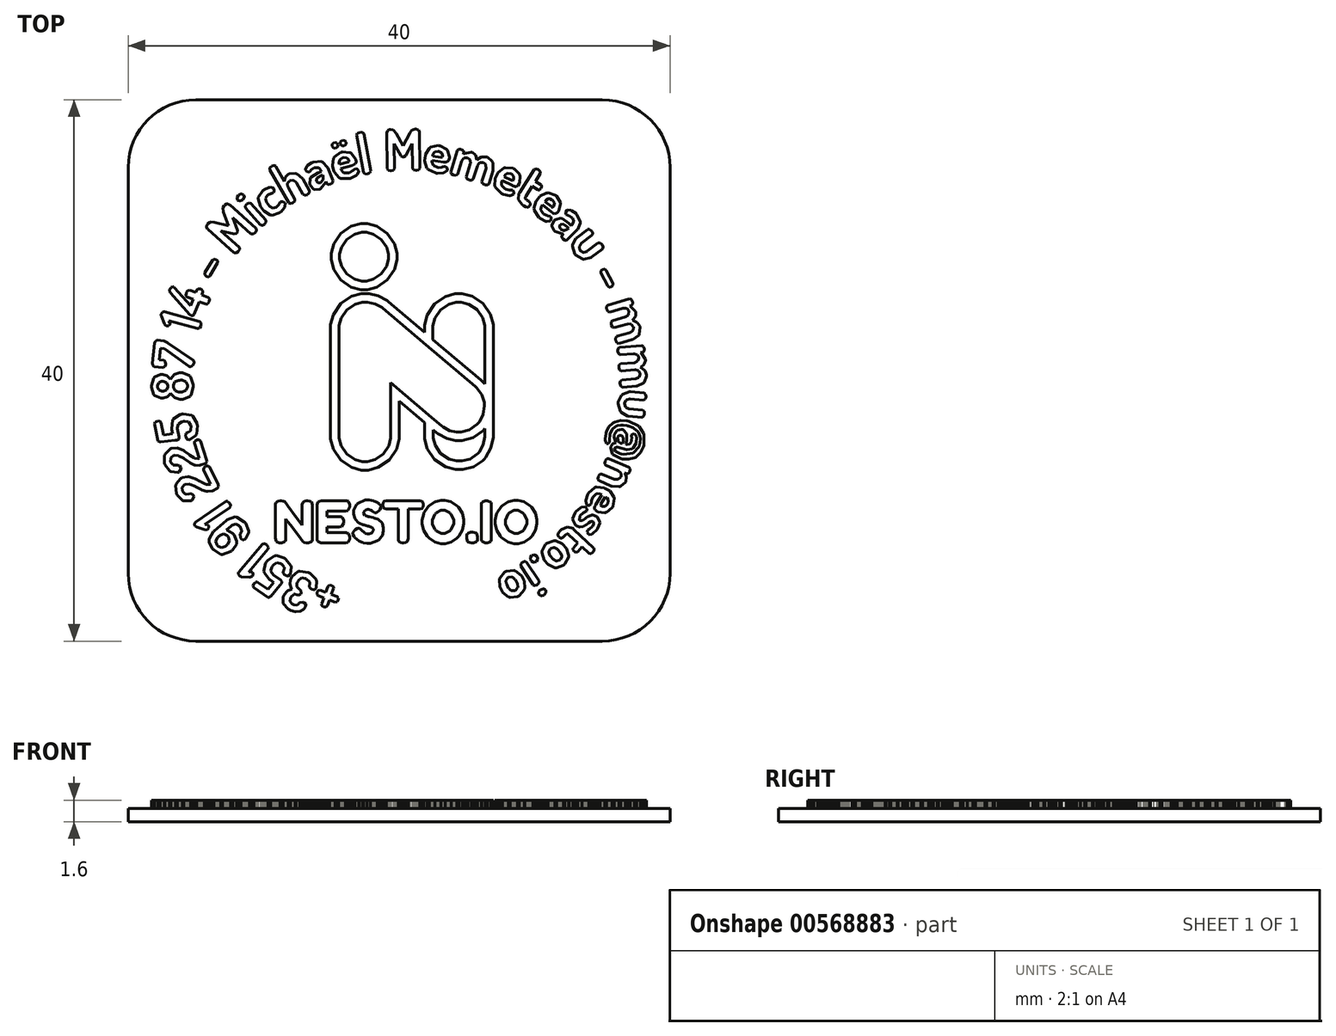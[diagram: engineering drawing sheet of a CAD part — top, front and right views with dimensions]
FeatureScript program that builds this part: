
annotation { "Feature Type Name" : "Feature", "Feature Type Description" : "" }
export const myFeature = defineFeature(function(context is Context, id is Id, definition is map)
    precondition{}
    {
        {
            var Q0;
            Q0=qCreatedBy(makeId("Top.planeOp"),FACE);
            var sketch = newSketch(context, id + "F0", { "sketchPlane" : qUnion([Q0])});
            skLineSegment(sketch, "E0", {"start": v(0.3, -0.3) * mm, "end": v(0.29, -0.31) * mm});
            skLineSegment(sketch, "E1", {"start": v(0.29, -0.31) * mm, "end": v(0.26, -0.33) * mm});
            skLineSegment(sketch, "E2", {"start": v(0.26, -0.33) * mm, "end": v(0.23, -0.33) * mm});
            skLineSegment(sketch, "E3", {"start": v(0.23, -0.33) * mm, "end": v(0.23, -0.33) * mm});
            skLineSegment(sketch, "E4", {"start": v(0.23, -0.33) * mm, "end": v(0.22, -0.33) * mm});
            skLineSegment(sketch, "E5", {"start": v(0.22, -0.33) * mm, "end": v(0.22, -0.33) * mm});
            skLineSegment(sketch, "E6", {"start": v(0.22, -0.33) * mm, "end": v(0.21, -0.33) * mm});
            skLineSegment(sketch, "E7", {"start": v(0.21, -0.33) * mm, "end": v(0.18, -0.33) * mm});
            skLineSegment(sketch, "E8", {"start": v(0.18, -0.33) * mm, "end": v(0.15, -0.3) * mm});
            skLineSegment(sketch, "E9", {"start": v(0.15, -0.3) * mm, "end": v(0.13, -0.28) * mm});
            skLineSegment(sketch, "E10", {"start": v(0.13, -0.28) * mm, "end": v(0.13, -0.25) * mm});
            skLineSegment(sketch, "E11", {"start": v(0.13, -0.25) * mm, "end": v(0.12, -0.24) * mm});
            skLineSegment(sketch, "E12", {"start": v(0.12, -0.24) * mm, "end": v(0.12, -0.22) * mm});
            skLineSegment(sketch, "E13", {"start": v(0.12, -0.22) * mm, "end": v(0.14, -0.23) * mm});
            skLineSegment(sketch, "E14", {"start": v(0.14, -0.23) * mm, "end": v(0.14, -0.23) * mm});
            skLineSegment(sketch, "E15", {"start": v(0.14, -0.23) * mm, "end": v(0.18, -0.25) * mm});
            skLineSegment(sketch, "E16", {"start": v(0.18, -0.25) * mm, "end": v(0.2, -0.26) * mm});
            skLineSegment(sketch, "E17", {"start": v(0.2, -0.26) * mm, "end": v(0.22, -0.26) * mm});
            skLineSegment(sketch, "E18", {"start": v(0.22, -0.26) * mm, "end": v(0.23, -0.26) * mm});
            skLineSegment(sketch, "E19", {"start": v(0.23, -0.26) * mm, "end": v(0.27, -0.25) * mm});
            skLineSegment(sketch, "E20", {"start": v(0.27, -0.25) * mm, "end": v(0.3, -0.22) * mm});
            skLineSegment(sketch, "E21", {"start": v(0.3, -0.22) * mm, "end": v(0.32, -0.22) * mm});
            skLineSegment(sketch, "E22", {"start": v(0.32, -0.22) * mm, "end": v(0.32, -0.24) * mm});
            skLineSegment(sketch, "E23", {"start": v(0.32, -0.24) * mm, "end": v(0.32, -0.24) * mm});
            skLineSegment(sketch, "E24", {"start": v(0.32, -0.24) * mm, "end": v(0.3, -0.28) * mm});
            skLineSegment(sketch, "E25", {"start": v(0.3, -0.28) * mm, "end": v(0.3, -0.3) * mm});
            skLineSegment(sketch, "E26", {"start": v(0.3, -0.3) * mm, "end": v(0.3, -0.3) * mm});
            skLineSegment(sketch, "E27", {"start": v(-0.03, -0.05) * mm, "end": v(-0.03, -0.24) * mm});
            skLineSegment(sketch, "E28", {"start": v(-0.03, -0.24) * mm, "end": v(-0.03, -0.25) * mm});
            skLineSegment(sketch, "E29", {"start": v(-0.03, -0.25) * mm, "end": v(-0.04, -0.28) * mm});
            skLineSegment(sketch, "E30", {"start": v(-0.04, -0.28) * mm, "end": v(-0.06, -0.3) * mm});
            skLineSegment(sketch, "E31", {"start": v(-0.06, -0.3) * mm, "end": v(-0.09, -0.33) * mm});
            skLineSegment(sketch, "E32", {"start": v(-0.09, -0.33) * mm, "end": v(-0.12, -0.34) * mm});
            skLineSegment(sketch, "E33", {"start": v(-0.12, -0.34) * mm, "end": v(-0.13, -0.34) * mm});
            skLineSegment(sketch, "E34", {"start": v(-0.13, -0.34) * mm, "end": v(-0.14, -0.34) * mm});
            skLineSegment(sketch, "E35", {"start": v(-0.14, -0.34) * mm, "end": v(-0.16, -0.33) * mm});
            skLineSegment(sketch, "E36", {"start": v(-0.16, -0.33) * mm, "end": v(-0.2, -0.3) * mm});
            skLineSegment(sketch, "E37", {"start": v(-0.2, -0.3) * mm, "end": v(-0.21, -0.28) * mm});
            skLineSegment(sketch, "E38", {"start": v(-0.21, -0.28) * mm, "end": v(-0.22, -0.25) * mm});
            skLineSegment(sketch, "E39", {"start": v(-0.22, -0.25) * mm, "end": v(-0.22, -0.24) * mm});
            skLineSegment(sketch, "E40", {"start": v(-0.22, -0.24) * mm, "end": v(-0.22, 0.16) * mm});
            skLineSegment(sketch, "E41", {"start": v(-0.22, 0.16) * mm, "end": v(-0.22, 0.17) * mm});
            skLineSegment(sketch, "E42", {"start": v(-0.22, 0.17) * mm, "end": v(-0.21, 0.2) * mm});
            skLineSegment(sketch, "E43", {"start": v(-0.21, 0.2) * mm, "end": v(-0.2, 0.22) * mm});
            skLineSegment(sketch, "E44", {"start": v(-0.2, 0.22) * mm, "end": v(-0.16, 0.24) * mm});
            skLineSegment(sketch, "E45", {"start": v(-0.16, 0.24) * mm, "end": v(-0.14, 0.25) * mm});
            skLineSegment(sketch, "E46", {"start": v(-0.14, 0.25) * mm, "end": v(-0.13, 0.25) * mm});
            skLineSegment(sketch, "E47", {"start": v(-0.13, 0.25) * mm, "end": v(-0.13, 0.25) * mm});
            skLineSegment(sketch, "E48", {"start": v(-0.13, 0.25) * mm, "end": v(-0.12, 0.25) * mm});
            skLineSegment(sketch, "E49", {"start": v(-0.12, 0.25) * mm, "end": v(-0.12, 0.25) * mm});
            skLineSegment(sketch, "E50", {"start": v(-0.12, 0.25) * mm, "end": v(-0.09, 0.25) * mm});
            skLineSegment(sketch, "E51", {"start": v(-0.09, 0.25) * mm, "end": v(-0.06, 0.23) * mm});
            skLineSegment(sketch, "E52", {"start": v(-0.06, 0.23) * mm, "end": v(-0.06, 0.23) * mm});
            skLineSegment(sketch, "E53", {"start": v(-0.06, 0.23) * mm, "end": v(0.1, 0.1) * mm});
            skLineSegment(sketch, "E54", {"start": v(0.1, 0.1) * mm, "end": v(0.1, 0.1) * mm});
            skLineSegment(sketch, "E55", {"start": v(0.1, 0.1) * mm, "end": v(0.28, -0.06) * mm});
            skLineSegment(sketch, "E56", {"start": v(0.28, -0.06) * mm, "end": v(0.29, -0.06) * mm});
            skLineSegment(sketch, "E57", {"start": v(0.29, -0.06) * mm, "end": v(0.3, -0.09) * mm});
            skLineSegment(sketch, "E58", {"start": v(0.3, -0.09) * mm, "end": v(0.31, -0.12) * mm});
            skLineSegment(sketch, "E59", {"start": v(0.31, -0.12) * mm, "end": v(0.31, -0.12) * mm});
            skLineSegment(sketch, "E60", {"start": v(0.31, -0.12) * mm, "end": v(0.32, -0.13) * mm});
            skLineSegment(sketch, "E61", {"start": v(0.32, -0.13) * mm, "end": v(0.31, -0.16) * mm});
            skLineSegment(sketch, "E62", {"start": v(0.31, -0.16) * mm, "end": v(0.3, -0.19) * mm});
            skLineSegment(sketch, "E63", {"start": v(0.3, -0.19) * mm, "end": v(0.3, -0.2) * mm});
            skLineSegment(sketch, "E64", {"start": v(0.3, -0.2) * mm, "end": v(0.29, -0.2) * mm});
            skLineSegment(sketch, "E65", {"start": v(0.29, -0.2) * mm, "end": v(0.26, -0.22) * mm});
            skLineSegment(sketch, "E66", {"start": v(0.26, -0.22) * mm, "end": v(0.23, -0.23) * mm});
            skLineSegment(sketch, "E67", {"start": v(0.23, -0.23) * mm, "end": v(0.22, -0.23) * mm});
            skLineSegment(sketch, "E68", {"start": v(0.22, -0.23) * mm, "end": v(0.21, -0.23) * mm});
            skLineSegment(sketch, "E69", {"start": v(0.21, -0.23) * mm, "end": v(0.19, -0.22) * mm});
            skLineSegment(sketch, "E70", {"start": v(0.19, -0.22) * mm, "end": v(0.16, -0.2) * mm});
            skLineSegment(sketch, "E71", {"start": v(0.16, -0.2) * mm, "end": v(0.16, -0.2) * mm});
            skLineSegment(sketch, "E72", {"start": v(0.16, -0.2) * mm, "end": v(0.12, -0.17) * mm});
            skLineSegment(sketch, "E73", {"start": v(0.12, -0.17) * mm, "end": v(-0.03, -0.05) * mm});
            skLineSegment(sketch, "E74", {"start": v(0.22, 0.25) * mm, "end": v(0.22, 0.25) * mm});
            skLineSegment(sketch, "E75", {"start": v(0.22, 0.25) * mm, "end": v(0.23, 0.25) * mm});
            skLineSegment(sketch, "E76", {"start": v(0.23, 0.25) * mm, "end": v(0.26, 0.24) * mm});
            skLineSegment(sketch, "E77", {"start": v(0.26, 0.24) * mm, "end": v(0.29, 0.22) * mm});
            skLineSegment(sketch, "E78", {"start": v(0.29, 0.22) * mm, "end": v(0.3, 0.2) * mm});
            skLineSegment(sketch, "E79", {"start": v(0.3, 0.2) * mm, "end": v(0.32, 0.17) * mm});
            skLineSegment(sketch, "E80", {"start": v(0.32, 0.17) * mm, "end": v(0.32, 0.16) * mm});
            skLineSegment(sketch, "E81", {"start": v(0.32, 0.16) * mm, "end": v(0.32, -0.05) * mm});
            skLineSegment(sketch, "E82", {"start": v(0.32, -0.05) * mm, "end": v(0.31, -0.05) * mm});
            skLineSegment(sketch, "E83", {"start": v(0.31, -0.05) * mm, "end": v(0.3, -0.04) * mm});
            skLineSegment(sketch, "E84", {"start": v(0.3, -0.04) * mm, "end": v(0.3, -0.04) * mm});
            skLineSegment(sketch, "E85", {"start": v(0.3, -0.04) * mm, "end": v(0.12, 0.11) * mm});
            skLineSegment(sketch, "E86", {"start": v(0.12, 0.11) * mm, "end": v(0.12, 0.16) * mm});
            skLineSegment(sketch, "E87", {"start": v(0.12, 0.16) * mm, "end": v(0.12, 0.16) * mm});
            skLineSegment(sketch, "E88", {"start": v(0.12, 0.16) * mm, "end": v(0.13, 0.2) * mm});
            skLineSegment(sketch, "E89", {"start": v(0.13, 0.2) * mm, "end": v(0.15, 0.22) * mm});
            skLineSegment(sketch, "E90", {"start": v(0.15, 0.22) * mm, "end": v(0.18, 0.24) * mm});
            skLineSegment(sketch, "E91", {"start": v(0.18, 0.24) * mm, "end": v(0.21, 0.25) * mm});
            skLineSegment(sketch, "E92", {"start": v(0.21, 0.25) * mm, "end": v(0.22, 0.25) * mm});
            skLineSegment(sketch, "E93", {"start": v(0.35, 0.16) * mm, "end": v(0.35, 0.17) * mm});
            skLineSegment(sketch, "E94", {"start": v(0.35, 0.17) * mm, "end": v(0.34, 0.2) * mm});
            skLineSegment(sketch, "E95", {"start": v(0.34, 0.2) * mm, "end": v(0.3, 0.25) * mm});
            skLineSegment(sketch, "E96", {"start": v(0.3, 0.25) * mm, "end": v(0.27, 0.27) * mm});
            skLineSegment(sketch, "E97", {"start": v(0.27, 0.27) * mm, "end": v(0.23, 0.28) * mm});
            skLineSegment(sketch, "E98", {"start": v(0.23, 0.28) * mm, "end": v(0.22, 0.28) * mm});
            skLineSegment(sketch, "E99", {"start": v(0.22, 0.28) * mm, "end": v(0.22, 0.28) * mm});
            skLineSegment(sketch, "E100", {"start": v(0.22, 0.28) * mm, "end": v(0.2, 0.28) * mm});
            skLineSegment(sketch, "E101", {"start": v(0.2, 0.28) * mm, "end": v(0.17, 0.27) * mm});
            skLineSegment(sketch, "E102", {"start": v(0.17, 0.27) * mm, "end": v(0.13, 0.25) * mm});
            skLineSegment(sketch, "E103", {"start": v(0.13, 0.25) * mm, "end": v(0.1, 0.2) * mm});
            skLineSegment(sketch, "E104", {"start": v(0.1, 0.2) * mm, "end": v(0.1, 0.17) * mm});
            skLineSegment(sketch, "E105", {"start": v(0.1, 0.17) * mm, "end": v(0.1, 0.16) * mm});
            skLineSegment(sketch, "E106", {"start": v(0.1, 0.16) * mm, "end": v(0.1, 0.14) * mm});
            skLineSegment(sketch, "E107", {"start": v(0.1, 0.14) * mm, "end": v(-0.04, 0.25) * mm});
            skLineSegment(sketch, "E108", {"start": v(-0.04, 0.25) * mm, "end": v(-0.05, 0.26) * mm});
            skLineSegment(sketch, "E109", {"start": v(-0.05, 0.26) * mm, "end": v(-0.08, 0.28) * mm});
            skLineSegment(sketch, "E110", {"start": v(-0.08, 0.28) * mm, "end": v(-0.11, 0.28) * mm});
            skLineSegment(sketch, "E111", {"start": v(-0.11, 0.28) * mm, "end": v(-0.12, 0.28) * mm});
            skLineSegment(sketch, "E112", {"start": v(-0.12, 0.28) * mm, "end": v(-0.12, 0.28) * mm});
            skLineSegment(sketch, "E113", {"start": v(-0.12, 0.28) * mm, "end": v(-0.13, 0.28) * mm});
            skLineSegment(sketch, "E114", {"start": v(-0.13, 0.28) * mm, "end": v(-0.13, 0.28) * mm});
            skLineSegment(sketch, "E115", {"start": v(-0.13, 0.28) * mm, "end": v(-0.14, 0.28) * mm});
            skLineSegment(sketch, "E116", {"start": v(-0.14, 0.28) * mm, "end": v(-0.18, 0.27) * mm});
            skLineSegment(sketch, "E117", {"start": v(-0.18, 0.27) * mm, "end": v(-0.22, 0.25) * mm});
            skLineSegment(sketch, "E118", {"start": v(-0.22, 0.25) * mm, "end": v(-0.24, 0.2) * mm});
            skLineSegment(sketch, "E119", {"start": v(-0.24, 0.2) * mm, "end": v(-0.25, 0.17) * mm});
            skLineSegment(sketch, "E120", {"start": v(-0.25, 0.17) * mm, "end": v(-0.25, 0.16) * mm});
            skLineSegment(sketch, "E121", {"start": v(-0.25, 0.16) * mm, "end": v(-0.25, -0.24) * mm});
            skLineSegment(sketch, "E122", {"start": v(-0.25, -0.24) * mm, "end": v(-0.25, -0.25) * mm});
            skLineSegment(sketch, "E123", {"start": v(-0.25, -0.25) * mm, "end": v(-0.24, -0.3) * mm});
            skLineSegment(sketch, "E124", {"start": v(-0.24, -0.3) * mm, "end": v(-0.22, -0.33) * mm});
            skLineSegment(sketch, "E125", {"start": v(-0.22, -0.33) * mm, "end": v(-0.18, -0.36) * mm});
            skLineSegment(sketch, "E126", {"start": v(-0.18, -0.36) * mm, "end": v(-0.14, -0.37) * mm});
            skLineSegment(sketch, "E127", {"start": v(-0.14, -0.37) * mm, "end": v(-0.13, -0.37) * mm});
            skLineSegment(sketch, "E128", {"start": v(-0.13, -0.37) * mm, "end": v(-0.11, -0.37) * mm});
            skLineSegment(sketch, "E129", {"start": v(-0.11, -0.37) * mm, "end": v(-0.08, -0.36) * mm});
            skLineSegment(sketch, "E130", {"start": v(-0.08, -0.36) * mm, "end": v(-0.04, -0.33) * mm});
            skLineSegment(sketch, "E131", {"start": v(-0.04, -0.33) * mm, "end": v(0, -0.3) * mm});
            skLineSegment(sketch, "E132", {"start": v(0, -0.3) * mm, "end": v(0, -0.25) * mm});
            skLineSegment(sketch, "E133", {"start": v(0, -0.25) * mm, "end": v(0, -0.24) * mm});
            skLineSegment(sketch, "E134", {"start": v(0, -0.24) * mm, "end": v(0, -0.11) * mm});
            skLineSegment(sketch, "E135", {"start": v(0, -0.11) * mm, "end": v(0.1, -0.2) * mm});
            skLineSegment(sketch, "E136", {"start": v(0.1, -0.2) * mm, "end": v(0.1, -0.24) * mm});
            skLineSegment(sketch, "E137", {"start": v(0.1, -0.24) * mm, "end": v(0.1, -0.25) * mm});
            skLineSegment(sketch, "E138", {"start": v(0.1, -0.25) * mm, "end": v(0.1, -0.29) * mm});
            skLineSegment(sketch, "E139", {"start": v(0.1, -0.29) * mm, "end": v(0.13, -0.33) * mm});
            skLineSegment(sketch, "E140", {"start": v(0.13, -0.33) * mm, "end": v(0.17, -0.36) * mm});
            skLineSegment(sketch, "E141", {"start": v(0.17, -0.36) * mm, "end": v(0.2, -0.37) * mm});
            skLineSegment(sketch, "E142", {"start": v(0.2, -0.37) * mm, "end": v(0.22, -0.37) * mm});
            skLineSegment(sketch, "E143", {"start": v(0.22, -0.37) * mm, "end": v(0.23, -0.37) * mm});
            skLineSegment(sketch, "E144", {"start": v(0.23, -0.37) * mm, "end": v(0.23, -0.37) * mm});
            skLineSegment(sketch, "E145", {"start": v(0.23, -0.37) * mm, "end": v(0.27, -0.36) * mm});
            skLineSegment(sketch, "E146", {"start": v(0.27, -0.36) * mm, "end": v(0.3, -0.33) * mm});
            skLineSegment(sketch, "E147", {"start": v(0.3, -0.33) * mm, "end": v(0.31, -0.33) * mm});
            skLineSegment(sketch, "E148", {"start": v(0.31, -0.33) * mm, "end": v(0.32, -0.32) * mm});
            skLineSegment(sketch, "E149", {"start": v(0.32, -0.32) * mm, "end": v(0.34, -0.29) * mm});
            skLineSegment(sketch, "E150", {"start": v(0.34, -0.29) * mm, "end": v(0.35, -0.25) * mm});
            skLineSegment(sketch, "E151", {"start": v(0.35, -0.25) * mm, "end": v(0.35, -0.24) * mm});
            skLineSegment(sketch, "E152", {"start": v(0.35, -0.24) * mm, "end": v(0.35, 0.16) * mm});
            skLineSegment(sketch, "E153", {"start": v(-0.13, 0.51) * mm, "end": v(-0.12, 0.51) * mm});
            skLineSegment(sketch, "E154", {"start": v(-0.12, 0.51) * mm, "end": v(-0.1, 0.5) * mm});
            skLineSegment(sketch, "E155", {"start": v(-0.1, 0.5) * mm, "end": v(-0.07, 0.48) * mm});
            skLineSegment(sketch, "E156", {"start": v(-0.07, 0.48) * mm, "end": v(-0.05, 0.46) * mm});
            skLineSegment(sketch, "E157", {"start": v(-0.05, 0.46) * mm, "end": v(-0.04, 0.43) * mm});
            skLineSegment(sketch, "E158", {"start": v(-0.04, 0.43) * mm, "end": v(-0.04, 0.42) * mm});
            skLineSegment(sketch, "E159", {"start": v(-0.04, 0.42) * mm, "end": v(-0.04, 0.41) * mm});
            skLineSegment(sketch, "E160", {"start": v(-0.04, 0.41) * mm, "end": v(-0.05, 0.39) * mm});
            skLineSegment(sketch, "E161", {"start": v(-0.05, 0.39) * mm, "end": v(-0.07, 0.36) * mm});
            skLineSegment(sketch, "E162", {"start": v(-0.07, 0.36) * mm, "end": v(-0.1, 0.34) * mm});
            skLineSegment(sketch, "E163", {"start": v(-0.1, 0.34) * mm, "end": v(-0.12, 0.33) * mm});
            skLineSegment(sketch, "E164", {"start": v(-0.12, 0.33) * mm, "end": v(-0.13, 0.33) * mm});
            skLineSegment(sketch, "E165", {"start": v(-0.13, 0.33) * mm, "end": v(-0.14, 0.33) * mm});
            skLineSegment(sketch, "E166", {"start": v(-0.14, 0.33) * mm, "end": v(-0.16, 0.34) * mm});
            skLineSegment(sketch, "E167", {"start": v(-0.16, 0.34) * mm, "end": v(-0.2, 0.36) * mm});
            skLineSegment(sketch, "E168", {"start": v(-0.2, 0.36) * mm, "end": v(-0.21, 0.39) * mm});
            skLineSegment(sketch, "E169", {"start": v(-0.21, 0.39) * mm, "end": v(-0.22, 0.41) * mm});
            skLineSegment(sketch, "E170", {"start": v(-0.22, 0.41) * mm, "end": v(-0.22, 0.42) * mm});
            skLineSegment(sketch, "E171", {"start": v(-0.22, 0.42) * mm, "end": v(-0.22, 0.43) * mm});
            skLineSegment(sketch, "E172", {"start": v(-0.22, 0.43) * mm, "end": v(-0.21, 0.46) * mm});
            skLineSegment(sketch, "E173", {"start": v(-0.21, 0.46) * mm, "end": v(-0.2, 0.48) * mm});
            skLineSegment(sketch, "E174", {"start": v(-0.2, 0.48) * mm, "end": v(-0.16, 0.5) * mm});
            skLineSegment(sketch, "E175", {"start": v(-0.16, 0.5) * mm, "end": v(-0.14, 0.51) * mm});
            skLineSegment(sketch, "E176", {"start": v(-0.14, 0.51) * mm, "end": v(-0.13, 0.51) * mm});
            skLineSegment(sketch, "E177", {"start": v(-0.13, 0.3) * mm, "end": v(-0.12, 0.3) * mm});
            skLineSegment(sketch, "E178", {"start": v(-0.12, 0.3) * mm, "end": v(-0.08, 0.3) * mm});
            skLineSegment(sketch, "E179", {"start": v(-0.08, 0.3) * mm, "end": v(-0.04, 0.33) * mm});
            skLineSegment(sketch, "E180", {"start": v(-0.04, 0.33) * mm, "end": v(-0.02, 0.37) * mm});
            skLineSegment(sketch, "E181", {"start": v(-0.02, 0.37) * mm, "end": v(0, 0.4) * mm});
            skLineSegment(sketch, "E182", {"start": v(0, 0.4) * mm, "end": v(0, 0.42) * mm});
            skLineSegment(sketch, "E183", {"start": v(0, 0.42) * mm, "end": v(0, 0.43) * mm});
            skLineSegment(sketch, "E184", {"start": v(0, 0.43) * mm, "end": v(-0.02, 0.47) * mm});
            skLineSegment(sketch, "E185", {"start": v(-0.02, 0.47) * mm, "end": v(-0.04, 0.5) * mm});
            skLineSegment(sketch, "E186", {"start": v(-0.04, 0.5) * mm, "end": v(-0.08, 0.53) * mm});
            skLineSegment(sketch, "E187", {"start": v(-0.08, 0.53) * mm, "end": v(-0.12, 0.54) * mm});
            skLineSegment(sketch, "E188", {"start": v(-0.12, 0.54) * mm, "end": v(-0.13, 0.54) * mm});
            skLineSegment(sketch, "E189", {"start": v(-0.13, 0.54) * mm, "end": v(-0.14, 0.54) * mm});
            skLineSegment(sketch, "E190", {"start": v(-0.14, 0.54) * mm, "end": v(-0.18, 0.53) * mm});
            skLineSegment(sketch, "E191", {"start": v(-0.18, 0.53) * mm, "end": v(-0.22, 0.5) * mm});
            skLineSegment(sketch, "E192", {"start": v(-0.22, 0.5) * mm, "end": v(-0.24, 0.47) * mm});
            skLineSegment(sketch, "E193", {"start": v(-0.24, 0.47) * mm, "end": v(-0.25, 0.43) * mm});
            skLineSegment(sketch, "E194", {"start": v(-0.25, 0.43) * mm, "end": v(-0.25, 0.42) * mm});
            skLineSegment(sketch, "E195", {"start": v(-0.25, 0.42) * mm, "end": v(-0.25, 0.4) * mm});
            skLineSegment(sketch, "E196", {"start": v(-0.25, 0.4) * mm, "end": v(-0.24, 0.37) * mm});
            skLineSegment(sketch, "E197", {"start": v(-0.24, 0.37) * mm, "end": v(-0.22, 0.33) * mm});
            skLineSegment(sketch, "E198", {"start": v(-0.22, 0.33) * mm, "end": v(-0.18, 0.3) * mm});
            skLineSegment(sketch, "E199", {"start": v(-0.18, 0.3) * mm, "end": v(-0.14, 0.3) * mm});
            skLineSegment(sketch, "E200", {"start": v(-0.14, 0.3) * mm, "end": v(-0.13, 0.3) * mm});
            skLineSegment(sketch, "E201", {"start": v(-0.36, -0.49) * mm, "end": v(-0.36, -0.49) * mm});
            skLineSegment(sketch, "E202", {"start": v(-0.36, -0.49) * mm, "end": v(-0.35, -0.48) * mm});
            skLineSegment(sketch, "E203", {"start": v(-0.35, -0.48) * mm, "end": v(-0.35, -0.48) * mm});
            skLineSegment(sketch, "E204", {"start": v(-0.35, -0.48) * mm, "end": v(-0.34, -0.48) * mm});
            skLineSegment(sketch, "E205", {"start": v(-0.34, -0.48) * mm, "end": v(-0.34, -0.48) * mm});
            skLineSegment(sketch, "E206", {"start": v(-0.34, -0.48) * mm, "end": v(-0.33, -0.48) * mm});
            skLineSegment(sketch, "E207", {"start": v(-0.33, -0.48) * mm, "end": v(-0.33, -0.48) * mm});
            skLineSegment(sketch, "E208", {"start": v(-0.33, -0.48) * mm, "end": v(-0.32, -0.48) * mm});
            skLineSegment(sketch, "E209", {"start": v(-0.32, -0.48) * mm, "end": v(-0.32, -0.49) * mm});
            skLineSegment(sketch, "E210", {"start": v(-0.32, -0.49) * mm, "end": v(-0.32, -0.49) * mm});
            skLineSegment(sketch, "E211", {"start": v(-0.32, -0.49) * mm, "end": v(-0.32, -0.5) * mm});
            skLineSegment(sketch, "E212", {"start": v(-0.32, -0.5) * mm, "end": v(-0.32, -0.5) * mm});
            skLineSegment(sketch, "E213", {"start": v(-0.32, -0.5) * mm, "end": v(-0.32, -0.62) * mm});
            skLineSegment(sketch, "E214", {"start": v(-0.32, -0.62) * mm, "end": v(-0.32, -0.62) * mm});
            skLineSegment(sketch, "E215", {"start": v(-0.32, -0.62) * mm, "end": v(-0.32, -0.63) * mm});
            skLineSegment(sketch, "E216", {"start": v(-0.32, -0.63) * mm, "end": v(-0.32, -0.63) * mm});
            skLineSegment(sketch, "E217", {"start": v(-0.32, -0.63) * mm, "end": v(-0.34, -0.64) * mm});
            skLineSegment(sketch, "E218", {"start": v(-0.34, -0.64) * mm, "end": v(-0.34, -0.64) * mm});
            skLineSegment(sketch, "E219", {"start": v(-0.34, -0.64) * mm, "end": v(-0.35, -0.64) * mm});
            skLineSegment(sketch, "E220", {"start": v(-0.35, -0.64) * mm, "end": v(-0.35, -0.64) * mm});
            skLineSegment(sketch, "E221", {"start": v(-0.35, -0.64) * mm, "end": v(-0.36, -0.63) * mm});
            skLineSegment(sketch, "E222", {"start": v(-0.36, -0.63) * mm, "end": v(-0.36, -0.63) * mm});
            skLineSegment(sketch, "E223", {"start": v(-0.36, -0.63) * mm, "end": v(-0.36, -0.62) * mm});
            skLineSegment(sketch, "E224", {"start": v(-0.36, -0.62) * mm, "end": v(-0.4, -0.58) * mm});
            skLineSegment(sketch, "E225", {"start": v(-0.4, -0.58) * mm, "end": v(-0.42, -0.55) * mm});
            skLineSegment(sketch, "E226", {"start": v(-0.42, -0.55) * mm, "end": v(-0.42, -0.55) * mm});
            skLineSegment(sketch, "E227", {"start": v(-0.42, -0.55) * mm, "end": v(-0.42, -0.62) * mm});
            skLineSegment(sketch, "E228", {"start": v(-0.42, -0.62) * mm, "end": v(-0.42, -0.62) * mm});
            skLineSegment(sketch, "E229", {"start": v(-0.42, -0.62) * mm, "end": v(-0.42, -0.63) * mm});
            skLineSegment(sketch, "E230", {"start": v(-0.42, -0.63) * mm, "end": v(-0.42, -0.63) * mm});
            skLineSegment(sketch, "E231", {"start": v(-0.42, -0.63) * mm, "end": v(-0.43, -0.64) * mm});
            skLineSegment(sketch, "E232", {"start": v(-0.43, -0.64) * mm, "end": v(-0.44, -0.64) * mm});
            skLineSegment(sketch, "E233", {"start": v(-0.44, -0.64) * mm, "end": v(-0.44, -0.64) * mm});
            skLineSegment(sketch, "E234", {"start": v(-0.44, -0.64) * mm, "end": v(-0.45, -0.63) * mm});
            skLineSegment(sketch, "E235", {"start": v(-0.45, -0.63) * mm, "end": v(-0.45, -0.63) * mm});
            skLineSegment(sketch, "E236", {"start": v(-0.45, -0.63) * mm, "end": v(-0.46, -0.63) * mm});
            skLineSegment(sketch, "E237", {"start": v(-0.46, -0.63) * mm, "end": v(-0.46, -0.63) * mm});
            skLineSegment(sketch, "E238", {"start": v(-0.46, -0.63) * mm, "end": v(-0.46, -0.62) * mm});
            skLineSegment(sketch, "E239", {"start": v(-0.46, -0.62) * mm, "end": v(-0.46, -0.62) * mm});
            skLineSegment(sketch, "E240", {"start": v(-0.46, -0.62) * mm, "end": v(-0.46, -0.5) * mm});
            skLineSegment(sketch, "E241", {"start": v(-0.46, -0.5) * mm, "end": v(-0.46, -0.5) * mm});
            skLineSegment(sketch, "E242", {"start": v(-0.46, -0.5) * mm, "end": v(-0.45, -0.49) * mm});
            skLineSegment(sketch, "E243", {"start": v(-0.45, -0.49) * mm, "end": v(-0.45, -0.49) * mm});
            skLineSegment(sketch, "E244", {"start": v(-0.45, -0.49) * mm, "end": v(-0.45, -0.48) * mm});
            skLineSegment(sketch, "E245", {"start": v(-0.45, -0.48) * mm, "end": v(-0.45, -0.48) * mm});
            skLineSegment(sketch, "E246", {"start": v(-0.45, -0.48) * mm, "end": v(-0.44, -0.48) * mm});
            skLineSegment(sketch, "E247", {"start": v(-0.44, -0.48) * mm, "end": v(-0.44, -0.48) * mm});
            skLineSegment(sketch, "E248", {"start": v(-0.44, -0.48) * mm, "end": v(-0.43, -0.48) * mm});
            skLineSegment(sketch, "E249", {"start": v(-0.43, -0.48) * mm, "end": v(-0.43, -0.48) * mm});
            skLineSegment(sketch, "E250", {"start": v(-0.43, -0.48) * mm, "end": v(-0.42, -0.48) * mm});
            skLineSegment(sketch, "E251", {"start": v(-0.42, -0.48) * mm, "end": v(-0.42, -0.49) * mm});
            skLineSegment(sketch, "E252", {"start": v(-0.42, -0.49) * mm, "end": v(-0.42, -0.49) * mm});
            skLineSegment(sketch, "E253", {"start": v(-0.42, -0.49) * mm, "end": v(-0.42, -0.5) * mm});
            skLineSegment(sketch, "E254", {"start": v(-0.42, -0.5) * mm, "end": v(-0.41, -0.5) * mm});
            skLineSegment(sketch, "E255", {"start": v(-0.41, -0.5) * mm, "end": v(-0.38, -0.54) * mm});
            skLineSegment(sketch, "E256", {"start": v(-0.38, -0.54) * mm, "end": v(-0.36, -0.57) * mm});
            skLineSegment(sketch, "E257", {"start": v(-0.36, -0.57) * mm, "end": v(-0.36, -0.57) * mm});
            skLineSegment(sketch, "E258", {"start": v(-0.36, -0.57) * mm, "end": v(-0.36, -0.5) * mm});
            skLineSegment(sketch, "E259", {"start": v(-0.36, -0.5) * mm, "end": v(-0.36, -0.5) * mm});
            skLineSegment(sketch, "E260", {"start": v(-0.36, -0.5) * mm, "end": v(-0.36, -0.49) * mm});
            skLineSegment(sketch, "E261", {"start": v(-0.27, -0.6) * mm, "end": v(-0.2, -0.6) * mm});
            skLineSegment(sketch, "E262", {"start": v(-0.2, -0.6) * mm, "end": v(-0.2, -0.6) * mm});
            skLineSegment(sketch, "E263", {"start": v(-0.2, -0.6) * mm, "end": v(-0.19, -0.6) * mm});
            skLineSegment(sketch, "E264", {"start": v(-0.19, -0.6) * mm, "end": v(-0.19, -0.6) * mm});
            skLineSegment(sketch, "E265", {"start": v(-0.19, -0.6) * mm, "end": v(-0.18, -0.61) * mm});
            skLineSegment(sketch, "E266", {"start": v(-0.18, -0.61) * mm, "end": v(-0.18, -0.62) * mm});
            skLineSegment(sketch, "E267", {"start": v(-0.18, -0.62) * mm, "end": v(-0.18, -0.62) * mm});
            skLineSegment(sketch, "E268", {"start": v(-0.18, -0.62) * mm, "end": v(-0.19, -0.64) * mm});
            skLineSegment(sketch, "E269", {"start": v(-0.19, -0.64) * mm, "end": v(-0.19, -0.64) * mm});
            skLineSegment(sketch, "E270", {"start": v(-0.19, -0.64) * mm, "end": v(-0.2, -0.64) * mm});
            skLineSegment(sketch, "E271", {"start": v(-0.2, -0.64) * mm, "end": v(-0.2, -0.64) * mm});
            skLineSegment(sketch, "E272", {"start": v(-0.2, -0.64) * mm, "end": v(-0.28, -0.64) * mm});
            skLineSegment(sketch, "E273", {"start": v(-0.28, -0.64) * mm, "end": v(-0.29, -0.64) * mm});
            skLineSegment(sketch, "E274", {"start": v(-0.29, -0.64) * mm, "end": v(-0.3, -0.63) * mm});
            skLineSegment(sketch, "E275", {"start": v(-0.3, -0.63) * mm, "end": v(-0.3, -0.63) * mm});
            skLineSegment(sketch, "E276", {"start": v(-0.3, -0.63) * mm, "end": v(-0.3, -0.62) * mm});
            skLineSegment(sketch, "E277", {"start": v(-0.3, -0.62) * mm, "end": v(-0.3, -0.62) * mm});
            skLineSegment(sketch, "E278", {"start": v(-0.3, -0.62) * mm, "end": v(-0.3, -0.5) * mm});
            skLineSegment(sketch, "E279", {"start": v(-0.3, -0.5) * mm, "end": v(-0.3, -0.5) * mm});
            skLineSegment(sketch, "E280", {"start": v(-0.3, -0.5) * mm, "end": v(-0.3, -0.49) * mm});
            skLineSegment(sketch, "E281", {"start": v(-0.3, -0.49) * mm, "end": v(-0.3, -0.49) * mm});
            skLineSegment(sketch, "E282", {"start": v(-0.3, -0.49) * mm, "end": v(-0.3, -0.48) * mm});
            skLineSegment(sketch, "E283", {"start": v(-0.3, -0.48) * mm, "end": v(-0.29, -0.48) * mm});
            skLineSegment(sketch, "E284", {"start": v(-0.29, -0.48) * mm, "end": v(-0.28, -0.48) * mm});
            skLineSegment(sketch, "E285", {"start": v(-0.28, -0.48) * mm, "end": v(-0.2, -0.48) * mm});
            skLineSegment(sketch, "E286", {"start": v(-0.2, -0.48) * mm, "end": v(-0.2, -0.48) * mm});
            skLineSegment(sketch, "E287", {"start": v(-0.2, -0.48) * mm, "end": v(-0.19, -0.48) * mm});
            skLineSegment(sketch, "E288", {"start": v(-0.19, -0.48) * mm, "end": v(-0.19, -0.48) * mm});
            skLineSegment(sketch, "E289", {"start": v(-0.19, -0.48) * mm, "end": v(-0.18, -0.5) * mm});
            skLineSegment(sketch, "E290", {"start": v(-0.18, -0.5) * mm, "end": v(-0.18, -0.5) * mm});
            skLineSegment(sketch, "E291", {"start": v(-0.18, -0.5) * mm, "end": v(-0.19, -0.52) * mm});
            skLineSegment(sketch, "E292", {"start": v(-0.19, -0.52) * mm, "end": v(-0.19, -0.52) * mm});
            skLineSegment(sketch, "E293", {"start": v(-0.19, -0.52) * mm, "end": v(-0.2, -0.52) * mm});
            skLineSegment(sketch, "E294", {"start": v(-0.2, -0.52) * mm, "end": v(-0.2, -0.52) * mm});
            skLineSegment(sketch, "E295", {"start": v(-0.2, -0.52) * mm, "end": v(-0.27, -0.52) * mm});
            skLineSegment(sketch, "E296", {"start": v(-0.27, -0.52) * mm, "end": v(-0.27, -0.54) * mm});
            skLineSegment(sketch, "E297", {"start": v(-0.27, -0.54) * mm, "end": v(-0.22, -0.54) * mm});
            skLineSegment(sketch, "E298", {"start": v(-0.22, -0.54) * mm, "end": v(-0.22, -0.54) * mm});
            skLineSegment(sketch, "E299", {"start": v(-0.22, -0.54) * mm, "end": v(-0.21, -0.54) * mm});
            skLineSegment(sketch, "E300", {"start": v(-0.21, -0.54) * mm, "end": v(-0.21, -0.54) * mm});
            skLineSegment(sketch, "E301", {"start": v(-0.21, -0.54) * mm, "end": v(-0.2, -0.54) * mm});
            skLineSegment(sketch, "E302", {"start": v(-0.2, -0.54) * mm, "end": v(-0.2, -0.56) * mm});
            skLineSegment(sketch, "E303", {"start": v(-0.2, -0.56) * mm, "end": v(-0.2, -0.56) * mm});
            skLineSegment(sketch, "E304", {"start": v(-0.2, -0.56) * mm, "end": v(-0.21, -0.58) * mm});
            skLineSegment(sketch, "E305", {"start": v(-0.21, -0.58) * mm, "end": v(-0.21, -0.58) * mm});
            skLineSegment(sketch, "E306", {"start": v(-0.21, -0.58) * mm, "end": v(-0.22, -0.58) * mm});
            skLineSegment(sketch, "E307", {"start": v(-0.22, -0.58) * mm, "end": v(-0.22, -0.58) * mm});
            skLineSegment(sketch, "E308", {"start": v(-0.22, -0.58) * mm, "end": v(-0.27, -0.58) * mm});
            skLineSegment(sketch, "E309", {"start": v(-0.27, -0.58) * mm, "end": v(-0.27, -0.6) * mm});
            skLineSegment(sketch, "E310", {"start": v(-0.17, -0.62) * mm, "end": v(-0.17, -0.61) * mm});
            skLineSegment(sketch, "E311", {"start": v(-0.17, -0.61) * mm, "end": v(-0.17, -0.6) * mm});
            skLineSegment(sketch, "E312", {"start": v(-0.17, -0.6) * mm, "end": v(-0.17, -0.6) * mm});
            skLineSegment(sketch, "E313", {"start": v(-0.17, -0.6) * mm, "end": v(-0.16, -0.59) * mm});
            skLineSegment(sketch, "E314", {"start": v(-0.16, -0.59) * mm, "end": v(-0.16, -0.59) * mm});
            skLineSegment(sketch, "E315", {"start": v(-0.16, -0.59) * mm, "end": v(-0.15, -0.58) * mm});
            skLineSegment(sketch, "E316", {"start": v(-0.15, -0.58) * mm, "end": v(-0.15, -0.58) * mm});
            skLineSegment(sketch, "E317", {"start": v(-0.15, -0.58) * mm, "end": v(-0.14, -0.6) * mm});
            skLineSegment(sketch, "E318", {"start": v(-0.14, -0.6) * mm, "end": v(-0.13, -0.6) * mm});
            skLineSegment(sketch, "E319", {"start": v(-0.13, -0.6) * mm, "end": v(-0.13, -0.6) * mm});
            skLineSegment(sketch, "E320", {"start": v(-0.13, -0.6) * mm, "end": v(-0.12, -0.6) * mm});
            skLineSegment(sketch, "E321", {"start": v(-0.12, -0.6) * mm, "end": v(-0.12, -0.6) * mm});
            skLineSegment(sketch, "E322", {"start": v(-0.12, -0.6) * mm, "end": v(-0.11, -0.6) * mm});
            skLineSegment(sketch, "E323", {"start": v(-0.11, -0.6) * mm, "end": v(-0.1, -0.6) * mm});
            skLineSegment(sketch, "E324", {"start": v(-0.1, -0.6) * mm, "end": v(-0.1, -0.6) * mm});
            skLineSegment(sketch, "E325", {"start": v(-0.1, -0.6) * mm, "end": v(-0.1, -0.59) * mm});
            skLineSegment(sketch, "E326", {"start": v(-0.1, -0.59) * mm, "end": v(-0.1, -0.59) * mm});
            skLineSegment(sketch, "E327", {"start": v(-0.1, -0.59) * mm, "end": v(-0.1, -0.58) * mm});
            skLineSegment(sketch, "E328", {"start": v(-0.1, -0.58) * mm, "end": v(-0.1, -0.58) * mm});
            skLineSegment(sketch, "E329", {"start": v(-0.1, -0.58) * mm, "end": v(-0.11, -0.58) * mm});
            skLineSegment(sketch, "E330", {"start": v(-0.11, -0.58) * mm, "end": v(-0.11, -0.58) * mm});
            skLineSegment(sketch, "E331", {"start": v(-0.11, -0.58) * mm, "end": v(-0.12, -0.57) * mm});
            skLineSegment(sketch, "E332", {"start": v(-0.12, -0.57) * mm, "end": v(-0.13, -0.57) * mm});
            skLineSegment(sketch, "E333", {"start": v(-0.13, -0.57) * mm, "end": v(-0.13, -0.57) * mm});
            skLineSegment(sketch, "E334", {"start": v(-0.13, -0.57) * mm, "end": v(-0.15, -0.56) * mm});
            skLineSegment(sketch, "E335", {"start": v(-0.15, -0.56) * mm, "end": v(-0.15, -0.56) * mm});
            skLineSegment(sketch, "E336", {"start": v(-0.15, -0.56) * mm, "end": v(-0.16, -0.55) * mm});
            skLineSegment(sketch, "E337", {"start": v(-0.16, -0.55) * mm, "end": v(-0.16, -0.55) * mm});
            skLineSegment(sketch, "E338", {"start": v(-0.16, -0.55) * mm, "end": v(-0.17, -0.53) * mm});
            skLineSegment(sketch, "E339", {"start": v(-0.17, -0.53) * mm, "end": v(-0.17, -0.53) * mm});
            skLineSegment(sketch, "E340", {"start": v(-0.17, -0.53) * mm, "end": v(-0.17, -0.52) * mm});
            skLineSegment(sketch, "E341", {"start": v(-0.17, -0.52) * mm, "end": v(-0.16, -0.5) * mm});
            skLineSegment(sketch, "E342", {"start": v(-0.16, -0.5) * mm, "end": v(-0.15, -0.5) * mm});
            skLineSegment(sketch, "E343", {"start": v(-0.15, -0.5) * mm, "end": v(-0.15, -0.5) * mm});
            skLineSegment(sketch, "E344", {"start": v(-0.15, -0.5) * mm, "end": v(-0.13, -0.48) * mm});
            skLineSegment(sketch, "E345", {"start": v(-0.13, -0.48) * mm, "end": v(-0.12, -0.48) * mm});
            skLineSegment(sketch, "E346", {"start": v(-0.12, -0.48) * mm, "end": v(-0.11, -0.48) * mm});
            skLineSegment(sketch, "E347", {"start": v(-0.11, -0.48) * mm, "end": v(-0.1, -0.48) * mm});
            skLineSegment(sketch, "E348", {"start": v(-0.1, -0.48) * mm, "end": v(-0.1, -0.48) * mm});
            skLineSegment(sketch, "E349", {"start": v(-0.1, -0.48) * mm, "end": v(-0.08, -0.49) * mm});
            skLineSegment(sketch, "E350", {"start": v(-0.08, -0.49) * mm, "end": v(-0.08, -0.49) * mm});
            skLineSegment(sketch, "E351", {"start": v(-0.08, -0.49) * mm, "end": v(-0.07, -0.5) * mm});
            skLineSegment(sketch, "E352", {"start": v(-0.07, -0.5) * mm, "end": v(-0.07, -0.5) * mm});
            skLineSegment(sketch, "E353", {"start": v(-0.07, -0.5) * mm, "end": v(-0.07, -0.51) * mm});
            skLineSegment(sketch, "E354", {"start": v(-0.07, -0.51) * mm, "end": v(-0.07, -0.51) * mm});
            skLineSegment(sketch, "E355", {"start": v(-0.07, -0.51) * mm, "end": v(-0.07, -0.52) * mm});
            skLineSegment(sketch, "E356", {"start": v(-0.07, -0.52) * mm, "end": v(-0.08, -0.53) * mm});
            skLineSegment(sketch, "E357", {"start": v(-0.08, -0.53) * mm, "end": v(-0.09, -0.53) * mm});
            skLineSegment(sketch, "E358", {"start": v(-0.09, -0.53) * mm, "end": v(-0.09, -0.53) * mm});
            skLineSegment(sketch, "E359", {"start": v(-0.09, -0.53) * mm, "end": v(-0.1, -0.52) * mm});
            skLineSegment(sketch, "E360", {"start": v(-0.1, -0.52) * mm, "end": v(-0.1, -0.52) * mm});
            skLineSegment(sketch, "E361", {"start": v(-0.1, -0.52) * mm, "end": v(-0.11, -0.51) * mm});
            skLineSegment(sketch, "E362", {"start": v(-0.11, -0.51) * mm, "end": v(-0.11, -0.51) * mm});
            skLineSegment(sketch, "E363", {"start": v(-0.11, -0.51) * mm, "end": v(-0.12, -0.51) * mm});
            skLineSegment(sketch, "E364", {"start": v(-0.12, -0.51) * mm, "end": v(-0.13, -0.52) * mm});
            skLineSegment(sketch, "E365", {"start": v(-0.13, -0.52) * mm, "end": v(-0.13, -0.52) * mm});
            skLineSegment(sketch, "E366", {"start": v(-0.13, -0.52) * mm, "end": v(-0.13, -0.53) * mm});
            skLineSegment(sketch, "E367", {"start": v(-0.13, -0.53) * mm, "end": v(-0.13, -0.53) * mm});
            skLineSegment(sketch, "E368", {"start": v(-0.13, -0.53) * mm, "end": v(-0.13, -0.54) * mm});
            skLineSegment(sketch, "E369", {"start": v(-0.13, -0.54) * mm, "end": v(-0.12, -0.54) * mm});
            skLineSegment(sketch, "E370", {"start": v(-0.12, -0.54) * mm, "end": v(-0.11, -0.54) * mm});
            skLineSegment(sketch, "E371", {"start": v(-0.11, -0.54) * mm, "end": v(-0.11, -0.54) * mm});
            skLineSegment(sketch, "E372", {"start": v(-0.11, -0.54) * mm, "end": v(-0.1, -0.54) * mm});
            skLineSegment(sketch, "E373", {"start": v(-0.1, -0.54) * mm, "end": v(-0.1, -0.54) * mm});
            skLineSegment(sketch, "E374", {"start": v(-0.1, -0.54) * mm, "end": v(-0.08, -0.55) * mm});
            skLineSegment(sketch, "E375", {"start": v(-0.08, -0.55) * mm, "end": v(-0.08, -0.55) * mm});
            skLineSegment(sketch, "E376", {"start": v(-0.08, -0.55) * mm, "end": v(-0.06, -0.56) * mm});
            skLineSegment(sketch, "E377", {"start": v(-0.06, -0.56) * mm, "end": v(-0.06, -0.56) * mm});
            skLineSegment(sketch, "E378", {"start": v(-0.06, -0.56) * mm, "end": v(-0.06, -0.57) * mm});
            skLineSegment(sketch, "E379", {"start": v(-0.06, -0.57) * mm, "end": v(-0.06, -0.58) * mm});
            skLineSegment(sketch, "E380", {"start": v(-0.06, -0.58) * mm, "end": v(-0.06, -0.59) * mm});
            skLineSegment(sketch, "E381", {"start": v(-0.06, -0.59) * mm, "end": v(-0.06, -0.6) * mm});
            skLineSegment(sketch, "E382", {"start": v(-0.06, -0.6) * mm, "end": v(-0.06, -0.6) * mm});
            skLineSegment(sketch, "E383", {"start": v(-0.06, -0.6) * mm, "end": v(-0.06, -0.61) * mm});
            skLineSegment(sketch, "E384", {"start": v(-0.06, -0.61) * mm, "end": v(-0.06, -0.61) * mm});
            skLineSegment(sketch, "E385", {"start": v(-0.06, -0.61) * mm, "end": v(-0.08, -0.63) * mm});
            skLineSegment(sketch, "E386", {"start": v(-0.08, -0.63) * mm, "end": v(-0.08, -0.63) * mm});
            skLineSegment(sketch, "E387", {"start": v(-0.08, -0.63) * mm, "end": v(-0.1, -0.64) * mm});
            skLineSegment(sketch, "E388", {"start": v(-0.1, -0.64) * mm, "end": v(-0.11, -0.64) * mm});
            skLineSegment(sketch, "E389", {"start": v(-0.11, -0.64) * mm, "end": v(-0.12, -0.64) * mm});
            skLineSegment(sketch, "E390", {"start": v(-0.12, -0.64) * mm, "end": v(-0.13, -0.64) * mm});
            skLineSegment(sketch, "E391", {"start": v(-0.13, -0.64) * mm, "end": v(-0.13, -0.64) * mm});
            skLineSegment(sketch, "E392", {"start": v(-0.13, -0.64) * mm, "end": v(-0.15, -0.63) * mm});
            skLineSegment(sketch, "E393", {"start": v(-0.15, -0.63) * mm, "end": v(-0.15, -0.63) * mm});
            skLineSegment(sketch, "E394", {"start": v(-0.15, -0.63) * mm, "end": v(-0.16, -0.62) * mm});
            skLineSegment(sketch, "E395", {"start": v(-0.16, -0.62) * mm, "end": v(-0.16, -0.62) * mm});
            skLineSegment(sketch, "E396", {"start": v(-0.16, -0.62) * mm, "end": v(-0.17, -0.62) * mm});
            skLineSegment(sketch, "E397", {"start": v(-0.04, -0.48) * mm, "end": v(0.07, -0.48) * mm});
            skLineSegment(sketch, "E398", {"start": v(0.07, -0.48) * mm, "end": v(0.08, -0.48) * mm});
            skLineSegment(sketch, "E399", {"start": v(0.08, -0.48) * mm, "end": v(0.08, -0.48) * mm});
            skLineSegment(sketch, "E400", {"start": v(0.08, -0.48) * mm, "end": v(0.09, -0.49) * mm});
            skLineSegment(sketch, "E401", {"start": v(0.09, -0.49) * mm, "end": v(0.09, -0.49) * mm});
            skLineSegment(sketch, "E402", {"start": v(0.09, -0.49) * mm, "end": v(0.09, -0.5) * mm});
            skLineSegment(sketch, "E403", {"start": v(0.09, -0.5) * mm, "end": v(0.09, -0.5) * mm});
            skLineSegment(sketch, "E404", {"start": v(0.09, -0.5) * mm, "end": v(0.08, -0.5) * mm});
            skLineSegment(sketch, "E405", {"start": v(0.08, -0.5) * mm, "end": v(0.08, -0.5) * mm});
            skLineSegment(sketch, "E406", {"start": v(0.08, -0.5) * mm, "end": v(0.08, -0.51) * mm});
            skLineSegment(sketch, "E407", {"start": v(0.08, -0.51) * mm, "end": v(0.08, -0.51) * mm});
            skLineSegment(sketch, "E408", {"start": v(0.08, -0.51) * mm, "end": v(0.07, -0.51) * mm});
            skLineSegment(sketch, "E409", {"start": v(0.07, -0.51) * mm, "end": v(0.03, -0.51) * mm});
            skLineSegment(sketch, "E410", {"start": v(0.03, -0.51) * mm, "end": v(0.03, -0.62) * mm});
            skLineSegment(sketch, "E411", {"start": v(0.03, -0.62) * mm, "end": v(0.03, -0.62) * mm});
            skLineSegment(sketch, "E412", {"start": v(0.03, -0.62) * mm, "end": v(0.03, -0.63) * mm});
            skLineSegment(sketch, "E413", {"start": v(0.03, -0.63) * mm, "end": v(0.03, -0.63) * mm});
            skLineSegment(sketch, "E414", {"start": v(0.03, -0.63) * mm, "end": v(0.03, -0.64) * mm});
            skLineSegment(sketch, "E415", {"start": v(0.03, -0.64) * mm, "end": v(0.03, -0.64) * mm});
            skLineSegment(sketch, "E416", {"start": v(0.03, -0.64) * mm, "end": v(0.02, -0.64) * mm});
            skLineSegment(sketch, "E417", {"start": v(0.02, -0.64) * mm, "end": v(0.02, -0.64) * mm});
            skLineSegment(sketch, "E418", {"start": v(0.02, -0.64) * mm, "end": v(0.01, -0.64) * mm});
            skLineSegment(sketch, "E419", {"start": v(0.01, -0.64) * mm, "end": v(0.01, -0.64) * mm});
            skLineSegment(sketch, "E420", {"start": v(0.01, -0.64) * mm, "end": v(0, -0.64) * mm});
            skLineSegment(sketch, "E421", {"start": v(0, -0.64) * mm, "end": v(0, -0.64) * mm});
            skLineSegment(sketch, "E422", {"start": v(0, -0.64) * mm, "end": v(0, -0.63) * mm});
            skLineSegment(sketch, "E423", {"start": v(0, -0.63) * mm, "end": v(0, -0.63) * mm});
            skLineSegment(sketch, "E424", {"start": v(0, -0.63) * mm, "end": v(0, -0.62) * mm});
            skLineSegment(sketch, "E425", {"start": v(0, -0.62) * mm, "end": v(0, -0.62) * mm});
            skLineSegment(sketch, "E426", {"start": v(0, -0.62) * mm, "end": v(0, -0.51) * mm});
            skLineSegment(sketch, "E427", {"start": v(0, -0.51) * mm, "end": v(-0.04, -0.51) * mm});
            skLineSegment(sketch, "E428", {"start": v(-0.04, -0.51) * mm, "end": v(-0.05, -0.51) * mm});
            skLineSegment(sketch, "E429", {"start": v(-0.05, -0.51) * mm, "end": v(-0.05, -0.51) * mm});
            skLineSegment(sketch, "E430", {"start": v(-0.05, -0.51) * mm, "end": v(-0.06, -0.51) * mm});
            skLineSegment(sketch, "E431", {"start": v(-0.06, -0.51) * mm, "end": v(-0.06, -0.5) * mm});
            skLineSegment(sketch, "E432", {"start": v(-0.06, -0.5) * mm, "end": v(-0.06, -0.5) * mm});
            skLineSegment(sketch, "E433", {"start": v(-0.06, -0.5) * mm, "end": v(-0.06, -0.49) * mm});
            skLineSegment(sketch, "E434", {"start": v(-0.06, -0.49) * mm, "end": v(-0.06, -0.49) * mm});
            skLineSegment(sketch, "E435", {"start": v(-0.06, -0.49) * mm, "end": v(-0.06, -0.48) * mm});
            skLineSegment(sketch, "E436", {"start": v(-0.06, -0.48) * mm, "end": v(-0.06, -0.48) * mm});
            skLineSegment(sketch, "E437", {"start": v(-0.06, -0.48) * mm, "end": v(-0.05, -0.48) * mm});
            skLineSegment(sketch, "E438", {"start": v(-0.05, -0.48) * mm, "end": v(-0.05, -0.48) * mm});
            skLineSegment(sketch, "E439", {"start": v(-0.05, -0.48) * mm, "end": v(-0.04, -0.48) * mm});
            skLineSegment(sketch, "E440", {"start": v(0.12, -0.56) * mm, "end": v(0.12, -0.57) * mm});
            skLineSegment(sketch, "E441", {"start": v(0.12, -0.57) * mm, "end": v(0.13, -0.59) * mm});
            skLineSegment(sketch, "E442", {"start": v(0.13, -0.59) * mm, "end": v(0.13, -0.6) * mm});
            skLineSegment(sketch, "E443", {"start": v(0.13, -0.6) * mm, "end": v(0.14, -0.6) * mm});
            skLineSegment(sketch, "E444", {"start": v(0.14, -0.6) * mm, "end": v(0.16, -0.6) * mm});
            skLineSegment(sketch, "E445", {"start": v(0.16, -0.6) * mm, "end": v(0.16, -0.6) * mm});
            skLineSegment(sketch, "E446", {"start": v(0.16, -0.6) * mm, "end": v(0.17, -0.6) * mm});
            skLineSegment(sketch, "E447", {"start": v(0.17, -0.6) * mm, "end": v(0.19, -0.6) * mm});
            skLineSegment(sketch, "E448", {"start": v(0.19, -0.6) * mm, "end": v(0.19, -0.6) * mm});
            skLineSegment(sketch, "E449", {"start": v(0.19, -0.6) * mm, "end": v(0.2, -0.59) * mm});
            skLineSegment(sketch, "E450", {"start": v(0.2, -0.59) * mm, "end": v(0.2, -0.57) * mm});
            skLineSegment(sketch, "E451", {"start": v(0.2, -0.57) * mm, "end": v(0.2, -0.56) * mm});
            skLineSegment(sketch, "E452", {"start": v(0.2, -0.56) * mm, "end": v(0.2, -0.55) * mm});
            skLineSegment(sketch, "E453", {"start": v(0.2, -0.55) * mm, "end": v(0.2, -0.53) * mm});
            skLineSegment(sketch, "E454", {"start": v(0.2, -0.53) * mm, "end": v(0.19, -0.53) * mm});
            skLineSegment(sketch, "E455", {"start": v(0.19, -0.53) * mm, "end": v(0.19, -0.53) * mm});
            skLineSegment(sketch, "E456", {"start": v(0.19, -0.53) * mm, "end": v(0.17, -0.52) * mm});
            skLineSegment(sketch, "E457", {"start": v(0.17, -0.52) * mm, "end": v(0.16, -0.52) * mm});
            skLineSegment(sketch, "E458", {"start": v(0.16, -0.52) * mm, "end": v(0.15, -0.52) * mm});
            skLineSegment(sketch, "E459", {"start": v(0.15, -0.52) * mm, "end": v(0.14, -0.53) * mm});
            skLineSegment(sketch, "E460", {"start": v(0.14, -0.53) * mm, "end": v(0.13, -0.53) * mm});
            skLineSegment(sketch, "E461", {"start": v(0.13, -0.53) * mm, "end": v(0.13, -0.53) * mm});
            skLineSegment(sketch, "E462", {"start": v(0.13, -0.53) * mm, "end": v(0.12, -0.55) * mm});
            skLineSegment(sketch, "E463", {"start": v(0.12, -0.55) * mm, "end": v(0.12, -0.56) * mm});
            skLineSegment(sketch, "E464", {"start": v(0.16, -0.48) * mm, "end": v(0.17, -0.48) * mm});
            skLineSegment(sketch, "E465", {"start": v(0.17, -0.48) * mm, "end": v(0.2, -0.48) * mm});
            skLineSegment(sketch, "E466", {"start": v(0.2, -0.48) * mm, "end": v(0.21, -0.5) * mm});
            skLineSegment(sketch, "E467", {"start": v(0.21, -0.5) * mm, "end": v(0.22, -0.5) * mm});
            skLineSegment(sketch, "E468", {"start": v(0.22, -0.5) * mm, "end": v(0.22, -0.5) * mm});
            skLineSegment(sketch, "E469", {"start": v(0.22, -0.5) * mm, "end": v(0.23, -0.53) * mm});
            skLineSegment(sketch, "E470", {"start": v(0.23, -0.53) * mm, "end": v(0.24, -0.55) * mm});
            skLineSegment(sketch, "E471", {"start": v(0.24, -0.55) * mm, "end": v(0.24, -0.56) * mm});
            skLineSegment(sketch, "E472", {"start": v(0.24, -0.56) * mm, "end": v(0.24, -0.57) * mm});
            skLineSegment(sketch, "E473", {"start": v(0.24, -0.57) * mm, "end": v(0.23, -0.59) * mm});
            skLineSegment(sketch, "E474", {"start": v(0.23, -0.59) * mm, "end": v(0.22, -0.61) * mm});
            skLineSegment(sketch, "E475", {"start": v(0.22, -0.61) * mm, "end": v(0.22, -0.62) * mm});
            skLineSegment(sketch, "E476", {"start": v(0.22, -0.62) * mm, "end": v(0.21, -0.62) * mm});
            skLineSegment(sketch, "E477", {"start": v(0.21, -0.62) * mm, "end": v(0.2, -0.63) * mm});
            skLineSegment(sketch, "E478", {"start": v(0.2, -0.63) * mm, "end": v(0.17, -0.64) * mm});
            skLineSegment(sketch, "E479", {"start": v(0.17, -0.64) * mm, "end": v(0.16, -0.64) * mm});
            skLineSegment(sketch, "E480", {"start": v(0.16, -0.64) * mm, "end": v(0.15, -0.64) * mm});
            skLineSegment(sketch, "E481", {"start": v(0.15, -0.64) * mm, "end": v(0.13, -0.63) * mm});
            skLineSegment(sketch, "E482", {"start": v(0.13, -0.63) * mm, "end": v(0.11, -0.62) * mm});
            skLineSegment(sketch, "E483", {"start": v(0.11, -0.62) * mm, "end": v(0.1, -0.62) * mm});
            skLineSegment(sketch, "E484", {"start": v(0.1, -0.62) * mm, "end": v(0.1, -0.61) * mm});
            skLineSegment(sketch, "E485", {"start": v(0.1, -0.61) * mm, "end": v(0.1, -0.6) * mm});
            skLineSegment(sketch, "E486", {"start": v(0.1, -0.6) * mm, "end": v(0.08, -0.57) * mm});
            skLineSegment(sketch, "E487", {"start": v(0.08, -0.57) * mm, "end": v(0.08, -0.56) * mm});
            skLineSegment(sketch, "E488", {"start": v(0.08, -0.56) * mm, "end": v(0.08, -0.55) * mm});
            skLineSegment(sketch, "E489", {"start": v(0.08, -0.55) * mm, "end": v(0.1, -0.53) * mm});
            skLineSegment(sketch, "E490", {"start": v(0.1, -0.53) * mm, "end": v(0.1, -0.53) * mm});
            skLineSegment(sketch, "E491", {"start": v(0.1, -0.53) * mm, "end": v(0.1, -0.52) * mm});
            skLineSegment(sketch, "E492", {"start": v(0.1, -0.52) * mm, "end": v(0.1, -0.5) * mm});
            skLineSegment(sketch, "E493", {"start": v(0.1, -0.5) * mm, "end": v(0.1, -0.5) * mm});
            skLineSegment(sketch, "E494", {"start": v(0.1, -0.5) * mm, "end": v(0.13, -0.49) * mm});
            skLineSegment(sketch, "E495", {"start": v(0.13, -0.49) * mm, "end": v(0.13, -0.49) * mm});
            skLineSegment(sketch, "E496", {"start": v(0.13, -0.49) * mm, "end": v(0.13, -0.48) * mm});
            skLineSegment(sketch, "E497", {"start": v(0.13, -0.48) * mm, "end": v(0.15, -0.48) * mm});
            skLineSegment(sketch, "E498", {"start": v(0.15, -0.48) * mm, "end": v(0.16, -0.48) * mm});
            skLineSegment(sketch, "E499", {"start": v(0.29, -0.6) * mm, "end": v(0.29, -0.6) * mm});
            skLineSegment(sketch, "E500", {"start": v(0.29, -0.6) * mm, "end": v(0.29, -0.61) * mm});
            skLineSegment(sketch, "E501", {"start": v(0.29, -0.61) * mm, "end": v(0.29, -0.62) * mm});
            skLineSegment(sketch, "E502", {"start": v(0.29, -0.62) * mm, "end": v(0.29, -0.62) * mm});
            skLineSegment(sketch, "E503", {"start": v(0.29, -0.62) * mm, "end": v(0.29, -0.63) * mm});
            skLineSegment(sketch, "E504", {"start": v(0.29, -0.63) * mm, "end": v(0.29, -0.63) * mm});
            skLineSegment(sketch, "E505", {"start": v(0.29, -0.63) * mm, "end": v(0.27, -0.64) * mm});
            skLineSegment(sketch, "E506", {"start": v(0.27, -0.64) * mm, "end": v(0.27, -0.64) * mm});
            skLineSegment(sketch, "E507", {"start": v(0.27, -0.64) * mm, "end": v(0.25, -0.63) * mm});
            skLineSegment(sketch, "E508", {"start": v(0.25, -0.63) * mm, "end": v(0.25, -0.63) * mm});
            skLineSegment(sketch, "E509", {"start": v(0.25, -0.63) * mm, "end": v(0.25, -0.62) * mm});
            skLineSegment(sketch, "E510", {"start": v(0.25, -0.62) * mm, "end": v(0.25, -0.62) * mm});
            skLineSegment(sketch, "E511", {"start": v(0.25, -0.62) * mm, "end": v(0.25, -0.6) * mm});
            skLineSegment(sketch, "E512", {"start": v(0.25, -0.6) * mm, "end": v(0.25, -0.6) * mm});
            skLineSegment(sketch, "E513", {"start": v(0.25, -0.6) * mm, "end": v(0.26, -0.6) * mm});
            skLineSegment(sketch, "E514", {"start": v(0.26, -0.6) * mm, "end": v(0.27, -0.6) * mm});
            skLineSegment(sketch, "E515", {"start": v(0.27, -0.6) * mm, "end": v(0.27, -0.6) * mm});
            skLineSegment(sketch, "E516", {"start": v(0.27, -0.6) * mm, "end": v(0.28, -0.6) * mm});
            skLineSegment(sketch, "E517", {"start": v(0.28, -0.6) * mm, "end": v(0.29, -0.6) * mm});
            skLineSegment(sketch, "E518", {"start": v(0.3, -0.5) * mm, "end": v(0.3, -0.5) * mm});
            skLineSegment(sketch, "E519", {"start": v(0.3, -0.5) * mm, "end": v(0.3, -0.49) * mm});
            skLineSegment(sketch, "E520", {"start": v(0.3, -0.49) * mm, "end": v(0.3, -0.49) * mm});
            skLineSegment(sketch, "E521", {"start": v(0.3, -0.49) * mm, "end": v(0.32, -0.48) * mm});
            skLineSegment(sketch, "E522", {"start": v(0.32, -0.48) * mm, "end": v(0.32, -0.48) * mm});
            skLineSegment(sketch, "E523", {"start": v(0.32, -0.48) * mm, "end": v(0.33, -0.48) * mm});
            skLineSegment(sketch, "E524", {"start": v(0.33, -0.48) * mm, "end": v(0.34, -0.49) * mm});
            skLineSegment(sketch, "E525", {"start": v(0.34, -0.49) * mm, "end": v(0.34, -0.49) * mm});
            skLineSegment(sketch, "E526", {"start": v(0.34, -0.49) * mm, "end": v(0.34, -0.5) * mm});
            skLineSegment(sketch, "E527", {"start": v(0.34, -0.5) * mm, "end": v(0.34, -0.5) * mm});
            skLineSegment(sketch, "E528", {"start": v(0.34, -0.5) * mm, "end": v(0.34, -0.62) * mm});
            skLineSegment(sketch, "E529", {"start": v(0.34, -0.62) * mm, "end": v(0.34, -0.62) * mm});
            skLineSegment(sketch, "E530", {"start": v(0.34, -0.62) * mm, "end": v(0.34, -0.63) * mm});
            skLineSegment(sketch, "E531", {"start": v(0.34, -0.63) * mm, "end": v(0.34, -0.63) * mm});
            skLineSegment(sketch, "E532", {"start": v(0.34, -0.63) * mm, "end": v(0.33, -0.64) * mm});
            skLineSegment(sketch, "E533", {"start": v(0.33, -0.64) * mm, "end": v(0.32, -0.64) * mm});
            skLineSegment(sketch, "E534", {"start": v(0.32, -0.64) * mm, "end": v(0.32, -0.64) * mm});
            skLineSegment(sketch, "E535", {"start": v(0.32, -0.64) * mm, "end": v(0.3, -0.63) * mm});
            skLineSegment(sketch, "E536", {"start": v(0.3, -0.63) * mm, "end": v(0.3, -0.63) * mm});
            skLineSegment(sketch, "E537", {"start": v(0.3, -0.63) * mm, "end": v(0.3, -0.62) * mm});
            skLineSegment(sketch, "E538", {"start": v(0.3, -0.62) * mm, "end": v(0.3, -0.62) * mm});
            skLineSegment(sketch, "E539", {"start": v(0.3, -0.62) * mm, "end": v(0.3, -0.5) * mm});
            skLineSegment(sketch, "E540", {"start": v(0.4, -0.56) * mm, "end": v(0.4, -0.57) * mm});
            skLineSegment(sketch, "E541", {"start": v(0.4, -0.57) * mm, "end": v(0.4, -0.59) * mm});
            skLineSegment(sketch, "E542", {"start": v(0.4, -0.59) * mm, "end": v(0.4, -0.6) * mm});
            skLineSegment(sketch, "E543", {"start": v(0.4, -0.6) * mm, "end": v(0.4, -0.6) * mm});
            skLineSegment(sketch, "E544", {"start": v(0.4, -0.6) * mm, "end": v(0.43, -0.6) * mm});
            skLineSegment(sketch, "E545", {"start": v(0.43, -0.6) * mm, "end": v(0.43, -0.6) * mm});
            skLineSegment(sketch, "E546", {"start": v(0.43, -0.6) * mm, "end": v(0.44, -0.6) * mm});
            skLineSegment(sketch, "E547", {"start": v(0.44, -0.6) * mm, "end": v(0.46, -0.6) * mm});
            skLineSegment(sketch, "E548", {"start": v(0.46, -0.6) * mm, "end": v(0.46, -0.6) * mm});
            skLineSegment(sketch, "E549", {"start": v(0.46, -0.6) * mm, "end": v(0.46, -0.59) * mm});
            skLineSegment(sketch, "E550", {"start": v(0.46, -0.59) * mm, "end": v(0.47, -0.57) * mm});
            skLineSegment(sketch, "E551", {"start": v(0.47, -0.57) * mm, "end": v(0.47, -0.56) * mm});
            skLineSegment(sketch, "E552", {"start": v(0.47, -0.56) * mm, "end": v(0.47, -0.55) * mm});
            skLineSegment(sketch, "E553", {"start": v(0.47, -0.55) * mm, "end": v(0.46, -0.53) * mm});
            skLineSegment(sketch, "E554", {"start": v(0.46, -0.53) * mm, "end": v(0.46, -0.53) * mm});
            skLineSegment(sketch, "E555", {"start": v(0.46, -0.53) * mm, "end": v(0.44, -0.52) * mm});
            skLineSegment(sketch, "E556", {"start": v(0.44, -0.52) * mm, "end": v(0.43, -0.52) * mm});
            skLineSegment(sketch, "E557", {"start": v(0.43, -0.52) * mm, "end": v(0.42, -0.52) * mm});
            skLineSegment(sketch, "E558", {"start": v(0.42, -0.52) * mm, "end": v(0.4, -0.53) * mm});
            skLineSegment(sketch, "E559", {"start": v(0.4, -0.53) * mm, "end": v(0.4, -0.53) * mm});
            skLineSegment(sketch, "E560", {"start": v(0.4, -0.53) * mm, "end": v(0.4, -0.55) * mm});
            skLineSegment(sketch, "E561", {"start": v(0.4, -0.55) * mm, "end": v(0.4, -0.56) * mm});
            skLineSegment(sketch, "E562", {"start": v(0.43, -0.48) * mm, "end": v(0.44, -0.48) * mm});
            skLineSegment(sketch, "E563", {"start": v(0.44, -0.48) * mm, "end": v(0.46, -0.48) * mm});
            skLineSegment(sketch, "E564", {"start": v(0.46, -0.48) * mm, "end": v(0.48, -0.5) * mm});
            skLineSegment(sketch, "E565", {"start": v(0.48, -0.5) * mm, "end": v(0.49, -0.5) * mm});
            skLineSegment(sketch, "E566", {"start": v(0.49, -0.5) * mm, "end": v(0.49, -0.5) * mm});
            skLineSegment(sketch, "E567", {"start": v(0.49, -0.5) * mm, "end": v(0.5, -0.53) * mm});
            skLineSegment(sketch, "E568", {"start": v(0.5, -0.53) * mm, "end": v(0.5, -0.55) * mm});
            skLineSegment(sketch, "E569", {"start": v(0.5, -0.55) * mm, "end": v(0.5, -0.56) * mm});
            skLineSegment(sketch, "E570", {"start": v(0.5, -0.56) * mm, "end": v(0.5, -0.57) * mm});
            skLineSegment(sketch, "E571", {"start": v(0.5, -0.57) * mm, "end": v(0.5, -0.59) * mm});
            skLineSegment(sketch, "E572", {"start": v(0.5, -0.59) * mm, "end": v(0.5, -0.61) * mm});
            skLineSegment(sketch, "E573", {"start": v(0.5, -0.61) * mm, "end": v(0.49, -0.62) * mm});
            skLineSegment(sketch, "E574", {"start": v(0.49, -0.62) * mm, "end": v(0.48, -0.62) * mm});
            skLineSegment(sketch, "E575", {"start": v(0.48, -0.62) * mm, "end": v(0.46, -0.63) * mm});
            skLineSegment(sketch, "E576", {"start": v(0.46, -0.63) * mm, "end": v(0.44, -0.64) * mm});
            skLineSegment(sketch, "E577", {"start": v(0.44, -0.64) * mm, "end": v(0.43, -0.64) * mm});
            skLineSegment(sketch, "E578", {"start": v(0.43, -0.64) * mm, "end": v(0.42, -0.64) * mm});
            skLineSegment(sketch, "E579", {"start": v(0.42, -0.64) * mm, "end": v(0.4, -0.63) * mm});
            skLineSegment(sketch, "E580", {"start": v(0.4, -0.63) * mm, "end": v(0.38, -0.62) * mm});
            skLineSegment(sketch, "E581", {"start": v(0.38, -0.62) * mm, "end": v(0.38, -0.62) * mm});
            skLineSegment(sketch, "E582", {"start": v(0.38, -0.62) * mm, "end": v(0.37, -0.61) * mm});
            skLineSegment(sketch, "E583", {"start": v(0.37, -0.61) * mm, "end": v(0.36, -0.6) * mm});
            skLineSegment(sketch, "E584", {"start": v(0.36, -0.6) * mm, "end": v(0.35, -0.57) * mm});
            skLineSegment(sketch, "E585", {"start": v(0.35, -0.57) * mm, "end": v(0.35, -0.56) * mm});
            skLineSegment(sketch, "E586", {"start": v(0.35, -0.56) * mm, "end": v(0.35, -0.55) * mm});
            skLineSegment(sketch, "E587", {"start": v(0.35, -0.55) * mm, "end": v(0.36, -0.53) * mm});
            skLineSegment(sketch, "E588", {"start": v(0.36, -0.53) * mm, "end": v(0.36, -0.53) * mm});
            skLineSegment(sketch, "E589", {"start": v(0.36, -0.53) * mm, "end": v(0.36, -0.52) * mm});
            skLineSegment(sketch, "E590", {"start": v(0.36, -0.52) * mm, "end": v(0.38, -0.5) * mm});
            skLineSegment(sketch, "E591", {"start": v(0.38, -0.5) * mm, "end": v(0.38, -0.5) * mm});
            skLineSegment(sketch, "E592", {"start": v(0.38, -0.5) * mm, "end": v(0.4, -0.49) * mm});
            skLineSegment(sketch, "E593", {"start": v(0.4, -0.49) * mm, "end": v(0.4, -0.49) * mm});
            skLineSegment(sketch, "E594", {"start": v(0.4, -0.49) * mm, "end": v(0.4, -0.48) * mm});
            skLineSegment(sketch, "E595", {"start": v(0.4, -0.48) * mm, "end": v(0.42, -0.48) * mm});
            skLineSegment(sketch, "E596", {"start": v(0.42, -0.48) * mm, "end": v(0.43, -0.48) * mm});
            skLineSegment(sketch, "E597", {"start": v(-0.22, -0.85) * mm, "end": v(-0.23, -0.85) * mm});
            skLineSegment(sketch, "E598", {"start": v(-0.23, -0.85) * mm, "end": v(-0.23, -0.85) * mm});
            skLineSegment(sketch, "E599", {"start": v(-0.23, -0.85) * mm, "end": v(-0.24, -0.86) * mm});
            skLineSegment(sketch, "E600", {"start": v(-0.24, -0.86) * mm, "end": v(-0.24, -0.86) * mm});
            skLineSegment(sketch, "E601", {"start": v(-0.24, -0.86) * mm, "end": v(-0.26, -0.85) * mm});
            skLineSegment(sketch, "E602", {"start": v(-0.26, -0.85) * mm, "end": v(-0.27, -0.87) * mm});
            skLineSegment(sketch, "E603", {"start": v(-0.27, -0.87) * mm, "end": v(-0.27, -0.87) * mm});
            skLineSegment(sketch, "E604", {"start": v(-0.27, -0.87) * mm, "end": v(-0.28, -0.87) * mm});
            skLineSegment(sketch, "E605", {"start": v(-0.28, -0.87) * mm, "end": v(-0.28, -0.87) * mm});
            skLineSegment(sketch, "E606", {"start": v(-0.28, -0.87) * mm, "end": v(-0.29, -0.87) * mm});
            skLineSegment(sketch, "E607", {"start": v(-0.29, -0.87) * mm, "end": v(-0.29, -0.87) * mm});
            skLineSegment(sketch, "E608", {"start": v(-0.29, -0.87) * mm, "end": v(-0.29, -0.86) * mm});
            skLineSegment(sketch, "E609", {"start": v(-0.29, -0.86) * mm, "end": v(-0.29, -0.86) * mm});
            skLineSegment(sketch, "E610", {"start": v(-0.29, -0.86) * mm, "end": v(-0.28, -0.84) * mm});
            skLineSegment(sketch, "E611", {"start": v(-0.28, -0.84) * mm, "end": v(-0.3, -0.83) * mm});
            skLineSegment(sketch, "E612", {"start": v(-0.3, -0.83) * mm, "end": v(-0.3, -0.83) * mm});
            skLineSegment(sketch, "E613", {"start": v(-0.3, -0.83) * mm, "end": v(-0.3, -0.82) * mm});
            skLineSegment(sketch, "E614", {"start": v(-0.3, -0.82) * mm, "end": v(-0.3, -0.82) * mm});
            skLineSegment(sketch, "E615", {"start": v(-0.3, -0.82) * mm, "end": v(-0.3, -0.81) * mm});
            skLineSegment(sketch, "E616", {"start": v(-0.3, -0.81) * mm, "end": v(-0.3, -0.81) * mm});
            skLineSegment(sketch, "E617", {"start": v(-0.3, -0.81) * mm, "end": v(-0.27, -0.82) * mm});
            skLineSegment(sketch, "E618", {"start": v(-0.27, -0.82) * mm, "end": v(-0.26, -0.8) * mm});
            skLineSegment(sketch, "E619", {"start": v(-0.26, -0.8) * mm, "end": v(-0.26, -0.8) * mm});
            skLineSegment(sketch, "E620", {"start": v(-0.26, -0.8) * mm, "end": v(-0.25, -0.8) * mm});
            skLineSegment(sketch, "E621", {"start": v(-0.25, -0.8) * mm, "end": v(-0.25, -0.8) * mm});
            skLineSegment(sketch, "E622", {"start": v(-0.25, -0.8) * mm, "end": v(-0.24, -0.8) * mm});
            skLineSegment(sketch, "E623", {"start": v(-0.24, -0.8) * mm, "end": v(-0.24, -0.8) * mm});
            skLineSegment(sketch, "E624", {"start": v(-0.24, -0.8) * mm, "end": v(-0.25, -0.83) * mm});
            skLineSegment(sketch, "E625", {"start": v(-0.25, -0.83) * mm, "end": v(-0.23, -0.84) * mm});
            skLineSegment(sketch, "E626", {"start": v(-0.23, -0.84) * mm, "end": v(-0.23, -0.84) * mm});
            skLineSegment(sketch, "E627", {"start": v(-0.23, -0.84) * mm, "end": v(-0.22, -0.84) * mm});
            skLineSegment(sketch, "E628", {"start": v(-0.22, -0.84) * mm, "end": v(-0.22, -0.84) * mm});
            skLineSegment(sketch, "E629", {"start": v(-0.22, -0.84) * mm, "end": v(-0.22, -0.85) * mm});
            skLineSegment(sketch, "E630", {"start": v(-0.22, -0.85) * mm, "end": v(-0.22, -0.85) * mm});
            skLineSegment(sketch, "E631", {"start": v(-0.3, -0.8) * mm, "end": v(-0.3, -0.8) * mm});
            skLineSegment(sketch, "E632", {"start": v(-0.3, -0.8) * mm, "end": v(-0.31, -0.81) * mm});
            skLineSegment(sketch, "E633", {"start": v(-0.31, -0.81) * mm, "end": v(-0.31, -0.81) * mm});
            skLineSegment(sketch, "E634", {"start": v(-0.31, -0.81) * mm, "end": v(-0.32, -0.8) * mm});
            skLineSegment(sketch, "E635", {"start": v(-0.32, -0.8) * mm, "end": v(-0.32, -0.8) * mm});
            skLineSegment(sketch, "E636", {"start": v(-0.32, -0.8) * mm, "end": v(-0.33, -0.8) * mm});
            skLineSegment(sketch, "E637", {"start": v(-0.33, -0.8) * mm, "end": v(-0.33, -0.8) * mm});
            skLineSegment(sketch, "E638", {"start": v(-0.33, -0.8) * mm, "end": v(-0.33, -0.78) * mm});
            skLineSegment(sketch, "E639", {"start": v(-0.33, -0.78) * mm, "end": v(-0.33, -0.78) * mm});
            skLineSegment(sketch, "E640", {"start": v(-0.33, -0.78) * mm, "end": v(-0.34, -0.77) * mm});
            skLineSegment(sketch, "E641", {"start": v(-0.34, -0.77) * mm, "end": v(-0.34, -0.77) * mm});
            skLineSegment(sketch, "E642", {"start": v(-0.34, -0.77) * mm, "end": v(-0.35, -0.77) * mm});
            skLineSegment(sketch, "E643", {"start": v(-0.35, -0.77) * mm, "end": v(-0.36, -0.77) * mm});
            skLineSegment(sketch, "E644", {"start": v(-0.36, -0.77) * mm, "end": v(-0.36, -0.77) * mm});
            skLineSegment(sketch, "E645", {"start": v(-0.36, -0.77) * mm, "end": v(-0.37, -0.78) * mm});
            skLineSegment(sketch, "E646", {"start": v(-0.37, -0.78) * mm, "end": v(-0.37, -0.78) * mm});
            skLineSegment(sketch, "E647", {"start": v(-0.37, -0.78) * mm, "end": v(-0.38, -0.78) * mm});
            skLineSegment(sketch, "E648", {"start": v(-0.38, -0.78) * mm, "end": v(-0.38, -0.79) * mm});
            skLineSegment(sketch, "E649", {"start": v(-0.38, -0.79) * mm, "end": v(-0.38, -0.8) * mm});
            skLineSegment(sketch, "E650", {"start": v(-0.38, -0.8) * mm, "end": v(-0.37, -0.8) * mm});
            skLineSegment(sketch, "E651", {"start": v(-0.37, -0.8) * mm, "end": v(-0.36, -0.81) * mm});
            skLineSegment(sketch, "E652", {"start": v(-0.36, -0.81) * mm, "end": v(-0.36, -0.81) * mm});
            skLineSegment(sketch, "E653", {"start": v(-0.36, -0.81) * mm, "end": v(-0.36, -0.82) * mm});
            skLineSegment(sketch, "E654", {"start": v(-0.36, -0.82) * mm, "end": v(-0.36, -0.82) * mm});
            skLineSegment(sketch, "E655", {"start": v(-0.36, -0.82) * mm, "end": v(-0.36, -0.83) * mm});
            skLineSegment(sketch, "E656", {"start": v(-0.36, -0.83) * mm, "end": v(-0.37, -0.83) * mm});
            skLineSegment(sketch, "E657", {"start": v(-0.37, -0.83) * mm, "end": v(-0.37, -0.83) * mm});
            skLineSegment(sketch, "E658", {"start": v(-0.37, -0.83) * mm, "end": v(-0.38, -0.83) * mm});
            skLineSegment(sketch, "E659", {"start": v(-0.38, -0.83) * mm, "end": v(-0.39, -0.83) * mm});
            skLineSegment(sketch, "E660", {"start": v(-0.39, -0.83) * mm, "end": v(-0.39, -0.83) * mm});
            skLineSegment(sketch, "E661", {"start": v(-0.39, -0.83) * mm, "end": v(-0.4, -0.84) * mm});
            skLineSegment(sketch, "E662", {"start": v(-0.4, -0.84) * mm, "end": v(-0.4, -0.84) * mm});
            skLineSegment(sketch, "E663", {"start": v(-0.4, -0.84) * mm, "end": v(-0.4, -0.85) * mm});
            skLineSegment(sketch, "E664", {"start": v(-0.4, -0.85) * mm, "end": v(-0.4, -0.86) * mm});
            skLineSegment(sketch, "E665", {"start": v(-0.4, -0.86) * mm, "end": v(-0.4, -0.86) * mm});
            skLineSegment(sketch, "E666", {"start": v(-0.4, -0.86) * mm, "end": v(-0.39, -0.86) * mm});
            skLineSegment(sketch, "E667", {"start": v(-0.39, -0.86) * mm, "end": v(-0.38, -0.87) * mm});
            skLineSegment(sketch, "E668", {"start": v(-0.38, -0.87) * mm, "end": v(-0.37, -0.86) * mm});
            skLineSegment(sketch, "E669", {"start": v(-0.37, -0.86) * mm, "end": v(-0.37, -0.86) * mm});
            skLineSegment(sketch, "E670", {"start": v(-0.37, -0.86) * mm, "end": v(-0.36, -0.86) * mm});
            skLineSegment(sketch, "E671", {"start": v(-0.36, -0.86) * mm, "end": v(-0.35, -0.86) * mm});
            skLineSegment(sketch, "E672", {"start": v(-0.35, -0.86) * mm, "end": v(-0.35, -0.86) * mm});
            skLineSegment(sketch, "E673", {"start": v(-0.35, -0.86) * mm, "end": v(-0.34, -0.86) * mm});
            skLineSegment(sketch, "E674", {"start": v(-0.34, -0.86) * mm, "end": v(-0.34, -0.86) * mm});
            skLineSegment(sketch, "E675", {"start": v(-0.34, -0.86) * mm, "end": v(-0.35, -0.87) * mm});
            skLineSegment(sketch, "E676", {"start": v(-0.35, -0.87) * mm, "end": v(-0.35, -0.87) * mm});
            skLineSegment(sketch, "E677", {"start": v(-0.35, -0.87) * mm, "end": v(-0.35, -0.88) * mm});
            skLineSegment(sketch, "E678", {"start": v(-0.35, -0.88) * mm, "end": v(-0.35, -0.88) * mm});
            skLineSegment(sketch, "E679", {"start": v(-0.35, -0.88) * mm, "end": v(-0.36, -0.89) * mm});
            skLineSegment(sketch, "E680", {"start": v(-0.36, -0.89) * mm, "end": v(-0.37, -0.89) * mm});
            skLineSegment(sketch, "E681", {"start": v(-0.37, -0.89) * mm, "end": v(-0.37, -0.9) * mm});
            skLineSegment(sketch, "E682", {"start": v(-0.37, -0.9) * mm, "end": v(-0.38, -0.9) * mm});
            skLineSegment(sketch, "E683", {"start": v(-0.38, -0.9) * mm, "end": v(-0.38, -0.9) * mm});
            skLineSegment(sketch, "E684", {"start": v(-0.38, -0.9) * mm, "end": v(-0.4, -0.89) * mm});
            skLineSegment(sketch, "E685", {"start": v(-0.4, -0.89) * mm, "end": v(-0.4, -0.88) * mm});
            skLineSegment(sketch, "E686", {"start": v(-0.4, -0.88) * mm, "end": v(-0.4, -0.88) * mm});
            skLineSegment(sketch, "E687", {"start": v(-0.4, -0.88) * mm, "end": v(-0.43, -0.86) * mm});
            skLineSegment(sketch, "E688", {"start": v(-0.43, -0.86) * mm, "end": v(-0.43, -0.84) * mm});
            skLineSegment(sketch, "E689", {"start": v(-0.43, -0.84) * mm, "end": v(-0.43, -0.83) * mm});
            skLineSegment(sketch, "E690", {"start": v(-0.43, -0.83) * mm, "end": v(-0.42, -0.83) * mm});
            skLineSegment(sketch, "E691", {"start": v(-0.42, -0.83) * mm, "end": v(-0.41, -0.81) * mm});
            skLineSegment(sketch, "E692", {"start": v(-0.41, -0.81) * mm, "end": v(-0.41, -0.81) * mm});
            skLineSegment(sketch, "E693", {"start": v(-0.41, -0.81) * mm, "end": v(-0.4, -0.8) * mm});
            skLineSegment(sketch, "E694", {"start": v(-0.4, -0.8) * mm, "end": v(-0.4, -0.8) * mm});
            skLineSegment(sketch, "E695", {"start": v(-0.4, -0.8) * mm, "end": v(-0.4, -0.79) * mm});
            skLineSegment(sketch, "E696", {"start": v(-0.4, -0.79) * mm, "end": v(-0.4, -0.77) * mm});
            skLineSegment(sketch, "E697", {"start": v(-0.4, -0.77) * mm, "end": v(-0.4, -0.77) * mm});
            skLineSegment(sketch, "E698", {"start": v(-0.4, -0.77) * mm, "end": v(-0.4, -0.76) * mm});
            skLineSegment(sketch, "E699", {"start": v(-0.4, -0.76) * mm, "end": v(-0.37, -0.74) * mm});
            skLineSegment(sketch, "E700", {"start": v(-0.37, -0.74) * mm, "end": v(-0.37, -0.74) * mm});
            skLineSegment(sketch, "E701", {"start": v(-0.37, -0.74) * mm, "end": v(-0.34, -0.75) * mm});
            skLineSegment(sketch, "E702", {"start": v(-0.34, -0.75) * mm, "end": v(-0.33, -0.75) * mm});
            skLineSegment(sketch, "E703", {"start": v(-0.33, -0.75) * mm, "end": v(-0.33, -0.75) * mm});
            skLineSegment(sketch, "E704", {"start": v(-0.33, -0.75) * mm, "end": v(-0.3, -0.77) * mm});
            skLineSegment(sketch, "E705", {"start": v(-0.3, -0.77) * mm, "end": v(-0.3, -0.78) * mm});
            skLineSegment(sketch, "E706", {"start": v(-0.3, -0.78) * mm, "end": v(-0.3, -0.78) * mm});
            skLineSegment(sketch, "E707", {"start": v(-0.3, -0.78) * mm, "end": v(-0.3, -0.8) * mm});
            skLineSegment(sketch, "E708", {"start": v(-0.4, -0.75) * mm, "end": v(-0.4, -0.75) * mm});
            skLineSegment(sketch, "E709", {"start": v(-0.4, -0.75) * mm, "end": v(-0.41, -0.76) * mm});
            skLineSegment(sketch, "E710", {"start": v(-0.41, -0.76) * mm, "end": v(-0.41, -0.76) * mm});
            skLineSegment(sketch, "E711", {"start": v(-0.41, -0.76) * mm, "end": v(-0.42, -0.76) * mm});
            skLineSegment(sketch, "E712", {"start": v(-0.42, -0.76) * mm, "end": v(-0.42, -0.76) * mm});
            skLineSegment(sketch, "E713", {"start": v(-0.42, -0.76) * mm, "end": v(-0.43, -0.75) * mm});
            skLineSegment(sketch, "E714", {"start": v(-0.43, -0.75) * mm, "end": v(-0.43, -0.75) * mm});
            skLineSegment(sketch, "E715", {"start": v(-0.43, -0.75) * mm, "end": v(-0.43, -0.74) * mm});
            skLineSegment(sketch, "E716", {"start": v(-0.43, -0.74) * mm, "end": v(-0.43, -0.74) * mm});
            skLineSegment(sketch, "E717", {"start": v(-0.43, -0.74) * mm, "end": v(-0.42, -0.73) * mm});
            skLineSegment(sketch, "E718", {"start": v(-0.42, -0.73) * mm, "end": v(-0.42, -0.73) * mm});
            skLineSegment(sketch, "E719", {"start": v(-0.42, -0.73) * mm, "end": v(-0.43, -0.72) * mm});
            skLineSegment(sketch, "E720", {"start": v(-0.43, -0.72) * mm, "end": v(-0.43, -0.71) * mm});
            skLineSegment(sketch, "E721", {"start": v(-0.43, -0.71) * mm, "end": v(-0.44, -0.71) * mm});
            skLineSegment(sketch, "E722", {"start": v(-0.44, -0.71) * mm, "end": v(-0.45, -0.7) * mm});
            skLineSegment(sketch, "E723", {"start": v(-0.45, -0.7) * mm, "end": v(-0.46, -0.72) * mm});
            skLineSegment(sketch, "E724", {"start": v(-0.46, -0.72) * mm, "end": v(-0.47, -0.72) * mm});
            skLineSegment(sketch, "E725", {"start": v(-0.47, -0.72) * mm, "end": v(-0.47, -0.72) * mm});
            skLineSegment(sketch, "E726", {"start": v(-0.47, -0.72) * mm, "end": v(-0.47, -0.73) * mm});
            skLineSegment(sketch, "E727", {"start": v(-0.47, -0.73) * mm, "end": v(-0.47, -0.74) * mm});
            skLineSegment(sketch, "E728", {"start": v(-0.47, -0.74) * mm, "end": v(-0.47, -0.74) * mm});
            skLineSegment(sketch, "E729", {"start": v(-0.47, -0.74) * mm, "end": v(-0.47, -0.75) * mm});
            skLineSegment(sketch, "E730", {"start": v(-0.47, -0.75) * mm, "end": v(-0.46, -0.76) * mm});
            skLineSegment(sketch, "E731", {"start": v(-0.46, -0.76) * mm, "end": v(-0.44, -0.77) * mm});
            skLineSegment(sketch, "E732", {"start": v(-0.44, -0.77) * mm, "end": v(-0.44, -0.77) * mm});
            skLineSegment(sketch, "E733", {"start": v(-0.44, -0.77) * mm, "end": v(-0.43, -0.78) * mm});
            skLineSegment(sketch, "E734", {"start": v(-0.43, -0.78) * mm, "end": v(-0.43, -0.78) * mm});
            skLineSegment(sketch, "E735", {"start": v(-0.43, -0.78) * mm, "end": v(-0.43, -0.79) * mm});
            skLineSegment(sketch, "E736", {"start": v(-0.43, -0.79) * mm, "end": v(-0.44, -0.79) * mm});
            skLineSegment(sketch, "E737", {"start": v(-0.44, -0.79) * mm, "end": v(-0.44, -0.79) * mm});
            skLineSegment(sketch, "E738", {"start": v(-0.44, -0.79) * mm, "end": v(-0.44, -0.8) * mm});
            skLineSegment(sketch, "E739", {"start": v(-0.44, -0.8) * mm, "end": v(-0.44, -0.8) * mm});
            skLineSegment(sketch, "E740", {"start": v(-0.44, -0.8) * mm, "end": v(-0.47, -0.83) * mm});
            skLineSegment(sketch, "E741", {"start": v(-0.47, -0.83) * mm, "end": v(-0.48, -0.84) * mm});
            skLineSegment(sketch, "E742", {"start": v(-0.48, -0.84) * mm, "end": v(-0.48, -0.84) * mm});
            skLineSegment(sketch, "E743", {"start": v(-0.48, -0.84) * mm, "end": v(-0.54, -0.8) * mm});
            skLineSegment(sketch, "E744", {"start": v(-0.54, -0.8) * mm, "end": v(-0.54, -0.8) * mm});
            skLineSegment(sketch, "E745", {"start": v(-0.54, -0.8) * mm, "end": v(-0.54, -0.79) * mm});
            skLineSegment(sketch, "E746", {"start": v(-0.54, -0.79) * mm, "end": v(-0.54, -0.79) * mm});
            skLineSegment(sketch, "E747", {"start": v(-0.54, -0.79) * mm, "end": v(-0.53, -0.78) * mm});
            skLineSegment(sketch, "E748", {"start": v(-0.53, -0.78) * mm, "end": v(-0.53, -0.78) * mm});
            skLineSegment(sketch, "E749", {"start": v(-0.53, -0.78) * mm, "end": v(-0.52, -0.78) * mm});
            skLineSegment(sketch, "E750", {"start": v(-0.52, -0.78) * mm, "end": v(-0.52, -0.78) * mm});
            skLineSegment(sketch, "E751", {"start": v(-0.52, -0.78) * mm, "end": v(-0.48, -0.8) * mm});
            skLineSegment(sketch, "E752", {"start": v(-0.48, -0.8) * mm, "end": v(-0.46, -0.78) * mm});
            skLineSegment(sketch, "E753", {"start": v(-0.46, -0.78) * mm, "end": v(-0.48, -0.77) * mm});
            skLineSegment(sketch, "E754", {"start": v(-0.48, -0.77) * mm, "end": v(-0.48, -0.77) * mm});
            skLineSegment(sketch, "E755", {"start": v(-0.48, -0.77) * mm, "end": v(-0.5, -0.75) * mm});
            skLineSegment(sketch, "E756", {"start": v(-0.5, -0.75) * mm, "end": v(-0.5, -0.74) * mm});
            skLineSegment(sketch, "E757", {"start": v(-0.5, -0.74) * mm, "end": v(-0.5, -0.74) * mm});
            skLineSegment(sketch, "E758", {"start": v(-0.5, -0.74) * mm, "end": v(-0.5, -0.71) * mm});
            skLineSegment(sketch, "E759", {"start": v(-0.5, -0.71) * mm, "end": v(-0.5, -0.7) * mm});
            skLineSegment(sketch, "E760", {"start": v(-0.5, -0.7) * mm, "end": v(-0.49, -0.7) * mm});
            skLineSegment(sketch, "E761", {"start": v(-0.49, -0.7) * mm, "end": v(-0.49, -0.7) * mm});
            skLineSegment(sketch, "E762", {"start": v(-0.49, -0.7) * mm, "end": v(-0.46, -0.68) * mm});
            skLineSegment(sketch, "E763", {"start": v(-0.46, -0.68) * mm, "end": v(-0.46, -0.68) * mm});
            skLineSegment(sketch, "E764", {"start": v(-0.46, -0.68) * mm, "end": v(-0.45, -0.68) * mm});
            skLineSegment(sketch, "E765", {"start": v(-0.45, -0.68) * mm, "end": v(-0.42, -0.7) * mm});
            skLineSegment(sketch, "E766", {"start": v(-0.42, -0.7) * mm, "end": v(-0.42, -0.7) * mm});
            skLineSegment(sketch, "E767", {"start": v(-0.42, -0.7) * mm, "end": v(-0.4, -0.72) * mm});
            skLineSegment(sketch, "E768", {"start": v(-0.4, -0.72) * mm, "end": v(-0.4, -0.72) * mm});
            skLineSegment(sketch, "E769", {"start": v(-0.4, -0.72) * mm, "end": v(-0.4, -0.73) * mm});
            skLineSegment(sketch, "E770", {"start": v(-0.4, -0.73) * mm, "end": v(-0.4, -0.75) * mm});
            skLineSegment(sketch, "E771", {"start": v(-0.54, -0.76) * mm, "end": v(-0.54, -0.76) * mm});
            skLineSegment(sketch, "E772", {"start": v(-0.54, -0.76) * mm, "end": v(-0.55, -0.76) * mm});
            skLineSegment(sketch, "E773", {"start": v(-0.55, -0.76) * mm, "end": v(-0.55, -0.76) * mm});
            skLineSegment(sketch, "E774", {"start": v(-0.55, -0.76) * mm, "end": v(-0.58, -0.76) * mm});
            skLineSegment(sketch, "E775", {"start": v(-0.58, -0.76) * mm, "end": v(-0.58, -0.76) * mm});
            skLineSegment(sketch, "E776", {"start": v(-0.58, -0.76) * mm, "end": v(-0.59, -0.76) * mm});
            skLineSegment(sketch, "E777", {"start": v(-0.59, -0.76) * mm, "end": v(-0.59, -0.76) * mm});
            skLineSegment(sketch, "E778", {"start": v(-0.59, -0.76) * mm, "end": v(-0.6, -0.75) * mm});
            skLineSegment(sketch, "E779", {"start": v(-0.6, -0.75) * mm, "end": v(-0.6, -0.75) * mm});
            skLineSegment(sketch, "E780", {"start": v(-0.6, -0.75) * mm, "end": v(-0.5, -0.64) * mm});
            skLineSegment(sketch, "E781", {"start": v(-0.5, -0.64) * mm, "end": v(-0.5, -0.64) * mm});
            skLineSegment(sketch, "E782", {"start": v(-0.5, -0.64) * mm, "end": v(-0.49, -0.64) * mm});
            skLineSegment(sketch, "E783", {"start": v(-0.49, -0.64) * mm, "end": v(-0.49, -0.64) * mm});
            skLineSegment(sketch, "E784", {"start": v(-0.49, -0.64) * mm, "end": v(-0.49, -0.65) * mm});
            skLineSegment(sketch, "E785", {"start": v(-0.49, -0.65) * mm, "end": v(-0.48, -0.65) * mm});
            skLineSegment(sketch, "E786", {"start": v(-0.48, -0.65) * mm, "end": v(-0.48, -0.65) * mm});
            skLineSegment(sketch, "E787", {"start": v(-0.48, -0.65) * mm, "end": v(-0.48, -0.66) * mm});
            skLineSegment(sketch, "E788", {"start": v(-0.48, -0.66) * mm, "end": v(-0.48, -0.66) * mm});
            skLineSegment(sketch, "E789", {"start": v(-0.48, -0.66) * mm, "end": v(-0.56, -0.74) * mm});
            skLineSegment(sketch, "E790", {"start": v(-0.56, -0.74) * mm, "end": v(-0.55, -0.74) * mm});
            skLineSegment(sketch, "E791", {"start": v(-0.55, -0.74) * mm, "end": v(-0.55, -0.74) * mm});
            skLineSegment(sketch, "E792", {"start": v(-0.55, -0.74) * mm, "end": v(-0.54, -0.75) * mm});
            skLineSegment(sketch, "E793", {"start": v(-0.54, -0.75) * mm, "end": v(-0.54, -0.75) * mm});
            skLineSegment(sketch, "E794", {"start": v(-0.54, -0.75) * mm, "end": v(-0.54, -0.76) * mm});
            skLineSegment(sketch, "E795", {"start": v(-0.64, -0.65) * mm, "end": v(-0.63, -0.64) * mm});
            skLineSegment(sketch, "E796", {"start": v(-0.63, -0.64) * mm, "end": v(-0.63, -0.63) * mm});
            skLineSegment(sketch, "E797", {"start": v(-0.63, -0.63) * mm, "end": v(-0.63, -0.62) * mm});
            skLineSegment(sketch, "E798", {"start": v(-0.63, -0.62) * mm, "end": v(-0.63, -0.61) * mm});
            skLineSegment(sketch, "E799", {"start": v(-0.63, -0.61) * mm, "end": v(-0.63, -0.61) * mm});
            skLineSegment(sketch, "E800", {"start": v(-0.63, -0.61) * mm, "end": v(-0.65, -0.6) * mm});
            skLineSegment(sketch, "E801", {"start": v(-0.65, -0.6) * mm, "end": v(-0.66, -0.6) * mm});
            skLineSegment(sketch, "E802", {"start": v(-0.66, -0.6) * mm, "end": v(-0.66, -0.61) * mm});
            skLineSegment(sketch, "E803", {"start": v(-0.66, -0.61) * mm, "end": v(-0.67, -0.61) * mm});
            skLineSegment(sketch, "E804", {"start": v(-0.67, -0.61) * mm, "end": v(-0.67, -0.62) * mm});
            skLineSegment(sketch, "E805", {"start": v(-0.67, -0.62) * mm, "end": v(-0.68, -0.63) * mm});
            skLineSegment(sketch, "E806", {"start": v(-0.68, -0.63) * mm, "end": v(-0.67, -0.64) * mm});
            skLineSegment(sketch, "E807", {"start": v(-0.67, -0.64) * mm, "end": v(-0.67, -0.65) * mm});
            skLineSegment(sketch, "E808", {"start": v(-0.67, -0.65) * mm, "end": v(-0.67, -0.65) * mm});
            skLineSegment(sketch, "E809", {"start": v(-0.67, -0.65) * mm, "end": v(-0.66, -0.66) * mm});
            skLineSegment(sketch, "E810", {"start": v(-0.66, -0.66) * mm, "end": v(-0.64, -0.65) * mm});
            skLineSegment(sketch, "E811", {"start": v(-0.64, -0.65) * mm, "end": v(-0.64, -0.65) * mm});
            skLineSegment(sketch, "E812", {"start": v(-0.57, -0.62) * mm, "end": v(-0.57, -0.62) * mm});
            skLineSegment(sketch, "E813", {"start": v(-0.57, -0.62) * mm, "end": v(-0.58, -0.63) * mm});
            skLineSegment(sketch, "E814", {"start": v(-0.58, -0.63) * mm, "end": v(-0.58, -0.63) * mm});
            skLineSegment(sketch, "E815", {"start": v(-0.58, -0.63) * mm, "end": v(-0.58, -0.62) * mm});
            skLineSegment(sketch, "E816", {"start": v(-0.58, -0.62) * mm, "end": v(-0.58, -0.62) * mm});
            skLineSegment(sketch, "E817", {"start": v(-0.58, -0.62) * mm, "end": v(-0.59, -0.62) * mm});
            skLineSegment(sketch, "E818", {"start": v(-0.59, -0.62) * mm, "end": v(-0.59, -0.6) * mm});
            skLineSegment(sketch, "E819", {"start": v(-0.59, -0.6) * mm, "end": v(-0.59, -0.6) * mm});
            skLineSegment(sketch, "E820", {"start": v(-0.59, -0.6) * mm, "end": v(-0.58, -0.6) * mm});
            skLineSegment(sketch, "E821", {"start": v(-0.58, -0.6) * mm, "end": v(-0.58, -0.6) * mm});
            skLineSegment(sketch, "E822", {"start": v(-0.58, -0.6) * mm, "end": v(-0.58, -0.59) * mm});
            skLineSegment(sketch, "E823", {"start": v(-0.58, -0.59) * mm, "end": v(-0.59, -0.58) * mm});
            skLineSegment(sketch, "E824", {"start": v(-0.59, -0.58) * mm, "end": v(-0.59, -0.58) * mm});
            skLineSegment(sketch, "E825", {"start": v(-0.59, -0.58) * mm, "end": v(-0.6, -0.57) * mm});
            skLineSegment(sketch, "E826", {"start": v(-0.6, -0.57) * mm, "end": v(-0.6, -0.57) * mm});
            skLineSegment(sketch, "E827", {"start": v(-0.6, -0.57) * mm, "end": v(-0.62, -0.57) * mm});
            skLineSegment(sketch, "E828", {"start": v(-0.62, -0.57) * mm, "end": v(-0.62, -0.57) * mm});
            skLineSegment(sketch, "E829", {"start": v(-0.62, -0.57) * mm, "end": v(-0.64, -0.59) * mm});
            skLineSegment(sketch, "E830", {"start": v(-0.64, -0.59) * mm, "end": v(-0.64, -0.59) * mm});
            skLineSegment(sketch, "E831", {"start": v(-0.64, -0.59) * mm, "end": v(-0.61, -0.6) * mm});
            skLineSegment(sketch, "E832", {"start": v(-0.61, -0.6) * mm, "end": v(-0.61, -0.6) * mm});
            skLineSegment(sketch, "E833", {"start": v(-0.61, -0.6) * mm, "end": v(-0.6, -0.63) * mm});
            skLineSegment(sketch, "E834", {"start": v(-0.6, -0.63) * mm, "end": v(-0.6, -0.63) * mm});
            skLineSegment(sketch, "E835", {"start": v(-0.6, -0.63) * mm, "end": v(-0.6, -0.64) * mm});
            skLineSegment(sketch, "E836", {"start": v(-0.6, -0.64) * mm, "end": v(-0.61, -0.66) * mm});
            skLineSegment(sketch, "E837", {"start": v(-0.61, -0.66) * mm, "end": v(-0.62, -0.66) * mm});
            skLineSegment(sketch, "E838", {"start": v(-0.62, -0.66) * mm, "end": v(-0.62, -0.67) * mm});
            skLineSegment(sketch, "E839", {"start": v(-0.62, -0.67) * mm, "end": v(-0.62, -0.67) * mm});
            skLineSegment(sketch, "E840", {"start": v(-0.62, -0.67) * mm, "end": v(-0.65, -0.68) * mm});
            skLineSegment(sketch, "E841", {"start": v(-0.65, -0.68) * mm, "end": v(-0.66, -0.68) * mm});
            skLineSegment(sketch, "E842", {"start": v(-0.66, -0.68) * mm, "end": v(-0.66, -0.68) * mm});
            skLineSegment(sketch, "E843", {"start": v(-0.66, -0.68) * mm, "end": v(-0.68, -0.66) * mm});
            skLineSegment(sketch, "E844", {"start": v(-0.68, -0.66) * mm, "end": v(-0.69, -0.66) * mm});
            skLineSegment(sketch, "E845", {"start": v(-0.69, -0.66) * mm, "end": v(-0.69, -0.66) * mm});
            skLineSegment(sketch, "E846", {"start": v(-0.69, -0.66) * mm, "end": v(-0.7, -0.63) * mm});
            skLineSegment(sketch, "E847", {"start": v(-0.7, -0.63) * mm, "end": v(-0.7, -0.63) * mm});
            skLineSegment(sketch, "E848", {"start": v(-0.7, -0.63) * mm, "end": v(-0.7, -0.62) * mm});
            skLineSegment(sketch, "E849", {"start": v(-0.7, -0.62) * mm, "end": v(-0.69, -0.6) * mm});
            skLineSegment(sketch, "E850", {"start": v(-0.69, -0.6) * mm, "end": v(-0.68, -0.6) * mm});
            skLineSegment(sketch, "E851", {"start": v(-0.68, -0.6) * mm, "end": v(-0.64, -0.55) * mm});
            skLineSegment(sketch, "E852", {"start": v(-0.64, -0.55) * mm, "end": v(-0.64, -0.55) * mm});
            skLineSegment(sketch, "E853", {"start": v(-0.64, -0.55) * mm, "end": v(-0.6, -0.54) * mm});
            skLineSegment(sketch, "E854", {"start": v(-0.6, -0.54) * mm, "end": v(-0.6, -0.54) * mm});
            skLineSegment(sketch, "E855", {"start": v(-0.6, -0.54) * mm, "end": v(-0.57, -0.56) * mm});
            skLineSegment(sketch, "E856", {"start": v(-0.57, -0.56) * mm, "end": v(-0.57, -0.56) * mm});
            skLineSegment(sketch, "E857", {"start": v(-0.57, -0.56) * mm, "end": v(-0.56, -0.6) * mm});
            skLineSegment(sketch, "E858", {"start": v(-0.56, -0.6) * mm, "end": v(-0.56, -0.6) * mm});
            skLineSegment(sketch, "E859", {"start": v(-0.56, -0.6) * mm, "end": v(-0.57, -0.62) * mm});
            skLineSegment(sketch, "E860", {"start": v(-0.7, -0.59) * mm, "end": v(-0.7, -0.59) * mm});
            skLineSegment(sketch, "E861", {"start": v(-0.7, -0.59) * mm, "end": v(-0.72, -0.59) * mm});
            skLineSegment(sketch, "E862", {"start": v(-0.72, -0.59) * mm, "end": v(-0.72, -0.59) * mm});
            skLineSegment(sketch, "E863", {"start": v(-0.72, -0.59) * mm, "end": v(-0.75, -0.58) * mm});
            skLineSegment(sketch, "E864", {"start": v(-0.75, -0.58) * mm, "end": v(-0.75, -0.58) * mm});
            skLineSegment(sketch, "E865", {"start": v(-0.75, -0.58) * mm, "end": v(-0.75, -0.57) * mm});
            skLineSegment(sketch, "E866", {"start": v(-0.75, -0.57) * mm, "end": v(-0.76, -0.57) * mm});
            skLineSegment(sketch, "E867", {"start": v(-0.76, -0.57) * mm, "end": v(-0.76, -0.57) * mm});
            skLineSegment(sketch, "E868", {"start": v(-0.76, -0.57) * mm, "end": v(-0.75, -0.56) * mm});
            skLineSegment(sketch, "E869", {"start": v(-0.75, -0.56) * mm, "end": v(-0.75, -0.56) * mm});
            skLineSegment(sketch, "E870", {"start": v(-0.75, -0.56) * mm, "end": v(-0.64, -0.48) * mm});
            skLineSegment(sketch, "E871", {"start": v(-0.64, -0.48) * mm, "end": v(-0.64, -0.48) * mm});
            skLineSegment(sketch, "E872", {"start": v(-0.64, -0.48) * mm, "end": v(-0.63, -0.48) * mm});
            skLineSegment(sketch, "E873", {"start": v(-0.63, -0.48) * mm, "end": v(-0.63, -0.48) * mm});
            skLineSegment(sketch, "E874", {"start": v(-0.63, -0.48) * mm, "end": v(-0.63, -0.49) * mm});
            skLineSegment(sketch, "E875", {"start": v(-0.63, -0.49) * mm, "end": v(-0.63, -0.5) * mm});
            skLineSegment(sketch, "E876", {"start": v(-0.63, -0.5) * mm, "end": v(-0.63, -0.5) * mm});
            skLineSegment(sketch, "E877", {"start": v(-0.63, -0.5) * mm, "end": v(-0.62, -0.5) * mm});
            skLineSegment(sketch, "E878", {"start": v(-0.62, -0.5) * mm, "end": v(-0.62, -0.5) * mm});
            skLineSegment(sketch, "E879", {"start": v(-0.62, -0.5) * mm, "end": v(-0.63, -0.5) * mm});
            skLineSegment(sketch, "E880", {"start": v(-0.63, -0.5) * mm, "end": v(-0.72, -0.57) * mm});
            skLineSegment(sketch, "E881", {"start": v(-0.72, -0.57) * mm, "end": v(-0.7, -0.57) * mm});
            skLineSegment(sketch, "E882", {"start": v(-0.7, -0.57) * mm, "end": v(-0.7, -0.57) * mm});
            skLineSegment(sketch, "E883", {"start": v(-0.7, -0.57) * mm, "end": v(-0.7, -0.58) * mm});
            skLineSegment(sketch, "E884", {"start": v(-0.7, -0.58) * mm, "end": v(-0.7, -0.58) * mm});
            skLineSegment(sketch, "E885", {"start": v(-0.7, -0.58) * mm, "end": v(-0.7, -0.59) * mm});
            skLineSegment(sketch, "E886", {"start": v(-0.67, -0.44) * mm, "end": v(-0.69, -0.44) * mm});
            skLineSegment(sketch, "E887", {"start": v(-0.69, -0.44) * mm, "end": v(-0.7, -0.45) * mm});
            skLineSegment(sketch, "E888", {"start": v(-0.7, -0.45) * mm, "end": v(-0.7, -0.45) * mm});
            skLineSegment(sketch, "E889", {"start": v(-0.7, -0.45) * mm, "end": v(-0.71, -0.45) * mm});
            skLineSegment(sketch, "E890", {"start": v(-0.71, -0.45) * mm, "end": v(-0.73, -0.44) * mm});
            skLineSegment(sketch, "E891", {"start": v(-0.73, -0.44) * mm, "end": v(-0.73, -0.44) * mm});
            skLineSegment(sketch, "E892", {"start": v(-0.73, -0.44) * mm, "end": v(-0.75, -0.43) * mm});
            skLineSegment(sketch, "E893", {"start": v(-0.75, -0.43) * mm, "end": v(-0.75, -0.43) * mm});
            skLineSegment(sketch, "E894", {"start": v(-0.75, -0.43) * mm, "end": v(-0.77, -0.42) * mm});
            skLineSegment(sketch, "E895", {"start": v(-0.77, -0.42) * mm, "end": v(-0.77, -0.42) * mm});
            skLineSegment(sketch, "E896", {"start": v(-0.77, -0.42) * mm, "end": v(-0.79, -0.42) * mm});
            skLineSegment(sketch, "E897", {"start": v(-0.79, -0.42) * mm, "end": v(-0.8, -0.42) * mm});
            skLineSegment(sketch, "E898", {"start": v(-0.8, -0.42) * mm, "end": v(-0.8, -0.42) * mm});
            skLineSegment(sketch, "E899", {"start": v(-0.8, -0.42) * mm, "end": v(-0.8, -0.43) * mm});
            skLineSegment(sketch, "E900", {"start": v(-0.8, -0.43) * mm, "end": v(-0.8, -0.43) * mm});
            skLineSegment(sketch, "E901", {"start": v(-0.8, -0.43) * mm, "end": v(-0.8, -0.45) * mm});
            skLineSegment(sketch, "E902", {"start": v(-0.8, -0.45) * mm, "end": v(-0.8, -0.45) * mm});
            skLineSegment(sketch, "E903", {"start": v(-0.8, -0.45) * mm, "end": v(-0.8, -0.46) * mm});
            skLineSegment(sketch, "E904", {"start": v(-0.8, -0.46) * mm, "end": v(-0.79, -0.46) * mm});
            skLineSegment(sketch, "E905", {"start": v(-0.79, -0.46) * mm, "end": v(-0.79, -0.46) * mm});
            skLineSegment(sketch, "E906", {"start": v(-0.79, -0.46) * mm, "end": v(-0.78, -0.46) * mm});
            skLineSegment(sketch, "E907", {"start": v(-0.78, -0.46) * mm, "end": v(-0.77, -0.46) * mm});
            skLineSegment(sketch, "E908", {"start": v(-0.77, -0.46) * mm, "end": v(-0.77, -0.46) * mm});
            skLineSegment(sketch, "E909", {"start": v(-0.77, -0.46) * mm, "end": v(-0.76, -0.46) * mm});
            skLineSegment(sketch, "E910", {"start": v(-0.76, -0.46) * mm, "end": v(-0.76, -0.46) * mm});
            skLineSegment(sketch, "E911", {"start": v(-0.76, -0.46) * mm, "end": v(-0.76, -0.47) * mm});
            skLineSegment(sketch, "E912", {"start": v(-0.76, -0.47) * mm, "end": v(-0.76, -0.48) * mm});
            skLineSegment(sketch, "E913", {"start": v(-0.76, -0.48) * mm, "end": v(-0.77, -0.48) * mm});
            skLineSegment(sketch, "E914", {"start": v(-0.77, -0.48) * mm, "end": v(-0.77, -0.48) * mm});
            skLineSegment(sketch, "E915", {"start": v(-0.77, -0.48) * mm, "end": v(-0.8, -0.48) * mm});
            skLineSegment(sketch, "E916", {"start": v(-0.8, -0.48) * mm, "end": v(-0.8, -0.48) * mm});
            skLineSegment(sketch, "E917", {"start": v(-0.8, -0.48) * mm, "end": v(-0.82, -0.46) * mm});
            skLineSegment(sketch, "E918", {"start": v(-0.82, -0.46) * mm, "end": v(-0.82, -0.46) * mm});
            skLineSegment(sketch, "E919", {"start": v(-0.82, -0.46) * mm, "end": v(-0.82, -0.45) * mm});
            skLineSegment(sketch, "E920", {"start": v(-0.82, -0.45) * mm, "end": v(-0.83, -0.43) * mm});
            skLineSegment(sketch, "E921", {"start": v(-0.83, -0.43) * mm, "end": v(-0.82, -0.42) * mm});
            skLineSegment(sketch, "E922", {"start": v(-0.82, -0.42) * mm, "end": v(-0.82, -0.42) * mm});
            skLineSegment(sketch, "E923", {"start": v(-0.82, -0.42) * mm, "end": v(-0.8, -0.4) * mm});
            skLineSegment(sketch, "E924", {"start": v(-0.8, -0.4) * mm, "end": v(-0.8, -0.4) * mm});
            skLineSegment(sketch, "E925", {"start": v(-0.8, -0.4) * mm, "end": v(-0.78, -0.4) * mm});
            skLineSegment(sketch, "E926", {"start": v(-0.78, -0.4) * mm, "end": v(-0.78, -0.4) * mm});
            skLineSegment(sketch, "E927", {"start": v(-0.78, -0.4) * mm, "end": v(-0.76, -0.4) * mm});
            skLineSegment(sketch, "E928", {"start": v(-0.76, -0.4) * mm, "end": v(-0.75, -0.4) * mm});
            skLineSegment(sketch, "E929", {"start": v(-0.75, -0.4) * mm, "end": v(-0.75, -0.4) * mm});
            skLineSegment(sketch, "E930", {"start": v(-0.75, -0.4) * mm, "end": v(-0.74, -0.41) * mm});
            skLineSegment(sketch, "E931", {"start": v(-0.74, -0.41) * mm, "end": v(-0.73, -0.41) * mm});
            skLineSegment(sketch, "E932", {"start": v(-0.73, -0.41) * mm, "end": v(-0.73, -0.41) * mm});
            skLineSegment(sketch, "E933", {"start": v(-0.73, -0.41) * mm, "end": v(-0.72, -0.42) * mm});
            skLineSegment(sketch, "E934", {"start": v(-0.72, -0.42) * mm, "end": v(-0.71, -0.42) * mm});
            skLineSegment(sketch, "E935", {"start": v(-0.71, -0.42) * mm, "end": v(-0.71, -0.42) * mm});
            skLineSegment(sketch, "E936", {"start": v(-0.71, -0.42) * mm, "end": v(-0.7, -0.42) * mm});
            skLineSegment(sketch, "E937", {"start": v(-0.7, -0.42) * mm, "end": v(-0.7, -0.42) * mm});
            skLineSegment(sketch, "E938", {"start": v(-0.7, -0.42) * mm, "end": v(-0.72, -0.37) * mm});
            skLineSegment(sketch, "E939", {"start": v(-0.72, -0.37) * mm, "end": v(-0.72, -0.37) * mm});
            skLineSegment(sketch, "E940", {"start": v(-0.72, -0.37) * mm, "end": v(-0.72, -0.36) * mm});
            skLineSegment(sketch, "E941", {"start": v(-0.72, -0.36) * mm, "end": v(-0.72, -0.36) * mm});
            skLineSegment(sketch, "E942", {"start": v(-0.72, -0.36) * mm, "end": v(-0.72, -0.35) * mm});
            skLineSegment(sketch, "E943", {"start": v(-0.72, -0.35) * mm, "end": v(-0.71, -0.35) * mm});
            skLineSegment(sketch, "E944", {"start": v(-0.71, -0.35) * mm, "end": v(-0.71, -0.35) * mm});
            skLineSegment(sketch, "E945", {"start": v(-0.71, -0.35) * mm, "end": v(-0.7, -0.35) * mm});
            skLineSegment(sketch, "E946", {"start": v(-0.7, -0.35) * mm, "end": v(-0.7, -0.35) * mm});
            skLineSegment(sketch, "E947", {"start": v(-0.7, -0.35) * mm, "end": v(-0.7, -0.36) * mm});
            skLineSegment(sketch, "E948", {"start": v(-0.7, -0.36) * mm, "end": v(-0.7, -0.36) * mm});
            skLineSegment(sketch, "E949", {"start": v(-0.7, -0.36) * mm, "end": v(-0.67, -0.42) * mm});
            skLineSegment(sketch, "E950", {"start": v(-0.67, -0.42) * mm, "end": v(-0.67, -0.42) * mm});
            skLineSegment(sketch, "E951", {"start": v(-0.67, -0.42) * mm, "end": v(-0.67, -0.43) * mm});
            skLineSegment(sketch, "E952", {"start": v(-0.67, -0.43) * mm, "end": v(-0.67, -0.43) * mm});
            skLineSegment(sketch, "E953", {"start": v(-0.67, -0.43) * mm, "end": v(-0.67, -0.44) * mm});
            skLineSegment(sketch, "E954", {"start": v(-0.67, -0.44) * mm, "end": v(-0.67, -0.44) * mm});
            skLineSegment(sketch, "E955", {"start": v(-0.71, -0.34) * mm, "end": v(-0.73, -0.35) * mm});
            skLineSegment(sketch, "E956", {"start": v(-0.73, -0.35) * mm, "end": v(-0.74, -0.35) * mm});
            skLineSegment(sketch, "E957", {"start": v(-0.74, -0.35) * mm, "end": v(-0.75, -0.35) * mm});
            skLineSegment(sketch, "E958", {"start": v(-0.75, -0.35) * mm, "end": v(-0.75, -0.35) * mm});
            skLineSegment(sketch, "E959", {"start": v(-0.75, -0.35) * mm, "end": v(-0.76, -0.35) * mm});
            skLineSegment(sketch, "E960", {"start": v(-0.76, -0.35) * mm, "end": v(-0.77, -0.34) * mm});
            skLineSegment(sketch, "E961", {"start": v(-0.77, -0.34) * mm, "end": v(-0.77, -0.34) * mm});
            skLineSegment(sketch, "E962", {"start": v(-0.77, -0.34) * mm, "end": v(-0.8, -0.33) * mm});
            skLineSegment(sketch, "E963", {"start": v(-0.8, -0.33) * mm, "end": v(-0.8, -0.33) * mm});
            skLineSegment(sketch, "E964", {"start": v(-0.8, -0.33) * mm, "end": v(-0.81, -0.32) * mm});
            skLineSegment(sketch, "E965", {"start": v(-0.81, -0.32) * mm, "end": v(-0.81, -0.32) * mm});
            skLineSegment(sketch, "E966", {"start": v(-0.81, -0.32) * mm, "end": v(-0.82, -0.31) * mm});
            skLineSegment(sketch, "E967", {"start": v(-0.82, -0.31) * mm, "end": v(-0.83, -0.31) * mm});
            skLineSegment(sketch, "E968", {"start": v(-0.83, -0.31) * mm, "end": v(-0.83, -0.31) * mm});
            skLineSegment(sketch, "E969", {"start": v(-0.83, -0.31) * mm, "end": v(-0.84, -0.32) * mm});
            skLineSegment(sketch, "E970", {"start": v(-0.84, -0.32) * mm, "end": v(-0.84, -0.32) * mm});
            skLineSegment(sketch, "E971", {"start": v(-0.84, -0.32) * mm, "end": v(-0.84, -0.34) * mm});
            skLineSegment(sketch, "E972", {"start": v(-0.84, -0.34) * mm, "end": v(-0.84, -0.34) * mm});
            skLineSegment(sketch, "E973", {"start": v(-0.84, -0.34) * mm, "end": v(-0.84, -0.35) * mm});
            skLineSegment(sketch, "E974", {"start": v(-0.84, -0.35) * mm, "end": v(-0.83, -0.35) * mm});
            skLineSegment(sketch, "E975", {"start": v(-0.83, -0.35) * mm, "end": v(-0.83, -0.35) * mm});
            skLineSegment(sketch, "E976", {"start": v(-0.83, -0.35) * mm, "end": v(-0.82, -0.35) * mm});
            skLineSegment(sketch, "E977", {"start": v(-0.82, -0.35) * mm, "end": v(-0.82, -0.35) * mm});
            skLineSegment(sketch, "E978", {"start": v(-0.82, -0.35) * mm, "end": v(-0.81, -0.35) * mm});
            skLineSegment(sketch, "E979", {"start": v(-0.81, -0.35) * mm, "end": v(-0.81, -0.35) * mm});
            skLineSegment(sketch, "E980", {"start": v(-0.81, -0.35) * mm, "end": v(-0.8, -0.36) * mm});
            skLineSegment(sketch, "E981", {"start": v(-0.8, -0.36) * mm, "end": v(-0.8, -0.36) * mm});
            skLineSegment(sketch, "E982", {"start": v(-0.8, -0.36) * mm, "end": v(-0.81, -0.38) * mm});
            skLineSegment(sketch, "E983", {"start": v(-0.81, -0.38) * mm, "end": v(-0.82, -0.38) * mm});
            skLineSegment(sketch, "E984", {"start": v(-0.82, -0.38) * mm, "end": v(-0.82, -0.38) * mm});
            skLineSegment(sketch, "E985", {"start": v(-0.82, -0.38) * mm, "end": v(-0.84, -0.37) * mm});
            skLineSegment(sketch, "E986", {"start": v(-0.84, -0.37) * mm, "end": v(-0.85, -0.37) * mm});
            skLineSegment(sketch, "E987", {"start": v(-0.85, -0.37) * mm, "end": v(-0.85, -0.37) * mm});
            skLineSegment(sketch, "E988", {"start": v(-0.85, -0.37) * mm, "end": v(-0.86, -0.35) * mm});
            skLineSegment(sketch, "E989", {"start": v(-0.86, -0.35) * mm, "end": v(-0.87, -0.35) * mm});
            skLineSegment(sketch, "E990", {"start": v(-0.87, -0.35) * mm, "end": v(-0.87, -0.34) * mm});
            skLineSegment(sketch, "E991", {"start": v(-0.87, -0.34) * mm, "end": v(-0.87, -0.31) * mm});
            skLineSegment(sketch, "E992", {"start": v(-0.87, -0.31) * mm, "end": v(-0.87, -0.31) * mm});
            skLineSegment(sketch, "E993", {"start": v(-0.87, -0.31) * mm, "end": v(-0.86, -0.3) * mm});
            skLineSegment(sketch, "E994", {"start": v(-0.86, -0.3) * mm, "end": v(-0.84, -0.29) * mm});
            skLineSegment(sketch, "E995", {"start": v(-0.84, -0.29) * mm, "end": v(-0.84, -0.29) * mm});
            skLineSegment(sketch, "E996", {"start": v(-0.84, -0.29) * mm, "end": v(-0.82, -0.29) * mm});
            skLineSegment(sketch, "E997", {"start": v(-0.82, -0.29) * mm, "end": v(-0.82, -0.29) * mm});
            skLineSegment(sketch, "E998", {"start": v(-0.82, -0.29) * mm, "end": v(-0.81, -0.29) * mm});
            skLineSegment(sketch, "E999", {"start": v(-0.81, -0.29) * mm, "end": v(-0.8, -0.3) * mm});
            skLineSegment(sketch, "E1000", {"start": v(-0.8, -0.3) * mm, "end": v(-0.8, -0.3) * mm});
            skLineSegment(sketch, "E1001", {"start": v(-0.8, -0.3) * mm, "end": v(-0.78, -0.31) * mm});
            skLineSegment(sketch, "E1002", {"start": v(-0.78, -0.31) * mm, "end": v(-0.77, -0.31) * mm});
            skLineSegment(sketch, "E1003", {"start": v(-0.77, -0.31) * mm, "end": v(-0.77, -0.31) * mm});
            skLineSegment(sketch, "E1004", {"start": v(-0.77, -0.31) * mm, "end": v(-0.76, -0.32) * mm});
            skLineSegment(sketch, "E1005", {"start": v(-0.76, -0.32) * mm, "end": v(-0.76, -0.32) * mm});
            skLineSegment(sketch, "E1006", {"start": v(-0.76, -0.32) * mm, "end": v(-0.75, -0.32) * mm});
            skLineSegment(sketch, "E1007", {"start": v(-0.75, -0.32) * mm, "end": v(-0.74, -0.33) * mm});
            skLineSegment(sketch, "E1008", {"start": v(-0.74, -0.33) * mm, "end": v(-0.74, -0.33) * mm});
            skLineSegment(sketch, "E1009", {"start": v(-0.74, -0.33) * mm, "end": v(-0.74, -0.32) * mm});
            skLineSegment(sketch, "E1010", {"start": v(-0.74, -0.32) * mm, "end": v(-0.76, -0.27) * mm});
            skLineSegment(sketch, "E1011", {"start": v(-0.76, -0.27) * mm, "end": v(-0.76, -0.27) * mm});
            skLineSegment(sketch, "E1012", {"start": v(-0.76, -0.27) * mm, "end": v(-0.75, -0.26) * mm});
            skLineSegment(sketch, "E1013", {"start": v(-0.75, -0.26) * mm, "end": v(-0.75, -0.26) * mm});
            skLineSegment(sketch, "E1014", {"start": v(-0.75, -0.26) * mm, "end": v(-0.74, -0.26) * mm});
            skLineSegment(sketch, "E1015", {"start": v(-0.74, -0.26) * mm, "end": v(-0.74, -0.26) * mm});
            skLineSegment(sketch, "E1016", {"start": v(-0.74, -0.26) * mm, "end": v(-0.73, -0.26) * mm});
            skLineSegment(sketch, "E1017", {"start": v(-0.73, -0.26) * mm, "end": v(-0.73, -0.26) * mm});
            skLineSegment(sketch, "E1018", {"start": v(-0.73, -0.26) * mm, "end": v(-0.71, -0.33) * mm});
            skLineSegment(sketch, "E1019", {"start": v(-0.71, -0.33) * mm, "end": v(-0.71, -0.33) * mm});
            skLineSegment(sketch, "E1020", {"start": v(-0.71, -0.33) * mm, "end": v(-0.71, -0.34) * mm});
            skLineSegment(sketch, "E1021", {"start": v(-0.71, -0.34) * mm, "end": v(-0.71, -0.34) * mm});
            skLineSegment(sketch, "E1022", {"start": v(-0.77, -0.26) * mm, "end": v(-0.77, -0.26) * mm});
            skLineSegment(sketch, "E1023", {"start": v(-0.77, -0.26) * mm, "end": v(-0.78, -0.25) * mm});
            skLineSegment(sketch, "E1024", {"start": v(-0.78, -0.25) * mm, "end": v(-0.78, -0.25) * mm});
            skLineSegment(sketch, "E1025", {"start": v(-0.78, -0.25) * mm, "end": v(-0.79, -0.25) * mm});
            skLineSegment(sketch, "E1026", {"start": v(-0.79, -0.25) * mm, "end": v(-0.79, -0.24) * mm});
            skLineSegment(sketch, "E1027", {"start": v(-0.79, -0.24) * mm, "end": v(-0.79, -0.24) * mm});
            skLineSegment(sketch, "E1028", {"start": v(-0.79, -0.24) * mm, "end": v(-0.79, -0.23) * mm});
            skLineSegment(sketch, "E1029", {"start": v(-0.79, -0.23) * mm, "end": v(-0.79, -0.23) * mm});
            skLineSegment(sketch, "E1030", {"start": v(-0.79, -0.23) * mm, "end": v(-0.78, -0.23) * mm});
            skLineSegment(sketch, "E1031", {"start": v(-0.78, -0.23) * mm, "end": v(-0.78, -0.23) * mm});
            skLineSegment(sketch, "E1032", {"start": v(-0.78, -0.23) * mm, "end": v(-0.77, -0.22) * mm});
            skLineSegment(sketch, "E1033", {"start": v(-0.77, -0.22) * mm, "end": v(-0.77, -0.22) * mm});
            skLineSegment(sketch, "E1034", {"start": v(-0.77, -0.22) * mm, "end": v(-0.77, -0.2) * mm});
            skLineSegment(sketch, "E1035", {"start": v(-0.77, -0.2) * mm, "end": v(-0.77, -0.2) * mm});
            skLineSegment(sketch, "E1036", {"start": v(-0.77, -0.2) * mm, "end": v(-0.78, -0.2) * mm});
            skLineSegment(sketch, "E1037", {"start": v(-0.78, -0.2) * mm, "end": v(-0.8, -0.19) * mm});
            skLineSegment(sketch, "E1038", {"start": v(-0.8, -0.19) * mm, "end": v(-0.8, -0.19) * mm});
            skLineSegment(sketch, "E1039", {"start": v(-0.8, -0.19) * mm, "end": v(-0.81, -0.2) * mm});
            skLineSegment(sketch, "E1040", {"start": v(-0.81, -0.2) * mm, "end": v(-0.82, -0.2) * mm});
            skLineSegment(sketch, "E1041", {"start": v(-0.82, -0.2) * mm, "end": v(-0.82, -0.2) * mm});
            skLineSegment(sketch, "E1042", {"start": v(-0.82, -0.2) * mm, "end": v(-0.82, -0.21) * mm});
            skLineSegment(sketch, "E1043", {"start": v(-0.82, -0.21) * mm, "end": v(-0.82, -0.21) * mm});
            skLineSegment(sketch, "E1044", {"start": v(-0.82, -0.21) * mm, "end": v(-0.81, -0.24) * mm});
            skLineSegment(sketch, "E1045", {"start": v(-0.81, -0.24) * mm, "end": v(-0.81, -0.25) * mm});
            skLineSegment(sketch, "E1046", {"start": v(-0.81, -0.25) * mm, "end": v(-0.81, -0.25) * mm});
            skLineSegment(sketch, "E1047", {"start": v(-0.81, -0.25) * mm, "end": v(-0.82, -0.26) * mm});
            skLineSegment(sketch, "E1048", {"start": v(-0.82, -0.26) * mm, "end": v(-0.82, -0.26) * mm});
            skLineSegment(sketch, "E1049", {"start": v(-0.82, -0.26) * mm, "end": v(-0.83, -0.26) * mm});
            skLineSegment(sketch, "E1050", {"start": v(-0.83, -0.26) * mm, "end": v(-0.83, -0.26) * mm});
            skLineSegment(sketch, "E1051", {"start": v(-0.83, -0.26) * mm, "end": v(-0.88, -0.26) * mm});
            skLineSegment(sketch, "E1052", {"start": v(-0.88, -0.26) * mm, "end": v(-0.88, -0.26) * mm});
            skLineSegment(sketch, "E1053", {"start": v(-0.88, -0.26) * mm, "end": v(-0.9, -0.26) * mm});
            skLineSegment(sketch, "E1054", {"start": v(-0.9, -0.26) * mm, "end": v(-0.9, -0.26) * mm});
            skLineSegment(sketch, "E1055", {"start": v(-0.9, -0.26) * mm, "end": v(-0.9, -0.2) * mm});
            skLineSegment(sketch, "E1056", {"start": v(-0.9, -0.2) * mm, "end": v(-0.9, -0.2) * mm});
            skLineSegment(sketch, "E1057", {"start": v(-0.9, -0.2) * mm, "end": v(-0.9, -0.19) * mm});
            skLineSegment(sketch, "E1058", {"start": v(-0.9, -0.19) * mm, "end": v(-0.9, -0.19) * mm});
            skLineSegment(sketch, "E1059", {"start": v(-0.9, -0.19) * mm, "end": v(-0.88, -0.19) * mm});
            skLineSegment(sketch, "E1060", {"start": v(-0.88, -0.19) * mm, "end": v(-0.88, -0.19) * mm});
            skLineSegment(sketch, "E1061", {"start": v(-0.88, -0.19) * mm, "end": v(-0.88, -0.2) * mm});
            skLineSegment(sketch, "E1062", {"start": v(-0.88, -0.2) * mm, "end": v(-0.88, -0.2) * mm});
            skLineSegment(sketch, "E1063", {"start": v(-0.88, -0.2) * mm, "end": v(-0.87, -0.24) * mm});
            skLineSegment(sketch, "E1064", {"start": v(-0.87, -0.24) * mm, "end": v(-0.84, -0.23) * mm});
            skLineSegment(sketch, "E1065", {"start": v(-0.84, -0.23) * mm, "end": v(-0.84, -0.22) * mm});
            skLineSegment(sketch, "E1066", {"start": v(-0.84, -0.22) * mm, "end": v(-0.84, -0.22) * mm});
            skLineSegment(sketch, "E1067", {"start": v(-0.84, -0.22) * mm, "end": v(-0.84, -0.18) * mm});
            skLineSegment(sketch, "E1068", {"start": v(-0.84, -0.18) * mm, "end": v(-0.84, -0.18) * mm});
            skLineSegment(sketch, "E1069", {"start": v(-0.84, -0.18) * mm, "end": v(-0.83, -0.18) * mm});
            skLineSegment(sketch, "E1070", {"start": v(-0.83, -0.18) * mm, "end": v(-0.8, -0.16) * mm});
            skLineSegment(sketch, "E1071", {"start": v(-0.8, -0.16) * mm, "end": v(-0.8, -0.16) * mm});
            skLineSegment(sketch, "E1072", {"start": v(-0.8, -0.16) * mm, "end": v(-0.77, -0.17) * mm});
            skLineSegment(sketch, "E1073", {"start": v(-0.77, -0.17) * mm, "end": v(-0.76, -0.17) * mm});
            skLineSegment(sketch, "E1074", {"start": v(-0.76, -0.17) * mm, "end": v(-0.76, -0.17) * mm});
            skLineSegment(sketch, "E1075", {"start": v(-0.76, -0.17) * mm, "end": v(-0.75, -0.2) * mm});
            skLineSegment(sketch, "E1076", {"start": v(-0.75, -0.2) * mm, "end": v(-0.75, -0.2) * mm});
            skLineSegment(sketch, "E1077", {"start": v(-0.75, -0.2) * mm, "end": v(-0.74, -0.2) * mm});
            skLineSegment(sketch, "E1078", {"start": v(-0.74, -0.2) * mm, "end": v(-0.75, -0.23) * mm});
            skLineSegment(sketch, "E1079", {"start": v(-0.75, -0.23) * mm, "end": v(-0.75, -0.24) * mm});
            skLineSegment(sketch, "E1080", {"start": v(-0.75, -0.24) * mm, "end": v(-0.75, -0.24) * mm});
            skLineSegment(sketch, "E1081", {"start": v(-0.75, -0.24) * mm, "end": v(-0.77, -0.26) * mm});
            skLineSegment(sketch, "E1082", {"start": v(-0.8, -0.08) * mm, "end": v(-0.8, -0.08) * mm});
            skLineSegment(sketch, "E1083", {"start": v(-0.8, -0.08) * mm, "end": v(-0.79, -0.07) * mm});
            skLineSegment(sketch, "E1084", {"start": v(-0.79, -0.07) * mm, "end": v(-0.78, -0.06) * mm});
            skLineSegment(sketch, "E1085", {"start": v(-0.78, -0.06) * mm, "end": v(-0.78, -0.06) * mm});
            skLineSegment(sketch, "E1086", {"start": v(-0.78, -0.06) * mm, "end": v(-0.78, -0.05) * mm});
            skLineSegment(sketch, "E1087", {"start": v(-0.78, -0.05) * mm, "end": v(-0.79, -0.04) * mm});
            skLineSegment(sketch, "E1088", {"start": v(-0.79, -0.04) * mm, "end": v(-0.8, -0.04) * mm});
            skLineSegment(sketch, "E1089", {"start": v(-0.8, -0.04) * mm, "end": v(-0.8, -0.04) * mm});
            skLineSegment(sketch, "E1090", {"start": v(-0.8, -0.04) * mm, "end": v(-0.81, -0.04) * mm});
            skLineSegment(sketch, "E1091", {"start": v(-0.81, -0.04) * mm, "end": v(-0.81, -0.04) * mm});
            skLineSegment(sketch, "E1092", {"start": v(-0.81, -0.04) * mm, "end": v(-0.83, -0.04) * mm});
            skLineSegment(sketch, "E1093", {"start": v(-0.83, -0.04) * mm, "end": v(-0.83, -0.05) * mm});
            skLineSegment(sketch, "E1094", {"start": v(-0.83, -0.05) * mm, "end": v(-0.83, -0.06) * mm});
            skLineSegment(sketch, "E1095", {"start": v(-0.83, -0.06) * mm, "end": v(-0.83, -0.06) * mm});
            skLineSegment(sketch, "E1096", {"start": v(-0.83, -0.06) * mm, "end": v(-0.83, -0.07) * mm});
            skLineSegment(sketch, "E1097", {"start": v(-0.83, -0.07) * mm, "end": v(-0.81, -0.08) * mm});
            skLineSegment(sketch, "E1098", {"start": v(-0.81, -0.08) * mm, "end": v(-0.8, -0.08) * mm});
            skLineSegment(sketch, "E1099", {"start": v(-0.9, -0.06) * mm, "end": v(-0.9, -0.06) * mm});
            skLineSegment(sketch, "E1100", {"start": v(-0.9, -0.06) * mm, "end": v(-0.89, -0.07) * mm});
            skLineSegment(sketch, "E1101", {"start": v(-0.89, -0.07) * mm, "end": v(-0.88, -0.08) * mm});
            skLineSegment(sketch, "E1102", {"start": v(-0.88, -0.08) * mm, "end": v(-0.87, -0.08) * mm});
            skLineSegment(sketch, "E1103", {"start": v(-0.87, -0.08) * mm, "end": v(-0.87, -0.08) * mm});
            skLineSegment(sketch, "E1104", {"start": v(-0.87, -0.08) * mm, "end": v(-0.86, -0.07) * mm});
            skLineSegment(sketch, "E1105", {"start": v(-0.86, -0.07) * mm, "end": v(-0.85, -0.06) * mm});
            skLineSegment(sketch, "E1106", {"start": v(-0.85, -0.06) * mm, "end": v(-0.85, -0.06) * mm});
            skLineSegment(sketch, "E1107", {"start": v(-0.85, -0.06) * mm, "end": v(-0.86, -0.05) * mm});
            skLineSegment(sketch, "E1108", {"start": v(-0.86, -0.05) * mm, "end": v(-0.87, -0.04) * mm});
            skLineSegment(sketch, "E1109", {"start": v(-0.87, -0.04) * mm, "end": v(-0.87, -0.04) * mm});
            skLineSegment(sketch, "E1110", {"start": v(-0.87, -0.04) * mm, "end": v(-0.88, -0.04) * mm});
            skLineSegment(sketch, "E1111", {"start": v(-0.88, -0.04) * mm, "end": v(-0.89, -0.05) * mm});
            skLineSegment(sketch, "E1112", {"start": v(-0.89, -0.05) * mm, "end": v(-0.9, -0.06) * mm});
            skLineSegment(sketch, "E1113", {"start": v(-0.8, -0.1) * mm, "end": v(-0.8, -0.1) * mm});
            skLineSegment(sketch, "E1114", {"start": v(-0.8, -0.1) * mm, "end": v(-0.83, -0.1) * mm});
            skLineSegment(sketch, "E1115", {"start": v(-0.83, -0.1) * mm, "end": v(-0.84, -0.09) * mm});
            skLineSegment(sketch, "E1116", {"start": v(-0.84, -0.09) * mm, "end": v(-0.84, -0.08) * mm});
            skLineSegment(sketch, "E1117", {"start": v(-0.84, -0.08) * mm, "end": v(-0.85, -0.09) * mm});
            skLineSegment(sketch, "E1118", {"start": v(-0.85, -0.09) * mm, "end": v(-0.86, -0.1) * mm});
            skLineSegment(sketch, "E1119", {"start": v(-0.86, -0.1) * mm, "end": v(-0.87, -0.1) * mm});
            skLineSegment(sketch, "E1120", {"start": v(-0.87, -0.1) * mm, "end": v(-0.88, -0.1) * mm});
            skLineSegment(sketch, "E1121", {"start": v(-0.88, -0.1) * mm, "end": v(-0.88, -0.1) * mm});
            skLineSegment(sketch, "E1122", {"start": v(-0.88, -0.1) * mm, "end": v(-0.9, -0.1) * mm});
            skLineSegment(sketch, "E1123", {"start": v(-0.9, -0.1) * mm, "end": v(-0.9, -0.1) * mm});
            skLineSegment(sketch, "E1124", {"start": v(-0.9, -0.1) * mm, "end": v(-0.9, -0.09) * mm});
            skLineSegment(sketch, "E1125", {"start": v(-0.9, -0.09) * mm, "end": v(-0.91, -0.06) * mm});
            skLineSegment(sketch, "E1126", {"start": v(-0.91, -0.06) * mm, "end": v(-0.91, -0.06) * mm});
            skLineSegment(sketch, "E1127", {"start": v(-0.91, -0.06) * mm, "end": v(-0.9, -0.03) * mm});
            skLineSegment(sketch, "E1128", {"start": v(-0.9, -0.03) * mm, "end": v(-0.9, -0.03) * mm});
            skLineSegment(sketch, "E1129", {"start": v(-0.9, -0.03) * mm, "end": v(-0.9, -0.02) * mm});
            skLineSegment(sketch, "E1130", {"start": v(-0.9, -0.02) * mm, "end": v(-0.88, -0.01) * mm});
            skLineSegment(sketch, "E1131", {"start": v(-0.88, -0.01) * mm, "end": v(-0.88, -0.01) * mm});
            skLineSegment(sketch, "E1132", {"start": v(-0.88, -0.01) * mm, "end": v(-0.87, -0.01) * mm});
            skLineSegment(sketch, "E1133", {"start": v(-0.87, -0.01) * mm, "end": v(-0.86, -0.02) * mm});
            skLineSegment(sketch, "E1134", {"start": v(-0.86, -0.02) * mm, "end": v(-0.85, -0.03) * mm});
            skLineSegment(sketch, "E1135", {"start": v(-0.85, -0.03) * mm, "end": v(-0.84, -0.03) * mm});
            skLineSegment(sketch, "E1136", {"start": v(-0.84, -0.03) * mm, "end": v(-0.84, -0.03) * mm});
            skLineSegment(sketch, "E1137", {"start": v(-0.84, -0.03) * mm, "end": v(-0.83, -0.02) * mm});
            skLineSegment(sketch, "E1138", {"start": v(-0.83, -0.02) * mm, "end": v(-0.81, 0) * mm});
            skLineSegment(sketch, "E1139", {"start": v(-0.81, 0) * mm, "end": v(-0.8, 0) * mm});
            skLineSegment(sketch, "E1140", {"start": v(-0.8, 0) * mm, "end": v(-0.8, 0) * mm});
            skLineSegment(sketch, "E1141", {"start": v(-0.8, 0) * mm, "end": v(-0.77, -0.02) * mm});
            skLineSegment(sketch, "E1142", {"start": v(-0.77, -0.02) * mm, "end": v(-0.77, -0.02) * mm});
            skLineSegment(sketch, "E1143", {"start": v(-0.77, -0.02) * mm, "end": v(-0.76, -0.05) * mm});
            skLineSegment(sketch, "E1144", {"start": v(-0.76, -0.05) * mm, "end": v(-0.76, -0.06) * mm});
            skLineSegment(sketch, "E1145", {"start": v(-0.76, -0.06) * mm, "end": v(-0.76, -0.06) * mm});
            skLineSegment(sketch, "E1146", {"start": v(-0.76, -0.06) * mm, "end": v(-0.77, -0.1) * mm});
            skLineSegment(sketch, "E1147", {"start": v(-0.77, -0.1) * mm, "end": v(-0.77, -0.1) * mm});
            skLineSegment(sketch, "E1148", {"start": v(-0.77, -0.1) * mm, "end": v(-0.8, -0.1) * mm});
            skLineSegment(sketch, "E1149", {"start": v(-0.87, 0.01) * mm, "end": v(-0.9, 0.01) * mm});
            skLineSegment(sketch, "E1150", {"start": v(-0.9, 0.01) * mm, "end": v(-0.9, 0.01) * mm});
            skLineSegment(sketch, "E1151", {"start": v(-0.9, 0.01) * mm, "end": v(-0.9, 0.02) * mm});
            skLineSegment(sketch, "E1152", {"start": v(-0.9, 0.02) * mm, "end": v(-0.9, 0.02) * mm});
            skLineSegment(sketch, "E1153", {"start": v(-0.9, 0.02) * mm, "end": v(-0.91, 0.02) * mm});
            skLineSegment(sketch, "E1154", {"start": v(-0.91, 0.02) * mm, "end": v(-0.91, 0.03) * mm});
            skLineSegment(sketch, "E1155", {"start": v(-0.91, 0.03) * mm, "end": v(-0.91, 0.03) * mm});
            skLineSegment(sketch, "E1156", {"start": v(-0.91, 0.03) * mm, "end": v(-0.9, 0.1) * mm});
            skLineSegment(sketch, "E1157", {"start": v(-0.9, 0.1) * mm, "end": v(-0.9, 0.1) * mm});
            skLineSegment(sketch, "E1158", {"start": v(-0.9, 0.1) * mm, "end": v(-0.9, 0.11) * mm});
            skLineSegment(sketch, "E1159", {"start": v(-0.9, 0.11) * mm, "end": v(-0.9, 0.11) * mm});
            skLineSegment(sketch, "E1160", {"start": v(-0.9, 0.11) * mm, "end": v(-0.87, 0.1) * mm});
            skLineSegment(sketch, "E1161", {"start": v(-0.87, 0.1) * mm, "end": v(-0.87, 0.1) * mm});
            skLineSegment(sketch, "E1162", {"start": v(-0.87, 0.1) * mm, "end": v(-0.86, 0.1) * mm});
            skLineSegment(sketch, "E1163", {"start": v(-0.86, 0.1) * mm, "end": v(-0.85, 0.1) * mm});
            skLineSegment(sketch, "E1164", {"start": v(-0.85, 0.1) * mm, "end": v(-0.76, 0.04) * mm});
            skLineSegment(sketch, "E1165", {"start": v(-0.76, 0.04) * mm, "end": v(-0.76, 0.04) * mm});
            skLineSegment(sketch, "E1166", {"start": v(-0.76, 0.04) * mm, "end": v(-0.76, 0.03) * mm});
            skLineSegment(sketch, "E1167", {"start": v(-0.76, 0.03) * mm, "end": v(-0.76, 0.03) * mm});
            skLineSegment(sketch, "E1168", {"start": v(-0.76, 0.03) * mm, "end": v(-0.76, 0.02) * mm});
            skLineSegment(sketch, "E1169", {"start": v(-0.76, 0.02) * mm, "end": v(-0.76, 0.02) * mm});
            skLineSegment(sketch, "E1170", {"start": v(-0.76, 0.02) * mm, "end": v(-0.77, 0.01) * mm});
            skLineSegment(sketch, "E1171", {"start": v(-0.77, 0.01) * mm, "end": v(-0.77, 0.01) * mm});
            skLineSegment(sketch, "E1172", {"start": v(-0.77, 0.01) * mm, "end": v(-0.78, 0.02) * mm});
            skLineSegment(sketch, "E1173", {"start": v(-0.78, 0.02) * mm, "end": v(-0.78, 0.02) * mm});
            skLineSegment(sketch, "E1174", {"start": v(-0.78, 0.02) * mm, "end": v(-0.87, 0.08) * mm});
            skLineSegment(sketch, "E1175", {"start": v(-0.87, 0.08) * mm, "end": v(-0.88, 0.08) * mm});
            skLineSegment(sketch, "E1176", {"start": v(-0.88, 0.08) * mm, "end": v(-0.89, 0.04) * mm});
            skLineSegment(sketch, "E1177", {"start": v(-0.89, 0.04) * mm, "end": v(-0.87, 0.04) * mm});
            skLineSegment(sketch, "E1178", {"start": v(-0.87, 0.04) * mm, "end": v(-0.87, 0.04) * mm});
            skLineSegment(sketch, "E1179", {"start": v(-0.87, 0.04) * mm, "end": v(-0.86, 0.03) * mm});
            skLineSegment(sketch, "E1180", {"start": v(-0.86, 0.03) * mm, "end": v(-0.86, 0.03) * mm});
            skLineSegment(sketch, "E1181", {"start": v(-0.86, 0.03) * mm, "end": v(-0.86, 0.02) * mm});
            skLineSegment(sketch, "E1182", {"start": v(-0.86, 0.02) * mm, "end": v(-0.86, 0.02) * mm});
            skLineSegment(sketch, "E1183", {"start": v(-0.86, 0.02) * mm, "end": v(-0.87, 0.01) * mm});
            skLineSegment(sketch, "E1184", {"start": v(-0.87, 0.01) * mm, "end": v(-0.87, 0.01) * mm});
            skLineSegment(sketch, "E1185", {"start": v(-0.86, 0.17) * mm, "end": v(-0.86, 0.17) * mm});
            skLineSegment(sketch, "E1186", {"start": v(-0.86, 0.17) * mm, "end": v(-0.87, 0.17) * mm});
            skLineSegment(sketch, "E1187", {"start": v(-0.87, 0.17) * mm, "end": v(-0.87, 0.17) * mm});
            skLineSegment(sketch, "E1188", {"start": v(-0.87, 0.17) * mm, "end": v(-0.88, 0.2) * mm});
            skLineSegment(sketch, "E1189", {"start": v(-0.88, 0.2) * mm, "end": v(-0.88, 0.2) * mm});
            skLineSegment(sketch, "E1190", {"start": v(-0.88, 0.2) * mm, "end": v(-0.87, 0.21) * mm});
            skLineSegment(sketch, "E1191", {"start": v(-0.87, 0.21) * mm, "end": v(-0.87, 0.21) * mm});
            skLineSegment(sketch, "E1192", {"start": v(-0.87, 0.21) * mm, "end": v(-0.87, 0.22) * mm});
            skLineSegment(sketch, "E1193", {"start": v(-0.87, 0.22) * mm, "end": v(-0.87, 0.22) * mm});
            skLineSegment(sketch, "E1194", {"start": v(-0.87, 0.22) * mm, "end": v(-0.74, 0.18) * mm});
            skLineSegment(sketch, "E1195", {"start": v(-0.74, 0.18) * mm, "end": v(-0.74, 0.18) * mm});
            skLineSegment(sketch, "E1196", {"start": v(-0.74, 0.18) * mm, "end": v(-0.73, 0.18) * mm});
            skLineSegment(sketch, "E1197", {"start": v(-0.73, 0.18) * mm, "end": v(-0.73, 0.18) * mm});
            skLineSegment(sketch, "E1198", {"start": v(-0.73, 0.18) * mm, "end": v(-0.73, 0.17) * mm});
            skLineSegment(sketch, "E1199", {"start": v(-0.73, 0.17) * mm, "end": v(-0.73, 0.17) * mm});
            skLineSegment(sketch, "E1200", {"start": v(-0.73, 0.17) * mm, "end": v(-0.73, 0.16) * mm});
            skLineSegment(sketch, "E1201", {"start": v(-0.73, 0.16) * mm, "end": v(-0.74, 0.16) * mm});
            skLineSegment(sketch, "E1202", {"start": v(-0.74, 0.16) * mm, "end": v(-0.74, 0.16) * mm});
            skLineSegment(sketch, "E1203", {"start": v(-0.74, 0.16) * mm, "end": v(-0.74, 0.15) * mm});
            skLineSegment(sketch, "E1204", {"start": v(-0.74, 0.15) * mm, "end": v(-0.74, 0.15) * mm});
            skLineSegment(sketch, "E1205", {"start": v(-0.74, 0.15) * mm, "end": v(-0.85, 0.18) * mm});
            skLineSegment(sketch, "E1206", {"start": v(-0.85, 0.18) * mm, "end": v(-0.85, 0.18) * mm});
            skLineSegment(sketch, "E1207", {"start": v(-0.85, 0.18) * mm, "end": v(-0.85, 0.17) * mm});
            skLineSegment(sketch, "E1208", {"start": v(-0.85, 0.17) * mm, "end": v(-0.85, 0.17) * mm});
            skLineSegment(sketch, "E1209", {"start": v(-0.85, 0.17) * mm, "end": v(-0.86, 0.16) * mm});
            skLineSegment(sketch, "E1210", {"start": v(-0.86, 0.16) * mm, "end": v(-0.86, 0.17) * mm});
            skLineSegment(sketch, "E1211", {"start": v(-0.77, 0.2) * mm, "end": v(-0.77, 0.2) * mm});
            skLineSegment(sketch, "E1212", {"start": v(-0.77, 0.2) * mm, "end": v(-0.84, 0.29) * mm});
            skLineSegment(sketch, "E1213", {"start": v(-0.84, 0.29) * mm, "end": v(-0.85, 0.29) * mm});
            skLineSegment(sketch, "E1214", {"start": v(-0.85, 0.29) * mm, "end": v(-0.85, 0.3) * mm});
            skLineSegment(sketch, "E1215", {"start": v(-0.85, 0.3) * mm, "end": v(-0.85, 0.3) * mm});
            skLineSegment(sketch, "E1216", {"start": v(-0.85, 0.3) * mm, "end": v(-0.84, 0.3) * mm});
            skLineSegment(sketch, "E1217", {"start": v(-0.84, 0.3) * mm, "end": v(-0.84, 0.3) * mm});
            skLineSegment(sketch, "E1218", {"start": v(-0.84, 0.3) * mm, "end": v(-0.83, 0.3) * mm});
            skLineSegment(sketch, "E1219", {"start": v(-0.83, 0.3) * mm, "end": v(-0.83, 0.3) * mm});
            skLineSegment(sketch, "E1220", {"start": v(-0.83, 0.3) * mm, "end": v(-0.77, 0.24) * mm});
            skLineSegment(sketch, "E1221", {"start": v(-0.77, 0.24) * mm, "end": v(-0.76, 0.26) * mm});
            skLineSegment(sketch, "E1222", {"start": v(-0.76, 0.26) * mm, "end": v(-0.78, 0.27) * mm});
            skLineSegment(sketch, "E1223", {"start": v(-0.78, 0.27) * mm, "end": v(-0.78, 0.27) * mm});
            skLineSegment(sketch, "E1224", {"start": v(-0.78, 0.27) * mm, "end": v(-0.79, 0.28) * mm});
            skLineSegment(sketch, "E1225", {"start": v(-0.79, 0.28) * mm, "end": v(-0.79, 0.28) * mm});
            skLineSegment(sketch, "E1226", {"start": v(-0.79, 0.28) * mm, "end": v(-0.79, 0.29) * mm});
            skLineSegment(sketch, "E1227", {"start": v(-0.79, 0.29) * mm, "end": v(-0.79, 0.29) * mm});
            skLineSegment(sketch, "E1228", {"start": v(-0.79, 0.29) * mm, "end": v(-0.78, 0.3) * mm});
            skLineSegment(sketch, "E1229", {"start": v(-0.78, 0.3) * mm, "end": v(-0.78, 0.3) * mm});
            skLineSegment(sketch, "E1230", {"start": v(-0.78, 0.3) * mm, "end": v(-0.77, 0.3) * mm});
            skLineSegment(sketch, "E1231", {"start": v(-0.77, 0.3) * mm, "end": v(-0.77, 0.3) * mm});
            skLineSegment(sketch, "E1232", {"start": v(-0.77, 0.3) * mm, "end": v(-0.75, 0.29) * mm});
            skLineSegment(sketch, "E1233", {"start": v(-0.75, 0.29) * mm, "end": v(-0.75, 0.3) * mm});
            skLineSegment(sketch, "E1234", {"start": v(-0.75, 0.3) * mm, "end": v(-0.75, 0.3) * mm});
            skLineSegment(sketch, "E1235", {"start": v(-0.75, 0.3) * mm, "end": v(-0.74, 0.3) * mm});
            skLineSegment(sketch, "E1236", {"start": v(-0.74, 0.3) * mm, "end": v(-0.74, 0.3) * mm});
            skLineSegment(sketch, "E1237", {"start": v(-0.74, 0.3) * mm, "end": v(-0.73, 0.3) * mm});
            skLineSegment(sketch, "E1238", {"start": v(-0.73, 0.3) * mm, "end": v(-0.73, 0.3) * mm});
            skLineSegment(sketch, "E1239", {"start": v(-0.73, 0.3) * mm, "end": v(-0.72, 0.29) * mm});
            skLineSegment(sketch, "E1240", {"start": v(-0.72, 0.29) * mm, "end": v(-0.73, 0.29) * mm});
            skLineSegment(sketch, "E1241", {"start": v(-0.73, 0.29) * mm, "end": v(-0.73, 0.28) * mm});
            skLineSegment(sketch, "E1242", {"start": v(-0.73, 0.28) * mm, "end": v(-0.7, 0.27) * mm});
            skLineSegment(sketch, "E1243", {"start": v(-0.7, 0.27) * mm, "end": v(-0.7, 0.27) * mm});
            skLineSegment(sketch, "E1244", {"start": v(-0.7, 0.27) * mm, "end": v(-0.7, 0.26) * mm});
            skLineSegment(sketch, "E1245", {"start": v(-0.7, 0.26) * mm, "end": v(-0.7, 0.26) * mm});
            skLineSegment(sketch, "E1246", {"start": v(-0.7, 0.26) * mm, "end": v(-0.7, 0.25) * mm});
            skLineSegment(sketch, "E1247", {"start": v(-0.7, 0.25) * mm, "end": v(-0.7, 0.25) * mm});
            skLineSegment(sketch, "E1248", {"start": v(-0.7, 0.25) * mm, "end": v(-0.71, 0.24) * mm});
            skLineSegment(sketch, "E1249", {"start": v(-0.71, 0.24) * mm, "end": v(-0.71, 0.24) * mm});
            skLineSegment(sketch, "E1250", {"start": v(-0.71, 0.24) * mm, "end": v(-0.74, 0.25) * mm});
            skLineSegment(sketch, "E1251", {"start": v(-0.74, 0.25) * mm, "end": v(-0.76, 0.2) * mm});
            skLineSegment(sketch, "E1252", {"start": v(-0.76, 0.2) * mm, "end": v(-0.76, 0.2) * mm});
            skLineSegment(sketch, "E1253", {"start": v(-0.76, 0.2) * mm, "end": v(-0.77, 0.2) * mm});
            skLineSegment(sketch, "E1254", {"start": v(-0.71, 0.35) * mm, "end": v(-0.71, 0.35) * mm});
            skLineSegment(sketch, "E1255", {"start": v(-0.71, 0.35) * mm, "end": v(-0.72, 0.35) * mm});
            skLineSegment(sketch, "E1256", {"start": v(-0.72, 0.35) * mm, "end": v(-0.72, 0.35) * mm});
            skLineSegment(sketch, "E1257", {"start": v(-0.72, 0.35) * mm, "end": v(-0.72, 0.36) * mm});
            skLineSegment(sketch, "E1258", {"start": v(-0.72, 0.36) * mm, "end": v(-0.72, 0.36) * mm});
            skLineSegment(sketch, "E1259", {"start": v(-0.72, 0.36) * mm, "end": v(-0.69, 0.4) * mm});
            skLineSegment(sketch, "E1260", {"start": v(-0.69, 0.4) * mm, "end": v(-0.69, 0.4) * mm});
            skLineSegment(sketch, "E1261", {"start": v(-0.69, 0.4) * mm, "end": v(-0.68, 0.41) * mm});
            skLineSegment(sketch, "E1262", {"start": v(-0.68, 0.41) * mm, "end": v(-0.68, 0.41) * mm});
            skLineSegment(sketch, "E1263", {"start": v(-0.68, 0.41) * mm, "end": v(-0.68, 0.4) * mm});
            skLineSegment(sketch, "E1264", {"start": v(-0.68, 0.4) * mm, "end": v(-0.68, 0.4) * mm});
            skLineSegment(sketch, "E1265", {"start": v(-0.68, 0.4) * mm, "end": v(-0.67, 0.4) * mm});
            skLineSegment(sketch, "E1266", {"start": v(-0.67, 0.4) * mm, "end": v(-0.67, 0.4) * mm});
            skLineSegment(sketch, "E1267", {"start": v(-0.67, 0.4) * mm, "end": v(-0.7, 0.35) * mm});
            skLineSegment(sketch, "E1268", {"start": v(-0.7, 0.35) * mm, "end": v(-0.7, 0.35) * mm});
            skLineSegment(sketch, "E1269", {"start": v(-0.7, 0.35) * mm, "end": v(-0.71, 0.35) * mm});
            skLineSegment(sketch, "E1270", {"start": v(-0.6, 0.44) * mm, "end": v(-0.7, 0.52) * mm});
            skLineSegment(sketch, "E1271", {"start": v(-0.7, 0.52) * mm, "end": v(-0.7, 0.52) * mm});
            skLineSegment(sketch, "E1272", {"start": v(-0.7, 0.52) * mm, "end": v(-0.71, 0.53) * mm});
            skLineSegment(sketch, "E1273", {"start": v(-0.71, 0.53) * mm, "end": v(-0.71, 0.53) * mm});
            skLineSegment(sketch, "E1274", {"start": v(-0.71, 0.53) * mm, "end": v(-0.7, 0.54) * mm});
            skLineSegment(sketch, "E1275", {"start": v(-0.7, 0.54) * mm, "end": v(-0.7, 0.54) * mm});
            skLineSegment(sketch, "E1276", {"start": v(-0.7, 0.54) * mm, "end": v(-0.7, 0.55) * mm});
            skLineSegment(sketch, "E1277", {"start": v(-0.7, 0.55) * mm, "end": v(-0.7, 0.55) * mm});
            skLineSegment(sketch, "E1278", {"start": v(-0.7, 0.55) * mm, "end": v(-0.68, 0.55) * mm});
            skLineSegment(sketch, "E1279", {"start": v(-0.68, 0.55) * mm, "end": v(-0.68, 0.55) * mm});
            skLineSegment(sketch, "E1280", {"start": v(-0.68, 0.55) * mm, "end": v(-0.63, 0.54) * mm});
            skLineSegment(sketch, "E1281", {"start": v(-0.63, 0.54) * mm, "end": v(-0.65, 0.59) * mm});
            skLineSegment(sketch, "E1282", {"start": v(-0.65, 0.59) * mm, "end": v(-0.65, 0.59) * mm});
            skLineSegment(sketch, "E1283", {"start": v(-0.65, 0.59) * mm, "end": v(-0.65, 0.6) * mm});
            skLineSegment(sketch, "E1284", {"start": v(-0.65, 0.6) * mm, "end": v(-0.65, 0.6) * mm});
            skLineSegment(sketch, "E1285", {"start": v(-0.65, 0.6) * mm, "end": v(-0.65, 0.61) * mm});
            skLineSegment(sketch, "E1286", {"start": v(-0.65, 0.61) * mm, "end": v(-0.64, 0.61) * mm});
            skLineSegment(sketch, "E1287", {"start": v(-0.64, 0.61) * mm, "end": v(-0.64, 0.62) * mm});
            skLineSegment(sketch, "E1288", {"start": v(-0.64, 0.62) * mm, "end": v(-0.64, 0.62) * mm});
            skLineSegment(sketch, "E1289", {"start": v(-0.64, 0.62) * mm, "end": v(-0.63, 0.61) * mm});
            skLineSegment(sketch, "E1290", {"start": v(-0.63, 0.61) * mm, "end": v(-0.63, 0.61) * mm});
            skLineSegment(sketch, "E1291", {"start": v(-0.63, 0.61) * mm, "end": v(-0.53, 0.53) * mm});
            skLineSegment(sketch, "E1292", {"start": v(-0.53, 0.53) * mm, "end": v(-0.53, 0.52) * mm});
            skLineSegment(sketch, "E1293", {"start": v(-0.53, 0.52) * mm, "end": v(-0.53, 0.52) * mm});
            skLineSegment(sketch, "E1294", {"start": v(-0.53, 0.52) * mm, "end": v(-0.53, 0.51) * mm});
            skLineSegment(sketch, "E1295", {"start": v(-0.53, 0.51) * mm, "end": v(-0.53, 0.5) * mm});
            skLineSegment(sketch, "E1296", {"start": v(-0.53, 0.5) * mm, "end": v(-0.53, 0.5) * mm});
            skLineSegment(sketch, "E1297", {"start": v(-0.53, 0.5) * mm, "end": v(-0.54, 0.5) * mm});
            skLineSegment(sketch, "E1298", {"start": v(-0.54, 0.5) * mm, "end": v(-0.54, 0.5) * mm});
            skLineSegment(sketch, "E1299", {"start": v(-0.54, 0.5) * mm, "end": v(-0.55, 0.5) * mm});
            skLineSegment(sketch, "E1300", {"start": v(-0.55, 0.5) * mm, "end": v(-0.55, 0.5) * mm});
            skLineSegment(sketch, "E1301", {"start": v(-0.55, 0.5) * mm, "end": v(-0.61, 0.56) * mm});
            skLineSegment(sketch, "E1302", {"start": v(-0.61, 0.56) * mm, "end": v(-0.6, 0.52) * mm});
            skLineSegment(sketch, "E1303", {"start": v(-0.6, 0.52) * mm, "end": v(-0.6, 0.52) * mm});
            skLineSegment(sketch, "E1304", {"start": v(-0.6, 0.52) * mm, "end": v(-0.6, 0.5) * mm});
            skLineSegment(sketch, "E1305", {"start": v(-0.6, 0.5) * mm, "end": v(-0.6, 0.5) * mm});
            skLineSegment(sketch, "E1306", {"start": v(-0.6, 0.5) * mm, "end": v(-0.66, 0.52) * mm});
            skLineSegment(sketch, "E1307", {"start": v(-0.66, 0.52) * mm, "end": v(-0.6, 0.46) * mm});
            skLineSegment(sketch, "E1308", {"start": v(-0.6, 0.46) * mm, "end": v(-0.6, 0.45) * mm});
            skLineSegment(sketch, "E1309", {"start": v(-0.6, 0.45) * mm, "end": v(-0.59, 0.45) * mm});
            skLineSegment(sketch, "E1310", {"start": v(-0.59, 0.45) * mm, "end": v(-0.59, 0.45) * mm});
            skLineSegment(sketch, "E1311", {"start": v(-0.59, 0.45) * mm, "end": v(-0.6, 0.44) * mm});
            skLineSegment(sketch, "E1312", {"start": v(-0.6, 0.44) * mm, "end": v(-0.6, 0.44) * mm});
            skLineSegment(sketch, "E1313", {"start": v(-0.6, 0.44) * mm, "end": v(-0.6, 0.43) * mm});
            skLineSegment(sketch, "E1314", {"start": v(-0.6, 0.43) * mm, "end": v(-0.6, 0.43) * mm});
            skLineSegment(sketch, "E1315", {"start": v(-0.6, 0.43) * mm, "end": v(-0.6, 0.44) * mm});
            skLineSegment(sketch, "E1316", {"start": v(-0.51, 0.54) * mm, "end": v(-0.57, 0.6) * mm});
            skLineSegment(sketch, "E1317", {"start": v(-0.57, 0.6) * mm, "end": v(-0.57, 0.6) * mm});
            skLineSegment(sketch, "E1318", {"start": v(-0.57, 0.6) * mm, "end": v(-0.56, 0.61) * mm});
            skLineSegment(sketch, "E1319", {"start": v(-0.56, 0.61) * mm, "end": v(-0.56, 0.61) * mm});
            skLineSegment(sketch, "E1320", {"start": v(-0.56, 0.61) * mm, "end": v(-0.55, 0.62) * mm});
            skLineSegment(sketch, "E1321", {"start": v(-0.55, 0.62) * mm, "end": v(-0.55, 0.62) * mm});
            skLineSegment(sketch, "E1322", {"start": v(-0.55, 0.62) * mm, "end": v(-0.5, 0.56) * mm});
            skLineSegment(sketch, "E1323", {"start": v(-0.5, 0.56) * mm, "end": v(-0.5, 0.55) * mm});
            skLineSegment(sketch, "E1324", {"start": v(-0.5, 0.55) * mm, "end": v(-0.5, 0.55) * mm});
            skLineSegment(sketch, "E1325", {"start": v(-0.5, 0.55) * mm, "end": v(-0.5, 0.54) * mm});
            skLineSegment(sketch, "E1326", {"start": v(-0.5, 0.54) * mm, "end": v(-0.5, 0.54) * mm});
            skLineSegment(sketch, "E1327", {"start": v(-0.5, 0.54) * mm, "end": v(-0.51, 0.54) * mm});
            skLineSegment(sketch, "E1328", {"start": v(-0.51, 0.54) * mm, "end": v(-0.51, 0.54) * mm});
            skLineSegment(sketch, "E1329", {"start": v(-0.6, 0.63) * mm, "end": v(-0.6, 0.63) * mm});
            skLineSegment(sketch, "E1330", {"start": v(-0.6, 0.63) * mm, "end": v(-0.6, 0.64) * mm});
            skLineSegment(sketch, "E1331", {"start": v(-0.6, 0.64) * mm, "end": v(-0.6, 0.64) * mm});
            skLineSegment(sketch, "E1332", {"start": v(-0.6, 0.64) * mm, "end": v(-0.6, 0.65) * mm});
            skLineSegment(sketch, "E1333", {"start": v(-0.6, 0.65) * mm, "end": v(-0.6, 0.65) * mm});
            skLineSegment(sketch, "E1334", {"start": v(-0.6, 0.65) * mm, "end": v(-0.58, 0.65) * mm});
            skLineSegment(sketch, "E1335", {"start": v(-0.58, 0.65) * mm, "end": v(-0.58, 0.65) * mm});
            skLineSegment(sketch, "E1336", {"start": v(-0.58, 0.65) * mm, "end": v(-0.57, 0.65) * mm});
            skLineSegment(sketch, "E1337", {"start": v(-0.57, 0.65) * mm, "end": v(-0.57, 0.65) * mm});
            skLineSegment(sketch, "E1338", {"start": v(-0.57, 0.65) * mm, "end": v(-0.57, 0.64) * mm});
            skLineSegment(sketch, "E1339", {"start": v(-0.57, 0.64) * mm, "end": v(-0.57, 0.64) * mm});
            skLineSegment(sketch, "E1340", {"start": v(-0.57, 0.64) * mm, "end": v(-0.58, 0.63) * mm});
            skLineSegment(sketch, "E1341", {"start": v(-0.58, 0.63) * mm, "end": v(-0.58, 0.63) * mm});
            skLineSegment(sketch, "E1342", {"start": v(-0.58, 0.63) * mm, "end": v(-0.59, 0.63) * mm});
            skLineSegment(sketch, "E1343", {"start": v(-0.59, 0.63) * mm, "end": v(-0.59, 0.63) * mm});
            skLineSegment(sketch, "E1344", {"start": v(-0.59, 0.63) * mm, "end": v(-0.6, 0.63) * mm});
            skLineSegment(sketch, "E1345", {"start": v(-0.5, 0.6) * mm, "end": v(-0.51, 0.6) * mm});
            skLineSegment(sketch, "E1346", {"start": v(-0.51, 0.6) * mm, "end": v(-0.51, 0.6) * mm});
            skLineSegment(sketch, "E1347", {"start": v(-0.51, 0.6) * mm, "end": v(-0.52, 0.63) * mm});
            skLineSegment(sketch, "E1348", {"start": v(-0.52, 0.63) * mm, "end": v(-0.52, 0.64) * mm});
            skLineSegment(sketch, "E1349", {"start": v(-0.52, 0.64) * mm, "end": v(-0.52, 0.64) * mm});
            skLineSegment(sketch, "E1350", {"start": v(-0.52, 0.64) * mm, "end": v(-0.5, 0.66) * mm});
            skLineSegment(sketch, "E1351", {"start": v(-0.5, 0.66) * mm, "end": v(-0.5, 0.67) * mm});
            skLineSegment(sketch, "E1352", {"start": v(-0.5, 0.67) * mm, "end": v(-0.5, 0.67) * mm});
            skLineSegment(sketch, "E1353", {"start": v(-0.5, 0.67) * mm, "end": v(-0.48, 0.68) * mm});
            skLineSegment(sketch, "E1354", {"start": v(-0.48, 0.68) * mm, "end": v(-0.48, 0.68) * mm});
            skLineSegment(sketch, "E1355", {"start": v(-0.48, 0.68) * mm, "end": v(-0.46, 0.67) * mm});
            skLineSegment(sketch, "E1356", {"start": v(-0.46, 0.67) * mm, "end": v(-0.46, 0.67) * mm});
            skLineSegment(sketch, "E1357", {"start": v(-0.46, 0.67) * mm, "end": v(-0.46, 0.66) * mm});
            skLineSegment(sketch, "E1358", {"start": v(-0.46, 0.66) * mm, "end": v(-0.46, 0.66) * mm});
            skLineSegment(sketch, "E1359", {"start": v(-0.46, 0.66) * mm, "end": v(-0.47, 0.65) * mm});
            skLineSegment(sketch, "E1360", {"start": v(-0.47, 0.65) * mm, "end": v(-0.47, 0.65) * mm});
            skLineSegment(sketch, "E1361", {"start": v(-0.47, 0.65) * mm, "end": v(-0.48, 0.65) * mm});
            skLineSegment(sketch, "E1362", {"start": v(-0.48, 0.65) * mm, "end": v(-0.48, 0.65) * mm});
            skLineSegment(sketch, "E1363", {"start": v(-0.48, 0.65) * mm, "end": v(-0.49, 0.65) * mm});
            skLineSegment(sketch, "E1364", {"start": v(-0.49, 0.65) * mm, "end": v(-0.5, 0.64) * mm});
            skLineSegment(sketch, "E1365", {"start": v(-0.5, 0.64) * mm, "end": v(-0.5, 0.62) * mm});
            skLineSegment(sketch, "E1366", {"start": v(-0.5, 0.62) * mm, "end": v(-0.49, 0.62) * mm});
            skLineSegment(sketch, "E1367", {"start": v(-0.49, 0.62) * mm, "end": v(-0.48, 0.6) * mm});
            skLineSegment(sketch, "E1368", {"start": v(-0.48, 0.6) * mm, "end": v(-0.48, 0.6) * mm});
            skLineSegment(sketch, "E1369", {"start": v(-0.48, 0.6) * mm, "end": v(-0.47, 0.6) * mm});
            skLineSegment(sketch, "E1370", {"start": v(-0.47, 0.6) * mm, "end": v(-0.45, 0.6) * mm});
            skLineSegment(sketch, "E1371", {"start": v(-0.45, 0.6) * mm, "end": v(-0.45, 0.6) * mm});
            skLineSegment(sketch, "E1372", {"start": v(-0.45, 0.6) * mm, "end": v(-0.44, 0.61) * mm});
            skLineSegment(sketch, "E1373", {"start": v(-0.44, 0.61) * mm, "end": v(-0.44, 0.61) * mm});
            skLineSegment(sketch, "E1374", {"start": v(-0.44, 0.61) * mm, "end": v(-0.44, 0.62) * mm});
            skLineSegment(sketch, "E1375", {"start": v(-0.44, 0.62) * mm, "end": v(-0.44, 0.62) * mm});
            skLineSegment(sketch, "E1376", {"start": v(-0.44, 0.62) * mm, "end": v(-0.43, 0.62) * mm});
            skLineSegment(sketch, "E1377", {"start": v(-0.43, 0.62) * mm, "end": v(-0.43, 0.62) * mm});
            skLineSegment(sketch, "E1378", {"start": v(-0.43, 0.62) * mm, "end": v(-0.42, 0.62) * mm});
            skLineSegment(sketch, "E1379", {"start": v(-0.42, 0.62) * mm, "end": v(-0.42, 0.62) * mm});
            skLineSegment(sketch, "E1380", {"start": v(-0.42, 0.62) * mm, "end": v(-0.42, 0.6) * mm});
            skLineSegment(sketch, "E1381", {"start": v(-0.42, 0.6) * mm, "end": v(-0.42, 0.6) * mm});
            skLineSegment(sketch, "E1382", {"start": v(-0.42, 0.6) * mm, "end": v(-0.44, 0.59) * mm});
            skLineSegment(sketch, "E1383", {"start": v(-0.44, 0.59) * mm, "end": v(-0.44, 0.58) * mm});
            skLineSegment(sketch, "E1384", {"start": v(-0.44, 0.58) * mm, "end": v(-0.44, 0.58) * mm});
            skLineSegment(sketch, "E1385", {"start": v(-0.44, 0.58) * mm, "end": v(-0.47, 0.57) * mm});
            skLineSegment(sketch, "E1386", {"start": v(-0.47, 0.57) * mm, "end": v(-0.47, 0.57) * mm});
            skLineSegment(sketch, "E1387", {"start": v(-0.47, 0.57) * mm, "end": v(-0.48, 0.57) * mm});
            skLineSegment(sketch, "E1388", {"start": v(-0.48, 0.57) * mm, "end": v(-0.5, 0.59) * mm});
            skLineSegment(sketch, "E1389", {"start": v(-0.5, 0.59) * mm, "end": v(-0.5, 0.6) * mm});
            skLineSegment(sketch, "E1390", {"start": v(-0.4, 0.62) * mm, "end": v(-0.48, 0.74) * mm});
            skLineSegment(sketch, "E1391", {"start": v(-0.48, 0.74) * mm, "end": v(-0.48, 0.74) * mm});
            skLineSegment(sketch, "E1392", {"start": v(-0.48, 0.74) * mm, "end": v(-0.48, 0.75) * mm});
            skLineSegment(sketch, "E1393", {"start": v(-0.48, 0.75) * mm, "end": v(-0.48, 0.75) * mm});
            skLineSegment(sketch, "E1394", {"start": v(-0.48, 0.75) * mm, "end": v(-0.47, 0.75) * mm});
            skLineSegment(sketch, "E1395", {"start": v(-0.47, 0.75) * mm, "end": v(-0.47, 0.75) * mm});
            skLineSegment(sketch, "E1396", {"start": v(-0.47, 0.75) * mm, "end": v(-0.47, 0.76) * mm});
            skLineSegment(sketch, "E1397", {"start": v(-0.47, 0.76) * mm, "end": v(-0.46, 0.76) * mm});
            skLineSegment(sketch, "E1398", {"start": v(-0.46, 0.76) * mm, "end": v(-0.46, 0.76) * mm});
            skLineSegment(sketch, "E1399", {"start": v(-0.46, 0.76) * mm, "end": v(-0.46, 0.75) * mm});
            skLineSegment(sketch, "E1400", {"start": v(-0.46, 0.75) * mm, "end": v(-0.45, 0.75) * mm});
            skLineSegment(sketch, "E1401", {"start": v(-0.45, 0.75) * mm, "end": v(-0.42, 0.7) * mm});
            skLineSegment(sketch, "E1402", {"start": v(-0.42, 0.7) * mm, "end": v(-0.42, 0.7) * mm});
            skLineSegment(sketch, "E1403", {"start": v(-0.42, 0.7) * mm, "end": v(-0.42, 0.71) * mm});
            skLineSegment(sketch, "E1404", {"start": v(-0.42, 0.71) * mm, "end": v(-0.42, 0.71) * mm});
            skLineSegment(sketch, "E1405", {"start": v(-0.42, 0.71) * mm, "end": v(-0.4, 0.72) * mm});
            skLineSegment(sketch, "E1406", {"start": v(-0.4, 0.72) * mm, "end": v(-0.4, 0.73) * mm});
            skLineSegment(sketch, "E1407", {"start": v(-0.4, 0.73) * mm, "end": v(-0.4, 0.73) * mm});
            skLineSegment(sketch, "E1408", {"start": v(-0.4, 0.73) * mm, "end": v(-0.38, 0.73) * mm});
            skLineSegment(sketch, "E1409", {"start": v(-0.38, 0.73) * mm, "end": v(-0.38, 0.73) * mm});
            skLineSegment(sketch, "E1410", {"start": v(-0.38, 0.73) * mm, "end": v(-0.36, 0.7) * mm});
            skLineSegment(sketch, "E1411", {"start": v(-0.36, 0.7) * mm, "end": v(-0.36, 0.7) * mm});
            skLineSegment(sketch, "E1412", {"start": v(-0.36, 0.7) * mm, "end": v(-0.33, 0.66) * mm});
            skLineSegment(sketch, "E1413", {"start": v(-0.33, 0.66) * mm, "end": v(-0.33, 0.66) * mm});
            skLineSegment(sketch, "E1414", {"start": v(-0.33, 0.66) * mm, "end": v(-0.34, 0.65) * mm});
            skLineSegment(sketch, "E1415", {"start": v(-0.34, 0.65) * mm, "end": v(-0.34, 0.65) * mm});
            skLineSegment(sketch, "E1416", {"start": v(-0.34, 0.65) * mm, "end": v(-0.35, 0.65) * mm});
            skLineSegment(sketch, "E1417", {"start": v(-0.35, 0.65) * mm, "end": v(-0.35, 0.65) * mm});
            skLineSegment(sketch, "E1418", {"start": v(-0.35, 0.65) * mm, "end": v(-0.38, 0.7) * mm});
            skLineSegment(sketch, "E1419", {"start": v(-0.38, 0.7) * mm, "end": v(-0.38, 0.7) * mm});
            skLineSegment(sketch, "E1420", {"start": v(-0.38, 0.7) * mm, "end": v(-0.39, 0.7) * mm});
            skLineSegment(sketch, "E1421", {"start": v(-0.39, 0.7) * mm, "end": v(-0.4, 0.7) * mm});
            skLineSegment(sketch, "E1422", {"start": v(-0.4, 0.7) * mm, "end": v(-0.4, 0.7) * mm});
            skLineSegment(sketch, "E1423", {"start": v(-0.4, 0.7) * mm, "end": v(-0.41, 0.7) * mm});
            skLineSegment(sketch, "E1424", {"start": v(-0.41, 0.7) * mm, "end": v(-0.41, 0.7) * mm});
            skLineSegment(sketch, "E1425", {"start": v(-0.41, 0.7) * mm, "end": v(-0.41, 0.69) * mm});
            skLineSegment(sketch, "E1426", {"start": v(-0.41, 0.69) * mm, "end": v(-0.41, 0.68) * mm});
            skLineSegment(sketch, "E1427", {"start": v(-0.41, 0.68) * mm, "end": v(-0.4, 0.68) * mm});
            skLineSegment(sketch, "E1428", {"start": v(-0.4, 0.68) * mm, "end": v(-0.39, 0.63) * mm});
            skLineSegment(sketch, "E1429", {"start": v(-0.39, 0.63) * mm, "end": v(-0.39, 0.63) * mm});
            skLineSegment(sketch, "E1430", {"start": v(-0.39, 0.63) * mm, "end": v(-0.4, 0.62) * mm});
            skLineSegment(sketch, "E1431", {"start": v(-0.4, 0.62) * mm, "end": v(-0.4, 0.62) * mm});
            skLineSegment(sketch, "E1432", {"start": v(-0.3, 0.7) * mm, "end": v(-0.3, 0.7) * mm});
            skLineSegment(sketch, "E1433", {"start": v(-0.3, 0.7) * mm, "end": v(-0.29, 0.7) * mm});
            skLineSegment(sketch, "E1434", {"start": v(-0.29, 0.7) * mm, "end": v(-0.28, 0.7) * mm});
            skLineSegment(sketch, "E1435", {"start": v(-0.28, 0.7) * mm, "end": v(-0.28, 0.7) * mm});
            skLineSegment(sketch, "E1436", {"start": v(-0.28, 0.7) * mm, "end": v(-0.28, 0.72) * mm});
            skLineSegment(sketch, "E1437", {"start": v(-0.28, 0.72) * mm, "end": v(-0.28, 0.72) * mm});
            skLineSegment(sketch, "E1438", {"start": v(-0.28, 0.72) * mm, "end": v(-0.29, 0.72) * mm});
            skLineSegment(sketch, "E1439", {"start": v(-0.29, 0.72) * mm, "end": v(-0.29, 0.72) * mm});
            skLineSegment(sketch, "E1440", {"start": v(-0.29, 0.72) * mm, "end": v(-0.3, 0.71) * mm});
            skLineSegment(sketch, "E1441", {"start": v(-0.3, 0.71) * mm, "end": v(-0.3, 0.71) * mm});
            skLineSegment(sketch, "E1442", {"start": v(-0.3, 0.71) * mm, "end": v(-0.3, 0.7) * mm});
            skLineSegment(sketch, "E1443", {"start": v(-0.33, 0.69) * mm, "end": v(-0.33, 0.69) * mm});
            skLineSegment(sketch, "E1444", {"start": v(-0.33, 0.69) * mm, "end": v(-0.33, 0.7) * mm});
            skLineSegment(sketch, "E1445", {"start": v(-0.33, 0.7) * mm, "end": v(-0.33, 0.71) * mm});
            skLineSegment(sketch, "E1446", {"start": v(-0.33, 0.71) * mm, "end": v(-0.32, 0.71) * mm});
            skLineSegment(sketch, "E1447", {"start": v(-0.32, 0.71) * mm, "end": v(-0.3, 0.73) * mm});
            skLineSegment(sketch, "E1448", {"start": v(-0.3, 0.73) * mm, "end": v(-0.3, 0.73) * mm});
            skLineSegment(sketch, "E1449", {"start": v(-0.3, 0.73) * mm, "end": v(-0.29, 0.74) * mm});
            skLineSegment(sketch, "E1450", {"start": v(-0.29, 0.74) * mm, "end": v(-0.29, 0.74) * mm});
            skLineSegment(sketch, "E1451", {"start": v(-0.29, 0.74) * mm, "end": v(-0.3, 0.75) * mm});
            skLineSegment(sketch, "E1452", {"start": v(-0.3, 0.75) * mm, "end": v(-0.3, 0.75) * mm});
            skLineSegment(sketch, "E1453", {"start": v(-0.3, 0.75) * mm, "end": v(-0.31, 0.75) * mm});
            skLineSegment(sketch, "E1454", {"start": v(-0.31, 0.75) * mm, "end": v(-0.31, 0.75) * mm});
            skLineSegment(sketch, "E1455", {"start": v(-0.31, 0.75) * mm, "end": v(-0.33, 0.74) * mm});
            skLineSegment(sketch, "E1456", {"start": v(-0.33, 0.74) * mm, "end": v(-0.33, 0.74) * mm});
            skLineSegment(sketch, "E1457", {"start": v(-0.33, 0.74) * mm, "end": v(-0.33, 0.73) * mm});
            skLineSegment(sketch, "E1458", {"start": v(-0.33, 0.73) * mm, "end": v(-0.33, 0.73) * mm});
            skLineSegment(sketch, "E1459", {"start": v(-0.33, 0.73) * mm, "end": v(-0.34, 0.73) * mm});
            skLineSegment(sketch, "E1460", {"start": v(-0.34, 0.73) * mm, "end": v(-0.34, 0.73) * mm});
            skLineSegment(sketch, "E1461", {"start": v(-0.34, 0.73) * mm, "end": v(-0.35, 0.74) * mm});
            skLineSegment(sketch, "E1462", {"start": v(-0.35, 0.74) * mm, "end": v(-0.35, 0.74) * mm});
            skLineSegment(sketch, "E1463", {"start": v(-0.35, 0.74) * mm, "end": v(-0.34, 0.75) * mm});
            skLineSegment(sketch, "E1464", {"start": v(-0.34, 0.75) * mm, "end": v(-0.34, 0.76) * mm});
            skLineSegment(sketch, "E1465", {"start": v(-0.34, 0.76) * mm, "end": v(-0.34, 0.76) * mm});
            skLineSegment(sketch, "E1466", {"start": v(-0.34, 0.76) * mm, "end": v(-0.32, 0.77) * mm});
            skLineSegment(sketch, "E1467", {"start": v(-0.32, 0.77) * mm, "end": v(-0.32, 0.77) * mm});
            skLineSegment(sketch, "E1468", {"start": v(-0.32, 0.77) * mm, "end": v(-0.29, 0.77) * mm});
            skLineSegment(sketch, "E1469", {"start": v(-0.29, 0.77) * mm, "end": v(-0.29, 0.77) * mm});
            skLineSegment(sketch, "E1470", {"start": v(-0.29, 0.77) * mm, "end": v(-0.28, 0.77) * mm});
            skLineSegment(sketch, "E1471", {"start": v(-0.28, 0.77) * mm, "end": v(-0.27, 0.75) * mm});
            skLineSegment(sketch, "E1472", {"start": v(-0.27, 0.75) * mm, "end": v(-0.26, 0.75) * mm});
            skLineSegment(sketch, "E1473", {"start": v(-0.26, 0.75) * mm, "end": v(-0.24, 0.7) * mm});
            skLineSegment(sketch, "E1474", {"start": v(-0.24, 0.7) * mm, "end": v(-0.24, 0.7) * mm});
            skLineSegment(sketch, "E1475", {"start": v(-0.24, 0.7) * mm, "end": v(-0.25, 0.7) * mm});
            skLineSegment(sketch, "E1476", {"start": v(-0.25, 0.7) * mm, "end": v(-0.25, 0.7) * mm});
            skLineSegment(sketch, "E1477", {"start": v(-0.25, 0.7) * mm, "end": v(-0.25, 0.69) * mm});
            skLineSegment(sketch, "E1478", {"start": v(-0.25, 0.69) * mm, "end": v(-0.25, 0.69) * mm});
            skLineSegment(sketch, "E1479", {"start": v(-0.25, 0.69) * mm, "end": v(-0.26, 0.69) * mm});
            skLineSegment(sketch, "E1480", {"start": v(-0.26, 0.69) * mm, "end": v(-0.26, 0.69) * mm});
            skLineSegment(sketch, "E1481", {"start": v(-0.26, 0.69) * mm, "end": v(-0.27, 0.7) * mm});
            skLineSegment(sketch, "E1482", {"start": v(-0.27, 0.7) * mm, "end": v(-0.27, 0.7) * mm});
            skLineSegment(sketch, "E1483", {"start": v(-0.27, 0.7) * mm, "end": v(-0.3, 0.67) * mm});
            skLineSegment(sketch, "E1484", {"start": v(-0.3, 0.67) * mm, "end": v(-0.3, 0.67) * mm});
            skLineSegment(sketch, "E1485", {"start": v(-0.3, 0.67) * mm, "end": v(-0.31, 0.67) * mm});
            skLineSegment(sketch, "E1486", {"start": v(-0.31, 0.67) * mm, "end": v(-0.31, 0.67) * mm});
            skLineSegment(sketch, "E1487", {"start": v(-0.31, 0.67) * mm, "end": v(-0.32, 0.67) * mm});
            skLineSegment(sketch, "E1488", {"start": v(-0.32, 0.67) * mm, "end": v(-0.33, 0.68) * mm});
            skLineSegment(sketch, "E1489", {"start": v(-0.33, 0.68) * mm, "end": v(-0.33, 0.69) * mm});
            skLineSegment(sketch, "E1490", {"start": v(-0.21, 0.83) * mm, "end": v(-0.21, 0.83) * mm});
            skLineSegment(sketch, "E1491", {"start": v(-0.21, 0.83) * mm, "end": v(-0.22, 0.84) * mm});
            skLineSegment(sketch, "E1492", {"start": v(-0.22, 0.84) * mm, "end": v(-0.22, 0.84) * mm});
            skLineSegment(sketch, "E1493", {"start": v(-0.22, 0.84) * mm, "end": v(-0.22, 0.85) * mm});
            skLineSegment(sketch, "E1494", {"start": v(-0.22, 0.85) * mm, "end": v(-0.21, 0.85) * mm});
            skLineSegment(sketch, "E1495", {"start": v(-0.21, 0.85) * mm, "end": v(-0.2, 0.85) * mm});
            skLineSegment(sketch, "E1496", {"start": v(-0.2, 0.85) * mm, "end": v(-0.2, 0.85) * mm});
            skLineSegment(sketch, "E1497", {"start": v(-0.2, 0.85) * mm, "end": v(-0.2, 0.84) * mm});
            skLineSegment(sketch, "E1498", {"start": v(-0.2, 0.84) * mm, "end": v(-0.2, 0.84) * mm});
            skLineSegment(sketch, "E1499", {"start": v(-0.2, 0.84) * mm, "end": v(-0.2, 0.83) * mm});
            skLineSegment(sketch, "E1500", {"start": v(-0.2, 0.83) * mm, "end": v(-0.2, 0.83) * mm});
            skLineSegment(sketch, "E1501", {"start": v(-0.2, 0.83) * mm, "end": v(-0.21, 0.83) * mm});
            skLineSegment(sketch, "E1502", {"start": v(-0.22, 0.76) * mm, "end": v(-0.2, 0.77) * mm});
            skLineSegment(sketch, "E1503", {"start": v(-0.2, 0.77) * mm, "end": v(-0.19, 0.77) * mm});
            skLineSegment(sketch, "E1504", {"start": v(-0.19, 0.77) * mm, "end": v(-0.19, 0.77) * mm});
            skLineSegment(sketch, "E1505", {"start": v(-0.19, 0.77) * mm, "end": v(-0.19, 0.78) * mm});
            skLineSegment(sketch, "E1506", {"start": v(-0.19, 0.78) * mm, "end": v(-0.19, 0.78) * mm});
            skLineSegment(sketch, "E1507", {"start": v(-0.19, 0.78) * mm, "end": v(-0.2, 0.78) * mm});
            skLineSegment(sketch, "E1508", {"start": v(-0.2, 0.78) * mm, "end": v(-0.2, 0.79) * mm});
            skLineSegment(sketch, "E1509", {"start": v(-0.2, 0.79) * mm, "end": v(-0.2, 0.79) * mm});
            skLineSegment(sketch, "E1510", {"start": v(-0.2, 0.79) * mm, "end": v(-0.22, 0.78) * mm});
            skLineSegment(sketch, "E1511", {"start": v(-0.22, 0.78) * mm, "end": v(-0.22, 0.78) * mm});
            skLineSegment(sketch, "E1512", {"start": v(-0.22, 0.78) * mm, "end": v(-0.22, 0.77) * mm});
            skLineSegment(sketch, "E1513", {"start": v(-0.22, 0.77) * mm, "end": v(-0.22, 0.77) * mm});
            skLineSegment(sketch, "E1514", {"start": v(-0.22, 0.77) * mm, "end": v(-0.22, 0.76) * mm});
            skLineSegment(sketch, "E1515", {"start": v(-0.24, 0.74) * mm, "end": v(-0.25, 0.75) * mm});
            skLineSegment(sketch, "E1516", {"start": v(-0.25, 0.75) * mm, "end": v(-0.25, 0.76) * mm});
            skLineSegment(sketch, "E1517", {"start": v(-0.25, 0.76) * mm, "end": v(-0.24, 0.78) * mm});
            skLineSegment(sketch, "E1518", {"start": v(-0.24, 0.78) * mm, "end": v(-0.24, 0.79) * mm});
            skLineSegment(sketch, "E1519", {"start": v(-0.24, 0.79) * mm, "end": v(-0.24, 0.79) * mm});
            skLineSegment(sketch, "E1520", {"start": v(-0.24, 0.79) * mm, "end": v(-0.22, 0.8) * mm});
            skLineSegment(sketch, "E1521", {"start": v(-0.22, 0.8) * mm, "end": v(-0.21, 0.8) * mm});
            skLineSegment(sketch, "E1522", {"start": v(-0.21, 0.8) * mm, "end": v(-0.2, 0.8) * mm});
            skLineSegment(sketch, "E1523", {"start": v(-0.2, 0.8) * mm, "end": v(-0.18, 0.8) * mm});
            skLineSegment(sketch, "E1524", {"start": v(-0.18, 0.8) * mm, "end": v(-0.18, 0.8) * mm});
            skLineSegment(sketch, "E1525", {"start": v(-0.18, 0.8) * mm, "end": v(-0.16, 0.78) * mm});
            skLineSegment(sketch, "E1526", {"start": v(-0.16, 0.78) * mm, "end": v(-0.16, 0.78) * mm});
            skLineSegment(sketch, "E1527", {"start": v(-0.16, 0.78) * mm, "end": v(-0.16, 0.77) * mm});
            skLineSegment(sketch, "E1528", {"start": v(-0.16, 0.77) * mm, "end": v(-0.16, 0.77) * mm});
            skLineSegment(sketch, "E1529", {"start": v(-0.16, 0.77) * mm, "end": v(-0.16, 0.76) * mm});
            skLineSegment(sketch, "E1530", {"start": v(-0.16, 0.76) * mm, "end": v(-0.16, 0.76) * mm});
            skLineSegment(sketch, "E1531", {"start": v(-0.16, 0.76) * mm, "end": v(-0.17, 0.76) * mm});
            skLineSegment(sketch, "E1532", {"start": v(-0.17, 0.76) * mm, "end": v(-0.17, 0.76) * mm});
            skLineSegment(sketch, "E1533", {"start": v(-0.17, 0.76) * mm, "end": v(-0.22, 0.75) * mm});
            skLineSegment(sketch, "E1534", {"start": v(-0.22, 0.75) * mm, "end": v(-0.21, 0.74) * mm});
            skLineSegment(sketch, "E1535", {"start": v(-0.21, 0.74) * mm, "end": v(-0.21, 0.74) * mm});
            skLineSegment(sketch, "E1536", {"start": v(-0.21, 0.74) * mm, "end": v(-0.2, 0.73) * mm});
            skLineSegment(sketch, "E1537", {"start": v(-0.2, 0.73) * mm, "end": v(-0.2, 0.73) * mm});
            skLineSegment(sketch, "E1538", {"start": v(-0.2, 0.73) * mm, "end": v(-0.19, 0.73) * mm});
            skLineSegment(sketch, "E1539", {"start": v(-0.19, 0.73) * mm, "end": v(-0.19, 0.73) * mm});
            skLineSegment(sketch, "E1540", {"start": v(-0.19, 0.73) * mm, "end": v(-0.18, 0.73) * mm});
            skLineSegment(sketch, "E1541", {"start": v(-0.18, 0.73) * mm, "end": v(-0.17, 0.74) * mm});
            skLineSegment(sketch, "E1542", {"start": v(-0.17, 0.74) * mm, "end": v(-0.17, 0.74) * mm});
            skLineSegment(sketch, "E1543", {"start": v(-0.17, 0.74) * mm, "end": v(-0.16, 0.74) * mm});
            skLineSegment(sketch, "E1544", {"start": v(-0.16, 0.74) * mm, "end": v(-0.16, 0.74) * mm});
            skLineSegment(sketch, "E1545", {"start": v(-0.16, 0.74) * mm, "end": v(-0.16, 0.75) * mm});
            skLineSegment(sketch, "E1546", {"start": v(-0.16, 0.75) * mm, "end": v(-0.16, 0.74) * mm});
            skLineSegment(sketch, "E1547", {"start": v(-0.16, 0.74) * mm, "end": v(-0.15, 0.74) * mm});
            skLineSegment(sketch, "E1548", {"start": v(-0.15, 0.74) * mm, "end": v(-0.15, 0.74) * mm});
            skLineSegment(sketch, "E1549", {"start": v(-0.15, 0.74) * mm, "end": v(-0.16, 0.72) * mm});
            skLineSegment(sketch, "E1550", {"start": v(-0.16, 0.72) * mm, "end": v(-0.16, 0.72) * mm});
            skLineSegment(sketch, "E1551", {"start": v(-0.16, 0.72) * mm, "end": v(-0.18, 0.71) * mm});
            skLineSegment(sketch, "E1552", {"start": v(-0.18, 0.71) * mm, "end": v(-0.18, 0.7) * mm});
            skLineSegment(sketch, "E1553", {"start": v(-0.18, 0.7) * mm, "end": v(-0.18, 0.7) * mm});
            skLineSegment(sketch, "E1554", {"start": v(-0.18, 0.7) * mm, "end": v(-0.22, 0.7) * mm});
            skLineSegment(sketch, "E1555", {"start": v(-0.22, 0.7) * mm, "end": v(-0.22, 0.71) * mm});
            skLineSegment(sketch, "E1556", {"start": v(-0.22, 0.71) * mm, "end": v(-0.22, 0.71) * mm});
            skLineSegment(sketch, "E1557", {"start": v(-0.22, 0.71) * mm, "end": v(-0.24, 0.73) * mm});
            skLineSegment(sketch, "E1558", {"start": v(-0.24, 0.73) * mm, "end": v(-0.24, 0.74) * mm});
            skLineSegment(sketch, "E1559", {"start": v(-0.24, 0.82) * mm, "end": v(-0.24, 0.82) * mm});
            skLineSegment(sketch, "E1560", {"start": v(-0.24, 0.82) * mm, "end": v(-0.25, 0.83) * mm});
            skLineSegment(sketch, "E1561", {"start": v(-0.25, 0.83) * mm, "end": v(-0.25, 0.83) * mm});
            skLineSegment(sketch, "E1562", {"start": v(-0.25, 0.83) * mm, "end": v(-0.25, 0.84) * mm});
            skLineSegment(sketch, "E1563", {"start": v(-0.25, 0.84) * mm, "end": v(-0.25, 0.84) * mm});
            skLineSegment(sketch, "E1564", {"start": v(-0.25, 0.84) * mm, "end": v(-0.24, 0.84) * mm});
            skLineSegment(sketch, "E1565", {"start": v(-0.24, 0.84) * mm, "end": v(-0.24, 0.84) * mm});
            skLineSegment(sketch, "E1566", {"start": v(-0.24, 0.84) * mm, "end": v(-0.23, 0.84) * mm});
            skLineSegment(sketch, "E1567", {"start": v(-0.23, 0.84) * mm, "end": v(-0.23, 0.84) * mm});
            skLineSegment(sketch, "E1568", {"start": v(-0.23, 0.84) * mm, "end": v(-0.23, 0.83) * mm});
            skLineSegment(sketch, "E1569", {"start": v(-0.23, 0.83) * mm, "end": v(-0.23, 0.83) * mm});
            skLineSegment(sketch, "E1570", {"start": v(-0.23, 0.83) * mm, "end": v(-0.23, 0.82) * mm});
            skLineSegment(sketch, "E1571", {"start": v(-0.23, 0.82) * mm, "end": v(-0.23, 0.82) * mm});
            skLineSegment(sketch, "E1572", {"start": v(-0.23, 0.82) * mm, "end": v(-0.24, 0.82) * mm});
            skLineSegment(sketch, "E1573", {"start": v(-0.13, 0.73) * mm, "end": v(-0.16, 0.87) * mm});
            skLineSegment(sketch, "E1574", {"start": v(-0.16, 0.87) * mm, "end": v(-0.16, 0.87) * mm});
            skLineSegment(sketch, "E1575", {"start": v(-0.16, 0.87) * mm, "end": v(-0.16, 0.88) * mm});
            skLineSegment(sketch, "E1576", {"start": v(-0.16, 0.88) * mm, "end": v(-0.15, 0.88) * mm});
            skLineSegment(sketch, "E1577", {"start": v(-0.15, 0.88) * mm, "end": v(-0.15, 0.88) * mm});
            skLineSegment(sketch, "E1578", {"start": v(-0.15, 0.88) * mm, "end": v(-0.14, 0.88) * mm});
            skLineSegment(sketch, "E1579", {"start": v(-0.14, 0.88) * mm, "end": v(-0.14, 0.88) * mm});
            skLineSegment(sketch, "E1580", {"start": v(-0.14, 0.88) * mm, "end": v(-0.13, 0.88) * mm});
            skLineSegment(sketch, "E1581", {"start": v(-0.13, 0.88) * mm, "end": v(-0.13, 0.87) * mm});
            skLineSegment(sketch, "E1582", {"start": v(-0.13, 0.87) * mm, "end": v(-0.13, 0.87) * mm});
            skLineSegment(sketch, "E1583", {"start": v(-0.13, 0.87) * mm, "end": v(-0.1, 0.74) * mm});
            skLineSegment(sketch, "E1584", {"start": v(-0.1, 0.74) * mm, "end": v(-0.1, 0.74) * mm});
            skLineSegment(sketch, "E1585", {"start": v(-0.1, 0.74) * mm, "end": v(-0.1, 0.73) * mm});
            skLineSegment(sketch, "E1586", {"start": v(-0.1, 0.73) * mm, "end": v(-0.1, 0.73) * mm});
            skLineSegment(sketch, "E1587", {"start": v(-0.1, 0.73) * mm, "end": v(-0.12, 0.73) * mm});
            skLineSegment(sketch, "E1588", {"start": v(-0.12, 0.73) * mm, "end": v(-0.12, 0.73) * mm});
            skLineSegment(sketch, "E1589", {"start": v(-0.12, 0.73) * mm, "end": v(-0.13, 0.73) * mm});
            skLineSegment(sketch, "E1590", {"start": v(-0.13, 0.73) * mm, "end": v(-0.13, 0.73) * mm});
            skLineSegment(sketch, "E1591", {"start": v(-0.04, 0.75) * mm, "end": v(-0.05, 0.88) * mm});
            skLineSegment(sketch, "E1592", {"start": v(-0.05, 0.88) * mm, "end": v(-0.05, 0.88) * mm});
            skLineSegment(sketch, "E1593", {"start": v(-0.05, 0.88) * mm, "end": v(-0.04, 0.89) * mm});
            skLineSegment(sketch, "E1594", {"start": v(-0.04, 0.89) * mm, "end": v(-0.04, 0.89) * mm});
            skLineSegment(sketch, "E1595", {"start": v(-0.04, 0.89) * mm, "end": v(-0.04, 0.9) * mm});
            skLineSegment(sketch, "E1596", {"start": v(-0.04, 0.9) * mm, "end": v(-0.03, 0.9) * mm});
            skLineSegment(sketch, "E1597", {"start": v(-0.03, 0.9) * mm, "end": v(-0.03, 0.9) * mm});
            skLineSegment(sketch, "E1598", {"start": v(-0.03, 0.9) * mm, "end": v(-0.02, 0.89) * mm});
            skLineSegment(sketch, "E1599", {"start": v(-0.02, 0.89) * mm, "end": v(-0.02, 0.89) * mm});
            skLineSegment(sketch, "E1600", {"start": v(-0.02, 0.89) * mm, "end": v(-0.01, 0.88) * mm});
            skLineSegment(sketch, "E1601", {"start": v(-0.01, 0.88) * mm, "end": v(-0.01, 0.88) * mm});
            skLineSegment(sketch, "E1602", {"start": v(-0.01, 0.88) * mm, "end": v(0.01, 0.83) * mm});
            skLineSegment(sketch, "E1603", {"start": v(0.01, 0.83) * mm, "end": v(0.04, 0.88) * mm});
            skLineSegment(sketch, "E1604", {"start": v(0.04, 0.88) * mm, "end": v(0.04, 0.88) * mm});
            skLineSegment(sketch, "E1605", {"start": v(0.04, 0.88) * mm, "end": v(0.05, 0.89) * mm});
            skLineSegment(sketch, "E1606", {"start": v(0.05, 0.89) * mm, "end": v(0.05, 0.89) * mm});
            skLineSegment(sketch, "E1607", {"start": v(0.05, 0.89) * mm, "end": v(0.06, 0.9) * mm});
            skLineSegment(sketch, "E1608", {"start": v(0.06, 0.9) * mm, "end": v(0.06, 0.9) * mm});
            skLineSegment(sketch, "E1609", {"start": v(0.06, 0.9) * mm, "end": v(0.07, 0.89) * mm});
            skLineSegment(sketch, "E1610", {"start": v(0.07, 0.89) * mm, "end": v(0.07, 0.89) * mm});
            skLineSegment(sketch, "E1611", {"start": v(0.07, 0.89) * mm, "end": v(0.07, 0.88) * mm});
            skLineSegment(sketch, "E1612", {"start": v(0.07, 0.88) * mm, "end": v(0.07, 0.88) * mm});
            skLineSegment(sketch, "E1613", {"start": v(0.07, 0.88) * mm, "end": v(0.08, 0.75) * mm});
            skLineSegment(sketch, "E1614", {"start": v(0.08, 0.75) * mm, "end": v(0.08, 0.75) * mm});
            skLineSegment(sketch, "E1615", {"start": v(0.08, 0.75) * mm, "end": v(0.07, 0.74) * mm});
            skLineSegment(sketch, "E1616", {"start": v(0.07, 0.74) * mm, "end": v(0.07, 0.74) * mm});
            skLineSegment(sketch, "E1617", {"start": v(0.07, 0.74) * mm, "end": v(0.06, 0.74) * mm});
            skLineSegment(sketch, "E1618", {"start": v(0.06, 0.74) * mm, "end": v(0.06, 0.74) * mm});
            skLineSegment(sketch, "E1619", {"start": v(0.06, 0.74) * mm, "end": v(0.05, 0.74) * mm});
            skLineSegment(sketch, "E1620", {"start": v(0.05, 0.74) * mm, "end": v(0.05, 0.74) * mm});
            skLineSegment(sketch, "E1621", {"start": v(0.05, 0.74) * mm, "end": v(0.05, 0.75) * mm});
            skLineSegment(sketch, "E1622", {"start": v(0.05, 0.75) * mm, "end": v(0.05, 0.75) * mm});
            skLineSegment(sketch, "E1623", {"start": v(0.05, 0.75) * mm, "end": v(0.05, 0.84) * mm});
            skLineSegment(sketch, "E1624", {"start": v(0.05, 0.84) * mm, "end": v(0.02, 0.8) * mm});
            skLineSegment(sketch, "E1625", {"start": v(0.02, 0.8) * mm, "end": v(0.02, 0.8) * mm});
            skLineSegment(sketch, "E1626", {"start": v(0.02, 0.8) * mm, "end": v(0.02, 0.79) * mm});
            skLineSegment(sketch, "E1627", {"start": v(0.02, 0.79) * mm, "end": v(0.01, 0.79) * mm});
            skLineSegment(sketch, "E1628", {"start": v(0.01, 0.79) * mm, "end": v(0.01, 0.79) * mm});
            skLineSegment(sketch, "E1629", {"start": v(0.01, 0.79) * mm, "end": v(0, 0.8) * mm});
            skLineSegment(sketch, "E1630", {"start": v(0, 0.8) * mm, "end": v(0, 0.8) * mm});
            skLineSegment(sketch, "E1631", {"start": v(0, 0.8) * mm, "end": v(-0.02, 0.84) * mm});
            skLineSegment(sketch, "E1632", {"start": v(-0.02, 0.84) * mm, "end": v(-0.02, 0.75) * mm});
            skLineSegment(sketch, "E1633", {"start": v(-0.02, 0.75) * mm, "end": v(-0.02, 0.75) * mm});
            skLineSegment(sketch, "E1634", {"start": v(-0.02, 0.75) * mm, "end": v(-0.02, 0.74) * mm});
            skLineSegment(sketch, "E1635", {"start": v(-0.02, 0.74) * mm, "end": v(-0.02, 0.74) * mm});
            skLineSegment(sketch, "E1636", {"start": v(-0.02, 0.74) * mm, "end": v(-0.03, 0.74) * mm});
            skLineSegment(sketch, "E1637", {"start": v(-0.03, 0.74) * mm, "end": v(-0.03, 0.74) * mm});
            skLineSegment(sketch, "E1638", {"start": v(-0.03, 0.74) * mm, "end": v(-0.04, 0.74) * mm});
            skLineSegment(sketch, "E1639", {"start": v(-0.04, 0.74) * mm, "end": v(-0.04, 0.74) * mm});
            skLineSegment(sketch, "E1640", {"start": v(-0.04, 0.74) * mm, "end": v(-0.04, 0.75) * mm});
            skLineSegment(sketch, "E1641", {"start": v(-0.04, 0.75) * mm, "end": v(-0.04, 0.75) * mm});
            skLineSegment(sketch, "E1642", {"start": v(0.12, 0.8) * mm, "end": v(0.15, 0.79) * mm});
            skLineSegment(sketch, "E1643", {"start": v(0.15, 0.79) * mm, "end": v(0.15, 0.79) * mm});
            skLineSegment(sketch, "E1644", {"start": v(0.15, 0.79) * mm, "end": v(0.16, 0.79) * mm});
            skLineSegment(sketch, "E1645", {"start": v(0.16, 0.79) * mm, "end": v(0.16, 0.79) * mm});
            skLineSegment(sketch, "E1646", {"start": v(0.16, 0.79) * mm, "end": v(0.16, 0.8) * mm});
            skLineSegment(sketch, "E1647", {"start": v(0.16, 0.8) * mm, "end": v(0.16, 0.8) * mm});
            skLineSegment(sketch, "E1648", {"start": v(0.16, 0.8) * mm, "end": v(0.15, 0.8) * mm});
            skLineSegment(sketch, "E1649", {"start": v(0.15, 0.8) * mm, "end": v(0.14, 0.8) * mm});
            skLineSegment(sketch, "E1650", {"start": v(0.14, 0.8) * mm, "end": v(0.14, 0.8) * mm});
            skLineSegment(sketch, "E1651", {"start": v(0.14, 0.8) * mm, "end": v(0.13, 0.8) * mm});
            skLineSegment(sketch, "E1652", {"start": v(0.13, 0.8) * mm, "end": v(0.13, 0.8) * mm});
            skLineSegment(sketch, "E1653", {"start": v(0.13, 0.8) * mm, "end": v(0.12, 0.8) * mm});
            skLineSegment(sketch, "E1654", {"start": v(0.12, 0.8) * mm, "end": v(0.12, 0.8) * mm});
            skLineSegment(sketch, "E1655", {"start": v(0.1, 0.78) * mm, "end": v(0.1, 0.8) * mm});
            skLineSegment(sketch, "E1656", {"start": v(0.1, 0.8) * mm, "end": v(0.1, 0.8) * mm});
            skLineSegment(sketch, "E1657", {"start": v(0.1, 0.8) * mm, "end": v(0.11, 0.82) * mm});
            skLineSegment(sketch, "E1658", {"start": v(0.11, 0.82) * mm, "end": v(0.11, 0.82) * mm});
            skLineSegment(sketch, "E1659", {"start": v(0.11, 0.82) * mm, "end": v(0.12, 0.82) * mm});
            skLineSegment(sketch, "E1660", {"start": v(0.12, 0.82) * mm, "end": v(0.14, 0.83) * mm});
            skLineSegment(sketch, "E1661", {"start": v(0.14, 0.83) * mm, "end": v(0.15, 0.83) * mm});
            skLineSegment(sketch, "E1662", {"start": v(0.15, 0.83) * mm, "end": v(0.15, 0.83) * mm});
            skLineSegment(sketch, "E1663", {"start": v(0.15, 0.83) * mm, "end": v(0.17, 0.82) * mm});
            skLineSegment(sketch, "E1664", {"start": v(0.17, 0.82) * mm, "end": v(0.18, 0.82) * mm});
            skLineSegment(sketch, "E1665", {"start": v(0.18, 0.82) * mm, "end": v(0.18, 0.81) * mm});
            skLineSegment(sketch, "E1666", {"start": v(0.18, 0.81) * mm, "end": v(0.19, 0.79) * mm});
            skLineSegment(sketch, "E1667", {"start": v(0.19, 0.79) * mm, "end": v(0.19, 0.79) * mm});
            skLineSegment(sketch, "E1668", {"start": v(0.19, 0.79) * mm, "end": v(0.19, 0.78) * mm});
            skLineSegment(sketch, "E1669", {"start": v(0.19, 0.78) * mm, "end": v(0.18, 0.78) * mm});
            skLineSegment(sketch, "E1670", {"start": v(0.18, 0.78) * mm, "end": v(0.18, 0.78) * mm});
            skLineSegment(sketch, "E1671", {"start": v(0.18, 0.78) * mm, "end": v(0.18, 0.77) * mm});
            skLineSegment(sketch, "E1672", {"start": v(0.18, 0.77) * mm, "end": v(0.18, 0.77) * mm});
            skLineSegment(sketch, "E1673", {"start": v(0.18, 0.77) * mm, "end": v(0.17, 0.77) * mm});
            skLineSegment(sketch, "E1674", {"start": v(0.17, 0.77) * mm, "end": v(0.17, 0.77) * mm});
            skLineSegment(sketch, "E1675", {"start": v(0.17, 0.77) * mm, "end": v(0.16, 0.77) * mm});
            skLineSegment(sketch, "E1676", {"start": v(0.16, 0.77) * mm, "end": v(0.16, 0.77) * mm});
            skLineSegment(sketch, "E1677", {"start": v(0.16, 0.77) * mm, "end": v(0.12, 0.78) * mm});
            skLineSegment(sketch, "E1678", {"start": v(0.12, 0.78) * mm, "end": v(0.12, 0.77) * mm});
            skLineSegment(sketch, "E1679", {"start": v(0.12, 0.77) * mm, "end": v(0.12, 0.77) * mm});
            skLineSegment(sketch, "E1680", {"start": v(0.12, 0.77) * mm, "end": v(0.12, 0.76) * mm});
            skLineSegment(sketch, "E1681", {"start": v(0.12, 0.76) * mm, "end": v(0.13, 0.76) * mm});
            skLineSegment(sketch, "E1682", {"start": v(0.13, 0.76) * mm, "end": v(0.13, 0.76) * mm});
            skLineSegment(sketch, "E1683", {"start": v(0.13, 0.76) * mm, "end": v(0.14, 0.75) * mm});
            skLineSegment(sketch, "E1684", {"start": v(0.14, 0.75) * mm, "end": v(0.14, 0.75) * mm});
            skLineSegment(sketch, "E1685", {"start": v(0.14, 0.75) * mm, "end": v(0.16, 0.75) * mm});
            skLineSegment(sketch, "E1686", {"start": v(0.16, 0.75) * mm, "end": v(0.16, 0.75) * mm});
            skLineSegment(sketch, "E1687", {"start": v(0.16, 0.75) * mm, "end": v(0.17, 0.75) * mm});
            skLineSegment(sketch, "E1688", {"start": v(0.17, 0.75) * mm, "end": v(0.17, 0.75) * mm});
            skLineSegment(sketch, "E1689", {"start": v(0.17, 0.75) * mm, "end": v(0.18, 0.75) * mm});
            skLineSegment(sketch, "E1690", {"start": v(0.18, 0.75) * mm, "end": v(0.18, 0.75) * mm});
            skLineSegment(sketch, "E1691", {"start": v(0.18, 0.75) * mm, "end": v(0.18, 0.74) * mm});
            skLineSegment(sketch, "E1692", {"start": v(0.18, 0.74) * mm, "end": v(0.18, 0.74) * mm});
            skLineSegment(sketch, "E1693", {"start": v(0.18, 0.74) * mm, "end": v(0.17, 0.73) * mm});
            skLineSegment(sketch, "E1694", {"start": v(0.17, 0.73) * mm, "end": v(0.17, 0.73) * mm});
            skLineSegment(sketch, "E1695", {"start": v(0.17, 0.73) * mm, "end": v(0.16, 0.73) * mm});
            skLineSegment(sketch, "E1696", {"start": v(0.16, 0.73) * mm, "end": v(0.14, 0.73) * mm});
            skLineSegment(sketch, "E1697", {"start": v(0.14, 0.73) * mm, "end": v(0.14, 0.73) * mm});
            skLineSegment(sketch, "E1698", {"start": v(0.14, 0.73) * mm, "end": v(0.1, 0.74) * mm});
            skLineSegment(sketch, "E1699", {"start": v(0.1, 0.74) * mm, "end": v(0.1, 0.75) * mm});
            skLineSegment(sketch, "E1700", {"start": v(0.1, 0.75) * mm, "end": v(0.1, 0.75) * mm});
            skLineSegment(sketch, "E1701", {"start": v(0.1, 0.75) * mm, "end": v(0.1, 0.77) * mm});
            skLineSegment(sketch, "E1702", {"start": v(0.1, 0.77) * mm, "end": v(0.1, 0.78) * mm});
            skLineSegment(sketch, "E1703", {"start": v(0.2, 0.73) * mm, "end": v(0.21, 0.81) * mm});
            skLineSegment(sketch, "E1704", {"start": v(0.21, 0.81) * mm, "end": v(0.21, 0.81) * mm});
            skLineSegment(sketch, "E1705", {"start": v(0.21, 0.81) * mm, "end": v(0.22, 0.82) * mm});
            skLineSegment(sketch, "E1706", {"start": v(0.22, 0.82) * mm, "end": v(0.22, 0.82) * mm});
            skLineSegment(sketch, "E1707", {"start": v(0.22, 0.82) * mm, "end": v(0.23, 0.82) * mm});
            skLineSegment(sketch, "E1708", {"start": v(0.23, 0.82) * mm, "end": v(0.23, 0.82) * mm});
            skLineSegment(sketch, "E1709", {"start": v(0.23, 0.82) * mm, "end": v(0.24, 0.81) * mm});
            skLineSegment(sketch, "E1710", {"start": v(0.24, 0.81) * mm, "end": v(0.24, 0.81) * mm});
            skLineSegment(sketch, "E1711", {"start": v(0.24, 0.81) * mm, "end": v(0.24, 0.8) * mm});
            skLineSegment(sketch, "E1712", {"start": v(0.24, 0.8) * mm, "end": v(0.24, 0.8) * mm});
            skLineSegment(sketch, "E1713", {"start": v(0.24, 0.8) * mm, "end": v(0.27, 0.8) * mm});
            skLineSegment(sketch, "E1714", {"start": v(0.27, 0.8) * mm, "end": v(0.27, 0.8) * mm});
            skLineSegment(sketch, "E1715", {"start": v(0.27, 0.8) * mm, "end": v(0.28, 0.8) * mm});
            skLineSegment(sketch, "E1716", {"start": v(0.28, 0.8) * mm, "end": v(0.28, 0.8) * mm});
            skLineSegment(sketch, "E1717", {"start": v(0.28, 0.8) * mm, "end": v(0.29, 0.78) * mm});
            skLineSegment(sketch, "E1718", {"start": v(0.29, 0.78) * mm, "end": v(0.29, 0.78) * mm});
            skLineSegment(sketch, "E1719", {"start": v(0.29, 0.78) * mm, "end": v(0.3, 0.79) * mm});
            skLineSegment(sketch, "E1720", {"start": v(0.3, 0.79) * mm, "end": v(0.3, 0.79) * mm});
            skLineSegment(sketch, "E1721", {"start": v(0.3, 0.79) * mm, "end": v(0.32, 0.79) * mm});
            skLineSegment(sketch, "E1722", {"start": v(0.32, 0.79) * mm, "end": v(0.32, 0.79) * mm});
            skLineSegment(sketch, "E1723", {"start": v(0.32, 0.79) * mm, "end": v(0.33, 0.79) * mm});
            skLineSegment(sketch, "E1724", {"start": v(0.33, 0.79) * mm, "end": v(0.34, 0.77) * mm});
            skLineSegment(sketch, "E1725", {"start": v(0.34, 0.77) * mm, "end": v(0.34, 0.77) * mm});
            skLineSegment(sketch, "E1726", {"start": v(0.34, 0.77) * mm, "end": v(0.35, 0.77) * mm});
            skLineSegment(sketch, "E1727", {"start": v(0.35, 0.77) * mm, "end": v(0.35, 0.74) * mm});
            skLineSegment(sketch, "E1728", {"start": v(0.35, 0.74) * mm, "end": v(0.35, 0.74) * mm});
            skLineSegment(sketch, "E1729", {"start": v(0.35, 0.74) * mm, "end": v(0.33, 0.7) * mm});
            skLineSegment(sketch, "E1730", {"start": v(0.33, 0.7) * mm, "end": v(0.33, 0.69) * mm});
            skLineSegment(sketch, "E1731", {"start": v(0.33, 0.69) * mm, "end": v(0.33, 0.69) * mm});
            skLineSegment(sketch, "E1732", {"start": v(0.33, 0.69) * mm, "end": v(0.32, 0.69) * mm});
            skLineSegment(sketch, "E1733", {"start": v(0.32, 0.69) * mm, "end": v(0.32, 0.69) * mm});
            skLineSegment(sketch, "E1734", {"start": v(0.32, 0.69) * mm, "end": v(0.3, 0.7) * mm});
            skLineSegment(sketch, "E1735", {"start": v(0.3, 0.7) * mm, "end": v(0.3, 0.7) * mm});
            skLineSegment(sketch, "E1736", {"start": v(0.3, 0.7) * mm, "end": v(0.32, 0.75) * mm});
            skLineSegment(sketch, "E1737", {"start": v(0.32, 0.75) * mm, "end": v(0.32, 0.75) * mm});
            skLineSegment(sketch, "E1738", {"start": v(0.32, 0.75) * mm, "end": v(0.32, 0.76) * mm});
            skLineSegment(sketch, "E1739", {"start": v(0.32, 0.76) * mm, "end": v(0.32, 0.76) * mm});
            skLineSegment(sketch, "E1740", {"start": v(0.32, 0.76) * mm, "end": v(0.31, 0.77) * mm});
            skLineSegment(sketch, "E1741", {"start": v(0.31, 0.77) * mm, "end": v(0.3, 0.77) * mm});
            skLineSegment(sketch, "E1742", {"start": v(0.3, 0.77) * mm, "end": v(0.3, 0.77) * mm});
            skLineSegment(sketch, "E1743", {"start": v(0.3, 0.77) * mm, "end": v(0.29, 0.76) * mm});
            skLineSegment(sketch, "E1744", {"start": v(0.29, 0.76) * mm, "end": v(0.29, 0.76) * mm});
            skLineSegment(sketch, "E1745", {"start": v(0.29, 0.76) * mm, "end": v(0.27, 0.7) * mm});
            skLineSegment(sketch, "E1746", {"start": v(0.27, 0.7) * mm, "end": v(0.27, 0.7) * mm});
            skLineSegment(sketch, "E1747", {"start": v(0.27, 0.7) * mm, "end": v(0.26, 0.7) * mm});
            skLineSegment(sketch, "E1748", {"start": v(0.26, 0.7) * mm, "end": v(0.26, 0.7) * mm});
            skLineSegment(sketch, "E1749", {"start": v(0.26, 0.7) * mm, "end": v(0.25, 0.7) * mm});
            skLineSegment(sketch, "E1750", {"start": v(0.25, 0.7) * mm, "end": v(0.25, 0.7) * mm});
            skLineSegment(sketch, "E1751", {"start": v(0.25, 0.7) * mm, "end": v(0.25, 0.71) * mm});
            skLineSegment(sketch, "E1752", {"start": v(0.25, 0.71) * mm, "end": v(0.25, 0.72) * mm});
            skLineSegment(sketch, "E1753", {"start": v(0.25, 0.72) * mm, "end": v(0.26, 0.76) * mm});
            skLineSegment(sketch, "E1754", {"start": v(0.26, 0.76) * mm, "end": v(0.26, 0.76) * mm});
            skLineSegment(sketch, "E1755", {"start": v(0.26, 0.76) * mm, "end": v(0.26, 0.78) * mm});
            skLineSegment(sketch, "E1756", {"start": v(0.26, 0.78) * mm, "end": v(0.26, 0.78) * mm});
            skLineSegment(sketch, "E1757", {"start": v(0.26, 0.78) * mm, "end": v(0.25, 0.79) * mm});
            skLineSegment(sketch, "E1758", {"start": v(0.25, 0.79) * mm, "end": v(0.25, 0.79) * mm});
            skLineSegment(sketch, "E1759", {"start": v(0.25, 0.79) * mm, "end": v(0.24, 0.78) * mm});
            skLineSegment(sketch, "E1760", {"start": v(0.24, 0.78) * mm, "end": v(0.24, 0.78) * mm});
            skLineSegment(sketch, "E1761", {"start": v(0.24, 0.78) * mm, "end": v(0.23, 0.77) * mm});
            skLineSegment(sketch, "E1762", {"start": v(0.23, 0.77) * mm, "end": v(0.23, 0.77) * mm});
            skLineSegment(sketch, "E1763", {"start": v(0.23, 0.77) * mm, "end": v(0.22, 0.73) * mm});
            skLineSegment(sketch, "E1764", {"start": v(0.22, 0.73) * mm, "end": v(0.22, 0.73) * mm});
            skLineSegment(sketch, "E1765", {"start": v(0.22, 0.73) * mm, "end": v(0.21, 0.72) * mm});
            skLineSegment(sketch, "E1766", {"start": v(0.21, 0.72) * mm, "end": v(0.21, 0.72) * mm});
            skLineSegment(sketch, "E1767", {"start": v(0.21, 0.72) * mm, "end": v(0.2, 0.72) * mm});
            skLineSegment(sketch, "E1768", {"start": v(0.2, 0.72) * mm, "end": v(0.2, 0.72) * mm});
            skLineSegment(sketch, "E1769", {"start": v(0.2, 0.72) * mm, "end": v(0.2, 0.73) * mm});
            skLineSegment(sketch, "E1770", {"start": v(0.2, 0.73) * mm, "end": v(0.2, 0.73) * mm});
            skLineSegment(sketch, "E1771", {"start": v(0.39, 0.72) * mm, "end": v(0.41, 0.7) * mm});
            skLineSegment(sketch, "E1772", {"start": v(0.41, 0.7) * mm, "end": v(0.42, 0.7) * mm});
            skLineSegment(sketch, "E1773", {"start": v(0.42, 0.7) * mm, "end": v(0.42, 0.7) * mm});
            skLineSegment(sketch, "E1774", {"start": v(0.42, 0.7) * mm, "end": v(0.42, 0.72) * mm});
            skLineSegment(sketch, "E1775", {"start": v(0.42, 0.72) * mm, "end": v(0.42, 0.72) * mm});
            skLineSegment(sketch, "E1776", {"start": v(0.42, 0.72) * mm, "end": v(0.41, 0.73) * mm});
            skLineSegment(sketch, "E1777", {"start": v(0.41, 0.73) * mm, "end": v(0.41, 0.73) * mm});
            skLineSegment(sketch, "E1778", {"start": v(0.41, 0.73) * mm, "end": v(0.4, 0.73) * mm});
            skLineSegment(sketch, "E1779", {"start": v(0.4, 0.73) * mm, "end": v(0.4, 0.73) * mm});
            skLineSegment(sketch, "E1780", {"start": v(0.4, 0.73) * mm, "end": v(0.4, 0.72) * mm});
            skLineSegment(sketch, "E1781", {"start": v(0.4, 0.72) * mm, "end": v(0.4, 0.72) * mm});
            skLineSegment(sketch, "E1782", {"start": v(0.4, 0.72) * mm, "end": v(0.39, 0.72) * mm});
            skLineSegment(sketch, "E1783", {"start": v(0.36, 0.71) * mm, "end": v(0.36, 0.73) * mm});
            skLineSegment(sketch, "E1784", {"start": v(0.36, 0.73) * mm, "end": v(0.36, 0.73) * mm});
            skLineSegment(sketch, "E1785", {"start": v(0.36, 0.73) * mm, "end": v(0.39, 0.75) * mm});
            skLineSegment(sketch, "E1786", {"start": v(0.39, 0.75) * mm, "end": v(0.39, 0.75) * mm});
            skLineSegment(sketch, "E1787", {"start": v(0.39, 0.75) * mm, "end": v(0.4, 0.75) * mm});
            skLineSegment(sketch, "E1788", {"start": v(0.4, 0.75) * mm, "end": v(0.42, 0.75) * mm});
            skLineSegment(sketch, "E1789", {"start": v(0.42, 0.75) * mm, "end": v(0.42, 0.75) * mm});
            skLineSegment(sketch, "E1790", {"start": v(0.42, 0.75) * mm, "end": v(0.43, 0.74) * mm});
            skLineSegment(sketch, "E1791", {"start": v(0.43, 0.74) * mm, "end": v(0.44, 0.72) * mm});
            skLineSegment(sketch, "E1792", {"start": v(0.44, 0.72) * mm, "end": v(0.45, 0.72) * mm});
            skLineSegment(sketch, "E1793", {"start": v(0.45, 0.72) * mm, "end": v(0.45, 0.72) * mm});
            skLineSegment(sketch, "E1794", {"start": v(0.45, 0.72) * mm, "end": v(0.45, 0.7) * mm});
            skLineSegment(sketch, "E1795", {"start": v(0.45, 0.7) * mm, "end": v(0.44, 0.7) * mm});
            skLineSegment(sketch, "E1796", {"start": v(0.44, 0.7) * mm, "end": v(0.44, 0.69) * mm});
            skLineSegment(sketch, "E1797", {"start": v(0.44, 0.69) * mm, "end": v(0.44, 0.68) * mm});
            skLineSegment(sketch, "E1798", {"start": v(0.44, 0.68) * mm, "end": v(0.44, 0.68) * mm});
            skLineSegment(sketch, "E1799", {"start": v(0.44, 0.68) * mm, "end": v(0.43, 0.68) * mm});
            skLineSegment(sketch, "E1800", {"start": v(0.43, 0.68) * mm, "end": v(0.43, 0.68) * mm});
            skLineSegment(sketch, "E1801", {"start": v(0.43, 0.68) * mm, "end": v(0.42, 0.68) * mm});
            skLineSegment(sketch, "E1802", {"start": v(0.42, 0.68) * mm, "end": v(0.42, 0.68) * mm});
            skLineSegment(sketch, "E1803", {"start": v(0.42, 0.68) * mm, "end": v(0.38, 0.7) * mm});
            skLineSegment(sketch, "E1804", {"start": v(0.38, 0.7) * mm, "end": v(0.38, 0.7) * mm});
            skLineSegment(sketch, "E1805", {"start": v(0.38, 0.7) * mm, "end": v(0.38, 0.68) * mm});
            skLineSegment(sketch, "E1806", {"start": v(0.38, 0.68) * mm, "end": v(0.38, 0.68) * mm});
            skLineSegment(sketch, "E1807", {"start": v(0.38, 0.68) * mm, "end": v(0.4, 0.67) * mm});
            skLineSegment(sketch, "E1808", {"start": v(0.4, 0.67) * mm, "end": v(0.4, 0.67) * mm});
            skLineSegment(sketch, "E1809", {"start": v(0.4, 0.67) * mm, "end": v(0.42, 0.67) * mm});
            skLineSegment(sketch, "E1810", {"start": v(0.42, 0.67) * mm, "end": v(0.42, 0.67) * mm});
            skLineSegment(sketch, "E1811", {"start": v(0.42, 0.67) * mm, "end": v(0.42, 0.66) * mm});
            skLineSegment(sketch, "E1812", {"start": v(0.42, 0.66) * mm, "end": v(0.42, 0.66) * mm});
            skLineSegment(sketch, "E1813", {"start": v(0.42, 0.66) * mm, "end": v(0.42, 0.65) * mm});
            skLineSegment(sketch, "E1814", {"start": v(0.42, 0.65) * mm, "end": v(0.42, 0.65) * mm});
            skLineSegment(sketch, "E1815", {"start": v(0.42, 0.65) * mm, "end": v(0.4, 0.65) * mm});
            skLineSegment(sketch, "E1816", {"start": v(0.4, 0.65) * mm, "end": v(0.4, 0.65) * mm});
            skLineSegment(sketch, "E1817", {"start": v(0.4, 0.65) * mm, "end": v(0.38, 0.65) * mm});
            skLineSegment(sketch, "E1818", {"start": v(0.38, 0.65) * mm, "end": v(0.38, 0.65) * mm});
            skLineSegment(sketch, "E1819", {"start": v(0.38, 0.65) * mm, "end": v(0.36, 0.68) * mm});
            skLineSegment(sketch, "E1820", {"start": v(0.36, 0.68) * mm, "end": v(0.35, 0.68) * mm});
            skLineSegment(sketch, "E1821", {"start": v(0.35, 0.68) * mm, "end": v(0.35, 0.68) * mm});
            skLineSegment(sketch, "E1822", {"start": v(0.35, 0.68) * mm, "end": v(0.35, 0.7) * mm});
            skLineSegment(sketch, "E1823", {"start": v(0.35, 0.7) * mm, "end": v(0.36, 0.71) * mm});
            skLineSegment(sketch, "E1824", {"start": v(0.44, 0.66) * mm, "end": v(0.5, 0.74) * mm});
            skLineSegment(sketch, "E1825", {"start": v(0.5, 0.74) * mm, "end": v(0.5, 0.74) * mm});
            skLineSegment(sketch, "E1826", {"start": v(0.5, 0.74) * mm, "end": v(0.51, 0.74) * mm});
            skLineSegment(sketch, "E1827", {"start": v(0.51, 0.74) * mm, "end": v(0.51, 0.74) * mm});
            skLineSegment(sketch, "E1828", {"start": v(0.51, 0.74) * mm, "end": v(0.52, 0.74) * mm});
            skLineSegment(sketch, "E1829", {"start": v(0.52, 0.74) * mm, "end": v(0.52, 0.73) * mm});
            skLineSegment(sketch, "E1830", {"start": v(0.52, 0.73) * mm, "end": v(0.52, 0.73) * mm});
            skLineSegment(sketch, "E1831", {"start": v(0.52, 0.73) * mm, "end": v(0.5, 0.7) * mm});
            skLineSegment(sketch, "E1832", {"start": v(0.5, 0.7) * mm, "end": v(0.52, 0.69) * mm});
            skLineSegment(sketch, "E1833", {"start": v(0.52, 0.69) * mm, "end": v(0.52, 0.68) * mm});
            skLineSegment(sketch, "E1834", {"start": v(0.52, 0.68) * mm, "end": v(0.53, 0.68) * mm});
            skLineSegment(sketch, "E1835", {"start": v(0.53, 0.68) * mm, "end": v(0.53, 0.68) * mm});
            skLineSegment(sketch, "E1836", {"start": v(0.53, 0.68) * mm, "end": v(0.52, 0.67) * mm});
            skLineSegment(sketch, "E1837", {"start": v(0.52, 0.67) * mm, "end": v(0.52, 0.67) * mm});
            skLineSegment(sketch, "E1838", {"start": v(0.52, 0.67) * mm, "end": v(0.51, 0.67) * mm});
            skLineSegment(sketch, "E1839", {"start": v(0.51, 0.67) * mm, "end": v(0.51, 0.67) * mm});
            skLineSegment(sketch, "E1840", {"start": v(0.51, 0.67) * mm, "end": v(0.5, 0.68) * mm});
            skLineSegment(sketch, "E1841", {"start": v(0.5, 0.68) * mm, "end": v(0.47, 0.64) * mm});
            skLineSegment(sketch, "E1842", {"start": v(0.47, 0.64) * mm, "end": v(0.47, 0.64) * mm});
            skLineSegment(sketch, "E1843", {"start": v(0.47, 0.64) * mm, "end": v(0.47, 0.63) * mm});
            skLineSegment(sketch, "E1844", {"start": v(0.47, 0.63) * mm, "end": v(0.47, 0.63) * mm});
            skLineSegment(sketch, "E1845", {"start": v(0.47, 0.63) * mm, "end": v(0.48, 0.62) * mm});
            skLineSegment(sketch, "E1846", {"start": v(0.48, 0.62) * mm, "end": v(0.48, 0.62) * mm});
            skLineSegment(sketch, "E1847", {"start": v(0.48, 0.62) * mm, "end": v(0.48, 0.6) * mm});
            skLineSegment(sketch, "E1848", {"start": v(0.48, 0.6) * mm, "end": v(0.48, 0.6) * mm});
            skLineSegment(sketch, "E1849", {"start": v(0.48, 0.6) * mm, "end": v(0.47, 0.6) * mm});
            skLineSegment(sketch, "E1850", {"start": v(0.47, 0.6) * mm, "end": v(0.47, 0.6) * mm});
            skLineSegment(sketch, "E1851", {"start": v(0.47, 0.6) * mm, "end": v(0.46, 0.6) * mm});
            skLineSegment(sketch, "E1852", {"start": v(0.46, 0.6) * mm, "end": v(0.45, 0.61) * mm});
            skLineSegment(sketch, "E1853", {"start": v(0.45, 0.61) * mm, "end": v(0.44, 0.63) * mm});
            skLineSegment(sketch, "E1854", {"start": v(0.44, 0.63) * mm, "end": v(0.44, 0.65) * mm});
            skLineSegment(sketch, "E1855", {"start": v(0.44, 0.65) * mm, "end": v(0.44, 0.66) * mm});
            skLineSegment(sketch, "E1856", {"start": v(0.54, 0.62) * mm, "end": v(0.56, 0.6) * mm});
            skLineSegment(sketch, "E1857", {"start": v(0.56, 0.6) * mm, "end": v(0.56, 0.6) * mm});
            skLineSegment(sketch, "E1858", {"start": v(0.56, 0.6) * mm, "end": v(0.57, 0.6) * mm});
            skLineSegment(sketch, "E1859", {"start": v(0.57, 0.6) * mm, "end": v(0.57, 0.6) * mm});
            skLineSegment(sketch, "E1860", {"start": v(0.57, 0.6) * mm, "end": v(0.57, 0.62) * mm});
            skLineSegment(sketch, "E1861", {"start": v(0.57, 0.62) * mm, "end": v(0.57, 0.62) * mm});
            skLineSegment(sketch, "E1862", {"start": v(0.57, 0.62) * mm, "end": v(0.57, 0.63) * mm});
            skLineSegment(sketch, "E1863", {"start": v(0.57, 0.63) * mm, "end": v(0.57, 0.63) * mm});
            skLineSegment(sketch, "E1864", {"start": v(0.57, 0.63) * mm, "end": v(0.56, 0.63) * mm});
            skLineSegment(sketch, "E1865", {"start": v(0.56, 0.63) * mm, "end": v(0.56, 0.63) * mm});
            skLineSegment(sketch, "E1866", {"start": v(0.56, 0.63) * mm, "end": v(0.55, 0.63) * mm});
            skLineSegment(sketch, "E1867", {"start": v(0.55, 0.63) * mm, "end": v(0.55, 0.63) * mm});
            skLineSegment(sketch, "E1868", {"start": v(0.55, 0.63) * mm, "end": v(0.54, 0.63) * mm});
            skLineSegment(sketch, "E1869", {"start": v(0.54, 0.63) * mm, "end": v(0.54, 0.63) * mm});
            skLineSegment(sketch, "E1870", {"start": v(0.54, 0.63) * mm, "end": v(0.54, 0.62) * mm});
            skLineSegment(sketch, "E1871", {"start": v(0.5, 0.63) * mm, "end": v(0.52, 0.64) * mm});
            skLineSegment(sketch, "E1872", {"start": v(0.52, 0.64) * mm, "end": v(0.52, 0.64) * mm});
            skLineSegment(sketch, "E1873", {"start": v(0.52, 0.64) * mm, "end": v(0.54, 0.66) * mm});
            skLineSegment(sketch, "E1874", {"start": v(0.54, 0.66) * mm, "end": v(0.55, 0.66) * mm});
            skLineSegment(sketch, "E1875", {"start": v(0.55, 0.66) * mm, "end": v(0.55, 0.66) * mm});
            skLineSegment(sketch, "E1876", {"start": v(0.55, 0.66) * mm, "end": v(0.58, 0.65) * mm});
            skLineSegment(sketch, "E1877", {"start": v(0.58, 0.65) * mm, "end": v(0.58, 0.65) * mm});
            skLineSegment(sketch, "E1878", {"start": v(0.58, 0.65) * mm, "end": v(0.58, 0.64) * mm});
            skLineSegment(sketch, "E1879", {"start": v(0.58, 0.64) * mm, "end": v(0.6, 0.62) * mm});
            skLineSegment(sketch, "E1880", {"start": v(0.6, 0.62) * mm, "end": v(0.6, 0.62) * mm});
            skLineSegment(sketch, "E1881", {"start": v(0.6, 0.62) * mm, "end": v(0.6, 0.61) * mm});
            skLineSegment(sketch, "E1882", {"start": v(0.6, 0.61) * mm, "end": v(0.59, 0.6) * mm});
            skLineSegment(sketch, "E1883", {"start": v(0.59, 0.6) * mm, "end": v(0.59, 0.59) * mm});
            skLineSegment(sketch, "E1884", {"start": v(0.59, 0.59) * mm, "end": v(0.59, 0.59) * mm});
            skLineSegment(sketch, "E1885", {"start": v(0.59, 0.59) * mm, "end": v(0.58, 0.58) * mm});
            skLineSegment(sketch, "E1886", {"start": v(0.58, 0.58) * mm, "end": v(0.58, 0.58) * mm});
            skLineSegment(sketch, "E1887", {"start": v(0.58, 0.58) * mm, "end": v(0.57, 0.58) * mm});
            skLineSegment(sketch, "E1888", {"start": v(0.57, 0.58) * mm, "end": v(0.57, 0.58) * mm});
            skLineSegment(sketch, "E1889", {"start": v(0.57, 0.58) * mm, "end": v(0.56, 0.59) * mm});
            skLineSegment(sketch, "E1890", {"start": v(0.56, 0.59) * mm, "end": v(0.56, 0.59) * mm});
            skLineSegment(sketch, "E1891", {"start": v(0.56, 0.59) * mm, "end": v(0.53, 0.61) * mm});
            skLineSegment(sketch, "E1892", {"start": v(0.53, 0.61) * mm, "end": v(0.53, 0.6) * mm});
            skLineSegment(sketch, "E1893", {"start": v(0.53, 0.6) * mm, "end": v(0.53, 0.6) * mm});
            skLineSegment(sketch, "E1894", {"start": v(0.53, 0.6) * mm, "end": v(0.52, 0.6) * mm});
            skLineSegment(sketch, "E1895", {"start": v(0.52, 0.6) * mm, "end": v(0.52, 0.6) * mm});
            skLineSegment(sketch, "E1896", {"start": v(0.52, 0.6) * mm, "end": v(0.53, 0.58) * mm});
            skLineSegment(sketch, "E1897", {"start": v(0.53, 0.58) * mm, "end": v(0.53, 0.58) * mm});
            skLineSegment(sketch, "E1898", {"start": v(0.53, 0.58) * mm, "end": v(0.55, 0.57) * mm});
            skLineSegment(sketch, "E1899", {"start": v(0.55, 0.57) * mm, "end": v(0.55, 0.57) * mm});
            skLineSegment(sketch, "E1900", {"start": v(0.55, 0.57) * mm, "end": v(0.56, 0.57) * mm});
            skLineSegment(sketch, "E1901", {"start": v(0.56, 0.57) * mm, "end": v(0.56, 0.57) * mm});
            skLineSegment(sketch, "E1902", {"start": v(0.56, 0.57) * mm, "end": v(0.56, 0.56) * mm});
            skLineSegment(sketch, "E1903", {"start": v(0.56, 0.56) * mm, "end": v(0.56, 0.56) * mm});
            skLineSegment(sketch, "E1904", {"start": v(0.56, 0.56) * mm, "end": v(0.56, 0.55) * mm});
            skLineSegment(sketch, "E1905", {"start": v(0.56, 0.55) * mm, "end": v(0.56, 0.55) * mm});
            skLineSegment(sketch, "E1906", {"start": v(0.56, 0.55) * mm, "end": v(0.55, 0.55) * mm});
            skLineSegment(sketch, "E1907", {"start": v(0.55, 0.55) * mm, "end": v(0.54, 0.55) * mm});
            skLineSegment(sketch, "E1908", {"start": v(0.54, 0.55) * mm, "end": v(0.54, 0.55) * mm});
            skLineSegment(sketch, "E1909", {"start": v(0.54, 0.55) * mm, "end": v(0.52, 0.56) * mm});
            skLineSegment(sketch, "E1910", {"start": v(0.52, 0.56) * mm, "end": v(0.52, 0.56) * mm});
            skLineSegment(sketch, "E1911", {"start": v(0.52, 0.56) * mm, "end": v(0.5, 0.6) * mm});
            skLineSegment(sketch, "E1912", {"start": v(0.5, 0.6) * mm, "end": v(0.5, 0.6) * mm});
            skLineSegment(sketch, "E1913", {"start": v(0.5, 0.6) * mm, "end": v(0.5, 0.62) * mm});
            skLineSegment(sketch, "E1914", {"start": v(0.5, 0.62) * mm, "end": v(0.5, 0.63) * mm});
            skLineSegment(sketch, "E1915", {"start": v(0.6, 0.54) * mm, "end": v(0.6, 0.54) * mm});
            skLineSegment(sketch, "E1916", {"start": v(0.6, 0.54) * mm, "end": v(0.6, 0.53) * mm});
            skLineSegment(sketch, "E1917", {"start": v(0.6, 0.53) * mm, "end": v(0.6, 0.53) * mm});
            skLineSegment(sketch, "E1918", {"start": v(0.6, 0.53) * mm, "end": v(0.6, 0.52) * mm});
            skLineSegment(sketch, "E1919", {"start": v(0.6, 0.52) * mm, "end": v(0.6, 0.52) * mm});
            skLineSegment(sketch, "E1920", {"start": v(0.6, 0.52) * mm, "end": v(0.61, 0.52) * mm});
            skLineSegment(sketch, "E1921", {"start": v(0.61, 0.52) * mm, "end": v(0.62, 0.52) * mm});
            skLineSegment(sketch, "E1922", {"start": v(0.62, 0.52) * mm, "end": v(0.62, 0.52) * mm});
            skLineSegment(sketch, "E1923", {"start": v(0.62, 0.52) * mm, "end": v(0.63, 0.53) * mm});
            skLineSegment(sketch, "E1924", {"start": v(0.63, 0.53) * mm, "end": v(0.62, 0.53) * mm});
            skLineSegment(sketch, "E1925", {"start": v(0.62, 0.53) * mm, "end": v(0.62, 0.53) * mm});
            skLineSegment(sketch, "E1926", {"start": v(0.62, 0.53) * mm, "end": v(0.6, 0.54) * mm});
            skLineSegment(sketch, "E1927", {"start": v(0.57, 0.55) * mm, "end": v(0.58, 0.56) * mm});
            skLineSegment(sketch, "E1928", {"start": v(0.58, 0.56) * mm, "end": v(0.6, 0.56) * mm});
            skLineSegment(sketch, "E1929", {"start": v(0.6, 0.56) * mm, "end": v(0.6, 0.56) * mm});
            skLineSegment(sketch, "E1930", {"start": v(0.6, 0.56) * mm, "end": v(0.63, 0.54) * mm});
            skLineSegment(sketch, "E1931", {"start": v(0.63, 0.54) * mm, "end": v(0.63, 0.54) * mm});
            skLineSegment(sketch, "E1932", {"start": v(0.63, 0.54) * mm, "end": v(0.64, 0.54) * mm});
            skLineSegment(sketch, "E1933", {"start": v(0.64, 0.54) * mm, "end": v(0.64, 0.54) * mm});
            skLineSegment(sketch, "E1934", {"start": v(0.64, 0.54) * mm, "end": v(0.64, 0.55) * mm});
            skLineSegment(sketch, "E1935", {"start": v(0.64, 0.55) * mm, "end": v(0.64, 0.55) * mm});
            skLineSegment(sketch, "E1936", {"start": v(0.64, 0.55) * mm, "end": v(0.64, 0.56) * mm});
            skLineSegment(sketch, "E1937", {"start": v(0.64, 0.56) * mm, "end": v(0.64, 0.56) * mm});
            skLineSegment(sketch, "E1938", {"start": v(0.64, 0.56) * mm, "end": v(0.64, 0.57) * mm});
            skLineSegment(sketch, "E1939", {"start": v(0.64, 0.57) * mm, "end": v(0.63, 0.57) * mm});
            skLineSegment(sketch, "E1940", {"start": v(0.63, 0.57) * mm, "end": v(0.62, 0.57) * mm});
            skLineSegment(sketch, "E1941", {"start": v(0.62, 0.57) * mm, "end": v(0.62, 0.57) * mm});
            skLineSegment(sketch, "E1942", {"start": v(0.62, 0.57) * mm, "end": v(0.62, 0.58) * mm});
            skLineSegment(sketch, "E1943", {"start": v(0.62, 0.58) * mm, "end": v(0.62, 0.58) * mm});
            skLineSegment(sketch, "E1944", {"start": v(0.62, 0.58) * mm, "end": v(0.61, 0.58) * mm});
            skLineSegment(sketch, "E1945", {"start": v(0.61, 0.58) * mm, "end": v(0.61, 0.58) * mm});
            skLineSegment(sketch, "E1946", {"start": v(0.61, 0.58) * mm, "end": v(0.62, 0.58) * mm});
            skLineSegment(sketch, "E1947", {"start": v(0.62, 0.58) * mm, "end": v(0.62, 0.6) * mm});
            skLineSegment(sketch, "E1948", {"start": v(0.62, 0.6) * mm, "end": v(0.62, 0.6) * mm});
            skLineSegment(sketch, "E1949", {"start": v(0.62, 0.6) * mm, "end": v(0.63, 0.6) * mm});
            skLineSegment(sketch, "E1950", {"start": v(0.63, 0.6) * mm, "end": v(0.63, 0.6) * mm});
            skLineSegment(sketch, "E1951", {"start": v(0.63, 0.6) * mm, "end": v(0.64, 0.6) * mm});
            skLineSegment(sketch, "E1952", {"start": v(0.64, 0.6) * mm, "end": v(0.65, 0.58) * mm});
            skLineSegment(sketch, "E1953", {"start": v(0.65, 0.58) * mm, "end": v(0.65, 0.58) * mm});
            skLineSegment(sketch, "E1954", {"start": v(0.65, 0.58) * mm, "end": v(0.66, 0.58) * mm});
            skLineSegment(sketch, "E1955", {"start": v(0.66, 0.58) * mm, "end": v(0.67, 0.55) * mm});
            skLineSegment(sketch, "E1956", {"start": v(0.67, 0.55) * mm, "end": v(0.67, 0.55) * mm});
            skLineSegment(sketch, "E1957", {"start": v(0.67, 0.55) * mm, "end": v(0.67, 0.54) * mm});
            skLineSegment(sketch, "E1958", {"start": v(0.67, 0.54) * mm, "end": v(0.66, 0.52) * mm});
            skLineSegment(sketch, "E1959", {"start": v(0.66, 0.52) * mm, "end": v(0.66, 0.52) * mm});
            skLineSegment(sketch, "E1960", {"start": v(0.66, 0.52) * mm, "end": v(0.62, 0.48) * mm});
            skLineSegment(sketch, "E1961", {"start": v(0.62, 0.48) * mm, "end": v(0.62, 0.48) * mm});
            skLineSegment(sketch, "E1962", {"start": v(0.62, 0.48) * mm, "end": v(0.61, 0.48) * mm});
            skLineSegment(sketch, "E1963", {"start": v(0.61, 0.48) * mm, "end": v(0.61, 0.48) * mm});
            skLineSegment(sketch, "E1964", {"start": v(0.61, 0.48) * mm, "end": v(0.6, 0.48) * mm});
            skLineSegment(sketch, "E1965", {"start": v(0.6, 0.48) * mm, "end": v(0.6, 0.49) * mm});
            skLineSegment(sketch, "E1966", {"start": v(0.6, 0.49) * mm, "end": v(0.6, 0.49) * mm});
            skLineSegment(sketch, "E1967", {"start": v(0.6, 0.49) * mm, "end": v(0.6, 0.5) * mm});
            skLineSegment(sketch, "E1968", {"start": v(0.6, 0.5) * mm, "end": v(0.6, 0.5) * mm});
            skLineSegment(sketch, "E1969", {"start": v(0.6, 0.5) * mm, "end": v(0.57, 0.51) * mm});
            skLineSegment(sketch, "E1970", {"start": v(0.57, 0.51) * mm, "end": v(0.57, 0.52) * mm});
            skLineSegment(sketch, "E1971", {"start": v(0.57, 0.52) * mm, "end": v(0.57, 0.52) * mm});
            skLineSegment(sketch, "E1972", {"start": v(0.57, 0.52) * mm, "end": v(0.56, 0.53) * mm});
            skLineSegment(sketch, "E1973", {"start": v(0.56, 0.53) * mm, "end": v(0.56, 0.53) * mm});
            skLineSegment(sketch, "E1974", {"start": v(0.56, 0.53) * mm, "end": v(0.56, 0.54) * mm});
            skLineSegment(sketch, "E1975", {"start": v(0.56, 0.54) * mm, "end": v(0.57, 0.55) * mm});
            skLineSegment(sketch, "E1976", {"start": v(0.57, 0.55) * mm, "end": v(0.57, 0.55) * mm});
            skLineSegment(sketch, "E1977", {"start": v(0.66, 0.5) * mm, "end": v(0.7, 0.52) * mm});
            skLineSegment(sketch, "E1978", {"start": v(0.7, 0.52) * mm, "end": v(0.7, 0.52) * mm});
            skLineSegment(sketch, "E1979", {"start": v(0.7, 0.52) * mm, "end": v(0.71, 0.52) * mm});
            skLineSegment(sketch, "E1980", {"start": v(0.71, 0.52) * mm, "end": v(0.71, 0.51) * mm});
            skLineSegment(sketch, "E1981", {"start": v(0.71, 0.51) * mm, "end": v(0.71, 0.5) * mm});
            skLineSegment(sketch, "E1982", {"start": v(0.71, 0.5) * mm, "end": v(0.71, 0.5) * mm});
            skLineSegment(sketch, "E1983", {"start": v(0.71, 0.5) * mm, "end": v(0.67, 0.47) * mm});
            skLineSegment(sketch, "E1984", {"start": v(0.67, 0.47) * mm, "end": v(0.67, 0.47) * mm});
            skLineSegment(sketch, "E1985", {"start": v(0.67, 0.47) * mm, "end": v(0.67, 0.46) * mm});
            skLineSegment(sketch, "E1986", {"start": v(0.67, 0.46) * mm, "end": v(0.67, 0.46) * mm});
            skLineSegment(sketch, "E1987", {"start": v(0.67, 0.46) * mm, "end": v(0.66, 0.46) * mm});
            skLineSegment(sketch, "E1988", {"start": v(0.66, 0.46) * mm, "end": v(0.67, 0.44) * mm});
            skLineSegment(sketch, "E1989", {"start": v(0.67, 0.44) * mm, "end": v(0.67, 0.44) * mm});
            skLineSegment(sketch, "E1990", {"start": v(0.67, 0.44) * mm, "end": v(0.68, 0.44) * mm});
            skLineSegment(sketch, "E1991", {"start": v(0.68, 0.44) * mm, "end": v(0.68, 0.44) * mm});
            skLineSegment(sketch, "E1992", {"start": v(0.68, 0.44) * mm, "end": v(0.7, 0.44) * mm});
            skLineSegment(sketch, "E1993", {"start": v(0.7, 0.44) * mm, "end": v(0.7, 0.44) * mm});
            skLineSegment(sketch, "E1994", {"start": v(0.7, 0.44) * mm, "end": v(0.73, 0.47) * mm});
            skLineSegment(sketch, "E1995", {"start": v(0.73, 0.47) * mm, "end": v(0.73, 0.47) * mm});
            skLineSegment(sketch, "E1996", {"start": v(0.73, 0.47) * mm, "end": v(0.74, 0.47) * mm});
            skLineSegment(sketch, "E1997", {"start": v(0.74, 0.47) * mm, "end": v(0.74, 0.47) * mm});
            skLineSegment(sketch, "E1998", {"start": v(0.74, 0.47) * mm, "end": v(0.75, 0.47) * mm});
            skLineSegment(sketch, "E1999", {"start": v(0.75, 0.47) * mm, "end": v(0.75, 0.46) * mm});
            skLineSegment(sketch, "E2000", {"start": v(0.75, 0.46) * mm, "end": v(0.75, 0.46) * mm});
            skLineSegment(sketch, "E2001", {"start": v(0.75, 0.46) * mm, "end": v(0.75, 0.45) * mm});
            skLineSegment(sketch, "E2002", {"start": v(0.75, 0.45) * mm, "end": v(0.75, 0.45) * mm});
            skLineSegment(sketch, "E2003", {"start": v(0.75, 0.45) * mm, "end": v(0.71, 0.42) * mm});
            skLineSegment(sketch, "E2004", {"start": v(0.71, 0.42) * mm, "end": v(0.7, 0.42) * mm});
            skLineSegment(sketch, "E2005", {"start": v(0.7, 0.42) * mm, "end": v(0.68, 0.41) * mm});
            skLineSegment(sketch, "E2006", {"start": v(0.68, 0.41) * mm, "end": v(0.68, 0.41) * mm});
            skLineSegment(sketch, "E2007", {"start": v(0.68, 0.41) * mm, "end": v(0.65, 0.43) * mm});
            skLineSegment(sketch, "E2008", {"start": v(0.65, 0.43) * mm, "end": v(0.65, 0.43) * mm});
            skLineSegment(sketch, "E2009", {"start": v(0.65, 0.43) * mm, "end": v(0.64, 0.46) * mm});
            skLineSegment(sketch, "E2010", {"start": v(0.64, 0.46) * mm, "end": v(0.64, 0.46) * mm});
            skLineSegment(sketch, "E2011", {"start": v(0.64, 0.46) * mm, "end": v(0.65, 0.49) * mm});
            skLineSegment(sketch, "E2012", {"start": v(0.65, 0.49) * mm, "end": v(0.66, 0.5) * mm});
            skLineSegment(sketch, "E2013", {"start": v(0.75, 0.37) * mm, "end": v(0.75, 0.37) * mm});
            skLineSegment(sketch, "E2014", {"start": v(0.75, 0.37) * mm, "end": v(0.76, 0.37) * mm});
            skLineSegment(sketch, "E2015", {"start": v(0.76, 0.37) * mm, "end": v(0.76, 0.37) * mm});
            skLineSegment(sketch, "E2016", {"start": v(0.76, 0.37) * mm, "end": v(0.79, 0.32) * mm});
            skLineSegment(sketch, "E2017", {"start": v(0.79, 0.32) * mm, "end": v(0.79, 0.32) * mm});
            skLineSegment(sketch, "E2018", {"start": v(0.79, 0.32) * mm, "end": v(0.79, 0.31) * mm});
            skLineSegment(sketch, "E2019", {"start": v(0.79, 0.31) * mm, "end": v(0.78, 0.3) * mm});
            skLineSegment(sketch, "E2020", {"start": v(0.78, 0.3) * mm, "end": v(0.78, 0.3) * mm});
            skLineSegment(sketch, "E2021", {"start": v(0.78, 0.3) * mm, "end": v(0.77, 0.3) * mm});
            skLineSegment(sketch, "E2022", {"start": v(0.77, 0.3) * mm, "end": v(0.77, 0.31) * mm});
            skLineSegment(sketch, "E2023", {"start": v(0.77, 0.31) * mm, "end": v(0.77, 0.31) * mm});
            skLineSegment(sketch, "E2024", {"start": v(0.77, 0.31) * mm, "end": v(0.74, 0.36) * mm});
            skLineSegment(sketch, "E2025", {"start": v(0.74, 0.36) * mm, "end": v(0.74, 0.36) * mm});
            skLineSegment(sketch, "E2026", {"start": v(0.74, 0.36) * mm, "end": v(0.74, 0.37) * mm});
            skLineSegment(sketch, "E2027", {"start": v(0.74, 0.37) * mm, "end": v(0.74, 0.37) * mm});
            skLineSegment(sketch, "E2028", {"start": v(0.74, 0.37) * mm, "end": v(0.75, 0.37) * mm});
            skLineSegment(sketch, "E2029", {"start": v(0.77, 0.24) * mm, "end": v(0.85, 0.26) * mm});
            skLineSegment(sketch, "E2030", {"start": v(0.85, 0.26) * mm, "end": v(0.85, 0.26) * mm});
            skLineSegment(sketch, "E2031", {"start": v(0.85, 0.26) * mm, "end": v(0.86, 0.26) * mm});
            skLineSegment(sketch, "E2032", {"start": v(0.86, 0.26) * mm, "end": v(0.86, 0.26) * mm});
            skLineSegment(sketch, "E2033", {"start": v(0.86, 0.26) * mm, "end": v(0.86, 0.25) * mm});
            skLineSegment(sketch, "E2034", {"start": v(0.86, 0.25) * mm, "end": v(0.86, 0.25) * mm});
            skLineSegment(sketch, "E2035", {"start": v(0.86, 0.25) * mm, "end": v(0.86, 0.24) * mm});
            skLineSegment(sketch, "E2036", {"start": v(0.86, 0.24) * mm, "end": v(0.86, 0.24) * mm});
            skLineSegment(sketch, "E2037", {"start": v(0.86, 0.24) * mm, "end": v(0.85, 0.24) * mm});
            skLineSegment(sketch, "E2038", {"start": v(0.85, 0.24) * mm, "end": v(0.85, 0.24) * mm});
            skLineSegment(sketch, "E2039", {"start": v(0.85, 0.24) * mm, "end": v(0.87, 0.22) * mm});
            skLineSegment(sketch, "E2040", {"start": v(0.87, 0.22) * mm, "end": v(0.87, 0.22) * mm});
            skLineSegment(sketch, "E2041", {"start": v(0.87, 0.22) * mm, "end": v(0.87, 0.21) * mm});
            skLineSegment(sketch, "E2042", {"start": v(0.87, 0.21) * mm, "end": v(0.87, 0.2) * mm});
            skLineSegment(sketch, "E2043", {"start": v(0.87, 0.2) * mm, "end": v(0.87, 0.2) * mm});
            skLineSegment(sketch, "E2044", {"start": v(0.87, 0.2) * mm, "end": v(0.86, 0.19) * mm});
            skLineSegment(sketch, "E2045", {"start": v(0.86, 0.19) * mm, "end": v(0.86, 0.19) * mm});
            skLineSegment(sketch, "E2046", {"start": v(0.86, 0.19) * mm, "end": v(0.86, 0.18) * mm});
            skLineSegment(sketch, "E2047", {"start": v(0.86, 0.18) * mm, "end": v(0.88, 0.18) * mm});
            skLineSegment(sketch, "E2048", {"start": v(0.88, 0.18) * mm, "end": v(0.88, 0.18) * mm});
            skLineSegment(sketch, "E2049", {"start": v(0.88, 0.18) * mm, "end": v(0.89, 0.16) * mm});
            skLineSegment(sketch, "E2050", {"start": v(0.89, 0.16) * mm, "end": v(0.89, 0.16) * mm});
            skLineSegment(sketch, "E2051", {"start": v(0.89, 0.16) * mm, "end": v(0.89, 0.13) * mm});
            skLineSegment(sketch, "E2052", {"start": v(0.89, 0.13) * mm, "end": v(0.89, 0.13) * mm});
            skLineSegment(sketch, "E2053", {"start": v(0.89, 0.13) * mm, "end": v(0.88, 0.13) * mm});
            skLineSegment(sketch, "E2054", {"start": v(0.88, 0.13) * mm, "end": v(0.86, 0.11) * mm});
            skLineSegment(sketch, "E2055", {"start": v(0.86, 0.11) * mm, "end": v(0.86, 0.11) * mm});
            skLineSegment(sketch, "E2056", {"start": v(0.86, 0.11) * mm, "end": v(0.81, 0.1) * mm});
            skLineSegment(sketch, "E2057", {"start": v(0.81, 0.1) * mm, "end": v(0.81, 0.1) * mm});
            skLineSegment(sketch, "E2058", {"start": v(0.81, 0.1) * mm, "end": v(0.8, 0.1) * mm});
            skLineSegment(sketch, "E2059", {"start": v(0.8, 0.1) * mm, "end": v(0.8, 0.1) * mm});
            skLineSegment(sketch, "E2060", {"start": v(0.8, 0.1) * mm, "end": v(0.8, 0.11) * mm});
            skLineSegment(sketch, "E2061", {"start": v(0.8, 0.11) * mm, "end": v(0.8, 0.11) * mm});
            skLineSegment(sketch, "E2062", {"start": v(0.8, 0.11) * mm, "end": v(0.8, 0.12) * mm});
            skLineSegment(sketch, "E2063", {"start": v(0.8, 0.12) * mm, "end": v(0.8, 0.12) * mm});
            skLineSegment(sketch, "E2064", {"start": v(0.8, 0.12) * mm, "end": v(0.8, 0.13) * mm});
            skLineSegment(sketch, "E2065", {"start": v(0.8, 0.13) * mm, "end": v(0.8, 0.13) * mm});
            skLineSegment(sketch, "E2066", {"start": v(0.8, 0.13) * mm, "end": v(0.85, 0.14) * mm});
            skLineSegment(sketch, "E2067", {"start": v(0.85, 0.14) * mm, "end": v(0.85, 0.14) * mm});
            skLineSegment(sketch, "E2068", {"start": v(0.85, 0.14) * mm, "end": v(0.86, 0.15) * mm});
            skLineSegment(sketch, "E2069", {"start": v(0.86, 0.15) * mm, "end": v(0.86, 0.15) * mm});
            skLineSegment(sketch, "E2070", {"start": v(0.86, 0.15) * mm, "end": v(0.86, 0.16) * mm});
            skLineSegment(sketch, "E2071", {"start": v(0.86, 0.16) * mm, "end": v(0.86, 0.16) * mm});
            skLineSegment(sketch, "E2072", {"start": v(0.86, 0.16) * mm, "end": v(0.86, 0.17) * mm});
            skLineSegment(sketch, "E2073", {"start": v(0.86, 0.17) * mm, "end": v(0.86, 0.17) * mm});
            skLineSegment(sketch, "E2074", {"start": v(0.86, 0.17) * mm, "end": v(0.84, 0.17) * mm});
            skLineSegment(sketch, "E2075", {"start": v(0.84, 0.17) * mm, "end": v(0.84, 0.17) * mm});
            skLineSegment(sketch, "E2076", {"start": v(0.84, 0.17) * mm, "end": v(0.8, 0.16) * mm});
            skLineSegment(sketch, "E2077", {"start": v(0.8, 0.16) * mm, "end": v(0.8, 0.16) * mm});
            skLineSegment(sketch, "E2078", {"start": v(0.8, 0.16) * mm, "end": v(0.79, 0.16) * mm});
            skLineSegment(sketch, "E2079", {"start": v(0.79, 0.16) * mm, "end": v(0.79, 0.16) * mm});
            skLineSegment(sketch, "E2080", {"start": v(0.79, 0.16) * mm, "end": v(0.78, 0.17) * mm});
            skLineSegment(sketch, "E2081", {"start": v(0.78, 0.17) * mm, "end": v(0.78, 0.17) * mm});
            skLineSegment(sketch, "E2082", {"start": v(0.78, 0.17) * mm, "end": v(0.78, 0.18) * mm});
            skLineSegment(sketch, "E2083", {"start": v(0.78, 0.18) * mm, "end": v(0.78, 0.18) * mm});
            skLineSegment(sketch, "E2084", {"start": v(0.78, 0.18) * mm, "end": v(0.79, 0.18) * mm});
            skLineSegment(sketch, "E2085", {"start": v(0.79, 0.18) * mm, "end": v(0.79, 0.18) * mm});
            skLineSegment(sketch, "E2086", {"start": v(0.79, 0.18) * mm, "end": v(0.83, 0.2) * mm});
            skLineSegment(sketch, "E2087", {"start": v(0.83, 0.2) * mm, "end": v(0.84, 0.2) * mm});
            skLineSegment(sketch, "E2088", {"start": v(0.84, 0.2) * mm, "end": v(0.85, 0.2) * mm});
            skLineSegment(sketch, "E2089", {"start": v(0.85, 0.2) * mm, "end": v(0.85, 0.2) * mm});
            skLineSegment(sketch, "E2090", {"start": v(0.85, 0.2) * mm, "end": v(0.85, 0.22) * mm});
            skLineSegment(sketch, "E2091", {"start": v(0.85, 0.22) * mm, "end": v(0.85, 0.22) * mm});
            skLineSegment(sketch, "E2092", {"start": v(0.85, 0.22) * mm, "end": v(0.84, 0.23) * mm});
            skLineSegment(sketch, "E2093", {"start": v(0.84, 0.23) * mm, "end": v(0.84, 0.23) * mm});
            skLineSegment(sketch, "E2094", {"start": v(0.84, 0.23) * mm, "end": v(0.83, 0.23) * mm});
            skLineSegment(sketch, "E2095", {"start": v(0.83, 0.23) * mm, "end": v(0.83, 0.23) * mm});
            skLineSegment(sketch, "E2096", {"start": v(0.83, 0.23) * mm, "end": v(0.78, 0.22) * mm});
            skLineSegment(sketch, "E2097", {"start": v(0.78, 0.22) * mm, "end": v(0.78, 0.22) * mm});
            skLineSegment(sketch, "E2098", {"start": v(0.78, 0.22) * mm, "end": v(0.77, 0.22) * mm});
            skLineSegment(sketch, "E2099", {"start": v(0.77, 0.22) * mm, "end": v(0.77, 0.22) * mm});
            skLineSegment(sketch, "E2100", {"start": v(0.77, 0.22) * mm, "end": v(0.77, 0.23) * mm});
            skLineSegment(sketch, "E2101", {"start": v(0.77, 0.23) * mm, "end": v(0.77, 0.23) * mm});
            skLineSegment(sketch, "E2102", {"start": v(0.77, 0.23) * mm, "end": v(0.77, 0.24) * mm});
            skLineSegment(sketch, "E2103", {"start": v(0.77, 0.24) * mm, "end": v(0.77, 0.24) * mm});
            skLineSegment(sketch, "E2104", {"start": v(0.81, 0.09) * mm, "end": v(0.9, 0.1) * mm});
            skLineSegment(sketch, "E2105", {"start": v(0.9, 0.1) * mm, "end": v(0.9, 0.1) * mm});
            skLineSegment(sketch, "E2106", {"start": v(0.9, 0.1) * mm, "end": v(0.9, 0.09) * mm});
            skLineSegment(sketch, "E2107", {"start": v(0.9, 0.09) * mm, "end": v(0.9, 0.09) * mm});
            skLineSegment(sketch, "E2108", {"start": v(0.9, 0.09) * mm, "end": v(0.9, 0.08) * mm});
            skLineSegment(sketch, "E2109", {"start": v(0.9, 0.08) * mm, "end": v(0.9, 0.08) * mm});
            skLineSegment(sketch, "E2110", {"start": v(0.9, 0.08) * mm, "end": v(0.9, 0.07) * mm});
            skLineSegment(sketch, "E2111", {"start": v(0.9, 0.07) * mm, "end": v(0.9, 0.07) * mm});
            skLineSegment(sketch, "E2112", {"start": v(0.9, 0.07) * mm, "end": v(0.9, 0.06) * mm});
            skLineSegment(sketch, "E2113", {"start": v(0.9, 0.06) * mm, "end": v(0.9, 0.04) * mm});
            skLineSegment(sketch, "E2114", {"start": v(0.9, 0.04) * mm, "end": v(0.9, 0.04) * mm});
            skLineSegment(sketch, "E2115", {"start": v(0.9, 0.04) * mm, "end": v(0.9, 0.02) * mm});
            skLineSegment(sketch, "E2116", {"start": v(0.9, 0.02) * mm, "end": v(0.9, 0.02) * mm});
            skLineSegment(sketch, "E2117", {"start": v(0.9, 0.02) * mm, "end": v(0.9, 0.01) * mm});
            skLineSegment(sketch, "E2118", {"start": v(0.9, 0.01) * mm, "end": v(0.9, 0.01) * mm});
            skLineSegment(sketch, "E2119", {"start": v(0.9, 0.01) * mm, "end": v(0.9, 0) * mm});
            skLineSegment(sketch, "E2120", {"start": v(0.9, 0) * mm, "end": v(0.9, 0) * mm});
            skLineSegment(sketch, "E2121", {"start": v(0.9, 0) * mm, "end": v(0.91, -0.02) * mm});
            skLineSegment(sketch, "E2122", {"start": v(0.91, -0.02) * mm, "end": v(0.91, -0.02) * mm});
            skLineSegment(sketch, "E2123", {"start": v(0.91, -0.02) * mm, "end": v(0.9, -0.04) * mm});
            skLineSegment(sketch, "E2124", {"start": v(0.9, -0.04) * mm, "end": v(0.9, -0.04) * mm});
            skLineSegment(sketch, "E2125", {"start": v(0.9, -0.04) * mm, "end": v(0.9, -0.05) * mm});
            skLineSegment(sketch, "E2126", {"start": v(0.9, -0.05) * mm, "end": v(0.88, -0.06) * mm});
            skLineSegment(sketch, "E2127", {"start": v(0.88, -0.06) * mm, "end": v(0.87, -0.06) * mm});
            skLineSegment(sketch, "E2128", {"start": v(0.87, -0.06) * mm, "end": v(0.82, -0.06) * mm});
            skLineSegment(sketch, "E2129", {"start": v(0.82, -0.06) * mm, "end": v(0.82, -0.06) * mm});
            skLineSegment(sketch, "E2130", {"start": v(0.82, -0.06) * mm, "end": v(0.82, -0.05) * mm});
            skLineSegment(sketch, "E2131", {"start": v(0.82, -0.05) * mm, "end": v(0.82, -0.05) * mm});
            skLineSegment(sketch, "E2132", {"start": v(0.82, -0.05) * mm, "end": v(0.82, -0.04) * mm});
            skLineSegment(sketch, "E2133", {"start": v(0.82, -0.04) * mm, "end": v(0.82, -0.04) * mm});
            skLineSegment(sketch, "E2134", {"start": v(0.82, -0.04) * mm, "end": v(0.87, -0.03) * mm});
            skLineSegment(sketch, "E2135", {"start": v(0.87, -0.03) * mm, "end": v(0.87, -0.03) * mm});
            skLineSegment(sketch, "E2136", {"start": v(0.87, -0.03) * mm, "end": v(0.88, -0.03) * mm});
            skLineSegment(sketch, "E2137", {"start": v(0.88, -0.03) * mm, "end": v(0.89, -0.03) * mm});
            skLineSegment(sketch, "E2138", {"start": v(0.89, -0.03) * mm, "end": v(0.89, -0.02) * mm});
            skLineSegment(sketch, "E2139", {"start": v(0.89, -0.02) * mm, "end": v(0.89, -0.01) * mm});
            skLineSegment(sketch, "E2140", {"start": v(0.89, -0.01) * mm, "end": v(0.89, -0.01) * mm});
            skLineSegment(sketch, "E2141", {"start": v(0.89, -0.01) * mm, "end": v(0.88, 0) * mm});
            skLineSegment(sketch, "E2142", {"start": v(0.88, 0) * mm, "end": v(0.88, 0) * mm});
            skLineSegment(sketch, "E2143", {"start": v(0.88, 0) * mm, "end": v(0.87, 0) * mm});
            skLineSegment(sketch, "E2144", {"start": v(0.87, 0) * mm, "end": v(0.87, 0) * mm});
            skLineSegment(sketch, "E2145", {"start": v(0.87, 0) * mm, "end": v(0.82, 0) * mm});
            skLineSegment(sketch, "E2146", {"start": v(0.82, 0) * mm, "end": v(0.82, 0) * mm});
            skLineSegment(sketch, "E2147", {"start": v(0.82, 0) * mm, "end": v(0.81, 0) * mm});
            skLineSegment(sketch, "E2148", {"start": v(0.81, 0) * mm, "end": v(0.81, 0) * mm});
            skLineSegment(sketch, "E2149", {"start": v(0.81, 0) * mm, "end": v(0.81, 0.01) * mm});
            skLineSegment(sketch, "E2150", {"start": v(0.81, 0.01) * mm, "end": v(0.81, 0.01) * mm});
            skLineSegment(sketch, "E2151", {"start": v(0.81, 0.01) * mm, "end": v(0.81, 0.02) * mm});
            skLineSegment(sketch, "E2152", {"start": v(0.81, 0.02) * mm, "end": v(0.81, 0.02) * mm});
            skLineSegment(sketch, "E2153", {"start": v(0.81, 0.02) * mm, "end": v(0.82, 0.02) * mm});
            skLineSegment(sketch, "E2154", {"start": v(0.82, 0.02) * mm, "end": v(0.82, 0.02) * mm});
            skLineSegment(sketch, "E2155", {"start": v(0.82, 0.02) * mm, "end": v(0.87, 0.03) * mm});
            skLineSegment(sketch, "E2156", {"start": v(0.87, 0.03) * mm, "end": v(0.87, 0.03) * mm});
            skLineSegment(sketch, "E2157", {"start": v(0.87, 0.03) * mm, "end": v(0.88, 0.03) * mm});
            skLineSegment(sketch, "E2158", {"start": v(0.88, 0.03) * mm, "end": v(0.88, 0.03) * mm});
            skLineSegment(sketch, "E2159", {"start": v(0.88, 0.03) * mm, "end": v(0.88, 0.04) * mm});
            skLineSegment(sketch, "E2160", {"start": v(0.88, 0.04) * mm, "end": v(0.88, 0.05) * mm});
            skLineSegment(sketch, "E2161", {"start": v(0.88, 0.05) * mm, "end": v(0.88, 0.05) * mm});
            skLineSegment(sketch, "E2162", {"start": v(0.88, 0.05) * mm, "end": v(0.88, 0.06) * mm});
            skLineSegment(sketch, "E2163", {"start": v(0.88, 0.06) * mm, "end": v(0.88, 0.06) * mm});
            skLineSegment(sketch, "E2164", {"start": v(0.88, 0.06) * mm, "end": v(0.87, 0.06) * mm});
            skLineSegment(sketch, "E2165", {"start": v(0.87, 0.06) * mm, "end": v(0.86, 0.06) * mm});
            skLineSegment(sketch, "E2166", {"start": v(0.86, 0.06) * mm, "end": v(0.82, 0.06) * mm});
            skLineSegment(sketch, "E2167", {"start": v(0.82, 0.06) * mm, "end": v(0.82, 0.06) * mm});
            skLineSegment(sketch, "E2168", {"start": v(0.82, 0.06) * mm, "end": v(0.81, 0.06) * mm});
            skLineSegment(sketch, "E2169", {"start": v(0.81, 0.06) * mm, "end": v(0.8, 0.06) * mm});
            skLineSegment(sketch, "E2170", {"start": v(0.8, 0.06) * mm, "end": v(0.8, 0.06) * mm});
            skLineSegment(sketch, "E2171", {"start": v(0.8, 0.06) * mm, "end": v(0.8, 0.07) * mm});
            skLineSegment(sketch, "E2172", {"start": v(0.8, 0.07) * mm, "end": v(0.8, 0.07) * mm});
            skLineSegment(sketch, "E2173", {"start": v(0.8, 0.07) * mm, "end": v(0.8, 0.08) * mm});
            skLineSegment(sketch, "E2174", {"start": v(0.8, 0.08) * mm, "end": v(0.8, 0.08) * mm});
            skLineSegment(sketch, "E2175", {"start": v(0.8, 0.08) * mm, "end": v(0.81, 0.09) * mm});
            skLineSegment(sketch, "E2176", {"start": v(0.81, 0.09) * mm, "end": v(0.81, 0.09) * mm});
            skLineSegment(sketch, "E2177", {"start": v(0.85, -0.08) * mm, "end": v(0.9, -0.08) * mm});
            skLineSegment(sketch, "E2178", {"start": v(0.9, -0.08) * mm, "end": v(0.9, -0.08) * mm});
            skLineSegment(sketch, "E2179", {"start": v(0.9, -0.08) * mm, "end": v(0.9, -0.09) * mm});
            skLineSegment(sketch, "E2180", {"start": v(0.9, -0.09) * mm, "end": v(0.9, -0.09) * mm});
            skLineSegment(sketch, "E2181", {"start": v(0.9, -0.09) * mm, "end": v(0.91, -0.1) * mm});
            skLineSegment(sketch, "E2182", {"start": v(0.91, -0.1) * mm, "end": v(0.91, -0.1) * mm});
            skLineSegment(sketch, "E2183", {"start": v(0.91, -0.1) * mm, "end": v(0.9, -0.1) * mm});
            skLineSegment(sketch, "E2184", {"start": v(0.9, -0.1) * mm, "end": v(0.9, -0.1) * mm});
            skLineSegment(sketch, "E2185", {"start": v(0.9, -0.1) * mm, "end": v(0.9, -0.11) * mm});
            skLineSegment(sketch, "E2186", {"start": v(0.9, -0.11) * mm, "end": v(0.9, -0.11) * mm});
            skLineSegment(sketch, "E2187", {"start": v(0.9, -0.11) * mm, "end": v(0.85, -0.1) * mm});
            skLineSegment(sketch, "E2188", {"start": v(0.85, -0.1) * mm, "end": v(0.85, -0.1) * mm});
            skLineSegment(sketch, "E2189", {"start": v(0.85, -0.1) * mm, "end": v(0.84, -0.1) * mm});
            skLineSegment(sketch, "E2190", {"start": v(0.84, -0.1) * mm, "end": v(0.84, -0.1) * mm});
            skLineSegment(sketch, "E2191", {"start": v(0.84, -0.1) * mm, "end": v(0.84, -0.11) * mm});
            skLineSegment(sketch, "E2192", {"start": v(0.84, -0.11) * mm, "end": v(0.83, -0.12) * mm});
            skLineSegment(sketch, "E2193", {"start": v(0.83, -0.12) * mm, "end": v(0.83, -0.12) * mm});
            skLineSegment(sketch, "E2194", {"start": v(0.83, -0.12) * mm, "end": v(0.84, -0.13) * mm});
            skLineSegment(sketch, "E2195", {"start": v(0.84, -0.13) * mm, "end": v(0.84, -0.14) * mm});
            skLineSegment(sketch, "E2196", {"start": v(0.84, -0.14) * mm, "end": v(0.84, -0.14) * mm});
            skLineSegment(sketch, "E2197", {"start": v(0.84, -0.14) * mm, "end": v(0.85, -0.14) * mm});
            skLineSegment(sketch, "E2198", {"start": v(0.85, -0.14) * mm, "end": v(0.85, -0.14) * mm});
            skLineSegment(sketch, "E2199", {"start": v(0.85, -0.14) * mm, "end": v(0.9, -0.15) * mm});
            skLineSegment(sketch, "E2200", {"start": v(0.9, -0.15) * mm, "end": v(0.9, -0.15) * mm});
            skLineSegment(sketch, "E2201", {"start": v(0.9, -0.15) * mm, "end": v(0.9, -0.16) * mm});
            skLineSegment(sketch, "E2202", {"start": v(0.9, -0.16) * mm, "end": v(0.9, -0.16) * mm});
            skLineSegment(sketch, "E2203", {"start": v(0.9, -0.16) * mm, "end": v(0.9, -0.17) * mm});
            skLineSegment(sketch, "E2204", {"start": v(0.9, -0.17) * mm, "end": v(0.9, -0.17) * mm});
            skLineSegment(sketch, "E2205", {"start": v(0.9, -0.17) * mm, "end": v(0.85, -0.17) * mm});
            skLineSegment(sketch, "E2206", {"start": v(0.85, -0.17) * mm, "end": v(0.84, -0.17) * mm});
            skLineSegment(sketch, "E2207", {"start": v(0.84, -0.17) * mm, "end": v(0.82, -0.16) * mm});
            skLineSegment(sketch, "E2208", {"start": v(0.82, -0.16) * mm, "end": v(0.82, -0.15) * mm});
            skLineSegment(sketch, "E2209", {"start": v(0.82, -0.15) * mm, "end": v(0.82, -0.15) * mm});
            skLineSegment(sketch, "E2210", {"start": v(0.82, -0.15) * mm, "end": v(0.8, -0.12) * mm});
            skLineSegment(sketch, "E2211", {"start": v(0.8, -0.12) * mm, "end": v(0.8, -0.12) * mm});
            skLineSegment(sketch, "E2212", {"start": v(0.8, -0.12) * mm, "end": v(0.82, -0.1) * mm});
            skLineSegment(sketch, "E2213", {"start": v(0.82, -0.1) * mm, "end": v(0.82, -0.09) * mm});
            skLineSegment(sketch, "E2214", {"start": v(0.82, -0.09) * mm, "end": v(0.83, -0.09) * mm});
            skLineSegment(sketch, "E2215", {"start": v(0.83, -0.09) * mm, "end": v(0.85, -0.08) * mm});
            skLineSegment(sketch, "E2216", {"start": v(0.85, -0.08) * mm, "end": v(0.85, -0.08) * mm});
            skLineSegment(sketch, "E2217", {"start": v(0.82, -0.24) * mm, "end": v(0.82, -0.24) * mm});
            skLineSegment(sketch, "E2218", {"start": v(0.82, -0.24) * mm, "end": v(0.81, -0.24) * mm});
            skLineSegment(sketch, "E2219", {"start": v(0.81, -0.24) * mm, "end": v(0.81, -0.24) * mm});
            skLineSegment(sketch, "E2220", {"start": v(0.81, -0.24) * mm, "end": v(0.8, -0.25) * mm});
            skLineSegment(sketch, "E2221", {"start": v(0.8, -0.25) * mm, "end": v(0.8, -0.25) * mm});
            skLineSegment(sketch, "E2222", {"start": v(0.8, -0.25) * mm, "end": v(0.8, -0.26) * mm});
            skLineSegment(sketch, "E2223", {"start": v(0.8, -0.26) * mm, "end": v(0.8, -0.26) * mm});
            skLineSegment(sketch, "E2224", {"start": v(0.8, -0.26) * mm, "end": v(0.82, -0.27) * mm});
            skLineSegment(sketch, "E2225", {"start": v(0.82, -0.27) * mm, "end": v(0.82, -0.27) * mm});
            skLineSegment(sketch, "E2226", {"start": v(0.82, -0.27) * mm, "end": v(0.83, -0.27) * mm});
            skLineSegment(sketch, "E2227", {"start": v(0.83, -0.27) * mm, "end": v(0.83, -0.26) * mm});
            skLineSegment(sketch, "E2228", {"start": v(0.83, -0.26) * mm, "end": v(0.83, -0.25) * mm});
            skLineSegment(sketch, "E2229", {"start": v(0.83, -0.25) * mm, "end": v(0.82, -0.24) * mm});
            skLineSegment(sketch, "E2230", {"start": v(0.85, -0.19) * mm, "end": v(0.85, -0.19) * mm});
            skLineSegment(sketch, "E2231", {"start": v(0.85, -0.19) * mm, "end": v(0.88, -0.2) * mm});
            skLineSegment(sketch, "E2232", {"start": v(0.88, -0.2) * mm, "end": v(0.88, -0.2) * mm});
            skLineSegment(sketch, "E2233", {"start": v(0.88, -0.2) * mm, "end": v(0.89, -0.2) * mm});
            skLineSegment(sketch, "E2234", {"start": v(0.89, -0.2) * mm, "end": v(0.9, -0.23) * mm});
            skLineSegment(sketch, "E2235", {"start": v(0.9, -0.23) * mm, "end": v(0.9, -0.23) * mm});
            skLineSegment(sketch, "E2236", {"start": v(0.9, -0.23) * mm, "end": v(0.9, -0.24) * mm});
            skLineSegment(sketch, "E2237", {"start": v(0.9, -0.24) * mm, "end": v(0.9, -0.27) * mm});
            skLineSegment(sketch, "E2238", {"start": v(0.9, -0.27) * mm, "end": v(0.9, -0.28) * mm});
            skLineSegment(sketch, "E2239", {"start": v(0.9, -0.28) * mm, "end": v(0.9, -0.28) * mm});
            skLineSegment(sketch, "E2240", {"start": v(0.9, -0.28) * mm, "end": v(0.9, -0.3) * mm});
            skLineSegment(sketch, "E2241", {"start": v(0.9, -0.3) * mm, "end": v(0.88, -0.32) * mm});
            skLineSegment(sketch, "E2242", {"start": v(0.88, -0.32) * mm, "end": v(0.87, -0.32) * mm});
            skLineSegment(sketch, "E2243", {"start": v(0.87, -0.32) * mm, "end": v(0.87, -0.32) * mm});
            skLineSegment(sketch, "E2244", {"start": v(0.87, -0.32) * mm, "end": v(0.85, -0.33) * mm});
            skLineSegment(sketch, "E2245", {"start": v(0.85, -0.33) * mm, "end": v(0.82, -0.33) * mm});
            skLineSegment(sketch, "E2246", {"start": v(0.82, -0.33) * mm, "end": v(0.82, -0.33) * mm});
            skLineSegment(sketch, "E2247", {"start": v(0.82, -0.33) * mm, "end": v(0.82, -0.32) * mm});
            skLineSegment(sketch, "E2248", {"start": v(0.82, -0.32) * mm, "end": v(0.8, -0.31) * mm});
            skLineSegment(sketch, "E2249", {"start": v(0.8, -0.31) * mm, "end": v(0.79, -0.3) * mm});
            skLineSegment(sketch, "E2250", {"start": v(0.79, -0.3) * mm, "end": v(0.79, -0.3) * mm});
            skLineSegment(sketch, "E2251", {"start": v(0.79, -0.3) * mm, "end": v(0.78, -0.29) * mm});
            skLineSegment(sketch, "E2252", {"start": v(0.78, -0.29) * mm, "end": v(0.78, -0.28) * mm});
            skLineSegment(sketch, "E2253", {"start": v(0.78, -0.28) * mm, "end": v(0.78, -0.28) * mm});
            skLineSegment(sketch, "E2254", {"start": v(0.78, -0.28) * mm, "end": v(0.79, -0.27) * mm});
            skLineSegment(sketch, "E2255", {"start": v(0.79, -0.27) * mm, "end": v(0.79, -0.27) * mm});
            skLineSegment(sketch, "E2256", {"start": v(0.79, -0.27) * mm, "end": v(0.8, -0.27) * mm});
            skLineSegment(sketch, "E2257", {"start": v(0.8, -0.27) * mm, "end": v(0.8, -0.27) * mm});
            skLineSegment(sketch, "E2258", {"start": v(0.8, -0.27) * mm, "end": v(0.8, -0.26) * mm});
            skLineSegment(sketch, "E2259", {"start": v(0.8, -0.26) * mm, "end": v(0.8, -0.24) * mm});
            skLineSegment(sketch, "E2260", {"start": v(0.8, -0.24) * mm, "end": v(0.8, -0.24) * mm});
            skLineSegment(sketch, "E2261", {"start": v(0.8, -0.24) * mm, "end": v(0.8, -0.22) * mm});
            skLineSegment(sketch, "E2262", {"start": v(0.8, -0.22) * mm, "end": v(0.8, -0.22) * mm});
            skLineSegment(sketch, "E2263", {"start": v(0.8, -0.22) * mm, "end": v(0.82, -0.22) * mm});
            skLineSegment(sketch, "E2264", {"start": v(0.82, -0.22) * mm, "end": v(0.82, -0.22) * mm});
            skLineSegment(sketch, "E2265", {"start": v(0.82, -0.22) * mm, "end": v(0.83, -0.22) * mm});
            skLineSegment(sketch, "E2266", {"start": v(0.83, -0.22) * mm, "end": v(0.84, -0.23) * mm});
            skLineSegment(sketch, "E2267", {"start": v(0.84, -0.23) * mm, "end": v(0.84, -0.26) * mm});
            skLineSegment(sketch, "E2268", {"start": v(0.84, -0.26) * mm, "end": v(0.84, -0.27) * mm});
            skLineSegment(sketch, "E2269", {"start": v(0.84, -0.27) * mm, "end": v(0.84, -0.27) * mm});
            skLineSegment(sketch, "E2270", {"start": v(0.84, -0.27) * mm, "end": v(0.85, -0.27) * mm});
            skLineSegment(sketch, "E2271", {"start": v(0.85, -0.27) * mm, "end": v(0.86, -0.26) * mm});
            skLineSegment(sketch, "E2272", {"start": v(0.86, -0.26) * mm, "end": v(0.86, -0.26) * mm});
            skLineSegment(sketch, "E2273", {"start": v(0.86, -0.26) * mm, "end": v(0.86, -0.25) * mm});
            skLineSegment(sketch, "E2274", {"start": v(0.86, -0.25) * mm, "end": v(0.86, -0.25) * mm});
            skLineSegment(sketch, "E2275", {"start": v(0.86, -0.25) * mm, "end": v(0.86, -0.24) * mm});
            skLineSegment(sketch, "E2276", {"start": v(0.86, -0.24) * mm, "end": v(0.86, -0.24) * mm});
            skLineSegment(sketch, "E2277", {"start": v(0.86, -0.24) * mm, "end": v(0.86, -0.23) * mm});
            skLineSegment(sketch, "E2278", {"start": v(0.86, -0.23) * mm, "end": v(0.86, -0.23) * mm});
            skLineSegment(sketch, "E2279", {"start": v(0.86, -0.23) * mm, "end": v(0.87, -0.23) * mm});
            skLineSegment(sketch, "E2280", {"start": v(0.87, -0.23) * mm, "end": v(0.87, -0.23) * mm});
            skLineSegment(sketch, "E2281", {"start": v(0.87, -0.23) * mm, "end": v(0.88, -0.24) * mm});
            skLineSegment(sketch, "E2282", {"start": v(0.88, -0.24) * mm, "end": v(0.88, -0.25) * mm});
            skLineSegment(sketch, "E2283", {"start": v(0.88, -0.25) * mm, "end": v(0.88, -0.25) * mm});
            skLineSegment(sketch, "E2284", {"start": v(0.88, -0.25) * mm, "end": v(0.88, -0.26) * mm});
            skLineSegment(sketch, "E2285", {"start": v(0.88, -0.26) * mm, "end": v(0.87, -0.27) * mm});
            skLineSegment(sketch, "E2286", {"start": v(0.87, -0.27) * mm, "end": v(0.87, -0.27) * mm});
            skLineSegment(sketch, "E2287", {"start": v(0.87, -0.27) * mm, "end": v(0.86, -0.29) * mm});
            skLineSegment(sketch, "E2288", {"start": v(0.86, -0.29) * mm, "end": v(0.86, -0.29) * mm});
            skLineSegment(sketch, "E2289", {"start": v(0.86, -0.29) * mm, "end": v(0.84, -0.3) * mm});
            skLineSegment(sketch, "E2290", {"start": v(0.84, -0.3) * mm, "end": v(0.84, -0.3) * mm});
            skLineSegment(sketch, "E2291", {"start": v(0.84, -0.3) * mm, "end": v(0.8, -0.28) * mm});
            skLineSegment(sketch, "E2292", {"start": v(0.8, -0.28) * mm, "end": v(0.8, -0.28) * mm});
            skLineSegment(sketch, "E2293", {"start": v(0.8, -0.28) * mm, "end": v(0.8, -0.29) * mm});
            skLineSegment(sketch, "E2294", {"start": v(0.8, -0.29) * mm, "end": v(0.8, -0.29) * mm});
            skLineSegment(sketch, "E2295", {"start": v(0.8, -0.29) * mm, "end": v(0.8, -0.3) * mm});
            skLineSegment(sketch, "E2296", {"start": v(0.8, -0.3) * mm, "end": v(0.8, -0.3) * mm});
            skLineSegment(sketch, "E2297", {"start": v(0.8, -0.3) * mm, "end": v(0.81, -0.3) * mm});
            skLineSegment(sketch, "E2298", {"start": v(0.81, -0.3) * mm, "end": v(0.82, -0.3) * mm});
            skLineSegment(sketch, "E2299", {"start": v(0.82, -0.3) * mm, "end": v(0.83, -0.31) * mm});
            skLineSegment(sketch, "E2300", {"start": v(0.83, -0.31) * mm, "end": v(0.86, -0.3) * mm});
            skLineSegment(sketch, "E2301", {"start": v(0.86, -0.3) * mm, "end": v(0.89, -0.28) * mm});
            skLineSegment(sketch, "E2302", {"start": v(0.89, -0.28) * mm, "end": v(0.89, -0.27) * mm});
            skLineSegment(sketch, "E2303", {"start": v(0.89, -0.27) * mm, "end": v(0.89, -0.27) * mm});
            skLineSegment(sketch, "E2304", {"start": v(0.89, -0.27) * mm, "end": v(0.9, -0.25) * mm});
            skLineSegment(sketch, "E2305", {"start": v(0.9, -0.25) * mm, "end": v(0.89, -0.25) * mm});
            skLineSegment(sketch, "E2306", {"start": v(0.89, -0.25) * mm, "end": v(0.89, -0.24) * mm});
            skLineSegment(sketch, "E2307", {"start": v(0.89, -0.24) * mm, "end": v(0.88, -0.23) * mm});
            skLineSegment(sketch, "E2308", {"start": v(0.88, -0.23) * mm, "end": v(0.88, -0.23) * mm});
            skLineSegment(sketch, "E2309", {"start": v(0.88, -0.23) * mm, "end": v(0.88, -0.22) * mm});
            skLineSegment(sketch, "E2310", {"start": v(0.88, -0.22) * mm, "end": v(0.87, -0.21) * mm});
            skLineSegment(sketch, "E2311", {"start": v(0.87, -0.21) * mm, "end": v(0.87, -0.21) * mm});
            skLineSegment(sketch, "E2312", {"start": v(0.87, -0.21) * mm, "end": v(0.86, -0.21) * mm});
            skLineSegment(sketch, "E2313", {"start": v(0.86, -0.21) * mm, "end": v(0.85, -0.2) * mm});
            skLineSegment(sketch, "E2314", {"start": v(0.85, -0.2) * mm, "end": v(0.84, -0.2) * mm});
            skLineSegment(sketch, "E2315", {"start": v(0.84, -0.2) * mm, "end": v(0.84, -0.2) * mm});
            skLineSegment(sketch, "E2316", {"start": v(0.84, -0.2) * mm, "end": v(0.83, -0.2) * mm});
            skLineSegment(sketch, "E2317", {"start": v(0.83, -0.2) * mm, "end": v(0.82, -0.2) * mm});
            skLineSegment(sketch, "E2318", {"start": v(0.82, -0.2) * mm, "end": v(0.82, -0.2) * mm});
            skLineSegment(sketch, "E2319", {"start": v(0.82, -0.2) * mm, "end": v(0.8, -0.2) * mm});
            skLineSegment(sketch, "E2320", {"start": v(0.8, -0.2) * mm, "end": v(0.8, -0.2) * mm});
            skLineSegment(sketch, "E2321", {"start": v(0.8, -0.2) * mm, "end": v(0.79, -0.21) * mm});
            skLineSegment(sketch, "E2322", {"start": v(0.79, -0.21) * mm, "end": v(0.79, -0.22) * mm});
            skLineSegment(sketch, "E2323", {"start": v(0.79, -0.22) * mm, "end": v(0.79, -0.22) * mm});
            skLineSegment(sketch, "E2324", {"start": v(0.79, -0.22) * mm, "end": v(0.78, -0.24) * mm});
            skLineSegment(sketch, "E2325", {"start": v(0.78, -0.24) * mm, "end": v(0.78, -0.24) * mm});
            skLineSegment(sketch, "E2326", {"start": v(0.78, -0.24) * mm, "end": v(0.78, -0.25) * mm});
            skLineSegment(sketch, "E2327", {"start": v(0.78, -0.25) * mm, "end": v(0.78, -0.26) * mm});
            skLineSegment(sketch, "E2328", {"start": v(0.78, -0.26) * mm, "end": v(0.78, -0.26) * mm});
            skLineSegment(sketch, "E2329", {"start": v(0.78, -0.26) * mm, "end": v(0.78, -0.27) * mm});
            skLineSegment(sketch, "E2330", {"start": v(0.78, -0.27) * mm, "end": v(0.78, -0.27) * mm});
            skLineSegment(sketch, "E2331", {"start": v(0.78, -0.27) * mm, "end": v(0.77, -0.27) * mm});
            skLineSegment(sketch, "E2332", {"start": v(0.77, -0.27) * mm, "end": v(0.77, -0.27) * mm});
            skLineSegment(sketch, "E2333", {"start": v(0.77, -0.27) * mm, "end": v(0.76, -0.26) * mm});
            skLineSegment(sketch, "E2334", {"start": v(0.76, -0.26) * mm, "end": v(0.76, -0.26) * mm});
            skLineSegment(sketch, "E2335", {"start": v(0.76, -0.26) * mm, "end": v(0.76, -0.25) * mm});
            skLineSegment(sketch, "E2336", {"start": v(0.76, -0.25) * mm, "end": v(0.76, -0.23) * mm});
            skLineSegment(sketch, "E2337", {"start": v(0.76, -0.23) * mm, "end": v(0.76, -0.23) * mm});
            skLineSegment(sketch, "E2338", {"start": v(0.76, -0.23) * mm, "end": v(0.77, -0.2) * mm});
            skLineSegment(sketch, "E2339", {"start": v(0.77, -0.2) * mm, "end": v(0.79, -0.2) * mm});
            skLineSegment(sketch, "E2340", {"start": v(0.79, -0.2) * mm, "end": v(0.8, -0.2) * mm});
            skLineSegment(sketch, "E2341", {"start": v(0.8, -0.2) * mm, "end": v(0.82, -0.18) * mm});
            skLineSegment(sketch, "E2342", {"start": v(0.82, -0.18) * mm, "end": v(0.84, -0.19) * mm});
            skLineSegment(sketch, "E2343", {"start": v(0.84, -0.19) * mm, "end": v(0.85, -0.19) * mm});
            skLineSegment(sketch, "E2344", {"start": v(0.77, -0.33) * mm, "end": v(0.85, -0.36) * mm});
            skLineSegment(sketch, "E2345", {"start": v(0.85, -0.36) * mm, "end": v(0.85, -0.36) * mm});
            skLineSegment(sketch, "E2346", {"start": v(0.85, -0.36) * mm, "end": v(0.85, -0.37) * mm});
            skLineSegment(sketch, "E2347", {"start": v(0.85, -0.37) * mm, "end": v(0.85, -0.37) * mm});
            skLineSegment(sketch, "E2348", {"start": v(0.85, -0.37) * mm, "end": v(0.85, -0.38) * mm});
            skLineSegment(sketch, "E2349", {"start": v(0.85, -0.38) * mm, "end": v(0.85, -0.38) * mm});
            skLineSegment(sketch, "E2350", {"start": v(0.85, -0.38) * mm, "end": v(0.84, -0.38) * mm});
            skLineSegment(sketch, "E2351", {"start": v(0.84, -0.38) * mm, "end": v(0.84, -0.38) * mm});
            skLineSegment(sketch, "E2352", {"start": v(0.84, -0.38) * mm, "end": v(0.83, -0.38) * mm});
            skLineSegment(sketch, "E2353", {"start": v(0.83, -0.38) * mm, "end": v(0.83, -0.38) * mm});
            skLineSegment(sketch, "E2354", {"start": v(0.83, -0.38) * mm, "end": v(0.84, -0.4) * mm});
            skLineSegment(sketch, "E2355", {"start": v(0.84, -0.4) * mm, "end": v(0.84, -0.4) * mm});
            skLineSegment(sketch, "E2356", {"start": v(0.84, -0.4) * mm, "end": v(0.84, -0.41) * mm});
            skLineSegment(sketch, "E2357", {"start": v(0.84, -0.41) * mm, "end": v(0.84, -0.41) * mm});
            skLineSegment(sketch, "E2358", {"start": v(0.84, -0.41) * mm, "end": v(0.82, -0.43) * mm});
            skLineSegment(sketch, "E2359", {"start": v(0.82, -0.43) * mm, "end": v(0.81, -0.43) * mm});
            skLineSegment(sketch, "E2360", {"start": v(0.81, -0.43) * mm, "end": v(0.81, -0.43) * mm});
            skLineSegment(sketch, "E2361", {"start": v(0.81, -0.43) * mm, "end": v(0.79, -0.43) * mm});
            skLineSegment(sketch, "E2362", {"start": v(0.79, -0.43) * mm, "end": v(0.78, -0.43) * mm});
            skLineSegment(sketch, "E2363", {"start": v(0.78, -0.43) * mm, "end": v(0.74, -0.4) * mm});
            skLineSegment(sketch, "E2364", {"start": v(0.74, -0.4) * mm, "end": v(0.74, -0.4) * mm});
            skLineSegment(sketch, "E2365", {"start": v(0.74, -0.4) * mm, "end": v(0.73, -0.4) * mm});
            skLineSegment(sketch, "E2366", {"start": v(0.73, -0.4) * mm, "end": v(0.73, -0.4) * mm});
            skLineSegment(sketch, "E2367", {"start": v(0.73, -0.4) * mm, "end": v(0.74, -0.4) * mm});
            skLineSegment(sketch, "E2368", {"start": v(0.74, -0.4) * mm, "end": v(0.74, -0.38) * mm});
            skLineSegment(sketch, "E2369", {"start": v(0.74, -0.38) * mm, "end": v(0.74, -0.38) * mm});
            skLineSegment(sketch, "E2370", {"start": v(0.74, -0.38) * mm, "end": v(0.75, -0.38) * mm});
            skLineSegment(sketch, "E2371", {"start": v(0.75, -0.38) * mm, "end": v(0.75, -0.38) * mm});
            skLineSegment(sketch, "E2372", {"start": v(0.75, -0.38) * mm, "end": v(0.8, -0.4) * mm});
            skLineSegment(sketch, "E2373", {"start": v(0.8, -0.4) * mm, "end": v(0.8, -0.4) * mm});
            skLineSegment(sketch, "E2374", {"start": v(0.8, -0.4) * mm, "end": v(0.82, -0.4) * mm});
            skLineSegment(sketch, "E2375", {"start": v(0.82, -0.4) * mm, "end": v(0.82, -0.4) * mm});
            skLineSegment(sketch, "E2376", {"start": v(0.82, -0.4) * mm, "end": v(0.82, -0.38) * mm});
            skLineSegment(sketch, "E2377", {"start": v(0.82, -0.38) * mm, "end": v(0.82, -0.38) * mm});
            skLineSegment(sketch, "E2378", {"start": v(0.82, -0.38) * mm, "end": v(0.8, -0.37) * mm});
            skLineSegment(sketch, "E2379", {"start": v(0.8, -0.37) * mm, "end": v(0.8, -0.37) * mm});
            skLineSegment(sketch, "E2380", {"start": v(0.8, -0.37) * mm, "end": v(0.76, -0.35) * mm});
            skLineSegment(sketch, "E2381", {"start": v(0.76, -0.35) * mm, "end": v(0.76, -0.35) * mm});
            skLineSegment(sketch, "E2382", {"start": v(0.76, -0.35) * mm, "end": v(0.76, -0.34) * mm});
            skLineSegment(sketch, "E2383", {"start": v(0.76, -0.34) * mm, "end": v(0.76, -0.34) * mm});
            skLineSegment(sketch, "E2384", {"start": v(0.76, -0.34) * mm, "end": v(0.76, -0.33) * mm});
            skLineSegment(sketch, "E2385", {"start": v(0.76, -0.33) * mm, "end": v(0.76, -0.33) * mm});
            skLineSegment(sketch, "E2386", {"start": v(0.76, -0.33) * mm, "end": v(0.77, -0.33) * mm});
            skLineSegment(sketch, "E2387", {"start": v(0.77, -0.33) * mm, "end": v(0.77, -0.33) * mm});
            skLineSegment(sketch, "E2388", {"start": v(0.76, -0.47) * mm, "end": v(0.75, -0.5) * mm});
            skLineSegment(sketch, "E2389", {"start": v(0.75, -0.5) * mm, "end": v(0.75, -0.5) * mm});
            skLineSegment(sketch, "E2390", {"start": v(0.75, -0.5) * mm, "end": v(0.74, -0.5) * mm});
            skLineSegment(sketch, "E2391", {"start": v(0.74, -0.5) * mm, "end": v(0.74, -0.5) * mm});
            skLineSegment(sketch, "E2392", {"start": v(0.74, -0.5) * mm, "end": v(0.75, -0.5) * mm});
            skLineSegment(sketch, "E2393", {"start": v(0.75, -0.5) * mm, "end": v(0.76, -0.5) * mm});
            skLineSegment(sketch, "E2394", {"start": v(0.76, -0.5) * mm, "end": v(0.76, -0.5) * mm});
            skLineSegment(sketch, "E2395", {"start": v(0.76, -0.5) * mm, "end": v(0.77, -0.5) * mm});
            skLineSegment(sketch, "E2396", {"start": v(0.77, -0.5) * mm, "end": v(0.77, -0.5) * mm});
            skLineSegment(sketch, "E2397", {"start": v(0.77, -0.5) * mm, "end": v(0.77, -0.48) * mm});
            skLineSegment(sketch, "E2398", {"start": v(0.77, -0.48) * mm, "end": v(0.77, -0.48) * mm});
            skLineSegment(sketch, "E2399", {"start": v(0.77, -0.48) * mm, "end": v(0.77, -0.47) * mm});
            skLineSegment(sketch, "E2400", {"start": v(0.77, -0.47) * mm, "end": v(0.77, -0.47) * mm});
            skLineSegment(sketch, "E2401", {"start": v(0.77, -0.47) * mm, "end": v(0.76, -0.47) * mm});
            skLineSegment(sketch, "E2402", {"start": v(0.76, -0.44) * mm, "end": v(0.77, -0.44) * mm});
            skLineSegment(sketch, "E2403", {"start": v(0.77, -0.44) * mm, "end": v(0.78, -0.45) * mm});
            skLineSegment(sketch, "E2404", {"start": v(0.78, -0.45) * mm, "end": v(0.8, -0.47) * mm});
            skLineSegment(sketch, "E2405", {"start": v(0.8, -0.47) * mm, "end": v(0.8, -0.47) * mm});
            skLineSegment(sketch, "E2406", {"start": v(0.8, -0.47) * mm, "end": v(0.79, -0.5) * mm});
            skLineSegment(sketch, "E2407", {"start": v(0.79, -0.5) * mm, "end": v(0.79, -0.5) * mm});
            skLineSegment(sketch, "E2408", {"start": v(0.79, -0.5) * mm, "end": v(0.76, -0.52) * mm});
            skLineSegment(sketch, "E2409", {"start": v(0.76, -0.52) * mm, "end": v(0.76, -0.52) * mm});
            skLineSegment(sketch, "E2410", {"start": v(0.76, -0.52) * mm, "end": v(0.76, -0.53) * mm});
            skLineSegment(sketch, "E2411", {"start": v(0.76, -0.53) * mm, "end": v(0.73, -0.52) * mm});
            skLineSegment(sketch, "E2412", {"start": v(0.73, -0.52) * mm, "end": v(0.73, -0.52) * mm});
            skLineSegment(sketch, "E2413", {"start": v(0.73, -0.52) * mm, "end": v(0.72, -0.52) * mm});
            skLineSegment(sketch, "E2414", {"start": v(0.72, -0.52) * mm, "end": v(0.72, -0.51) * mm});
            skLineSegment(sketch, "E2415", {"start": v(0.72, -0.51) * mm, "end": v(0.72, -0.51) * mm});
            skLineSegment(sketch, "E2416", {"start": v(0.72, -0.51) * mm, "end": v(0.72, -0.5) * mm});
            skLineSegment(sketch, "E2417", {"start": v(0.72, -0.5) * mm, "end": v(0.72, -0.5) * mm});
            skLineSegment(sketch, "E2418", {"start": v(0.72, -0.5) * mm, "end": v(0.73, -0.5) * mm});
            skLineSegment(sketch, "E2419", {"start": v(0.73, -0.5) * mm, "end": v(0.73, -0.5) * mm});
            skLineSegment(sketch, "E2420", {"start": v(0.73, -0.5) * mm, "end": v(0.75, -0.46) * mm});
            skLineSegment(sketch, "E2421", {"start": v(0.75, -0.46) * mm, "end": v(0.74, -0.46) * mm});
            skLineSegment(sketch, "E2422", {"start": v(0.74, -0.46) * mm, "end": v(0.74, -0.46) * mm});
            skLineSegment(sketch, "E2423", {"start": v(0.74, -0.46) * mm, "end": v(0.73, -0.46) * mm});
            skLineSegment(sketch, "E2424", {"start": v(0.73, -0.46) * mm, "end": v(0.73, -0.46) * mm});
            skLineSegment(sketch, "E2425", {"start": v(0.73, -0.46) * mm, "end": v(0.72, -0.47) * mm});
            skLineSegment(sketch, "E2426", {"start": v(0.72, -0.47) * mm, "end": v(0.71, -0.47) * mm});
            skLineSegment(sketch, "E2427", {"start": v(0.71, -0.47) * mm, "end": v(0.71, -0.47) * mm});
            skLineSegment(sketch, "E2428", {"start": v(0.71, -0.47) * mm, "end": v(0.71, -0.48) * mm});
            skLineSegment(sketch, "E2429", {"start": v(0.71, -0.48) * mm, "end": v(0.71, -0.48) * mm});
            skLineSegment(sketch, "E2430", {"start": v(0.71, -0.48) * mm, "end": v(0.7, -0.5) * mm});
            skLineSegment(sketch, "E2431", {"start": v(0.7, -0.5) * mm, "end": v(0.7, -0.5) * mm});
            skLineSegment(sketch, "E2432", {"start": v(0.7, -0.5) * mm, "end": v(0.69, -0.48) * mm});
            skLineSegment(sketch, "E2433", {"start": v(0.69, -0.48) * mm, "end": v(0.69, -0.48) * mm});
            skLineSegment(sketch, "E2434", {"start": v(0.69, -0.48) * mm, "end": v(0.7, -0.46) * mm});
            skLineSegment(sketch, "E2435", {"start": v(0.7, -0.46) * mm, "end": v(0.7, -0.46) * mm});
            skLineSegment(sketch, "E2436", {"start": v(0.7, -0.46) * mm, "end": v(0.7, -0.45) * mm});
            skLineSegment(sketch, "E2437", {"start": v(0.7, -0.45) * mm, "end": v(0.72, -0.43) * mm});
            skLineSegment(sketch, "E2438", {"start": v(0.72, -0.43) * mm, "end": v(0.73, -0.43) * mm});
            skLineSegment(sketch, "E2439", {"start": v(0.73, -0.43) * mm, "end": v(0.73, -0.43) * mm});
            skLineSegment(sketch, "E2440", {"start": v(0.73, -0.43) * mm, "end": v(0.76, -0.43) * mm});
            skLineSegment(sketch, "E2441", {"start": v(0.76, -0.43) * mm, "end": v(0.76, -0.44) * mm});
            skLineSegment(sketch, "E2442", {"start": v(0.69, -0.5) * mm, "end": v(0.69, -0.5) * mm});
            skLineSegment(sketch, "E2443", {"start": v(0.69, -0.5) * mm, "end": v(0.7, -0.51) * mm});
            skLineSegment(sketch, "E2444", {"start": v(0.7, -0.51) * mm, "end": v(0.7, -0.51) * mm});
            skLineSegment(sketch, "E2445", {"start": v(0.7, -0.51) * mm, "end": v(0.7, -0.52) * mm});
            skLineSegment(sketch, "E2446", {"start": v(0.7, -0.52) * mm, "end": v(0.7, -0.52) * mm});
            skLineSegment(sketch, "E2447", {"start": v(0.7, -0.52) * mm, "end": v(0.69, -0.52) * mm});
            skLineSegment(sketch, "E2448", {"start": v(0.69, -0.52) * mm, "end": v(0.69, -0.52) * mm});
            skLineSegment(sketch, "E2449", {"start": v(0.69, -0.52) * mm, "end": v(0.68, -0.53) * mm});
            skLineSegment(sketch, "E2450", {"start": v(0.68, -0.53) * mm, "end": v(0.68, -0.53) * mm});
            skLineSegment(sketch, "E2451", {"start": v(0.68, -0.53) * mm, "end": v(0.67, -0.54) * mm});
            skLineSegment(sketch, "E2452", {"start": v(0.67, -0.54) * mm, "end": v(0.67, -0.54) * mm});
            skLineSegment(sketch, "E2453", {"start": v(0.67, -0.54) * mm, "end": v(0.66, -0.55) * mm});
            skLineSegment(sketch, "E2454", {"start": v(0.66, -0.55) * mm, "end": v(0.67, -0.55) * mm});
            skLineSegment(sketch, "E2455", {"start": v(0.67, -0.55) * mm, "end": v(0.67, -0.55) * mm});
            skLineSegment(sketch, "E2456", {"start": v(0.67, -0.55) * mm, "end": v(0.68, -0.55) * mm});
            skLineSegment(sketch, "E2457", {"start": v(0.68, -0.55) * mm, "end": v(0.68, -0.55) * mm});
            skLineSegment(sketch, "E2458", {"start": v(0.68, -0.55) * mm, "end": v(0.69, -0.55) * mm});
            skLineSegment(sketch, "E2459", {"start": v(0.69, -0.55) * mm, "end": v(0.69, -0.55) * mm});
            skLineSegment(sketch, "E2460", {"start": v(0.69, -0.55) * mm, "end": v(0.7, -0.54) * mm});
            skLineSegment(sketch, "E2461", {"start": v(0.7, -0.54) * mm, "end": v(0.7, -0.54) * mm});
            skLineSegment(sketch, "E2462", {"start": v(0.7, -0.54) * mm, "end": v(0.71, -0.53) * mm});
            skLineSegment(sketch, "E2463", {"start": v(0.71, -0.53) * mm, "end": v(0.71, -0.53) * mm});
            skLineSegment(sketch, "E2464", {"start": v(0.71, -0.53) * mm, "end": v(0.73, -0.54) * mm});
            skLineSegment(sketch, "E2465", {"start": v(0.73, -0.54) * mm, "end": v(0.73, -0.54) * mm});
            skLineSegment(sketch, "E2466", {"start": v(0.73, -0.54) * mm, "end": v(0.74, -0.56) * mm});
            skLineSegment(sketch, "E2467", {"start": v(0.74, -0.56) * mm, "end": v(0.74, -0.56) * mm});
            skLineSegment(sketch, "E2468", {"start": v(0.74, -0.56) * mm, "end": v(0.73, -0.59) * mm});
            skLineSegment(sketch, "E2469", {"start": v(0.73, -0.59) * mm, "end": v(0.73, -0.59) * mm});
            skLineSegment(sketch, "E2470", {"start": v(0.73, -0.59) * mm, "end": v(0.72, -0.6) * mm});
            skLineSegment(sketch, "E2471", {"start": v(0.72, -0.6) * mm, "end": v(0.71, -0.6) * mm});
            skLineSegment(sketch, "E2472", {"start": v(0.71, -0.6) * mm, "end": v(0.71, -0.6) * mm});
            skLineSegment(sketch, "E2473", {"start": v(0.71, -0.6) * mm, "end": v(0.7, -0.6) * mm});
            skLineSegment(sketch, "E2474", {"start": v(0.7, -0.6) * mm, "end": v(0.7, -0.6) * mm});
            skLineSegment(sketch, "E2475", {"start": v(0.7, -0.6) * mm, "end": v(0.7, -0.59) * mm});
            skLineSegment(sketch, "E2476", {"start": v(0.7, -0.59) * mm, "end": v(0.7, -0.58) * mm});
            skLineSegment(sketch, "E2477", {"start": v(0.7, -0.58) * mm, "end": v(0.7, -0.58) * mm});
            skLineSegment(sketch, "E2478", {"start": v(0.7, -0.58) * mm, "end": v(0.71, -0.58) * mm});
            skLineSegment(sketch, "E2479", {"start": v(0.71, -0.58) * mm, "end": v(0.71, -0.58) * mm});
            skLineSegment(sketch, "E2480", {"start": v(0.71, -0.58) * mm, "end": v(0.71, -0.57) * mm});
            skLineSegment(sketch, "E2481", {"start": v(0.71, -0.57) * mm, "end": v(0.72, -0.57) * mm});
            skLineSegment(sketch, "E2482", {"start": v(0.72, -0.57) * mm, "end": v(0.72, -0.57) * mm});
            skLineSegment(sketch, "E2483", {"start": v(0.72, -0.57) * mm, "end": v(0.72, -0.56) * mm});
            skLineSegment(sketch, "E2484", {"start": v(0.72, -0.56) * mm, "end": v(0.72, -0.56) * mm});
            skLineSegment(sketch, "E2485", {"start": v(0.72, -0.56) * mm, "end": v(0.71, -0.56) * mm});
            skLineSegment(sketch, "E2486", {"start": v(0.71, -0.56) * mm, "end": v(0.7, -0.56) * mm});
            skLineSegment(sketch, "E2487", {"start": v(0.7, -0.56) * mm, "end": v(0.7, -0.56) * mm});
            skLineSegment(sketch, "E2488", {"start": v(0.7, -0.56) * mm, "end": v(0.7, -0.57) * mm});
            skLineSegment(sketch, "E2489", {"start": v(0.7, -0.57) * mm, "end": v(0.7, -0.57) * mm});
            skLineSegment(sketch, "E2490", {"start": v(0.7, -0.57) * mm, "end": v(0.69, -0.57) * mm});
            skLineSegment(sketch, "E2491", {"start": v(0.69, -0.57) * mm, "end": v(0.68, -0.58) * mm});
            skLineSegment(sketch, "E2492", {"start": v(0.68, -0.58) * mm, "end": v(0.68, -0.58) * mm});
            skLineSegment(sketch, "E2493", {"start": v(0.68, -0.58) * mm, "end": v(0.67, -0.58) * mm});
            skLineSegment(sketch, "E2494", {"start": v(0.67, -0.58) * mm, "end": v(0.67, -0.58) * mm});
            skLineSegment(sketch, "E2495", {"start": v(0.67, -0.58) * mm, "end": v(0.65, -0.57) * mm});
            skLineSegment(sketch, "E2496", {"start": v(0.65, -0.57) * mm, "end": v(0.65, -0.57) * mm});
            skLineSegment(sketch, "E2497", {"start": v(0.65, -0.57) * mm, "end": v(0.64, -0.55) * mm});
            skLineSegment(sketch, "E2498", {"start": v(0.64, -0.55) * mm, "end": v(0.64, -0.55) * mm});
            skLineSegment(sketch, "E2499", {"start": v(0.64, -0.55) * mm, "end": v(0.65, -0.53) * mm});
            skLineSegment(sketch, "E2500", {"start": v(0.65, -0.53) * mm, "end": v(0.65, -0.52) * mm});
            skLineSegment(sketch, "E2501", {"start": v(0.65, -0.52) * mm, "end": v(0.65, -0.52) * mm});
            skLineSegment(sketch, "E2502", {"start": v(0.65, -0.52) * mm, "end": v(0.67, -0.5) * mm});
            skLineSegment(sketch, "E2503", {"start": v(0.67, -0.5) * mm, "end": v(0.67, -0.5) * mm});
            skLineSegment(sketch, "E2504", {"start": v(0.67, -0.5) * mm, "end": v(0.69, -0.5) * mm});
            skLineSegment(sketch, "E2505", {"start": v(0.65, -0.59) * mm, "end": v(0.72, -0.66) * mm});
            skLineSegment(sketch, "E2506", {"start": v(0.72, -0.66) * mm, "end": v(0.72, -0.66) * mm});
            skLineSegment(sketch, "E2507", {"start": v(0.72, -0.66) * mm, "end": v(0.72, -0.67) * mm});
            skLineSegment(sketch, "E2508", {"start": v(0.72, -0.67) * mm, "end": v(0.72, -0.67) * mm});
            skLineSegment(sketch, "E2509", {"start": v(0.72, -0.67) * mm, "end": v(0.71, -0.67) * mm});
            skLineSegment(sketch, "E2510", {"start": v(0.71, -0.67) * mm, "end": v(0.7, -0.68) * mm});
            skLineSegment(sketch, "E2511", {"start": v(0.7, -0.68) * mm, "end": v(0.7, -0.68) * mm});
            skLineSegment(sketch, "E2512", {"start": v(0.7, -0.68) * mm, "end": v(0.67, -0.65) * mm});
            skLineSegment(sketch, "E2513", {"start": v(0.67, -0.65) * mm, "end": v(0.66, -0.67) * mm});
            skLineSegment(sketch, "E2514", {"start": v(0.66, -0.67) * mm, "end": v(0.66, -0.67) * mm});
            skLineSegment(sketch, "E2515", {"start": v(0.66, -0.67) * mm, "end": v(0.65, -0.67) * mm});
            skLineSegment(sketch, "E2516", {"start": v(0.65, -0.67) * mm, "end": v(0.65, -0.67) * mm});
            skLineSegment(sketch, "E2517", {"start": v(0.65, -0.67) * mm, "end": v(0.64, -0.66) * mm});
            skLineSegment(sketch, "E2518", {"start": v(0.64, -0.66) * mm, "end": v(0.64, -0.66) * mm});
            skLineSegment(sketch, "E2519", {"start": v(0.64, -0.66) * mm, "end": v(0.66, -0.64) * mm});
            skLineSegment(sketch, "E2520", {"start": v(0.66, -0.64) * mm, "end": v(0.63, -0.6) * mm});
            skLineSegment(sketch, "E2521", {"start": v(0.63, -0.6) * mm, "end": v(0.63, -0.6) * mm});
            skLineSegment(sketch, "E2522", {"start": v(0.63, -0.6) * mm, "end": v(0.62, -0.6) * mm});
            skLineSegment(sketch, "E2523", {"start": v(0.62, -0.6) * mm, "end": v(0.62, -0.6) * mm});
            skLineSegment(sketch, "E2524", {"start": v(0.62, -0.6) * mm, "end": v(0.61, -0.6) * mm});
            skLineSegment(sketch, "E2525", {"start": v(0.61, -0.6) * mm, "end": v(0.61, -0.6) * mm});
            skLineSegment(sketch, "E2526", {"start": v(0.61, -0.6) * mm, "end": v(0.6, -0.62) * mm});
            skLineSegment(sketch, "E2527", {"start": v(0.6, -0.62) * mm, "end": v(0.6, -0.62) * mm});
            skLineSegment(sketch, "E2528", {"start": v(0.6, -0.62) * mm, "end": v(0.59, -0.62) * mm});
            skLineSegment(sketch, "E2529", {"start": v(0.59, -0.62) * mm, "end": v(0.59, -0.62) * mm});
            skLineSegment(sketch, "E2530", {"start": v(0.59, -0.62) * mm, "end": v(0.59, -0.6) * mm});
            skLineSegment(sketch, "E2531", {"start": v(0.59, -0.6) * mm, "end": v(0.59, -0.6) * mm});
            skLineSegment(sketch, "E2532", {"start": v(0.59, -0.6) * mm, "end": v(0.6, -0.6) * mm});
            skLineSegment(sketch, "E2533", {"start": v(0.6, -0.6) * mm, "end": v(0.6, -0.59) * mm});
            skLineSegment(sketch, "E2534", {"start": v(0.6, -0.59) * mm, "end": v(0.62, -0.58) * mm});
            skLineSegment(sketch, "E2535", {"start": v(0.62, -0.58) * mm, "end": v(0.64, -0.58) * mm});
            skLineSegment(sketch, "E2536", {"start": v(0.64, -0.58) * mm, "end": v(0.65, -0.59) * mm});
            skLineSegment(sketch, "E2537", {"start": v(0.58, -0.66) * mm, "end": v(0.58, -0.66) * mm});
            skLineSegment(sketch, "E2538", {"start": v(0.58, -0.66) * mm, "end": v(0.57, -0.65) * mm});
            skLineSegment(sketch, "E2539", {"start": v(0.57, -0.65) * mm, "end": v(0.57, -0.65) * mm});
            skLineSegment(sketch, "E2540", {"start": v(0.57, -0.65) * mm, "end": v(0.56, -0.66) * mm});
            skLineSegment(sketch, "E2541", {"start": v(0.56, -0.66) * mm, "end": v(0.56, -0.66) * mm});
            skLineSegment(sketch, "E2542", {"start": v(0.56, -0.66) * mm, "end": v(0.55, -0.67) * mm});
            skLineSegment(sketch, "E2543", {"start": v(0.55, -0.67) * mm, "end": v(0.55, -0.67) * mm});
            skLineSegment(sketch, "E2544", {"start": v(0.55, -0.67) * mm, "end": v(0.56, -0.68) * mm});
            skLineSegment(sketch, "E2545", {"start": v(0.56, -0.68) * mm, "end": v(0.56, -0.68) * mm});
            skLineSegment(sketch, "E2546", {"start": v(0.56, -0.68) * mm, "end": v(0.57, -0.7) * mm});
            skLineSegment(sketch, "E2547", {"start": v(0.57, -0.7) * mm, "end": v(0.57, -0.7) * mm});
            skLineSegment(sketch, "E2548", {"start": v(0.57, -0.7) * mm, "end": v(0.58, -0.7) * mm});
            skLineSegment(sketch, "E2549", {"start": v(0.58, -0.7) * mm, "end": v(0.58, -0.7) * mm});
            skLineSegment(sketch, "E2550", {"start": v(0.58, -0.7) * mm, "end": v(0.6, -0.7) * mm});
            skLineSegment(sketch, "E2551", {"start": v(0.6, -0.7) * mm, "end": v(0.6, -0.7) * mm});
            skLineSegment(sketch, "E2552", {"start": v(0.6, -0.7) * mm, "end": v(0.6, -0.69) * mm});
            skLineSegment(sketch, "E2553", {"start": v(0.6, -0.69) * mm, "end": v(0.6, -0.69) * mm});
            skLineSegment(sketch, "E2554", {"start": v(0.6, -0.69) * mm, "end": v(0.6, -0.67) * mm});
            skLineSegment(sketch, "E2555", {"start": v(0.6, -0.67) * mm, "end": v(0.6, -0.67) * mm});
            skLineSegment(sketch, "E2556", {"start": v(0.6, -0.67) * mm, "end": v(0.58, -0.66) * mm});
            skLineSegment(sketch, "E2557", {"start": v(0.6, -0.64) * mm, "end": v(0.62, -0.66) * mm});
            skLineSegment(sketch, "E2558", {"start": v(0.62, -0.66) * mm, "end": v(0.62, -0.66) * mm});
            skLineSegment(sketch, "E2559", {"start": v(0.62, -0.66) * mm, "end": v(0.63, -0.68) * mm});
            skLineSegment(sketch, "E2560", {"start": v(0.63, -0.68) * mm, "end": v(0.63, -0.69) * mm});
            skLineSegment(sketch, "E2561", {"start": v(0.63, -0.69) * mm, "end": v(0.62, -0.69) * mm});
            skLineSegment(sketch, "E2562", {"start": v(0.62, -0.69) * mm, "end": v(0.61, -0.72) * mm});
            skLineSegment(sketch, "E2563", {"start": v(0.61, -0.72) * mm, "end": v(0.6, -0.72) * mm});
            skLineSegment(sketch, "E2564", {"start": v(0.6, -0.72) * mm, "end": v(0.6, -0.72) * mm});
            skLineSegment(sketch, "E2565", {"start": v(0.6, -0.72) * mm, "end": v(0.58, -0.73) * mm});
            skLineSegment(sketch, "E2566", {"start": v(0.58, -0.73) * mm, "end": v(0.58, -0.73) * mm});
            skLineSegment(sketch, "E2567", {"start": v(0.58, -0.73) * mm, "end": v(0.57, -0.73) * mm});
            skLineSegment(sketch, "E2568", {"start": v(0.57, -0.73) * mm, "end": v(0.55, -0.72) * mm});
            skLineSegment(sketch, "E2569", {"start": v(0.55, -0.72) * mm, "end": v(0.55, -0.72) * mm});
            skLineSegment(sketch, "E2570", {"start": v(0.55, -0.72) * mm, "end": v(0.54, -0.7) * mm});
            skLineSegment(sketch, "E2571", {"start": v(0.54, -0.7) * mm, "end": v(0.53, -0.7) * mm});
            skLineSegment(sketch, "E2572", {"start": v(0.53, -0.7) * mm, "end": v(0.53, -0.67) * mm});
            skLineSegment(sketch, "E2573", {"start": v(0.53, -0.67) * mm, "end": v(0.53, -0.67) * mm});
            skLineSegment(sketch, "E2574", {"start": v(0.53, -0.67) * mm, "end": v(0.54, -0.64) * mm});
            skLineSegment(sketch, "E2575", {"start": v(0.54, -0.64) * mm, "end": v(0.54, -0.64) * mm});
            skLineSegment(sketch, "E2576", {"start": v(0.54, -0.64) * mm, "end": v(0.57, -0.63) * mm});
            skLineSegment(sketch, "E2577", {"start": v(0.57, -0.63) * mm, "end": v(0.57, -0.63) * mm});
            skLineSegment(sketch, "E2578", {"start": v(0.57, -0.63) * mm, "end": v(0.58, -0.63) * mm});
            skLineSegment(sketch, "E2579", {"start": v(0.58, -0.63) * mm, "end": v(0.6, -0.64) * mm});
            skLineSegment(sketch, "E2580", {"start": v(0.6, -0.64) * mm, "end": v(0.6, -0.64) * mm});
            skLineSegment(sketch, "E2581", {"start": v(0.5, -0.68) * mm, "end": v(0.5, -0.68) * mm});
            skLineSegment(sketch, "E2582", {"start": v(0.5, -0.68) * mm, "end": v(0.5, -0.69) * mm});
            skLineSegment(sketch, "E2583", {"start": v(0.5, -0.69) * mm, "end": v(0.5, -0.69) * mm});
            skLineSegment(sketch, "E2584", {"start": v(0.5, -0.69) * mm, "end": v(0.51, -0.7) * mm});
            skLineSegment(sketch, "E2585", {"start": v(0.51, -0.7) * mm, "end": v(0.51, -0.7) * mm});
            skLineSegment(sketch, "E2586", {"start": v(0.51, -0.7) * mm, "end": v(0.5, -0.7) * mm});
            skLineSegment(sketch, "E2587", {"start": v(0.5, -0.7) * mm, "end": v(0.5, -0.7) * mm});
            skLineSegment(sketch, "E2588", {"start": v(0.5, -0.7) * mm, "end": v(0.49, -0.7) * mm});
            skLineSegment(sketch, "E2589", {"start": v(0.49, -0.7) * mm, "end": v(0.49, -0.7) * mm});
            skLineSegment(sketch, "E2590", {"start": v(0.49, -0.7) * mm, "end": v(0.48, -0.7) * mm});
            skLineSegment(sketch, "E2591", {"start": v(0.48, -0.7) * mm, "end": v(0.48, -0.7) * mm});
            skLineSegment(sketch, "E2592", {"start": v(0.48, -0.7) * mm, "end": v(0.49, -0.68) * mm});
            skLineSegment(sketch, "E2593", {"start": v(0.49, -0.68) * mm, "end": v(0.49, -0.68) * mm});
            skLineSegment(sketch, "E2594", {"start": v(0.49, -0.68) * mm, "end": v(0.5, -0.68) * mm});
            skLineSegment(sketch, "E2595", {"start": v(0.54, -0.81) * mm, "end": v(0.54, -0.81) * mm});
            skLineSegment(sketch, "E2596", {"start": v(0.54, -0.81) * mm, "end": v(0.54, -0.82) * mm});
            skLineSegment(sketch, "E2597", {"start": v(0.54, -0.82) * mm, "end": v(0.54, -0.82) * mm});
            skLineSegment(sketch, "E2598", {"start": v(0.54, -0.82) * mm, "end": v(0.54, -0.83) * mm});
            skLineSegment(sketch, "E2599", {"start": v(0.54, -0.83) * mm, "end": v(0.53, -0.83) * mm});
            skLineSegment(sketch, "E2600", {"start": v(0.53, -0.83) * mm, "end": v(0.53, -0.83) * mm});
            skLineSegment(sketch, "E2601", {"start": v(0.53, -0.83) * mm, "end": v(0.52, -0.83) * mm});
            skLineSegment(sketch, "E2602", {"start": v(0.52, -0.83) * mm, "end": v(0.52, -0.83) * mm});
            skLineSegment(sketch, "E2603", {"start": v(0.52, -0.83) * mm, "end": v(0.51, -0.82) * mm});
            skLineSegment(sketch, "E2604", {"start": v(0.51, -0.82) * mm, "end": v(0.51, -0.82) * mm});
            skLineSegment(sketch, "E2605", {"start": v(0.51, -0.82) * mm, "end": v(0.52, -0.82) * mm});
            skLineSegment(sketch, "E2606", {"start": v(0.52, -0.82) * mm, "end": v(0.52, -0.81) * mm});
            skLineSegment(sketch, "E2607", {"start": v(0.52, -0.81) * mm, "end": v(0.52, -0.81) * mm});
            skLineSegment(sketch, "E2608", {"start": v(0.52, -0.81) * mm, "end": v(0.52, -0.8) * mm});
            skLineSegment(sketch, "E2609", {"start": v(0.52, -0.8) * mm, "end": v(0.53, -0.8) * mm});
            skLineSegment(sketch, "E2610", {"start": v(0.53, -0.8) * mm, "end": v(0.53, -0.8) * mm});
            skLineSegment(sketch, "E2611", {"start": v(0.53, -0.8) * mm, "end": v(0.54, -0.81) * mm});
            skLineSegment(sketch, "E2612", {"start": v(0.47, -0.7) * mm, "end": v(0.52, -0.78) * mm});
            skLineSegment(sketch, "E2613", {"start": v(0.52, -0.78) * mm, "end": v(0.52, -0.78) * mm});
            skLineSegment(sketch, "E2614", {"start": v(0.52, -0.78) * mm, "end": v(0.52, -0.79) * mm});
            skLineSegment(sketch, "E2615", {"start": v(0.52, -0.79) * mm, "end": v(0.5, -0.8) * mm});
            skLineSegment(sketch, "E2616", {"start": v(0.5, -0.8) * mm, "end": v(0.5, -0.8) * mm});
            skLineSegment(sketch, "E2617", {"start": v(0.5, -0.8) * mm, "end": v(0.45, -0.72) * mm});
            skLineSegment(sketch, "E2618", {"start": v(0.45, -0.72) * mm, "end": v(0.45, -0.72) * mm});
            skLineSegment(sketch, "E2619", {"start": v(0.45, -0.72) * mm, "end": v(0.45, -0.7) * mm});
            skLineSegment(sketch, "E2620", {"start": v(0.45, -0.7) * mm, "end": v(0.46, -0.7) * mm});
            skLineSegment(sketch, "E2621", {"start": v(0.46, -0.7) * mm, "end": v(0.46, -0.7) * mm});
            skLineSegment(sketch, "E2622", {"start": v(0.46, -0.7) * mm, "end": v(0.47, -0.7) * mm});
            skLineSegment(sketch, "E2623", {"start": v(0.47, -0.7) * mm, "end": v(0.47, -0.7) * mm});
            skLineSegment(sketch, "E2624", {"start": v(0.43, -0.77) * mm, "end": v(0.43, -0.77) * mm});
            skLineSegment(sketch, "E2625", {"start": v(0.43, -0.77) * mm, "end": v(0.42, -0.76) * mm});
            skLineSegment(sketch, "E2626", {"start": v(0.42, -0.76) * mm, "end": v(0.42, -0.76) * mm});
            skLineSegment(sketch, "E2627", {"start": v(0.42, -0.76) * mm, "end": v(0.4, -0.76) * mm});
            skLineSegment(sketch, "E2628", {"start": v(0.4, -0.76) * mm, "end": v(0.4, -0.76) * mm});
            skLineSegment(sketch, "E2629", {"start": v(0.4, -0.76) * mm, "end": v(0.4, -0.77) * mm});
            skLineSegment(sketch, "E2630", {"start": v(0.4, -0.77) * mm, "end": v(0.4, -0.78) * mm});
            skLineSegment(sketch, "E2631", {"start": v(0.4, -0.78) * mm, "end": v(0.4, -0.78) * mm});
            skLineSegment(sketch, "E2632", {"start": v(0.4, -0.78) * mm, "end": v(0.4, -0.79) * mm});
            skLineSegment(sketch, "E2633", {"start": v(0.4, -0.79) * mm, "end": v(0.4, -0.79) * mm});
            skLineSegment(sketch, "E2634", {"start": v(0.4, -0.79) * mm, "end": v(0.4, -0.8) * mm});
            skLineSegment(sketch, "E2635", {"start": v(0.4, -0.8) * mm, "end": v(0.4, -0.8) * mm});
            skLineSegment(sketch, "E2636", {"start": v(0.4, -0.8) * mm, "end": v(0.41, -0.81) * mm});
            skLineSegment(sketch, "E2637", {"start": v(0.41, -0.81) * mm, "end": v(0.42, -0.81) * mm});
            skLineSegment(sketch, "E2638", {"start": v(0.42, -0.81) * mm, "end": v(0.42, -0.81) * mm});
            skLineSegment(sketch, "E2639", {"start": v(0.42, -0.81) * mm, "end": v(0.43, -0.81) * mm});
            skLineSegment(sketch, "E2640", {"start": v(0.43, -0.81) * mm, "end": v(0.43, -0.81) * mm});
            skLineSegment(sketch, "E2641", {"start": v(0.43, -0.81) * mm, "end": v(0.44, -0.8) * mm});
            skLineSegment(sketch, "E2642", {"start": v(0.44, -0.8) * mm, "end": v(0.44, -0.8) * mm});
            skLineSegment(sketch, "E2643", {"start": v(0.44, -0.8) * mm, "end": v(0.44, -0.79) * mm});
            skLineSegment(sketch, "E2644", {"start": v(0.44, -0.79) * mm, "end": v(0.44, -0.79) * mm});
            skLineSegment(sketch, "E2645", {"start": v(0.44, -0.79) * mm, "end": v(0.43, -0.77) * mm});
            skLineSegment(sketch, "E2646", {"start": v(0.45, -0.76) * mm, "end": v(0.46, -0.78) * mm});
            skLineSegment(sketch, "E2647", {"start": v(0.46, -0.78) * mm, "end": v(0.46, -0.78) * mm});
            skLineSegment(sketch, "E2648", {"start": v(0.46, -0.78) * mm, "end": v(0.46, -0.8) * mm});
            skLineSegment(sketch, "E2649", {"start": v(0.46, -0.8) * mm, "end": v(0.46, -0.8) * mm});
            skLineSegment(sketch, "E2650", {"start": v(0.46, -0.8) * mm, "end": v(0.46, -0.81) * mm});
            skLineSegment(sketch, "E2651", {"start": v(0.46, -0.81) * mm, "end": v(0.44, -0.83) * mm});
            skLineSegment(sketch, "E2652", {"start": v(0.44, -0.83) * mm, "end": v(0.44, -0.83) * mm});
            skLineSegment(sketch, "E2653", {"start": v(0.44, -0.83) * mm, "end": v(0.4, -0.84) * mm});
            skLineSegment(sketch, "E2654", {"start": v(0.4, -0.84) * mm, "end": v(0.4, -0.84) * mm});
            skLineSegment(sketch, "E2655", {"start": v(0.4, -0.84) * mm, "end": v(0.38, -0.82) * mm});
            skLineSegment(sketch, "E2656", {"start": v(0.38, -0.82) * mm, "end": v(0.38, -0.82) * mm});
            skLineSegment(sketch, "E2657", {"start": v(0.38, -0.82) * mm, "end": v(0.37, -0.8) * mm});
            skLineSegment(sketch, "E2658", {"start": v(0.37, -0.8) * mm, "end": v(0.37, -0.8) * mm});
            skLineSegment(sketch, "E2659", {"start": v(0.37, -0.8) * mm, "end": v(0.37, -0.77) * mm});
            skLineSegment(sketch, "E2660", {"start": v(0.37, -0.77) * mm, "end": v(0.37, -0.77) * mm});
            skLineSegment(sketch, "E2661", {"start": v(0.37, -0.77) * mm, "end": v(0.39, -0.74) * mm});
            skLineSegment(sketch, "E2662", {"start": v(0.39, -0.74) * mm, "end": v(0.4, -0.74) * mm});
            skLineSegment(sketch, "E2663", {"start": v(0.4, -0.74) * mm, "end": v(0.4, -0.74) * mm});
            skLineSegment(sketch, "E2664", {"start": v(0.4, -0.74) * mm, "end": v(0.42, -0.74) * mm});
            skLineSegment(sketch, "E2665", {"start": v(0.42, -0.74) * mm, "end": v(0.43, -0.74) * mm});
            skLineSegment(sketch, "E2666", {"start": v(0.43, -0.74) * mm, "end": v(0.43, -0.74) * mm});
            skLineSegment(sketch, "E2667", {"start": v(0.43, -0.74) * mm, "end": v(0.45, -0.76) * mm});
            skLineSegment(sketch, "E2668", {"start": v(0.45, -0.76) * mm, "end": v(0.45, -0.76) * mm});
            skLineSegment(sketch, "E2669.bottom", {"start": v(1, -1) * mm, "end": v(-1, -1) * mm});
            skLineSegment(sketch, "E2669.top", {"start": v(1, 1) * mm, "end": v(-1, 1) * mm});
            skLineSegment(sketch, "E2669.left", {"start": v(1, -1) * mm, "end": v(1, 1) * mm});
            skLineSegment(sketch, "E2669.right", {"start": v(-1, -1) * mm, "end": v(-1, 1) * mm});
            skPoint(sketch, "E2669.middle", {"position": v(0, 0) * mm});
            skSolve(sketch);
        }
        {
            var Q0;
            Q0 = qSketchRegion(id + "F0", true);
            var Q1;
            Q1=makeQuery(id+"F0.imprint","IMPRINT",FACE,{"disambiguationData":[TD([[makeQuery(id+"F0.imprint","IMPRINT",EDGE,{"derivedFrom":sQuery(id+"F0.wireOp",EDGE,"E153")}),-1.0]])]});
            var Q2;
            Q2=makeQuery(id+"F0.imprint","IMPRINT",FACE,{"disambiguationData":[TD([[makeQuery(id+"F0.imprint","IMPRINT",EDGE,{"derivedFrom":sQuery(id+"F0.wireOp",EDGE,"E27")}),-1.0]])]});
            var Q3;
            Q3=makeQuery(id+"F0.imprint","IMPRINT",FACE,{"disambiguationData":[TD([[makeQuery(id+"F0.imprint","IMPRINT",EDGE,{"derivedFrom":sQuery(id+"F0.wireOp",EDGE,"E74")}),-1.0]])]});
            var Q4;
            Q4=makeQuery(id+"F0.imprint","IMPRINT",FACE,{"disambiguationData":[TD([[makeQuery(id+"F0.imprint","IMPRINT",EDGE,{"derivedFrom":sQuery(id+"F0.wireOp",EDGE,"E0")}),-1.0]])]});
            var Q5;
            Q5=makeQuery(id+"F0.imprint","IMPRINT",FACE,{"disambiguationData":[TD([[makeQuery(id+"F0.imprint","IMPRINT",EDGE,{"derivedFrom":sQuery(id+"F0.wireOp",EDGE,"E440")}),1.0]])]});
            var Q6;
            Q6=makeQuery(id+"F0.imprint","IMPRINT",FACE,{"disambiguationData":[TD([[makeQuery(id+"F0.imprint","IMPRINT",EDGE,{"derivedFrom":sQuery(id+"F0.wireOp",EDGE,"E540")}),1.0]])]});
            var Q7;
            Q7=makeQuery(id+"F0.imprint","IMPRINT",FACE,{"disambiguationData":[TD([[makeQuery(id+"F0.imprint","IMPRINT",EDGE,{"derivedFrom":sQuery(id+"F0.wireOp",EDGE,"E2624")}),1.0]])]});
            var Q8;
            Q8=makeQuery(id+"F0.imprint","IMPRINT",FACE,{"disambiguationData":[TD([[makeQuery(id+"F0.imprint","IMPRINT",EDGE,{"derivedFrom":sQuery(id+"F0.wireOp",EDGE,"E2537")}),1.0]])]});
            var Q9;
            Q9=makeQuery(id+"F0.imprint","IMPRINT",FACE,{"disambiguationData":[TD([[makeQuery(id+"F0.imprint","IMPRINT",EDGE,{"derivedFrom":sQuery(id+"F0.wireOp",EDGE,"E2388")}),1.0]])]});
            var Q10;
            Q10=makeQuery(id+"F0.imprint","IMPRINT",FACE,{"disambiguationData":[TD([[makeQuery(id+"F0.imprint","IMPRINT",EDGE,{"derivedFrom":sQuery(id+"F0.wireOp",EDGE,"E2217")}),1.0]])]});
            var Q11;
            Q11=makeQuery(id+"F0.imprint","IMPRINT",FACE,{"disambiguationData":[TD([[makeQuery(id+"F0.imprint","IMPRINT",EDGE,{"derivedFrom":sQuery(id+"F0.wireOp",EDGE,"E1915")}),1.0]])]});
            var Q12;
            Q12=makeQuery(id+"F0.imprint","IMPRINT",FACE,{"disambiguationData":[TD([[makeQuery(id+"F0.imprint","IMPRINT",EDGE,{"derivedFrom":sQuery(id+"F0.wireOp",EDGE,"E1856")}),1.0]])]});
            var Q13;
            Q13=makeQuery(id+"F0.imprint","IMPRINT",FACE,{"disambiguationData":[TD([[makeQuery(id+"F0.imprint","IMPRINT",EDGE,{"derivedFrom":sQuery(id+"F0.wireOp",EDGE,"E1771")}),1.0]])]});
            var Q14;
            Q14=makeQuery(id+"F0.imprint","IMPRINT",FACE,{"disambiguationData":[TD([[makeQuery(id+"F0.imprint","IMPRINT",EDGE,{"derivedFrom":sQuery(id+"F0.wireOp",EDGE,"E1642")}),1.0]])]});
            var Q15;
            Q15=makeQuery(id+"F0.imprint","IMPRINT",FACE,{"disambiguationData":[TD([[makeQuery(id+"F0.imprint","IMPRINT",EDGE,{"derivedFrom":sQuery(id+"F0.wireOp",EDGE,"E1502")}),1.0]])]});
            var Q16;
            Q16=makeQuery(id+"F0.imprint","IMPRINT",FACE,{"disambiguationData":[TD([[makeQuery(id+"F0.imprint","IMPRINT",EDGE,{"derivedFrom":sQuery(id+"F0.wireOp",EDGE,"E1432")}),1.0]])]});
            var Q17;
            Q17=makeQuery(id+"F0.imprint","IMPRINT",FACE,{"disambiguationData":[TD([[makeQuery(id+"F0.imprint","IMPRINT",EDGE,{"derivedFrom":sQuery(id+"F0.wireOp",EDGE,"E1082")}),1.0]])]});
            var Q18;
            Q18=makeQuery(id+"F0.imprint","IMPRINT",FACE,{"disambiguationData":[TD([[makeQuery(id+"F0.imprint","IMPRINT",EDGE,{"derivedFrom":sQuery(id+"F0.wireOp",EDGE,"E1099")}),1.0]])]});
            var Q19;
            Q19=makeQuery(id+"F0.imprint","IMPRINT",FACE,{"disambiguationData":[TD([[makeQuery(id+"F0.imprint","IMPRINT",EDGE,{"derivedFrom":sQuery(id+"F0.wireOp",EDGE,"E795")}),1.0]])]});
            extrude(context, id + "F1", {"entities" : qUnion([Q0, Q1, Q2, Q3, Q4, Q5, Q6, Q7, Q8, Q9, Q10, Q11, Q12, Q13, Q14, Q15, Q16, Q17, Q18, Q19]), "depth" : 0.03 * mm, "offsetDistance" : 25 * mm});
        }
        {
            var Q0;
            Q0=makeQuery(id+"F1.opExtrude","SWEPT_BODY",BODY,{"disambiguationData":[OSD([sQuery(id+"F0.wireOp",EDGE,"E0"),sQuery(id+"F0.wireOp",EDGE,"E1"),sQuery(id+"F0.wireOp",EDGE,"E2"),sQuery(id+"F0.wireOp",EDGE,"E3"),sQuery(id+"F0.wireOp",EDGE,"E3"),sQuery(id+"F0.wireOp",EDGE,"E4"),sQuery(id+"F0.wireOp",EDGE,"E5"),sQuery(id+"F0.wireOp",EDGE,"E6"),sQuery(id+"F0.wireOp",EDGE,"E7"),sQuery(id+"F0.wireOp",EDGE,"E8"),sQuery(id+"F0.wireOp",EDGE,"E9"),sQuery(id+"F0.wireOp",EDGE,"E10"),sQuery(id+"F0.wireOp",EDGE,"E11"),sQuery(id+"F0.wireOp",EDGE,"E12"),sQuery(id+"F0.wireOp",EDGE,"E13"),sQuery(id+"F0.wireOp",EDGE,"E14"),sQuery(id+"F0.wireOp",EDGE,"E15"),sQuery(id+"F0.wireOp",EDGE,"E16"),sQuery(id+"F0.wireOp",EDGE,"E17"),sQuery(id+"F0.wireOp",EDGE,"E18"),sQuery(id+"F0.wireOp",EDGE,"E19"),sQuery(id+"F0.wireOp",EDGE,"E20"),sQuery(id+"F0.wireOp",EDGE,"E21"),sQuery(id+"F0.wireOp",EDGE,"E22"),sQuery(id+"F0.wireOp",EDGE,"E23"),sQuery(id+"F0.wireOp",EDGE,"E24"),sQuery(id+"F0.wireOp",EDGE,"E25"),sQuery(id+"F0.wireOp",EDGE,"E26")])]});
            var Q1;
            Q1=makeQuery(id+"F1.opExtrude","SWEPT_BODY",BODY,{"disambiguationData":[OSD([sQuery(id+"F0.wireOp",EDGE,"E27"),sQuery(id+"F0.wireOp",EDGE,"E28"),sQuery(id+"F0.wireOp",EDGE,"E29"),sQuery(id+"F0.wireOp",EDGE,"E30"),sQuery(id+"F0.wireOp",EDGE,"E31"),sQuery(id+"F0.wireOp",EDGE,"E32"),sQuery(id+"F0.wireOp",EDGE,"E33"),sQuery(id+"F0.wireOp",EDGE,"E34"),sQuery(id+"F0.wireOp",EDGE,"E35"),sQuery(id+"F0.wireOp",EDGE,"E36"),sQuery(id+"F0.wireOp",EDGE,"E37"),sQuery(id+"F0.wireOp",EDGE,"E38"),sQuery(id+"F0.wireOp",EDGE,"E39"),sQuery(id+"F0.wireOp",EDGE,"E40"),sQuery(id+"F0.wireOp",EDGE,"E41"),sQuery(id+"F0.wireOp",EDGE,"E42"),sQuery(id+"F0.wireOp",EDGE,"E43"),sQuery(id+"F0.wireOp",EDGE,"E44"),sQuery(id+"F0.wireOp",EDGE,"E45"),sQuery(id+"F0.wireOp",EDGE,"E46"),sQuery(id+"F0.wireOp",EDGE,"E47"),sQuery(id+"F0.wireOp",EDGE,"E48"),sQuery(id+"F0.wireOp",EDGE,"E49"),sQuery(id+"F0.wireOp",EDGE,"E49"),sQuery(id+"F0.wireOp",EDGE,"E49"),sQuery(id+"F0.wireOp",EDGE,"E50"),sQuery(id+"F0.wireOp",EDGE,"E51"),sQuery(id+"F0.wireOp",EDGE,"E52"),sQuery(id+"F0.wireOp",EDGE,"E53"),sQuery(id+"F0.wireOp",EDGE,"E55"),sQuery(id+"F0.wireOp",EDGE,"E56"),sQuery(id+"F0.wireOp",EDGE,"E57"),sQuery(id+"F0.wireOp",EDGE,"E58"),sQuery(id+"F0.wireOp",EDGE,"E59"),sQuery(id+"F0.wireOp",EDGE,"E60"),sQuery(id+"F0.wireOp",EDGE,"E61"),sQuery(id+"F0.wireOp",EDGE,"E62"),sQuery(id+"F0.wireOp",EDGE,"E63"),sQuery(id+"F0.wireOp",EDGE,"E64"),sQuery(id+"F0.wireOp",EDGE,"E65"),sQuery(id+"F0.wireOp",EDGE,"E66"),sQuery(id+"F0.wireOp",EDGE,"E67"),sQuery(id+"F0.wireOp",EDGE,"E68"),sQuery(id+"F0.wireOp",EDGE,"E69"),sQuery(id+"F0.wireOp",EDGE,"E70"),sQuery(id+"F0.wireOp",EDGE,"E71"),sQuery(id+"F0.wireOp",EDGE,"E72"),sQuery(id+"F0.wireOp",EDGE,"E73")])]});
            var Q2;
            Q2=makeQuery(id+"F1.opExtrude","SWEPT_BODY",BODY,{"disambiguationData":[OSD([sQuery(id+"F0.wireOp",EDGE,"E74"),sQuery(id+"F0.wireOp",EDGE,"E75"),sQuery(id+"F0.wireOp",EDGE,"E76"),sQuery(id+"F0.wireOp",EDGE,"E77"),sQuery(id+"F0.wireOp",EDGE,"E78"),sQuery(id+"F0.wireOp",EDGE,"E79"),sQuery(id+"F0.wireOp",EDGE,"E80"),sQuery(id+"F0.wireOp",EDGE,"E81"),sQuery(id+"F0.wireOp",EDGE,"E82"),sQuery(id+"F0.wireOp",EDGE,"E83"),sQuery(id+"F0.wireOp",EDGE,"E84"),sQuery(id+"F0.wireOp",EDGE,"E85"),sQuery(id+"F0.wireOp",EDGE,"E86"),sQuery(id+"F0.wireOp",EDGE,"E87"),sQuery(id+"F0.wireOp",EDGE,"E88"),sQuery(id+"F0.wireOp",EDGE,"E89"),sQuery(id+"F0.wireOp",EDGE,"E90"),sQuery(id+"F0.wireOp",EDGE,"E91"),sQuery(id+"F0.wireOp",EDGE,"E92")])]});
            var Q3;
            Q3=makeQuery(id+"F1.opExtrude","SWEPT_BODY",BODY,{"disambiguationData":[OSD([sQuery(id+"F0.wireOp",EDGE,"E93"),sQuery(id+"F0.wireOp",EDGE,"E94"),sQuery(id+"F0.wireOp",EDGE,"E95"),sQuery(id+"F0.wireOp",EDGE,"E96"),sQuery(id+"F0.wireOp",EDGE,"E97"),sQuery(id+"F0.wireOp",EDGE,"E98"),sQuery(id+"F0.wireOp",EDGE,"E99"),sQuery(id+"F0.wireOp",EDGE,"E100"),sQuery(id+"F0.wireOp",EDGE,"E101"),sQuery(id+"F0.wireOp",EDGE,"E102"),sQuery(id+"F0.wireOp",EDGE,"E103"),sQuery(id+"F0.wireOp",EDGE,"E104"),sQuery(id+"F0.wireOp",EDGE,"E105"),sQuery(id+"F0.wireOp",EDGE,"E106"),sQuery(id+"F0.wireOp",EDGE,"E107"),sQuery(id+"F0.wireOp",EDGE,"E108"),sQuery(id+"F0.wireOp",EDGE,"E109"),sQuery(id+"F0.wireOp",EDGE,"E110"),sQuery(id+"F0.wireOp",EDGE,"E111"),sQuery(id+"F0.wireOp",EDGE,"E112"),sQuery(id+"F0.wireOp",EDGE,"E112"),sQuery(id+"F0.wireOp",EDGE,"E112"),sQuery(id+"F0.wireOp",EDGE,"E112"),sQuery(id+"F0.wireOp",EDGE,"E112"),sQuery(id+"F0.wireOp",EDGE,"E113"),sQuery(id+"F0.wireOp",EDGE,"E114"),sQuery(id+"F0.wireOp",EDGE,"E115"),sQuery(id+"F0.wireOp",EDGE,"E116"),sQuery(id+"F0.wireOp",EDGE,"E117"),sQuery(id+"F0.wireOp",EDGE,"E118"),sQuery(id+"F0.wireOp",EDGE,"E119"),sQuery(id+"F0.wireOp",EDGE,"E120"),sQuery(id+"F0.wireOp",EDGE,"E121"),sQuery(id+"F0.wireOp",EDGE,"E122"),sQuery(id+"F0.wireOp",EDGE,"E123"),sQuery(id+"F0.wireOp",EDGE,"E124"),sQuery(id+"F0.wireOp",EDGE,"E125"),sQuery(id+"F0.wireOp",EDGE,"E126"),sQuery(id+"F0.wireOp",EDGE,"E127"),sQuery(id+"F0.wireOp",EDGE,"E128"),sQuery(id+"F0.wireOp",EDGE,"E129"),sQuery(id+"F0.wireOp",EDGE,"E130"),sQuery(id+"F0.wireOp",EDGE,"E131"),sQuery(id+"F0.wireOp",EDGE,"E132"),sQuery(id+"F0.wireOp",EDGE,"E133"),sQuery(id+"F0.wireOp",EDGE,"E134"),sQuery(id+"F0.wireOp",EDGE,"E135"),sQuery(id+"F0.wireOp",EDGE,"E136"),sQuery(id+"F0.wireOp",EDGE,"E137"),sQuery(id+"F0.wireOp",EDGE,"E138"),sQuery(id+"F0.wireOp",EDGE,"E139"),sQuery(id+"F0.wireOp",EDGE,"E140"),sQuery(id+"F0.wireOp",EDGE,"E141"),sQuery(id+"F0.wireOp",EDGE,"E142"),sQuery(id+"F0.wireOp",EDGE,"E143"),sQuery(id+"F0.wireOp",EDGE,"E144"),sQuery(id+"F0.wireOp",EDGE,"E145"),sQuery(id+"F0.wireOp",EDGE,"E146"),sQuery(id+"F0.wireOp",EDGE,"E147"),sQuery(id+"F0.wireOp",EDGE,"E148"),sQuery(id+"F0.wireOp",EDGE,"E149"),sQuery(id+"F0.wireOp",EDGE,"E150"),sQuery(id+"F0.wireOp",EDGE,"E151"),sQuery(id+"F0.wireOp",EDGE,"E152"),sQuery(id+"F0.wireOp",EDGE,"E177"),sQuery(id+"F0.wireOp",EDGE,"E178"),sQuery(id+"F0.wireOp",EDGE,"E179"),sQuery(id+"F0.wireOp",EDGE,"E180"),sQuery(id+"F0.wireOp",EDGE,"E181"),sQuery(id+"F0.wireOp",EDGE,"E182"),sQuery(id+"F0.wireOp",EDGE,"E183"),sQuery(id+"F0.wireOp",EDGE,"E184"),sQuery(id+"F0.wireOp",EDGE,"E185"),sQuery(id+"F0.wireOp",EDGE,"E186"),sQuery(id+"F0.wireOp",EDGE,"E187"),sQuery(id+"F0.wireOp",EDGE,"E188"),sQuery(id+"F0.wireOp",EDGE,"E189"),sQuery(id+"F0.wireOp",EDGE,"E190"),sQuery(id+"F0.wireOp",EDGE,"E191"),sQuery(id+"F0.wireOp",EDGE,"E192"),sQuery(id+"F0.wireOp",EDGE,"E193"),sQuery(id+"F0.wireOp",EDGE,"E194"),sQuery(id+"F0.wireOp",EDGE,"E195"),sQuery(id+"F0.wireOp",EDGE,"E196"),sQuery(id+"F0.wireOp",EDGE,"E197"),sQuery(id+"F0.wireOp",EDGE,"E198"),sQuery(id+"F0.wireOp",EDGE,"E199"),sQuery(id+"F0.wireOp",EDGE,"E200"),sQuery(id+"F0.wireOp",EDGE,"E201"),sQuery(id+"F0.wireOp",EDGE,"E202"),sQuery(id+"F0.wireOp",EDGE,"E203"),sQuery(id+"F0.wireOp",EDGE,"E203"),sQuery(id+"F0.wireOp",EDGE,"E204"),sQuery(id+"F0.wireOp",EDGE,"E205"),sQuery(id+"F0.wireOp",EDGE,"E205"),sQuery(id+"F0.wireOp",EDGE,"E206"),sQuery(id+"F0.wireOp",EDGE,"E207"),sQuery(id+"F0.wireOp",EDGE,"E207"),sQuery(id+"F0.wireOp",EDGE,"E208"),sQuery(id+"F0.wireOp",EDGE,"E209"),sQuery(id+"F0.wireOp",EDGE,"E210"),sQuery(id+"F0.wireOp",EDGE,"E210"),sQuery(id+"F0.wireOp",EDGE,"E210"),sQuery(id+"F0.wireOp",EDGE,"E211"),sQuery(id+"F0.wireOp",EDGE,"E212"),sQuery(id+"F0.wireOp",EDGE,"E212"),sQuery(id+"F0.wireOp",EDGE,"E213"),sQuery(id+"F0.wireOp",EDGE,"E214"),sQuery(id+"F0.wireOp",EDGE,"E215"),sQuery(id+"F0.wireOp",EDGE,"E216"),sQuery(id+"F0.wireOp",EDGE,"E216"),sQuery(id+"F0.wireOp",EDGE,"E216"),sQuery(id+"F0.wireOp",EDGE,"E216"),sQuery(id+"F0.wireOp",EDGE,"E216"),sQuery(id+"F0.wireOp",EDGE,"E217"),sQuery(id+"F0.wireOp",EDGE,"E218"),sQuery(id+"F0.wireOp",EDGE,"E218"),sQuery(id+"F0.wireOp",EDGE,"E219"),sQuery(id+"F0.wireOp",EDGE,"E220"),sQuery(id+"F0.wireOp",EDGE,"E220"),sQuery(id+"F0.wireOp",EDGE,"E221"),sQuery(id+"F0.wireOp",EDGE,"E222"),sQuery(id+"F0.wireOp",EDGE,"E223"),sQuery(id+"F0.wireOp",EDGE,"E224"),sQuery(id+"F0.wireOp",EDGE,"E225"),sQuery(id+"F0.wireOp",EDGE,"E226"),sQuery(id+"F0.wireOp",EDGE,"E227"),sQuery(id+"F0.wireOp",EDGE,"E228"),sQuery(id+"F0.wireOp",EDGE,"E229"),sQuery(id+"F0.wireOp",EDGE,"E230"),sQuery(id+"F0.wireOp",EDGE,"E230"),sQuery(id+"F0.wireOp",EDGE,"E230"),sQuery(id+"F0.wireOp",EDGE,"E230"),sQuery(id+"F0.wireOp",EDGE,"E230"),sQuery(id+"F0.wireOp",EDGE,"E231"),sQuery(id+"F0.wireOp",EDGE,"E232"),sQuery(id+"F0.wireOp",EDGE,"E233"),sQuery(id+"F0.wireOp",EDGE,"E234"),sQuery(id+"F0.wireOp",EDGE,"E235"),sQuery(id+"F0.wireOp",EDGE,"E235"),sQuery(id+"F0.wireOp",EDGE,"E236"),sQuery(id+"F0.wireOp",EDGE,"E237"),sQuery(id+"F0.wireOp",EDGE,"E237"),sQuery(id+"F0.wireOp",EDGE,"E238"),sQuery(id+"F0.wireOp",EDGE,"E239"),sQuery(id+"F0.wireOp",EDGE,"E240"),sQuery(id+"F0.wireOp",EDGE,"E241"),sQuery(id+"F0.wireOp",EDGE,"E242"),sQuery(id+"F0.wireOp",EDGE,"E243"),sQuery(id+"F0.wireOp",EDGE,"E243"),sQuery(id+"F0.wireOp",EDGE,"E244"),sQuery(id+"F0.wireOp",EDGE,"E245"),sQuery(id+"F0.wireOp",EDGE,"E245"),sQuery(id+"F0.wireOp",EDGE,"E246"),sQuery(id+"F0.wireOp",EDGE,"E247"),sQuery(id+"F0.wireOp",EDGE,"E247"),sQuery(id+"F0.wireOp",EDGE,"E248"),sQuery(id+"F0.wireOp",EDGE,"E249"),sQuery(id+"F0.wireOp",EDGE,"E249"),sQuery(id+"F0.wireOp",EDGE,"E250"),sQuery(id+"F0.wireOp",EDGE,"E251"),sQuery(id+"F0.wireOp",EDGE,"E252"),sQuery(id+"F0.wireOp",EDGE,"E252"),sQuery(id+"F0.wireOp",EDGE,"E253"),sQuery(id+"F0.wireOp",EDGE,"E254"),sQuery(id+"F0.wireOp",EDGE,"E255"),sQuery(id+"F0.wireOp",EDGE,"E256"),sQuery(id+"F0.wireOp",EDGE,"E257"),sQuery(id+"F0.wireOp",EDGE,"E258"),sQuery(id+"F0.wireOp",EDGE,"E259"),sQuery(id+"F0.wireOp",EDGE,"E260"),sQuery(id+"F0.wireOp",EDGE,"E201"),sQuery(id+"F0.wireOp",EDGE,"E261"),sQuery(id+"F0.wireOp",EDGE,"E262"),sQuery(id+"F0.wireOp",EDGE,"E262"),sQuery(id+"F0.wireOp",EDGE,"E262"),sQuery(id+"F0.wireOp",EDGE,"E262"),sQuery(id+"F0.wireOp",EDGE,"E263"),sQuery(id+"F0.wireOp",EDGE,"E264"),sQuery(id+"F0.wireOp",EDGE,"E264"),sQuery(id+"F0.wireOp",EDGE,"E265"),sQuery(id+"F0.wireOp",EDGE,"E266"),sQuery(id+"F0.wireOp",EDGE,"E267"),sQuery(id+"F0.wireOp",EDGE,"E268"),sQuery(id+"F0.wireOp",EDGE,"E269"),sQuery(id+"F0.wireOp",EDGE,"E270"),sQuery(id+"F0.wireOp",EDGE,"E271"),sQuery(id+"F0.wireOp",EDGE,"E271"),sQuery(id+"F0.wireOp",EDGE,"E272"),sQuery(id+"F0.wireOp",EDGE,"E273"),sQuery(id+"F0.wireOp",EDGE,"E274"),sQuery(id+"F0.wireOp",EDGE,"E275"),sQuery(id+"F0.wireOp",EDGE,"E275"),sQuery(id+"F0.wireOp",EDGE,"E276"),sQuery(id+"F0.wireOp",EDGE,"E277"),sQuery(id+"F0.wireOp",EDGE,"E278"),sQuery(id+"F0.wireOp",EDGE,"E279"),sQuery(id+"F0.wireOp",EDGE,"E280"),sQuery(id+"F0.wireOp",EDGE,"E281"),sQuery(id+"F0.wireOp",EDGE,"E282"),sQuery(id+"F0.wireOp",EDGE,"E283"),sQuery(id+"F0.wireOp",EDGE,"E284"),sQuery(id+"F0.wireOp",EDGE,"E285"),sQuery(id+"F0.wireOp",EDGE,"E286"),sQuery(id+"F0.wireOp",EDGE,"E286"),sQuery(id+"F0.wireOp",EDGE,"E286"),sQuery(id+"F0.wireOp",EDGE,"E286"),sQuery(id+"F0.wireOp",EDGE,"E287"),sQuery(id+"F0.wireOp",EDGE,"E288"),sQuery(id+"F0.wireOp",EDGE,"E288"),sQuery(id+"F0.wireOp",EDGE,"E289"),sQuery(id+"F0.wireOp",EDGE,"E290"),sQuery(id+"F0.wireOp",EDGE,"E290"),sQuery(id+"F0.wireOp",EDGE,"E291"),sQuery(id+"F0.wireOp",EDGE,"E292"),sQuery(id+"F0.wireOp",EDGE,"E293"),sQuery(id+"F0.wireOp",EDGE,"E294"),sQuery(id+"F0.wireOp",EDGE,"E294"),sQuery(id+"F0.wireOp",EDGE,"E295"),sQuery(id+"F0.wireOp",EDGE,"E296"),sQuery(id+"F0.wireOp",EDGE,"E297"),sQuery(id+"F0.wireOp",EDGE,"E298"),sQuery(id+"F0.wireOp",EDGE,"E298"),sQuery(id+"F0.wireOp",EDGE,"E298"),sQuery(id+"F0.wireOp",EDGE,"E298"),sQuery(id+"F0.wireOp",EDGE,"E299"),sQuery(id+"F0.wireOp",EDGE,"E300"),sQuery(id+"F0.wireOp",EDGE,"E301"),sQuery(id+"F0.wireOp",EDGE,"E302"),sQuery(id+"F0.wireOp",EDGE,"E303"),sQuery(id+"F0.wireOp",EDGE,"E303"),sQuery(id+"F0.wireOp",EDGE,"E304"),sQuery(id+"F0.wireOp",EDGE,"E305"),sQuery(id+"F0.wireOp",EDGE,"E305"),sQuery(id+"F0.wireOp",EDGE,"E306"),sQuery(id+"F0.wireOp",EDGE,"E307"),sQuery(id+"F0.wireOp",EDGE,"E308"),sQuery(id+"F0.wireOp",EDGE,"E309"),sQuery(id+"F0.wireOp",EDGE,"E310"),sQuery(id+"F0.wireOp",EDGE,"E311"),sQuery(id+"F0.wireOp",EDGE,"E312"),sQuery(id+"F0.wireOp",EDGE,"E312"),sQuery(id+"F0.wireOp",EDGE,"E313"),sQuery(id+"F0.wireOp",EDGE,"E314"),sQuery(id+"F0.wireOp",EDGE,"E314"),sQuery(id+"F0.wireOp",EDGE,"E315"),sQuery(id+"F0.wireOp",EDGE,"E316"),sQuery(id+"F0.wireOp",EDGE,"E316"),sQuery(id+"F0.wireOp",EDGE,"E317"),sQuery(id+"F0.wireOp",EDGE,"E318"),sQuery(id+"F0.wireOp",EDGE,"E319"),sQuery(id+"F0.wireOp",EDGE,"E319"),sQuery(id+"F0.wireOp",EDGE,"E319"),sQuery(id+"F0.wireOp",EDGE,"E320"),sQuery(id+"F0.wireOp",EDGE,"E321"),sQuery(id+"F0.wireOp",EDGE,"E321"),sQuery(id+"F0.wireOp",EDGE,"E322"),sQuery(id+"F0.wireOp",EDGE,"E323"),sQuery(id+"F0.wireOp",EDGE,"E324"),sQuery(id+"F0.wireOp",EDGE,"E325"),sQuery(id+"F0.wireOp",EDGE,"E326"),sQuery(id+"F0.wireOp",EDGE,"E327"),sQuery(id+"F0.wireOp",EDGE,"E328"),sQuery(id+"F0.wireOp",EDGE,"E328"),sQuery(id+"F0.wireOp",EDGE,"E329"),sQuery(id+"F0.wireOp",EDGE,"E330"),sQuery(id+"F0.wireOp",EDGE,"E331"),sQuery(id+"F0.wireOp",EDGE,"E332"),sQuery(id+"F0.wireOp",EDGE,"E333"),sQuery(id+"F0.wireOp",EDGE,"E333"),sQuery(id+"F0.wireOp",EDGE,"E334"),sQuery(id+"F0.wireOp",EDGE,"E335"),sQuery(id+"F0.wireOp",EDGE,"E335"),sQuery(id+"F0.wireOp",EDGE,"E336"),sQuery(id+"F0.wireOp",EDGE,"E337"),sQuery(id+"F0.wireOp",EDGE,"E337"),sQuery(id+"F0.wireOp",EDGE,"E338"),sQuery(id+"F0.wireOp",EDGE,"E339"),sQuery(id+"F0.wireOp",EDGE,"E340"),sQuery(id+"F0.wireOp",EDGE,"E341"),sQuery(id+"F0.wireOp",EDGE,"E342"),sQuery(id+"F0.wireOp",EDGE,"E343"),sQuery(id+"F0.wireOp",EDGE,"E344"),sQuery(id+"F0.wireOp",EDGE,"E345"),sQuery(id+"F0.wireOp",EDGE,"E346"),sQuery(id+"F0.wireOp",EDGE,"E347"),sQuery(id+"F0.wireOp",EDGE,"E348"),sQuery(id+"F0.wireOp",EDGE,"E348"),sQuery(id+"F0.wireOp",EDGE,"E349"),sQuery(id+"F0.wireOp",EDGE,"E350"),sQuery(id+"F0.wireOp",EDGE,"E351"),sQuery(id+"F0.wireOp",EDGE,"E352"),sQuery(id+"F0.wireOp",EDGE,"E352"),sQuery(id+"F0.wireOp",EDGE,"E352"),sQuery(id+"F0.wireOp",EDGE,"E352"),sQuery(id+"F0.wireOp",EDGE,"E353"),sQuery(id+"F0.wireOp",EDGE,"E354"),sQuery(id+"F0.wireOp",EDGE,"E355"),sQuery(id+"F0.wireOp",EDGE,"E356"),sQuery(id+"F0.wireOp",EDGE,"E357"),sQuery(id+"F0.wireOp",EDGE,"E358"),sQuery(id+"F0.wireOp",EDGE,"E359"),sQuery(id+"F0.wireOp",EDGE,"E360"),sQuery(id+"F0.wireOp",EDGE,"E360"),sQuery(id+"F0.wireOp",EDGE,"E360"),sQuery(id+"F0.wireOp",EDGE,"E360"),sQuery(id+"F0.wireOp",EDGE,"E360"),sQuery(id+"F0.wireOp",EDGE,"E360"),sQuery(id+"F0.wireOp",EDGE,"E360"),sQuery(id+"F0.wireOp",EDGE,"E360"),sQuery(id+"F0.wireOp",EDGE,"E361"),sQuery(id+"F0.wireOp",EDGE,"E362"),sQuery(id+"F0.wireOp",EDGE,"E363"),sQuery(id+"F0.wireOp",EDGE,"E364"),sQuery(id+"F0.wireOp",EDGE,"E365"),sQuery(id+"F0.wireOp",EDGE,"E365"),sQuery(id+"F0.wireOp",EDGE,"E365"),sQuery(id+"F0.wireOp",EDGE,"E366"),sQuery(id+"F0.wireOp",EDGE,"E367"),sQuery(id+"F0.wireOp",EDGE,"E367"),sQuery(id+"F0.wireOp",EDGE,"E368"),sQuery(id+"F0.wireOp",EDGE,"E369"),sQuery(id+"F0.wireOp",EDGE,"E370"),sQuery(id+"F0.wireOp",EDGE,"E371"),sQuery(id+"F0.wireOp",EDGE,"E371"),sQuery(id+"F0.wireOp",EDGE,"E372"),sQuery(id+"F0.wireOp",EDGE,"E373"),sQuery(id+"F0.wireOp",EDGE,"E373"),sQuery(id+"F0.wireOp",EDGE,"E374"),sQuery(id+"F0.wireOp",EDGE,"E375"),sQuery(id+"F0.wireOp",EDGE,"E375"),sQuery(id+"F0.wireOp",EDGE,"E376"),sQuery(id+"F0.wireOp",EDGE,"E377"),sQuery(id+"F0.wireOp",EDGE,"E378"),sQuery(id+"F0.wireOp",EDGE,"E379"),sQuery(id+"F0.wireOp",EDGE,"E380"),sQuery(id+"F0.wireOp",EDGE,"E381"),sQuery(id+"F0.wireOp",EDGE,"E382"),sQuery(id+"F0.wireOp",EDGE,"E383"),sQuery(id+"F0.wireOp",EDGE,"E384"),sQuery(id+"F0.wireOp",EDGE,"E385"),sQuery(id+"F0.wireOp",EDGE,"E386"),sQuery(id+"F0.wireOp",EDGE,"E386"),sQuery(id+"F0.wireOp",EDGE,"E387"),sQuery(id+"F0.wireOp",EDGE,"E388"),sQuery(id+"F0.wireOp",EDGE,"E389"),sQuery(id+"F0.wireOp",EDGE,"E390"),sQuery(id+"F0.wireOp",EDGE,"E391"),sQuery(id+"F0.wireOp",EDGE,"E391"),sQuery(id+"F0.wireOp",EDGE,"E392"),sQuery(id+"F0.wireOp",EDGE,"E393"),sQuery(id+"F0.wireOp",EDGE,"E393"),sQuery(id+"F0.wireOp",EDGE,"E394"),sQuery(id+"F0.wireOp",EDGE,"E395"),sQuery(id+"F0.wireOp",EDGE,"E396"),sQuery(id+"F0.wireOp",EDGE,"E397"),sQuery(id+"F0.wireOp",EDGE,"E398"),sQuery(id+"F0.wireOp",EDGE,"E399"),sQuery(id+"F0.wireOp",EDGE,"E399"),sQuery(id+"F0.wireOp",EDGE,"E399"),sQuery(id+"F0.wireOp",EDGE,"E400"),sQuery(id+"F0.wireOp",EDGE,"E401"),sQuery(id+"F0.wireOp",EDGE,"E401"),sQuery(id+"F0.wireOp",EDGE,"E402"),sQuery(id+"F0.wireOp",EDGE,"E403"),sQuery(id+"F0.wireOp",EDGE,"E403"),sQuery(id+"F0.wireOp",EDGE,"E403"),sQuery(id+"F0.wireOp",EDGE,"E403"),sQuery(id+"F0.wireOp",EDGE,"E403"),sQuery(id+"F0.wireOp",EDGE,"E404"),sQuery(id+"F0.wireOp",EDGE,"E405"),sQuery(id+"F0.wireOp",EDGE,"E406"),sQuery(id+"F0.wireOp",EDGE,"E407"),sQuery(id+"F0.wireOp",EDGE,"E408"),sQuery(id+"F0.wireOp",EDGE,"E409"),sQuery(id+"F0.wireOp",EDGE,"E410"),sQuery(id+"F0.wireOp",EDGE,"E411"),sQuery(id+"F0.wireOp",EDGE,"E412"),sQuery(id+"F0.wireOp",EDGE,"E413"),sQuery(id+"F0.wireOp",EDGE,"E413"),sQuery(id+"F0.wireOp",EDGE,"E413"),sQuery(id+"F0.wireOp",EDGE,"E413"),sQuery(id+"F0.wireOp",EDGE,"E413"),sQuery(id+"F0.wireOp",EDGE,"E414"),sQuery(id+"F0.wireOp",EDGE,"E415"),sQuery(id+"F0.wireOp",EDGE,"E416"),sQuery(id+"F0.wireOp",EDGE,"E417"),sQuery(id+"F0.wireOp",EDGE,"E418"),sQuery(id+"F0.wireOp",EDGE,"E419"),sQuery(id+"F0.wireOp",EDGE,"E420"),sQuery(id+"F0.wireOp",EDGE,"E421"),sQuery(id+"F0.wireOp",EDGE,"E421"),sQuery(id+"F0.wireOp",EDGE,"E422"),sQuery(id+"F0.wireOp",EDGE,"E423"),sQuery(id+"F0.wireOp",EDGE,"E423"),sQuery(id+"F0.wireOp",EDGE,"E423"),sQuery(id+"F0.wireOp",EDGE,"E423"),sQuery(id+"F0.wireOp",EDGE,"E423"),sQuery(id+"F0.wireOp",EDGE,"E424"),sQuery(id+"F0.wireOp",EDGE,"E425"),sQuery(id+"F0.wireOp",EDGE,"E426"),sQuery(id+"F0.wireOp",EDGE,"E427"),sQuery(id+"F0.wireOp",EDGE,"E428"),sQuery(id+"F0.wireOp",EDGE,"E429"),sQuery(id+"F0.wireOp",EDGE,"E429"),sQuery(id+"F0.wireOp",EDGE,"E430"),sQuery(id+"F0.wireOp",EDGE,"E431"),sQuery(id+"F0.wireOp",EDGE,"E432"),sQuery(id+"F0.wireOp",EDGE,"E432"),sQuery(id+"F0.wireOp",EDGE,"E432"),sQuery(id+"F0.wireOp",EDGE,"E432"),sQuery(id+"F0.wireOp",EDGE,"E432"),sQuery(id+"F0.wireOp",EDGE,"E433"),sQuery(id+"F0.wireOp",EDGE,"E434"),sQuery(id+"F0.wireOp",EDGE,"E434"),sQuery(id+"F0.wireOp",EDGE,"E435"),sQuery(id+"F0.wireOp",EDGE,"E436"),sQuery(id+"F0.wireOp",EDGE,"E437"),sQuery(id+"F0.wireOp",EDGE,"E438"),sQuery(id+"F0.wireOp",EDGE,"E439"),sQuery(id+"F0.wireOp",EDGE,"E464"),sQuery(id+"F0.wireOp",EDGE,"E465"),sQuery(id+"F0.wireOp",EDGE,"E466"),sQuery(id+"F0.wireOp",EDGE,"E467"),sQuery(id+"F0.wireOp",EDGE,"E468"),sQuery(id+"F0.wireOp",EDGE,"E469"),sQuery(id+"F0.wireOp",EDGE,"E470"),sQuery(id+"F0.wireOp",EDGE,"E471"),sQuery(id+"F0.wireOp",EDGE,"E472"),sQuery(id+"F0.wireOp",EDGE,"E473"),sQuery(id+"F0.wireOp",EDGE,"E474"),sQuery(id+"F0.wireOp",EDGE,"E475"),sQuery(id+"F0.wireOp",EDGE,"E476"),sQuery(id+"F0.wireOp",EDGE,"E477"),sQuery(id+"F0.wireOp",EDGE,"E478"),sQuery(id+"F0.wireOp",EDGE,"E479"),sQuery(id+"F0.wireOp",EDGE,"E480"),sQuery(id+"F0.wireOp",EDGE,"E481"),sQuery(id+"F0.wireOp",EDGE,"E482"),sQuery(id+"F0.wireOp",EDGE,"E483"),sQuery(id+"F0.wireOp",EDGE,"E484"),sQuery(id+"F0.wireOp",EDGE,"E485"),sQuery(id+"F0.wireOp",EDGE,"E486"),sQuery(id+"F0.wireOp",EDGE,"E487"),sQuery(id+"F0.wireOp",EDGE,"E488"),sQuery(id+"F0.wireOp",EDGE,"E489"),sQuery(id+"F0.wireOp",EDGE,"E490"),sQuery(id+"F0.wireOp",EDGE,"E491"),sQuery(id+"F0.wireOp",EDGE,"E492"),sQuery(id+"F0.wireOp",EDGE,"E493"),sQuery(id+"F0.wireOp",EDGE,"E493"),sQuery(id+"F0.wireOp",EDGE,"E494"),sQuery(id+"F0.wireOp",EDGE,"E495"),sQuery(id+"F0.wireOp",EDGE,"E496"),sQuery(id+"F0.wireOp",EDGE,"E497"),sQuery(id+"F0.wireOp",EDGE,"E498"),sQuery(id+"F0.wireOp",EDGE,"E499"),sQuery(id+"F0.wireOp",EDGE,"E500"),sQuery(id+"F0.wireOp",EDGE,"E501"),sQuery(id+"F0.wireOp",EDGE,"E502"),sQuery(id+"F0.wireOp",EDGE,"E502"),sQuery(id+"F0.wireOp",EDGE,"E502"),sQuery(id+"F0.wireOp",EDGE,"E503"),sQuery(id+"F0.wireOp",EDGE,"E504"),sQuery(id+"F0.wireOp",EDGE,"E504"),sQuery(id+"F0.wireOp",EDGE,"E504"),sQuery(id+"F0.wireOp",EDGE,"E504"),sQuery(id+"F0.wireOp",EDGE,"E505"),sQuery(id+"F0.wireOp",EDGE,"E506"),sQuery(id+"F0.wireOp",EDGE,"E506"),sQuery(id+"F0.wireOp",EDGE,"E507"),sQuery(id+"F0.wireOp",EDGE,"E508"),sQuery(id+"F0.wireOp",EDGE,"E508"),sQuery(id+"F0.wireOp",EDGE,"E509"),sQuery(id+"F0.wireOp",EDGE,"E510"),sQuery(id+"F0.wireOp",EDGE,"E510"),sQuery(id+"F0.wireOp",EDGE,"E510"),sQuery(id+"F0.wireOp",EDGE,"E511"),sQuery(id+"F0.wireOp",EDGE,"E512"),sQuery(id+"F0.wireOp",EDGE,"E512"),sQuery(id+"F0.wireOp",EDGE,"E512"),sQuery(id+"F0.wireOp",EDGE,"E512"),sQuery(id+"F0.wireOp",EDGE,"E512"),sQuery(id+"F0.wireOp",EDGE,"E513"),sQuery(id+"F0.wireOp",EDGE,"E514"),sQuery(id+"F0.wireOp",EDGE,"E515"),sQuery(id+"F0.wireOp",EDGE,"E516"),sQuery(id+"F0.wireOp",EDGE,"E517"),sQuery(id+"F0.wireOp",EDGE,"E518"),sQuery(id+"F0.wireOp",EDGE,"E518"),sQuery(id+"F0.wireOp",EDGE,"E518"),sQuery(id+"F0.wireOp",EDGE,"E518"),sQuery(id+"F0.wireOp",EDGE,"E519"),sQuery(id+"F0.wireOp",EDGE,"E520"),sQuery(id+"F0.wireOp",EDGE,"E520"),sQuery(id+"F0.wireOp",EDGE,"E521"),sQuery(id+"F0.wireOp",EDGE,"E522"),sQuery(id+"F0.wireOp",EDGE,"E523"),sQuery(id+"F0.wireOp",EDGE,"E524"),sQuery(id+"F0.wireOp",EDGE,"E525"),sQuery(id+"F0.wireOp",EDGE,"E525"),sQuery(id+"F0.wireOp",EDGE,"E526"),sQuery(id+"F0.wireOp",EDGE,"E527"),sQuery(id+"F0.wireOp",EDGE,"E528"),sQuery(id+"F0.wireOp",EDGE,"E529"),sQuery(id+"F0.wireOp",EDGE,"E530"),sQuery(id+"F0.wireOp",EDGE,"E531"),sQuery(id+"F0.wireOp",EDGE,"E531"),sQuery(id+"F0.wireOp",EDGE,"E531"),sQuery(id+"F0.wireOp",EDGE,"E531"),sQuery(id+"F0.wireOp",EDGE,"E531"),sQuery(id+"F0.wireOp",EDGE,"E532"),sQuery(id+"F0.wireOp",EDGE,"E533"),sQuery(id+"F0.wireOp",EDGE,"E534"),sQuery(id+"F0.wireOp",EDGE,"E535"),sQuery(id+"F0.wireOp",EDGE,"E536"),sQuery(id+"F0.wireOp",EDGE,"E536"),sQuery(id+"F0.wireOp",EDGE,"E537"),sQuery(id+"F0.wireOp",EDGE,"E538"),sQuery(id+"F0.wireOp",EDGE,"E539"),sQuery(id+"F0.wireOp",EDGE,"E562"),sQuery(id+"F0.wireOp",EDGE,"E563"),sQuery(id+"F0.wireOp",EDGE,"E564"),sQuery(id+"F0.wireOp",EDGE,"E565"),sQuery(id+"F0.wireOp",EDGE,"E566"),sQuery(id+"F0.wireOp",EDGE,"E567"),sQuery(id+"F0.wireOp",EDGE,"E568"),sQuery(id+"F0.wireOp",EDGE,"E569"),sQuery(id+"F0.wireOp",EDGE,"E570"),sQuery(id+"F0.wireOp",EDGE,"E571"),sQuery(id+"F0.wireOp",EDGE,"E572"),sQuery(id+"F0.wireOp",EDGE,"E573"),sQuery(id+"F0.wireOp",EDGE,"E574"),sQuery(id+"F0.wireOp",EDGE,"E575"),sQuery(id+"F0.wireOp",EDGE,"E576"),sQuery(id+"F0.wireOp",EDGE,"E577"),sQuery(id+"F0.wireOp",EDGE,"E578"),sQuery(id+"F0.wireOp",EDGE,"E579"),sQuery(id+"F0.wireOp",EDGE,"E580"),sQuery(id+"F0.wireOp",EDGE,"E581"),sQuery(id+"F0.wireOp",EDGE,"E582"),sQuery(id+"F0.wireOp",EDGE,"E583"),sQuery(id+"F0.wireOp",EDGE,"E584"),sQuery(id+"F0.wireOp",EDGE,"E585"),sQuery(id+"F0.wireOp",EDGE,"E586"),sQuery(id+"F0.wireOp",EDGE,"E587"),sQuery(id+"F0.wireOp",EDGE,"E588"),sQuery(id+"F0.wireOp",EDGE,"E589"),sQuery(id+"F0.wireOp",EDGE,"E590"),sQuery(id+"F0.wireOp",EDGE,"E591"),sQuery(id+"F0.wireOp",EDGE,"E591"),sQuery(id+"F0.wireOp",EDGE,"E592"),sQuery(id+"F0.wireOp",EDGE,"E593"),sQuery(id+"F0.wireOp",EDGE,"E594"),sQuery(id+"F0.wireOp",EDGE,"E595"),sQuery(id+"F0.wireOp",EDGE,"E596"),sQuery(id+"F0.wireOp",EDGE,"E597"),sQuery(id+"F0.wireOp",EDGE,"E598"),sQuery(id+"F0.wireOp",EDGE,"E598"),sQuery(id+"F0.wireOp",EDGE,"E598"),sQuery(id+"F0.wireOp",EDGE,"E599"),sQuery(id+"F0.wireOp",EDGE,"E600"),sQuery(id+"F0.wireOp",EDGE,"E601"),sQuery(id+"F0.wireOp",EDGE,"E602"),sQuery(id+"F0.wireOp",EDGE,"E603"),sQuery(id+"F0.wireOp",EDGE,"E603"),sQuery(id+"F0.wireOp",EDGE,"E603"),sQuery(id+"F0.wireOp",EDGE,"E603"),sQuery(id+"F0.wireOp",EDGE,"E604"),sQuery(id+"F0.wireOp",EDGE,"E605"),sQuery(id+"F0.wireOp",EDGE,"E605"),sQuery(id+"F0.wireOp",EDGE,"E605"),sQuery(id+"F0.wireOp",EDGE,"E606"),sQuery(id+"F0.wireOp",EDGE,"E607"),sQuery(id+"F0.wireOp",EDGE,"E608"),sQuery(id+"F0.wireOp",EDGE,"E609"),sQuery(id+"F0.wireOp",EDGE,"E610"),sQuery(id+"F0.wireOp",EDGE,"E611"),sQuery(id+"F0.wireOp",EDGE,"E612"),sQuery(id+"F0.wireOp",EDGE,"E612"),sQuery(id+"F0.wireOp",EDGE,"E612"),sQuery(id+"F0.wireOp",EDGE,"E612"),sQuery(id+"F0.wireOp",EDGE,"E613"),sQuery(id+"F0.wireOp",EDGE,"E614"),sQuery(id+"F0.wireOp",EDGE,"E614"),sQuery(id+"F0.wireOp",EDGE,"E615"),sQuery(id+"F0.wireOp",EDGE,"E616"),sQuery(id+"F0.wireOp",EDGE,"E616"),sQuery(id+"F0.wireOp",EDGE,"E616"),sQuery(id+"F0.wireOp",EDGE,"E616"),sQuery(id+"F0.wireOp",EDGE,"E617"),sQuery(id+"F0.wireOp",EDGE,"E618"),sQuery(id+"F0.wireOp",EDGE,"E619"),sQuery(id+"F0.wireOp",EDGE,"E619"),sQuery(id+"F0.wireOp",EDGE,"E619"),sQuery(id+"F0.wireOp",EDGE,"E619"),sQuery(id+"F0.wireOp",EDGE,"E620"),sQuery(id+"F0.wireOp",EDGE,"E621"),sQuery(id+"F0.wireOp",EDGE,"E621"),sQuery(id+"F0.wireOp",EDGE,"E622"),sQuery(id+"F0.wireOp",EDGE,"E623"),sQuery(id+"F0.wireOp",EDGE,"E623"),sQuery(id+"F0.wireOp",EDGE,"E623"),sQuery(id+"F0.wireOp",EDGE,"E623"),sQuery(id+"F0.wireOp",EDGE,"E624"),sQuery(id+"F0.wireOp",EDGE,"E625"),sQuery(id+"F0.wireOp",EDGE,"E626"),sQuery(id+"F0.wireOp",EDGE,"E627"),sQuery(id+"F0.wireOp",EDGE,"E628"),sQuery(id+"F0.wireOp",EDGE,"E628"),sQuery(id+"F0.wireOp",EDGE,"E629"),sQuery(id+"F0.wireOp",EDGE,"E630"),sQuery(id+"F0.wireOp",EDGE,"E631"),sQuery(id+"F0.wireOp",EDGE,"E632"),sQuery(id+"F0.wireOp",EDGE,"E633"),sQuery(id+"F0.wireOp",EDGE,"E633"),sQuery(id+"F0.wireOp",EDGE,"E634"),sQuery(id+"F0.wireOp",EDGE,"E635"),sQuery(id+"F0.wireOp",EDGE,"E635"),sQuery(id+"F0.wireOp",EDGE,"E636"),sQuery(id+"F0.wireOp",EDGE,"E637"),sQuery(id+"F0.wireOp",EDGE,"E637"),sQuery(id+"F0.wireOp",EDGE,"E637"),sQuery(id+"F0.wireOp",EDGE,"E637"),sQuery(id+"F0.wireOp",EDGE,"E637"),sQuery(id+"F0.wireOp",EDGE,"E638"),sQuery(id+"F0.wireOp",EDGE,"E639"),sQuery(id+"F0.wireOp",EDGE,"E639"),sQuery(id+"F0.wireOp",EDGE,"E640"),sQuery(id+"F0.wireOp",EDGE,"E641"),sQuery(id+"F0.wireOp",EDGE,"E642"),sQuery(id+"F0.wireOp",EDGE,"E643"),sQuery(id+"F0.wireOp",EDGE,"E644"),sQuery(id+"F0.wireOp",EDGE,"E644"),sQuery(id+"F0.wireOp",EDGE,"E645"),sQuery(id+"F0.wireOp",EDGE,"E646"),sQuery(id+"F0.wireOp",EDGE,"E647"),sQuery(id+"F0.wireOp",EDGE,"E648"),sQuery(id+"F0.wireOp",EDGE,"E649"),sQuery(id+"F0.wireOp",EDGE,"E650"),sQuery(id+"F0.wireOp",EDGE,"E651"),sQuery(id+"F0.wireOp",EDGE,"E652"),sQuery(id+"F0.wireOp",EDGE,"E653"),sQuery(id+"F0.wireOp",EDGE,"E654"),sQuery(id+"F0.wireOp",EDGE,"E655"),sQuery(id+"F0.wireOp",EDGE,"E656"),sQuery(id+"F0.wireOp",EDGE,"E657"),sQuery(id+"F0.wireOp",EDGE,"E658"),sQuery(id+"F0.wireOp",EDGE,"E659"),sQuery(id+"F0.wireOp",EDGE,"E660"),sQuery(id+"F0.wireOp",EDGE,"E660"),sQuery(id+"F0.wireOp",EDGE,"E661"),sQuery(id+"F0.wireOp",EDGE,"E662"),sQuery(id+"F0.wireOp",EDGE,"E662"),sQuery(id+"F0.wireOp",EDGE,"E663"),sQuery(id+"F0.wireOp",EDGE,"E664"),sQuery(id+"F0.wireOp",EDGE,"E665"),sQuery(id+"F0.wireOp",EDGE,"E666"),sQuery(id+"F0.wireOp",EDGE,"E667"),sQuery(id+"F0.wireOp",EDGE,"E668"),sQuery(id+"F0.wireOp",EDGE,"E669"),sQuery(id+"F0.wireOp",EDGE,"E669"),sQuery(id+"F0.wireOp",EDGE,"E670"),sQuery(id+"F0.wireOp",EDGE,"E671"),sQuery(id+"F0.wireOp",EDGE,"E672"),sQuery(id+"F0.wireOp",EDGE,"E673"),sQuery(id+"F0.wireOp",EDGE,"E674"),sQuery(id+"F0.wireOp",EDGE,"E674"),sQuery(id+"F0.wireOp",EDGE,"E675"),sQuery(id+"F0.wireOp",EDGE,"E676"),sQuery(id+"F0.wireOp",EDGE,"E676"),sQuery(id+"F0.wireOp",EDGE,"E677"),sQuery(id+"F0.wireOp",EDGE,"E678"),sQuery(id+"F0.wireOp",EDGE,"E678"),sQuery(id+"F0.wireOp",EDGE,"E679"),sQuery(id+"F0.wireOp",EDGE,"E680"),sQuery(id+"F0.wireOp",EDGE,"E681"),sQuery(id+"F0.wireOp",EDGE,"E682"),sQuery(id+"F0.wireOp",EDGE,"E683"),sQuery(id+"F0.wireOp",EDGE,"E683"),sQuery(id+"F0.wireOp",EDGE,"E684"),sQuery(id+"F0.wireOp",EDGE,"E685"),sQuery(id+"F0.wireOp",EDGE,"E686"),sQuery(id+"F0.wireOp",EDGE,"E687"),sQuery(id+"F0.wireOp",EDGE,"E688"),sQuery(id+"F0.wireOp",EDGE,"E689"),sQuery(id+"F0.wireOp",EDGE,"E690"),sQuery(id+"F0.wireOp",EDGE,"E691"),sQuery(id+"F0.wireOp",EDGE,"E692"),sQuery(id+"F0.wireOp",EDGE,"E692"),sQuery(id+"F0.wireOp",EDGE,"E693"),sQuery(id+"F0.wireOp",EDGE,"E694"),sQuery(id+"F0.wireOp",EDGE,"E694"),sQuery(id+"F0.wireOp",EDGE,"E695"),sQuery(id+"F0.wireOp",EDGE,"E696"),sQuery(id+"F0.wireOp",EDGE,"E697"),sQuery(id+"F0.wireOp",EDGE,"E697"),sQuery(id+"F0.wireOp",EDGE,"E698"),sQuery(id+"F0.wireOp",EDGE,"E699"),sQuery(id+"F0.wireOp",EDGE,"E700"),sQuery(id+"F0.wireOp",EDGE,"E700"),sQuery(id+"F0.wireOp",EDGE,"E701"),sQuery(id+"F0.wireOp",EDGE,"E702"),sQuery(id+"F0.wireOp",EDGE,"E703"),sQuery(id+"F0.wireOp",EDGE,"E704"),sQuery(id+"F0.wireOp",EDGE,"E705"),sQuery(id+"F0.wireOp",EDGE,"E706"),sQuery(id+"F0.wireOp",EDGE,"E707"),sQuery(id+"F0.wireOp",EDGE,"E631"),sQuery(id+"F0.wireOp",EDGE,"E708"),sQuery(id+"F0.wireOp",EDGE,"E709"),sQuery(id+"F0.wireOp",EDGE,"E710"),sQuery(id+"F0.wireOp",EDGE,"E710"),sQuery(id+"F0.wireOp",EDGE,"E711"),sQuery(id+"F0.wireOp",EDGE,"E712"),sQuery(id+"F0.wireOp",EDGE,"E712"),sQuery(id+"F0.wireOp",EDGE,"E713"),sQuery(id+"F0.wireOp",EDGE,"E714"),sQuery(id+"F0.wireOp",EDGE,"E714"),sQuery(id+"F0.wireOp",EDGE,"E715"),sQuery(id+"F0.wireOp",EDGE,"E716"),sQuery(id+"F0.wireOp",EDGE,"E716"),sQuery(id+"F0.wireOp",EDGE,"E717"),sQuery(id+"F0.wireOp",EDGE,"E718"),sQuery(id+"F0.wireOp",EDGE,"E718"),sQuery(id+"F0.wireOp",EDGE,"E719"),sQuery(id+"F0.wireOp",EDGE,"E720"),sQuery(id+"F0.wireOp",EDGE,"E721"),sQuery(id+"F0.wireOp",EDGE,"E722"),sQuery(id+"F0.wireOp",EDGE,"E723"),sQuery(id+"F0.wireOp",EDGE,"E724"),sQuery(id+"F0.wireOp",EDGE,"E725"),sQuery(id+"F0.wireOp",EDGE,"E726"),sQuery(id+"F0.wireOp",EDGE,"E727"),sQuery(id+"F0.wireOp",EDGE,"E728"),sQuery(id+"F0.wireOp",EDGE,"E728"),sQuery(id+"F0.wireOp",EDGE,"E729"),sQuery(id+"F0.wireOp",EDGE,"E730"),sQuery(id+"F0.wireOp",EDGE,"E731"),sQuery(id+"F0.wireOp",EDGE,"E732"),sQuery(id+"F0.wireOp",EDGE,"E733"),sQuery(id+"F0.wireOp",EDGE,"E734"),sQuery(id+"F0.wireOp",EDGE,"E734"),sQuery(id+"F0.wireOp",EDGE,"E735"),sQuery(id+"F0.wireOp",EDGE,"E736"),sQuery(id+"F0.wireOp",EDGE,"E737"),sQuery(id+"F0.wireOp",EDGE,"E737"),sQuery(id+"F0.wireOp",EDGE,"E738"),sQuery(id+"F0.wireOp",EDGE,"E739"),sQuery(id+"F0.wireOp",EDGE,"E739"),sQuery(id+"F0.wireOp",EDGE,"E739"),sQuery(id+"F0.wireOp",EDGE,"E740"),sQuery(id+"F0.wireOp",EDGE,"E741"),sQuery(id+"F0.wireOp",EDGE,"E742"),sQuery(id+"F0.wireOp",EDGE,"E742"),sQuery(id+"F0.wireOp",EDGE,"E743"),sQuery(id+"F0.wireOp",EDGE,"E744"),sQuery(id+"F0.wireOp",EDGE,"E744"),sQuery(id+"F0.wireOp",EDGE,"E744"),sQuery(id+"F0.wireOp",EDGE,"E744"),sQuery(id+"F0.wireOp",EDGE,"E745"),sQuery(id+"F0.wireOp",EDGE,"E746"),sQuery(id+"F0.wireOp",EDGE,"E746"),sQuery(id+"F0.wireOp",EDGE,"E747"),sQuery(id+"F0.wireOp",EDGE,"E748"),sQuery(id+"F0.wireOp",EDGE,"E748"),sQuery(id+"F0.wireOp",EDGE,"E749"),sQuery(id+"F0.wireOp",EDGE,"E750"),sQuery(id+"F0.wireOp",EDGE,"E751"),sQuery(id+"F0.wireOp",EDGE,"E752"),sQuery(id+"F0.wireOp",EDGE,"E753"),sQuery(id+"F0.wireOp",EDGE,"E754"),sQuery(id+"F0.wireOp",EDGE,"E755"),sQuery(id+"F0.wireOp",EDGE,"E756"),sQuery(id+"F0.wireOp",EDGE,"E757"),sQuery(id+"F0.wireOp",EDGE,"E758"),sQuery(id+"F0.wireOp",EDGE,"E759"),sQuery(id+"F0.wireOp",EDGE,"E760"),sQuery(id+"F0.wireOp",EDGE,"E761"),sQuery(id+"F0.wireOp",EDGE,"E762"),sQuery(id+"F0.wireOp",EDGE,"E763"),sQuery(id+"F0.wireOp",EDGE,"E764"),sQuery(id+"F0.wireOp",EDGE,"E765"),sQuery(id+"F0.wireOp",EDGE,"E766"),sQuery(id+"F0.wireOp",EDGE,"E766"),sQuery(id+"F0.wireOp",EDGE,"E767"),sQuery(id+"F0.wireOp",EDGE,"E768"),sQuery(id+"F0.wireOp",EDGE,"E769"),sQuery(id+"F0.wireOp",EDGE,"E770"),sQuery(id+"F0.wireOp",EDGE,"E708"),sQuery(id+"F0.wireOp",EDGE,"E771"),sQuery(id+"F0.wireOp",EDGE,"E772"),sQuery(id+"F0.wireOp",EDGE,"E773"),sQuery(id+"F0.wireOp",EDGE,"E774"),sQuery(id+"F0.wireOp",EDGE,"E775"),sQuery(id+"F0.wireOp",EDGE,"E776"),sQuery(id+"F0.wireOp",EDGE,"E777"),sQuery(id+"F0.wireOp",EDGE,"E777"),sQuery(id+"F0.wireOp",EDGE,"E778"),sQuery(id+"F0.wireOp",EDGE,"E779"),sQuery(id+"F0.wireOp",EDGE,"E779"),sQuery(id+"F0.wireOp",EDGE,"E779"),sQuery(id+"F0.wireOp",EDGE,"E779"),sQuery(id+"F0.wireOp",EDGE,"E780"),sQuery(id+"F0.wireOp",EDGE,"E781"),sQuery(id+"F0.wireOp",EDGE,"E781"),sQuery(id+"F0.wireOp",EDGE,"E781"),sQuery(id+"F0.wireOp",EDGE,"E781"),sQuery(id+"F0.wireOp",EDGE,"E782"),sQuery(id+"F0.wireOp",EDGE,"E783"),sQuery(id+"F0.wireOp",EDGE,"E784"),sQuery(id+"F0.wireOp",EDGE,"E785"),sQuery(id+"F0.wireOp",EDGE,"E786"),sQuery(id+"F0.wireOp",EDGE,"E786"),sQuery(id+"F0.wireOp",EDGE,"E787"),sQuery(id+"F0.wireOp",EDGE,"E788"),sQuery(id+"F0.wireOp",EDGE,"E789"),sQuery(id+"F0.wireOp",EDGE,"E790"),sQuery(id+"F0.wireOp",EDGE,"E791"),sQuery(id+"F0.wireOp",EDGE,"E792"),sQuery(id+"F0.wireOp",EDGE,"E793"),sQuery(id+"F0.wireOp",EDGE,"E793"),sQuery(id+"F0.wireOp",EDGE,"E793"),sQuery(id+"F0.wireOp",EDGE,"E793"),sQuery(id+"F0.wireOp",EDGE,"E793"),sQuery(id+"F0.wireOp",EDGE,"E794"),sQuery(id+"F0.wireOp",EDGE,"E771"),sQuery(id+"F0.wireOp",EDGE,"E812"),sQuery(id+"F0.wireOp",EDGE,"E813"),sQuery(id+"F0.wireOp",EDGE,"E814"),sQuery(id+"F0.wireOp",EDGE,"E814"),sQuery(id+"F0.wireOp",EDGE,"E815"),sQuery(id+"F0.wireOp",EDGE,"E816"),sQuery(id+"F0.wireOp",EDGE,"E817"),sQuery(id+"F0.wireOp",EDGE,"E818"),sQuery(id+"F0.wireOp",EDGE,"E819"),sQuery(id+"F0.wireOp",EDGE,"E819"),sQuery(id+"F0.wireOp",EDGE,"E820"),sQuery(id+"F0.wireOp",EDGE,"E821"),sQuery(id+"F0.wireOp",EDGE,"E822"),sQuery(id+"F0.wireOp",EDGE,"E823"),sQuery(id+"F0.wireOp",EDGE,"E824"),sQuery(id+"F0.wireOp",EDGE,"E825"),sQuery(id+"F0.wireOp",EDGE,"E826"),sQuery(id+"F0.wireOp",EDGE,"E827"),sQuery(id+"F0.wireOp",EDGE,"E828"),sQuery(id+"F0.wireOp",EDGE,"E829"),sQuery(id+"F0.wireOp",EDGE,"E830"),sQuery(id+"F0.wireOp",EDGE,"E831"),sQuery(id+"F0.wireOp",EDGE,"E832"),sQuery(id+"F0.wireOp",EDGE,"E832"),sQuery(id+"F0.wireOp",EDGE,"E833"),sQuery(id+"F0.wireOp",EDGE,"E834"),sQuery(id+"F0.wireOp",EDGE,"E835"),sQuery(id+"F0.wireOp",EDGE,"E836"),sQuery(id+"F0.wireOp",EDGE,"E837"),sQuery(id+"F0.wireOp",EDGE,"E838"),sQuery(id+"F0.wireOp",EDGE,"E839"),sQuery(id+"F0.wireOp",EDGE,"E840"),sQuery(id+"F0.wireOp",EDGE,"E841"),sQuery(id+"F0.wireOp",EDGE,"E842"),sQuery(id+"F0.wireOp",EDGE,"E843"),sQuery(id+"F0.wireOp",EDGE,"E844"),sQuery(id+"F0.wireOp",EDGE,"E845"),sQuery(id+"F0.wireOp",EDGE,"E846"),sQuery(id+"F0.wireOp",EDGE,"E847"),sQuery(id+"F0.wireOp",EDGE,"E848"),sQuery(id+"F0.wireOp",EDGE,"E849"),sQuery(id+"F0.wireOp",EDGE,"E850"),sQuery(id+"F0.wireOp",EDGE,"E851"),sQuery(id+"F0.wireOp",EDGE,"E852"),sQuery(id+"F0.wireOp",EDGE,"E853"),sQuery(id+"F0.wireOp",EDGE,"E854"),sQuery(id+"F0.wireOp",EDGE,"E854"),sQuery(id+"F0.wireOp",EDGE,"E855"),sQuery(id+"F0.wireOp",EDGE,"E856"),sQuery(id+"F0.wireOp",EDGE,"E856"),sQuery(id+"F0.wireOp",EDGE,"E857"),sQuery(id+"F0.wireOp",EDGE,"E858"),sQuery(id+"F0.wireOp",EDGE,"E858"),sQuery(id+"F0.wireOp",EDGE,"E859"),sQuery(id+"F0.wireOp",EDGE,"E812"),sQuery(id+"F0.wireOp",EDGE,"E860"),sQuery(id+"F0.wireOp",EDGE,"E861"),sQuery(id+"F0.wireOp",EDGE,"E862"),sQuery(id+"F0.wireOp",EDGE,"E863"),sQuery(id+"F0.wireOp",EDGE,"E864"),sQuery(id+"F0.wireOp",EDGE,"E864"),sQuery(id+"F0.wireOp",EDGE,"E864"),sQuery(id+"F0.wireOp",EDGE,"E865"),sQuery(id+"F0.wireOp",EDGE,"E866"),sQuery(id+"F0.wireOp",EDGE,"E867"),sQuery(id+"F0.wireOp",EDGE,"E867"),sQuery(id+"F0.wireOp",EDGE,"E868"),sQuery(id+"F0.wireOp",EDGE,"E869"),sQuery(id+"F0.wireOp",EDGE,"E870"),sQuery(id+"F0.wireOp",EDGE,"E871"),sQuery(id+"F0.wireOp",EDGE,"E872"),sQuery(id+"F0.wireOp",EDGE,"E873"),sQuery(id+"F0.wireOp",EDGE,"E873"),sQuery(id+"F0.wireOp",EDGE,"E874"),sQuery(id+"F0.wireOp",EDGE,"E875"),sQuery(id+"F0.wireOp",EDGE,"E876"),sQuery(id+"F0.wireOp",EDGE,"E877"),sQuery(id+"F0.wireOp",EDGE,"E878"),sQuery(id+"F0.wireOp",EDGE,"E878"),sQuery(id+"F0.wireOp",EDGE,"E878"),sQuery(id+"F0.wireOp",EDGE,"E879"),sQuery(id+"F0.wireOp",EDGE,"E880"),sQuery(id+"F0.wireOp",EDGE,"E881"),sQuery(id+"F0.wireOp",EDGE,"E882"),sQuery(id+"F0.wireOp",EDGE,"E882"),sQuery(id+"F0.wireOp",EDGE,"E882"),sQuery(id+"F0.wireOp",EDGE,"E882"),sQuery(id+"F0.wireOp",EDGE,"E883"),sQuery(id+"F0.wireOp",EDGE,"E884"),sQuery(id+"F0.wireOp",EDGE,"E884"),sQuery(id+"F0.wireOp",EDGE,"E885"),sQuery(id+"F0.wireOp",EDGE,"E860"),sQuery(id+"F0.wireOp",EDGE,"E886"),sQuery(id+"F0.wireOp",EDGE,"E887"),sQuery(id+"F0.wireOp",EDGE,"E888"),sQuery(id+"F0.wireOp",EDGE,"E888"),sQuery(id+"F0.wireOp",EDGE,"E889"),sQuery(id+"F0.wireOp",EDGE,"E890"),sQuery(id+"F0.wireOp",EDGE,"E891"),sQuery(id+"F0.wireOp",EDGE,"E892"),sQuery(id+"F0.wireOp",EDGE,"E893"),sQuery(id+"F0.wireOp",EDGE,"E894"),sQuery(id+"F0.wireOp",EDGE,"E895"),sQuery(id+"F0.wireOp",EDGE,"E895"),sQuery(id+"F0.wireOp",EDGE,"E896"),sQuery(id+"F0.wireOp",EDGE,"E897"),sQuery(id+"F0.wireOp",EDGE,"E898"),sQuery(id+"F0.wireOp",EDGE,"E899"),sQuery(id+"F0.wireOp",EDGE,"E900"),sQuery(id+"F0.wireOp",EDGE,"E900"),sQuery(id+"F0.wireOp",EDGE,"E901"),sQuery(id+"F0.wireOp",EDGE,"E902"),sQuery(id+"F0.wireOp",EDGE,"E902"),sQuery(id+"F0.wireOp",EDGE,"E903"),sQuery(id+"F0.wireOp",EDGE,"E904"),sQuery(id+"F0.wireOp",EDGE,"E905"),sQuery(id+"F0.wireOp",EDGE,"E906"),sQuery(id+"F0.wireOp",EDGE,"E907"),sQuery(id+"F0.wireOp",EDGE,"E908"),sQuery(id+"F0.wireOp",EDGE,"E908"),sQuery(id+"F0.wireOp",EDGE,"E908"),sQuery(id+"F0.wireOp",EDGE,"E908"),sQuery(id+"F0.wireOp",EDGE,"E909"),sQuery(id+"F0.wireOp",EDGE,"E910"),sQuery(id+"F0.wireOp",EDGE,"E911"),sQuery(id+"F0.wireOp",EDGE,"E912"),sQuery(id+"F0.wireOp",EDGE,"E913"),sQuery(id+"F0.wireOp",EDGE,"E914"),sQuery(id+"F0.wireOp",EDGE,"E915"),sQuery(id+"F0.wireOp",EDGE,"E916"),sQuery(id+"F0.wireOp",EDGE,"E916"),sQuery(id+"F0.wireOp",EDGE,"E917"),sQuery(id+"F0.wireOp",EDGE,"E918"),sQuery(id+"F0.wireOp",EDGE,"E919"),sQuery(id+"F0.wireOp",EDGE,"E920"),sQuery(id+"F0.wireOp",EDGE,"E921"),sQuery(id+"F0.wireOp",EDGE,"E922"),sQuery(id+"F0.wireOp",EDGE,"E923"),sQuery(id+"F0.wireOp",EDGE,"E924"),sQuery(id+"F0.wireOp",EDGE,"E924"),sQuery(id+"F0.wireOp",EDGE,"E925"),sQuery(id+"F0.wireOp",EDGE,"E926"),sQuery(id+"F0.wireOp",EDGE,"E926"),sQuery(id+"F0.wireOp",EDGE,"E927"),sQuery(id+"F0.wireOp",EDGE,"E928"),sQuery(id+"F0.wireOp",EDGE,"E929"),sQuery(id+"F0.wireOp",EDGE,"E930"),sQuery(id+"F0.wireOp",EDGE,"E931"),sQuery(id+"F0.wireOp",EDGE,"E932"),sQuery(id+"F0.wireOp",EDGE,"E933"),sQuery(id+"F0.wireOp",EDGE,"E934"),sQuery(id+"F0.wireOp",EDGE,"E935"),sQuery(id+"F0.wireOp",EDGE,"E936"),sQuery(id+"F0.wireOp",EDGE,"E937"),sQuery(id+"F0.wireOp",EDGE,"E937"),sQuery(id+"F0.wireOp",EDGE,"E938"),sQuery(id+"F0.wireOp",EDGE,"E939"),sQuery(id+"F0.wireOp",EDGE,"E940"),sQuery(id+"F0.wireOp",EDGE,"E941"),sQuery(id+"F0.wireOp",EDGE,"E941"),sQuery(id+"F0.wireOp",EDGE,"E942"),sQuery(id+"F0.wireOp",EDGE,"E943"),sQuery(id+"F0.wireOp",EDGE,"E944"),sQuery(id+"F0.wireOp",EDGE,"E945"),sQuery(id+"F0.wireOp",EDGE,"E946"),sQuery(id+"F0.wireOp",EDGE,"E946"),sQuery(id+"F0.wireOp",EDGE,"E947"),sQuery(id+"F0.wireOp",EDGE,"E948"),sQuery(id+"F0.wireOp",EDGE,"E949"),sQuery(id+"F0.wireOp",EDGE,"E950"),sQuery(id+"F0.wireOp",EDGE,"E951"),sQuery(id+"F0.wireOp",EDGE,"E952"),sQuery(id+"F0.wireOp",EDGE,"E952"),sQuery(id+"F0.wireOp",EDGE,"E953"),sQuery(id+"F0.wireOp",EDGE,"E954"),sQuery(id+"F0.wireOp",EDGE,"E955"),sQuery(id+"F0.wireOp",EDGE,"E956"),sQuery(id+"F0.wireOp",EDGE,"E957"),sQuery(id+"F0.wireOp",EDGE,"E958"),sQuery(id+"F0.wireOp",EDGE,"E959"),sQuery(id+"F0.wireOp",EDGE,"E960"),sQuery(id+"F0.wireOp",EDGE,"E961"),sQuery(id+"F0.wireOp",EDGE,"E962"),sQuery(id+"F0.wireOp",EDGE,"E963"),sQuery(id+"F0.wireOp",EDGE,"E964"),sQuery(id+"F0.wireOp",EDGE,"E965"),sQuery(id+"F0.wireOp",EDGE,"E966"),sQuery(id+"F0.wireOp",EDGE,"E967"),sQuery(id+"F0.wireOp",EDGE,"E968"),sQuery(id+"F0.wireOp",EDGE,"E968"),sQuery(id+"F0.wireOp",EDGE,"E969"),sQuery(id+"F0.wireOp",EDGE,"E970"),sQuery(id+"F0.wireOp",EDGE,"E970"),sQuery(id+"F0.wireOp",EDGE,"E971"),sQuery(id+"F0.wireOp",EDGE,"E972"),sQuery(id+"F0.wireOp",EDGE,"E972"),sQuery(id+"F0.wireOp",EDGE,"E973"),sQuery(id+"F0.wireOp",EDGE,"E974"),sQuery(id+"F0.wireOp",EDGE,"E975"),sQuery(id+"F0.wireOp",EDGE,"E976"),sQuery(id+"F0.wireOp",EDGE,"E977"),sQuery(id+"F0.wireOp",EDGE,"E977"),sQuery(id+"F0.wireOp",EDGE,"E978"),sQuery(id+"F0.wireOp",EDGE,"E979"),sQuery(id+"F0.wireOp",EDGE,"E979"),sQuery(id+"F0.wireOp",EDGE,"E980"),sQuery(id+"F0.wireOp",EDGE,"E981"),sQuery(id+"F0.wireOp",EDGE,"E981"),sQuery(id+"F0.wireOp",EDGE,"E982"),sQuery(id+"F0.wireOp",EDGE,"E983"),sQuery(id+"F0.wireOp",EDGE,"E984"),sQuery(id+"F0.wireOp",EDGE,"E985"),sQuery(id+"F0.wireOp",EDGE,"E986"),sQuery(id+"F0.wireOp",EDGE,"E987"),sQuery(id+"F0.wireOp",EDGE,"E988"),sQuery(id+"F0.wireOp",EDGE,"E989"),sQuery(id+"F0.wireOp",EDGE,"E990"),sQuery(id+"F0.wireOp",EDGE,"E991"),sQuery(id+"F0.wireOp",EDGE,"E992"),sQuery(id+"F0.wireOp",EDGE,"E993"),sQuery(id+"F0.wireOp",EDGE,"E994"),sQuery(id+"F0.wireOp",EDGE,"E995"),sQuery(id+"F0.wireOp",EDGE,"E995"),sQuery(id+"F0.wireOp",EDGE,"E996"),sQuery(id+"F0.wireOp",EDGE,"E997"),sQuery(id+"F0.wireOp",EDGE,"E998"),sQuery(id+"F0.wireOp",EDGE,"E999"),sQuery(id+"F0.wireOp",EDGE,"E1000"),sQuery(id+"F0.wireOp",EDGE,"E1000"),sQuery(id+"F0.wireOp",EDGE,"E1001"),sQuery(id+"F0.wireOp",EDGE,"E1002"),sQuery(id+"F0.wireOp",EDGE,"E1003"),sQuery(id+"F0.wireOp",EDGE,"E1004"),sQuery(id+"F0.wireOp",EDGE,"E1005"),sQuery(id+"F0.wireOp",EDGE,"E1006"),sQuery(id+"F0.wireOp",EDGE,"E1007"),sQuery(id+"F0.wireOp",EDGE,"E1008"),sQuery(id+"F0.wireOp",EDGE,"E1009"),sQuery(id+"F0.wireOp",EDGE,"E1010"),sQuery(id+"F0.wireOp",EDGE,"E1011"),sQuery(id+"F0.wireOp",EDGE,"E1012"),sQuery(id+"F0.wireOp",EDGE,"E1013"),sQuery(id+"F0.wireOp",EDGE,"E1013"),sQuery(id+"F0.wireOp",EDGE,"E1013"),sQuery(id+"F0.wireOp",EDGE,"E1013"),sQuery(id+"F0.wireOp",EDGE,"E1013"),sQuery(id+"F0.wireOp",EDGE,"E1014"),sQuery(id+"F0.wireOp",EDGE,"E1015"),sQuery(id+"F0.wireOp",EDGE,"E1015"),sQuery(id+"F0.wireOp",EDGE,"E1016"),sQuery(id+"F0.wireOp",EDGE,"E1017"),sQuery(id+"F0.wireOp",EDGE,"E1018"),sQuery(id+"F0.wireOp",EDGE,"E1019"),sQuery(id+"F0.wireOp",EDGE,"E1020"),sQuery(id+"F0.wireOp",EDGE,"E1021"),sQuery(id+"F0.wireOp",EDGE,"E1021"),sQuery(id+"F0.wireOp",EDGE,"E1021"),sQuery(id+"F0.wireOp",EDGE,"E1021"),sQuery(id+"F0.wireOp",EDGE,"E1022"),sQuery(id+"F0.wireOp",EDGE,"E1023"),sQuery(id+"F0.wireOp",EDGE,"E1024"),sQuery(id+"F0.wireOp",EDGE,"E1024"),sQuery(id+"F0.wireOp",EDGE,"E1025"),sQuery(id+"F0.wireOp",EDGE,"E1026"),sQuery(id+"F0.wireOp",EDGE,"E1027"),sQuery(id+"F0.wireOp",EDGE,"E1028"),sQuery(id+"F0.wireOp",EDGE,"E1029"),sQuery(id+"F0.wireOp",EDGE,"E1029"),sQuery(id+"F0.wireOp",EDGE,"E1030"),sQuery(id+"F0.wireOp",EDGE,"E1031"),sQuery(id+"F0.wireOp",EDGE,"E1031"),sQuery(id+"F0.wireOp",EDGE,"E1032"),sQuery(id+"F0.wireOp",EDGE,"E1033"),sQuery(id+"F0.wireOp",EDGE,"E1033"),sQuery(id+"F0.wireOp",EDGE,"E1034"),sQuery(id+"F0.wireOp",EDGE,"E1035"),sQuery(id+"F0.wireOp",EDGE,"E1035"),sQuery(id+"F0.wireOp",EDGE,"E1036"),sQuery(id+"F0.wireOp",EDGE,"E1037"),sQuery(id+"F0.wireOp",EDGE,"E1038"),sQuery(id+"F0.wireOp",EDGE,"E1038"),sQuery(id+"F0.wireOp",EDGE,"E1038"),sQuery(id+"F0.wireOp",EDGE,"E1039"),sQuery(id+"F0.wireOp",EDGE,"E1040"),sQuery(id+"F0.wireOp",EDGE,"E1041"),sQuery(id+"F0.wireOp",EDGE,"E1042"),sQuery(id+"F0.wireOp",EDGE,"E1043"),sQuery(id+"F0.wireOp",EDGE,"E1044"),sQuery(id+"F0.wireOp",EDGE,"E1045"),sQuery(id+"F0.wireOp",EDGE,"E1046"),sQuery(id+"F0.wireOp",EDGE,"E1046"),sQuery(id+"F0.wireOp",EDGE,"E1046"),sQuery(id+"F0.wireOp",EDGE,"E1047"),sQuery(id+"F0.wireOp",EDGE,"E1048"),sQuery(id+"F0.wireOp",EDGE,"E1048"),sQuery(id+"F0.wireOp",EDGE,"E1048"),sQuery(id+"F0.wireOp",EDGE,"E1048"),sQuery(id+"F0.wireOp",EDGE,"E1048"),sQuery(id+"F0.wireOp",EDGE,"E1049"),sQuery(id+"F0.wireOp",EDGE,"E1050"),sQuery(id+"F0.wireOp",EDGE,"E1051"),sQuery(id+"F0.wireOp",EDGE,"E1052"),sQuery(id+"F0.wireOp",EDGE,"E1053"),sQuery(id+"F0.wireOp",EDGE,"E1054"),sQuery(id+"F0.wireOp",EDGE,"E1055"),sQuery(id+"F0.wireOp",EDGE,"E1056"),sQuery(id+"F0.wireOp",EDGE,"E1056"),sQuery(id+"F0.wireOp",EDGE,"E1056"),sQuery(id+"F0.wireOp",EDGE,"E1056"),sQuery(id+"F0.wireOp",EDGE,"E1057"),sQuery(id+"F0.wireOp",EDGE,"E1058"),sQuery(id+"F0.wireOp",EDGE,"E1058"),sQuery(id+"F0.wireOp",EDGE,"E1059"),sQuery(id+"F0.wireOp",EDGE,"E1060"),sQuery(id+"F0.wireOp",EDGE,"E1060"),sQuery(id+"F0.wireOp",EDGE,"E1061"),sQuery(id+"F0.wireOp",EDGE,"E1062"),sQuery(id+"F0.wireOp",EDGE,"E1063"),sQuery(id+"F0.wireOp",EDGE,"E1064"),sQuery(id+"F0.wireOp",EDGE,"E1065"),sQuery(id+"F0.wireOp",EDGE,"E1066"),sQuery(id+"F0.wireOp",EDGE,"E1067"),sQuery(id+"F0.wireOp",EDGE,"E1068"),sQuery(id+"F0.wireOp",EDGE,"E1069"),sQuery(id+"F0.wireOp",EDGE,"E1070"),sQuery(id+"F0.wireOp",EDGE,"E1071"),sQuery(id+"F0.wireOp",EDGE,"E1071"),sQuery(id+"F0.wireOp",EDGE,"E1071"),sQuery(id+"F0.wireOp",EDGE,"E1072"),sQuery(id+"F0.wireOp",EDGE,"E1073"),sQuery(id+"F0.wireOp",EDGE,"E1074"),sQuery(id+"F0.wireOp",EDGE,"E1075"),sQuery(id+"F0.wireOp",EDGE,"E1076"),sQuery(id+"F0.wireOp",EDGE,"E1077"),sQuery(id+"F0.wireOp",EDGE,"E1078"),sQuery(id+"F0.wireOp",EDGE,"E1079"),sQuery(id+"F0.wireOp",EDGE,"E1080"),sQuery(id+"F0.wireOp",EDGE,"E1081"),sQuery(id+"F0.wireOp",EDGE,"E1022"),sQuery(id+"F0.wireOp",EDGE,"E1113"),sQuery(id+"F0.wireOp",EDGE,"E1113"),sQuery(id+"F0.wireOp",EDGE,"E1114"),sQuery(id+"F0.wireOp",EDGE,"E1115"),sQuery(id+"F0.wireOp",EDGE,"E1116"),sQuery(id+"F0.wireOp",EDGE,"E1117"),sQuery(id+"F0.wireOp",EDGE,"E1118"),sQuery(id+"F0.wireOp",EDGE,"E1119"),sQuery(id+"F0.wireOp",EDGE,"E1120"),sQuery(id+"F0.wireOp",EDGE,"E1121"),sQuery(id+"F0.wireOp",EDGE,"E1122"),sQuery(id+"F0.wireOp",EDGE,"E1123"),sQuery(id+"F0.wireOp",EDGE,"E1124"),sQuery(id+"F0.wireOp",EDGE,"E1125"),sQuery(id+"F0.wireOp",EDGE,"E1126"),sQuery(id+"F0.wireOp",EDGE,"E1126"),sQuery(id+"F0.wireOp",EDGE,"E1127"),sQuery(id+"F0.wireOp",EDGE,"E1128"),sQuery(id+"F0.wireOp",EDGE,"E1129"),sQuery(id+"F0.wireOp",EDGE,"E1130"),sQuery(id+"F0.wireOp",EDGE,"E1131"),sQuery(id+"F0.wireOp",EDGE,"E1132"),sQuery(id+"F0.wireOp",EDGE,"E1133"),sQuery(id+"F0.wireOp",EDGE,"E1134"),sQuery(id+"F0.wireOp",EDGE,"E1135"),sQuery(id+"F0.wireOp",EDGE,"E1136"),sQuery(id+"F0.wireOp",EDGE,"E1137"),sQuery(id+"F0.wireOp",EDGE,"E1138"),sQuery(id+"F0.wireOp",EDGE,"E1139"),sQuery(id+"F0.wireOp",EDGE,"E1140"),sQuery(id+"F0.wireOp",EDGE,"E1140"),sQuery(id+"F0.wireOp",EDGE,"E1141"),sQuery(id+"F0.wireOp",EDGE,"E1142"),sQuery(id+"F0.wireOp",EDGE,"E1142"),sQuery(id+"F0.wireOp",EDGE,"E1143"),sQuery(id+"F0.wireOp",EDGE,"E1144"),sQuery(id+"F0.wireOp",EDGE,"E1145"),sQuery(id+"F0.wireOp",EDGE,"E1146"),sQuery(id+"F0.wireOp",EDGE,"E1147"),sQuery(id+"F0.wireOp",EDGE,"E1147"),sQuery(id+"F0.wireOp",EDGE,"E1148"),sQuery(id+"F0.wireOp",EDGE,"E1113"),sQuery(id+"F0.wireOp",EDGE,"E1149"),sQuery(id+"F0.wireOp",EDGE,"E1150"),sQuery(id+"F0.wireOp",EDGE,"E1151"),sQuery(id+"F0.wireOp",EDGE,"E1152"),sQuery(id+"F0.wireOp",EDGE,"E1153"),sQuery(id+"F0.wireOp",EDGE,"E1154"),sQuery(id+"F0.wireOp",EDGE,"E1155"),sQuery(id+"F0.wireOp",EDGE,"E1156"),sQuery(id+"F0.wireOp",EDGE,"E1157"),sQuery(id+"F0.wireOp",EDGE,"E1157"),sQuery(id+"F0.wireOp",EDGE,"E1157"),sQuery(id+"F0.wireOp",EDGE,"E1157"),sQuery(id+"F0.wireOp",EDGE,"E1158"),sQuery(id+"F0.wireOp",EDGE,"E1159"),sQuery(id+"F0.wireOp",EDGE,"E1160"),sQuery(id+"F0.wireOp",EDGE,"E1161"),sQuery(id+"F0.wireOp",EDGE,"E1162"),sQuery(id+"F0.wireOp",EDGE,"E1163"),sQuery(id+"F0.wireOp",EDGE,"E1164"),sQuery(id+"F0.wireOp",EDGE,"E1165"),sQuery(id+"F0.wireOp",EDGE,"E1166"),sQuery(id+"F0.wireOp",EDGE,"E1167"),sQuery(id+"F0.wireOp",EDGE,"E1167"),sQuery(id+"F0.wireOp",EDGE,"E1168"),sQuery(id+"F0.wireOp",EDGE,"E1169"),sQuery(id+"F0.wireOp",EDGE,"E1169"),sQuery(id+"F0.wireOp",EDGE,"E1170"),sQuery(id+"F0.wireOp",EDGE,"E1171"),sQuery(id+"F0.wireOp",EDGE,"E1171"),sQuery(id+"F0.wireOp",EDGE,"E1172"),sQuery(id+"F0.wireOp",EDGE,"E1173"),sQuery(id+"F0.wireOp",EDGE,"E1174"),sQuery(id+"F0.wireOp",EDGE,"E1175"),sQuery(id+"F0.wireOp",EDGE,"E1176"),sQuery(id+"F0.wireOp",EDGE,"E1177"),sQuery(id+"F0.wireOp",EDGE,"E1178"),sQuery(id+"F0.wireOp",EDGE,"E1179"),sQuery(id+"F0.wireOp",EDGE,"E1180"),sQuery(id+"F0.wireOp",EDGE,"E1180"),sQuery(id+"F0.wireOp",EDGE,"E1181"),sQuery(id+"F0.wireOp",EDGE,"E1182"),sQuery(id+"F0.wireOp",EDGE,"E1182"),sQuery(id+"F0.wireOp",EDGE,"E1183"),sQuery(id+"F0.wireOp",EDGE,"E1184"),sQuery(id+"F0.wireOp",EDGE,"E1184"),sQuery(id+"F0.wireOp",EDGE,"E1184"),sQuery(id+"F0.wireOp",EDGE,"E1184"),sQuery(id+"F0.wireOp",EDGE,"E1185"),sQuery(id+"F0.wireOp",EDGE,"E1186"),sQuery(id+"F0.wireOp",EDGE,"E1187"),sQuery(id+"F0.wireOp",EDGE,"E1188"),sQuery(id+"F0.wireOp",EDGE,"E1189"),sQuery(id+"F0.wireOp",EDGE,"E1189"),sQuery(id+"F0.wireOp",EDGE,"E1189"),sQuery(id+"F0.wireOp",EDGE,"E1189"),sQuery(id+"F0.wireOp",EDGE,"E1190"),sQuery(id+"F0.wireOp",EDGE,"E1191"),sQuery(id+"F0.wireOp",EDGE,"E1192"),sQuery(id+"F0.wireOp",EDGE,"E1193"),sQuery(id+"F0.wireOp",EDGE,"E1193"),sQuery(id+"F0.wireOp",EDGE,"E1194"),sQuery(id+"F0.wireOp",EDGE,"E1195"),sQuery(id+"F0.wireOp",EDGE,"E1196"),sQuery(id+"F0.wireOp",EDGE,"E1197"),sQuery(id+"F0.wireOp",EDGE,"E1198"),sQuery(id+"F0.wireOp",EDGE,"E1199"),sQuery(id+"F0.wireOp",EDGE,"E1199"),sQuery(id+"F0.wireOp",EDGE,"E1200"),sQuery(id+"F0.wireOp",EDGE,"E1201"),sQuery(id+"F0.wireOp",EDGE,"E1202"),sQuery(id+"F0.wireOp",EDGE,"E1202"),sQuery(id+"F0.wireOp",EDGE,"E1203"),sQuery(id+"F0.wireOp",EDGE,"E1204"),sQuery(id+"F0.wireOp",EDGE,"E1205"),sQuery(id+"F0.wireOp",EDGE,"E1206"),sQuery(id+"F0.wireOp",EDGE,"E1206"),sQuery(id+"F0.wireOp",EDGE,"E1207"),sQuery(id+"F0.wireOp",EDGE,"E1208"),sQuery(id+"F0.wireOp",EDGE,"E1208"),sQuery(id+"F0.wireOp",EDGE,"E1208"),sQuery(id+"F0.wireOp",EDGE,"E1208"),sQuery(id+"F0.wireOp",EDGE,"E1208"),sQuery(id+"F0.wireOp",EDGE,"E1209"),sQuery(id+"F0.wireOp",EDGE,"E1210"),sQuery(id+"F0.wireOp",EDGE,"E1211"),sQuery(id+"F0.wireOp",EDGE,"E1211"),sQuery(id+"F0.wireOp",EDGE,"E1211"),sQuery(id+"F0.wireOp",EDGE,"E1212"),sQuery(id+"F0.wireOp",EDGE,"E1213"),sQuery(id+"F0.wireOp",EDGE,"E1214"),sQuery(id+"F0.wireOp",EDGE,"E1215"),sQuery(id+"F0.wireOp",EDGE,"E1215"),sQuery(id+"F0.wireOp",EDGE,"E1216"),sQuery(id+"F0.wireOp",EDGE,"E1217"),sQuery(id+"F0.wireOp",EDGE,"E1217"),sQuery(id+"F0.wireOp",EDGE,"E1218"),sQuery(id+"F0.wireOp",EDGE,"E1219"),sQuery(id+"F0.wireOp",EDGE,"E1219"),sQuery(id+"F0.wireOp",EDGE,"E1219"),sQuery(id+"F0.wireOp",EDGE,"E1219"),sQuery(id+"F0.wireOp",EDGE,"E1220"),sQuery(id+"F0.wireOp",EDGE,"E1221"),sQuery(id+"F0.wireOp",EDGE,"E1222"),sQuery(id+"F0.wireOp",EDGE,"E1223"),sQuery(id+"F0.wireOp",EDGE,"E1224"),sQuery(id+"F0.wireOp",EDGE,"E1225"),sQuery(id+"F0.wireOp",EDGE,"E1225"),sQuery(id+"F0.wireOp",EDGE,"E1226"),sQuery(id+"F0.wireOp",EDGE,"E1227"),sQuery(id+"F0.wireOp",EDGE,"E1227"),sQuery(id+"F0.wireOp",EDGE,"E1228"),sQuery(id+"F0.wireOp",EDGE,"E1229"),sQuery(id+"F0.wireOp",EDGE,"E1229"),sQuery(id+"F0.wireOp",EDGE,"E1230"),sQuery(id+"F0.wireOp",EDGE,"E1231"),sQuery(id+"F0.wireOp",EDGE,"E1232"),sQuery(id+"F0.wireOp",EDGE,"E1233"),sQuery(id+"F0.wireOp",EDGE,"E1234"),sQuery(id+"F0.wireOp",EDGE,"E1235"),sQuery(id+"F0.wireOp",EDGE,"E1236"),sQuery(id+"F0.wireOp",EDGE,"E1236"),sQuery(id+"F0.wireOp",EDGE,"E1237"),sQuery(id+"F0.wireOp",EDGE,"E1238"),sQuery(id+"F0.wireOp",EDGE,"E1238"),sQuery(id+"F0.wireOp",EDGE,"E1238"),sQuery(id+"F0.wireOp",EDGE,"E1238"),sQuery(id+"F0.wireOp",EDGE,"E1238"),sQuery(id+"F0.wireOp",EDGE,"E1239"),sQuery(id+"F0.wireOp",EDGE,"E1240"),sQuery(id+"F0.wireOp",EDGE,"E1241"),sQuery(id+"F0.wireOp",EDGE,"E1242"),sQuery(id+"F0.wireOp",EDGE,"E1243"),sQuery(id+"F0.wireOp",EDGE,"E1244"),sQuery(id+"F0.wireOp",EDGE,"E1245"),sQuery(id+"F0.wireOp",EDGE,"E1245"),sQuery(id+"F0.wireOp",EDGE,"E1245"),sQuery(id+"F0.wireOp",EDGE,"E1246"),sQuery(id+"F0.wireOp",EDGE,"E1247"),sQuery(id+"F0.wireOp",EDGE,"E1247"),sQuery(id+"F0.wireOp",EDGE,"E1247"),sQuery(id+"F0.wireOp",EDGE,"E1247"),sQuery(id+"F0.wireOp",EDGE,"E1248"),sQuery(id+"F0.wireOp",EDGE,"E1249"),sQuery(id+"F0.wireOp",EDGE,"E1250"),sQuery(id+"F0.wireOp",EDGE,"E1251"),sQuery(id+"F0.wireOp",EDGE,"E1252"),sQuery(id+"F0.wireOp",EDGE,"E1252"),sQuery(id+"F0.wireOp",EDGE,"E1252"),sQuery(id+"F0.wireOp",EDGE,"E1252"),sQuery(id+"F0.wireOp",EDGE,"E1253"),sQuery(id+"F0.wireOp",EDGE,"E1211"),sQuery(id+"F0.wireOp",EDGE,"E1254"),sQuery(id+"F0.wireOp",EDGE,"E1255"),sQuery(id+"F0.wireOp",EDGE,"E1256"),sQuery(id+"F0.wireOp",EDGE,"E1256"),sQuery(id+"F0.wireOp",EDGE,"E1257"),sQuery(id+"F0.wireOp",EDGE,"E1258"),sQuery(id+"F0.wireOp",EDGE,"E1259"),sQuery(id+"F0.wireOp",EDGE,"E1260"),sQuery(id+"F0.wireOp",EDGE,"E1261"),sQuery(id+"F0.wireOp",EDGE,"E1262"),sQuery(id+"F0.wireOp",EDGE,"E1262"),sQuery(id+"F0.wireOp",EDGE,"E1263"),sQuery(id+"F0.wireOp",EDGE,"E1264"),sQuery(id+"F0.wireOp",EDGE,"E1265"),sQuery(id+"F0.wireOp",EDGE,"E1266"),sQuery(id+"F0.wireOp",EDGE,"E1266"),sQuery(id+"F0.wireOp",EDGE,"E1266"),sQuery(id+"F0.wireOp",EDGE,"E1266"),sQuery(id+"F0.wireOp",EDGE,"E1266"),sQuery(id+"F0.wireOp",EDGE,"E1267"),sQuery(id+"F0.wireOp",EDGE,"E1268"),sQuery(id+"F0.wireOp",EDGE,"E1268"),sQuery(id+"F0.wireOp",EDGE,"E1268"),sQuery(id+"F0.wireOp",EDGE,"E1268"),sQuery(id+"F0.wireOp",EDGE,"E1269"),sQuery(id+"F0.wireOp",EDGE,"E1254"),sQuery(id+"F0.wireOp",EDGE,"E1270"),sQuery(id+"F0.wireOp",EDGE,"E1271"),sQuery(id+"F0.wireOp",EDGE,"E1272"),sQuery(id+"F0.wireOp",EDGE,"E1273"),sQuery(id+"F0.wireOp",EDGE,"E1273"),sQuery(id+"F0.wireOp",EDGE,"E1274"),sQuery(id+"F0.wireOp",EDGE,"E1275"),sQuery(id+"F0.wireOp",EDGE,"E1275"),sQuery(id+"F0.wireOp",EDGE,"E1276"),sQuery(id+"F0.wireOp",EDGE,"E1277"),sQuery(id+"F0.wireOp",EDGE,"E1277"),sQuery(id+"F0.wireOp",EDGE,"E1278"),sQuery(id+"F0.wireOp",EDGE,"E1279"),sQuery(id+"F0.wireOp",EDGE,"E1280"),sQuery(id+"F0.wireOp",EDGE,"E1281"),sQuery(id+"F0.wireOp",EDGE,"E1282"),sQuery(id+"F0.wireOp",EDGE,"E1283"),sQuery(id+"F0.wireOp",EDGE,"E1284"),sQuery(id+"F0.wireOp",EDGE,"E1284"),sQuery(id+"F0.wireOp",EDGE,"E1284"),sQuery(id+"F0.wireOp",EDGE,"E1285"),sQuery(id+"F0.wireOp",EDGE,"E1286"),sQuery(id+"F0.wireOp",EDGE,"E1287"),sQuery(id+"F0.wireOp",EDGE,"E1288"),sQuery(id+"F0.wireOp",EDGE,"E1288"),sQuery(id+"F0.wireOp",EDGE,"E1289"),sQuery(id+"F0.wireOp",EDGE,"E1290"),sQuery(id+"F0.wireOp",EDGE,"E1291"),sQuery(id+"F0.wireOp",EDGE,"E1292"),sQuery(id+"F0.wireOp",EDGE,"E1293"),sQuery(id+"F0.wireOp",EDGE,"E1293"),sQuery(id+"F0.wireOp",EDGE,"E1293"),sQuery(id+"F0.wireOp",EDGE,"E1294"),sQuery(id+"F0.wireOp",EDGE,"E1295"),sQuery(id+"F0.wireOp",EDGE,"E1296"),sQuery(id+"F0.wireOp",EDGE,"E1297"),sQuery(id+"F0.wireOp",EDGE,"E1298"),sQuery(id+"F0.wireOp",EDGE,"E1298"),sQuery(id+"F0.wireOp",EDGE,"E1299"),sQuery(id+"F0.wireOp",EDGE,"E1300"),sQuery(id+"F0.wireOp",EDGE,"E1301"),sQuery(id+"F0.wireOp",EDGE,"E1302"),sQuery(id+"F0.wireOp",EDGE,"E1303"),sQuery(id+"F0.wireOp",EDGE,"E1304"),sQuery(id+"F0.wireOp",EDGE,"E1305"),sQuery(id+"F0.wireOp",EDGE,"E1305"),sQuery(id+"F0.wireOp",EDGE,"E1305"),sQuery(id+"F0.wireOp",EDGE,"E1305"),sQuery(id+"F0.wireOp",EDGE,"E1306"),sQuery(id+"F0.wireOp",EDGE,"E1307"),sQuery(id+"F0.wireOp",EDGE,"E1308"),sQuery(id+"F0.wireOp",EDGE,"E1309"),sQuery(id+"F0.wireOp",EDGE,"E1310"),sQuery(id+"F0.wireOp",EDGE,"E1310"),sQuery(id+"F0.wireOp",EDGE,"E1311"),sQuery(id+"F0.wireOp",EDGE,"E1312"),sQuery(id+"F0.wireOp",EDGE,"E1312"),sQuery(id+"F0.wireOp",EDGE,"E1313"),sQuery(id+"F0.wireOp",EDGE,"E1314"),sQuery(id+"F0.wireOp",EDGE,"E1314"),sQuery(id+"F0.wireOp",EDGE,"E1314"),sQuery(id+"F0.wireOp",EDGE,"E1315"),sQuery(id+"F0.wireOp",EDGE,"E1316"),sQuery(id+"F0.wireOp",EDGE,"E1317"),sQuery(id+"F0.wireOp",EDGE,"E1317"),sQuery(id+"F0.wireOp",EDGE,"E1317"),sQuery(id+"F0.wireOp",EDGE,"E1317"),sQuery(id+"F0.wireOp",EDGE,"E1318"),sQuery(id+"F0.wireOp",EDGE,"E1319"),sQuery(id+"F0.wireOp",EDGE,"E1319"),sQuery(id+"F0.wireOp",EDGE,"E1320"),sQuery(id+"F0.wireOp",EDGE,"E1321"),sQuery(id+"F0.wireOp",EDGE,"E1321"),sQuery(id+"F0.wireOp",EDGE,"E1321"),sQuery(id+"F0.wireOp",EDGE,"E1321"),sQuery(id+"F0.wireOp",EDGE,"E1322"),sQuery(id+"F0.wireOp",EDGE,"E1323"),sQuery(id+"F0.wireOp",EDGE,"E1324"),sQuery(id+"F0.wireOp",EDGE,"E1324"),sQuery(id+"F0.wireOp",EDGE,"E1324"),sQuery(id+"F0.wireOp",EDGE,"E1325"),sQuery(id+"F0.wireOp",EDGE,"E1326"),sQuery(id+"F0.wireOp",EDGE,"E1326"),sQuery(id+"F0.wireOp",EDGE,"E1326"),sQuery(id+"F0.wireOp",EDGE,"E1326"),sQuery(id+"F0.wireOp",EDGE,"E1326"),sQuery(id+"F0.wireOp",EDGE,"E1327"),sQuery(id+"F0.wireOp",EDGE,"E1328"),sQuery(id+"F0.wireOp",EDGE,"E1329"),sQuery(id+"F0.wireOp",EDGE,"E1330"),sQuery(id+"F0.wireOp",EDGE,"E1331"),sQuery(id+"F0.wireOp",EDGE,"E1331"),sQuery(id+"F0.wireOp",EDGE,"E1332"),sQuery(id+"F0.wireOp",EDGE,"E1333"),sQuery(id+"F0.wireOp",EDGE,"E1333"),sQuery(id+"F0.wireOp",EDGE,"E1334"),sQuery(id+"F0.wireOp",EDGE,"E1335"),sQuery(id+"F0.wireOp",EDGE,"E1335"),sQuery(id+"F0.wireOp",EDGE,"E1335"),sQuery(id+"F0.wireOp",EDGE,"E1336"),sQuery(id+"F0.wireOp",EDGE,"E1337"),sQuery(id+"F0.wireOp",EDGE,"E1338"),sQuery(id+"F0.wireOp",EDGE,"E1339"),sQuery(id+"F0.wireOp",EDGE,"E1339"),sQuery(id+"F0.wireOp",EDGE,"E1340"),sQuery(id+"F0.wireOp",EDGE,"E1341"),sQuery(id+"F0.wireOp",EDGE,"E1341"),sQuery(id+"F0.wireOp",EDGE,"E1342"),sQuery(id+"F0.wireOp",EDGE,"E1343"),sQuery(id+"F0.wireOp",EDGE,"E1343"),sQuery(id+"F0.wireOp",EDGE,"E1344"),sQuery(id+"F0.wireOp",EDGE,"E1329"),sQuery(id+"F0.wireOp",EDGE,"E1345"),sQuery(id+"F0.wireOp",EDGE,"E1346"),sQuery(id+"F0.wireOp",EDGE,"E1347"),sQuery(id+"F0.wireOp",EDGE,"E1348"),sQuery(id+"F0.wireOp",EDGE,"E1349"),sQuery(id+"F0.wireOp",EDGE,"E1350"),sQuery(id+"F0.wireOp",EDGE,"E1351"),sQuery(id+"F0.wireOp",EDGE,"E1352"),sQuery(id+"F0.wireOp",EDGE,"E1353"),sQuery(id+"F0.wireOp",EDGE,"E1354"),sQuery(id+"F0.wireOp",EDGE,"E1354"),sQuery(id+"F0.wireOp",EDGE,"E1355"),sQuery(id+"F0.wireOp",EDGE,"E1356"),sQuery(id+"F0.wireOp",EDGE,"E1356"),sQuery(id+"F0.wireOp",EDGE,"E1356"),sQuery(id+"F0.wireOp",EDGE,"E1357"),sQuery(id+"F0.wireOp",EDGE,"E1358"),sQuery(id+"F0.wireOp",EDGE,"E1358"),sQuery(id+"F0.wireOp",EDGE,"E1358"),sQuery(id+"F0.wireOp",EDGE,"E1358"),sQuery(id+"F0.wireOp",EDGE,"E1359"),sQuery(id+"F0.wireOp",EDGE,"E1360"),sQuery(id+"F0.wireOp",EDGE,"E1360"),sQuery(id+"F0.wireOp",EDGE,"E1361"),sQuery(id+"F0.wireOp",EDGE,"E1362"),sQuery(id+"F0.wireOp",EDGE,"E1363"),sQuery(id+"F0.wireOp",EDGE,"E1364"),sQuery(id+"F0.wireOp",EDGE,"E1365"),sQuery(id+"F0.wireOp",EDGE,"E1366"),sQuery(id+"F0.wireOp",EDGE,"E1367"),sQuery(id+"F0.wireOp",EDGE,"E1368"),sQuery(id+"F0.wireOp",EDGE,"E1369"),sQuery(id+"F0.wireOp",EDGE,"E1370"),sQuery(id+"F0.wireOp",EDGE,"E1371"),sQuery(id+"F0.wireOp",EDGE,"E1371"),sQuery(id+"F0.wireOp",EDGE,"E1372"),sQuery(id+"F0.wireOp",EDGE,"E1373"),sQuery(id+"F0.wireOp",EDGE,"E1374"),sQuery(id+"F0.wireOp",EDGE,"E1375"),sQuery(id+"F0.wireOp",EDGE,"E1375"),sQuery(id+"F0.wireOp",EDGE,"E1375"),sQuery(id+"F0.wireOp",EDGE,"E1376"),sQuery(id+"F0.wireOp",EDGE,"E1377"),sQuery(id+"F0.wireOp",EDGE,"E1377"),sQuery(id+"F0.wireOp",EDGE,"E1378"),sQuery(id+"F0.wireOp",EDGE,"E1379"),sQuery(id+"F0.wireOp",EDGE,"E1379"),sQuery(id+"F0.wireOp",EDGE,"E1380"),sQuery(id+"F0.wireOp",EDGE,"E1381"),sQuery(id+"F0.wireOp",EDGE,"E1381"),sQuery(id+"F0.wireOp",EDGE,"E1382"),sQuery(id+"F0.wireOp",EDGE,"E1383"),sQuery(id+"F0.wireOp",EDGE,"E1384"),sQuery(id+"F0.wireOp",EDGE,"E1385"),sQuery(id+"F0.wireOp",EDGE,"E1386"),sQuery(id+"F0.wireOp",EDGE,"E1387"),sQuery(id+"F0.wireOp",EDGE,"E1388"),sQuery(id+"F0.wireOp",EDGE,"E1389"),sQuery(id+"F0.wireOp",EDGE,"E1390"),sQuery(id+"F0.wireOp",EDGE,"E1391"),sQuery(id+"F0.wireOp",EDGE,"E1392"),sQuery(id+"F0.wireOp",EDGE,"E1393"),sQuery(id+"F0.wireOp",EDGE,"E1393"),sQuery(id+"F0.wireOp",EDGE,"E1394"),sQuery(id+"F0.wireOp",EDGE,"E1395"),sQuery(id+"F0.wireOp",EDGE,"E1396"),sQuery(id+"F0.wireOp",EDGE,"E1397"),sQuery(id+"F0.wireOp",EDGE,"E1398"),sQuery(id+"F0.wireOp",EDGE,"E1398"),sQuery(id+"F0.wireOp",EDGE,"E1399"),sQuery(id+"F0.wireOp",EDGE,"E1400"),sQuery(id+"F0.wireOp",EDGE,"E1401"),sQuery(id+"F0.wireOp",EDGE,"E1402"),sQuery(id+"F0.wireOp",EDGE,"E1403"),sQuery(id+"F0.wireOp",EDGE,"E1404"),sQuery(id+"F0.wireOp",EDGE,"E1404"),sQuery(id+"F0.wireOp",EDGE,"E1405"),sQuery(id+"F0.wireOp",EDGE,"E1406"),sQuery(id+"F0.wireOp",EDGE,"E1407"),sQuery(id+"F0.wireOp",EDGE,"E1408"),sQuery(id+"F0.wireOp",EDGE,"E1409"),sQuery(id+"F0.wireOp",EDGE,"E1409"),sQuery(id+"F0.wireOp",EDGE,"E1410"),sQuery(id+"F0.wireOp",EDGE,"E1411"),sQuery(id+"F0.wireOp",EDGE,"E1412"),sQuery(id+"F0.wireOp",EDGE,"E1413"),sQuery(id+"F0.wireOp",EDGE,"E1413"),sQuery(id+"F0.wireOp",EDGE,"E1413"),sQuery(id+"F0.wireOp",EDGE,"E1413"),sQuery(id+"F0.wireOp",EDGE,"E1414"),sQuery(id+"F0.wireOp",EDGE,"E1415"),sQuery(id+"F0.wireOp",EDGE,"E1415"),sQuery(id+"F0.wireOp",EDGE,"E1416"),sQuery(id+"F0.wireOp",EDGE,"E1417"),sQuery(id+"F0.wireOp",EDGE,"E1417"),sQuery(id+"F0.wireOp",EDGE,"E1417"),sQuery(id+"F0.wireOp",EDGE,"E1417"),sQuery(id+"F0.wireOp",EDGE,"E1418"),sQuery(id+"F0.wireOp",EDGE,"E1419"),sQuery(id+"F0.wireOp",EDGE,"E1420"),sQuery(id+"F0.wireOp",EDGE,"E1421"),sQuery(id+"F0.wireOp",EDGE,"E1422"),sQuery(id+"F0.wireOp",EDGE,"E1422"),sQuery(id+"F0.wireOp",EDGE,"E1422"),sQuery(id+"F0.wireOp",EDGE,"E1422"),sQuery(id+"F0.wireOp",EDGE,"E1423"),sQuery(id+"F0.wireOp",EDGE,"E1424"),sQuery(id+"F0.wireOp",EDGE,"E1425"),sQuery(id+"F0.wireOp",EDGE,"E1426"),sQuery(id+"F0.wireOp",EDGE,"E1427"),sQuery(id+"F0.wireOp",EDGE,"E1428"),sQuery(id+"F0.wireOp",EDGE,"E1429"),sQuery(id+"F0.wireOp",EDGE,"E1429"),sQuery(id+"F0.wireOp",EDGE,"E1429"),sQuery(id+"F0.wireOp",EDGE,"E1429"),sQuery(id+"F0.wireOp",EDGE,"E1430"),sQuery(id+"F0.wireOp",EDGE,"E1431"),sQuery(id+"F0.wireOp",EDGE,"E1431"),sQuery(id+"F0.wireOp",EDGE,"E1431"),sQuery(id+"F0.wireOp",EDGE,"E1431"),sQuery(id+"F0.wireOp",EDGE,"E1431"),sQuery(id+"F0.wireOp",EDGE,"E1431"),sQuery(id+"F0.wireOp",EDGE,"E1431"),sQuery(id+"F0.wireOp",EDGE,"E1443"),sQuery(id+"F0.wireOp",EDGE,"E1444"),sQuery(id+"F0.wireOp",EDGE,"E1445"),sQuery(id+"F0.wireOp",EDGE,"E1446"),sQuery(id+"F0.wireOp",EDGE,"E1447"),sQuery(id+"F0.wireOp",EDGE,"E1448"),sQuery(id+"F0.wireOp",EDGE,"E1449"),sQuery(id+"F0.wireOp",EDGE,"E1450"),sQuery(id+"F0.wireOp",EDGE,"E1450"),sQuery(id+"F0.wireOp",EDGE,"E1451"),sQuery(id+"F0.wireOp",EDGE,"E1452"),sQuery(id+"F0.wireOp",EDGE,"E1452"),sQuery(id+"F0.wireOp",EDGE,"E1453"),sQuery(id+"F0.wireOp",EDGE,"E1454"),sQuery(id+"F0.wireOp",EDGE,"E1454"),sQuery(id+"F0.wireOp",EDGE,"E1455"),sQuery(id+"F0.wireOp",EDGE,"E1456"),sQuery(id+"F0.wireOp",EDGE,"E1456"),sQuery(id+"F0.wireOp",EDGE,"E1457"),sQuery(id+"F0.wireOp",EDGE,"E1458"),sQuery(id+"F0.wireOp",EDGE,"E1458"),sQuery(id+"F0.wireOp",EDGE,"E1459"),sQuery(id+"F0.wireOp",EDGE,"E1460"),sQuery(id+"F0.wireOp",EDGE,"E1460"),sQuery(id+"F0.wireOp",EDGE,"E1461"),sQuery(id+"F0.wireOp",EDGE,"E1462"),sQuery(id+"F0.wireOp",EDGE,"E1462"),sQuery(id+"F0.wireOp",EDGE,"E1463"),sQuery(id+"F0.wireOp",EDGE,"E1464"),sQuery(id+"F0.wireOp",EDGE,"E1465"),sQuery(id+"F0.wireOp",EDGE,"E1466"),sQuery(id+"F0.wireOp",EDGE,"E1467"),sQuery(id+"F0.wireOp",EDGE,"E1467"),sQuery(id+"F0.wireOp",EDGE,"E1468"),sQuery(id+"F0.wireOp",EDGE,"E1469"),sQuery(id+"F0.wireOp",EDGE,"E1470"),sQuery(id+"F0.wireOp",EDGE,"E1471"),sQuery(id+"F0.wireOp",EDGE,"E1472"),sQuery(id+"F0.wireOp",EDGE,"E1473"),sQuery(id+"F0.wireOp",EDGE,"E1474"),sQuery(id+"F0.wireOp",EDGE,"E1475"),sQuery(id+"F0.wireOp",EDGE,"E1476"),sQuery(id+"F0.wireOp",EDGE,"E1476"),sQuery(id+"F0.wireOp",EDGE,"E1477"),sQuery(id+"F0.wireOp",EDGE,"E1478"),sQuery(id+"F0.wireOp",EDGE,"E1478"),sQuery(id+"F0.wireOp",EDGE,"E1479"),sQuery(id+"F0.wireOp",EDGE,"E1480"),sQuery(id+"F0.wireOp",EDGE,"E1480"),sQuery(id+"F0.wireOp",EDGE,"E1481"),sQuery(id+"F0.wireOp",EDGE,"E1482"),sQuery(id+"F0.wireOp",EDGE,"E1482"),sQuery(id+"F0.wireOp",EDGE,"E1482"),sQuery(id+"F0.wireOp",EDGE,"E1483"),sQuery(id+"F0.wireOp",EDGE,"E1484"),sQuery(id+"F0.wireOp",EDGE,"E1484"),sQuery(id+"F0.wireOp",EDGE,"E1485"),sQuery(id+"F0.wireOp",EDGE,"E1486"),sQuery(id+"F0.wireOp",EDGE,"E1487"),sQuery(id+"F0.wireOp",EDGE,"E1488"),sQuery(id+"F0.wireOp",EDGE,"E1489"),sQuery(id+"F0.wireOp",EDGE,"E1490"),sQuery(id+"F0.wireOp",EDGE,"E1491"),sQuery(id+"F0.wireOp",EDGE,"E1492"),sQuery(id+"F0.wireOp",EDGE,"E1492"),sQuery(id+"F0.wireOp",EDGE,"E1492"),sQuery(id+"F0.wireOp",EDGE,"E1492"),sQuery(id+"F0.wireOp",EDGE,"E1493"),sQuery(id+"F0.wireOp",EDGE,"E1494"),sQuery(id+"F0.wireOp",EDGE,"E1495"),sQuery(id+"F0.wireOp",EDGE,"E1496"),sQuery(id+"F0.wireOp",EDGE,"E1496"),sQuery(id+"F0.wireOp",EDGE,"E1496"),sQuery(id+"F0.wireOp",EDGE,"E1496"),sQuery(id+"F0.wireOp",EDGE,"E1497"),sQuery(id+"F0.wireOp",EDGE,"E1498"),sQuery(id+"F0.wireOp",EDGE,"E1498"),sQuery(id+"F0.wireOp",EDGE,"E1498"),sQuery(id+"F0.wireOp",EDGE,"E1499"),sQuery(id+"F0.wireOp",EDGE,"E1500"),sQuery(id+"F0.wireOp",EDGE,"E1500"),sQuery(id+"F0.wireOp",EDGE,"E1500"),sQuery(id+"F0.wireOp",EDGE,"E1500"),sQuery(id+"F0.wireOp",EDGE,"E1501"),sQuery(id+"F0.wireOp",EDGE,"E1490"),sQuery(id+"F0.wireOp",EDGE,"E1515"),sQuery(id+"F0.wireOp",EDGE,"E1516"),sQuery(id+"F0.wireOp",EDGE,"E1517"),sQuery(id+"F0.wireOp",EDGE,"E1518"),sQuery(id+"F0.wireOp",EDGE,"E1519"),sQuery(id+"F0.wireOp",EDGE,"E1520"),sQuery(id+"F0.wireOp",EDGE,"E1521"),sQuery(id+"F0.wireOp",EDGE,"E1522"),sQuery(id+"F0.wireOp",EDGE,"E1523"),sQuery(id+"F0.wireOp",EDGE,"E1524"),sQuery(id+"F0.wireOp",EDGE,"E1524"),sQuery(id+"F0.wireOp",EDGE,"E1525"),sQuery(id+"F0.wireOp",EDGE,"E1526"),sQuery(id+"F0.wireOp",EDGE,"E1526"),sQuery(id+"F0.wireOp",EDGE,"E1527"),sQuery(id+"F0.wireOp",EDGE,"E1528"),sQuery(id+"F0.wireOp",EDGE,"E1528"),sQuery(id+"F0.wireOp",EDGE,"E1529"),sQuery(id+"F0.wireOp",EDGE,"E1530"),sQuery(id+"F0.wireOp",EDGE,"E1530"),sQuery(id+"F0.wireOp",EDGE,"E1531"),sQuery(id+"F0.wireOp",EDGE,"E1532"),sQuery(id+"F0.wireOp",EDGE,"E1532"),sQuery(id+"F0.wireOp",EDGE,"E1532"),sQuery(id+"F0.wireOp",EDGE,"E1532"),sQuery(id+"F0.wireOp",EDGE,"E1533"),sQuery(id+"F0.wireOp",EDGE,"E1534"),sQuery(id+"F0.wireOp",EDGE,"E1535"),sQuery(id+"F0.wireOp",EDGE,"E1536"),sQuery(id+"F0.wireOp",EDGE,"E1537"),sQuery(id+"F0.wireOp",EDGE,"E1537"),sQuery(id+"F0.wireOp",EDGE,"E1538"),sQuery(id+"F0.wireOp",EDGE,"E1539"),sQuery(id+"F0.wireOp",EDGE,"E1540"),sQuery(id+"F0.wireOp",EDGE,"E1541"),sQuery(id+"F0.wireOp",EDGE,"E1542"),sQuery(id+"F0.wireOp",EDGE,"E1542"),sQuery(id+"F0.wireOp",EDGE,"E1543"),sQuery(id+"F0.wireOp",EDGE,"E1544"),sQuery(id+"F0.wireOp",EDGE,"E1545"),sQuery(id+"F0.wireOp",EDGE,"E1546"),sQuery(id+"F0.wireOp",EDGE,"E1547"),sQuery(id+"F0.wireOp",EDGE,"E1548"),sQuery(id+"F0.wireOp",EDGE,"E1548"),sQuery(id+"F0.wireOp",EDGE,"E1548"),sQuery(id+"F0.wireOp",EDGE,"E1548"),sQuery(id+"F0.wireOp",EDGE,"E1549"),sQuery(id+"F0.wireOp",EDGE,"E1550"),sQuery(id+"F0.wireOp",EDGE,"E1550"),sQuery(id+"F0.wireOp",EDGE,"E1551"),sQuery(id+"F0.wireOp",EDGE,"E1552"),sQuery(id+"F0.wireOp",EDGE,"E1553"),sQuery(id+"F0.wireOp",EDGE,"E1554"),sQuery(id+"F0.wireOp",EDGE,"E1555"),sQuery(id+"F0.wireOp",EDGE,"E1556"),sQuery(id+"F0.wireOp",EDGE,"E1557"),sQuery(id+"F0.wireOp",EDGE,"E1558"),sQuery(id+"F0.wireOp",EDGE,"E1559"),sQuery(id+"F0.wireOp",EDGE,"E1560"),sQuery(id+"F0.wireOp",EDGE,"E1561"),sQuery(id+"F0.wireOp",EDGE,"E1561"),sQuery(id+"F0.wireOp",EDGE,"E1562"),sQuery(id+"F0.wireOp",EDGE,"E1563"),sQuery(id+"F0.wireOp",EDGE,"E1563"),sQuery(id+"F0.wireOp",EDGE,"E1564"),sQuery(id+"F0.wireOp",EDGE,"E1565"),sQuery(id+"F0.wireOp",EDGE,"E1565"),sQuery(id+"F0.wireOp",EDGE,"E1566"),sQuery(id+"F0.wireOp",EDGE,"E1567"),sQuery(id+"F0.wireOp",EDGE,"E1567"),sQuery(id+"F0.wireOp",EDGE,"E1567"),sQuery(id+"F0.wireOp",EDGE,"E1568"),sQuery(id+"F0.wireOp",EDGE,"E1569"),sQuery(id+"F0.wireOp",EDGE,"E1569"),sQuery(id+"F0.wireOp",EDGE,"E1569"),sQuery(id+"F0.wireOp",EDGE,"E1569"),sQuery(id+"F0.wireOp",EDGE,"E1570"),sQuery(id+"F0.wireOp",EDGE,"E1571"),sQuery(id+"F0.wireOp",EDGE,"E1571"),sQuery(id+"F0.wireOp",EDGE,"E1572"),sQuery(id+"F0.wireOp",EDGE,"E1559"),sQuery(id+"F0.wireOp",EDGE,"E1573"),sQuery(id+"F0.wireOp",EDGE,"E1574"),sQuery(id+"F0.wireOp",EDGE,"E1575"),sQuery(id+"F0.wireOp",EDGE,"E1576"),sQuery(id+"F0.wireOp",EDGE,"E1577"),sQuery(id+"F0.wireOp",EDGE,"E1577"),sQuery(id+"F0.wireOp",EDGE,"E1577"),sQuery(id+"F0.wireOp",EDGE,"E1578"),sQuery(id+"F0.wireOp",EDGE,"E1579"),sQuery(id+"F0.wireOp",EDGE,"E1579"),sQuery(id+"F0.wireOp",EDGE,"E1580"),sQuery(id+"F0.wireOp",EDGE,"E1581"),sQuery(id+"F0.wireOp",EDGE,"E1582"),sQuery(id+"F0.wireOp",EDGE,"E1583"),sQuery(id+"F0.wireOp",EDGE,"E1584"),sQuery(id+"F0.wireOp",EDGE,"E1585"),sQuery(id+"F0.wireOp",EDGE,"E1586"),sQuery(id+"F0.wireOp",EDGE,"E1586"),sQuery(id+"F0.wireOp",EDGE,"E1587"),sQuery(id+"F0.wireOp",EDGE,"E1588"),sQuery(id+"F0.wireOp",EDGE,"E1588"),sQuery(id+"F0.wireOp",EDGE,"E1589"),sQuery(id+"F0.wireOp",EDGE,"E1590"),sQuery(id+"F0.wireOp",EDGE,"E1590"),sQuery(id+"F0.wireOp",EDGE,"E1590"),sQuery(id+"F0.wireOp",EDGE,"E1590"),sQuery(id+"F0.wireOp",EDGE,"E1591"),sQuery(id+"F0.wireOp",EDGE,"E1592"),sQuery(id+"F0.wireOp",EDGE,"E1593"),sQuery(id+"F0.wireOp",EDGE,"E1594"),sQuery(id+"F0.wireOp",EDGE,"E1594"),sQuery(id+"F0.wireOp",EDGE,"E1595"),sQuery(id+"F0.wireOp",EDGE,"E1596"),sQuery(id+"F0.wireOp",EDGE,"E1597"),sQuery(id+"F0.wireOp",EDGE,"E1598"),sQuery(id+"F0.wireOp",EDGE,"E1599"),sQuery(id+"F0.wireOp",EDGE,"E1599"),sQuery(id+"F0.wireOp",EDGE,"E1600"),sQuery(id+"F0.wireOp",EDGE,"E1601"),sQuery(id+"F0.wireOp",EDGE,"E1602"),sQuery(id+"F0.wireOp",EDGE,"E1603"),sQuery(id+"F0.wireOp",EDGE,"E1604"),sQuery(id+"F0.wireOp",EDGE,"E1605"),sQuery(id+"F0.wireOp",EDGE,"E1606"),sQuery(id+"F0.wireOp",EDGE,"E1606"),sQuery(id+"F0.wireOp",EDGE,"E1607"),sQuery(id+"F0.wireOp",EDGE,"E1608"),sQuery(id+"F0.wireOp",EDGE,"E1608"),sQuery(id+"F0.wireOp",EDGE,"E1609"),sQuery(id+"F0.wireOp",EDGE,"E1610"),sQuery(id+"F0.wireOp",EDGE,"E1610"),sQuery(id+"F0.wireOp",EDGE,"E1611"),sQuery(id+"F0.wireOp",EDGE,"E1612"),sQuery(id+"F0.wireOp",EDGE,"E1613"),sQuery(id+"F0.wireOp",EDGE,"E1614"),sQuery(id+"F0.wireOp",EDGE,"E1615"),sQuery(id+"F0.wireOp",EDGE,"E1616"),sQuery(id+"F0.wireOp",EDGE,"E1616"),sQuery(id+"F0.wireOp",EDGE,"E1617"),sQuery(id+"F0.wireOp",EDGE,"E1618"),sQuery(id+"F0.wireOp",EDGE,"E1618"),sQuery(id+"F0.wireOp",EDGE,"E1619"),sQuery(id+"F0.wireOp",EDGE,"E1620"),sQuery(id+"F0.wireOp",EDGE,"E1620"),sQuery(id+"F0.wireOp",EDGE,"E1621"),sQuery(id+"F0.wireOp",EDGE,"E1622"),sQuery(id+"F0.wireOp",EDGE,"E1623"),sQuery(id+"F0.wireOp",EDGE,"E1624"),sQuery(id+"F0.wireOp",EDGE,"E1625"),sQuery(id+"F0.wireOp",EDGE,"E1626"),sQuery(id+"F0.wireOp",EDGE,"E1627"),sQuery(id+"F0.wireOp",EDGE,"E1628"),sQuery(id+"F0.wireOp",EDGE,"E1629"),sQuery(id+"F0.wireOp",EDGE,"E1630"),sQuery(id+"F0.wireOp",EDGE,"E1631"),sQuery(id+"F0.wireOp",EDGE,"E1632"),sQuery(id+"F0.wireOp",EDGE,"E1633"),sQuery(id+"F0.wireOp",EDGE,"E1634"),sQuery(id+"F0.wireOp",EDGE,"E1635"),sQuery(id+"F0.wireOp",EDGE,"E1635"),sQuery(id+"F0.wireOp",EDGE,"E1636"),sQuery(id+"F0.wireOp",EDGE,"E1637"),sQuery(id+"F0.wireOp",EDGE,"E1637"),sQuery(id+"F0.wireOp",EDGE,"E1638"),sQuery(id+"F0.wireOp",EDGE,"E1639"),sQuery(id+"F0.wireOp",EDGE,"E1639"),sQuery(id+"F0.wireOp",EDGE,"E1640"),sQuery(id+"F0.wireOp",EDGE,"E1641"),sQuery(id+"F0.wireOp",EDGE,"E1655"),sQuery(id+"F0.wireOp",EDGE,"E1656"),sQuery(id+"F0.wireOp",EDGE,"E1657"),sQuery(id+"F0.wireOp",EDGE,"E1658"),sQuery(id+"F0.wireOp",EDGE,"E1659"),sQuery(id+"F0.wireOp",EDGE,"E1660"),sQuery(id+"F0.wireOp",EDGE,"E1661"),sQuery(id+"F0.wireOp",EDGE,"E1662"),sQuery(id+"F0.wireOp",EDGE,"E1663"),sQuery(id+"F0.wireOp",EDGE,"E1664"),sQuery(id+"F0.wireOp",EDGE,"E1665"),sQuery(id+"F0.wireOp",EDGE,"E1666"),sQuery(id+"F0.wireOp",EDGE,"E1667"),sQuery(id+"F0.wireOp",EDGE,"E1668"),sQuery(id+"F0.wireOp",EDGE,"E1669"),sQuery(id+"F0.wireOp",EDGE,"E1670"),sQuery(id+"F0.wireOp",EDGE,"E1670"),sQuery(id+"F0.wireOp",EDGE,"E1671"),sQuery(id+"F0.wireOp",EDGE,"E1672"),sQuery(id+"F0.wireOp",EDGE,"E1672"),sQuery(id+"F0.wireOp",EDGE,"E1673"),sQuery(id+"F0.wireOp",EDGE,"E1674"),sQuery(id+"F0.wireOp",EDGE,"E1674"),sQuery(id+"F0.wireOp",EDGE,"E1675"),sQuery(id+"F0.wireOp",EDGE,"E1676"),sQuery(id+"F0.wireOp",EDGE,"E1677"),sQuery(id+"F0.wireOp",EDGE,"E1678"),sQuery(id+"F0.wireOp",EDGE,"E1679"),sQuery(id+"F0.wireOp",EDGE,"E1680"),sQuery(id+"F0.wireOp",EDGE,"E1681"),sQuery(id+"F0.wireOp",EDGE,"E1682"),sQuery(id+"F0.wireOp",EDGE,"E1683"),sQuery(id+"F0.wireOp",EDGE,"E1684"),sQuery(id+"F0.wireOp",EDGE,"E1684"),sQuery(id+"F0.wireOp",EDGE,"E1685"),sQuery(id+"F0.wireOp",EDGE,"E1686"),sQuery(id+"F0.wireOp",EDGE,"E1686"),sQuery(id+"F0.wireOp",EDGE,"E1687"),sQuery(id+"F0.wireOp",EDGE,"E1688"),sQuery(id+"F0.wireOp",EDGE,"E1688"),sQuery(id+"F0.wireOp",EDGE,"E1689"),sQuery(id+"F0.wireOp",EDGE,"E1690"),sQuery(id+"F0.wireOp",EDGE,"E1690"),sQuery(id+"F0.wireOp",EDGE,"E1691"),sQuery(id+"F0.wireOp",EDGE,"E1692"),sQuery(id+"F0.wireOp",EDGE,"E1692"),sQuery(id+"F0.wireOp",EDGE,"E1693"),sQuery(id+"F0.wireOp",EDGE,"E1694"),sQuery(id+"F0.wireOp",EDGE,"E1695"),sQuery(id+"F0.wireOp",EDGE,"E1696"),sQuery(id+"F0.wireOp",EDGE,"E1697"),sQuery(id+"F0.wireOp",EDGE,"E1697"),sQuery(id+"F0.wireOp",EDGE,"E1698"),sQuery(id+"F0.wireOp",EDGE,"E1699"),sQuery(id+"F0.wireOp",EDGE,"E1700"),sQuery(id+"F0.wireOp",EDGE,"E1701"),sQuery(id+"F0.wireOp",EDGE,"E1702"),sQuery(id+"F0.wireOp",EDGE,"E1703"),sQuery(id+"F0.wireOp",EDGE,"E1704"),sQuery(id+"F0.wireOp",EDGE,"E1705"),sQuery(id+"F0.wireOp",EDGE,"E1706"),sQuery(id+"F0.wireOp",EDGE,"E1706"),sQuery(id+"F0.wireOp",EDGE,"E1707"),sQuery(id+"F0.wireOp",EDGE,"E1708"),sQuery(id+"F0.wireOp",EDGE,"E1708"),sQuery(id+"F0.wireOp",EDGE,"E1709"),sQuery(id+"F0.wireOp",EDGE,"E1710"),sQuery(id+"F0.wireOp",EDGE,"E1710"),sQuery(id+"F0.wireOp",EDGE,"E1711"),sQuery(id+"F0.wireOp",EDGE,"E1712"),sQuery(id+"F0.wireOp",EDGE,"E1712"),sQuery(id+"F0.wireOp",EDGE,"E1712"),sQuery(id+"F0.wireOp",EDGE,"E1713"),sQuery(id+"F0.wireOp",EDGE,"E1714"),sQuery(id+"F0.wireOp",EDGE,"E1714"),sQuery(id+"F0.wireOp",EDGE,"E1715"),sQuery(id+"F0.wireOp",EDGE,"E1716"),sQuery(id+"F0.wireOp",EDGE,"E1716"),sQuery(id+"F0.wireOp",EDGE,"E1717"),sQuery(id+"F0.wireOp",EDGE,"E1718"),sQuery(id+"F0.wireOp",EDGE,"E1718"),sQuery(id+"F0.wireOp",EDGE,"E1719"),sQuery(id+"F0.wireOp",EDGE,"E1720"),sQuery(id+"F0.wireOp",EDGE,"E1720"),sQuery(id+"F0.wireOp",EDGE,"E1721"),sQuery(id+"F0.wireOp",EDGE,"E1722"),sQuery(id+"F0.wireOp",EDGE,"E1723"),sQuery(id+"F0.wireOp",EDGE,"E1724"),sQuery(id+"F0.wireOp",EDGE,"E1725"),sQuery(id+"F0.wireOp",EDGE,"E1726"),sQuery(id+"F0.wireOp",EDGE,"E1727"),sQuery(id+"F0.wireOp",EDGE,"E1728"),sQuery(id+"F0.wireOp",EDGE,"E1729"),sQuery(id+"F0.wireOp",EDGE,"E1730"),sQuery(id+"F0.wireOp",EDGE,"E1731"),sQuery(id+"F0.wireOp",EDGE,"E1731"),sQuery(id+"F0.wireOp",EDGE,"E1732"),sQuery(id+"F0.wireOp",EDGE,"E1733"),sQuery(id+"F0.wireOp",EDGE,"E1733"),sQuery(id+"F0.wireOp",EDGE,"E1733"),sQuery(id+"F0.wireOp",EDGE,"E1734"),sQuery(id+"F0.wireOp",EDGE,"E1735"),sQuery(id+"F0.wireOp",EDGE,"E1735"),sQuery(id+"F0.wireOp",EDGE,"E1735"),sQuery(id+"F0.wireOp",EDGE,"E1735"),sQuery(id+"F0.wireOp",EDGE,"E1736"),sQuery(id+"F0.wireOp",EDGE,"E1737"),sQuery(id+"F0.wireOp",EDGE,"E1738"),sQuery(id+"F0.wireOp",EDGE,"E1739"),sQuery(id+"F0.wireOp",EDGE,"E1739"),sQuery(id+"F0.wireOp",EDGE,"E1740"),sQuery(id+"F0.wireOp",EDGE,"E1741"),sQuery(id+"F0.wireOp",EDGE,"E1742"),sQuery(id+"F0.wireOp",EDGE,"E1742"),sQuery(id+"F0.wireOp",EDGE,"E1742"),sQuery(id+"F0.wireOp",EDGE,"E1742"),sQuery(id+"F0.wireOp",EDGE,"E1743"),sQuery(id+"F0.wireOp",EDGE,"E1744"),sQuery(id+"F0.wireOp",EDGE,"E1745"),sQuery(id+"F0.wireOp",EDGE,"E1746"),sQuery(id+"F0.wireOp",EDGE,"E1746"),sQuery(id+"F0.wireOp",EDGE,"E1746"),sQuery(id+"F0.wireOp",EDGE,"E1746"),sQuery(id+"F0.wireOp",EDGE,"E1747"),sQuery(id+"F0.wireOp",EDGE,"E1748"),sQuery(id+"F0.wireOp",EDGE,"E1748"),sQuery(id+"F0.wireOp",EDGE,"E1749"),sQuery(id+"F0.wireOp",EDGE,"E1750"),sQuery(id+"F0.wireOp",EDGE,"E1750"),sQuery(id+"F0.wireOp",EDGE,"E1751"),sQuery(id+"F0.wireOp",EDGE,"E1752"),sQuery(id+"F0.wireOp",EDGE,"E1753"),sQuery(id+"F0.wireOp",EDGE,"E1754"),sQuery(id+"F0.wireOp",EDGE,"E1755"),sQuery(id+"F0.wireOp",EDGE,"E1756"),sQuery(id+"F0.wireOp",EDGE,"E1756"),sQuery(id+"F0.wireOp",EDGE,"E1757"),sQuery(id+"F0.wireOp",EDGE,"E1758"),sQuery(id+"F0.wireOp",EDGE,"E1758"),sQuery(id+"F0.wireOp",EDGE,"E1759"),sQuery(id+"F0.wireOp",EDGE,"E1760"),sQuery(id+"F0.wireOp",EDGE,"E1760"),sQuery(id+"F0.wireOp",EDGE,"E1761"),sQuery(id+"F0.wireOp",EDGE,"E1762"),sQuery(id+"F0.wireOp",EDGE,"E1763"),sQuery(id+"F0.wireOp",EDGE,"E1764"),sQuery(id+"F0.wireOp",EDGE,"E1765"),sQuery(id+"F0.wireOp",EDGE,"E1766"),sQuery(id+"F0.wireOp",EDGE,"E1767"),sQuery(id+"F0.wireOp",EDGE,"E1768"),sQuery(id+"F0.wireOp",EDGE,"E1768"),sQuery(id+"F0.wireOp",EDGE,"E1768"),sQuery(id+"F0.wireOp",EDGE,"E1769"),sQuery(id+"F0.wireOp",EDGE,"E1770"),sQuery(id+"F0.wireOp",EDGE,"E1770"),sQuery(id+"F0.wireOp",EDGE,"E1770"),sQuery(id+"F0.wireOp",EDGE,"E1770"),sQuery(id+"F0.wireOp",EDGE,"E1783"),sQuery(id+"F0.wireOp",EDGE,"E1784"),sQuery(id+"F0.wireOp",EDGE,"E1785"),sQuery(id+"F0.wireOp",EDGE,"E1786"),sQuery(id+"F0.wireOp",EDGE,"E1787"),sQuery(id+"F0.wireOp",EDGE,"E1788"),sQuery(id+"F0.wireOp",EDGE,"E1789"),sQuery(id+"F0.wireOp",EDGE,"E1790"),sQuery(id+"F0.wireOp",EDGE,"E1791"),sQuery(id+"F0.wireOp",EDGE,"E1792"),sQuery(id+"F0.wireOp",EDGE,"E1793"),sQuery(id+"F0.wireOp",EDGE,"E1794"),sQuery(id+"F0.wireOp",EDGE,"E1795"),sQuery(id+"F0.wireOp",EDGE,"E1796"),sQuery(id+"F0.wireOp",EDGE,"E1797"),sQuery(id+"F0.wireOp",EDGE,"E1798"),sQuery(id+"F0.wireOp",EDGE,"E1798"),sQuery(id+"F0.wireOp",EDGE,"E1799"),sQuery(id+"F0.wireOp",EDGE,"E1800"),sQuery(id+"F0.wireOp",EDGE,"E1800"),sQuery(id+"F0.wireOp",EDGE,"E1800"),sQuery(id+"F0.wireOp",EDGE,"E1801"),sQuery(id+"F0.wireOp",EDGE,"E1802"),sQuery(id+"F0.wireOp",EDGE,"E1802"),sQuery(id+"F0.wireOp",EDGE,"E1802"),sQuery(id+"F0.wireOp",EDGE,"E1803"),sQuery(id+"F0.wireOp",EDGE,"E1804"),sQuery(id+"F0.wireOp",EDGE,"E1804"),sQuery(id+"F0.wireOp",EDGE,"E1805"),sQuery(id+"F0.wireOp",EDGE,"E1806"),sQuery(id+"F0.wireOp",EDGE,"E1806"),sQuery(id+"F0.wireOp",EDGE,"E1807"),sQuery(id+"F0.wireOp",EDGE,"E1808"),sQuery(id+"F0.wireOp",EDGE,"E1808"),sQuery(id+"F0.wireOp",EDGE,"E1808"),sQuery(id+"F0.wireOp",EDGE,"E1808"),sQuery(id+"F0.wireOp",EDGE,"E1808"),sQuery(id+"F0.wireOp",EDGE,"E1809"),sQuery(id+"F0.wireOp",EDGE,"E1810"),sQuery(id+"F0.wireOp",EDGE,"E1810"),sQuery(id+"F0.wireOp",EDGE,"E1811"),sQuery(id+"F0.wireOp",EDGE,"E1812"),sQuery(id+"F0.wireOp",EDGE,"E1812"),sQuery(id+"F0.wireOp",EDGE,"E1813"),sQuery(id+"F0.wireOp",EDGE,"E1814"),sQuery(id+"F0.wireOp",EDGE,"E1814"),sQuery(id+"F0.wireOp",EDGE,"E1815"),sQuery(id+"F0.wireOp",EDGE,"E1816"),sQuery(id+"F0.wireOp",EDGE,"E1816"),sQuery(id+"F0.wireOp",EDGE,"E1817"),sQuery(id+"F0.wireOp",EDGE,"E1818"),sQuery(id+"F0.wireOp",EDGE,"E1818"),sQuery(id+"F0.wireOp",EDGE,"E1819"),sQuery(id+"F0.wireOp",EDGE,"E1820"),sQuery(id+"F0.wireOp",EDGE,"E1821"),sQuery(id+"F0.wireOp",EDGE,"E1822"),sQuery(id+"F0.wireOp",EDGE,"E1823"),sQuery(id+"F0.wireOp",EDGE,"E1824"),sQuery(id+"F0.wireOp",EDGE,"E1825"),sQuery(id+"F0.wireOp",EDGE,"E1825"),sQuery(id+"F0.wireOp",EDGE,"E1825"),sQuery(id+"F0.wireOp",EDGE,"E1825"),sQuery(id+"F0.wireOp",EDGE,"E1826"),sQuery(id+"F0.wireOp",EDGE,"E1827"),sQuery(id+"F0.wireOp",EDGE,"E1827"),sQuery(id+"F0.wireOp",EDGE,"E1828"),sQuery(id+"F0.wireOp",EDGE,"E1829"),sQuery(id+"F0.wireOp",EDGE,"E1830"),sQuery(id+"F0.wireOp",EDGE,"E1830"),sQuery(id+"F0.wireOp",EDGE,"E1830"),sQuery(id+"F0.wireOp",EDGE,"E1831"),sQuery(id+"F0.wireOp",EDGE,"E1832"),sQuery(id+"F0.wireOp",EDGE,"E1833"),sQuery(id+"F0.wireOp",EDGE,"E1834"),sQuery(id+"F0.wireOp",EDGE,"E1835"),sQuery(id+"F0.wireOp",EDGE,"E1835"),sQuery(id+"F0.wireOp",EDGE,"E1836"),sQuery(id+"F0.wireOp",EDGE,"E1837"),sQuery(id+"F0.wireOp",EDGE,"E1837"),sQuery(id+"F0.wireOp",EDGE,"E1837"),sQuery(id+"F0.wireOp",EDGE,"E1837"),sQuery(id+"F0.wireOp",EDGE,"E1837"),sQuery(id+"F0.wireOp",EDGE,"E1838"),sQuery(id+"F0.wireOp",EDGE,"E1839"),sQuery(id+"F0.wireOp",EDGE,"E1840"),sQuery(id+"F0.wireOp",EDGE,"E1841"),sQuery(id+"F0.wireOp",EDGE,"E1842"),sQuery(id+"F0.wireOp",EDGE,"E1842"),sQuery(id+"F0.wireOp",EDGE,"E1842"),sQuery(id+"F0.wireOp",EDGE,"E1842"),sQuery(id+"F0.wireOp",EDGE,"E1843"),sQuery(id+"F0.wireOp",EDGE,"E1844"),sQuery(id+"F0.wireOp",EDGE,"E1845"),sQuery(id+"F0.wireOp",EDGE,"E1846"),sQuery(id+"F0.wireOp",EDGE,"E1846"),sQuery(id+"F0.wireOp",EDGE,"E1846"),sQuery(id+"F0.wireOp",EDGE,"E1846"),sQuery(id+"F0.wireOp",EDGE,"E1847"),sQuery(id+"F0.wireOp",EDGE,"E1848"),sQuery(id+"F0.wireOp",EDGE,"E1848"),sQuery(id+"F0.wireOp",EDGE,"E1848"),sQuery(id+"F0.wireOp",EDGE,"E1848"),sQuery(id+"F0.wireOp",EDGE,"E1849"),sQuery(id+"F0.wireOp",EDGE,"E1850"),sQuery(id+"F0.wireOp",EDGE,"E1850"),sQuery(id+"F0.wireOp",EDGE,"E1851"),sQuery(id+"F0.wireOp",EDGE,"E1852"),sQuery(id+"F0.wireOp",EDGE,"E1853"),sQuery(id+"F0.wireOp",EDGE,"E1854"),sQuery(id+"F0.wireOp",EDGE,"E1855"),sQuery(id+"F0.wireOp",EDGE,"E1871"),sQuery(id+"F0.wireOp",EDGE,"E1872"),sQuery(id+"F0.wireOp",EDGE,"E1873"),sQuery(id+"F0.wireOp",EDGE,"E1874"),sQuery(id+"F0.wireOp",EDGE,"E1875"),sQuery(id+"F0.wireOp",EDGE,"E1876"),sQuery(id+"F0.wireOp",EDGE,"E1877"),sQuery(id+"F0.wireOp",EDGE,"E1878"),sQuery(id+"F0.wireOp",EDGE,"E1879"),sQuery(id+"F0.wireOp",EDGE,"E1880"),sQuery(id+"F0.wireOp",EDGE,"E1881"),sQuery(id+"F0.wireOp",EDGE,"E1882"),sQuery(id+"F0.wireOp",EDGE,"E1883"),sQuery(id+"F0.wireOp",EDGE,"E1884"),sQuery(id+"F0.wireOp",EDGE,"E1885"),sQuery(id+"F0.wireOp",EDGE,"E1886"),sQuery(id+"F0.wireOp",EDGE,"E1886"),sQuery(id+"F0.wireOp",EDGE,"E1887"),sQuery(id+"F0.wireOp",EDGE,"E1888"),sQuery(id+"F0.wireOp",EDGE,"E1888"),sQuery(id+"F0.wireOp",EDGE,"E1888"),sQuery(id+"F0.wireOp",EDGE,"E1888"),sQuery(id+"F0.wireOp",EDGE,"E1888"),sQuery(id+"F0.wireOp",EDGE,"E1889"),sQuery(id+"F0.wireOp",EDGE,"E1890"),sQuery(id+"F0.wireOp",EDGE,"E1891"),sQuery(id+"F0.wireOp",EDGE,"E1892"),sQuery(id+"F0.wireOp",EDGE,"E1893"),sQuery(id+"F0.wireOp",EDGE,"E1894"),sQuery(id+"F0.wireOp",EDGE,"E1895"),sQuery(id+"F0.wireOp",EDGE,"E1895"),sQuery(id+"F0.wireOp",EDGE,"E1896"),sQuery(id+"F0.wireOp",EDGE,"E1897"),sQuery(id+"F0.wireOp",EDGE,"E1897"),sQuery(id+"F0.wireOp",EDGE,"E1898"),sQuery(id+"F0.wireOp",EDGE,"E1899"),sQuery(id+"F0.wireOp",EDGE,"E1899"),sQuery(id+"F0.wireOp",EDGE,"E1900"),sQuery(id+"F0.wireOp",EDGE,"E1901"),sQuery(id+"F0.wireOp",EDGE,"E1901"),sQuery(id+"F0.wireOp",EDGE,"E1902"),sQuery(id+"F0.wireOp",EDGE,"E1903"),sQuery(id+"F0.wireOp",EDGE,"E1903"),sQuery(id+"F0.wireOp",EDGE,"E1904"),sQuery(id+"F0.wireOp",EDGE,"E1905"),sQuery(id+"F0.wireOp",EDGE,"E1905"),sQuery(id+"F0.wireOp",EDGE,"E1906"),sQuery(id+"F0.wireOp",EDGE,"E1907"),sQuery(id+"F0.wireOp",EDGE,"E1908"),sQuery(id+"F0.wireOp",EDGE,"E1909"),sQuery(id+"F0.wireOp",EDGE,"E1910"),sQuery(id+"F0.wireOp",EDGE,"E1910"),sQuery(id+"F0.wireOp",EDGE,"E1911"),sQuery(id+"F0.wireOp",EDGE,"E1912"),sQuery(id+"F0.wireOp",EDGE,"E1912"),sQuery(id+"F0.wireOp",EDGE,"E1913"),sQuery(id+"F0.wireOp",EDGE,"E1914"),sQuery(id+"F0.wireOp",EDGE,"E1927"),sQuery(id+"F0.wireOp",EDGE,"E1928"),sQuery(id+"F0.wireOp",EDGE,"E1929"),sQuery(id+"F0.wireOp",EDGE,"E1929"),sQuery(id+"F0.wireOp",EDGE,"E1930"),sQuery(id+"F0.wireOp",EDGE,"E1931"),sQuery(id+"F0.wireOp",EDGE,"E1932"),sQuery(id+"F0.wireOp",EDGE,"E1933"),sQuery(id+"F0.wireOp",EDGE,"E1933"),sQuery(id+"F0.wireOp",EDGE,"E1934"),sQuery(id+"F0.wireOp",EDGE,"E1935"),sQuery(id+"F0.wireOp",EDGE,"E1935"),sQuery(id+"F0.wireOp",EDGE,"E1936"),sQuery(id+"F0.wireOp",EDGE,"E1937"),sQuery(id+"F0.wireOp",EDGE,"E1938"),sQuery(id+"F0.wireOp",EDGE,"E1939"),sQuery(id+"F0.wireOp",EDGE,"E1940"),sQuery(id+"F0.wireOp",EDGE,"E1941"),sQuery(id+"F0.wireOp",EDGE,"E1942"),sQuery(id+"F0.wireOp",EDGE,"E1943"),sQuery(id+"F0.wireOp",EDGE,"E1943"),sQuery(id+"F0.wireOp",EDGE,"E1944"),sQuery(id+"F0.wireOp",EDGE,"E1945"),sQuery(id+"F0.wireOp",EDGE,"E1946"),sQuery(id+"F0.wireOp",EDGE,"E1947"),sQuery(id+"F0.wireOp",EDGE,"E1948"),sQuery(id+"F0.wireOp",EDGE,"E1948"),sQuery(id+"F0.wireOp",EDGE,"E1949"),sQuery(id+"F0.wireOp",EDGE,"E1950"),sQuery(id+"F0.wireOp",EDGE,"E1951"),sQuery(id+"F0.wireOp",EDGE,"E1952"),sQuery(id+"F0.wireOp",EDGE,"E1953"),sQuery(id+"F0.wireOp",EDGE,"E1954"),sQuery(id+"F0.wireOp",EDGE,"E1955"),sQuery(id+"F0.wireOp",EDGE,"E1956"),sQuery(id+"F0.wireOp",EDGE,"E1957"),sQuery(id+"F0.wireOp",EDGE,"E1958"),sQuery(id+"F0.wireOp",EDGE,"E1959"),sQuery(id+"F0.wireOp",EDGE,"E1960"),sQuery(id+"F0.wireOp",EDGE,"E1961"),sQuery(id+"F0.wireOp",EDGE,"E1962"),sQuery(id+"F0.wireOp",EDGE,"E1963"),sQuery(id+"F0.wireOp",EDGE,"E1963"),sQuery(id+"F0.wireOp",EDGE,"E1964"),sQuery(id+"F0.wireOp",EDGE,"E1965"),sQuery(id+"F0.wireOp",EDGE,"E1966"),sQuery(id+"F0.wireOp",EDGE,"E1967"),sQuery(id+"F0.wireOp",EDGE,"E1968"),sQuery(id+"F0.wireOp",EDGE,"E1968"),sQuery(id+"F0.wireOp",EDGE,"E1968"),sQuery(id+"F0.wireOp",EDGE,"E1968"),sQuery(id+"F0.wireOp",EDGE,"E1968"),sQuery(id+"F0.wireOp",EDGE,"E1968"),sQuery(id+"F0.wireOp",EDGE,"E1969"),sQuery(id+"F0.wireOp",EDGE,"E1970"),sQuery(id+"F0.wireOp",EDGE,"E1971"),sQuery(id+"F0.wireOp",EDGE,"E1972"),sQuery(id+"F0.wireOp",EDGE,"E1973"),sQuery(id+"F0.wireOp",EDGE,"E1974"),sQuery(id+"F0.wireOp",EDGE,"E1975"),sQuery(id+"F0.wireOp",EDGE,"E1976"),sQuery(id+"F0.wireOp",EDGE,"E1977"),sQuery(id+"F0.wireOp",EDGE,"E1978"),sQuery(id+"F0.wireOp",EDGE,"E1978"),sQuery(id+"F0.wireOp",EDGE,"E1978"),sQuery(id+"F0.wireOp",EDGE,"E1978"),sQuery(id+"F0.wireOp",EDGE,"E1978"),sQuery(id+"F0.wireOp",EDGE,"E1979"),sQuery(id+"F0.wireOp",EDGE,"E1980"),sQuery(id+"F0.wireOp",EDGE,"E1981"),sQuery(id+"F0.wireOp",EDGE,"E1982"),sQuery(id+"F0.wireOp",EDGE,"E1982"),sQuery(id+"F0.wireOp",EDGE,"E1982"),sQuery(id+"F0.wireOp",EDGE,"E1982"),sQuery(id+"F0.wireOp",EDGE,"E1983"),sQuery(id+"F0.wireOp",EDGE,"E1984"),sQuery(id+"F0.wireOp",EDGE,"E1985"),sQuery(id+"F0.wireOp",EDGE,"E1986"),sQuery(id+"F0.wireOp",EDGE,"E1987"),sQuery(id+"F0.wireOp",EDGE,"E1988"),sQuery(id+"F0.wireOp",EDGE,"E1989"),sQuery(id+"F0.wireOp",EDGE,"E1989"),sQuery(id+"F0.wireOp",EDGE,"E1990"),sQuery(id+"F0.wireOp",EDGE,"E1991"),sQuery(id+"F0.wireOp",EDGE,"E1991"),sQuery(id+"F0.wireOp",EDGE,"E1992"),sQuery(id+"F0.wireOp",EDGE,"E1993"),sQuery(id+"F0.wireOp",EDGE,"E1994"),sQuery(id+"F0.wireOp",EDGE,"E1995"),sQuery(id+"F0.wireOp",EDGE,"E1996"),sQuery(id+"F0.wireOp",EDGE,"E1997"),sQuery(id+"F0.wireOp",EDGE,"E1997"),sQuery(id+"F0.wireOp",EDGE,"E1998"),sQuery(id+"F0.wireOp",EDGE,"E1999"),sQuery(id+"F0.wireOp",EDGE,"E2000"),sQuery(id+"F0.wireOp",EDGE,"E2000"),sQuery(id+"F0.wireOp",EDGE,"E2000"),sQuery(id+"F0.wireOp",EDGE,"E2001"),sQuery(id+"F0.wireOp",EDGE,"E2002"),sQuery(id+"F0.wireOp",EDGE,"E2002"),sQuery(id+"F0.wireOp",EDGE,"E2003"),sQuery(id+"F0.wireOp",EDGE,"E2004"),sQuery(id+"F0.wireOp",EDGE,"E2005"),sQuery(id+"F0.wireOp",EDGE,"E2006"),sQuery(id+"F0.wireOp",EDGE,"E2006"),sQuery(id+"F0.wireOp",EDGE,"E2007"),sQuery(id+"F0.wireOp",EDGE,"E2008"),sQuery(id+"F0.wireOp",EDGE,"E2008"),sQuery(id+"F0.wireOp",EDGE,"E2009"),sQuery(id+"F0.wireOp",EDGE,"E2010"),sQuery(id+"F0.wireOp",EDGE,"E2010"),sQuery(id+"F0.wireOp",EDGE,"E2011"),sQuery(id+"F0.wireOp",EDGE,"E2012"),sQuery(id+"F0.wireOp",EDGE,"E2013"),sQuery(id+"F0.wireOp",EDGE,"E2014"),sQuery(id+"F0.wireOp",EDGE,"E2015"),sQuery(id+"F0.wireOp",EDGE,"E2015"),sQuery(id+"F0.wireOp",EDGE,"E2015"),sQuery(id+"F0.wireOp",EDGE,"E2015"),sQuery(id+"F0.wireOp",EDGE,"E2016"),sQuery(id+"F0.wireOp",EDGE,"E2017"),sQuery(id+"F0.wireOp",EDGE,"E2017"),sQuery(id+"F0.wireOp",EDGE,"E2017"),sQuery(id+"F0.wireOp",EDGE,"E2018"),sQuery(id+"F0.wireOp",EDGE,"E2019"),sQuery(id+"F0.wireOp",EDGE,"E2020"),sQuery(id+"F0.wireOp",EDGE,"E2020"),sQuery(id+"F0.wireOp",EDGE,"E2020"),sQuery(id+"F0.wireOp",EDGE,"E2020"),sQuery(id+"F0.wireOp",EDGE,"E2021"),sQuery(id+"F0.wireOp",EDGE,"E2022"),sQuery(id+"F0.wireOp",EDGE,"E2023"),sQuery(id+"F0.wireOp",EDGE,"E2024"),sQuery(id+"F0.wireOp",EDGE,"E2025"),sQuery(id+"F0.wireOp",EDGE,"E2026"),sQuery(id+"F0.wireOp",EDGE,"E2027"),sQuery(id+"F0.wireOp",EDGE,"E2027"),sQuery(id+"F0.wireOp",EDGE,"E2028"),sQuery(id+"F0.wireOp",EDGE,"E2013"),sQuery(id+"F0.wireOp",EDGE,"E2029"),sQuery(id+"F0.wireOp",EDGE,"E2030"),sQuery(id+"F0.wireOp",EDGE,"E2031"),sQuery(id+"F0.wireOp",EDGE,"E2032"),sQuery(id+"F0.wireOp",EDGE,"E2032"),sQuery(id+"F0.wireOp",EDGE,"E2033"),sQuery(id+"F0.wireOp",EDGE,"E2034"),sQuery(id+"F0.wireOp",EDGE,"E2034"),sQuery(id+"F0.wireOp",EDGE,"E2034"),sQuery(id+"F0.wireOp",EDGE,"E2035"),sQuery(id+"F0.wireOp",EDGE,"E2036"),sQuery(id+"F0.wireOp",EDGE,"E2036"),sQuery(id+"F0.wireOp",EDGE,"E2036"),sQuery(id+"F0.wireOp",EDGE,"E2037"),sQuery(id+"F0.wireOp",EDGE,"E2038"),sQuery(id+"F0.wireOp",EDGE,"E2039"),sQuery(id+"F0.wireOp",EDGE,"E2040"),sQuery(id+"F0.wireOp",EDGE,"E2041"),sQuery(id+"F0.wireOp",EDGE,"E2042"),sQuery(id+"F0.wireOp",EDGE,"E2043"),sQuery(id+"F0.wireOp",EDGE,"E2043"),sQuery(id+"F0.wireOp",EDGE,"E2044"),sQuery(id+"F0.wireOp",EDGE,"E2045"),sQuery(id+"F0.wireOp",EDGE,"E2046"),sQuery(id+"F0.wireOp",EDGE,"E2047"),sQuery(id+"F0.wireOp",EDGE,"E2048"),sQuery(id+"F0.wireOp",EDGE,"E2048"),sQuery(id+"F0.wireOp",EDGE,"E2049"),sQuery(id+"F0.wireOp",EDGE,"E2050"),sQuery(id+"F0.wireOp",EDGE,"E2050"),sQuery(id+"F0.wireOp",EDGE,"E2051"),sQuery(id+"F0.wireOp",EDGE,"E2052"),sQuery(id+"F0.wireOp",EDGE,"E2053"),sQuery(id+"F0.wireOp",EDGE,"E2054"),sQuery(id+"F0.wireOp",EDGE,"E2055"),sQuery(id+"F0.wireOp",EDGE,"E2056"),sQuery(id+"F0.wireOp",EDGE,"E2057"),sQuery(id+"F0.wireOp",EDGE,"E2058"),sQuery(id+"F0.wireOp",EDGE,"E2059"),sQuery(id+"F0.wireOp",EDGE,"E2059"),sQuery(id+"F0.wireOp",EDGE,"E2059"),sQuery(id+"F0.wireOp",EDGE,"E2060"),sQuery(id+"F0.wireOp",EDGE,"E2061"),sQuery(id+"F0.wireOp",EDGE,"E2062"),sQuery(id+"F0.wireOp",EDGE,"E2063"),sQuery(id+"F0.wireOp",EDGE,"E2063"),sQuery(id+"F0.wireOp",EDGE,"E2064"),sQuery(id+"F0.wireOp",EDGE,"E2065"),sQuery(id+"F0.wireOp",EDGE,"E2066"),sQuery(id+"F0.wireOp",EDGE,"E2067"),sQuery(id+"F0.wireOp",EDGE,"E2068"),sQuery(id+"F0.wireOp",EDGE,"E2069"),sQuery(id+"F0.wireOp",EDGE,"E2069"),sQuery(id+"F0.wireOp",EDGE,"E2070"),sQuery(id+"F0.wireOp",EDGE,"E2071"),sQuery(id+"F0.wireOp",EDGE,"E2071"),sQuery(id+"F0.wireOp",EDGE,"E2072"),sQuery(id+"F0.wireOp",EDGE,"E2073"),sQuery(id+"F0.wireOp",EDGE,"E2073"),sQuery(id+"F0.wireOp",EDGE,"E2074"),sQuery(id+"F0.wireOp",EDGE,"E2075"),sQuery(id+"F0.wireOp",EDGE,"E2076"),sQuery(id+"F0.wireOp",EDGE,"E2077"),sQuery(id+"F0.wireOp",EDGE,"E2078"),sQuery(id+"F0.wireOp",EDGE,"E2079"),sQuery(id+"F0.wireOp",EDGE,"E2079"),sQuery(id+"F0.wireOp",EDGE,"E2080"),sQuery(id+"F0.wireOp",EDGE,"E2081"),sQuery(id+"F0.wireOp",EDGE,"E2081"),sQuery(id+"F0.wireOp",EDGE,"E2082"),sQuery(id+"F0.wireOp",EDGE,"E2083"),sQuery(id+"F0.wireOp",EDGE,"E2083"),sQuery(id+"F0.wireOp",EDGE,"E2084"),sQuery(id+"F0.wireOp",EDGE,"E2085"),sQuery(id+"F0.wireOp",EDGE,"E2086"),sQuery(id+"F0.wireOp",EDGE,"E2087"),sQuery(id+"F0.wireOp",EDGE,"E2088"),sQuery(id+"F0.wireOp",EDGE,"E2089"),sQuery(id+"F0.wireOp",EDGE,"E2089"),sQuery(id+"F0.wireOp",EDGE,"E2090"),sQuery(id+"F0.wireOp",EDGE,"E2091"),sQuery(id+"F0.wireOp",EDGE,"E2091"),sQuery(id+"F0.wireOp",EDGE,"E2092"),sQuery(id+"F0.wireOp",EDGE,"E2093"),sQuery(id+"F0.wireOp",EDGE,"E2093"),sQuery(id+"F0.wireOp",EDGE,"E2094"),sQuery(id+"F0.wireOp",EDGE,"E2095"),sQuery(id+"F0.wireOp",EDGE,"E2096"),sQuery(id+"F0.wireOp",EDGE,"E2097"),sQuery(id+"F0.wireOp",EDGE,"E2098"),sQuery(id+"F0.wireOp",EDGE,"E2099"),sQuery(id+"F0.wireOp",EDGE,"E2099"),sQuery(id+"F0.wireOp",EDGE,"E2100"),sQuery(id+"F0.wireOp",EDGE,"E2101"),sQuery(id+"F0.wireOp",EDGE,"E2101"),sQuery(id+"F0.wireOp",EDGE,"E2102"),sQuery(id+"F0.wireOp",EDGE,"E2103"),sQuery(id+"F0.wireOp",EDGE,"E2103"),sQuery(id+"F0.wireOp",EDGE,"E2103"),sQuery(id+"F0.wireOp",EDGE,"E2103"),sQuery(id+"F0.wireOp",EDGE,"E2104"),sQuery(id+"F0.wireOp",EDGE,"E2105"),sQuery(id+"F0.wireOp",EDGE,"E2106"),sQuery(id+"F0.wireOp",EDGE,"E2107"),sQuery(id+"F0.wireOp",EDGE,"E2107"),sQuery(id+"F0.wireOp",EDGE,"E2108"),sQuery(id+"F0.wireOp",EDGE,"E2109"),sQuery(id+"F0.wireOp",EDGE,"E2109"),sQuery(id+"F0.wireOp",EDGE,"E2110"),sQuery(id+"F0.wireOp",EDGE,"E2111"),sQuery(id+"F0.wireOp",EDGE,"E2111"),sQuery(id+"F0.wireOp",EDGE,"E2111"),sQuery(id+"F0.wireOp",EDGE,"E2111"),sQuery(id+"F0.wireOp",EDGE,"E2111"),sQuery(id+"F0.wireOp",EDGE,"E2112"),sQuery(id+"F0.wireOp",EDGE,"E2113"),sQuery(id+"F0.wireOp",EDGE,"E2114"),sQuery(id+"F0.wireOp",EDGE,"E2114"),sQuery(id+"F0.wireOp",EDGE,"E2115"),sQuery(id+"F0.wireOp",EDGE,"E2116"),sQuery(id+"F0.wireOp",EDGE,"E2116"),sQuery(id+"F0.wireOp",EDGE,"E2117"),sQuery(id+"F0.wireOp",EDGE,"E2118"),sQuery(id+"F0.wireOp",EDGE,"E2118"),sQuery(id+"F0.wireOp",EDGE,"E2119"),sQuery(id+"F0.wireOp",EDGE,"E2120"),sQuery(id+"F0.wireOp",EDGE,"E2120"),sQuery(id+"F0.wireOp",EDGE,"E2121"),sQuery(id+"F0.wireOp",EDGE,"E2122"),sQuery(id+"F0.wireOp",EDGE,"E2122"),sQuery(id+"F0.wireOp",EDGE,"E2123"),sQuery(id+"F0.wireOp",EDGE,"E2124"),sQuery(id+"F0.wireOp",EDGE,"E2125"),sQuery(id+"F0.wireOp",EDGE,"E2126"),sQuery(id+"F0.wireOp",EDGE,"E2127"),sQuery(id+"F0.wireOp",EDGE,"E2128"),sQuery(id+"F0.wireOp",EDGE,"E2129"),sQuery(id+"F0.wireOp",EDGE,"E2129"),sQuery(id+"F0.wireOp",EDGE,"E2129"),sQuery(id+"F0.wireOp",EDGE,"E2129"),sQuery(id+"F0.wireOp",EDGE,"E2130"),sQuery(id+"F0.wireOp",EDGE,"E2131"),sQuery(id+"F0.wireOp",EDGE,"E2131"),sQuery(id+"F0.wireOp",EDGE,"E2132"),sQuery(id+"F0.wireOp",EDGE,"E2133"),sQuery(id+"F0.wireOp",EDGE,"E2133"),sQuery(id+"F0.wireOp",EDGE,"E2133"),sQuery(id+"F0.wireOp",EDGE,"E2133"),sQuery(id+"F0.wireOp",EDGE,"E2134"),sQuery(id+"F0.wireOp",EDGE,"E2135"),sQuery(id+"F0.wireOp",EDGE,"E2136"),sQuery(id+"F0.wireOp",EDGE,"E2137"),sQuery(id+"F0.wireOp",EDGE,"E2138"),sQuery(id+"F0.wireOp",EDGE,"E2139"),sQuery(id+"F0.wireOp",EDGE,"E2140"),sQuery(id+"F0.wireOp",EDGE,"E2140"),sQuery(id+"F0.wireOp",EDGE,"E2141"),sQuery(id+"F0.wireOp",EDGE,"E2142"),sQuery(id+"F0.wireOp",EDGE,"E2142"),sQuery(id+"F0.wireOp",EDGE,"E2143"),sQuery(id+"F0.wireOp",EDGE,"E2144"),sQuery(id+"F0.wireOp",EDGE,"E2145"),sQuery(id+"F0.wireOp",EDGE,"E2146"),sQuery(id+"F0.wireOp",EDGE,"E2147"),sQuery(id+"F0.wireOp",EDGE,"E2148"),sQuery(id+"F0.wireOp",EDGE,"E2148"),sQuery(id+"F0.wireOp",EDGE,"E2149"),sQuery(id+"F0.wireOp",EDGE,"E2150"),sQuery(id+"F0.wireOp",EDGE,"E2150"),sQuery(id+"F0.wireOp",EDGE,"E2151"),sQuery(id+"F0.wireOp",EDGE,"E2152"),sQuery(id+"F0.wireOp",EDGE,"E2152"),sQuery(id+"F0.wireOp",EDGE,"E2153"),sQuery(id+"F0.wireOp",EDGE,"E2154"),sQuery(id+"F0.wireOp",EDGE,"E2155"),sQuery(id+"F0.wireOp",EDGE,"E2156"),sQuery(id+"F0.wireOp",EDGE,"E2157"),sQuery(id+"F0.wireOp",EDGE,"E2158"),sQuery(id+"F0.wireOp",EDGE,"E2159"),sQuery(id+"F0.wireOp",EDGE,"E2160"),sQuery(id+"F0.wireOp",EDGE,"E2161"),sQuery(id+"F0.wireOp",EDGE,"E2161"),sQuery(id+"F0.wireOp",EDGE,"E2162"),sQuery(id+"F0.wireOp",EDGE,"E2163"),sQuery(id+"F0.wireOp",EDGE,"E2163"),sQuery(id+"F0.wireOp",EDGE,"E2164"),sQuery(id+"F0.wireOp",EDGE,"E2165"),sQuery(id+"F0.wireOp",EDGE,"E2166"),sQuery(id+"F0.wireOp",EDGE,"E2167"),sQuery(id+"F0.wireOp",EDGE,"E2168"),sQuery(id+"F0.wireOp",EDGE,"E2169"),sQuery(id+"F0.wireOp",EDGE,"E2170"),sQuery(id+"F0.wireOp",EDGE,"E2171"),sQuery(id+"F0.wireOp",EDGE,"E2172"),sQuery(id+"F0.wireOp",EDGE,"E2172"),sQuery(id+"F0.wireOp",EDGE,"E2173"),sQuery(id+"F0.wireOp",EDGE,"E2174"),sQuery(id+"F0.wireOp",EDGE,"E2174"),sQuery(id+"F0.wireOp",EDGE,"E2175"),sQuery(id+"F0.wireOp",EDGE,"E2176"),sQuery(id+"F0.wireOp",EDGE,"E2177"),sQuery(id+"F0.wireOp",EDGE,"E2178"),sQuery(id+"F0.wireOp",EDGE,"E2179"),sQuery(id+"F0.wireOp",EDGE,"E2180"),sQuery(id+"F0.wireOp",EDGE,"E2180"),sQuery(id+"F0.wireOp",EDGE,"E2181"),sQuery(id+"F0.wireOp",EDGE,"E2182"),sQuery(id+"F0.wireOp",EDGE,"E2182"),sQuery(id+"F0.wireOp",EDGE,"E2183"),sQuery(id+"F0.wireOp",EDGE,"E2184"),sQuery(id+"F0.wireOp",EDGE,"E2184"),sQuery(id+"F0.wireOp",EDGE,"E2185"),sQuery(id+"F0.wireOp",EDGE,"E2186"),sQuery(id+"F0.wireOp",EDGE,"E2187"),sQuery(id+"F0.wireOp",EDGE,"E2188"),sQuery(id+"F0.wireOp",EDGE,"E2189"),sQuery(id+"F0.wireOp",EDGE,"E2190"),sQuery(id+"F0.wireOp",EDGE,"E2191"),sQuery(id+"F0.wireOp",EDGE,"E2192"),sQuery(id+"F0.wireOp",EDGE,"E2193"),sQuery(id+"F0.wireOp",EDGE,"E2193"),sQuery(id+"F0.wireOp",EDGE,"E2194"),sQuery(id+"F0.wireOp",EDGE,"E2195"),sQuery(id+"F0.wireOp",EDGE,"E2196"),sQuery(id+"F0.wireOp",EDGE,"E2197"),sQuery(id+"F0.wireOp",EDGE,"E2198"),sQuery(id+"F0.wireOp",EDGE,"E2199"),sQuery(id+"F0.wireOp",EDGE,"E2200"),sQuery(id+"F0.wireOp",EDGE,"E2200"),sQuery(id+"F0.wireOp",EDGE,"E2200"),sQuery(id+"F0.wireOp",EDGE,"E2200"),sQuery(id+"F0.wireOp",EDGE,"E2201"),sQuery(id+"F0.wireOp",EDGE,"E2202"),sQuery(id+"F0.wireOp",EDGE,"E2202"),sQuery(id+"F0.wireOp",EDGE,"E2203"),sQuery(id+"F0.wireOp",EDGE,"E2204"),sQuery(id+"F0.wireOp",EDGE,"E2204"),sQuery(id+"F0.wireOp",EDGE,"E2204"),sQuery(id+"F0.wireOp",EDGE,"E2204"),sQuery(id+"F0.wireOp",EDGE,"E2205"),sQuery(id+"F0.wireOp",EDGE,"E2206"),sQuery(id+"F0.wireOp",EDGE,"E2207"),sQuery(id+"F0.wireOp",EDGE,"E2208"),sQuery(id+"F0.wireOp",EDGE,"E2209"),sQuery(id+"F0.wireOp",EDGE,"E2210"),sQuery(id+"F0.wireOp",EDGE,"E2211"),sQuery(id+"F0.wireOp",EDGE,"E2211"),sQuery(id+"F0.wireOp",EDGE,"E2212"),sQuery(id+"F0.wireOp",EDGE,"E2213"),sQuery(id+"F0.wireOp",EDGE,"E2214"),sQuery(id+"F0.wireOp",EDGE,"E2215"),sQuery(id+"F0.wireOp",EDGE,"E2216"),sQuery(id+"F0.wireOp",EDGE,"E2230"),sQuery(id+"F0.wireOp",EDGE,"E2231"),sQuery(id+"F0.wireOp",EDGE,"E2232"),sQuery(id+"F0.wireOp",EDGE,"E2233"),sQuery(id+"F0.wireOp",EDGE,"E2234"),sQuery(id+"F0.wireOp",EDGE,"E2235"),sQuery(id+"F0.wireOp",EDGE,"E2236"),sQuery(id+"F0.wireOp",EDGE,"E2237"),sQuery(id+"F0.wireOp",EDGE,"E2238"),sQuery(id+"F0.wireOp",EDGE,"E2239"),sQuery(id+"F0.wireOp",EDGE,"E2240"),sQuery(id+"F0.wireOp",EDGE,"E2241"),sQuery(id+"F0.wireOp",EDGE,"E2242"),sQuery(id+"F0.wireOp",EDGE,"E2243"),sQuery(id+"F0.wireOp",EDGE,"E2244"),sQuery(id+"F0.wireOp",EDGE,"E2245"),sQuery(id+"F0.wireOp",EDGE,"E2246"),sQuery(id+"F0.wireOp",EDGE,"E2247"),sQuery(id+"F0.wireOp",EDGE,"E2248"),sQuery(id+"F0.wireOp",EDGE,"E2249"),sQuery(id+"F0.wireOp",EDGE,"E2250"),sQuery(id+"F0.wireOp",EDGE,"E2251"),sQuery(id+"F0.wireOp",EDGE,"E2252"),sQuery(id+"F0.wireOp",EDGE,"E2253"),sQuery(id+"F0.wireOp",EDGE,"E2254"),sQuery(id+"F0.wireOp",EDGE,"E2255"),sQuery(id+"F0.wireOp",EDGE,"E2255"),sQuery(id+"F0.wireOp",EDGE,"E2256"),sQuery(id+"F0.wireOp",EDGE,"E2257"),sQuery(id+"F0.wireOp",EDGE,"E2258"),sQuery(id+"F0.wireOp",EDGE,"E2259"),sQuery(id+"F0.wireOp",EDGE,"E2260"),sQuery(id+"F0.wireOp",EDGE,"E2260"),sQuery(id+"F0.wireOp",EDGE,"E2261"),sQuery(id+"F0.wireOp",EDGE,"E2262"),sQuery(id+"F0.wireOp",EDGE,"E2262"),sQuery(id+"F0.wireOp",EDGE,"E2263"),sQuery(id+"F0.wireOp",EDGE,"E2264"),sQuery(id+"F0.wireOp",EDGE,"E2265"),sQuery(id+"F0.wireOp",EDGE,"E2266"),sQuery(id+"F0.wireOp",EDGE,"E2267"),sQuery(id+"F0.wireOp",EDGE,"E2268"),sQuery(id+"F0.wireOp",EDGE,"E2269"),sQuery(id+"F0.wireOp",EDGE,"E2269"),sQuery(id+"F0.wireOp",EDGE,"E2269"),sQuery(id+"F0.wireOp",EDGE,"E2270"),sQuery(id+"F0.wireOp",EDGE,"E2271"),sQuery(id+"F0.wireOp",EDGE,"E2272"),sQuery(id+"F0.wireOp",EDGE,"E2272"),sQuery(id+"F0.wireOp",EDGE,"E2273"),sQuery(id+"F0.wireOp",EDGE,"E2274"),sQuery(id+"F0.wireOp",EDGE,"E2275"),sQuery(id+"F0.wireOp",EDGE,"E2276"),sQuery(id+"F0.wireOp",EDGE,"E2276"),sQuery(id+"F0.wireOp",EDGE,"E2276"),sQuery(id+"F0.wireOp",EDGE,"E2276"),sQuery(id+"F0.wireOp",EDGE,"E2277"),sQuery(id+"F0.wireOp",EDGE,"E2278"),sQuery(id+"F0.wireOp",EDGE,"E2279"),sQuery(id+"F0.wireOp",EDGE,"E2280"),sQuery(id+"F0.wireOp",EDGE,"E2280"),sQuery(id+"F0.wireOp",EDGE,"E2281"),sQuery(id+"F0.wireOp",EDGE,"E2282"),sQuery(id+"F0.wireOp",EDGE,"E2283"),sQuery(id+"F0.wireOp",EDGE,"E2284"),sQuery(id+"F0.wireOp",EDGE,"E2285"),sQuery(id+"F0.wireOp",EDGE,"E2286"),sQuery(id+"F0.wireOp",EDGE,"E2287"),sQuery(id+"F0.wireOp",EDGE,"E2288"),sQuery(id+"F0.wireOp",EDGE,"E2288"),sQuery(id+"F0.wireOp",EDGE,"E2289"),sQuery(id+"F0.wireOp",EDGE,"E2290"),sQuery(id+"F0.wireOp",EDGE,"E2291"),sQuery(id+"F0.wireOp",EDGE,"E2292"),sQuery(id+"F0.wireOp",EDGE,"E2293"),sQuery(id+"F0.wireOp",EDGE,"E2294"),sQuery(id+"F0.wireOp",EDGE,"E2295"),sQuery(id+"F0.wireOp",EDGE,"E2296"),sQuery(id+"F0.wireOp",EDGE,"E2297"),sQuery(id+"F0.wireOp",EDGE,"E2298"),sQuery(id+"F0.wireOp",EDGE,"E2299"),sQuery(id+"F0.wireOp",EDGE,"E2300"),sQuery(id+"F0.wireOp",EDGE,"E2301"),sQuery(id+"F0.wireOp",EDGE,"E2302"),sQuery(id+"F0.wireOp",EDGE,"E2303"),sQuery(id+"F0.wireOp",EDGE,"E2304"),sQuery(id+"F0.wireOp",EDGE,"E2305"),sQuery(id+"F0.wireOp",EDGE,"E2306"),sQuery(id+"F0.wireOp",EDGE,"E2307"),sQuery(id+"F0.wireOp",EDGE,"E2308"),sQuery(id+"F0.wireOp",EDGE,"E2309"),sQuery(id+"F0.wireOp",EDGE,"E2310"),sQuery(id+"F0.wireOp",EDGE,"E2311"),sQuery(id+"F0.wireOp",EDGE,"E2312"),sQuery(id+"F0.wireOp",EDGE,"E2313"),sQuery(id+"F0.wireOp",EDGE,"E2314"),sQuery(id+"F0.wireOp",EDGE,"E2315"),sQuery(id+"F0.wireOp",EDGE,"E2316"),sQuery(id+"F0.wireOp",EDGE,"E2317"),sQuery(id+"F0.wireOp",EDGE,"E2318"),sQuery(id+"F0.wireOp",EDGE,"E2319"),sQuery(id+"F0.wireOp",EDGE,"E2320"),sQuery(id+"F0.wireOp",EDGE,"E2320"),sQuery(id+"F0.wireOp",EDGE,"E2321"),sQuery(id+"F0.wireOp",EDGE,"E2322"),sQuery(id+"F0.wireOp",EDGE,"E2323"),sQuery(id+"F0.wireOp",EDGE,"E2324"),sQuery(id+"F0.wireOp",EDGE,"E2325"),sQuery(id+"F0.wireOp",EDGE,"E2325"),sQuery(id+"F0.wireOp",EDGE,"E2326"),sQuery(id+"F0.wireOp",EDGE,"E2327"),sQuery(id+"F0.wireOp",EDGE,"E2328"),sQuery(id+"F0.wireOp",EDGE,"E2329"),sQuery(id+"F0.wireOp",EDGE,"E2330"),sQuery(id+"F0.wireOp",EDGE,"E2330"),sQuery(id+"F0.wireOp",EDGE,"E2331"),sQuery(id+"F0.wireOp",EDGE,"E2332"),sQuery(id+"F0.wireOp",EDGE,"E2332"),sQuery(id+"F0.wireOp",EDGE,"E2332"),sQuery(id+"F0.wireOp",EDGE,"E2332"),sQuery(id+"F0.wireOp",EDGE,"E2332"),sQuery(id+"F0.wireOp",EDGE,"E2333"),sQuery(id+"F0.wireOp",EDGE,"E2334"),sQuery(id+"F0.wireOp",EDGE,"E2335"),sQuery(id+"F0.wireOp",EDGE,"E2336"),sQuery(id+"F0.wireOp",EDGE,"E2337"),sQuery(id+"F0.wireOp",EDGE,"E2337"),sQuery(id+"F0.wireOp",EDGE,"E2338"),sQuery(id+"F0.wireOp",EDGE,"E2339"),sQuery(id+"F0.wireOp",EDGE,"E2340"),sQuery(id+"F0.wireOp",EDGE,"E2320"),sQuery(id+"F0.wireOp",EDGE,"E2341"),sQuery(id+"F0.wireOp",EDGE,"E2342"),sQuery(id+"F0.wireOp",EDGE,"E2343"),sQuery(id+"F0.wireOp",EDGE,"E2344"),sQuery(id+"F0.wireOp",EDGE,"E2345"),sQuery(id+"F0.wireOp",EDGE,"E2345"),sQuery(id+"F0.wireOp",EDGE,"E2345"),sQuery(id+"F0.wireOp",EDGE,"E2345"),sQuery(id+"F0.wireOp",EDGE,"E2346"),sQuery(id+"F0.wireOp",EDGE,"E2347"),sQuery(id+"F0.wireOp",EDGE,"E2347"),sQuery(id+"F0.wireOp",EDGE,"E2348"),sQuery(id+"F0.wireOp",EDGE,"E2349"),sQuery(id+"F0.wireOp",EDGE,"E2350"),sQuery(id+"F0.wireOp",EDGE,"E2351"),sQuery(id+"F0.wireOp",EDGE,"E2351"),sQuery(id+"F0.wireOp",EDGE,"E2352"),sQuery(id+"F0.wireOp",EDGE,"E2353"),sQuery(id+"F0.wireOp",EDGE,"E2354"),sQuery(id+"F0.wireOp",EDGE,"E2355"),sQuery(id+"F0.wireOp",EDGE,"E2355"),sQuery(id+"F0.wireOp",EDGE,"E2355"),sQuery(id+"F0.wireOp",EDGE,"E2356"),sQuery(id+"F0.wireOp",EDGE,"E2357"),sQuery(id+"F0.wireOp",EDGE,"E2358"),sQuery(id+"F0.wireOp",EDGE,"E2359"),sQuery(id+"F0.wireOp",EDGE,"E2360"),sQuery(id+"F0.wireOp",EDGE,"E2361"),sQuery(id+"F0.wireOp",EDGE,"E2362"),sQuery(id+"F0.wireOp",EDGE,"E2363"),sQuery(id+"F0.wireOp",EDGE,"E2364"),sQuery(id+"F0.wireOp",EDGE,"E2365"),sQuery(id+"F0.wireOp",EDGE,"E2366"),sQuery(id+"F0.wireOp",EDGE,"E2366"),sQuery(id+"F0.wireOp",EDGE,"E2367"),sQuery(id+"F0.wireOp",EDGE,"E2364"),sQuery(id+"F0.wireOp",EDGE,"E2364"),sQuery(id+"F0.wireOp",EDGE,"E2368"),sQuery(id+"F0.wireOp",EDGE,"E2369"),sQuery(id+"F0.wireOp",EDGE,"E2369"),sQuery(id+"F0.wireOp",EDGE,"E2370"),sQuery(id+"F0.wireOp",EDGE,"E2371"),sQuery(id+"F0.wireOp",EDGE,"E2372"),sQuery(id+"F0.wireOp",EDGE,"E2373"),sQuery(id+"F0.wireOp",EDGE,"E2373"),sQuery(id+"F0.wireOp",EDGE,"E2373"),sQuery(id+"F0.wireOp",EDGE,"E2373"),sQuery(id+"F0.wireOp",EDGE,"E2374"),sQuery(id+"F0.wireOp",EDGE,"E2375"),sQuery(id+"F0.wireOp",EDGE,"E2375"),sQuery(id+"F0.wireOp",EDGE,"E2376"),sQuery(id+"F0.wireOp",EDGE,"E2377"),sQuery(id+"F0.wireOp",EDGE,"E2377"),sQuery(id+"F0.wireOp",EDGE,"E2378"),sQuery(id+"F0.wireOp",EDGE,"E2379"),sQuery(id+"F0.wireOp",EDGE,"E2380"),sQuery(id+"F0.wireOp",EDGE,"E2381"),sQuery(id+"F0.wireOp",EDGE,"E2381"),sQuery(id+"F0.wireOp",EDGE,"E2382"),sQuery(id+"F0.wireOp",EDGE,"E2383"),sQuery(id+"F0.wireOp",EDGE,"E2383"),sQuery(id+"F0.wireOp",EDGE,"E2384"),sQuery(id+"F0.wireOp",EDGE,"E2385"),sQuery(id+"F0.wireOp",EDGE,"E2386"),sQuery(id+"F0.wireOp",EDGE,"E2387"),sQuery(id+"F0.wireOp",EDGE,"E2387"),sQuery(id+"F0.wireOp",EDGE,"E2387"),sQuery(id+"F0.wireOp",EDGE,"E2387"),sQuery(id+"F0.wireOp",EDGE,"E2402"),sQuery(id+"F0.wireOp",EDGE,"E2403"),sQuery(id+"F0.wireOp",EDGE,"E2404"),sQuery(id+"F0.wireOp",EDGE,"E2405"),sQuery(id+"F0.wireOp",EDGE,"E2405"),sQuery(id+"F0.wireOp",EDGE,"E2406"),sQuery(id+"F0.wireOp",EDGE,"E2407"),sQuery(id+"F0.wireOp",EDGE,"E2407"),sQuery(id+"F0.wireOp",EDGE,"E2408"),sQuery(id+"F0.wireOp",EDGE,"E2409"),sQuery(id+"F0.wireOp",EDGE,"E2410"),sQuery(id+"F0.wireOp",EDGE,"E2411"),sQuery(id+"F0.wireOp",EDGE,"E2412"),sQuery(id+"F0.wireOp",EDGE,"E2412"),sQuery(id+"F0.wireOp",EDGE,"E2413"),sQuery(id+"F0.wireOp",EDGE,"E2414"),sQuery(id+"F0.wireOp",EDGE,"E2415"),sQuery(id+"F0.wireOp",EDGE,"E2416"),sQuery(id+"F0.wireOp",EDGE,"E2417"),sQuery(id+"F0.wireOp",EDGE,"E2417"),sQuery(id+"F0.wireOp",EDGE,"E2417"),sQuery(id+"F0.wireOp",EDGE,"E2417"),sQuery(id+"F0.wireOp",EDGE,"E2417"),sQuery(id+"F0.wireOp",EDGE,"E2418"),sQuery(id+"F0.wireOp",EDGE,"E2419"),sQuery(id+"F0.wireOp",EDGE,"E2420"),sQuery(id+"F0.wireOp",EDGE,"E2421"),sQuery(id+"F0.wireOp",EDGE,"E2422"),sQuery(id+"F0.wireOp",EDGE,"E2423"),sQuery(id+"F0.wireOp",EDGE,"E2424"),sQuery(id+"F0.wireOp",EDGE,"E2424"),sQuery(id+"F0.wireOp",EDGE,"E2425"),sQuery(id+"F0.wireOp",EDGE,"E2426"),sQuery(id+"F0.wireOp",EDGE,"E2427"),sQuery(id+"F0.wireOp",EDGE,"E2428"),sQuery(id+"F0.wireOp",EDGE,"E2429"),sQuery(id+"F0.wireOp",EDGE,"E2429"),sQuery(id+"F0.wireOp",EDGE,"E2430"),sQuery(id+"F0.wireOp",EDGE,"E2431"),sQuery(id+"F0.wireOp",EDGE,"E2431"),sQuery(id+"F0.wireOp",EDGE,"E2431"),sQuery(id+"F0.wireOp",EDGE,"E2431"),sQuery(id+"F0.wireOp",EDGE,"E2431"),sQuery(id+"F0.wireOp",EDGE,"E2431"),sQuery(id+"F0.wireOp",EDGE,"E2431"),sQuery(id+"F0.wireOp",EDGE,"E2431"),sQuery(id+"F0.wireOp",EDGE,"E2432"),sQuery(id+"F0.wireOp",EDGE,"E2433"),sQuery(id+"F0.wireOp",EDGE,"E2433"),sQuery(id+"F0.wireOp",EDGE,"E2434"),sQuery(id+"F0.wireOp",EDGE,"E2435"),sQuery(id+"F0.wireOp",EDGE,"E2436"),sQuery(id+"F0.wireOp",EDGE,"E2437"),sQuery(id+"F0.wireOp",EDGE,"E2438"),sQuery(id+"F0.wireOp",EDGE,"E2439"),sQuery(id+"F0.wireOp",EDGE,"E2440"),sQuery(id+"F0.wireOp",EDGE,"E2441"),sQuery(id+"F0.wireOp",EDGE,"E2442"),sQuery(id+"F0.wireOp",EDGE,"E2443"),sQuery(id+"F0.wireOp",EDGE,"E2444"),sQuery(id+"F0.wireOp",EDGE,"E2444"),sQuery(id+"F0.wireOp",EDGE,"E2445"),sQuery(id+"F0.wireOp",EDGE,"E2446"),sQuery(id+"F0.wireOp",EDGE,"E2446"),sQuery(id+"F0.wireOp",EDGE,"E2447"),sQuery(id+"F0.wireOp",EDGE,"E2448"),sQuery(id+"F0.wireOp",EDGE,"E2448"),sQuery(id+"F0.wireOp",EDGE,"E2449"),sQuery(id+"F0.wireOp",EDGE,"E2450"),sQuery(id+"F0.wireOp",EDGE,"E2450"),sQuery(id+"F0.wireOp",EDGE,"E2451"),sQuery(id+"F0.wireOp",EDGE,"E2452"),sQuery(id+"F0.wireOp",EDGE,"E2452"),sQuery(id+"F0.wireOp",EDGE,"E2453"),sQuery(id+"F0.wireOp",EDGE,"E2454"),sQuery(id+"F0.wireOp",EDGE,"E2455"),sQuery(id+"F0.wireOp",EDGE,"E2455"),sQuery(id+"F0.wireOp",EDGE,"E2456"),sQuery(id+"F0.wireOp",EDGE,"E2457"),sQuery(id+"F0.wireOp",EDGE,"E2458"),sQuery(id+"F0.wireOp",EDGE,"E2459"),sQuery(id+"F0.wireOp",EDGE,"E2459"),sQuery(id+"F0.wireOp",EDGE,"E2460"),sQuery(id+"F0.wireOp",EDGE,"E2461"),sQuery(id+"F0.wireOp",EDGE,"E2461"),sQuery(id+"F0.wireOp",EDGE,"E2462"),sQuery(id+"F0.wireOp",EDGE,"E2463"),sQuery(id+"F0.wireOp",EDGE,"E2463"),sQuery(id+"F0.wireOp",EDGE,"E2464"),sQuery(id+"F0.wireOp",EDGE,"E2465"),sQuery(id+"F0.wireOp",EDGE,"E2465"),sQuery(id+"F0.wireOp",EDGE,"E2466"),sQuery(id+"F0.wireOp",EDGE,"E2467"),sQuery(id+"F0.wireOp",EDGE,"E2467"),sQuery(id+"F0.wireOp",EDGE,"E2468"),sQuery(id+"F0.wireOp",EDGE,"E2469"),sQuery(id+"F0.wireOp",EDGE,"E2469"),sQuery(id+"F0.wireOp",EDGE,"E2470"),sQuery(id+"F0.wireOp",EDGE,"E2471"),sQuery(id+"F0.wireOp",EDGE,"E2472"),sQuery(id+"F0.wireOp",EDGE,"E2473"),sQuery(id+"F0.wireOp",EDGE,"E2474"),sQuery(id+"F0.wireOp",EDGE,"E2474"),sQuery(id+"F0.wireOp",EDGE,"E2474"),sQuery(id+"F0.wireOp",EDGE,"E2474"),sQuery(id+"F0.wireOp",EDGE,"E2474"),sQuery(id+"F0.wireOp",EDGE,"E2474"),sQuery(id+"F0.wireOp",EDGE,"E2474"),sQuery(id+"F0.wireOp",EDGE,"E2474"),sQuery(id+"F0.wireOp",EDGE,"E2475"),sQuery(id+"F0.wireOp",EDGE,"E2476"),sQuery(id+"F0.wireOp",EDGE,"E2477"),sQuery(id+"F0.wireOp",EDGE,"E2478"),sQuery(id+"F0.wireOp",EDGE,"E2479"),sQuery(id+"F0.wireOp",EDGE,"E2480"),sQuery(id+"F0.wireOp",EDGE,"E2481"),sQuery(id+"F0.wireOp",EDGE,"E2482"),sQuery(id+"F0.wireOp",EDGE,"E2483"),sQuery(id+"F0.wireOp",EDGE,"E2484"),sQuery(id+"F0.wireOp",EDGE,"E2484"),sQuery(id+"F0.wireOp",EDGE,"E2485"),sQuery(id+"F0.wireOp",EDGE,"E2486"),sQuery(id+"F0.wireOp",EDGE,"E2487"),sQuery(id+"F0.wireOp",EDGE,"E2487"),sQuery(id+"F0.wireOp",EDGE,"E2487"),sQuery(id+"F0.wireOp",EDGE,"E2487"),sQuery(id+"F0.wireOp",EDGE,"E2487"),sQuery(id+"F0.wireOp",EDGE,"E2488"),sQuery(id+"F0.wireOp",EDGE,"E2489"),sQuery(id+"F0.wireOp",EDGE,"E2490"),sQuery(id+"F0.wireOp",EDGE,"E2491"),sQuery(id+"F0.wireOp",EDGE,"E2492"),sQuery(id+"F0.wireOp",EDGE,"E2492"),sQuery(id+"F0.wireOp",EDGE,"E2493"),sQuery(id+"F0.wireOp",EDGE,"E2494"),sQuery(id+"F0.wireOp",EDGE,"E2494"),sQuery(id+"F0.wireOp",EDGE,"E2495"),sQuery(id+"F0.wireOp",EDGE,"E2496"),sQuery(id+"F0.wireOp",EDGE,"E2496"),sQuery(id+"F0.wireOp",EDGE,"E2497"),sQuery(id+"F0.wireOp",EDGE,"E2498"),sQuery(id+"F0.wireOp",EDGE,"E2498"),sQuery(id+"F0.wireOp",EDGE,"E2499"),sQuery(id+"F0.wireOp",EDGE,"E2500"),sQuery(id+"F0.wireOp",EDGE,"E2501"),sQuery(id+"F0.wireOp",EDGE,"E2502"),sQuery(id+"F0.wireOp",EDGE,"E2503"),sQuery(id+"F0.wireOp",EDGE,"E2503"),sQuery(id+"F0.wireOp",EDGE,"E2504"),sQuery(id+"F0.wireOp",EDGE,"E2442"),sQuery(id+"F0.wireOp",EDGE,"E2505"),sQuery(id+"F0.wireOp",EDGE,"E2506"),sQuery(id+"F0.wireOp",EDGE,"E2506"),sQuery(id+"F0.wireOp",EDGE,"E2506"),sQuery(id+"F0.wireOp",EDGE,"E2506"),sQuery(id+"F0.wireOp",EDGE,"E2507"),sQuery(id+"F0.wireOp",EDGE,"E2508"),sQuery(id+"F0.wireOp",EDGE,"E2509"),sQuery(id+"F0.wireOp",EDGE,"E2510"),sQuery(id+"F0.wireOp",EDGE,"E2511"),sQuery(id+"F0.wireOp",EDGE,"E2511"),sQuery(id+"F0.wireOp",EDGE,"E2511"),sQuery(id+"F0.wireOp",EDGE,"E2511"),sQuery(id+"F0.wireOp",EDGE,"E2512"),sQuery(id+"F0.wireOp",EDGE,"E2513"),sQuery(id+"F0.wireOp",EDGE,"E2514"),sQuery(id+"F0.wireOp",EDGE,"E2515"),sQuery(id+"F0.wireOp",EDGE,"E2516"),sQuery(id+"F0.wireOp",EDGE,"E2516"),sQuery(id+"F0.wireOp",EDGE,"E2516"),sQuery(id+"F0.wireOp",EDGE,"E2516"),sQuery(id+"F0.wireOp",EDGE,"E2516"),sQuery(id+"F0.wireOp",EDGE,"E2517"),sQuery(id+"F0.wireOp",EDGE,"E2518"),sQuery(id+"F0.wireOp",EDGE,"E2518"),sQuery(id+"F0.wireOp",EDGE,"E2518"),sQuery(id+"F0.wireOp",EDGE,"E2518"),sQuery(id+"F0.wireOp",EDGE,"E2519"),sQuery(id+"F0.wireOp",EDGE,"E2520"),sQuery(id+"F0.wireOp",EDGE,"E2521"),sQuery(id+"F0.wireOp",EDGE,"E2522"),sQuery(id+"F0.wireOp",EDGE,"E2523"),sQuery(id+"F0.wireOp",EDGE,"E2523"),sQuery(id+"F0.wireOp",EDGE,"E2524"),sQuery(id+"F0.wireOp",EDGE,"E2525"),sQuery(id+"F0.wireOp",EDGE,"E2526"),sQuery(id+"F0.wireOp",EDGE,"E2527"),sQuery(id+"F0.wireOp",EDGE,"E2527"),sQuery(id+"F0.wireOp",EDGE,"E2527"),sQuery(id+"F0.wireOp",EDGE,"E2527"),sQuery(id+"F0.wireOp",EDGE,"E2527"),sQuery(id+"F0.wireOp",EDGE,"E2528"),sQuery(id+"F0.wireOp",EDGE,"E2529"),sQuery(id+"F0.wireOp",EDGE,"E2530"),sQuery(id+"F0.wireOp",EDGE,"E2531"),sQuery(id+"F0.wireOp",EDGE,"E2531"),sQuery(id+"F0.wireOp",EDGE,"E2531"),sQuery(id+"F0.wireOp",EDGE,"E2531"),sQuery(id+"F0.wireOp",EDGE,"E2532"),sQuery(id+"F0.wireOp",EDGE,"E2533"),sQuery(id+"F0.wireOp",EDGE,"E2534"),sQuery(id+"F0.wireOp",EDGE,"E2535"),sQuery(id+"F0.wireOp",EDGE,"E2536"),sQuery(id+"F0.wireOp",EDGE,"E2557"),sQuery(id+"F0.wireOp",EDGE,"E2558"),sQuery(id+"F0.wireOp",EDGE,"E2559"),sQuery(id+"F0.wireOp",EDGE,"E2560"),sQuery(id+"F0.wireOp",EDGE,"E2561"),sQuery(id+"F0.wireOp",EDGE,"E2562"),sQuery(id+"F0.wireOp",EDGE,"E2563"),sQuery(id+"F0.wireOp",EDGE,"E2564"),sQuery(id+"F0.wireOp",EDGE,"E2565"),sQuery(id+"F0.wireOp",EDGE,"E2566"),sQuery(id+"F0.wireOp",EDGE,"E2567"),sQuery(id+"F0.wireOp",EDGE,"E2568"),sQuery(id+"F0.wireOp",EDGE,"E2569"),sQuery(id+"F0.wireOp",EDGE,"E2570"),sQuery(id+"F0.wireOp",EDGE,"E2571"),sQuery(id+"F0.wireOp",EDGE,"E2572"),sQuery(id+"F0.wireOp",EDGE,"E2573"),sQuery(id+"F0.wireOp",EDGE,"E2573"),sQuery(id+"F0.wireOp",EDGE,"E2574"),sQuery(id+"F0.wireOp",EDGE,"E2575"),sQuery(id+"F0.wireOp",EDGE,"E2575"),sQuery(id+"F0.wireOp",EDGE,"E2576"),sQuery(id+"F0.wireOp",EDGE,"E2577"),sQuery(id+"F0.wireOp",EDGE,"E2578"),sQuery(id+"F0.wireOp",EDGE,"E2579"),sQuery(id+"F0.wireOp",EDGE,"E2580"),sQuery(id+"F0.wireOp",EDGE,"E2581"),sQuery(id+"F0.wireOp",EDGE,"E2582"),sQuery(id+"F0.wireOp",EDGE,"E2583"),sQuery(id+"F0.wireOp",EDGE,"E2583"),sQuery(id+"F0.wireOp",EDGE,"E2584"),sQuery(id+"F0.wireOp",EDGE,"E2585"),sQuery(id+"F0.wireOp",EDGE,"E2585"),sQuery(id+"F0.wireOp",EDGE,"E2586"),sQuery(id+"F0.wireOp",EDGE,"E2587"),sQuery(id+"F0.wireOp",EDGE,"E2587"),sQuery(id+"F0.wireOp",EDGE,"E2587"),sQuery(id+"F0.wireOp",EDGE,"E2587"),sQuery(id+"F0.wireOp",EDGE,"E2587"),sQuery(id+"F0.wireOp",EDGE,"E2588"),sQuery(id+"F0.wireOp",EDGE,"E2589"),sQuery(id+"F0.wireOp",EDGE,"E2589"),sQuery(id+"F0.wireOp",EDGE,"E2590"),sQuery(id+"F0.wireOp",EDGE,"E2591"),sQuery(id+"F0.wireOp",EDGE,"E2591"),sQuery(id+"F0.wireOp",EDGE,"E2592"),sQuery(id+"F0.wireOp",EDGE,"E2593"),sQuery(id+"F0.wireOp",EDGE,"E2594"),sQuery(id+"F0.wireOp",EDGE,"E2581"),sQuery(id+"F0.wireOp",EDGE,"E2581"),sQuery(id+"F0.wireOp",EDGE,"E2595"),sQuery(id+"F0.wireOp",EDGE,"E2596"),sQuery(id+"F0.wireOp",EDGE,"E2597"),sQuery(id+"F0.wireOp",EDGE,"E2597"),sQuery(id+"F0.wireOp",EDGE,"E2598"),sQuery(id+"F0.wireOp",EDGE,"E2599"),sQuery(id+"F0.wireOp",EDGE,"E2600"),sQuery(id+"F0.wireOp",EDGE,"E2601"),sQuery(id+"F0.wireOp",EDGE,"E2602"),sQuery(id+"F0.wireOp",EDGE,"E2602"),sQuery(id+"F0.wireOp",EDGE,"E2602"),sQuery(id+"F0.wireOp",EDGE,"E2602"),sQuery(id+"F0.wireOp",EDGE,"E2602"),sQuery(id+"F0.wireOp",EDGE,"E2603"),sQuery(id+"F0.wireOp",EDGE,"E2604"),sQuery(id+"F0.wireOp",EDGE,"E2605"),sQuery(id+"F0.wireOp",EDGE,"E2606"),sQuery(id+"F0.wireOp",EDGE,"E2607"),sQuery(id+"F0.wireOp",EDGE,"E2608"),sQuery(id+"F0.wireOp",EDGE,"E2609"),sQuery(id+"F0.wireOp",EDGE,"E2610"),sQuery(id+"F0.wireOp",EDGE,"E2610"),sQuery(id+"F0.wireOp",EDGE,"E2611"),sQuery(id+"F0.wireOp",EDGE,"E2595"),sQuery(id+"F0.wireOp",EDGE,"E2612"),sQuery(id+"F0.wireOp",EDGE,"E2613"),sQuery(id+"F0.wireOp",EDGE,"E2613"),sQuery(id+"F0.wireOp",EDGE,"E2613"),sQuery(id+"F0.wireOp",EDGE,"E2614"),sQuery(id+"F0.wireOp",EDGE,"E2615"),sQuery(id+"F0.wireOp",EDGE,"E2616"),sQuery(id+"F0.wireOp",EDGE,"E2616"),sQuery(id+"F0.wireOp",EDGE,"E2616"),sQuery(id+"F0.wireOp",EDGE,"E2616"),sQuery(id+"F0.wireOp",EDGE,"E2616"),sQuery(id+"F0.wireOp",EDGE,"E2616"),sQuery(id+"F0.wireOp",EDGE,"E2616"),sQuery(id+"F0.wireOp",EDGE,"E2617"),sQuery(id+"F0.wireOp",EDGE,"E2618"),sQuery(id+"F0.wireOp",EDGE,"E2618"),sQuery(id+"F0.wireOp",EDGE,"E2618"),sQuery(id+"F0.wireOp",EDGE,"E2618"),sQuery(id+"F0.wireOp",EDGE,"E2619"),sQuery(id+"F0.wireOp",EDGE,"E2620"),sQuery(id+"F0.wireOp",EDGE,"E2621"),sQuery(id+"F0.wireOp",EDGE,"E2621"),sQuery(id+"F0.wireOp",EDGE,"E2621"),sQuery(id+"F0.wireOp",EDGE,"E2621"),sQuery(id+"F0.wireOp",EDGE,"E2622"),sQuery(id+"F0.wireOp",EDGE,"E2623"),sQuery(id+"F0.wireOp",EDGE,"E2646"),sQuery(id+"F0.wireOp",EDGE,"E2647"),sQuery(id+"F0.wireOp",EDGE,"E2648"),sQuery(id+"F0.wireOp",EDGE,"E2649"),sQuery(id+"F0.wireOp",EDGE,"E2650"),sQuery(id+"F0.wireOp",EDGE,"E2651"),sQuery(id+"F0.wireOp",EDGE,"E2652"),sQuery(id+"F0.wireOp",EDGE,"E2652"),sQuery(id+"F0.wireOp",EDGE,"E2653"),sQuery(id+"F0.wireOp",EDGE,"E2654"),sQuery(id+"F0.wireOp",EDGE,"E2654"),sQuery(id+"F0.wireOp",EDGE,"E2655"),sQuery(id+"F0.wireOp",EDGE,"E2656"),sQuery(id+"F0.wireOp",EDGE,"E2657"),sQuery(id+"F0.wireOp",EDGE,"E2658"),sQuery(id+"F0.wireOp",EDGE,"E2659"),sQuery(id+"F0.wireOp",EDGE,"E2660"),sQuery(id+"F0.wireOp",EDGE,"E2660"),sQuery(id+"F0.wireOp",EDGE,"E2661"),sQuery(id+"F0.wireOp",EDGE,"E2662"),sQuery(id+"F0.wireOp",EDGE,"E2663"),sQuery(id+"F0.wireOp",EDGE,"E2664"),sQuery(id+"F0.wireOp",EDGE,"E2665"),sQuery(id+"F0.wireOp",EDGE,"E2666"),sQuery(id+"F0.wireOp",EDGE,"E2667"),sQuery(id+"F0.wireOp",EDGE,"E2668"),sQuery(id+"F0.wireOp",EDGE,"E2669.bottom"),sQuery(id+"F0.wireOp",EDGE,"E2669.top"),sQuery(id+"F0.wireOp",EDGE,"E2669.left"),sQuery(id+"F0.wireOp",EDGE,"E2669.right")])]});
            var Q4;
            Q4=makeQuery(id+"F1.opExtrude","SWEPT_BODY",BODY,{"disambiguationData":[OSD([sQuery(id+"F0.wireOp",EDGE,"E153"),sQuery(id+"F0.wireOp",EDGE,"E154"),sQuery(id+"F0.wireOp",EDGE,"E155"),sQuery(id+"F0.wireOp",EDGE,"E156"),sQuery(id+"F0.wireOp",EDGE,"E157"),sQuery(id+"F0.wireOp",EDGE,"E158"),sQuery(id+"F0.wireOp",EDGE,"E159"),sQuery(id+"F0.wireOp",EDGE,"E160"),sQuery(id+"F0.wireOp",EDGE,"E161"),sQuery(id+"F0.wireOp",EDGE,"E162"),sQuery(id+"F0.wireOp",EDGE,"E163"),sQuery(id+"F0.wireOp",EDGE,"E164"),sQuery(id+"F0.wireOp",EDGE,"E165"),sQuery(id+"F0.wireOp",EDGE,"E166"),sQuery(id+"F0.wireOp",EDGE,"E167"),sQuery(id+"F0.wireOp",EDGE,"E168"),sQuery(id+"F0.wireOp",EDGE,"E169"),sQuery(id+"F0.wireOp",EDGE,"E170"),sQuery(id+"F0.wireOp",EDGE,"E171"),sQuery(id+"F0.wireOp",EDGE,"E172"),sQuery(id+"F0.wireOp",EDGE,"E173"),sQuery(id+"F0.wireOp",EDGE,"E174"),sQuery(id+"F0.wireOp",EDGE,"E175"),sQuery(id+"F0.wireOp",EDGE,"E176")])]});
            var Q5;
            Q5=makeQuery(id+"F1.opExtrude","SWEPT_BODY",BODY,{"disambiguationData":[OSD([sQuery(id+"F0.wireOp",EDGE,"E440"),sQuery(id+"F0.wireOp",EDGE,"E441"),sQuery(id+"F0.wireOp",EDGE,"E442"),sQuery(id+"F0.wireOp",EDGE,"E443"),sQuery(id+"F0.wireOp",EDGE,"E444"),sQuery(id+"F0.wireOp",EDGE,"E445"),sQuery(id+"F0.wireOp",EDGE,"E446"),sQuery(id+"F0.wireOp",EDGE,"E447"),sQuery(id+"F0.wireOp",EDGE,"E448"),sQuery(id+"F0.wireOp",EDGE,"E449"),sQuery(id+"F0.wireOp",EDGE,"E450"),sQuery(id+"F0.wireOp",EDGE,"E451"),sQuery(id+"F0.wireOp",EDGE,"E452"),sQuery(id+"F0.wireOp",EDGE,"E453"),sQuery(id+"F0.wireOp",EDGE,"E454"),sQuery(id+"F0.wireOp",EDGE,"E455"),sQuery(id+"F0.wireOp",EDGE,"E456"),sQuery(id+"F0.wireOp",EDGE,"E457"),sQuery(id+"F0.wireOp",EDGE,"E458"),sQuery(id+"F0.wireOp",EDGE,"E459"),sQuery(id+"F0.wireOp",EDGE,"E460"),sQuery(id+"F0.wireOp",EDGE,"E461"),sQuery(id+"F0.wireOp",EDGE,"E462"),sQuery(id+"F0.wireOp",EDGE,"E463")])]});
            var Q6;
            Q6=makeQuery(id+"F1.opExtrude","SWEPT_BODY",BODY,{"disambiguationData":[OSD([sQuery(id+"F0.wireOp",EDGE,"E540"),sQuery(id+"F0.wireOp",EDGE,"E541"),sQuery(id+"F0.wireOp",EDGE,"E542"),sQuery(id+"F0.wireOp",EDGE,"E543"),sQuery(id+"F0.wireOp",EDGE,"E544"),sQuery(id+"F0.wireOp",EDGE,"E545"),sQuery(id+"F0.wireOp",EDGE,"E546"),sQuery(id+"F0.wireOp",EDGE,"E547"),sQuery(id+"F0.wireOp",EDGE,"E548"),sQuery(id+"F0.wireOp",EDGE,"E549"),sQuery(id+"F0.wireOp",EDGE,"E550"),sQuery(id+"F0.wireOp",EDGE,"E551"),sQuery(id+"F0.wireOp",EDGE,"E552"),sQuery(id+"F0.wireOp",EDGE,"E553"),sQuery(id+"F0.wireOp",EDGE,"E554"),sQuery(id+"F0.wireOp",EDGE,"E554"),sQuery(id+"F0.wireOp",EDGE,"E555"),sQuery(id+"F0.wireOp",EDGE,"E556"),sQuery(id+"F0.wireOp",EDGE,"E557"),sQuery(id+"F0.wireOp",EDGE,"E558"),sQuery(id+"F0.wireOp",EDGE,"E559"),sQuery(id+"F0.wireOp",EDGE,"E559"),sQuery(id+"F0.wireOp",EDGE,"E560"),sQuery(id+"F0.wireOp",EDGE,"E561")])]});
            var Q7;
            Q7=makeQuery(id+"F1.opExtrude","SWEPT_BODY",BODY,{"disambiguationData":[OSD([sQuery(id+"F0.wireOp",EDGE,"E795"),sQuery(id+"F0.wireOp",EDGE,"E796"),sQuery(id+"F0.wireOp",EDGE,"E797"),sQuery(id+"F0.wireOp",EDGE,"E798"),sQuery(id+"F0.wireOp",EDGE,"E799"),sQuery(id+"F0.wireOp",EDGE,"E800"),sQuery(id+"F0.wireOp",EDGE,"E801"),sQuery(id+"F0.wireOp",EDGE,"E802"),sQuery(id+"F0.wireOp",EDGE,"E803"),sQuery(id+"F0.wireOp",EDGE,"E804"),sQuery(id+"F0.wireOp",EDGE,"E805"),sQuery(id+"F0.wireOp",EDGE,"E806"),sQuery(id+"F0.wireOp",EDGE,"E807"),sQuery(id+"F0.wireOp",EDGE,"E808"),sQuery(id+"F0.wireOp",EDGE,"E809"),sQuery(id+"F0.wireOp",EDGE,"E810"),sQuery(id+"F0.wireOp",EDGE,"E811"),sQuery(id+"F0.wireOp",EDGE,"E811")])]});
            var Q8;
            Q8=makeQuery(id+"F1.opExtrude","SWEPT_BODY",BODY,{"disambiguationData":[OSD([sQuery(id+"F0.wireOp",EDGE,"E1082"),sQuery(id+"F0.wireOp",EDGE,"E1083"),sQuery(id+"F0.wireOp",EDGE,"E1084"),sQuery(id+"F0.wireOp",EDGE,"E1085"),sQuery(id+"F0.wireOp",EDGE,"E1086"),sQuery(id+"F0.wireOp",EDGE,"E1087"),sQuery(id+"F0.wireOp",EDGE,"E1088"),sQuery(id+"F0.wireOp",EDGE,"E1089"),sQuery(id+"F0.wireOp",EDGE,"E1090"),sQuery(id+"F0.wireOp",EDGE,"E1091"),sQuery(id+"F0.wireOp",EDGE,"E1092"),sQuery(id+"F0.wireOp",EDGE,"E1093"),sQuery(id+"F0.wireOp",EDGE,"E1094"),sQuery(id+"F0.wireOp",EDGE,"E1095"),sQuery(id+"F0.wireOp",EDGE,"E1096"),sQuery(id+"F0.wireOp",EDGE,"E1097"),sQuery(id+"F0.wireOp",EDGE,"E1098"),sQuery(id+"F0.wireOp",EDGE,"E1082")])]});
            var Q9;
            Q9=makeQuery(id+"F1.opExtrude","SWEPT_BODY",BODY,{"disambiguationData":[OSD([sQuery(id+"F0.wireOp",EDGE,"E1099"),sQuery(id+"F0.wireOp",EDGE,"E1100"),sQuery(id+"F0.wireOp",EDGE,"E1101"),sQuery(id+"F0.wireOp",EDGE,"E1102"),sQuery(id+"F0.wireOp",EDGE,"E1103"),sQuery(id+"F0.wireOp",EDGE,"E1104"),sQuery(id+"F0.wireOp",EDGE,"E1105"),sQuery(id+"F0.wireOp",EDGE,"E1106"),sQuery(id+"F0.wireOp",EDGE,"E1106"),sQuery(id+"F0.wireOp",EDGE,"E1107"),sQuery(id+"F0.wireOp",EDGE,"E1108"),sQuery(id+"F0.wireOp",EDGE,"E1109"),sQuery(id+"F0.wireOp",EDGE,"E1110"),sQuery(id+"F0.wireOp",EDGE,"E1111"),sQuery(id+"F0.wireOp",EDGE,"E1112"),sQuery(id+"F0.wireOp",EDGE,"E1099")])]});
            var Q10;
            Q10=makeQuery(id+"F1.opExtrude","SWEPT_BODY",BODY,{"disambiguationData":[OSD([sQuery(id+"F0.wireOp",EDGE,"E1432"),sQuery(id+"F0.wireOp",EDGE,"E1432"),sQuery(id+"F0.wireOp",EDGE,"E1432"),sQuery(id+"F0.wireOp",EDGE,"E1432"),sQuery(id+"F0.wireOp",EDGE,"E1432"),sQuery(id+"F0.wireOp",EDGE,"E1432"),sQuery(id+"F0.wireOp",EDGE,"E1433"),sQuery(id+"F0.wireOp",EDGE,"E1434"),sQuery(id+"F0.wireOp",EDGE,"E1435"),sQuery(id+"F0.wireOp",EDGE,"E1435"),sQuery(id+"F0.wireOp",EDGE,"E1436"),sQuery(id+"F0.wireOp",EDGE,"E1437"),sQuery(id+"F0.wireOp",EDGE,"E1437"),sQuery(id+"F0.wireOp",EDGE,"E1438"),sQuery(id+"F0.wireOp",EDGE,"E1439"),sQuery(id+"F0.wireOp",EDGE,"E1440"),sQuery(id+"F0.wireOp",EDGE,"E1441"),sQuery(id+"F0.wireOp",EDGE,"E1441"),sQuery(id+"F0.wireOp",EDGE,"E1442"),sQuery(id+"F0.wireOp",EDGE,"E1432")])]});
            var Q11;
            Q11=makeQuery(id+"F1.opExtrude","SWEPT_BODY",BODY,{"disambiguationData":[OSD([sQuery(id+"F0.wireOp",EDGE,"E1502"),sQuery(id+"F0.wireOp",EDGE,"E1503"),sQuery(id+"F0.wireOp",EDGE,"E1504"),sQuery(id+"F0.wireOp",EDGE,"E1504"),sQuery(id+"F0.wireOp",EDGE,"E1504"),sQuery(id+"F0.wireOp",EDGE,"E1505"),sQuery(id+"F0.wireOp",EDGE,"E1506"),sQuery(id+"F0.wireOp",EDGE,"E1506"),sQuery(id+"F0.wireOp",EDGE,"E1507"),sQuery(id+"F0.wireOp",EDGE,"E1508"),sQuery(id+"F0.wireOp",EDGE,"E1509"),sQuery(id+"F0.wireOp",EDGE,"E1509"),sQuery(id+"F0.wireOp",EDGE,"E1509"),sQuery(id+"F0.wireOp",EDGE,"E1509"),sQuery(id+"F0.wireOp",EDGE,"E1510"),sQuery(id+"F0.wireOp",EDGE,"E1511"),sQuery(id+"F0.wireOp",EDGE,"E1511"),sQuery(id+"F0.wireOp",EDGE,"E1512"),sQuery(id+"F0.wireOp",EDGE,"E1513"),sQuery(id+"F0.wireOp",EDGE,"E1514")])]});
            var Q12;
            Q12=makeQuery(id+"F1.opExtrude","SWEPT_BODY",BODY,{"disambiguationData":[OSD([sQuery(id+"F0.wireOp",EDGE,"E1642"),sQuery(id+"F0.wireOp",EDGE,"E1643"),sQuery(id+"F0.wireOp",EDGE,"E1644"),sQuery(id+"F0.wireOp",EDGE,"E1645"),sQuery(id+"F0.wireOp",EDGE,"E1645"),sQuery(id+"F0.wireOp",EDGE,"E1646"),sQuery(id+"F0.wireOp",EDGE,"E1647"),sQuery(id+"F0.wireOp",EDGE,"E1647"),sQuery(id+"F0.wireOp",EDGE,"E1647"),sQuery(id+"F0.wireOp",EDGE,"E1647"),sQuery(id+"F0.wireOp",EDGE,"E1647"),sQuery(id+"F0.wireOp",EDGE,"E1648"),sQuery(id+"F0.wireOp",EDGE,"E1649"),sQuery(id+"F0.wireOp",EDGE,"E1650"),sQuery(id+"F0.wireOp",EDGE,"E1651"),sQuery(id+"F0.wireOp",EDGE,"E1652"),sQuery(id+"F0.wireOp",EDGE,"E1652"),sQuery(id+"F0.wireOp",EDGE,"E1653"),sQuery(id+"F0.wireOp",EDGE,"E1654"),sQuery(id+"F0.wireOp",EDGE,"E1654")])]});
            var Q13;
            Q13=makeQuery(id+"F1.opExtrude","SWEPT_BODY",BODY,{"disambiguationData":[OSD([sQuery(id+"F0.wireOp",EDGE,"E1771"),sQuery(id+"F0.wireOp",EDGE,"E1772"),sQuery(id+"F0.wireOp",EDGE,"E1773"),sQuery(id+"F0.wireOp",EDGE,"E1773"),sQuery(id+"F0.wireOp",EDGE,"E1773"),sQuery(id+"F0.wireOp",EDGE,"E1773"),sQuery(id+"F0.wireOp",EDGE,"E1773"),sQuery(id+"F0.wireOp",EDGE,"E1773"),sQuery(id+"F0.wireOp",EDGE,"E1774"),sQuery(id+"F0.wireOp",EDGE,"E1775"),sQuery(id+"F0.wireOp",EDGE,"E1775"),sQuery(id+"F0.wireOp",EDGE,"E1776"),sQuery(id+"F0.wireOp",EDGE,"E1777"),sQuery(id+"F0.wireOp",EDGE,"E1777"),sQuery(id+"F0.wireOp",EDGE,"E1778"),sQuery(id+"F0.wireOp",EDGE,"E1779"),sQuery(id+"F0.wireOp",EDGE,"E1779"),sQuery(id+"F0.wireOp",EDGE,"E1780"),sQuery(id+"F0.wireOp",EDGE,"E1781"),sQuery(id+"F0.wireOp",EDGE,"E1782")])]});
            var Q14;
            Q14=makeQuery(id+"F1.opExtrude","SWEPT_BODY",BODY,{"disambiguationData":[OSD([sQuery(id+"F0.wireOp",EDGE,"E1856"),sQuery(id+"F0.wireOp",EDGE,"E1857"),sQuery(id+"F0.wireOp",EDGE,"E1858"),sQuery(id+"F0.wireOp",EDGE,"E1859"),sQuery(id+"F0.wireOp",EDGE,"E1859"),sQuery(id+"F0.wireOp",EDGE,"E1859"),sQuery(id+"F0.wireOp",EDGE,"E1859"),sQuery(id+"F0.wireOp",EDGE,"E1859"),sQuery(id+"F0.wireOp",EDGE,"E1860"),sQuery(id+"F0.wireOp",EDGE,"E1861"),sQuery(id+"F0.wireOp",EDGE,"E1861"),sQuery(id+"F0.wireOp",EDGE,"E1862"),sQuery(id+"F0.wireOp",EDGE,"E1863"),sQuery(id+"F0.wireOp",EDGE,"E1864"),sQuery(id+"F0.wireOp",EDGE,"E1865"),sQuery(id+"F0.wireOp",EDGE,"E1866"),sQuery(id+"F0.wireOp",EDGE,"E1867"),sQuery(id+"F0.wireOp",EDGE,"E1868"),sQuery(id+"F0.wireOp",EDGE,"E1869"),sQuery(id+"F0.wireOp",EDGE,"E1870")])]});
            var Q15;
            Q15=makeQuery(id+"F1.opExtrude","SWEPT_BODY",BODY,{"disambiguationData":[OSD([sQuery(id+"F0.wireOp",EDGE,"E1915"),sQuery(id+"F0.wireOp",EDGE,"E1916"),sQuery(id+"F0.wireOp",EDGE,"E1917"),sQuery(id+"F0.wireOp",EDGE,"E1917"),sQuery(id+"F0.wireOp",EDGE,"E1918"),sQuery(id+"F0.wireOp",EDGE,"E1919"),sQuery(id+"F0.wireOp",EDGE,"E1919"),sQuery(id+"F0.wireOp",EDGE,"E1919"),sQuery(id+"F0.wireOp",EDGE,"E1919"),sQuery(id+"F0.wireOp",EDGE,"E1920"),sQuery(id+"F0.wireOp",EDGE,"E1921"),sQuery(id+"F0.wireOp",EDGE,"E1922"),sQuery(id+"F0.wireOp",EDGE,"E1923"),sQuery(id+"F0.wireOp",EDGE,"E1924"),sQuery(id+"F0.wireOp",EDGE,"E1925"),sQuery(id+"F0.wireOp",EDGE,"E1926"),sQuery(id+"F0.wireOp",EDGE,"E1915"),sQuery(id+"F0.wireOp",EDGE,"E1915"),sQuery(id+"F0.wireOp",EDGE,"E1915"),sQuery(id+"F0.wireOp",EDGE,"E1915")])]});
            var Q16;
            Q16=makeQuery(id+"F1.opExtrude","SWEPT_BODY",BODY,{"disambiguationData":[OSD([sQuery(id+"F0.wireOp",EDGE,"E2217"),sQuery(id+"F0.wireOp",EDGE,"E2218"),sQuery(id+"F0.wireOp",EDGE,"E2219"),sQuery(id+"F0.wireOp",EDGE,"E2219"),sQuery(id+"F0.wireOp",EDGE,"E2220"),sQuery(id+"F0.wireOp",EDGE,"E2221"),sQuery(id+"F0.wireOp",EDGE,"E2221"),sQuery(id+"F0.wireOp",EDGE,"E2222"),sQuery(id+"F0.wireOp",EDGE,"E2223"),sQuery(id+"F0.wireOp",EDGE,"E2223"),sQuery(id+"F0.wireOp",EDGE,"E2224"),sQuery(id+"F0.wireOp",EDGE,"E2225"),sQuery(id+"F0.wireOp",EDGE,"E2225"),sQuery(id+"F0.wireOp",EDGE,"E2226"),sQuery(id+"F0.wireOp",EDGE,"E2227"),sQuery(id+"F0.wireOp",EDGE,"E2228"),sQuery(id+"F0.wireOp",EDGE,"E2229"),sQuery(id+"F0.wireOp",EDGE,"E2217")])]});
            var Q17;
            Q17=makeQuery(id+"F1.opExtrude","SWEPT_BODY",BODY,{"disambiguationData":[OSD([sQuery(id+"F0.wireOp",EDGE,"E2388"),sQuery(id+"F0.wireOp",EDGE,"E2389"),sQuery(id+"F0.wireOp",EDGE,"E2390"),sQuery(id+"F0.wireOp",EDGE,"E2391"),sQuery(id+"F0.wireOp",EDGE,"E2391"),sQuery(id+"F0.wireOp",EDGE,"E2392"),sQuery(id+"F0.wireOp",EDGE,"E2389"),sQuery(id+"F0.wireOp",EDGE,"E2389"),sQuery(id+"F0.wireOp",EDGE,"E2393"),sQuery(id+"F0.wireOp",EDGE,"E2394"),sQuery(id+"F0.wireOp",EDGE,"E2394"),sQuery(id+"F0.wireOp",EDGE,"E2395"),sQuery(id+"F0.wireOp",EDGE,"E2396"),sQuery(id+"F0.wireOp",EDGE,"E2396"),sQuery(id+"F0.wireOp",EDGE,"E2397"),sQuery(id+"F0.wireOp",EDGE,"E2398"),sQuery(id+"F0.wireOp",EDGE,"E2398"),sQuery(id+"F0.wireOp",EDGE,"E2399"),sQuery(id+"F0.wireOp",EDGE,"E2400"),sQuery(id+"F0.wireOp",EDGE,"E2401")])]});
            var Q18;
            Q18=makeQuery(id+"F1.opExtrude","SWEPT_BODY",BODY,{"disambiguationData":[OSD([sQuery(id+"F0.wireOp",EDGE,"E2537"),sQuery(id+"F0.wireOp",EDGE,"E2538"),sQuery(id+"F0.wireOp",EDGE,"E2539"),sQuery(id+"F0.wireOp",EDGE,"E2539"),sQuery(id+"F0.wireOp",EDGE,"E2540"),sQuery(id+"F0.wireOp",EDGE,"E2541"),sQuery(id+"F0.wireOp",EDGE,"E2541"),sQuery(id+"F0.wireOp",EDGE,"E2542"),sQuery(id+"F0.wireOp",EDGE,"E2543"),sQuery(id+"F0.wireOp",EDGE,"E2543"),sQuery(id+"F0.wireOp",EDGE,"E2544"),sQuery(id+"F0.wireOp",EDGE,"E2545"),sQuery(id+"F0.wireOp",EDGE,"E2546"),sQuery(id+"F0.wireOp",EDGE,"E2547"),sQuery(id+"F0.wireOp",EDGE,"E2548"),sQuery(id+"F0.wireOp",EDGE,"E2549"),sQuery(id+"F0.wireOp",EDGE,"E2549"),sQuery(id+"F0.wireOp",EDGE,"E2550"),sQuery(id+"F0.wireOp",EDGE,"E2551"),sQuery(id+"F0.wireOp",EDGE,"E2551"),sQuery(id+"F0.wireOp",EDGE,"E2552"),sQuery(id+"F0.wireOp",EDGE,"E2553"),sQuery(id+"F0.wireOp",EDGE,"E2553"),sQuery(id+"F0.wireOp",EDGE,"E2554"),sQuery(id+"F0.wireOp",EDGE,"E2555"),sQuery(id+"F0.wireOp",EDGE,"E2556")])]});
            var Q19;
            Q19=makeQuery(id+"F1.opExtrude","SWEPT_BODY",BODY,{"disambiguationData":[OSD([sQuery(id+"F0.wireOp",EDGE,"E2624"),sQuery(id+"F0.wireOp",EDGE,"E2625"),sQuery(id+"F0.wireOp",EDGE,"E2626"),sQuery(id+"F0.wireOp",EDGE,"E2626"),sQuery(id+"F0.wireOp",EDGE,"E2627"),sQuery(id+"F0.wireOp",EDGE,"E2628"),sQuery(id+"F0.wireOp",EDGE,"E2628"),sQuery(id+"F0.wireOp",EDGE,"E2629"),sQuery(id+"F0.wireOp",EDGE,"E2630"),sQuery(id+"F0.wireOp",EDGE,"E2631"),sQuery(id+"F0.wireOp",EDGE,"E2632"),sQuery(id+"F0.wireOp",EDGE,"E2633"),sQuery(id+"F0.wireOp",EDGE,"E2634"),sQuery(id+"F0.wireOp",EDGE,"E2635"),sQuery(id+"F0.wireOp",EDGE,"E2636"),sQuery(id+"F0.wireOp",EDGE,"E2637"),sQuery(id+"F0.wireOp",EDGE,"E2638"),sQuery(id+"F0.wireOp",EDGE,"E2639"),sQuery(id+"F0.wireOp",EDGE,"E2640"),sQuery(id+"F0.wireOp",EDGE,"E2640"),sQuery(id+"F0.wireOp",EDGE,"E2641"),sQuery(id+"F0.wireOp",EDGE,"E2642"),sQuery(id+"F0.wireOp",EDGE,"E2642"),sQuery(id+"F0.wireOp",EDGE,"E2643"),sQuery(id+"F0.wireOp",EDGE,"E2644"),sQuery(id+"F0.wireOp",EDGE,"E2645")])]});
            var Q20;
            Q20=qCreatedBy(makeId("Origin.pointOp"),VERTEX);
            transform(context, id + "F2", {"entities" : qUnion([Q0, Q1, Q2, Q3, Q4, Q5, Q6, Q7, Q8, Q9, Q10, Q11, Q12, Q13, Q14, Q15, Q16, Q17, Q18, Q19]), "transformType" : TransformType.SCALE_UNIFORMLY, "scale" : 20, "scalePoint" : qUnion([Q20]), "makeCopy" : false});
        }
        {
            var Q0;
            Q0=qCreatedBy(makeId("Top.planeOp"),FACE);
            cPlane(context, id + "F3", {"entities" : qUnion([Q0]), "cplaneType" : CPlaneType.OFFSET, "offset" : 1 * mm, "oppositeDirection" : true, "width" : 150 * mm, "height" : 150 * mm});
        }
        {
            var Q0;
            Q0=qCreatedBy(id+"F3.planeOp",FACE);
            var sketch = newSketch(context, id + "F4", { "sketchPlane" : qUnion([Q0])});
            skLineSegment(sketch, "E2670.bottom", {"start": v(-20, -20) * mm, "end": v(20, -20) * mm});
            skLineSegment(sketch, "E2670.top", {"start": v(-20, 20) * mm, "end": v(20, 20) * mm});
            skLineSegment(sketch, "E2670.left", {"start": v(-20, -20) * mm, "end": v(-20, 20) * mm});
            skLineSegment(sketch, "E2670.right", {"start": v(20, -20) * mm, "end": v(20, 20) * mm});
            skSolve(sketch);
        }
        {
            var Q0;
            Q0=qSketchRegion(id+"F4",true);
            var Q1;
            Q1=makeQuery(id+"F1.opExtrude","CAP_VERTEX",VERTEX,{"disambiguationData":[OSD([sQuery(id+"F0.wireOp",EDGE,"E2669.top"),sQuery(id+"F0.wireOp",EDGE,"E2669.right")])],"isStart":false});
            extrude(context, id + "F5", {"entities" : qUnion([Q0]), "endBound" : BoundingType.UP_TO_VERTEX, "depth" : 2 * mm, "endBoundEntityVertex" : qUnion([Q1]), "offsetDistance" : 25 * mm});
        }
        {
            var Q0;
            Q0=makeQuery(id+"F1.opExtrude","SWEPT_BODY",BODY,{"disambiguationData":[OSD([sQuery(id+"F0.wireOp",EDGE,"E0"),sQuery(id+"F0.wireOp",EDGE,"E1"),sQuery(id+"F0.wireOp",EDGE,"E2"),sQuery(id+"F0.wireOp",EDGE,"E3"),sQuery(id+"F0.wireOp",EDGE,"E3"),sQuery(id+"F0.wireOp",EDGE,"E4"),sQuery(id+"F0.wireOp",EDGE,"E5"),sQuery(id+"F0.wireOp",EDGE,"E6"),sQuery(id+"F0.wireOp",EDGE,"E7"),sQuery(id+"F0.wireOp",EDGE,"E8"),sQuery(id+"F0.wireOp",EDGE,"E9"),sQuery(id+"F0.wireOp",EDGE,"E10"),sQuery(id+"F0.wireOp",EDGE,"E11"),sQuery(id+"F0.wireOp",EDGE,"E12"),sQuery(id+"F0.wireOp",EDGE,"E13"),sQuery(id+"F0.wireOp",EDGE,"E14"),sQuery(id+"F0.wireOp",EDGE,"E15"),sQuery(id+"F0.wireOp",EDGE,"E16"),sQuery(id+"F0.wireOp",EDGE,"E17"),sQuery(id+"F0.wireOp",EDGE,"E18"),sQuery(id+"F0.wireOp",EDGE,"E19"),sQuery(id+"F0.wireOp",EDGE,"E20"),sQuery(id+"F0.wireOp",EDGE,"E21"),sQuery(id+"F0.wireOp",EDGE,"E22"),sQuery(id+"F0.wireOp",EDGE,"E23"),sQuery(id+"F0.wireOp",EDGE,"E24"),sQuery(id+"F0.wireOp",EDGE,"E25"),sQuery(id+"F0.wireOp",EDGE,"E26")])]});
            var Q1;
            Q1=makeQuery(id+"F1.opExtrude","SWEPT_BODY",BODY,{"disambiguationData":[OSD([sQuery(id+"F0.wireOp",EDGE,"E27"),sQuery(id+"F0.wireOp",EDGE,"E28"),sQuery(id+"F0.wireOp",EDGE,"E29"),sQuery(id+"F0.wireOp",EDGE,"E30"),sQuery(id+"F0.wireOp",EDGE,"E31"),sQuery(id+"F0.wireOp",EDGE,"E32"),sQuery(id+"F0.wireOp",EDGE,"E33"),sQuery(id+"F0.wireOp",EDGE,"E34"),sQuery(id+"F0.wireOp",EDGE,"E35"),sQuery(id+"F0.wireOp",EDGE,"E36"),sQuery(id+"F0.wireOp",EDGE,"E37"),sQuery(id+"F0.wireOp",EDGE,"E38"),sQuery(id+"F0.wireOp",EDGE,"E39"),sQuery(id+"F0.wireOp",EDGE,"E40"),sQuery(id+"F0.wireOp",EDGE,"E41"),sQuery(id+"F0.wireOp",EDGE,"E42"),sQuery(id+"F0.wireOp",EDGE,"E43"),sQuery(id+"F0.wireOp",EDGE,"E44"),sQuery(id+"F0.wireOp",EDGE,"E45"),sQuery(id+"F0.wireOp",EDGE,"E46"),sQuery(id+"F0.wireOp",EDGE,"E47"),sQuery(id+"F0.wireOp",EDGE,"E48"),sQuery(id+"F0.wireOp",EDGE,"E49"),sQuery(id+"F0.wireOp",EDGE,"E49"),sQuery(id+"F0.wireOp",EDGE,"E49"),sQuery(id+"F0.wireOp",EDGE,"E50"),sQuery(id+"F0.wireOp",EDGE,"E51"),sQuery(id+"F0.wireOp",EDGE,"E52"),sQuery(id+"F0.wireOp",EDGE,"E53"),sQuery(id+"F0.wireOp",EDGE,"E55"),sQuery(id+"F0.wireOp",EDGE,"E56"),sQuery(id+"F0.wireOp",EDGE,"E57"),sQuery(id+"F0.wireOp",EDGE,"E58"),sQuery(id+"F0.wireOp",EDGE,"E59"),sQuery(id+"F0.wireOp",EDGE,"E60"),sQuery(id+"F0.wireOp",EDGE,"E61"),sQuery(id+"F0.wireOp",EDGE,"E62"),sQuery(id+"F0.wireOp",EDGE,"E63"),sQuery(id+"F0.wireOp",EDGE,"E64"),sQuery(id+"F0.wireOp",EDGE,"E65"),sQuery(id+"F0.wireOp",EDGE,"E66"),sQuery(id+"F0.wireOp",EDGE,"E67"),sQuery(id+"F0.wireOp",EDGE,"E68"),sQuery(id+"F0.wireOp",EDGE,"E69"),sQuery(id+"F0.wireOp",EDGE,"E70"),sQuery(id+"F0.wireOp",EDGE,"E71"),sQuery(id+"F0.wireOp",EDGE,"E72"),sQuery(id+"F0.wireOp",EDGE,"E73")])]});
            var Q2;
            Q2=makeQuery(id+"F1.opExtrude","SWEPT_BODY",BODY,{"disambiguationData":[OSD([sQuery(id+"F0.wireOp",EDGE,"E74"),sQuery(id+"F0.wireOp",EDGE,"E75"),sQuery(id+"F0.wireOp",EDGE,"E76"),sQuery(id+"F0.wireOp",EDGE,"E77"),sQuery(id+"F0.wireOp",EDGE,"E78"),sQuery(id+"F0.wireOp",EDGE,"E79"),sQuery(id+"F0.wireOp",EDGE,"E80"),sQuery(id+"F0.wireOp",EDGE,"E81"),sQuery(id+"F0.wireOp",EDGE,"E82"),sQuery(id+"F0.wireOp",EDGE,"E83"),sQuery(id+"F0.wireOp",EDGE,"E84"),sQuery(id+"F0.wireOp",EDGE,"E85"),sQuery(id+"F0.wireOp",EDGE,"E86"),sQuery(id+"F0.wireOp",EDGE,"E87"),sQuery(id+"F0.wireOp",EDGE,"E88"),sQuery(id+"F0.wireOp",EDGE,"E89"),sQuery(id+"F0.wireOp",EDGE,"E90"),sQuery(id+"F0.wireOp",EDGE,"E91"),sQuery(id+"F0.wireOp",EDGE,"E92")])]});
            var Q3;
            Q3=makeQuery(id+"F1.opExtrude","SWEPT_BODY",BODY,{"disambiguationData":[OSD([sQuery(id+"F0.wireOp",EDGE,"E93"),sQuery(id+"F0.wireOp",EDGE,"E94"),sQuery(id+"F0.wireOp",EDGE,"E95"),sQuery(id+"F0.wireOp",EDGE,"E96"),sQuery(id+"F0.wireOp",EDGE,"E97"),sQuery(id+"F0.wireOp",EDGE,"E98"),sQuery(id+"F0.wireOp",EDGE,"E99"),sQuery(id+"F0.wireOp",EDGE,"E100"),sQuery(id+"F0.wireOp",EDGE,"E101"),sQuery(id+"F0.wireOp",EDGE,"E102"),sQuery(id+"F0.wireOp",EDGE,"E103"),sQuery(id+"F0.wireOp",EDGE,"E104"),sQuery(id+"F0.wireOp",EDGE,"E105"),sQuery(id+"F0.wireOp",EDGE,"E106"),sQuery(id+"F0.wireOp",EDGE,"E107"),sQuery(id+"F0.wireOp",EDGE,"E108"),sQuery(id+"F0.wireOp",EDGE,"E109"),sQuery(id+"F0.wireOp",EDGE,"E110"),sQuery(id+"F0.wireOp",EDGE,"E111"),sQuery(id+"F0.wireOp",EDGE,"E112"),sQuery(id+"F0.wireOp",EDGE,"E112"),sQuery(id+"F0.wireOp",EDGE,"E112"),sQuery(id+"F0.wireOp",EDGE,"E112"),sQuery(id+"F0.wireOp",EDGE,"E112"),sQuery(id+"F0.wireOp",EDGE,"E113"),sQuery(id+"F0.wireOp",EDGE,"E114"),sQuery(id+"F0.wireOp",EDGE,"E115"),sQuery(id+"F0.wireOp",EDGE,"E116"),sQuery(id+"F0.wireOp",EDGE,"E117"),sQuery(id+"F0.wireOp",EDGE,"E118"),sQuery(id+"F0.wireOp",EDGE,"E119"),sQuery(id+"F0.wireOp",EDGE,"E120"),sQuery(id+"F0.wireOp",EDGE,"E121"),sQuery(id+"F0.wireOp",EDGE,"E122"),sQuery(id+"F0.wireOp",EDGE,"E123"),sQuery(id+"F0.wireOp",EDGE,"E124"),sQuery(id+"F0.wireOp",EDGE,"E125"),sQuery(id+"F0.wireOp",EDGE,"E126"),sQuery(id+"F0.wireOp",EDGE,"E127"),sQuery(id+"F0.wireOp",EDGE,"E128"),sQuery(id+"F0.wireOp",EDGE,"E129"),sQuery(id+"F0.wireOp",EDGE,"E130"),sQuery(id+"F0.wireOp",EDGE,"E131"),sQuery(id+"F0.wireOp",EDGE,"E132"),sQuery(id+"F0.wireOp",EDGE,"E133"),sQuery(id+"F0.wireOp",EDGE,"E134"),sQuery(id+"F0.wireOp",EDGE,"E135"),sQuery(id+"F0.wireOp",EDGE,"E136"),sQuery(id+"F0.wireOp",EDGE,"E137"),sQuery(id+"F0.wireOp",EDGE,"E138"),sQuery(id+"F0.wireOp",EDGE,"E139"),sQuery(id+"F0.wireOp",EDGE,"E140"),sQuery(id+"F0.wireOp",EDGE,"E141"),sQuery(id+"F0.wireOp",EDGE,"E142"),sQuery(id+"F0.wireOp",EDGE,"E143"),sQuery(id+"F0.wireOp",EDGE,"E144"),sQuery(id+"F0.wireOp",EDGE,"E145"),sQuery(id+"F0.wireOp",EDGE,"E146"),sQuery(id+"F0.wireOp",EDGE,"E147"),sQuery(id+"F0.wireOp",EDGE,"E148"),sQuery(id+"F0.wireOp",EDGE,"E149"),sQuery(id+"F0.wireOp",EDGE,"E150"),sQuery(id+"F0.wireOp",EDGE,"E151"),sQuery(id+"F0.wireOp",EDGE,"E152"),sQuery(id+"F0.wireOp",EDGE,"E177"),sQuery(id+"F0.wireOp",EDGE,"E178"),sQuery(id+"F0.wireOp",EDGE,"E179"),sQuery(id+"F0.wireOp",EDGE,"E180"),sQuery(id+"F0.wireOp",EDGE,"E181"),sQuery(id+"F0.wireOp",EDGE,"E182"),sQuery(id+"F0.wireOp",EDGE,"E183"),sQuery(id+"F0.wireOp",EDGE,"E184"),sQuery(id+"F0.wireOp",EDGE,"E185"),sQuery(id+"F0.wireOp",EDGE,"E186"),sQuery(id+"F0.wireOp",EDGE,"E187"),sQuery(id+"F0.wireOp",EDGE,"E188"),sQuery(id+"F0.wireOp",EDGE,"E189"),sQuery(id+"F0.wireOp",EDGE,"E190"),sQuery(id+"F0.wireOp",EDGE,"E191"),sQuery(id+"F0.wireOp",EDGE,"E192"),sQuery(id+"F0.wireOp",EDGE,"E193"),sQuery(id+"F0.wireOp",EDGE,"E194"),sQuery(id+"F0.wireOp",EDGE,"E195"),sQuery(id+"F0.wireOp",EDGE,"E196"),sQuery(id+"F0.wireOp",EDGE,"E197"),sQuery(id+"F0.wireOp",EDGE,"E198"),sQuery(id+"F0.wireOp",EDGE,"E199"),sQuery(id+"F0.wireOp",EDGE,"E200"),sQuery(id+"F0.wireOp",EDGE,"E201"),sQuery(id+"F0.wireOp",EDGE,"E202"),sQuery(id+"F0.wireOp",EDGE,"E203"),sQuery(id+"F0.wireOp",EDGE,"E203"),sQuery(id+"F0.wireOp",EDGE,"E204"),sQuery(id+"F0.wireOp",EDGE,"E205"),sQuery(id+"F0.wireOp",EDGE,"E205"),sQuery(id+"F0.wireOp",EDGE,"E206"),sQuery(id+"F0.wireOp",EDGE,"E207"),sQuery(id+"F0.wireOp",EDGE,"E207"),sQuery(id+"F0.wireOp",EDGE,"E208"),sQuery(id+"F0.wireOp",EDGE,"E209"),sQuery(id+"F0.wireOp",EDGE,"E210"),sQuery(id+"F0.wireOp",EDGE,"E210"),sQuery(id+"F0.wireOp",EDGE,"E210"),sQuery(id+"F0.wireOp",EDGE,"E211"),sQuery(id+"F0.wireOp",EDGE,"E212"),sQuery(id+"F0.wireOp",EDGE,"E212"),sQuery(id+"F0.wireOp",EDGE,"E213"),sQuery(id+"F0.wireOp",EDGE,"E214"),sQuery(id+"F0.wireOp",EDGE,"E215"),sQuery(id+"F0.wireOp",EDGE,"E216"),sQuery(id+"F0.wireOp",EDGE,"E216"),sQuery(id+"F0.wireOp",EDGE,"E216"),sQuery(id+"F0.wireOp",EDGE,"E216"),sQuery(id+"F0.wireOp",EDGE,"E216"),sQuery(id+"F0.wireOp",EDGE,"E217"),sQuery(id+"F0.wireOp",EDGE,"E218"),sQuery(id+"F0.wireOp",EDGE,"E218"),sQuery(id+"F0.wireOp",EDGE,"E219"),sQuery(id+"F0.wireOp",EDGE,"E220"),sQuery(id+"F0.wireOp",EDGE,"E220"),sQuery(id+"F0.wireOp",EDGE,"E221"),sQuery(id+"F0.wireOp",EDGE,"E222"),sQuery(id+"F0.wireOp",EDGE,"E223"),sQuery(id+"F0.wireOp",EDGE,"E224"),sQuery(id+"F0.wireOp",EDGE,"E225"),sQuery(id+"F0.wireOp",EDGE,"E226"),sQuery(id+"F0.wireOp",EDGE,"E227"),sQuery(id+"F0.wireOp",EDGE,"E228"),sQuery(id+"F0.wireOp",EDGE,"E229"),sQuery(id+"F0.wireOp",EDGE,"E230"),sQuery(id+"F0.wireOp",EDGE,"E230"),sQuery(id+"F0.wireOp",EDGE,"E230"),sQuery(id+"F0.wireOp",EDGE,"E230"),sQuery(id+"F0.wireOp",EDGE,"E230"),sQuery(id+"F0.wireOp",EDGE,"E231"),sQuery(id+"F0.wireOp",EDGE,"E232"),sQuery(id+"F0.wireOp",EDGE,"E233"),sQuery(id+"F0.wireOp",EDGE,"E234"),sQuery(id+"F0.wireOp",EDGE,"E235"),sQuery(id+"F0.wireOp",EDGE,"E235"),sQuery(id+"F0.wireOp",EDGE,"E236"),sQuery(id+"F0.wireOp",EDGE,"E237"),sQuery(id+"F0.wireOp",EDGE,"E237"),sQuery(id+"F0.wireOp",EDGE,"E238"),sQuery(id+"F0.wireOp",EDGE,"E239"),sQuery(id+"F0.wireOp",EDGE,"E240"),sQuery(id+"F0.wireOp",EDGE,"E241"),sQuery(id+"F0.wireOp",EDGE,"E242"),sQuery(id+"F0.wireOp",EDGE,"E243"),sQuery(id+"F0.wireOp",EDGE,"E243"),sQuery(id+"F0.wireOp",EDGE,"E244"),sQuery(id+"F0.wireOp",EDGE,"E245"),sQuery(id+"F0.wireOp",EDGE,"E245"),sQuery(id+"F0.wireOp",EDGE,"E246"),sQuery(id+"F0.wireOp",EDGE,"E247"),sQuery(id+"F0.wireOp",EDGE,"E247"),sQuery(id+"F0.wireOp",EDGE,"E248"),sQuery(id+"F0.wireOp",EDGE,"E249"),sQuery(id+"F0.wireOp",EDGE,"E249"),sQuery(id+"F0.wireOp",EDGE,"E250"),sQuery(id+"F0.wireOp",EDGE,"E251"),sQuery(id+"F0.wireOp",EDGE,"E252"),sQuery(id+"F0.wireOp",EDGE,"E252"),sQuery(id+"F0.wireOp",EDGE,"E253"),sQuery(id+"F0.wireOp",EDGE,"E254"),sQuery(id+"F0.wireOp",EDGE,"E255"),sQuery(id+"F0.wireOp",EDGE,"E256"),sQuery(id+"F0.wireOp",EDGE,"E257"),sQuery(id+"F0.wireOp",EDGE,"E258"),sQuery(id+"F0.wireOp",EDGE,"E259"),sQuery(id+"F0.wireOp",EDGE,"E260"),sQuery(id+"F0.wireOp",EDGE,"E201"),sQuery(id+"F0.wireOp",EDGE,"E261"),sQuery(id+"F0.wireOp",EDGE,"E262"),sQuery(id+"F0.wireOp",EDGE,"E262"),sQuery(id+"F0.wireOp",EDGE,"E262"),sQuery(id+"F0.wireOp",EDGE,"E262"),sQuery(id+"F0.wireOp",EDGE,"E263"),sQuery(id+"F0.wireOp",EDGE,"E264"),sQuery(id+"F0.wireOp",EDGE,"E264"),sQuery(id+"F0.wireOp",EDGE,"E265"),sQuery(id+"F0.wireOp",EDGE,"E266"),sQuery(id+"F0.wireOp",EDGE,"E267"),sQuery(id+"F0.wireOp",EDGE,"E268"),sQuery(id+"F0.wireOp",EDGE,"E269"),sQuery(id+"F0.wireOp",EDGE,"E270"),sQuery(id+"F0.wireOp",EDGE,"E271"),sQuery(id+"F0.wireOp",EDGE,"E271"),sQuery(id+"F0.wireOp",EDGE,"E272"),sQuery(id+"F0.wireOp",EDGE,"E273"),sQuery(id+"F0.wireOp",EDGE,"E274"),sQuery(id+"F0.wireOp",EDGE,"E275"),sQuery(id+"F0.wireOp",EDGE,"E275"),sQuery(id+"F0.wireOp",EDGE,"E276"),sQuery(id+"F0.wireOp",EDGE,"E277"),sQuery(id+"F0.wireOp",EDGE,"E278"),sQuery(id+"F0.wireOp",EDGE,"E279"),sQuery(id+"F0.wireOp",EDGE,"E280"),sQuery(id+"F0.wireOp",EDGE,"E281"),sQuery(id+"F0.wireOp",EDGE,"E282"),sQuery(id+"F0.wireOp",EDGE,"E283"),sQuery(id+"F0.wireOp",EDGE,"E284"),sQuery(id+"F0.wireOp",EDGE,"E285"),sQuery(id+"F0.wireOp",EDGE,"E286"),sQuery(id+"F0.wireOp",EDGE,"E286"),sQuery(id+"F0.wireOp",EDGE,"E286"),sQuery(id+"F0.wireOp",EDGE,"E286"),sQuery(id+"F0.wireOp",EDGE,"E287"),sQuery(id+"F0.wireOp",EDGE,"E288"),sQuery(id+"F0.wireOp",EDGE,"E288"),sQuery(id+"F0.wireOp",EDGE,"E289"),sQuery(id+"F0.wireOp",EDGE,"E290"),sQuery(id+"F0.wireOp",EDGE,"E290"),sQuery(id+"F0.wireOp",EDGE,"E291"),sQuery(id+"F0.wireOp",EDGE,"E292"),sQuery(id+"F0.wireOp",EDGE,"E293"),sQuery(id+"F0.wireOp",EDGE,"E294"),sQuery(id+"F0.wireOp",EDGE,"E294"),sQuery(id+"F0.wireOp",EDGE,"E295"),sQuery(id+"F0.wireOp",EDGE,"E296"),sQuery(id+"F0.wireOp",EDGE,"E297"),sQuery(id+"F0.wireOp",EDGE,"E298"),sQuery(id+"F0.wireOp",EDGE,"E298"),sQuery(id+"F0.wireOp",EDGE,"E298"),sQuery(id+"F0.wireOp",EDGE,"E298"),sQuery(id+"F0.wireOp",EDGE,"E299"),sQuery(id+"F0.wireOp",EDGE,"E300"),sQuery(id+"F0.wireOp",EDGE,"E301"),sQuery(id+"F0.wireOp",EDGE,"E302"),sQuery(id+"F0.wireOp",EDGE,"E303"),sQuery(id+"F0.wireOp",EDGE,"E303"),sQuery(id+"F0.wireOp",EDGE,"E304"),sQuery(id+"F0.wireOp",EDGE,"E305"),sQuery(id+"F0.wireOp",EDGE,"E305"),sQuery(id+"F0.wireOp",EDGE,"E306"),sQuery(id+"F0.wireOp",EDGE,"E307"),sQuery(id+"F0.wireOp",EDGE,"E308"),sQuery(id+"F0.wireOp",EDGE,"E309"),sQuery(id+"F0.wireOp",EDGE,"E310"),sQuery(id+"F0.wireOp",EDGE,"E311"),sQuery(id+"F0.wireOp",EDGE,"E312"),sQuery(id+"F0.wireOp",EDGE,"E312"),sQuery(id+"F0.wireOp",EDGE,"E313"),sQuery(id+"F0.wireOp",EDGE,"E314"),sQuery(id+"F0.wireOp",EDGE,"E314"),sQuery(id+"F0.wireOp",EDGE,"E315"),sQuery(id+"F0.wireOp",EDGE,"E316"),sQuery(id+"F0.wireOp",EDGE,"E316"),sQuery(id+"F0.wireOp",EDGE,"E317"),sQuery(id+"F0.wireOp",EDGE,"E318"),sQuery(id+"F0.wireOp",EDGE,"E319"),sQuery(id+"F0.wireOp",EDGE,"E319"),sQuery(id+"F0.wireOp",EDGE,"E319"),sQuery(id+"F0.wireOp",EDGE,"E320"),sQuery(id+"F0.wireOp",EDGE,"E321"),sQuery(id+"F0.wireOp",EDGE,"E321"),sQuery(id+"F0.wireOp",EDGE,"E322"),sQuery(id+"F0.wireOp",EDGE,"E323"),sQuery(id+"F0.wireOp",EDGE,"E324"),sQuery(id+"F0.wireOp",EDGE,"E325"),sQuery(id+"F0.wireOp",EDGE,"E326"),sQuery(id+"F0.wireOp",EDGE,"E327"),sQuery(id+"F0.wireOp",EDGE,"E328"),sQuery(id+"F0.wireOp",EDGE,"E328"),sQuery(id+"F0.wireOp",EDGE,"E329"),sQuery(id+"F0.wireOp",EDGE,"E330"),sQuery(id+"F0.wireOp",EDGE,"E331"),sQuery(id+"F0.wireOp",EDGE,"E332"),sQuery(id+"F0.wireOp",EDGE,"E333"),sQuery(id+"F0.wireOp",EDGE,"E333"),sQuery(id+"F0.wireOp",EDGE,"E334"),sQuery(id+"F0.wireOp",EDGE,"E335"),sQuery(id+"F0.wireOp",EDGE,"E335"),sQuery(id+"F0.wireOp",EDGE,"E336"),sQuery(id+"F0.wireOp",EDGE,"E337"),sQuery(id+"F0.wireOp",EDGE,"E337"),sQuery(id+"F0.wireOp",EDGE,"E338"),sQuery(id+"F0.wireOp",EDGE,"E339"),sQuery(id+"F0.wireOp",EDGE,"E340"),sQuery(id+"F0.wireOp",EDGE,"E341"),sQuery(id+"F0.wireOp",EDGE,"E342"),sQuery(id+"F0.wireOp",EDGE,"E343"),sQuery(id+"F0.wireOp",EDGE,"E344"),sQuery(id+"F0.wireOp",EDGE,"E345"),sQuery(id+"F0.wireOp",EDGE,"E346"),sQuery(id+"F0.wireOp",EDGE,"E347"),sQuery(id+"F0.wireOp",EDGE,"E348"),sQuery(id+"F0.wireOp",EDGE,"E348"),sQuery(id+"F0.wireOp",EDGE,"E349"),sQuery(id+"F0.wireOp",EDGE,"E350"),sQuery(id+"F0.wireOp",EDGE,"E351"),sQuery(id+"F0.wireOp",EDGE,"E352"),sQuery(id+"F0.wireOp",EDGE,"E352"),sQuery(id+"F0.wireOp",EDGE,"E352"),sQuery(id+"F0.wireOp",EDGE,"E352"),sQuery(id+"F0.wireOp",EDGE,"E353"),sQuery(id+"F0.wireOp",EDGE,"E354"),sQuery(id+"F0.wireOp",EDGE,"E355"),sQuery(id+"F0.wireOp",EDGE,"E356"),sQuery(id+"F0.wireOp",EDGE,"E357"),sQuery(id+"F0.wireOp",EDGE,"E358"),sQuery(id+"F0.wireOp",EDGE,"E359"),sQuery(id+"F0.wireOp",EDGE,"E360"),sQuery(id+"F0.wireOp",EDGE,"E360"),sQuery(id+"F0.wireOp",EDGE,"E360"),sQuery(id+"F0.wireOp",EDGE,"E360"),sQuery(id+"F0.wireOp",EDGE,"E360"),sQuery(id+"F0.wireOp",EDGE,"E360"),sQuery(id+"F0.wireOp",EDGE,"E360"),sQuery(id+"F0.wireOp",EDGE,"E360"),sQuery(id+"F0.wireOp",EDGE,"E361"),sQuery(id+"F0.wireOp",EDGE,"E362"),sQuery(id+"F0.wireOp",EDGE,"E363"),sQuery(id+"F0.wireOp",EDGE,"E364"),sQuery(id+"F0.wireOp",EDGE,"E365"),sQuery(id+"F0.wireOp",EDGE,"E365"),sQuery(id+"F0.wireOp",EDGE,"E365"),sQuery(id+"F0.wireOp",EDGE,"E366"),sQuery(id+"F0.wireOp",EDGE,"E367"),sQuery(id+"F0.wireOp",EDGE,"E367"),sQuery(id+"F0.wireOp",EDGE,"E368"),sQuery(id+"F0.wireOp",EDGE,"E369"),sQuery(id+"F0.wireOp",EDGE,"E370"),sQuery(id+"F0.wireOp",EDGE,"E371"),sQuery(id+"F0.wireOp",EDGE,"E371"),sQuery(id+"F0.wireOp",EDGE,"E372"),sQuery(id+"F0.wireOp",EDGE,"E373"),sQuery(id+"F0.wireOp",EDGE,"E373"),sQuery(id+"F0.wireOp",EDGE,"E374"),sQuery(id+"F0.wireOp",EDGE,"E375"),sQuery(id+"F0.wireOp",EDGE,"E375"),sQuery(id+"F0.wireOp",EDGE,"E376"),sQuery(id+"F0.wireOp",EDGE,"E377"),sQuery(id+"F0.wireOp",EDGE,"E378"),sQuery(id+"F0.wireOp",EDGE,"E379"),sQuery(id+"F0.wireOp",EDGE,"E380"),sQuery(id+"F0.wireOp",EDGE,"E381"),sQuery(id+"F0.wireOp",EDGE,"E382"),sQuery(id+"F0.wireOp",EDGE,"E383"),sQuery(id+"F0.wireOp",EDGE,"E384"),sQuery(id+"F0.wireOp",EDGE,"E385"),sQuery(id+"F0.wireOp",EDGE,"E386"),sQuery(id+"F0.wireOp",EDGE,"E386"),sQuery(id+"F0.wireOp",EDGE,"E387"),sQuery(id+"F0.wireOp",EDGE,"E388"),sQuery(id+"F0.wireOp",EDGE,"E389"),sQuery(id+"F0.wireOp",EDGE,"E390"),sQuery(id+"F0.wireOp",EDGE,"E391"),sQuery(id+"F0.wireOp",EDGE,"E391"),sQuery(id+"F0.wireOp",EDGE,"E392"),sQuery(id+"F0.wireOp",EDGE,"E393"),sQuery(id+"F0.wireOp",EDGE,"E393"),sQuery(id+"F0.wireOp",EDGE,"E394"),sQuery(id+"F0.wireOp",EDGE,"E395"),sQuery(id+"F0.wireOp",EDGE,"E396"),sQuery(id+"F0.wireOp",EDGE,"E397"),sQuery(id+"F0.wireOp",EDGE,"E398"),sQuery(id+"F0.wireOp",EDGE,"E399"),sQuery(id+"F0.wireOp",EDGE,"E399"),sQuery(id+"F0.wireOp",EDGE,"E399"),sQuery(id+"F0.wireOp",EDGE,"E400"),sQuery(id+"F0.wireOp",EDGE,"E401"),sQuery(id+"F0.wireOp",EDGE,"E401"),sQuery(id+"F0.wireOp",EDGE,"E402"),sQuery(id+"F0.wireOp",EDGE,"E403"),sQuery(id+"F0.wireOp",EDGE,"E403"),sQuery(id+"F0.wireOp",EDGE,"E403"),sQuery(id+"F0.wireOp",EDGE,"E403"),sQuery(id+"F0.wireOp",EDGE,"E403"),sQuery(id+"F0.wireOp",EDGE,"E404"),sQuery(id+"F0.wireOp",EDGE,"E405"),sQuery(id+"F0.wireOp",EDGE,"E406"),sQuery(id+"F0.wireOp",EDGE,"E407"),sQuery(id+"F0.wireOp",EDGE,"E408"),sQuery(id+"F0.wireOp",EDGE,"E409"),sQuery(id+"F0.wireOp",EDGE,"E410"),sQuery(id+"F0.wireOp",EDGE,"E411"),sQuery(id+"F0.wireOp",EDGE,"E412"),sQuery(id+"F0.wireOp",EDGE,"E413"),sQuery(id+"F0.wireOp",EDGE,"E413"),sQuery(id+"F0.wireOp",EDGE,"E413"),sQuery(id+"F0.wireOp",EDGE,"E413"),sQuery(id+"F0.wireOp",EDGE,"E413"),sQuery(id+"F0.wireOp",EDGE,"E414"),sQuery(id+"F0.wireOp",EDGE,"E415"),sQuery(id+"F0.wireOp",EDGE,"E416"),sQuery(id+"F0.wireOp",EDGE,"E417"),sQuery(id+"F0.wireOp",EDGE,"E418"),sQuery(id+"F0.wireOp",EDGE,"E419"),sQuery(id+"F0.wireOp",EDGE,"E420"),sQuery(id+"F0.wireOp",EDGE,"E421"),sQuery(id+"F0.wireOp",EDGE,"E421"),sQuery(id+"F0.wireOp",EDGE,"E422"),sQuery(id+"F0.wireOp",EDGE,"E423"),sQuery(id+"F0.wireOp",EDGE,"E423"),sQuery(id+"F0.wireOp",EDGE,"E423"),sQuery(id+"F0.wireOp",EDGE,"E423"),sQuery(id+"F0.wireOp",EDGE,"E423"),sQuery(id+"F0.wireOp",EDGE,"E424"),sQuery(id+"F0.wireOp",EDGE,"E425"),sQuery(id+"F0.wireOp",EDGE,"E426"),sQuery(id+"F0.wireOp",EDGE,"E427"),sQuery(id+"F0.wireOp",EDGE,"E428"),sQuery(id+"F0.wireOp",EDGE,"E429"),sQuery(id+"F0.wireOp",EDGE,"E429"),sQuery(id+"F0.wireOp",EDGE,"E430"),sQuery(id+"F0.wireOp",EDGE,"E431"),sQuery(id+"F0.wireOp",EDGE,"E432"),sQuery(id+"F0.wireOp",EDGE,"E432"),sQuery(id+"F0.wireOp",EDGE,"E432"),sQuery(id+"F0.wireOp",EDGE,"E432"),sQuery(id+"F0.wireOp",EDGE,"E432"),sQuery(id+"F0.wireOp",EDGE,"E433"),sQuery(id+"F0.wireOp",EDGE,"E434"),sQuery(id+"F0.wireOp",EDGE,"E434"),sQuery(id+"F0.wireOp",EDGE,"E435"),sQuery(id+"F0.wireOp",EDGE,"E436"),sQuery(id+"F0.wireOp",EDGE,"E437"),sQuery(id+"F0.wireOp",EDGE,"E438"),sQuery(id+"F0.wireOp",EDGE,"E439"),sQuery(id+"F0.wireOp",EDGE,"E464"),sQuery(id+"F0.wireOp",EDGE,"E465"),sQuery(id+"F0.wireOp",EDGE,"E466"),sQuery(id+"F0.wireOp",EDGE,"E467"),sQuery(id+"F0.wireOp",EDGE,"E468"),sQuery(id+"F0.wireOp",EDGE,"E469"),sQuery(id+"F0.wireOp",EDGE,"E470"),sQuery(id+"F0.wireOp",EDGE,"E471"),sQuery(id+"F0.wireOp",EDGE,"E472"),sQuery(id+"F0.wireOp",EDGE,"E473"),sQuery(id+"F0.wireOp",EDGE,"E474"),sQuery(id+"F0.wireOp",EDGE,"E475"),sQuery(id+"F0.wireOp",EDGE,"E476"),sQuery(id+"F0.wireOp",EDGE,"E477"),sQuery(id+"F0.wireOp",EDGE,"E478"),sQuery(id+"F0.wireOp",EDGE,"E479"),sQuery(id+"F0.wireOp",EDGE,"E480"),sQuery(id+"F0.wireOp",EDGE,"E481"),sQuery(id+"F0.wireOp",EDGE,"E482"),sQuery(id+"F0.wireOp",EDGE,"E483"),sQuery(id+"F0.wireOp",EDGE,"E484"),sQuery(id+"F0.wireOp",EDGE,"E485"),sQuery(id+"F0.wireOp",EDGE,"E486"),sQuery(id+"F0.wireOp",EDGE,"E487"),sQuery(id+"F0.wireOp",EDGE,"E488"),sQuery(id+"F0.wireOp",EDGE,"E489"),sQuery(id+"F0.wireOp",EDGE,"E490"),sQuery(id+"F0.wireOp",EDGE,"E491"),sQuery(id+"F0.wireOp",EDGE,"E492"),sQuery(id+"F0.wireOp",EDGE,"E493"),sQuery(id+"F0.wireOp",EDGE,"E493"),sQuery(id+"F0.wireOp",EDGE,"E494"),sQuery(id+"F0.wireOp",EDGE,"E495"),sQuery(id+"F0.wireOp",EDGE,"E496"),sQuery(id+"F0.wireOp",EDGE,"E497"),sQuery(id+"F0.wireOp",EDGE,"E498"),sQuery(id+"F0.wireOp",EDGE,"E499"),sQuery(id+"F0.wireOp",EDGE,"E500"),sQuery(id+"F0.wireOp",EDGE,"E501"),sQuery(id+"F0.wireOp",EDGE,"E502"),sQuery(id+"F0.wireOp",EDGE,"E502"),sQuery(id+"F0.wireOp",EDGE,"E502"),sQuery(id+"F0.wireOp",EDGE,"E503"),sQuery(id+"F0.wireOp",EDGE,"E504"),sQuery(id+"F0.wireOp",EDGE,"E504"),sQuery(id+"F0.wireOp",EDGE,"E504"),sQuery(id+"F0.wireOp",EDGE,"E504"),sQuery(id+"F0.wireOp",EDGE,"E505"),sQuery(id+"F0.wireOp",EDGE,"E506"),sQuery(id+"F0.wireOp",EDGE,"E506"),sQuery(id+"F0.wireOp",EDGE,"E507"),sQuery(id+"F0.wireOp",EDGE,"E508"),sQuery(id+"F0.wireOp",EDGE,"E508"),sQuery(id+"F0.wireOp",EDGE,"E509"),sQuery(id+"F0.wireOp",EDGE,"E510"),sQuery(id+"F0.wireOp",EDGE,"E510"),sQuery(id+"F0.wireOp",EDGE,"E510"),sQuery(id+"F0.wireOp",EDGE,"E511"),sQuery(id+"F0.wireOp",EDGE,"E512"),sQuery(id+"F0.wireOp",EDGE,"E512"),sQuery(id+"F0.wireOp",EDGE,"E512"),sQuery(id+"F0.wireOp",EDGE,"E512"),sQuery(id+"F0.wireOp",EDGE,"E512"),sQuery(id+"F0.wireOp",EDGE,"E513"),sQuery(id+"F0.wireOp",EDGE,"E514"),sQuery(id+"F0.wireOp",EDGE,"E515"),sQuery(id+"F0.wireOp",EDGE,"E516"),sQuery(id+"F0.wireOp",EDGE,"E517"),sQuery(id+"F0.wireOp",EDGE,"E518"),sQuery(id+"F0.wireOp",EDGE,"E518"),sQuery(id+"F0.wireOp",EDGE,"E518"),sQuery(id+"F0.wireOp",EDGE,"E518"),sQuery(id+"F0.wireOp",EDGE,"E519"),sQuery(id+"F0.wireOp",EDGE,"E520"),sQuery(id+"F0.wireOp",EDGE,"E520"),sQuery(id+"F0.wireOp",EDGE,"E521"),sQuery(id+"F0.wireOp",EDGE,"E522"),sQuery(id+"F0.wireOp",EDGE,"E523"),sQuery(id+"F0.wireOp",EDGE,"E524"),sQuery(id+"F0.wireOp",EDGE,"E525"),sQuery(id+"F0.wireOp",EDGE,"E525"),sQuery(id+"F0.wireOp",EDGE,"E526"),sQuery(id+"F0.wireOp",EDGE,"E527"),sQuery(id+"F0.wireOp",EDGE,"E528"),sQuery(id+"F0.wireOp",EDGE,"E529"),sQuery(id+"F0.wireOp",EDGE,"E530"),sQuery(id+"F0.wireOp",EDGE,"E531"),sQuery(id+"F0.wireOp",EDGE,"E531"),sQuery(id+"F0.wireOp",EDGE,"E531"),sQuery(id+"F0.wireOp",EDGE,"E531"),sQuery(id+"F0.wireOp",EDGE,"E531"),sQuery(id+"F0.wireOp",EDGE,"E532"),sQuery(id+"F0.wireOp",EDGE,"E533"),sQuery(id+"F0.wireOp",EDGE,"E534"),sQuery(id+"F0.wireOp",EDGE,"E535"),sQuery(id+"F0.wireOp",EDGE,"E536"),sQuery(id+"F0.wireOp",EDGE,"E536"),sQuery(id+"F0.wireOp",EDGE,"E537"),sQuery(id+"F0.wireOp",EDGE,"E538"),sQuery(id+"F0.wireOp",EDGE,"E539"),sQuery(id+"F0.wireOp",EDGE,"E562"),sQuery(id+"F0.wireOp",EDGE,"E563"),sQuery(id+"F0.wireOp",EDGE,"E564"),sQuery(id+"F0.wireOp",EDGE,"E565"),sQuery(id+"F0.wireOp",EDGE,"E566"),sQuery(id+"F0.wireOp",EDGE,"E567"),sQuery(id+"F0.wireOp",EDGE,"E568"),sQuery(id+"F0.wireOp",EDGE,"E569"),sQuery(id+"F0.wireOp",EDGE,"E570"),sQuery(id+"F0.wireOp",EDGE,"E571"),sQuery(id+"F0.wireOp",EDGE,"E572"),sQuery(id+"F0.wireOp",EDGE,"E573"),sQuery(id+"F0.wireOp",EDGE,"E574"),sQuery(id+"F0.wireOp",EDGE,"E575"),sQuery(id+"F0.wireOp",EDGE,"E576"),sQuery(id+"F0.wireOp",EDGE,"E577"),sQuery(id+"F0.wireOp",EDGE,"E578"),sQuery(id+"F0.wireOp",EDGE,"E579"),sQuery(id+"F0.wireOp",EDGE,"E580"),sQuery(id+"F0.wireOp",EDGE,"E581"),sQuery(id+"F0.wireOp",EDGE,"E582"),sQuery(id+"F0.wireOp",EDGE,"E583"),sQuery(id+"F0.wireOp",EDGE,"E584"),sQuery(id+"F0.wireOp",EDGE,"E585"),sQuery(id+"F0.wireOp",EDGE,"E586"),sQuery(id+"F0.wireOp",EDGE,"E587"),sQuery(id+"F0.wireOp",EDGE,"E588"),sQuery(id+"F0.wireOp",EDGE,"E589"),sQuery(id+"F0.wireOp",EDGE,"E590"),sQuery(id+"F0.wireOp",EDGE,"E591"),sQuery(id+"F0.wireOp",EDGE,"E591"),sQuery(id+"F0.wireOp",EDGE,"E592"),sQuery(id+"F0.wireOp",EDGE,"E593"),sQuery(id+"F0.wireOp",EDGE,"E594"),sQuery(id+"F0.wireOp",EDGE,"E595"),sQuery(id+"F0.wireOp",EDGE,"E596"),sQuery(id+"F0.wireOp",EDGE,"E597"),sQuery(id+"F0.wireOp",EDGE,"E598"),sQuery(id+"F0.wireOp",EDGE,"E598"),sQuery(id+"F0.wireOp",EDGE,"E598"),sQuery(id+"F0.wireOp",EDGE,"E599"),sQuery(id+"F0.wireOp",EDGE,"E600"),sQuery(id+"F0.wireOp",EDGE,"E601"),sQuery(id+"F0.wireOp",EDGE,"E602"),sQuery(id+"F0.wireOp",EDGE,"E603"),sQuery(id+"F0.wireOp",EDGE,"E603"),sQuery(id+"F0.wireOp",EDGE,"E603"),sQuery(id+"F0.wireOp",EDGE,"E603"),sQuery(id+"F0.wireOp",EDGE,"E604"),sQuery(id+"F0.wireOp",EDGE,"E605"),sQuery(id+"F0.wireOp",EDGE,"E605"),sQuery(id+"F0.wireOp",EDGE,"E605"),sQuery(id+"F0.wireOp",EDGE,"E606"),sQuery(id+"F0.wireOp",EDGE,"E607"),sQuery(id+"F0.wireOp",EDGE,"E608"),sQuery(id+"F0.wireOp",EDGE,"E609"),sQuery(id+"F0.wireOp",EDGE,"E610"),sQuery(id+"F0.wireOp",EDGE,"E611"),sQuery(id+"F0.wireOp",EDGE,"E612"),sQuery(id+"F0.wireOp",EDGE,"E612"),sQuery(id+"F0.wireOp",EDGE,"E612"),sQuery(id+"F0.wireOp",EDGE,"E612"),sQuery(id+"F0.wireOp",EDGE,"E613"),sQuery(id+"F0.wireOp",EDGE,"E614"),sQuery(id+"F0.wireOp",EDGE,"E614"),sQuery(id+"F0.wireOp",EDGE,"E615"),sQuery(id+"F0.wireOp",EDGE,"E616"),sQuery(id+"F0.wireOp",EDGE,"E616"),sQuery(id+"F0.wireOp",EDGE,"E616"),sQuery(id+"F0.wireOp",EDGE,"E616"),sQuery(id+"F0.wireOp",EDGE,"E617"),sQuery(id+"F0.wireOp",EDGE,"E618"),sQuery(id+"F0.wireOp",EDGE,"E619"),sQuery(id+"F0.wireOp",EDGE,"E619"),sQuery(id+"F0.wireOp",EDGE,"E619"),sQuery(id+"F0.wireOp",EDGE,"E619"),sQuery(id+"F0.wireOp",EDGE,"E620"),sQuery(id+"F0.wireOp",EDGE,"E621"),sQuery(id+"F0.wireOp",EDGE,"E621"),sQuery(id+"F0.wireOp",EDGE,"E622"),sQuery(id+"F0.wireOp",EDGE,"E623"),sQuery(id+"F0.wireOp",EDGE,"E623"),sQuery(id+"F0.wireOp",EDGE,"E623"),sQuery(id+"F0.wireOp",EDGE,"E623"),sQuery(id+"F0.wireOp",EDGE,"E624"),sQuery(id+"F0.wireOp",EDGE,"E625"),sQuery(id+"F0.wireOp",EDGE,"E626"),sQuery(id+"F0.wireOp",EDGE,"E627"),sQuery(id+"F0.wireOp",EDGE,"E628"),sQuery(id+"F0.wireOp",EDGE,"E628"),sQuery(id+"F0.wireOp",EDGE,"E629"),sQuery(id+"F0.wireOp",EDGE,"E630"),sQuery(id+"F0.wireOp",EDGE,"E631"),sQuery(id+"F0.wireOp",EDGE,"E632"),sQuery(id+"F0.wireOp",EDGE,"E633"),sQuery(id+"F0.wireOp",EDGE,"E633"),sQuery(id+"F0.wireOp",EDGE,"E634"),sQuery(id+"F0.wireOp",EDGE,"E635"),sQuery(id+"F0.wireOp",EDGE,"E635"),sQuery(id+"F0.wireOp",EDGE,"E636"),sQuery(id+"F0.wireOp",EDGE,"E637"),sQuery(id+"F0.wireOp",EDGE,"E637"),sQuery(id+"F0.wireOp",EDGE,"E637"),sQuery(id+"F0.wireOp",EDGE,"E637"),sQuery(id+"F0.wireOp",EDGE,"E637"),sQuery(id+"F0.wireOp",EDGE,"E638"),sQuery(id+"F0.wireOp",EDGE,"E639"),sQuery(id+"F0.wireOp",EDGE,"E639"),sQuery(id+"F0.wireOp",EDGE,"E640"),sQuery(id+"F0.wireOp",EDGE,"E641"),sQuery(id+"F0.wireOp",EDGE,"E642"),sQuery(id+"F0.wireOp",EDGE,"E643"),sQuery(id+"F0.wireOp",EDGE,"E644"),sQuery(id+"F0.wireOp",EDGE,"E644"),sQuery(id+"F0.wireOp",EDGE,"E645"),sQuery(id+"F0.wireOp",EDGE,"E646"),sQuery(id+"F0.wireOp",EDGE,"E647"),sQuery(id+"F0.wireOp",EDGE,"E648"),sQuery(id+"F0.wireOp",EDGE,"E649"),sQuery(id+"F0.wireOp",EDGE,"E650"),sQuery(id+"F0.wireOp",EDGE,"E651"),sQuery(id+"F0.wireOp",EDGE,"E652"),sQuery(id+"F0.wireOp",EDGE,"E653"),sQuery(id+"F0.wireOp",EDGE,"E654"),sQuery(id+"F0.wireOp",EDGE,"E655"),sQuery(id+"F0.wireOp",EDGE,"E656"),sQuery(id+"F0.wireOp",EDGE,"E657"),sQuery(id+"F0.wireOp",EDGE,"E658"),sQuery(id+"F0.wireOp",EDGE,"E659"),sQuery(id+"F0.wireOp",EDGE,"E660"),sQuery(id+"F0.wireOp",EDGE,"E660"),sQuery(id+"F0.wireOp",EDGE,"E661"),sQuery(id+"F0.wireOp",EDGE,"E662"),sQuery(id+"F0.wireOp",EDGE,"E662"),sQuery(id+"F0.wireOp",EDGE,"E663"),sQuery(id+"F0.wireOp",EDGE,"E664"),sQuery(id+"F0.wireOp",EDGE,"E665"),sQuery(id+"F0.wireOp",EDGE,"E666"),sQuery(id+"F0.wireOp",EDGE,"E667"),sQuery(id+"F0.wireOp",EDGE,"E668"),sQuery(id+"F0.wireOp",EDGE,"E669"),sQuery(id+"F0.wireOp",EDGE,"E669"),sQuery(id+"F0.wireOp",EDGE,"E670"),sQuery(id+"F0.wireOp",EDGE,"E671"),sQuery(id+"F0.wireOp",EDGE,"E672"),sQuery(id+"F0.wireOp",EDGE,"E673"),sQuery(id+"F0.wireOp",EDGE,"E674"),sQuery(id+"F0.wireOp",EDGE,"E674"),sQuery(id+"F0.wireOp",EDGE,"E675"),sQuery(id+"F0.wireOp",EDGE,"E676"),sQuery(id+"F0.wireOp",EDGE,"E676"),sQuery(id+"F0.wireOp",EDGE,"E677"),sQuery(id+"F0.wireOp",EDGE,"E678"),sQuery(id+"F0.wireOp",EDGE,"E678"),sQuery(id+"F0.wireOp",EDGE,"E679"),sQuery(id+"F0.wireOp",EDGE,"E680"),sQuery(id+"F0.wireOp",EDGE,"E681"),sQuery(id+"F0.wireOp",EDGE,"E682"),sQuery(id+"F0.wireOp",EDGE,"E683"),sQuery(id+"F0.wireOp",EDGE,"E683"),sQuery(id+"F0.wireOp",EDGE,"E684"),sQuery(id+"F0.wireOp",EDGE,"E685"),sQuery(id+"F0.wireOp",EDGE,"E686"),sQuery(id+"F0.wireOp",EDGE,"E687"),sQuery(id+"F0.wireOp",EDGE,"E688"),sQuery(id+"F0.wireOp",EDGE,"E689"),sQuery(id+"F0.wireOp",EDGE,"E690"),sQuery(id+"F0.wireOp",EDGE,"E691"),sQuery(id+"F0.wireOp",EDGE,"E692"),sQuery(id+"F0.wireOp",EDGE,"E692"),sQuery(id+"F0.wireOp",EDGE,"E693"),sQuery(id+"F0.wireOp",EDGE,"E694"),sQuery(id+"F0.wireOp",EDGE,"E694"),sQuery(id+"F0.wireOp",EDGE,"E695"),sQuery(id+"F0.wireOp",EDGE,"E696"),sQuery(id+"F0.wireOp",EDGE,"E697"),sQuery(id+"F0.wireOp",EDGE,"E697"),sQuery(id+"F0.wireOp",EDGE,"E698"),sQuery(id+"F0.wireOp",EDGE,"E699"),sQuery(id+"F0.wireOp",EDGE,"E700"),sQuery(id+"F0.wireOp",EDGE,"E700"),sQuery(id+"F0.wireOp",EDGE,"E701"),sQuery(id+"F0.wireOp",EDGE,"E702"),sQuery(id+"F0.wireOp",EDGE,"E703"),sQuery(id+"F0.wireOp",EDGE,"E704"),sQuery(id+"F0.wireOp",EDGE,"E705"),sQuery(id+"F0.wireOp",EDGE,"E706"),sQuery(id+"F0.wireOp",EDGE,"E707"),sQuery(id+"F0.wireOp",EDGE,"E631"),sQuery(id+"F0.wireOp",EDGE,"E708"),sQuery(id+"F0.wireOp",EDGE,"E709"),sQuery(id+"F0.wireOp",EDGE,"E710"),sQuery(id+"F0.wireOp",EDGE,"E710"),sQuery(id+"F0.wireOp",EDGE,"E711"),sQuery(id+"F0.wireOp",EDGE,"E712"),sQuery(id+"F0.wireOp",EDGE,"E712"),sQuery(id+"F0.wireOp",EDGE,"E713"),sQuery(id+"F0.wireOp",EDGE,"E714"),sQuery(id+"F0.wireOp",EDGE,"E714"),sQuery(id+"F0.wireOp",EDGE,"E715"),sQuery(id+"F0.wireOp",EDGE,"E716"),sQuery(id+"F0.wireOp",EDGE,"E716"),sQuery(id+"F0.wireOp",EDGE,"E717"),sQuery(id+"F0.wireOp",EDGE,"E718"),sQuery(id+"F0.wireOp",EDGE,"E718"),sQuery(id+"F0.wireOp",EDGE,"E719"),sQuery(id+"F0.wireOp",EDGE,"E720"),sQuery(id+"F0.wireOp",EDGE,"E721"),sQuery(id+"F0.wireOp",EDGE,"E722"),sQuery(id+"F0.wireOp",EDGE,"E723"),sQuery(id+"F0.wireOp",EDGE,"E724"),sQuery(id+"F0.wireOp",EDGE,"E725"),sQuery(id+"F0.wireOp",EDGE,"E726"),sQuery(id+"F0.wireOp",EDGE,"E727"),sQuery(id+"F0.wireOp",EDGE,"E728"),sQuery(id+"F0.wireOp",EDGE,"E728"),sQuery(id+"F0.wireOp",EDGE,"E729"),sQuery(id+"F0.wireOp",EDGE,"E730"),sQuery(id+"F0.wireOp",EDGE,"E731"),sQuery(id+"F0.wireOp",EDGE,"E732"),sQuery(id+"F0.wireOp",EDGE,"E733"),sQuery(id+"F0.wireOp",EDGE,"E734"),sQuery(id+"F0.wireOp",EDGE,"E734"),sQuery(id+"F0.wireOp",EDGE,"E735"),sQuery(id+"F0.wireOp",EDGE,"E736"),sQuery(id+"F0.wireOp",EDGE,"E737"),sQuery(id+"F0.wireOp",EDGE,"E737"),sQuery(id+"F0.wireOp",EDGE,"E738"),sQuery(id+"F0.wireOp",EDGE,"E739"),sQuery(id+"F0.wireOp",EDGE,"E739"),sQuery(id+"F0.wireOp",EDGE,"E739"),sQuery(id+"F0.wireOp",EDGE,"E740"),sQuery(id+"F0.wireOp",EDGE,"E741"),sQuery(id+"F0.wireOp",EDGE,"E742"),sQuery(id+"F0.wireOp",EDGE,"E742"),sQuery(id+"F0.wireOp",EDGE,"E743"),sQuery(id+"F0.wireOp",EDGE,"E744"),sQuery(id+"F0.wireOp",EDGE,"E744"),sQuery(id+"F0.wireOp",EDGE,"E744"),sQuery(id+"F0.wireOp",EDGE,"E744"),sQuery(id+"F0.wireOp",EDGE,"E745"),sQuery(id+"F0.wireOp",EDGE,"E746"),sQuery(id+"F0.wireOp",EDGE,"E746"),sQuery(id+"F0.wireOp",EDGE,"E747"),sQuery(id+"F0.wireOp",EDGE,"E748"),sQuery(id+"F0.wireOp",EDGE,"E748"),sQuery(id+"F0.wireOp",EDGE,"E749"),sQuery(id+"F0.wireOp",EDGE,"E750"),sQuery(id+"F0.wireOp",EDGE,"E751"),sQuery(id+"F0.wireOp",EDGE,"E752"),sQuery(id+"F0.wireOp",EDGE,"E753"),sQuery(id+"F0.wireOp",EDGE,"E754"),sQuery(id+"F0.wireOp",EDGE,"E755"),sQuery(id+"F0.wireOp",EDGE,"E756"),sQuery(id+"F0.wireOp",EDGE,"E757"),sQuery(id+"F0.wireOp",EDGE,"E758"),sQuery(id+"F0.wireOp",EDGE,"E759"),sQuery(id+"F0.wireOp",EDGE,"E760"),sQuery(id+"F0.wireOp",EDGE,"E761"),sQuery(id+"F0.wireOp",EDGE,"E762"),sQuery(id+"F0.wireOp",EDGE,"E763"),sQuery(id+"F0.wireOp",EDGE,"E764"),sQuery(id+"F0.wireOp",EDGE,"E765"),sQuery(id+"F0.wireOp",EDGE,"E766"),sQuery(id+"F0.wireOp",EDGE,"E766"),sQuery(id+"F0.wireOp",EDGE,"E767"),sQuery(id+"F0.wireOp",EDGE,"E768"),sQuery(id+"F0.wireOp",EDGE,"E769"),sQuery(id+"F0.wireOp",EDGE,"E770"),sQuery(id+"F0.wireOp",EDGE,"E708"),sQuery(id+"F0.wireOp",EDGE,"E771"),sQuery(id+"F0.wireOp",EDGE,"E772"),sQuery(id+"F0.wireOp",EDGE,"E773"),sQuery(id+"F0.wireOp",EDGE,"E774"),sQuery(id+"F0.wireOp",EDGE,"E775"),sQuery(id+"F0.wireOp",EDGE,"E776"),sQuery(id+"F0.wireOp",EDGE,"E777"),sQuery(id+"F0.wireOp",EDGE,"E777"),sQuery(id+"F0.wireOp",EDGE,"E778"),sQuery(id+"F0.wireOp",EDGE,"E779"),sQuery(id+"F0.wireOp",EDGE,"E779"),sQuery(id+"F0.wireOp",EDGE,"E779"),sQuery(id+"F0.wireOp",EDGE,"E779"),sQuery(id+"F0.wireOp",EDGE,"E780"),sQuery(id+"F0.wireOp",EDGE,"E781"),sQuery(id+"F0.wireOp",EDGE,"E781"),sQuery(id+"F0.wireOp",EDGE,"E781"),sQuery(id+"F0.wireOp",EDGE,"E781"),sQuery(id+"F0.wireOp",EDGE,"E782"),sQuery(id+"F0.wireOp",EDGE,"E783"),sQuery(id+"F0.wireOp",EDGE,"E784"),sQuery(id+"F0.wireOp",EDGE,"E785"),sQuery(id+"F0.wireOp",EDGE,"E786"),sQuery(id+"F0.wireOp",EDGE,"E786"),sQuery(id+"F0.wireOp",EDGE,"E787"),sQuery(id+"F0.wireOp",EDGE,"E788"),sQuery(id+"F0.wireOp",EDGE,"E789"),sQuery(id+"F0.wireOp",EDGE,"E790"),sQuery(id+"F0.wireOp",EDGE,"E791"),sQuery(id+"F0.wireOp",EDGE,"E792"),sQuery(id+"F0.wireOp",EDGE,"E793"),sQuery(id+"F0.wireOp",EDGE,"E793"),sQuery(id+"F0.wireOp",EDGE,"E793"),sQuery(id+"F0.wireOp",EDGE,"E793"),sQuery(id+"F0.wireOp",EDGE,"E793"),sQuery(id+"F0.wireOp",EDGE,"E794"),sQuery(id+"F0.wireOp",EDGE,"E771"),sQuery(id+"F0.wireOp",EDGE,"E812"),sQuery(id+"F0.wireOp",EDGE,"E813"),sQuery(id+"F0.wireOp",EDGE,"E814"),sQuery(id+"F0.wireOp",EDGE,"E814"),sQuery(id+"F0.wireOp",EDGE,"E815"),sQuery(id+"F0.wireOp",EDGE,"E816"),sQuery(id+"F0.wireOp",EDGE,"E817"),sQuery(id+"F0.wireOp",EDGE,"E818"),sQuery(id+"F0.wireOp",EDGE,"E819"),sQuery(id+"F0.wireOp",EDGE,"E819"),sQuery(id+"F0.wireOp",EDGE,"E820"),sQuery(id+"F0.wireOp",EDGE,"E821"),sQuery(id+"F0.wireOp",EDGE,"E822"),sQuery(id+"F0.wireOp",EDGE,"E823"),sQuery(id+"F0.wireOp",EDGE,"E824"),sQuery(id+"F0.wireOp",EDGE,"E825"),sQuery(id+"F0.wireOp",EDGE,"E826"),sQuery(id+"F0.wireOp",EDGE,"E827"),sQuery(id+"F0.wireOp",EDGE,"E828"),sQuery(id+"F0.wireOp",EDGE,"E829"),sQuery(id+"F0.wireOp",EDGE,"E830"),sQuery(id+"F0.wireOp",EDGE,"E831"),sQuery(id+"F0.wireOp",EDGE,"E832"),sQuery(id+"F0.wireOp",EDGE,"E832"),sQuery(id+"F0.wireOp",EDGE,"E833"),sQuery(id+"F0.wireOp",EDGE,"E834"),sQuery(id+"F0.wireOp",EDGE,"E835"),sQuery(id+"F0.wireOp",EDGE,"E836"),sQuery(id+"F0.wireOp",EDGE,"E837"),sQuery(id+"F0.wireOp",EDGE,"E838"),sQuery(id+"F0.wireOp",EDGE,"E839"),sQuery(id+"F0.wireOp",EDGE,"E840"),sQuery(id+"F0.wireOp",EDGE,"E841"),sQuery(id+"F0.wireOp",EDGE,"E842"),sQuery(id+"F0.wireOp",EDGE,"E843"),sQuery(id+"F0.wireOp",EDGE,"E844"),sQuery(id+"F0.wireOp",EDGE,"E845"),sQuery(id+"F0.wireOp",EDGE,"E846"),sQuery(id+"F0.wireOp",EDGE,"E847"),sQuery(id+"F0.wireOp",EDGE,"E848"),sQuery(id+"F0.wireOp",EDGE,"E849"),sQuery(id+"F0.wireOp",EDGE,"E850"),sQuery(id+"F0.wireOp",EDGE,"E851"),sQuery(id+"F0.wireOp",EDGE,"E852"),sQuery(id+"F0.wireOp",EDGE,"E853"),sQuery(id+"F0.wireOp",EDGE,"E854"),sQuery(id+"F0.wireOp",EDGE,"E854"),sQuery(id+"F0.wireOp",EDGE,"E855"),sQuery(id+"F0.wireOp",EDGE,"E856"),sQuery(id+"F0.wireOp",EDGE,"E856"),sQuery(id+"F0.wireOp",EDGE,"E857"),sQuery(id+"F0.wireOp",EDGE,"E858"),sQuery(id+"F0.wireOp",EDGE,"E858"),sQuery(id+"F0.wireOp",EDGE,"E859"),sQuery(id+"F0.wireOp",EDGE,"E812"),sQuery(id+"F0.wireOp",EDGE,"E860"),sQuery(id+"F0.wireOp",EDGE,"E861"),sQuery(id+"F0.wireOp",EDGE,"E862"),sQuery(id+"F0.wireOp",EDGE,"E863"),sQuery(id+"F0.wireOp",EDGE,"E864"),sQuery(id+"F0.wireOp",EDGE,"E864"),sQuery(id+"F0.wireOp",EDGE,"E864"),sQuery(id+"F0.wireOp",EDGE,"E865"),sQuery(id+"F0.wireOp",EDGE,"E866"),sQuery(id+"F0.wireOp",EDGE,"E867"),sQuery(id+"F0.wireOp",EDGE,"E867"),sQuery(id+"F0.wireOp",EDGE,"E868"),sQuery(id+"F0.wireOp",EDGE,"E869"),sQuery(id+"F0.wireOp",EDGE,"E870"),sQuery(id+"F0.wireOp",EDGE,"E871"),sQuery(id+"F0.wireOp",EDGE,"E872"),sQuery(id+"F0.wireOp",EDGE,"E873"),sQuery(id+"F0.wireOp",EDGE,"E873"),sQuery(id+"F0.wireOp",EDGE,"E874"),sQuery(id+"F0.wireOp",EDGE,"E875"),sQuery(id+"F0.wireOp",EDGE,"E876"),sQuery(id+"F0.wireOp",EDGE,"E877"),sQuery(id+"F0.wireOp",EDGE,"E878"),sQuery(id+"F0.wireOp",EDGE,"E878"),sQuery(id+"F0.wireOp",EDGE,"E878"),sQuery(id+"F0.wireOp",EDGE,"E879"),sQuery(id+"F0.wireOp",EDGE,"E880"),sQuery(id+"F0.wireOp",EDGE,"E881"),sQuery(id+"F0.wireOp",EDGE,"E882"),sQuery(id+"F0.wireOp",EDGE,"E882"),sQuery(id+"F0.wireOp",EDGE,"E882"),sQuery(id+"F0.wireOp",EDGE,"E882"),sQuery(id+"F0.wireOp",EDGE,"E883"),sQuery(id+"F0.wireOp",EDGE,"E884"),sQuery(id+"F0.wireOp",EDGE,"E884"),sQuery(id+"F0.wireOp",EDGE,"E885"),sQuery(id+"F0.wireOp",EDGE,"E860"),sQuery(id+"F0.wireOp",EDGE,"E886"),sQuery(id+"F0.wireOp",EDGE,"E887"),sQuery(id+"F0.wireOp",EDGE,"E888"),sQuery(id+"F0.wireOp",EDGE,"E888"),sQuery(id+"F0.wireOp",EDGE,"E889"),sQuery(id+"F0.wireOp",EDGE,"E890"),sQuery(id+"F0.wireOp",EDGE,"E891"),sQuery(id+"F0.wireOp",EDGE,"E892"),sQuery(id+"F0.wireOp",EDGE,"E893"),sQuery(id+"F0.wireOp",EDGE,"E894"),sQuery(id+"F0.wireOp",EDGE,"E895"),sQuery(id+"F0.wireOp",EDGE,"E895"),sQuery(id+"F0.wireOp",EDGE,"E896"),sQuery(id+"F0.wireOp",EDGE,"E897"),sQuery(id+"F0.wireOp",EDGE,"E898"),sQuery(id+"F0.wireOp",EDGE,"E899"),sQuery(id+"F0.wireOp",EDGE,"E900"),sQuery(id+"F0.wireOp",EDGE,"E900"),sQuery(id+"F0.wireOp",EDGE,"E901"),sQuery(id+"F0.wireOp",EDGE,"E902"),sQuery(id+"F0.wireOp",EDGE,"E902"),sQuery(id+"F0.wireOp",EDGE,"E903"),sQuery(id+"F0.wireOp",EDGE,"E904"),sQuery(id+"F0.wireOp",EDGE,"E905"),sQuery(id+"F0.wireOp",EDGE,"E906"),sQuery(id+"F0.wireOp",EDGE,"E907"),sQuery(id+"F0.wireOp",EDGE,"E908"),sQuery(id+"F0.wireOp",EDGE,"E908"),sQuery(id+"F0.wireOp",EDGE,"E908"),sQuery(id+"F0.wireOp",EDGE,"E908"),sQuery(id+"F0.wireOp",EDGE,"E909"),sQuery(id+"F0.wireOp",EDGE,"E910"),sQuery(id+"F0.wireOp",EDGE,"E911"),sQuery(id+"F0.wireOp",EDGE,"E912"),sQuery(id+"F0.wireOp",EDGE,"E913"),sQuery(id+"F0.wireOp",EDGE,"E914"),sQuery(id+"F0.wireOp",EDGE,"E915"),sQuery(id+"F0.wireOp",EDGE,"E916"),sQuery(id+"F0.wireOp",EDGE,"E916"),sQuery(id+"F0.wireOp",EDGE,"E917"),sQuery(id+"F0.wireOp",EDGE,"E918"),sQuery(id+"F0.wireOp",EDGE,"E919"),sQuery(id+"F0.wireOp",EDGE,"E920"),sQuery(id+"F0.wireOp",EDGE,"E921"),sQuery(id+"F0.wireOp",EDGE,"E922"),sQuery(id+"F0.wireOp",EDGE,"E923"),sQuery(id+"F0.wireOp",EDGE,"E924"),sQuery(id+"F0.wireOp",EDGE,"E924"),sQuery(id+"F0.wireOp",EDGE,"E925"),sQuery(id+"F0.wireOp",EDGE,"E926"),sQuery(id+"F0.wireOp",EDGE,"E926"),sQuery(id+"F0.wireOp",EDGE,"E927"),sQuery(id+"F0.wireOp",EDGE,"E928"),sQuery(id+"F0.wireOp",EDGE,"E929"),sQuery(id+"F0.wireOp",EDGE,"E930"),sQuery(id+"F0.wireOp",EDGE,"E931"),sQuery(id+"F0.wireOp",EDGE,"E932"),sQuery(id+"F0.wireOp",EDGE,"E933"),sQuery(id+"F0.wireOp",EDGE,"E934"),sQuery(id+"F0.wireOp",EDGE,"E935"),sQuery(id+"F0.wireOp",EDGE,"E936"),sQuery(id+"F0.wireOp",EDGE,"E937"),sQuery(id+"F0.wireOp",EDGE,"E937"),sQuery(id+"F0.wireOp",EDGE,"E938"),sQuery(id+"F0.wireOp",EDGE,"E939"),sQuery(id+"F0.wireOp",EDGE,"E940"),sQuery(id+"F0.wireOp",EDGE,"E941"),sQuery(id+"F0.wireOp",EDGE,"E941"),sQuery(id+"F0.wireOp",EDGE,"E942"),sQuery(id+"F0.wireOp",EDGE,"E943"),sQuery(id+"F0.wireOp",EDGE,"E944"),sQuery(id+"F0.wireOp",EDGE,"E945"),sQuery(id+"F0.wireOp",EDGE,"E946"),sQuery(id+"F0.wireOp",EDGE,"E946"),sQuery(id+"F0.wireOp",EDGE,"E947"),sQuery(id+"F0.wireOp",EDGE,"E948"),sQuery(id+"F0.wireOp",EDGE,"E949"),sQuery(id+"F0.wireOp",EDGE,"E950"),sQuery(id+"F0.wireOp",EDGE,"E951"),sQuery(id+"F0.wireOp",EDGE,"E952"),sQuery(id+"F0.wireOp",EDGE,"E952"),sQuery(id+"F0.wireOp",EDGE,"E953"),sQuery(id+"F0.wireOp",EDGE,"E954"),sQuery(id+"F0.wireOp",EDGE,"E955"),sQuery(id+"F0.wireOp",EDGE,"E956"),sQuery(id+"F0.wireOp",EDGE,"E957"),sQuery(id+"F0.wireOp",EDGE,"E958"),sQuery(id+"F0.wireOp",EDGE,"E959"),sQuery(id+"F0.wireOp",EDGE,"E960"),sQuery(id+"F0.wireOp",EDGE,"E961"),sQuery(id+"F0.wireOp",EDGE,"E962"),sQuery(id+"F0.wireOp",EDGE,"E963"),sQuery(id+"F0.wireOp",EDGE,"E964"),sQuery(id+"F0.wireOp",EDGE,"E965"),sQuery(id+"F0.wireOp",EDGE,"E966"),sQuery(id+"F0.wireOp",EDGE,"E967"),sQuery(id+"F0.wireOp",EDGE,"E968"),sQuery(id+"F0.wireOp",EDGE,"E968"),sQuery(id+"F0.wireOp",EDGE,"E969"),sQuery(id+"F0.wireOp",EDGE,"E970"),sQuery(id+"F0.wireOp",EDGE,"E970"),sQuery(id+"F0.wireOp",EDGE,"E971"),sQuery(id+"F0.wireOp",EDGE,"E972"),sQuery(id+"F0.wireOp",EDGE,"E972"),sQuery(id+"F0.wireOp",EDGE,"E973"),sQuery(id+"F0.wireOp",EDGE,"E974"),sQuery(id+"F0.wireOp",EDGE,"E975"),sQuery(id+"F0.wireOp",EDGE,"E976"),sQuery(id+"F0.wireOp",EDGE,"E977"),sQuery(id+"F0.wireOp",EDGE,"E977"),sQuery(id+"F0.wireOp",EDGE,"E978"),sQuery(id+"F0.wireOp",EDGE,"E979"),sQuery(id+"F0.wireOp",EDGE,"E979"),sQuery(id+"F0.wireOp",EDGE,"E980"),sQuery(id+"F0.wireOp",EDGE,"E981"),sQuery(id+"F0.wireOp",EDGE,"E981"),sQuery(id+"F0.wireOp",EDGE,"E982"),sQuery(id+"F0.wireOp",EDGE,"E983"),sQuery(id+"F0.wireOp",EDGE,"E984"),sQuery(id+"F0.wireOp",EDGE,"E985"),sQuery(id+"F0.wireOp",EDGE,"E986"),sQuery(id+"F0.wireOp",EDGE,"E987"),sQuery(id+"F0.wireOp",EDGE,"E988"),sQuery(id+"F0.wireOp",EDGE,"E989"),sQuery(id+"F0.wireOp",EDGE,"E990"),sQuery(id+"F0.wireOp",EDGE,"E991"),sQuery(id+"F0.wireOp",EDGE,"E992"),sQuery(id+"F0.wireOp",EDGE,"E993"),sQuery(id+"F0.wireOp",EDGE,"E994"),sQuery(id+"F0.wireOp",EDGE,"E995"),sQuery(id+"F0.wireOp",EDGE,"E995"),sQuery(id+"F0.wireOp",EDGE,"E996"),sQuery(id+"F0.wireOp",EDGE,"E997"),sQuery(id+"F0.wireOp",EDGE,"E998"),sQuery(id+"F0.wireOp",EDGE,"E999"),sQuery(id+"F0.wireOp",EDGE,"E1000"),sQuery(id+"F0.wireOp",EDGE,"E1000"),sQuery(id+"F0.wireOp",EDGE,"E1001"),sQuery(id+"F0.wireOp",EDGE,"E1002"),sQuery(id+"F0.wireOp",EDGE,"E1003"),sQuery(id+"F0.wireOp",EDGE,"E1004"),sQuery(id+"F0.wireOp",EDGE,"E1005"),sQuery(id+"F0.wireOp",EDGE,"E1006"),sQuery(id+"F0.wireOp",EDGE,"E1007"),sQuery(id+"F0.wireOp",EDGE,"E1008"),sQuery(id+"F0.wireOp",EDGE,"E1009"),sQuery(id+"F0.wireOp",EDGE,"E1010"),sQuery(id+"F0.wireOp",EDGE,"E1011"),sQuery(id+"F0.wireOp",EDGE,"E1012"),sQuery(id+"F0.wireOp",EDGE,"E1013"),sQuery(id+"F0.wireOp",EDGE,"E1013"),sQuery(id+"F0.wireOp",EDGE,"E1013"),sQuery(id+"F0.wireOp",EDGE,"E1013"),sQuery(id+"F0.wireOp",EDGE,"E1013"),sQuery(id+"F0.wireOp",EDGE,"E1014"),sQuery(id+"F0.wireOp",EDGE,"E1015"),sQuery(id+"F0.wireOp",EDGE,"E1015"),sQuery(id+"F0.wireOp",EDGE,"E1016"),sQuery(id+"F0.wireOp",EDGE,"E1017"),sQuery(id+"F0.wireOp",EDGE,"E1018"),sQuery(id+"F0.wireOp",EDGE,"E1019"),sQuery(id+"F0.wireOp",EDGE,"E1020"),sQuery(id+"F0.wireOp",EDGE,"E1021"),sQuery(id+"F0.wireOp",EDGE,"E1021"),sQuery(id+"F0.wireOp",EDGE,"E1021"),sQuery(id+"F0.wireOp",EDGE,"E1021"),sQuery(id+"F0.wireOp",EDGE,"E1022"),sQuery(id+"F0.wireOp",EDGE,"E1023"),sQuery(id+"F0.wireOp",EDGE,"E1024"),sQuery(id+"F0.wireOp",EDGE,"E1024"),sQuery(id+"F0.wireOp",EDGE,"E1025"),sQuery(id+"F0.wireOp",EDGE,"E1026"),sQuery(id+"F0.wireOp",EDGE,"E1027"),sQuery(id+"F0.wireOp",EDGE,"E1028"),sQuery(id+"F0.wireOp",EDGE,"E1029"),sQuery(id+"F0.wireOp",EDGE,"E1029"),sQuery(id+"F0.wireOp",EDGE,"E1030"),sQuery(id+"F0.wireOp",EDGE,"E1031"),sQuery(id+"F0.wireOp",EDGE,"E1031"),sQuery(id+"F0.wireOp",EDGE,"E1032"),sQuery(id+"F0.wireOp",EDGE,"E1033"),sQuery(id+"F0.wireOp",EDGE,"E1033"),sQuery(id+"F0.wireOp",EDGE,"E1034"),sQuery(id+"F0.wireOp",EDGE,"E1035"),sQuery(id+"F0.wireOp",EDGE,"E1035"),sQuery(id+"F0.wireOp",EDGE,"E1036"),sQuery(id+"F0.wireOp",EDGE,"E1037"),sQuery(id+"F0.wireOp",EDGE,"E1038"),sQuery(id+"F0.wireOp",EDGE,"E1038"),sQuery(id+"F0.wireOp",EDGE,"E1038"),sQuery(id+"F0.wireOp",EDGE,"E1039"),sQuery(id+"F0.wireOp",EDGE,"E1040"),sQuery(id+"F0.wireOp",EDGE,"E1041"),sQuery(id+"F0.wireOp",EDGE,"E1042"),sQuery(id+"F0.wireOp",EDGE,"E1043"),sQuery(id+"F0.wireOp",EDGE,"E1044"),sQuery(id+"F0.wireOp",EDGE,"E1045"),sQuery(id+"F0.wireOp",EDGE,"E1046"),sQuery(id+"F0.wireOp",EDGE,"E1046"),sQuery(id+"F0.wireOp",EDGE,"E1046"),sQuery(id+"F0.wireOp",EDGE,"E1047"),sQuery(id+"F0.wireOp",EDGE,"E1048"),sQuery(id+"F0.wireOp",EDGE,"E1048"),sQuery(id+"F0.wireOp",EDGE,"E1048"),sQuery(id+"F0.wireOp",EDGE,"E1048"),sQuery(id+"F0.wireOp",EDGE,"E1048"),sQuery(id+"F0.wireOp",EDGE,"E1049"),sQuery(id+"F0.wireOp",EDGE,"E1050"),sQuery(id+"F0.wireOp",EDGE,"E1051"),sQuery(id+"F0.wireOp",EDGE,"E1052"),sQuery(id+"F0.wireOp",EDGE,"E1053"),sQuery(id+"F0.wireOp",EDGE,"E1054"),sQuery(id+"F0.wireOp",EDGE,"E1055"),sQuery(id+"F0.wireOp",EDGE,"E1056"),sQuery(id+"F0.wireOp",EDGE,"E1056"),sQuery(id+"F0.wireOp",EDGE,"E1056"),sQuery(id+"F0.wireOp",EDGE,"E1056"),sQuery(id+"F0.wireOp",EDGE,"E1057"),sQuery(id+"F0.wireOp",EDGE,"E1058"),sQuery(id+"F0.wireOp",EDGE,"E1058"),sQuery(id+"F0.wireOp",EDGE,"E1059"),sQuery(id+"F0.wireOp",EDGE,"E1060"),sQuery(id+"F0.wireOp",EDGE,"E1060"),sQuery(id+"F0.wireOp",EDGE,"E1061"),sQuery(id+"F0.wireOp",EDGE,"E1062"),sQuery(id+"F0.wireOp",EDGE,"E1063"),sQuery(id+"F0.wireOp",EDGE,"E1064"),sQuery(id+"F0.wireOp",EDGE,"E1065"),sQuery(id+"F0.wireOp",EDGE,"E1066"),sQuery(id+"F0.wireOp",EDGE,"E1067"),sQuery(id+"F0.wireOp",EDGE,"E1068"),sQuery(id+"F0.wireOp",EDGE,"E1069"),sQuery(id+"F0.wireOp",EDGE,"E1070"),sQuery(id+"F0.wireOp",EDGE,"E1071"),sQuery(id+"F0.wireOp",EDGE,"E1071"),sQuery(id+"F0.wireOp",EDGE,"E1071"),sQuery(id+"F0.wireOp",EDGE,"E1072"),sQuery(id+"F0.wireOp",EDGE,"E1073"),sQuery(id+"F0.wireOp",EDGE,"E1074"),sQuery(id+"F0.wireOp",EDGE,"E1075"),sQuery(id+"F0.wireOp",EDGE,"E1076"),sQuery(id+"F0.wireOp",EDGE,"E1077"),sQuery(id+"F0.wireOp",EDGE,"E1078"),sQuery(id+"F0.wireOp",EDGE,"E1079"),sQuery(id+"F0.wireOp",EDGE,"E1080"),sQuery(id+"F0.wireOp",EDGE,"E1081"),sQuery(id+"F0.wireOp",EDGE,"E1022"),sQuery(id+"F0.wireOp",EDGE,"E1113"),sQuery(id+"F0.wireOp",EDGE,"E1113"),sQuery(id+"F0.wireOp",EDGE,"E1114"),sQuery(id+"F0.wireOp",EDGE,"E1115"),sQuery(id+"F0.wireOp",EDGE,"E1116"),sQuery(id+"F0.wireOp",EDGE,"E1117"),sQuery(id+"F0.wireOp",EDGE,"E1118"),sQuery(id+"F0.wireOp",EDGE,"E1119"),sQuery(id+"F0.wireOp",EDGE,"E1120"),sQuery(id+"F0.wireOp",EDGE,"E1121"),sQuery(id+"F0.wireOp",EDGE,"E1122"),sQuery(id+"F0.wireOp",EDGE,"E1123"),sQuery(id+"F0.wireOp",EDGE,"E1124"),sQuery(id+"F0.wireOp",EDGE,"E1125"),sQuery(id+"F0.wireOp",EDGE,"E1126"),sQuery(id+"F0.wireOp",EDGE,"E1126"),sQuery(id+"F0.wireOp",EDGE,"E1127"),sQuery(id+"F0.wireOp",EDGE,"E1128"),sQuery(id+"F0.wireOp",EDGE,"E1129"),sQuery(id+"F0.wireOp",EDGE,"E1130"),sQuery(id+"F0.wireOp",EDGE,"E1131"),sQuery(id+"F0.wireOp",EDGE,"E1132"),sQuery(id+"F0.wireOp",EDGE,"E1133"),sQuery(id+"F0.wireOp",EDGE,"E1134"),sQuery(id+"F0.wireOp",EDGE,"E1135"),sQuery(id+"F0.wireOp",EDGE,"E1136"),sQuery(id+"F0.wireOp",EDGE,"E1137"),sQuery(id+"F0.wireOp",EDGE,"E1138"),sQuery(id+"F0.wireOp",EDGE,"E1139"),sQuery(id+"F0.wireOp",EDGE,"E1140"),sQuery(id+"F0.wireOp",EDGE,"E1140"),sQuery(id+"F0.wireOp",EDGE,"E1141"),sQuery(id+"F0.wireOp",EDGE,"E1142"),sQuery(id+"F0.wireOp",EDGE,"E1142"),sQuery(id+"F0.wireOp",EDGE,"E1143"),sQuery(id+"F0.wireOp",EDGE,"E1144"),sQuery(id+"F0.wireOp",EDGE,"E1145"),sQuery(id+"F0.wireOp",EDGE,"E1146"),sQuery(id+"F0.wireOp",EDGE,"E1147"),sQuery(id+"F0.wireOp",EDGE,"E1147"),sQuery(id+"F0.wireOp",EDGE,"E1148"),sQuery(id+"F0.wireOp",EDGE,"E1113"),sQuery(id+"F0.wireOp",EDGE,"E1149"),sQuery(id+"F0.wireOp",EDGE,"E1150"),sQuery(id+"F0.wireOp",EDGE,"E1151"),sQuery(id+"F0.wireOp",EDGE,"E1152"),sQuery(id+"F0.wireOp",EDGE,"E1153"),sQuery(id+"F0.wireOp",EDGE,"E1154"),sQuery(id+"F0.wireOp",EDGE,"E1155"),sQuery(id+"F0.wireOp",EDGE,"E1156"),sQuery(id+"F0.wireOp",EDGE,"E1157"),sQuery(id+"F0.wireOp",EDGE,"E1157"),sQuery(id+"F0.wireOp",EDGE,"E1157"),sQuery(id+"F0.wireOp",EDGE,"E1157"),sQuery(id+"F0.wireOp",EDGE,"E1158"),sQuery(id+"F0.wireOp",EDGE,"E1159"),sQuery(id+"F0.wireOp",EDGE,"E1160"),sQuery(id+"F0.wireOp",EDGE,"E1161"),sQuery(id+"F0.wireOp",EDGE,"E1162"),sQuery(id+"F0.wireOp",EDGE,"E1163"),sQuery(id+"F0.wireOp",EDGE,"E1164"),sQuery(id+"F0.wireOp",EDGE,"E1165"),sQuery(id+"F0.wireOp",EDGE,"E1166"),sQuery(id+"F0.wireOp",EDGE,"E1167"),sQuery(id+"F0.wireOp",EDGE,"E1167"),sQuery(id+"F0.wireOp",EDGE,"E1168"),sQuery(id+"F0.wireOp",EDGE,"E1169"),sQuery(id+"F0.wireOp",EDGE,"E1169"),sQuery(id+"F0.wireOp",EDGE,"E1170"),sQuery(id+"F0.wireOp",EDGE,"E1171"),sQuery(id+"F0.wireOp",EDGE,"E1171"),sQuery(id+"F0.wireOp",EDGE,"E1172"),sQuery(id+"F0.wireOp",EDGE,"E1173"),sQuery(id+"F0.wireOp",EDGE,"E1174"),sQuery(id+"F0.wireOp",EDGE,"E1175"),sQuery(id+"F0.wireOp",EDGE,"E1176"),sQuery(id+"F0.wireOp",EDGE,"E1177"),sQuery(id+"F0.wireOp",EDGE,"E1178"),sQuery(id+"F0.wireOp",EDGE,"E1179"),sQuery(id+"F0.wireOp",EDGE,"E1180"),sQuery(id+"F0.wireOp",EDGE,"E1180"),sQuery(id+"F0.wireOp",EDGE,"E1181"),sQuery(id+"F0.wireOp",EDGE,"E1182"),sQuery(id+"F0.wireOp",EDGE,"E1182"),sQuery(id+"F0.wireOp",EDGE,"E1183"),sQuery(id+"F0.wireOp",EDGE,"E1184"),sQuery(id+"F0.wireOp",EDGE,"E1184"),sQuery(id+"F0.wireOp",EDGE,"E1184"),sQuery(id+"F0.wireOp",EDGE,"E1184"),sQuery(id+"F0.wireOp",EDGE,"E1185"),sQuery(id+"F0.wireOp",EDGE,"E1186"),sQuery(id+"F0.wireOp",EDGE,"E1187"),sQuery(id+"F0.wireOp",EDGE,"E1188"),sQuery(id+"F0.wireOp",EDGE,"E1189"),sQuery(id+"F0.wireOp",EDGE,"E1189"),sQuery(id+"F0.wireOp",EDGE,"E1189"),sQuery(id+"F0.wireOp",EDGE,"E1189"),sQuery(id+"F0.wireOp",EDGE,"E1190"),sQuery(id+"F0.wireOp",EDGE,"E1191"),sQuery(id+"F0.wireOp",EDGE,"E1192"),sQuery(id+"F0.wireOp",EDGE,"E1193"),sQuery(id+"F0.wireOp",EDGE,"E1193"),sQuery(id+"F0.wireOp",EDGE,"E1194"),sQuery(id+"F0.wireOp",EDGE,"E1195"),sQuery(id+"F0.wireOp",EDGE,"E1196"),sQuery(id+"F0.wireOp",EDGE,"E1197"),sQuery(id+"F0.wireOp",EDGE,"E1198"),sQuery(id+"F0.wireOp",EDGE,"E1199"),sQuery(id+"F0.wireOp",EDGE,"E1199"),sQuery(id+"F0.wireOp",EDGE,"E1200"),sQuery(id+"F0.wireOp",EDGE,"E1201"),sQuery(id+"F0.wireOp",EDGE,"E1202"),sQuery(id+"F0.wireOp",EDGE,"E1202"),sQuery(id+"F0.wireOp",EDGE,"E1203"),sQuery(id+"F0.wireOp",EDGE,"E1204"),sQuery(id+"F0.wireOp",EDGE,"E1205"),sQuery(id+"F0.wireOp",EDGE,"E1206"),sQuery(id+"F0.wireOp",EDGE,"E1206"),sQuery(id+"F0.wireOp",EDGE,"E1207"),sQuery(id+"F0.wireOp",EDGE,"E1208"),sQuery(id+"F0.wireOp",EDGE,"E1208"),sQuery(id+"F0.wireOp",EDGE,"E1208"),sQuery(id+"F0.wireOp",EDGE,"E1208"),sQuery(id+"F0.wireOp",EDGE,"E1208"),sQuery(id+"F0.wireOp",EDGE,"E1209"),sQuery(id+"F0.wireOp",EDGE,"E1210"),sQuery(id+"F0.wireOp",EDGE,"E1211"),sQuery(id+"F0.wireOp",EDGE,"E1211"),sQuery(id+"F0.wireOp",EDGE,"E1211"),sQuery(id+"F0.wireOp",EDGE,"E1212"),sQuery(id+"F0.wireOp",EDGE,"E1213"),sQuery(id+"F0.wireOp",EDGE,"E1214"),sQuery(id+"F0.wireOp",EDGE,"E1215"),sQuery(id+"F0.wireOp",EDGE,"E1215"),sQuery(id+"F0.wireOp",EDGE,"E1216"),sQuery(id+"F0.wireOp",EDGE,"E1217"),sQuery(id+"F0.wireOp",EDGE,"E1217"),sQuery(id+"F0.wireOp",EDGE,"E1218"),sQuery(id+"F0.wireOp",EDGE,"E1219"),sQuery(id+"F0.wireOp",EDGE,"E1219"),sQuery(id+"F0.wireOp",EDGE,"E1219"),sQuery(id+"F0.wireOp",EDGE,"E1219"),sQuery(id+"F0.wireOp",EDGE,"E1220"),sQuery(id+"F0.wireOp",EDGE,"E1221"),sQuery(id+"F0.wireOp",EDGE,"E1222"),sQuery(id+"F0.wireOp",EDGE,"E1223"),sQuery(id+"F0.wireOp",EDGE,"E1224"),sQuery(id+"F0.wireOp",EDGE,"E1225"),sQuery(id+"F0.wireOp",EDGE,"E1225"),sQuery(id+"F0.wireOp",EDGE,"E1226"),sQuery(id+"F0.wireOp",EDGE,"E1227"),sQuery(id+"F0.wireOp",EDGE,"E1227"),sQuery(id+"F0.wireOp",EDGE,"E1228"),sQuery(id+"F0.wireOp",EDGE,"E1229"),sQuery(id+"F0.wireOp",EDGE,"E1229"),sQuery(id+"F0.wireOp",EDGE,"E1230"),sQuery(id+"F0.wireOp",EDGE,"E1231"),sQuery(id+"F0.wireOp",EDGE,"E1232"),sQuery(id+"F0.wireOp",EDGE,"E1233"),sQuery(id+"F0.wireOp",EDGE,"E1234"),sQuery(id+"F0.wireOp",EDGE,"E1235"),sQuery(id+"F0.wireOp",EDGE,"E1236"),sQuery(id+"F0.wireOp",EDGE,"E1236"),sQuery(id+"F0.wireOp",EDGE,"E1237"),sQuery(id+"F0.wireOp",EDGE,"E1238"),sQuery(id+"F0.wireOp",EDGE,"E1238"),sQuery(id+"F0.wireOp",EDGE,"E1238"),sQuery(id+"F0.wireOp",EDGE,"E1238"),sQuery(id+"F0.wireOp",EDGE,"E1238"),sQuery(id+"F0.wireOp",EDGE,"E1239"),sQuery(id+"F0.wireOp",EDGE,"E1240"),sQuery(id+"F0.wireOp",EDGE,"E1241"),sQuery(id+"F0.wireOp",EDGE,"E1242"),sQuery(id+"F0.wireOp",EDGE,"E1243"),sQuery(id+"F0.wireOp",EDGE,"E1244"),sQuery(id+"F0.wireOp",EDGE,"E1245"),sQuery(id+"F0.wireOp",EDGE,"E1245"),sQuery(id+"F0.wireOp",EDGE,"E1245"),sQuery(id+"F0.wireOp",EDGE,"E1246"),sQuery(id+"F0.wireOp",EDGE,"E1247"),sQuery(id+"F0.wireOp",EDGE,"E1247"),sQuery(id+"F0.wireOp",EDGE,"E1247"),sQuery(id+"F0.wireOp",EDGE,"E1247"),sQuery(id+"F0.wireOp",EDGE,"E1248"),sQuery(id+"F0.wireOp",EDGE,"E1249"),sQuery(id+"F0.wireOp",EDGE,"E1250"),sQuery(id+"F0.wireOp",EDGE,"E1251"),sQuery(id+"F0.wireOp",EDGE,"E1252"),sQuery(id+"F0.wireOp",EDGE,"E1252"),sQuery(id+"F0.wireOp",EDGE,"E1252"),sQuery(id+"F0.wireOp",EDGE,"E1252"),sQuery(id+"F0.wireOp",EDGE,"E1253"),sQuery(id+"F0.wireOp",EDGE,"E1211"),sQuery(id+"F0.wireOp",EDGE,"E1254"),sQuery(id+"F0.wireOp",EDGE,"E1255"),sQuery(id+"F0.wireOp",EDGE,"E1256"),sQuery(id+"F0.wireOp",EDGE,"E1256"),sQuery(id+"F0.wireOp",EDGE,"E1257"),sQuery(id+"F0.wireOp",EDGE,"E1258"),sQuery(id+"F0.wireOp",EDGE,"E1259"),sQuery(id+"F0.wireOp",EDGE,"E1260"),sQuery(id+"F0.wireOp",EDGE,"E1261"),sQuery(id+"F0.wireOp",EDGE,"E1262"),sQuery(id+"F0.wireOp",EDGE,"E1262"),sQuery(id+"F0.wireOp",EDGE,"E1263"),sQuery(id+"F0.wireOp",EDGE,"E1264"),sQuery(id+"F0.wireOp",EDGE,"E1265"),sQuery(id+"F0.wireOp",EDGE,"E1266"),sQuery(id+"F0.wireOp",EDGE,"E1266"),sQuery(id+"F0.wireOp",EDGE,"E1266"),sQuery(id+"F0.wireOp",EDGE,"E1266"),sQuery(id+"F0.wireOp",EDGE,"E1266"),sQuery(id+"F0.wireOp",EDGE,"E1267"),sQuery(id+"F0.wireOp",EDGE,"E1268"),sQuery(id+"F0.wireOp",EDGE,"E1268"),sQuery(id+"F0.wireOp",EDGE,"E1268"),sQuery(id+"F0.wireOp",EDGE,"E1268"),sQuery(id+"F0.wireOp",EDGE,"E1269"),sQuery(id+"F0.wireOp",EDGE,"E1254"),sQuery(id+"F0.wireOp",EDGE,"E1270"),sQuery(id+"F0.wireOp",EDGE,"E1271"),sQuery(id+"F0.wireOp",EDGE,"E1272"),sQuery(id+"F0.wireOp",EDGE,"E1273"),sQuery(id+"F0.wireOp",EDGE,"E1273"),sQuery(id+"F0.wireOp",EDGE,"E1274"),sQuery(id+"F0.wireOp",EDGE,"E1275"),sQuery(id+"F0.wireOp",EDGE,"E1275"),sQuery(id+"F0.wireOp",EDGE,"E1276"),sQuery(id+"F0.wireOp",EDGE,"E1277"),sQuery(id+"F0.wireOp",EDGE,"E1277"),sQuery(id+"F0.wireOp",EDGE,"E1278"),sQuery(id+"F0.wireOp",EDGE,"E1279"),sQuery(id+"F0.wireOp",EDGE,"E1280"),sQuery(id+"F0.wireOp",EDGE,"E1281"),sQuery(id+"F0.wireOp",EDGE,"E1282"),sQuery(id+"F0.wireOp",EDGE,"E1283"),sQuery(id+"F0.wireOp",EDGE,"E1284"),sQuery(id+"F0.wireOp",EDGE,"E1284"),sQuery(id+"F0.wireOp",EDGE,"E1284"),sQuery(id+"F0.wireOp",EDGE,"E1285"),sQuery(id+"F0.wireOp",EDGE,"E1286"),sQuery(id+"F0.wireOp",EDGE,"E1287"),sQuery(id+"F0.wireOp",EDGE,"E1288"),sQuery(id+"F0.wireOp",EDGE,"E1288"),sQuery(id+"F0.wireOp",EDGE,"E1289"),sQuery(id+"F0.wireOp",EDGE,"E1290"),sQuery(id+"F0.wireOp",EDGE,"E1291"),sQuery(id+"F0.wireOp",EDGE,"E1292"),sQuery(id+"F0.wireOp",EDGE,"E1293"),sQuery(id+"F0.wireOp",EDGE,"E1293"),sQuery(id+"F0.wireOp",EDGE,"E1293"),sQuery(id+"F0.wireOp",EDGE,"E1294"),sQuery(id+"F0.wireOp",EDGE,"E1295"),sQuery(id+"F0.wireOp",EDGE,"E1296"),sQuery(id+"F0.wireOp",EDGE,"E1297"),sQuery(id+"F0.wireOp",EDGE,"E1298"),sQuery(id+"F0.wireOp",EDGE,"E1298"),sQuery(id+"F0.wireOp",EDGE,"E1299"),sQuery(id+"F0.wireOp",EDGE,"E1300"),sQuery(id+"F0.wireOp",EDGE,"E1301"),sQuery(id+"F0.wireOp",EDGE,"E1302"),sQuery(id+"F0.wireOp",EDGE,"E1303"),sQuery(id+"F0.wireOp",EDGE,"E1304"),sQuery(id+"F0.wireOp",EDGE,"E1305"),sQuery(id+"F0.wireOp",EDGE,"E1305"),sQuery(id+"F0.wireOp",EDGE,"E1305"),sQuery(id+"F0.wireOp",EDGE,"E1305"),sQuery(id+"F0.wireOp",EDGE,"E1306"),sQuery(id+"F0.wireOp",EDGE,"E1307"),sQuery(id+"F0.wireOp",EDGE,"E1308"),sQuery(id+"F0.wireOp",EDGE,"E1309"),sQuery(id+"F0.wireOp",EDGE,"E1310"),sQuery(id+"F0.wireOp",EDGE,"E1310"),sQuery(id+"F0.wireOp",EDGE,"E1311"),sQuery(id+"F0.wireOp",EDGE,"E1312"),sQuery(id+"F0.wireOp",EDGE,"E1312"),sQuery(id+"F0.wireOp",EDGE,"E1313"),sQuery(id+"F0.wireOp",EDGE,"E1314"),sQuery(id+"F0.wireOp",EDGE,"E1314"),sQuery(id+"F0.wireOp",EDGE,"E1314"),sQuery(id+"F0.wireOp",EDGE,"E1315"),sQuery(id+"F0.wireOp",EDGE,"E1316"),sQuery(id+"F0.wireOp",EDGE,"E1317"),sQuery(id+"F0.wireOp",EDGE,"E1317"),sQuery(id+"F0.wireOp",EDGE,"E1317"),sQuery(id+"F0.wireOp",EDGE,"E1317"),sQuery(id+"F0.wireOp",EDGE,"E1318"),sQuery(id+"F0.wireOp",EDGE,"E1319"),sQuery(id+"F0.wireOp",EDGE,"E1319"),sQuery(id+"F0.wireOp",EDGE,"E1320"),sQuery(id+"F0.wireOp",EDGE,"E1321"),sQuery(id+"F0.wireOp",EDGE,"E1321"),sQuery(id+"F0.wireOp",EDGE,"E1321"),sQuery(id+"F0.wireOp",EDGE,"E1321"),sQuery(id+"F0.wireOp",EDGE,"E1322"),sQuery(id+"F0.wireOp",EDGE,"E1323"),sQuery(id+"F0.wireOp",EDGE,"E1324"),sQuery(id+"F0.wireOp",EDGE,"E1324"),sQuery(id+"F0.wireOp",EDGE,"E1324"),sQuery(id+"F0.wireOp",EDGE,"E1325"),sQuery(id+"F0.wireOp",EDGE,"E1326"),sQuery(id+"F0.wireOp",EDGE,"E1326"),sQuery(id+"F0.wireOp",EDGE,"E1326"),sQuery(id+"F0.wireOp",EDGE,"E1326"),sQuery(id+"F0.wireOp",EDGE,"E1326"),sQuery(id+"F0.wireOp",EDGE,"E1327"),sQuery(id+"F0.wireOp",EDGE,"E1328"),sQuery(id+"F0.wireOp",EDGE,"E1329"),sQuery(id+"F0.wireOp",EDGE,"E1330"),sQuery(id+"F0.wireOp",EDGE,"E1331"),sQuery(id+"F0.wireOp",EDGE,"E1331"),sQuery(id+"F0.wireOp",EDGE,"E1332"),sQuery(id+"F0.wireOp",EDGE,"E1333"),sQuery(id+"F0.wireOp",EDGE,"E1333"),sQuery(id+"F0.wireOp",EDGE,"E1334"),sQuery(id+"F0.wireOp",EDGE,"E1335"),sQuery(id+"F0.wireOp",EDGE,"E1335"),sQuery(id+"F0.wireOp",EDGE,"E1335"),sQuery(id+"F0.wireOp",EDGE,"E1336"),sQuery(id+"F0.wireOp",EDGE,"E1337"),sQuery(id+"F0.wireOp",EDGE,"E1338"),sQuery(id+"F0.wireOp",EDGE,"E1339"),sQuery(id+"F0.wireOp",EDGE,"E1339"),sQuery(id+"F0.wireOp",EDGE,"E1340"),sQuery(id+"F0.wireOp",EDGE,"E1341"),sQuery(id+"F0.wireOp",EDGE,"E1341"),sQuery(id+"F0.wireOp",EDGE,"E1342"),sQuery(id+"F0.wireOp",EDGE,"E1343"),sQuery(id+"F0.wireOp",EDGE,"E1343"),sQuery(id+"F0.wireOp",EDGE,"E1344"),sQuery(id+"F0.wireOp",EDGE,"E1329"),sQuery(id+"F0.wireOp",EDGE,"E1345"),sQuery(id+"F0.wireOp",EDGE,"E1346"),sQuery(id+"F0.wireOp",EDGE,"E1347"),sQuery(id+"F0.wireOp",EDGE,"E1348"),sQuery(id+"F0.wireOp",EDGE,"E1349"),sQuery(id+"F0.wireOp",EDGE,"E1350"),sQuery(id+"F0.wireOp",EDGE,"E1351"),sQuery(id+"F0.wireOp",EDGE,"E1352"),sQuery(id+"F0.wireOp",EDGE,"E1353"),sQuery(id+"F0.wireOp",EDGE,"E1354"),sQuery(id+"F0.wireOp",EDGE,"E1354"),sQuery(id+"F0.wireOp",EDGE,"E1355"),sQuery(id+"F0.wireOp",EDGE,"E1356"),sQuery(id+"F0.wireOp",EDGE,"E1356"),sQuery(id+"F0.wireOp",EDGE,"E1356"),sQuery(id+"F0.wireOp",EDGE,"E1357"),sQuery(id+"F0.wireOp",EDGE,"E1358"),sQuery(id+"F0.wireOp",EDGE,"E1358"),sQuery(id+"F0.wireOp",EDGE,"E1358"),sQuery(id+"F0.wireOp",EDGE,"E1358"),sQuery(id+"F0.wireOp",EDGE,"E1359"),sQuery(id+"F0.wireOp",EDGE,"E1360"),sQuery(id+"F0.wireOp",EDGE,"E1360"),sQuery(id+"F0.wireOp",EDGE,"E1361"),sQuery(id+"F0.wireOp",EDGE,"E1362"),sQuery(id+"F0.wireOp",EDGE,"E1363"),sQuery(id+"F0.wireOp",EDGE,"E1364"),sQuery(id+"F0.wireOp",EDGE,"E1365"),sQuery(id+"F0.wireOp",EDGE,"E1366"),sQuery(id+"F0.wireOp",EDGE,"E1367"),sQuery(id+"F0.wireOp",EDGE,"E1368"),sQuery(id+"F0.wireOp",EDGE,"E1369"),sQuery(id+"F0.wireOp",EDGE,"E1370"),sQuery(id+"F0.wireOp",EDGE,"E1371"),sQuery(id+"F0.wireOp",EDGE,"E1371"),sQuery(id+"F0.wireOp",EDGE,"E1372"),sQuery(id+"F0.wireOp",EDGE,"E1373"),sQuery(id+"F0.wireOp",EDGE,"E1374"),sQuery(id+"F0.wireOp",EDGE,"E1375"),sQuery(id+"F0.wireOp",EDGE,"E1375"),sQuery(id+"F0.wireOp",EDGE,"E1375"),sQuery(id+"F0.wireOp",EDGE,"E1376"),sQuery(id+"F0.wireOp",EDGE,"E1377"),sQuery(id+"F0.wireOp",EDGE,"E1377"),sQuery(id+"F0.wireOp",EDGE,"E1378"),sQuery(id+"F0.wireOp",EDGE,"E1379"),sQuery(id+"F0.wireOp",EDGE,"E1379"),sQuery(id+"F0.wireOp",EDGE,"E1380"),sQuery(id+"F0.wireOp",EDGE,"E1381"),sQuery(id+"F0.wireOp",EDGE,"E1381"),sQuery(id+"F0.wireOp",EDGE,"E1382"),sQuery(id+"F0.wireOp",EDGE,"E1383"),sQuery(id+"F0.wireOp",EDGE,"E1384"),sQuery(id+"F0.wireOp",EDGE,"E1385"),sQuery(id+"F0.wireOp",EDGE,"E1386"),sQuery(id+"F0.wireOp",EDGE,"E1387"),sQuery(id+"F0.wireOp",EDGE,"E1388"),sQuery(id+"F0.wireOp",EDGE,"E1389"),sQuery(id+"F0.wireOp",EDGE,"E1390"),sQuery(id+"F0.wireOp",EDGE,"E1391"),sQuery(id+"F0.wireOp",EDGE,"E1392"),sQuery(id+"F0.wireOp",EDGE,"E1393"),sQuery(id+"F0.wireOp",EDGE,"E1393"),sQuery(id+"F0.wireOp",EDGE,"E1394"),sQuery(id+"F0.wireOp",EDGE,"E1395"),sQuery(id+"F0.wireOp",EDGE,"E1396"),sQuery(id+"F0.wireOp",EDGE,"E1397"),sQuery(id+"F0.wireOp",EDGE,"E1398"),sQuery(id+"F0.wireOp",EDGE,"E1398"),sQuery(id+"F0.wireOp",EDGE,"E1399"),sQuery(id+"F0.wireOp",EDGE,"E1400"),sQuery(id+"F0.wireOp",EDGE,"E1401"),sQuery(id+"F0.wireOp",EDGE,"E1402"),sQuery(id+"F0.wireOp",EDGE,"E1403"),sQuery(id+"F0.wireOp",EDGE,"E1404"),sQuery(id+"F0.wireOp",EDGE,"E1404"),sQuery(id+"F0.wireOp",EDGE,"E1405"),sQuery(id+"F0.wireOp",EDGE,"E1406"),sQuery(id+"F0.wireOp",EDGE,"E1407"),sQuery(id+"F0.wireOp",EDGE,"E1408"),sQuery(id+"F0.wireOp",EDGE,"E1409"),sQuery(id+"F0.wireOp",EDGE,"E1409"),sQuery(id+"F0.wireOp",EDGE,"E1410"),sQuery(id+"F0.wireOp",EDGE,"E1411"),sQuery(id+"F0.wireOp",EDGE,"E1412"),sQuery(id+"F0.wireOp",EDGE,"E1413"),sQuery(id+"F0.wireOp",EDGE,"E1413"),sQuery(id+"F0.wireOp",EDGE,"E1413"),sQuery(id+"F0.wireOp",EDGE,"E1413"),sQuery(id+"F0.wireOp",EDGE,"E1414"),sQuery(id+"F0.wireOp",EDGE,"E1415"),sQuery(id+"F0.wireOp",EDGE,"E1415"),sQuery(id+"F0.wireOp",EDGE,"E1416"),sQuery(id+"F0.wireOp",EDGE,"E1417"),sQuery(id+"F0.wireOp",EDGE,"E1417"),sQuery(id+"F0.wireOp",EDGE,"E1417"),sQuery(id+"F0.wireOp",EDGE,"E1417"),sQuery(id+"F0.wireOp",EDGE,"E1418"),sQuery(id+"F0.wireOp",EDGE,"E1419"),sQuery(id+"F0.wireOp",EDGE,"E1420"),sQuery(id+"F0.wireOp",EDGE,"E1421"),sQuery(id+"F0.wireOp",EDGE,"E1422"),sQuery(id+"F0.wireOp",EDGE,"E1422"),sQuery(id+"F0.wireOp",EDGE,"E1422"),sQuery(id+"F0.wireOp",EDGE,"E1422"),sQuery(id+"F0.wireOp",EDGE,"E1423"),sQuery(id+"F0.wireOp",EDGE,"E1424"),sQuery(id+"F0.wireOp",EDGE,"E1425"),sQuery(id+"F0.wireOp",EDGE,"E1426"),sQuery(id+"F0.wireOp",EDGE,"E1427"),sQuery(id+"F0.wireOp",EDGE,"E1428"),sQuery(id+"F0.wireOp",EDGE,"E1429"),sQuery(id+"F0.wireOp",EDGE,"E1429"),sQuery(id+"F0.wireOp",EDGE,"E1429"),sQuery(id+"F0.wireOp",EDGE,"E1429"),sQuery(id+"F0.wireOp",EDGE,"E1430"),sQuery(id+"F0.wireOp",EDGE,"E1431"),sQuery(id+"F0.wireOp",EDGE,"E1431"),sQuery(id+"F0.wireOp",EDGE,"E1431"),sQuery(id+"F0.wireOp",EDGE,"E1431"),sQuery(id+"F0.wireOp",EDGE,"E1431"),sQuery(id+"F0.wireOp",EDGE,"E1431"),sQuery(id+"F0.wireOp",EDGE,"E1431"),sQuery(id+"F0.wireOp",EDGE,"E1443"),sQuery(id+"F0.wireOp",EDGE,"E1444"),sQuery(id+"F0.wireOp",EDGE,"E1445"),sQuery(id+"F0.wireOp",EDGE,"E1446"),sQuery(id+"F0.wireOp",EDGE,"E1447"),sQuery(id+"F0.wireOp",EDGE,"E1448"),sQuery(id+"F0.wireOp",EDGE,"E1449"),sQuery(id+"F0.wireOp",EDGE,"E1450"),sQuery(id+"F0.wireOp",EDGE,"E1450"),sQuery(id+"F0.wireOp",EDGE,"E1451"),sQuery(id+"F0.wireOp",EDGE,"E1452"),sQuery(id+"F0.wireOp",EDGE,"E1452"),sQuery(id+"F0.wireOp",EDGE,"E1453"),sQuery(id+"F0.wireOp",EDGE,"E1454"),sQuery(id+"F0.wireOp",EDGE,"E1454"),sQuery(id+"F0.wireOp",EDGE,"E1455"),sQuery(id+"F0.wireOp",EDGE,"E1456"),sQuery(id+"F0.wireOp",EDGE,"E1456"),sQuery(id+"F0.wireOp",EDGE,"E1457"),sQuery(id+"F0.wireOp",EDGE,"E1458"),sQuery(id+"F0.wireOp",EDGE,"E1458"),sQuery(id+"F0.wireOp",EDGE,"E1459"),sQuery(id+"F0.wireOp",EDGE,"E1460"),sQuery(id+"F0.wireOp",EDGE,"E1460"),sQuery(id+"F0.wireOp",EDGE,"E1461"),sQuery(id+"F0.wireOp",EDGE,"E1462"),sQuery(id+"F0.wireOp",EDGE,"E1462"),sQuery(id+"F0.wireOp",EDGE,"E1463"),sQuery(id+"F0.wireOp",EDGE,"E1464"),sQuery(id+"F0.wireOp",EDGE,"E1465"),sQuery(id+"F0.wireOp",EDGE,"E1466"),sQuery(id+"F0.wireOp",EDGE,"E1467"),sQuery(id+"F0.wireOp",EDGE,"E1467"),sQuery(id+"F0.wireOp",EDGE,"E1468"),sQuery(id+"F0.wireOp",EDGE,"E1469"),sQuery(id+"F0.wireOp",EDGE,"E1470"),sQuery(id+"F0.wireOp",EDGE,"E1471"),sQuery(id+"F0.wireOp",EDGE,"E1472"),sQuery(id+"F0.wireOp",EDGE,"E1473"),sQuery(id+"F0.wireOp",EDGE,"E1474"),sQuery(id+"F0.wireOp",EDGE,"E1475"),sQuery(id+"F0.wireOp",EDGE,"E1476"),sQuery(id+"F0.wireOp",EDGE,"E1476"),sQuery(id+"F0.wireOp",EDGE,"E1477"),sQuery(id+"F0.wireOp",EDGE,"E1478"),sQuery(id+"F0.wireOp",EDGE,"E1478"),sQuery(id+"F0.wireOp",EDGE,"E1479"),sQuery(id+"F0.wireOp",EDGE,"E1480"),sQuery(id+"F0.wireOp",EDGE,"E1480"),sQuery(id+"F0.wireOp",EDGE,"E1481"),sQuery(id+"F0.wireOp",EDGE,"E1482"),sQuery(id+"F0.wireOp",EDGE,"E1482"),sQuery(id+"F0.wireOp",EDGE,"E1482"),sQuery(id+"F0.wireOp",EDGE,"E1483"),sQuery(id+"F0.wireOp",EDGE,"E1484"),sQuery(id+"F0.wireOp",EDGE,"E1484"),sQuery(id+"F0.wireOp",EDGE,"E1485"),sQuery(id+"F0.wireOp",EDGE,"E1486"),sQuery(id+"F0.wireOp",EDGE,"E1487"),sQuery(id+"F0.wireOp",EDGE,"E1488"),sQuery(id+"F0.wireOp",EDGE,"E1489"),sQuery(id+"F0.wireOp",EDGE,"E1490"),sQuery(id+"F0.wireOp",EDGE,"E1491"),sQuery(id+"F0.wireOp",EDGE,"E1492"),sQuery(id+"F0.wireOp",EDGE,"E1492"),sQuery(id+"F0.wireOp",EDGE,"E1492"),sQuery(id+"F0.wireOp",EDGE,"E1492"),sQuery(id+"F0.wireOp",EDGE,"E1493"),sQuery(id+"F0.wireOp",EDGE,"E1494"),sQuery(id+"F0.wireOp",EDGE,"E1495"),sQuery(id+"F0.wireOp",EDGE,"E1496"),sQuery(id+"F0.wireOp",EDGE,"E1496"),sQuery(id+"F0.wireOp",EDGE,"E1496"),sQuery(id+"F0.wireOp",EDGE,"E1496"),sQuery(id+"F0.wireOp",EDGE,"E1497"),sQuery(id+"F0.wireOp",EDGE,"E1498"),sQuery(id+"F0.wireOp",EDGE,"E1498"),sQuery(id+"F0.wireOp",EDGE,"E1498"),sQuery(id+"F0.wireOp",EDGE,"E1499"),sQuery(id+"F0.wireOp",EDGE,"E1500"),sQuery(id+"F0.wireOp",EDGE,"E1500"),sQuery(id+"F0.wireOp",EDGE,"E1500"),sQuery(id+"F0.wireOp",EDGE,"E1500"),sQuery(id+"F0.wireOp",EDGE,"E1501"),sQuery(id+"F0.wireOp",EDGE,"E1490"),sQuery(id+"F0.wireOp",EDGE,"E1515"),sQuery(id+"F0.wireOp",EDGE,"E1516"),sQuery(id+"F0.wireOp",EDGE,"E1517"),sQuery(id+"F0.wireOp",EDGE,"E1518"),sQuery(id+"F0.wireOp",EDGE,"E1519"),sQuery(id+"F0.wireOp",EDGE,"E1520"),sQuery(id+"F0.wireOp",EDGE,"E1521"),sQuery(id+"F0.wireOp",EDGE,"E1522"),sQuery(id+"F0.wireOp",EDGE,"E1523"),sQuery(id+"F0.wireOp",EDGE,"E1524"),sQuery(id+"F0.wireOp",EDGE,"E1524"),sQuery(id+"F0.wireOp",EDGE,"E1525"),sQuery(id+"F0.wireOp",EDGE,"E1526"),sQuery(id+"F0.wireOp",EDGE,"E1526"),sQuery(id+"F0.wireOp",EDGE,"E1527"),sQuery(id+"F0.wireOp",EDGE,"E1528"),sQuery(id+"F0.wireOp",EDGE,"E1528"),sQuery(id+"F0.wireOp",EDGE,"E1529"),sQuery(id+"F0.wireOp",EDGE,"E1530"),sQuery(id+"F0.wireOp",EDGE,"E1530"),sQuery(id+"F0.wireOp",EDGE,"E1531"),sQuery(id+"F0.wireOp",EDGE,"E1532"),sQuery(id+"F0.wireOp",EDGE,"E1532"),sQuery(id+"F0.wireOp",EDGE,"E1532"),sQuery(id+"F0.wireOp",EDGE,"E1532"),sQuery(id+"F0.wireOp",EDGE,"E1533"),sQuery(id+"F0.wireOp",EDGE,"E1534"),sQuery(id+"F0.wireOp",EDGE,"E1535"),sQuery(id+"F0.wireOp",EDGE,"E1536"),sQuery(id+"F0.wireOp",EDGE,"E1537"),sQuery(id+"F0.wireOp",EDGE,"E1537"),sQuery(id+"F0.wireOp",EDGE,"E1538"),sQuery(id+"F0.wireOp",EDGE,"E1539"),sQuery(id+"F0.wireOp",EDGE,"E1540"),sQuery(id+"F0.wireOp",EDGE,"E1541"),sQuery(id+"F0.wireOp",EDGE,"E1542"),sQuery(id+"F0.wireOp",EDGE,"E1542"),sQuery(id+"F0.wireOp",EDGE,"E1543"),sQuery(id+"F0.wireOp",EDGE,"E1544"),sQuery(id+"F0.wireOp",EDGE,"E1545"),sQuery(id+"F0.wireOp",EDGE,"E1546"),sQuery(id+"F0.wireOp",EDGE,"E1547"),sQuery(id+"F0.wireOp",EDGE,"E1548"),sQuery(id+"F0.wireOp",EDGE,"E1548"),sQuery(id+"F0.wireOp",EDGE,"E1548"),sQuery(id+"F0.wireOp",EDGE,"E1548"),sQuery(id+"F0.wireOp",EDGE,"E1549"),sQuery(id+"F0.wireOp",EDGE,"E1550"),sQuery(id+"F0.wireOp",EDGE,"E1550"),sQuery(id+"F0.wireOp",EDGE,"E1551"),sQuery(id+"F0.wireOp",EDGE,"E1552"),sQuery(id+"F0.wireOp",EDGE,"E1553"),sQuery(id+"F0.wireOp",EDGE,"E1554"),sQuery(id+"F0.wireOp",EDGE,"E1555"),sQuery(id+"F0.wireOp",EDGE,"E1556"),sQuery(id+"F0.wireOp",EDGE,"E1557"),sQuery(id+"F0.wireOp",EDGE,"E1558"),sQuery(id+"F0.wireOp",EDGE,"E1559"),sQuery(id+"F0.wireOp",EDGE,"E1560"),sQuery(id+"F0.wireOp",EDGE,"E1561"),sQuery(id+"F0.wireOp",EDGE,"E1561"),sQuery(id+"F0.wireOp",EDGE,"E1562"),sQuery(id+"F0.wireOp",EDGE,"E1563"),sQuery(id+"F0.wireOp",EDGE,"E1563"),sQuery(id+"F0.wireOp",EDGE,"E1564"),sQuery(id+"F0.wireOp",EDGE,"E1565"),sQuery(id+"F0.wireOp",EDGE,"E1565"),sQuery(id+"F0.wireOp",EDGE,"E1566"),sQuery(id+"F0.wireOp",EDGE,"E1567"),sQuery(id+"F0.wireOp",EDGE,"E1567"),sQuery(id+"F0.wireOp",EDGE,"E1567"),sQuery(id+"F0.wireOp",EDGE,"E1568"),sQuery(id+"F0.wireOp",EDGE,"E1569"),sQuery(id+"F0.wireOp",EDGE,"E1569"),sQuery(id+"F0.wireOp",EDGE,"E1569"),sQuery(id+"F0.wireOp",EDGE,"E1569"),sQuery(id+"F0.wireOp",EDGE,"E1570"),sQuery(id+"F0.wireOp",EDGE,"E1571"),sQuery(id+"F0.wireOp",EDGE,"E1571"),sQuery(id+"F0.wireOp",EDGE,"E1572"),sQuery(id+"F0.wireOp",EDGE,"E1559"),sQuery(id+"F0.wireOp",EDGE,"E1573"),sQuery(id+"F0.wireOp",EDGE,"E1574"),sQuery(id+"F0.wireOp",EDGE,"E1575"),sQuery(id+"F0.wireOp",EDGE,"E1576"),sQuery(id+"F0.wireOp",EDGE,"E1577"),sQuery(id+"F0.wireOp",EDGE,"E1577"),sQuery(id+"F0.wireOp",EDGE,"E1577"),sQuery(id+"F0.wireOp",EDGE,"E1578"),sQuery(id+"F0.wireOp",EDGE,"E1579"),sQuery(id+"F0.wireOp",EDGE,"E1579"),sQuery(id+"F0.wireOp",EDGE,"E1580"),sQuery(id+"F0.wireOp",EDGE,"E1581"),sQuery(id+"F0.wireOp",EDGE,"E1582"),sQuery(id+"F0.wireOp",EDGE,"E1583"),sQuery(id+"F0.wireOp",EDGE,"E1584"),sQuery(id+"F0.wireOp",EDGE,"E1585"),sQuery(id+"F0.wireOp",EDGE,"E1586"),sQuery(id+"F0.wireOp",EDGE,"E1586"),sQuery(id+"F0.wireOp",EDGE,"E1587"),sQuery(id+"F0.wireOp",EDGE,"E1588"),sQuery(id+"F0.wireOp",EDGE,"E1588"),sQuery(id+"F0.wireOp",EDGE,"E1589"),sQuery(id+"F0.wireOp",EDGE,"E1590"),sQuery(id+"F0.wireOp",EDGE,"E1590"),sQuery(id+"F0.wireOp",EDGE,"E1590"),sQuery(id+"F0.wireOp",EDGE,"E1590"),sQuery(id+"F0.wireOp",EDGE,"E1591"),sQuery(id+"F0.wireOp",EDGE,"E1592"),sQuery(id+"F0.wireOp",EDGE,"E1593"),sQuery(id+"F0.wireOp",EDGE,"E1594"),sQuery(id+"F0.wireOp",EDGE,"E1594"),sQuery(id+"F0.wireOp",EDGE,"E1595"),sQuery(id+"F0.wireOp",EDGE,"E1596"),sQuery(id+"F0.wireOp",EDGE,"E1597"),sQuery(id+"F0.wireOp",EDGE,"E1598"),sQuery(id+"F0.wireOp",EDGE,"E1599"),sQuery(id+"F0.wireOp",EDGE,"E1599"),sQuery(id+"F0.wireOp",EDGE,"E1600"),sQuery(id+"F0.wireOp",EDGE,"E1601"),sQuery(id+"F0.wireOp",EDGE,"E1602"),sQuery(id+"F0.wireOp",EDGE,"E1603"),sQuery(id+"F0.wireOp",EDGE,"E1604"),sQuery(id+"F0.wireOp",EDGE,"E1605"),sQuery(id+"F0.wireOp",EDGE,"E1606"),sQuery(id+"F0.wireOp",EDGE,"E1606"),sQuery(id+"F0.wireOp",EDGE,"E1607"),sQuery(id+"F0.wireOp",EDGE,"E1608"),sQuery(id+"F0.wireOp",EDGE,"E1608"),sQuery(id+"F0.wireOp",EDGE,"E1609"),sQuery(id+"F0.wireOp",EDGE,"E1610"),sQuery(id+"F0.wireOp",EDGE,"E1610"),sQuery(id+"F0.wireOp",EDGE,"E1611"),sQuery(id+"F0.wireOp",EDGE,"E1612"),sQuery(id+"F0.wireOp",EDGE,"E1613"),sQuery(id+"F0.wireOp",EDGE,"E1614"),sQuery(id+"F0.wireOp",EDGE,"E1615"),sQuery(id+"F0.wireOp",EDGE,"E1616"),sQuery(id+"F0.wireOp",EDGE,"E1616"),sQuery(id+"F0.wireOp",EDGE,"E1617"),sQuery(id+"F0.wireOp",EDGE,"E1618"),sQuery(id+"F0.wireOp",EDGE,"E1618"),sQuery(id+"F0.wireOp",EDGE,"E1619"),sQuery(id+"F0.wireOp",EDGE,"E1620"),sQuery(id+"F0.wireOp",EDGE,"E1620"),sQuery(id+"F0.wireOp",EDGE,"E1621"),sQuery(id+"F0.wireOp",EDGE,"E1622"),sQuery(id+"F0.wireOp",EDGE,"E1623"),sQuery(id+"F0.wireOp",EDGE,"E1624"),sQuery(id+"F0.wireOp",EDGE,"E1625"),sQuery(id+"F0.wireOp",EDGE,"E1626"),sQuery(id+"F0.wireOp",EDGE,"E1627"),sQuery(id+"F0.wireOp",EDGE,"E1628"),sQuery(id+"F0.wireOp",EDGE,"E1629"),sQuery(id+"F0.wireOp",EDGE,"E1630"),sQuery(id+"F0.wireOp",EDGE,"E1631"),sQuery(id+"F0.wireOp",EDGE,"E1632"),sQuery(id+"F0.wireOp",EDGE,"E1633"),sQuery(id+"F0.wireOp",EDGE,"E1634"),sQuery(id+"F0.wireOp",EDGE,"E1635"),sQuery(id+"F0.wireOp",EDGE,"E1635"),sQuery(id+"F0.wireOp",EDGE,"E1636"),sQuery(id+"F0.wireOp",EDGE,"E1637"),sQuery(id+"F0.wireOp",EDGE,"E1637"),sQuery(id+"F0.wireOp",EDGE,"E1638"),sQuery(id+"F0.wireOp",EDGE,"E1639"),sQuery(id+"F0.wireOp",EDGE,"E1639"),sQuery(id+"F0.wireOp",EDGE,"E1640"),sQuery(id+"F0.wireOp",EDGE,"E1641"),sQuery(id+"F0.wireOp",EDGE,"E1655"),sQuery(id+"F0.wireOp",EDGE,"E1656"),sQuery(id+"F0.wireOp",EDGE,"E1657"),sQuery(id+"F0.wireOp",EDGE,"E1658"),sQuery(id+"F0.wireOp",EDGE,"E1659"),sQuery(id+"F0.wireOp",EDGE,"E1660"),sQuery(id+"F0.wireOp",EDGE,"E1661"),sQuery(id+"F0.wireOp",EDGE,"E1662"),sQuery(id+"F0.wireOp",EDGE,"E1663"),sQuery(id+"F0.wireOp",EDGE,"E1664"),sQuery(id+"F0.wireOp",EDGE,"E1665"),sQuery(id+"F0.wireOp",EDGE,"E1666"),sQuery(id+"F0.wireOp",EDGE,"E1667"),sQuery(id+"F0.wireOp",EDGE,"E1668"),sQuery(id+"F0.wireOp",EDGE,"E1669"),sQuery(id+"F0.wireOp",EDGE,"E1670"),sQuery(id+"F0.wireOp",EDGE,"E1670"),sQuery(id+"F0.wireOp",EDGE,"E1671"),sQuery(id+"F0.wireOp",EDGE,"E1672"),sQuery(id+"F0.wireOp",EDGE,"E1672"),sQuery(id+"F0.wireOp",EDGE,"E1673"),sQuery(id+"F0.wireOp",EDGE,"E1674"),sQuery(id+"F0.wireOp",EDGE,"E1674"),sQuery(id+"F0.wireOp",EDGE,"E1675"),sQuery(id+"F0.wireOp",EDGE,"E1676"),sQuery(id+"F0.wireOp",EDGE,"E1677"),sQuery(id+"F0.wireOp",EDGE,"E1678"),sQuery(id+"F0.wireOp",EDGE,"E1679"),sQuery(id+"F0.wireOp",EDGE,"E1680"),sQuery(id+"F0.wireOp",EDGE,"E1681"),sQuery(id+"F0.wireOp",EDGE,"E1682"),sQuery(id+"F0.wireOp",EDGE,"E1683"),sQuery(id+"F0.wireOp",EDGE,"E1684"),sQuery(id+"F0.wireOp",EDGE,"E1684"),sQuery(id+"F0.wireOp",EDGE,"E1685"),sQuery(id+"F0.wireOp",EDGE,"E1686"),sQuery(id+"F0.wireOp",EDGE,"E1686"),sQuery(id+"F0.wireOp",EDGE,"E1687"),sQuery(id+"F0.wireOp",EDGE,"E1688"),sQuery(id+"F0.wireOp",EDGE,"E1688"),sQuery(id+"F0.wireOp",EDGE,"E1689"),sQuery(id+"F0.wireOp",EDGE,"E1690"),sQuery(id+"F0.wireOp",EDGE,"E1690"),sQuery(id+"F0.wireOp",EDGE,"E1691"),sQuery(id+"F0.wireOp",EDGE,"E1692"),sQuery(id+"F0.wireOp",EDGE,"E1692"),sQuery(id+"F0.wireOp",EDGE,"E1693"),sQuery(id+"F0.wireOp",EDGE,"E1694"),sQuery(id+"F0.wireOp",EDGE,"E1695"),sQuery(id+"F0.wireOp",EDGE,"E1696"),sQuery(id+"F0.wireOp",EDGE,"E1697"),sQuery(id+"F0.wireOp",EDGE,"E1697"),sQuery(id+"F0.wireOp",EDGE,"E1698"),sQuery(id+"F0.wireOp",EDGE,"E1699"),sQuery(id+"F0.wireOp",EDGE,"E1700"),sQuery(id+"F0.wireOp",EDGE,"E1701"),sQuery(id+"F0.wireOp",EDGE,"E1702"),sQuery(id+"F0.wireOp",EDGE,"E1703"),sQuery(id+"F0.wireOp",EDGE,"E1704"),sQuery(id+"F0.wireOp",EDGE,"E1705"),sQuery(id+"F0.wireOp",EDGE,"E1706"),sQuery(id+"F0.wireOp",EDGE,"E1706"),sQuery(id+"F0.wireOp",EDGE,"E1707"),sQuery(id+"F0.wireOp",EDGE,"E1708"),sQuery(id+"F0.wireOp",EDGE,"E1708"),sQuery(id+"F0.wireOp",EDGE,"E1709"),sQuery(id+"F0.wireOp",EDGE,"E1710"),sQuery(id+"F0.wireOp",EDGE,"E1710"),sQuery(id+"F0.wireOp",EDGE,"E1711"),sQuery(id+"F0.wireOp",EDGE,"E1712"),sQuery(id+"F0.wireOp",EDGE,"E1712"),sQuery(id+"F0.wireOp",EDGE,"E1712"),sQuery(id+"F0.wireOp",EDGE,"E1713"),sQuery(id+"F0.wireOp",EDGE,"E1714"),sQuery(id+"F0.wireOp",EDGE,"E1714"),sQuery(id+"F0.wireOp",EDGE,"E1715"),sQuery(id+"F0.wireOp",EDGE,"E1716"),sQuery(id+"F0.wireOp",EDGE,"E1716"),sQuery(id+"F0.wireOp",EDGE,"E1717"),sQuery(id+"F0.wireOp",EDGE,"E1718"),sQuery(id+"F0.wireOp",EDGE,"E1718"),sQuery(id+"F0.wireOp",EDGE,"E1719"),sQuery(id+"F0.wireOp",EDGE,"E1720"),sQuery(id+"F0.wireOp",EDGE,"E1720"),sQuery(id+"F0.wireOp",EDGE,"E1721"),sQuery(id+"F0.wireOp",EDGE,"E1722"),sQuery(id+"F0.wireOp",EDGE,"E1723"),sQuery(id+"F0.wireOp",EDGE,"E1724"),sQuery(id+"F0.wireOp",EDGE,"E1725"),sQuery(id+"F0.wireOp",EDGE,"E1726"),sQuery(id+"F0.wireOp",EDGE,"E1727"),sQuery(id+"F0.wireOp",EDGE,"E1728"),sQuery(id+"F0.wireOp",EDGE,"E1729"),sQuery(id+"F0.wireOp",EDGE,"E1730"),sQuery(id+"F0.wireOp",EDGE,"E1731"),sQuery(id+"F0.wireOp",EDGE,"E1731"),sQuery(id+"F0.wireOp",EDGE,"E1732"),sQuery(id+"F0.wireOp",EDGE,"E1733"),sQuery(id+"F0.wireOp",EDGE,"E1733"),sQuery(id+"F0.wireOp",EDGE,"E1733"),sQuery(id+"F0.wireOp",EDGE,"E1734"),sQuery(id+"F0.wireOp",EDGE,"E1735"),sQuery(id+"F0.wireOp",EDGE,"E1735"),sQuery(id+"F0.wireOp",EDGE,"E1735"),sQuery(id+"F0.wireOp",EDGE,"E1735"),sQuery(id+"F0.wireOp",EDGE,"E1736"),sQuery(id+"F0.wireOp",EDGE,"E1737"),sQuery(id+"F0.wireOp",EDGE,"E1738"),sQuery(id+"F0.wireOp",EDGE,"E1739"),sQuery(id+"F0.wireOp",EDGE,"E1739"),sQuery(id+"F0.wireOp",EDGE,"E1740"),sQuery(id+"F0.wireOp",EDGE,"E1741"),sQuery(id+"F0.wireOp",EDGE,"E1742"),sQuery(id+"F0.wireOp",EDGE,"E1742"),sQuery(id+"F0.wireOp",EDGE,"E1742"),sQuery(id+"F0.wireOp",EDGE,"E1742"),sQuery(id+"F0.wireOp",EDGE,"E1743"),sQuery(id+"F0.wireOp",EDGE,"E1744"),sQuery(id+"F0.wireOp",EDGE,"E1745"),sQuery(id+"F0.wireOp",EDGE,"E1746"),sQuery(id+"F0.wireOp",EDGE,"E1746"),sQuery(id+"F0.wireOp",EDGE,"E1746"),sQuery(id+"F0.wireOp",EDGE,"E1746"),sQuery(id+"F0.wireOp",EDGE,"E1747"),sQuery(id+"F0.wireOp",EDGE,"E1748"),sQuery(id+"F0.wireOp",EDGE,"E1748"),sQuery(id+"F0.wireOp",EDGE,"E1749"),sQuery(id+"F0.wireOp",EDGE,"E1750"),sQuery(id+"F0.wireOp",EDGE,"E1750"),sQuery(id+"F0.wireOp",EDGE,"E1751"),sQuery(id+"F0.wireOp",EDGE,"E1752"),sQuery(id+"F0.wireOp",EDGE,"E1753"),sQuery(id+"F0.wireOp",EDGE,"E1754"),sQuery(id+"F0.wireOp",EDGE,"E1755"),sQuery(id+"F0.wireOp",EDGE,"E1756"),sQuery(id+"F0.wireOp",EDGE,"E1756"),sQuery(id+"F0.wireOp",EDGE,"E1757"),sQuery(id+"F0.wireOp",EDGE,"E1758"),sQuery(id+"F0.wireOp",EDGE,"E1758"),sQuery(id+"F0.wireOp",EDGE,"E1759"),sQuery(id+"F0.wireOp",EDGE,"E1760"),sQuery(id+"F0.wireOp",EDGE,"E1760"),sQuery(id+"F0.wireOp",EDGE,"E1761"),sQuery(id+"F0.wireOp",EDGE,"E1762"),sQuery(id+"F0.wireOp",EDGE,"E1763"),sQuery(id+"F0.wireOp",EDGE,"E1764"),sQuery(id+"F0.wireOp",EDGE,"E1765"),sQuery(id+"F0.wireOp",EDGE,"E1766"),sQuery(id+"F0.wireOp",EDGE,"E1767"),sQuery(id+"F0.wireOp",EDGE,"E1768"),sQuery(id+"F0.wireOp",EDGE,"E1768"),sQuery(id+"F0.wireOp",EDGE,"E1768"),sQuery(id+"F0.wireOp",EDGE,"E1769"),sQuery(id+"F0.wireOp",EDGE,"E1770"),sQuery(id+"F0.wireOp",EDGE,"E1770"),sQuery(id+"F0.wireOp",EDGE,"E1770"),sQuery(id+"F0.wireOp",EDGE,"E1770"),sQuery(id+"F0.wireOp",EDGE,"E1783"),sQuery(id+"F0.wireOp",EDGE,"E1784"),sQuery(id+"F0.wireOp",EDGE,"E1785"),sQuery(id+"F0.wireOp",EDGE,"E1786"),sQuery(id+"F0.wireOp",EDGE,"E1787"),sQuery(id+"F0.wireOp",EDGE,"E1788"),sQuery(id+"F0.wireOp",EDGE,"E1789"),sQuery(id+"F0.wireOp",EDGE,"E1790"),sQuery(id+"F0.wireOp",EDGE,"E1791"),sQuery(id+"F0.wireOp",EDGE,"E1792"),sQuery(id+"F0.wireOp",EDGE,"E1793"),sQuery(id+"F0.wireOp",EDGE,"E1794"),sQuery(id+"F0.wireOp",EDGE,"E1795"),sQuery(id+"F0.wireOp",EDGE,"E1796"),sQuery(id+"F0.wireOp",EDGE,"E1797"),sQuery(id+"F0.wireOp",EDGE,"E1798"),sQuery(id+"F0.wireOp",EDGE,"E1798"),sQuery(id+"F0.wireOp",EDGE,"E1799"),sQuery(id+"F0.wireOp",EDGE,"E1800"),sQuery(id+"F0.wireOp",EDGE,"E1800"),sQuery(id+"F0.wireOp",EDGE,"E1800"),sQuery(id+"F0.wireOp",EDGE,"E1801"),sQuery(id+"F0.wireOp",EDGE,"E1802"),sQuery(id+"F0.wireOp",EDGE,"E1802"),sQuery(id+"F0.wireOp",EDGE,"E1802"),sQuery(id+"F0.wireOp",EDGE,"E1803"),sQuery(id+"F0.wireOp",EDGE,"E1804"),sQuery(id+"F0.wireOp",EDGE,"E1804"),sQuery(id+"F0.wireOp",EDGE,"E1805"),sQuery(id+"F0.wireOp",EDGE,"E1806"),sQuery(id+"F0.wireOp",EDGE,"E1806"),sQuery(id+"F0.wireOp",EDGE,"E1807"),sQuery(id+"F0.wireOp",EDGE,"E1808"),sQuery(id+"F0.wireOp",EDGE,"E1808"),sQuery(id+"F0.wireOp",EDGE,"E1808"),sQuery(id+"F0.wireOp",EDGE,"E1808"),sQuery(id+"F0.wireOp",EDGE,"E1808"),sQuery(id+"F0.wireOp",EDGE,"E1809"),sQuery(id+"F0.wireOp",EDGE,"E1810"),sQuery(id+"F0.wireOp",EDGE,"E1810"),sQuery(id+"F0.wireOp",EDGE,"E1811"),sQuery(id+"F0.wireOp",EDGE,"E1812"),sQuery(id+"F0.wireOp",EDGE,"E1812"),sQuery(id+"F0.wireOp",EDGE,"E1813"),sQuery(id+"F0.wireOp",EDGE,"E1814"),sQuery(id+"F0.wireOp",EDGE,"E1814"),sQuery(id+"F0.wireOp",EDGE,"E1815"),sQuery(id+"F0.wireOp",EDGE,"E1816"),sQuery(id+"F0.wireOp",EDGE,"E1816"),sQuery(id+"F0.wireOp",EDGE,"E1817"),sQuery(id+"F0.wireOp",EDGE,"E1818"),sQuery(id+"F0.wireOp",EDGE,"E1818"),sQuery(id+"F0.wireOp",EDGE,"E1819"),sQuery(id+"F0.wireOp",EDGE,"E1820"),sQuery(id+"F0.wireOp",EDGE,"E1821"),sQuery(id+"F0.wireOp",EDGE,"E1822"),sQuery(id+"F0.wireOp",EDGE,"E1823"),sQuery(id+"F0.wireOp",EDGE,"E1824"),sQuery(id+"F0.wireOp",EDGE,"E1825"),sQuery(id+"F0.wireOp",EDGE,"E1825"),sQuery(id+"F0.wireOp",EDGE,"E1825"),sQuery(id+"F0.wireOp",EDGE,"E1825"),sQuery(id+"F0.wireOp",EDGE,"E1826"),sQuery(id+"F0.wireOp",EDGE,"E1827"),sQuery(id+"F0.wireOp",EDGE,"E1827"),sQuery(id+"F0.wireOp",EDGE,"E1828"),sQuery(id+"F0.wireOp",EDGE,"E1829"),sQuery(id+"F0.wireOp",EDGE,"E1830"),sQuery(id+"F0.wireOp",EDGE,"E1830"),sQuery(id+"F0.wireOp",EDGE,"E1830"),sQuery(id+"F0.wireOp",EDGE,"E1831"),sQuery(id+"F0.wireOp",EDGE,"E1832"),sQuery(id+"F0.wireOp",EDGE,"E1833"),sQuery(id+"F0.wireOp",EDGE,"E1834"),sQuery(id+"F0.wireOp",EDGE,"E1835"),sQuery(id+"F0.wireOp",EDGE,"E1835"),sQuery(id+"F0.wireOp",EDGE,"E1836"),sQuery(id+"F0.wireOp",EDGE,"E1837"),sQuery(id+"F0.wireOp",EDGE,"E1837"),sQuery(id+"F0.wireOp",EDGE,"E1837"),sQuery(id+"F0.wireOp",EDGE,"E1837"),sQuery(id+"F0.wireOp",EDGE,"E1837"),sQuery(id+"F0.wireOp",EDGE,"E1838"),sQuery(id+"F0.wireOp",EDGE,"E1839"),sQuery(id+"F0.wireOp",EDGE,"E1840"),sQuery(id+"F0.wireOp",EDGE,"E1841"),sQuery(id+"F0.wireOp",EDGE,"E1842"),sQuery(id+"F0.wireOp",EDGE,"E1842"),sQuery(id+"F0.wireOp",EDGE,"E1842"),sQuery(id+"F0.wireOp",EDGE,"E1842"),sQuery(id+"F0.wireOp",EDGE,"E1843"),sQuery(id+"F0.wireOp",EDGE,"E1844"),sQuery(id+"F0.wireOp",EDGE,"E1845"),sQuery(id+"F0.wireOp",EDGE,"E1846"),sQuery(id+"F0.wireOp",EDGE,"E1846"),sQuery(id+"F0.wireOp",EDGE,"E1846"),sQuery(id+"F0.wireOp",EDGE,"E1846"),sQuery(id+"F0.wireOp",EDGE,"E1847"),sQuery(id+"F0.wireOp",EDGE,"E1848"),sQuery(id+"F0.wireOp",EDGE,"E1848"),sQuery(id+"F0.wireOp",EDGE,"E1848"),sQuery(id+"F0.wireOp",EDGE,"E1848"),sQuery(id+"F0.wireOp",EDGE,"E1849"),sQuery(id+"F0.wireOp",EDGE,"E1850"),sQuery(id+"F0.wireOp",EDGE,"E1850"),sQuery(id+"F0.wireOp",EDGE,"E1851"),sQuery(id+"F0.wireOp",EDGE,"E1852"),sQuery(id+"F0.wireOp",EDGE,"E1853"),sQuery(id+"F0.wireOp",EDGE,"E1854"),sQuery(id+"F0.wireOp",EDGE,"E1855"),sQuery(id+"F0.wireOp",EDGE,"E1871"),sQuery(id+"F0.wireOp",EDGE,"E1872"),sQuery(id+"F0.wireOp",EDGE,"E1873"),sQuery(id+"F0.wireOp",EDGE,"E1874"),sQuery(id+"F0.wireOp",EDGE,"E1875"),sQuery(id+"F0.wireOp",EDGE,"E1876"),sQuery(id+"F0.wireOp",EDGE,"E1877"),sQuery(id+"F0.wireOp",EDGE,"E1878"),sQuery(id+"F0.wireOp",EDGE,"E1879"),sQuery(id+"F0.wireOp",EDGE,"E1880"),sQuery(id+"F0.wireOp",EDGE,"E1881"),sQuery(id+"F0.wireOp",EDGE,"E1882"),sQuery(id+"F0.wireOp",EDGE,"E1883"),sQuery(id+"F0.wireOp",EDGE,"E1884"),sQuery(id+"F0.wireOp",EDGE,"E1885"),sQuery(id+"F0.wireOp",EDGE,"E1886"),sQuery(id+"F0.wireOp",EDGE,"E1886"),sQuery(id+"F0.wireOp",EDGE,"E1887"),sQuery(id+"F0.wireOp",EDGE,"E1888"),sQuery(id+"F0.wireOp",EDGE,"E1888"),sQuery(id+"F0.wireOp",EDGE,"E1888"),sQuery(id+"F0.wireOp",EDGE,"E1888"),sQuery(id+"F0.wireOp",EDGE,"E1888"),sQuery(id+"F0.wireOp",EDGE,"E1889"),sQuery(id+"F0.wireOp",EDGE,"E1890"),sQuery(id+"F0.wireOp",EDGE,"E1891"),sQuery(id+"F0.wireOp",EDGE,"E1892"),sQuery(id+"F0.wireOp",EDGE,"E1893"),sQuery(id+"F0.wireOp",EDGE,"E1894"),sQuery(id+"F0.wireOp",EDGE,"E1895"),sQuery(id+"F0.wireOp",EDGE,"E1895"),sQuery(id+"F0.wireOp",EDGE,"E1896"),sQuery(id+"F0.wireOp",EDGE,"E1897"),sQuery(id+"F0.wireOp",EDGE,"E1897"),sQuery(id+"F0.wireOp",EDGE,"E1898"),sQuery(id+"F0.wireOp",EDGE,"E1899"),sQuery(id+"F0.wireOp",EDGE,"E1899"),sQuery(id+"F0.wireOp",EDGE,"E1900"),sQuery(id+"F0.wireOp",EDGE,"E1901"),sQuery(id+"F0.wireOp",EDGE,"E1901"),sQuery(id+"F0.wireOp",EDGE,"E1902"),sQuery(id+"F0.wireOp",EDGE,"E1903"),sQuery(id+"F0.wireOp",EDGE,"E1903"),sQuery(id+"F0.wireOp",EDGE,"E1904"),sQuery(id+"F0.wireOp",EDGE,"E1905"),sQuery(id+"F0.wireOp",EDGE,"E1905"),sQuery(id+"F0.wireOp",EDGE,"E1906"),sQuery(id+"F0.wireOp",EDGE,"E1907"),sQuery(id+"F0.wireOp",EDGE,"E1908"),sQuery(id+"F0.wireOp",EDGE,"E1909"),sQuery(id+"F0.wireOp",EDGE,"E1910"),sQuery(id+"F0.wireOp",EDGE,"E1910"),sQuery(id+"F0.wireOp",EDGE,"E1911"),sQuery(id+"F0.wireOp",EDGE,"E1912"),sQuery(id+"F0.wireOp",EDGE,"E1912"),sQuery(id+"F0.wireOp",EDGE,"E1913"),sQuery(id+"F0.wireOp",EDGE,"E1914"),sQuery(id+"F0.wireOp",EDGE,"E1927"),sQuery(id+"F0.wireOp",EDGE,"E1928"),sQuery(id+"F0.wireOp",EDGE,"E1929"),sQuery(id+"F0.wireOp",EDGE,"E1929"),sQuery(id+"F0.wireOp",EDGE,"E1930"),sQuery(id+"F0.wireOp",EDGE,"E1931"),sQuery(id+"F0.wireOp",EDGE,"E1932"),sQuery(id+"F0.wireOp",EDGE,"E1933"),sQuery(id+"F0.wireOp",EDGE,"E1933"),sQuery(id+"F0.wireOp",EDGE,"E1934"),sQuery(id+"F0.wireOp",EDGE,"E1935"),sQuery(id+"F0.wireOp",EDGE,"E1935"),sQuery(id+"F0.wireOp",EDGE,"E1936"),sQuery(id+"F0.wireOp",EDGE,"E1937"),sQuery(id+"F0.wireOp",EDGE,"E1938"),sQuery(id+"F0.wireOp",EDGE,"E1939"),sQuery(id+"F0.wireOp",EDGE,"E1940"),sQuery(id+"F0.wireOp",EDGE,"E1941"),sQuery(id+"F0.wireOp",EDGE,"E1942"),sQuery(id+"F0.wireOp",EDGE,"E1943"),sQuery(id+"F0.wireOp",EDGE,"E1943"),sQuery(id+"F0.wireOp",EDGE,"E1944"),sQuery(id+"F0.wireOp",EDGE,"E1945"),sQuery(id+"F0.wireOp",EDGE,"E1946"),sQuery(id+"F0.wireOp",EDGE,"E1947"),sQuery(id+"F0.wireOp",EDGE,"E1948"),sQuery(id+"F0.wireOp",EDGE,"E1948"),sQuery(id+"F0.wireOp",EDGE,"E1949"),sQuery(id+"F0.wireOp",EDGE,"E1950"),sQuery(id+"F0.wireOp",EDGE,"E1951"),sQuery(id+"F0.wireOp",EDGE,"E1952"),sQuery(id+"F0.wireOp",EDGE,"E1953"),sQuery(id+"F0.wireOp",EDGE,"E1954"),sQuery(id+"F0.wireOp",EDGE,"E1955"),sQuery(id+"F0.wireOp",EDGE,"E1956"),sQuery(id+"F0.wireOp",EDGE,"E1957"),sQuery(id+"F0.wireOp",EDGE,"E1958"),sQuery(id+"F0.wireOp",EDGE,"E1959"),sQuery(id+"F0.wireOp",EDGE,"E1960"),sQuery(id+"F0.wireOp",EDGE,"E1961"),sQuery(id+"F0.wireOp",EDGE,"E1962"),sQuery(id+"F0.wireOp",EDGE,"E1963"),sQuery(id+"F0.wireOp",EDGE,"E1963"),sQuery(id+"F0.wireOp",EDGE,"E1964"),sQuery(id+"F0.wireOp",EDGE,"E1965"),sQuery(id+"F0.wireOp",EDGE,"E1966"),sQuery(id+"F0.wireOp",EDGE,"E1967"),sQuery(id+"F0.wireOp",EDGE,"E1968"),sQuery(id+"F0.wireOp",EDGE,"E1968"),sQuery(id+"F0.wireOp",EDGE,"E1968"),sQuery(id+"F0.wireOp",EDGE,"E1968"),sQuery(id+"F0.wireOp",EDGE,"E1968"),sQuery(id+"F0.wireOp",EDGE,"E1968"),sQuery(id+"F0.wireOp",EDGE,"E1969"),sQuery(id+"F0.wireOp",EDGE,"E1970"),sQuery(id+"F0.wireOp",EDGE,"E1971"),sQuery(id+"F0.wireOp",EDGE,"E1972"),sQuery(id+"F0.wireOp",EDGE,"E1973"),sQuery(id+"F0.wireOp",EDGE,"E1974"),sQuery(id+"F0.wireOp",EDGE,"E1975"),sQuery(id+"F0.wireOp",EDGE,"E1976"),sQuery(id+"F0.wireOp",EDGE,"E1977"),sQuery(id+"F0.wireOp",EDGE,"E1978"),sQuery(id+"F0.wireOp",EDGE,"E1978"),sQuery(id+"F0.wireOp",EDGE,"E1978"),sQuery(id+"F0.wireOp",EDGE,"E1978"),sQuery(id+"F0.wireOp",EDGE,"E1978"),sQuery(id+"F0.wireOp",EDGE,"E1979"),sQuery(id+"F0.wireOp",EDGE,"E1980"),sQuery(id+"F0.wireOp",EDGE,"E1981"),sQuery(id+"F0.wireOp",EDGE,"E1982"),sQuery(id+"F0.wireOp",EDGE,"E1982"),sQuery(id+"F0.wireOp",EDGE,"E1982"),sQuery(id+"F0.wireOp",EDGE,"E1982"),sQuery(id+"F0.wireOp",EDGE,"E1983"),sQuery(id+"F0.wireOp",EDGE,"E1984"),sQuery(id+"F0.wireOp",EDGE,"E1985"),sQuery(id+"F0.wireOp",EDGE,"E1986"),sQuery(id+"F0.wireOp",EDGE,"E1987"),sQuery(id+"F0.wireOp",EDGE,"E1988"),sQuery(id+"F0.wireOp",EDGE,"E1989"),sQuery(id+"F0.wireOp",EDGE,"E1989"),sQuery(id+"F0.wireOp",EDGE,"E1990"),sQuery(id+"F0.wireOp",EDGE,"E1991"),sQuery(id+"F0.wireOp",EDGE,"E1991"),sQuery(id+"F0.wireOp",EDGE,"E1992"),sQuery(id+"F0.wireOp",EDGE,"E1993"),sQuery(id+"F0.wireOp",EDGE,"E1994"),sQuery(id+"F0.wireOp",EDGE,"E1995"),sQuery(id+"F0.wireOp",EDGE,"E1996"),sQuery(id+"F0.wireOp",EDGE,"E1997"),sQuery(id+"F0.wireOp",EDGE,"E1997"),sQuery(id+"F0.wireOp",EDGE,"E1998"),sQuery(id+"F0.wireOp",EDGE,"E1999"),sQuery(id+"F0.wireOp",EDGE,"E2000"),sQuery(id+"F0.wireOp",EDGE,"E2000"),sQuery(id+"F0.wireOp",EDGE,"E2000"),sQuery(id+"F0.wireOp",EDGE,"E2001"),sQuery(id+"F0.wireOp",EDGE,"E2002"),sQuery(id+"F0.wireOp",EDGE,"E2002"),sQuery(id+"F0.wireOp",EDGE,"E2003"),sQuery(id+"F0.wireOp",EDGE,"E2004"),sQuery(id+"F0.wireOp",EDGE,"E2005"),sQuery(id+"F0.wireOp",EDGE,"E2006"),sQuery(id+"F0.wireOp",EDGE,"E2006"),sQuery(id+"F0.wireOp",EDGE,"E2007"),sQuery(id+"F0.wireOp",EDGE,"E2008"),sQuery(id+"F0.wireOp",EDGE,"E2008"),sQuery(id+"F0.wireOp",EDGE,"E2009"),sQuery(id+"F0.wireOp",EDGE,"E2010"),sQuery(id+"F0.wireOp",EDGE,"E2010"),sQuery(id+"F0.wireOp",EDGE,"E2011"),sQuery(id+"F0.wireOp",EDGE,"E2012"),sQuery(id+"F0.wireOp",EDGE,"E2013"),sQuery(id+"F0.wireOp",EDGE,"E2014"),sQuery(id+"F0.wireOp",EDGE,"E2015"),sQuery(id+"F0.wireOp",EDGE,"E2015"),sQuery(id+"F0.wireOp",EDGE,"E2015"),sQuery(id+"F0.wireOp",EDGE,"E2015"),sQuery(id+"F0.wireOp",EDGE,"E2016"),sQuery(id+"F0.wireOp",EDGE,"E2017"),sQuery(id+"F0.wireOp",EDGE,"E2017"),sQuery(id+"F0.wireOp",EDGE,"E2017"),sQuery(id+"F0.wireOp",EDGE,"E2018"),sQuery(id+"F0.wireOp",EDGE,"E2019"),sQuery(id+"F0.wireOp",EDGE,"E2020"),sQuery(id+"F0.wireOp",EDGE,"E2020"),sQuery(id+"F0.wireOp",EDGE,"E2020"),sQuery(id+"F0.wireOp",EDGE,"E2020"),sQuery(id+"F0.wireOp",EDGE,"E2021"),sQuery(id+"F0.wireOp",EDGE,"E2022"),sQuery(id+"F0.wireOp",EDGE,"E2023"),sQuery(id+"F0.wireOp",EDGE,"E2024"),sQuery(id+"F0.wireOp",EDGE,"E2025"),sQuery(id+"F0.wireOp",EDGE,"E2026"),sQuery(id+"F0.wireOp",EDGE,"E2027"),sQuery(id+"F0.wireOp",EDGE,"E2027"),sQuery(id+"F0.wireOp",EDGE,"E2028"),sQuery(id+"F0.wireOp",EDGE,"E2013"),sQuery(id+"F0.wireOp",EDGE,"E2029"),sQuery(id+"F0.wireOp",EDGE,"E2030"),sQuery(id+"F0.wireOp",EDGE,"E2031"),sQuery(id+"F0.wireOp",EDGE,"E2032"),sQuery(id+"F0.wireOp",EDGE,"E2032"),sQuery(id+"F0.wireOp",EDGE,"E2033"),sQuery(id+"F0.wireOp",EDGE,"E2034"),sQuery(id+"F0.wireOp",EDGE,"E2034"),sQuery(id+"F0.wireOp",EDGE,"E2034"),sQuery(id+"F0.wireOp",EDGE,"E2035"),sQuery(id+"F0.wireOp",EDGE,"E2036"),sQuery(id+"F0.wireOp",EDGE,"E2036"),sQuery(id+"F0.wireOp",EDGE,"E2036"),sQuery(id+"F0.wireOp",EDGE,"E2037"),sQuery(id+"F0.wireOp",EDGE,"E2038"),sQuery(id+"F0.wireOp",EDGE,"E2039"),sQuery(id+"F0.wireOp",EDGE,"E2040"),sQuery(id+"F0.wireOp",EDGE,"E2041"),sQuery(id+"F0.wireOp",EDGE,"E2042"),sQuery(id+"F0.wireOp",EDGE,"E2043"),sQuery(id+"F0.wireOp",EDGE,"E2043"),sQuery(id+"F0.wireOp",EDGE,"E2044"),sQuery(id+"F0.wireOp",EDGE,"E2045"),sQuery(id+"F0.wireOp",EDGE,"E2046"),sQuery(id+"F0.wireOp",EDGE,"E2047"),sQuery(id+"F0.wireOp",EDGE,"E2048"),sQuery(id+"F0.wireOp",EDGE,"E2048"),sQuery(id+"F0.wireOp",EDGE,"E2049"),sQuery(id+"F0.wireOp",EDGE,"E2050"),sQuery(id+"F0.wireOp",EDGE,"E2050"),sQuery(id+"F0.wireOp",EDGE,"E2051"),sQuery(id+"F0.wireOp",EDGE,"E2052"),sQuery(id+"F0.wireOp",EDGE,"E2053"),sQuery(id+"F0.wireOp",EDGE,"E2054"),sQuery(id+"F0.wireOp",EDGE,"E2055"),sQuery(id+"F0.wireOp",EDGE,"E2056"),sQuery(id+"F0.wireOp",EDGE,"E2057"),sQuery(id+"F0.wireOp",EDGE,"E2058"),sQuery(id+"F0.wireOp",EDGE,"E2059"),sQuery(id+"F0.wireOp",EDGE,"E2059"),sQuery(id+"F0.wireOp",EDGE,"E2059"),sQuery(id+"F0.wireOp",EDGE,"E2060"),sQuery(id+"F0.wireOp",EDGE,"E2061"),sQuery(id+"F0.wireOp",EDGE,"E2062"),sQuery(id+"F0.wireOp",EDGE,"E2063"),sQuery(id+"F0.wireOp",EDGE,"E2063"),sQuery(id+"F0.wireOp",EDGE,"E2064"),sQuery(id+"F0.wireOp",EDGE,"E2065"),sQuery(id+"F0.wireOp",EDGE,"E2066"),sQuery(id+"F0.wireOp",EDGE,"E2067"),sQuery(id+"F0.wireOp",EDGE,"E2068"),sQuery(id+"F0.wireOp",EDGE,"E2069"),sQuery(id+"F0.wireOp",EDGE,"E2069"),sQuery(id+"F0.wireOp",EDGE,"E2070"),sQuery(id+"F0.wireOp",EDGE,"E2071"),sQuery(id+"F0.wireOp",EDGE,"E2071"),sQuery(id+"F0.wireOp",EDGE,"E2072"),sQuery(id+"F0.wireOp",EDGE,"E2073"),sQuery(id+"F0.wireOp",EDGE,"E2073"),sQuery(id+"F0.wireOp",EDGE,"E2074"),sQuery(id+"F0.wireOp",EDGE,"E2075"),sQuery(id+"F0.wireOp",EDGE,"E2076"),sQuery(id+"F0.wireOp",EDGE,"E2077"),sQuery(id+"F0.wireOp",EDGE,"E2078"),sQuery(id+"F0.wireOp",EDGE,"E2079"),sQuery(id+"F0.wireOp",EDGE,"E2079"),sQuery(id+"F0.wireOp",EDGE,"E2080"),sQuery(id+"F0.wireOp",EDGE,"E2081"),sQuery(id+"F0.wireOp",EDGE,"E2081"),sQuery(id+"F0.wireOp",EDGE,"E2082"),sQuery(id+"F0.wireOp",EDGE,"E2083"),sQuery(id+"F0.wireOp",EDGE,"E2083"),sQuery(id+"F0.wireOp",EDGE,"E2084"),sQuery(id+"F0.wireOp",EDGE,"E2085"),sQuery(id+"F0.wireOp",EDGE,"E2086"),sQuery(id+"F0.wireOp",EDGE,"E2087"),sQuery(id+"F0.wireOp",EDGE,"E2088"),sQuery(id+"F0.wireOp",EDGE,"E2089"),sQuery(id+"F0.wireOp",EDGE,"E2089"),sQuery(id+"F0.wireOp",EDGE,"E2090"),sQuery(id+"F0.wireOp",EDGE,"E2091"),sQuery(id+"F0.wireOp",EDGE,"E2091"),sQuery(id+"F0.wireOp",EDGE,"E2092"),sQuery(id+"F0.wireOp",EDGE,"E2093"),sQuery(id+"F0.wireOp",EDGE,"E2093"),sQuery(id+"F0.wireOp",EDGE,"E2094"),sQuery(id+"F0.wireOp",EDGE,"E2095"),sQuery(id+"F0.wireOp",EDGE,"E2096"),sQuery(id+"F0.wireOp",EDGE,"E2097"),sQuery(id+"F0.wireOp",EDGE,"E2098"),sQuery(id+"F0.wireOp",EDGE,"E2099"),sQuery(id+"F0.wireOp",EDGE,"E2099"),sQuery(id+"F0.wireOp",EDGE,"E2100"),sQuery(id+"F0.wireOp",EDGE,"E2101"),sQuery(id+"F0.wireOp",EDGE,"E2101"),sQuery(id+"F0.wireOp",EDGE,"E2102"),sQuery(id+"F0.wireOp",EDGE,"E2103"),sQuery(id+"F0.wireOp",EDGE,"E2103"),sQuery(id+"F0.wireOp",EDGE,"E2103"),sQuery(id+"F0.wireOp",EDGE,"E2103"),sQuery(id+"F0.wireOp",EDGE,"E2104"),sQuery(id+"F0.wireOp",EDGE,"E2105"),sQuery(id+"F0.wireOp",EDGE,"E2106"),sQuery(id+"F0.wireOp",EDGE,"E2107"),sQuery(id+"F0.wireOp",EDGE,"E2107"),sQuery(id+"F0.wireOp",EDGE,"E2108"),sQuery(id+"F0.wireOp",EDGE,"E2109"),sQuery(id+"F0.wireOp",EDGE,"E2109"),sQuery(id+"F0.wireOp",EDGE,"E2110"),sQuery(id+"F0.wireOp",EDGE,"E2111"),sQuery(id+"F0.wireOp",EDGE,"E2111"),sQuery(id+"F0.wireOp",EDGE,"E2111"),sQuery(id+"F0.wireOp",EDGE,"E2111"),sQuery(id+"F0.wireOp",EDGE,"E2111"),sQuery(id+"F0.wireOp",EDGE,"E2112"),sQuery(id+"F0.wireOp",EDGE,"E2113"),sQuery(id+"F0.wireOp",EDGE,"E2114"),sQuery(id+"F0.wireOp",EDGE,"E2114"),sQuery(id+"F0.wireOp",EDGE,"E2115"),sQuery(id+"F0.wireOp",EDGE,"E2116"),sQuery(id+"F0.wireOp",EDGE,"E2116"),sQuery(id+"F0.wireOp",EDGE,"E2117"),sQuery(id+"F0.wireOp",EDGE,"E2118"),sQuery(id+"F0.wireOp",EDGE,"E2118"),sQuery(id+"F0.wireOp",EDGE,"E2119"),sQuery(id+"F0.wireOp",EDGE,"E2120"),sQuery(id+"F0.wireOp",EDGE,"E2120"),sQuery(id+"F0.wireOp",EDGE,"E2121"),sQuery(id+"F0.wireOp",EDGE,"E2122"),sQuery(id+"F0.wireOp",EDGE,"E2122"),sQuery(id+"F0.wireOp",EDGE,"E2123"),sQuery(id+"F0.wireOp",EDGE,"E2124"),sQuery(id+"F0.wireOp",EDGE,"E2125"),sQuery(id+"F0.wireOp",EDGE,"E2126"),sQuery(id+"F0.wireOp",EDGE,"E2127"),sQuery(id+"F0.wireOp",EDGE,"E2128"),sQuery(id+"F0.wireOp",EDGE,"E2129"),sQuery(id+"F0.wireOp",EDGE,"E2129"),sQuery(id+"F0.wireOp",EDGE,"E2129"),sQuery(id+"F0.wireOp",EDGE,"E2129"),sQuery(id+"F0.wireOp",EDGE,"E2130"),sQuery(id+"F0.wireOp",EDGE,"E2131"),sQuery(id+"F0.wireOp",EDGE,"E2131"),sQuery(id+"F0.wireOp",EDGE,"E2132"),sQuery(id+"F0.wireOp",EDGE,"E2133"),sQuery(id+"F0.wireOp",EDGE,"E2133"),sQuery(id+"F0.wireOp",EDGE,"E2133"),sQuery(id+"F0.wireOp",EDGE,"E2133"),sQuery(id+"F0.wireOp",EDGE,"E2134"),sQuery(id+"F0.wireOp",EDGE,"E2135"),sQuery(id+"F0.wireOp",EDGE,"E2136"),sQuery(id+"F0.wireOp",EDGE,"E2137"),sQuery(id+"F0.wireOp",EDGE,"E2138"),sQuery(id+"F0.wireOp",EDGE,"E2139"),sQuery(id+"F0.wireOp",EDGE,"E2140"),sQuery(id+"F0.wireOp",EDGE,"E2140"),sQuery(id+"F0.wireOp",EDGE,"E2141"),sQuery(id+"F0.wireOp",EDGE,"E2142"),sQuery(id+"F0.wireOp",EDGE,"E2142"),sQuery(id+"F0.wireOp",EDGE,"E2143"),sQuery(id+"F0.wireOp",EDGE,"E2144"),sQuery(id+"F0.wireOp",EDGE,"E2145"),sQuery(id+"F0.wireOp",EDGE,"E2146"),sQuery(id+"F0.wireOp",EDGE,"E2147"),sQuery(id+"F0.wireOp",EDGE,"E2148"),sQuery(id+"F0.wireOp",EDGE,"E2148"),sQuery(id+"F0.wireOp",EDGE,"E2149"),sQuery(id+"F0.wireOp",EDGE,"E2150"),sQuery(id+"F0.wireOp",EDGE,"E2150"),sQuery(id+"F0.wireOp",EDGE,"E2151"),sQuery(id+"F0.wireOp",EDGE,"E2152"),sQuery(id+"F0.wireOp",EDGE,"E2152"),sQuery(id+"F0.wireOp",EDGE,"E2153"),sQuery(id+"F0.wireOp",EDGE,"E2154"),sQuery(id+"F0.wireOp",EDGE,"E2155"),sQuery(id+"F0.wireOp",EDGE,"E2156"),sQuery(id+"F0.wireOp",EDGE,"E2157"),sQuery(id+"F0.wireOp",EDGE,"E2158"),sQuery(id+"F0.wireOp",EDGE,"E2159"),sQuery(id+"F0.wireOp",EDGE,"E2160"),sQuery(id+"F0.wireOp",EDGE,"E2161"),sQuery(id+"F0.wireOp",EDGE,"E2161"),sQuery(id+"F0.wireOp",EDGE,"E2162"),sQuery(id+"F0.wireOp",EDGE,"E2163"),sQuery(id+"F0.wireOp",EDGE,"E2163"),sQuery(id+"F0.wireOp",EDGE,"E2164"),sQuery(id+"F0.wireOp",EDGE,"E2165"),sQuery(id+"F0.wireOp",EDGE,"E2166"),sQuery(id+"F0.wireOp",EDGE,"E2167"),sQuery(id+"F0.wireOp",EDGE,"E2168"),sQuery(id+"F0.wireOp",EDGE,"E2169"),sQuery(id+"F0.wireOp",EDGE,"E2170"),sQuery(id+"F0.wireOp",EDGE,"E2171"),sQuery(id+"F0.wireOp",EDGE,"E2172"),sQuery(id+"F0.wireOp",EDGE,"E2172"),sQuery(id+"F0.wireOp",EDGE,"E2173"),sQuery(id+"F0.wireOp",EDGE,"E2174"),sQuery(id+"F0.wireOp",EDGE,"E2174"),sQuery(id+"F0.wireOp",EDGE,"E2175"),sQuery(id+"F0.wireOp",EDGE,"E2176"),sQuery(id+"F0.wireOp",EDGE,"E2177"),sQuery(id+"F0.wireOp",EDGE,"E2178"),sQuery(id+"F0.wireOp",EDGE,"E2179"),sQuery(id+"F0.wireOp",EDGE,"E2180"),sQuery(id+"F0.wireOp",EDGE,"E2180"),sQuery(id+"F0.wireOp",EDGE,"E2181"),sQuery(id+"F0.wireOp",EDGE,"E2182"),sQuery(id+"F0.wireOp",EDGE,"E2182"),sQuery(id+"F0.wireOp",EDGE,"E2183"),sQuery(id+"F0.wireOp",EDGE,"E2184"),sQuery(id+"F0.wireOp",EDGE,"E2184"),sQuery(id+"F0.wireOp",EDGE,"E2185"),sQuery(id+"F0.wireOp",EDGE,"E2186"),sQuery(id+"F0.wireOp",EDGE,"E2187"),sQuery(id+"F0.wireOp",EDGE,"E2188"),sQuery(id+"F0.wireOp",EDGE,"E2189"),sQuery(id+"F0.wireOp",EDGE,"E2190"),sQuery(id+"F0.wireOp",EDGE,"E2191"),sQuery(id+"F0.wireOp",EDGE,"E2192"),sQuery(id+"F0.wireOp",EDGE,"E2193"),sQuery(id+"F0.wireOp",EDGE,"E2193"),sQuery(id+"F0.wireOp",EDGE,"E2194"),sQuery(id+"F0.wireOp",EDGE,"E2195"),sQuery(id+"F0.wireOp",EDGE,"E2196"),sQuery(id+"F0.wireOp",EDGE,"E2197"),sQuery(id+"F0.wireOp",EDGE,"E2198"),sQuery(id+"F0.wireOp",EDGE,"E2199"),sQuery(id+"F0.wireOp",EDGE,"E2200"),sQuery(id+"F0.wireOp",EDGE,"E2200"),sQuery(id+"F0.wireOp",EDGE,"E2200"),sQuery(id+"F0.wireOp",EDGE,"E2200"),sQuery(id+"F0.wireOp",EDGE,"E2201"),sQuery(id+"F0.wireOp",EDGE,"E2202"),sQuery(id+"F0.wireOp",EDGE,"E2202"),sQuery(id+"F0.wireOp",EDGE,"E2203"),sQuery(id+"F0.wireOp",EDGE,"E2204"),sQuery(id+"F0.wireOp",EDGE,"E2204"),sQuery(id+"F0.wireOp",EDGE,"E2204"),sQuery(id+"F0.wireOp",EDGE,"E2204"),sQuery(id+"F0.wireOp",EDGE,"E2205"),sQuery(id+"F0.wireOp",EDGE,"E2206"),sQuery(id+"F0.wireOp",EDGE,"E2207"),sQuery(id+"F0.wireOp",EDGE,"E2208"),sQuery(id+"F0.wireOp",EDGE,"E2209"),sQuery(id+"F0.wireOp",EDGE,"E2210"),sQuery(id+"F0.wireOp",EDGE,"E2211"),sQuery(id+"F0.wireOp",EDGE,"E2211"),sQuery(id+"F0.wireOp",EDGE,"E2212"),sQuery(id+"F0.wireOp",EDGE,"E2213"),sQuery(id+"F0.wireOp",EDGE,"E2214"),sQuery(id+"F0.wireOp",EDGE,"E2215"),sQuery(id+"F0.wireOp",EDGE,"E2216"),sQuery(id+"F0.wireOp",EDGE,"E2230"),sQuery(id+"F0.wireOp",EDGE,"E2231"),sQuery(id+"F0.wireOp",EDGE,"E2232"),sQuery(id+"F0.wireOp",EDGE,"E2233"),sQuery(id+"F0.wireOp",EDGE,"E2234"),sQuery(id+"F0.wireOp",EDGE,"E2235"),sQuery(id+"F0.wireOp",EDGE,"E2236"),sQuery(id+"F0.wireOp",EDGE,"E2237"),sQuery(id+"F0.wireOp",EDGE,"E2238"),sQuery(id+"F0.wireOp",EDGE,"E2239"),sQuery(id+"F0.wireOp",EDGE,"E2240"),sQuery(id+"F0.wireOp",EDGE,"E2241"),sQuery(id+"F0.wireOp",EDGE,"E2242"),sQuery(id+"F0.wireOp",EDGE,"E2243"),sQuery(id+"F0.wireOp",EDGE,"E2244"),sQuery(id+"F0.wireOp",EDGE,"E2245"),sQuery(id+"F0.wireOp",EDGE,"E2246"),sQuery(id+"F0.wireOp",EDGE,"E2247"),sQuery(id+"F0.wireOp",EDGE,"E2248"),sQuery(id+"F0.wireOp",EDGE,"E2249"),sQuery(id+"F0.wireOp",EDGE,"E2250"),sQuery(id+"F0.wireOp",EDGE,"E2251"),sQuery(id+"F0.wireOp",EDGE,"E2252"),sQuery(id+"F0.wireOp",EDGE,"E2253"),sQuery(id+"F0.wireOp",EDGE,"E2254"),sQuery(id+"F0.wireOp",EDGE,"E2255"),sQuery(id+"F0.wireOp",EDGE,"E2255"),sQuery(id+"F0.wireOp",EDGE,"E2256"),sQuery(id+"F0.wireOp",EDGE,"E2257"),sQuery(id+"F0.wireOp",EDGE,"E2258"),sQuery(id+"F0.wireOp",EDGE,"E2259"),sQuery(id+"F0.wireOp",EDGE,"E2260"),sQuery(id+"F0.wireOp",EDGE,"E2260"),sQuery(id+"F0.wireOp",EDGE,"E2261"),sQuery(id+"F0.wireOp",EDGE,"E2262"),sQuery(id+"F0.wireOp",EDGE,"E2262"),sQuery(id+"F0.wireOp",EDGE,"E2263"),sQuery(id+"F0.wireOp",EDGE,"E2264"),sQuery(id+"F0.wireOp",EDGE,"E2265"),sQuery(id+"F0.wireOp",EDGE,"E2266"),sQuery(id+"F0.wireOp",EDGE,"E2267"),sQuery(id+"F0.wireOp",EDGE,"E2268"),sQuery(id+"F0.wireOp",EDGE,"E2269"),sQuery(id+"F0.wireOp",EDGE,"E2269"),sQuery(id+"F0.wireOp",EDGE,"E2269"),sQuery(id+"F0.wireOp",EDGE,"E2270"),sQuery(id+"F0.wireOp",EDGE,"E2271"),sQuery(id+"F0.wireOp",EDGE,"E2272"),sQuery(id+"F0.wireOp",EDGE,"E2272"),sQuery(id+"F0.wireOp",EDGE,"E2273"),sQuery(id+"F0.wireOp",EDGE,"E2274"),sQuery(id+"F0.wireOp",EDGE,"E2275"),sQuery(id+"F0.wireOp",EDGE,"E2276"),sQuery(id+"F0.wireOp",EDGE,"E2276"),sQuery(id+"F0.wireOp",EDGE,"E2276"),sQuery(id+"F0.wireOp",EDGE,"E2276"),sQuery(id+"F0.wireOp",EDGE,"E2277"),sQuery(id+"F0.wireOp",EDGE,"E2278"),sQuery(id+"F0.wireOp",EDGE,"E2279"),sQuery(id+"F0.wireOp",EDGE,"E2280"),sQuery(id+"F0.wireOp",EDGE,"E2280"),sQuery(id+"F0.wireOp",EDGE,"E2281"),sQuery(id+"F0.wireOp",EDGE,"E2282"),sQuery(id+"F0.wireOp",EDGE,"E2283"),sQuery(id+"F0.wireOp",EDGE,"E2284"),sQuery(id+"F0.wireOp",EDGE,"E2285"),sQuery(id+"F0.wireOp",EDGE,"E2286"),sQuery(id+"F0.wireOp",EDGE,"E2287"),sQuery(id+"F0.wireOp",EDGE,"E2288"),sQuery(id+"F0.wireOp",EDGE,"E2288"),sQuery(id+"F0.wireOp",EDGE,"E2289"),sQuery(id+"F0.wireOp",EDGE,"E2290"),sQuery(id+"F0.wireOp",EDGE,"E2291"),sQuery(id+"F0.wireOp",EDGE,"E2292"),sQuery(id+"F0.wireOp",EDGE,"E2293"),sQuery(id+"F0.wireOp",EDGE,"E2294"),sQuery(id+"F0.wireOp",EDGE,"E2295"),sQuery(id+"F0.wireOp",EDGE,"E2296"),sQuery(id+"F0.wireOp",EDGE,"E2297"),sQuery(id+"F0.wireOp",EDGE,"E2298"),sQuery(id+"F0.wireOp",EDGE,"E2299"),sQuery(id+"F0.wireOp",EDGE,"E2300"),sQuery(id+"F0.wireOp",EDGE,"E2301"),sQuery(id+"F0.wireOp",EDGE,"E2302"),sQuery(id+"F0.wireOp",EDGE,"E2303"),sQuery(id+"F0.wireOp",EDGE,"E2304"),sQuery(id+"F0.wireOp",EDGE,"E2305"),sQuery(id+"F0.wireOp",EDGE,"E2306"),sQuery(id+"F0.wireOp",EDGE,"E2307"),sQuery(id+"F0.wireOp",EDGE,"E2308"),sQuery(id+"F0.wireOp",EDGE,"E2309"),sQuery(id+"F0.wireOp",EDGE,"E2310"),sQuery(id+"F0.wireOp",EDGE,"E2311"),sQuery(id+"F0.wireOp",EDGE,"E2312"),sQuery(id+"F0.wireOp",EDGE,"E2313"),sQuery(id+"F0.wireOp",EDGE,"E2314"),sQuery(id+"F0.wireOp",EDGE,"E2315"),sQuery(id+"F0.wireOp",EDGE,"E2316"),sQuery(id+"F0.wireOp",EDGE,"E2317"),sQuery(id+"F0.wireOp",EDGE,"E2318"),sQuery(id+"F0.wireOp",EDGE,"E2319"),sQuery(id+"F0.wireOp",EDGE,"E2320"),sQuery(id+"F0.wireOp",EDGE,"E2320"),sQuery(id+"F0.wireOp",EDGE,"E2321"),sQuery(id+"F0.wireOp",EDGE,"E2322"),sQuery(id+"F0.wireOp",EDGE,"E2323"),sQuery(id+"F0.wireOp",EDGE,"E2324"),sQuery(id+"F0.wireOp",EDGE,"E2325"),sQuery(id+"F0.wireOp",EDGE,"E2325"),sQuery(id+"F0.wireOp",EDGE,"E2326"),sQuery(id+"F0.wireOp",EDGE,"E2327"),sQuery(id+"F0.wireOp",EDGE,"E2328"),sQuery(id+"F0.wireOp",EDGE,"E2329"),sQuery(id+"F0.wireOp",EDGE,"E2330"),sQuery(id+"F0.wireOp",EDGE,"E2330"),sQuery(id+"F0.wireOp",EDGE,"E2331"),sQuery(id+"F0.wireOp",EDGE,"E2332"),sQuery(id+"F0.wireOp",EDGE,"E2332"),sQuery(id+"F0.wireOp",EDGE,"E2332"),sQuery(id+"F0.wireOp",EDGE,"E2332"),sQuery(id+"F0.wireOp",EDGE,"E2332"),sQuery(id+"F0.wireOp",EDGE,"E2333"),sQuery(id+"F0.wireOp",EDGE,"E2334"),sQuery(id+"F0.wireOp",EDGE,"E2335"),sQuery(id+"F0.wireOp",EDGE,"E2336"),sQuery(id+"F0.wireOp",EDGE,"E2337"),sQuery(id+"F0.wireOp",EDGE,"E2337"),sQuery(id+"F0.wireOp",EDGE,"E2338"),sQuery(id+"F0.wireOp",EDGE,"E2339"),sQuery(id+"F0.wireOp",EDGE,"E2340"),sQuery(id+"F0.wireOp",EDGE,"E2320"),sQuery(id+"F0.wireOp",EDGE,"E2341"),sQuery(id+"F0.wireOp",EDGE,"E2342"),sQuery(id+"F0.wireOp",EDGE,"E2343"),sQuery(id+"F0.wireOp",EDGE,"E2344"),sQuery(id+"F0.wireOp",EDGE,"E2345"),sQuery(id+"F0.wireOp",EDGE,"E2345"),sQuery(id+"F0.wireOp",EDGE,"E2345"),sQuery(id+"F0.wireOp",EDGE,"E2345"),sQuery(id+"F0.wireOp",EDGE,"E2346"),sQuery(id+"F0.wireOp",EDGE,"E2347"),sQuery(id+"F0.wireOp",EDGE,"E2347"),sQuery(id+"F0.wireOp",EDGE,"E2348"),sQuery(id+"F0.wireOp",EDGE,"E2349"),sQuery(id+"F0.wireOp",EDGE,"E2350"),sQuery(id+"F0.wireOp",EDGE,"E2351"),sQuery(id+"F0.wireOp",EDGE,"E2351"),sQuery(id+"F0.wireOp",EDGE,"E2352"),sQuery(id+"F0.wireOp",EDGE,"E2353"),sQuery(id+"F0.wireOp",EDGE,"E2354"),sQuery(id+"F0.wireOp",EDGE,"E2355"),sQuery(id+"F0.wireOp",EDGE,"E2355"),sQuery(id+"F0.wireOp",EDGE,"E2355"),sQuery(id+"F0.wireOp",EDGE,"E2356"),sQuery(id+"F0.wireOp",EDGE,"E2357"),sQuery(id+"F0.wireOp",EDGE,"E2358"),sQuery(id+"F0.wireOp",EDGE,"E2359"),sQuery(id+"F0.wireOp",EDGE,"E2360"),sQuery(id+"F0.wireOp",EDGE,"E2361"),sQuery(id+"F0.wireOp",EDGE,"E2362"),sQuery(id+"F0.wireOp",EDGE,"E2363"),sQuery(id+"F0.wireOp",EDGE,"E2364"),sQuery(id+"F0.wireOp",EDGE,"E2365"),sQuery(id+"F0.wireOp",EDGE,"E2366"),sQuery(id+"F0.wireOp",EDGE,"E2366"),sQuery(id+"F0.wireOp",EDGE,"E2367"),sQuery(id+"F0.wireOp",EDGE,"E2364"),sQuery(id+"F0.wireOp",EDGE,"E2364"),sQuery(id+"F0.wireOp",EDGE,"E2368"),sQuery(id+"F0.wireOp",EDGE,"E2369"),sQuery(id+"F0.wireOp",EDGE,"E2369"),sQuery(id+"F0.wireOp",EDGE,"E2370"),sQuery(id+"F0.wireOp",EDGE,"E2371"),sQuery(id+"F0.wireOp",EDGE,"E2372"),sQuery(id+"F0.wireOp",EDGE,"E2373"),sQuery(id+"F0.wireOp",EDGE,"E2373"),sQuery(id+"F0.wireOp",EDGE,"E2373"),sQuery(id+"F0.wireOp",EDGE,"E2373"),sQuery(id+"F0.wireOp",EDGE,"E2374"),sQuery(id+"F0.wireOp",EDGE,"E2375"),sQuery(id+"F0.wireOp",EDGE,"E2375"),sQuery(id+"F0.wireOp",EDGE,"E2376"),sQuery(id+"F0.wireOp",EDGE,"E2377"),sQuery(id+"F0.wireOp",EDGE,"E2377"),sQuery(id+"F0.wireOp",EDGE,"E2378"),sQuery(id+"F0.wireOp",EDGE,"E2379"),sQuery(id+"F0.wireOp",EDGE,"E2380"),sQuery(id+"F0.wireOp",EDGE,"E2381"),sQuery(id+"F0.wireOp",EDGE,"E2381"),sQuery(id+"F0.wireOp",EDGE,"E2382"),sQuery(id+"F0.wireOp",EDGE,"E2383"),sQuery(id+"F0.wireOp",EDGE,"E2383"),sQuery(id+"F0.wireOp",EDGE,"E2384"),sQuery(id+"F0.wireOp",EDGE,"E2385"),sQuery(id+"F0.wireOp",EDGE,"E2386"),sQuery(id+"F0.wireOp",EDGE,"E2387"),sQuery(id+"F0.wireOp",EDGE,"E2387"),sQuery(id+"F0.wireOp",EDGE,"E2387"),sQuery(id+"F0.wireOp",EDGE,"E2387"),sQuery(id+"F0.wireOp",EDGE,"E2402"),sQuery(id+"F0.wireOp",EDGE,"E2403"),sQuery(id+"F0.wireOp",EDGE,"E2404"),sQuery(id+"F0.wireOp",EDGE,"E2405"),sQuery(id+"F0.wireOp",EDGE,"E2405"),sQuery(id+"F0.wireOp",EDGE,"E2406"),sQuery(id+"F0.wireOp",EDGE,"E2407"),sQuery(id+"F0.wireOp",EDGE,"E2407"),sQuery(id+"F0.wireOp",EDGE,"E2408"),sQuery(id+"F0.wireOp",EDGE,"E2409"),sQuery(id+"F0.wireOp",EDGE,"E2410"),sQuery(id+"F0.wireOp",EDGE,"E2411"),sQuery(id+"F0.wireOp",EDGE,"E2412"),sQuery(id+"F0.wireOp",EDGE,"E2412"),sQuery(id+"F0.wireOp",EDGE,"E2413"),sQuery(id+"F0.wireOp",EDGE,"E2414"),sQuery(id+"F0.wireOp",EDGE,"E2415"),sQuery(id+"F0.wireOp",EDGE,"E2416"),sQuery(id+"F0.wireOp",EDGE,"E2417"),sQuery(id+"F0.wireOp",EDGE,"E2417"),sQuery(id+"F0.wireOp",EDGE,"E2417"),sQuery(id+"F0.wireOp",EDGE,"E2417"),sQuery(id+"F0.wireOp",EDGE,"E2417"),sQuery(id+"F0.wireOp",EDGE,"E2418"),sQuery(id+"F0.wireOp",EDGE,"E2419"),sQuery(id+"F0.wireOp",EDGE,"E2420"),sQuery(id+"F0.wireOp",EDGE,"E2421"),sQuery(id+"F0.wireOp",EDGE,"E2422"),sQuery(id+"F0.wireOp",EDGE,"E2423"),sQuery(id+"F0.wireOp",EDGE,"E2424"),sQuery(id+"F0.wireOp",EDGE,"E2424"),sQuery(id+"F0.wireOp",EDGE,"E2425"),sQuery(id+"F0.wireOp",EDGE,"E2426"),sQuery(id+"F0.wireOp",EDGE,"E2427"),sQuery(id+"F0.wireOp",EDGE,"E2428"),sQuery(id+"F0.wireOp",EDGE,"E2429"),sQuery(id+"F0.wireOp",EDGE,"E2429"),sQuery(id+"F0.wireOp",EDGE,"E2430"),sQuery(id+"F0.wireOp",EDGE,"E2431"),sQuery(id+"F0.wireOp",EDGE,"E2431"),sQuery(id+"F0.wireOp",EDGE,"E2431"),sQuery(id+"F0.wireOp",EDGE,"E2431"),sQuery(id+"F0.wireOp",EDGE,"E2431"),sQuery(id+"F0.wireOp",EDGE,"E2431"),sQuery(id+"F0.wireOp",EDGE,"E2431"),sQuery(id+"F0.wireOp",EDGE,"E2431"),sQuery(id+"F0.wireOp",EDGE,"E2432"),sQuery(id+"F0.wireOp",EDGE,"E2433"),sQuery(id+"F0.wireOp",EDGE,"E2433"),sQuery(id+"F0.wireOp",EDGE,"E2434"),sQuery(id+"F0.wireOp",EDGE,"E2435"),sQuery(id+"F0.wireOp",EDGE,"E2436"),sQuery(id+"F0.wireOp",EDGE,"E2437"),sQuery(id+"F0.wireOp",EDGE,"E2438"),sQuery(id+"F0.wireOp",EDGE,"E2439"),sQuery(id+"F0.wireOp",EDGE,"E2440"),sQuery(id+"F0.wireOp",EDGE,"E2441"),sQuery(id+"F0.wireOp",EDGE,"E2442"),sQuery(id+"F0.wireOp",EDGE,"E2443"),sQuery(id+"F0.wireOp",EDGE,"E2444"),sQuery(id+"F0.wireOp",EDGE,"E2444"),sQuery(id+"F0.wireOp",EDGE,"E2445"),sQuery(id+"F0.wireOp",EDGE,"E2446"),sQuery(id+"F0.wireOp",EDGE,"E2446"),sQuery(id+"F0.wireOp",EDGE,"E2447"),sQuery(id+"F0.wireOp",EDGE,"E2448"),sQuery(id+"F0.wireOp",EDGE,"E2448"),sQuery(id+"F0.wireOp",EDGE,"E2449"),sQuery(id+"F0.wireOp",EDGE,"E2450"),sQuery(id+"F0.wireOp",EDGE,"E2450"),sQuery(id+"F0.wireOp",EDGE,"E2451"),sQuery(id+"F0.wireOp",EDGE,"E2452"),sQuery(id+"F0.wireOp",EDGE,"E2452"),sQuery(id+"F0.wireOp",EDGE,"E2453"),sQuery(id+"F0.wireOp",EDGE,"E2454"),sQuery(id+"F0.wireOp",EDGE,"E2455"),sQuery(id+"F0.wireOp",EDGE,"E2455"),sQuery(id+"F0.wireOp",EDGE,"E2456"),sQuery(id+"F0.wireOp",EDGE,"E2457"),sQuery(id+"F0.wireOp",EDGE,"E2458"),sQuery(id+"F0.wireOp",EDGE,"E2459"),sQuery(id+"F0.wireOp",EDGE,"E2459"),sQuery(id+"F0.wireOp",EDGE,"E2460"),sQuery(id+"F0.wireOp",EDGE,"E2461"),sQuery(id+"F0.wireOp",EDGE,"E2461"),sQuery(id+"F0.wireOp",EDGE,"E2462"),sQuery(id+"F0.wireOp",EDGE,"E2463"),sQuery(id+"F0.wireOp",EDGE,"E2463"),sQuery(id+"F0.wireOp",EDGE,"E2464"),sQuery(id+"F0.wireOp",EDGE,"E2465"),sQuery(id+"F0.wireOp",EDGE,"E2465"),sQuery(id+"F0.wireOp",EDGE,"E2466"),sQuery(id+"F0.wireOp",EDGE,"E2467"),sQuery(id+"F0.wireOp",EDGE,"E2467"),sQuery(id+"F0.wireOp",EDGE,"E2468"),sQuery(id+"F0.wireOp",EDGE,"E2469"),sQuery(id+"F0.wireOp",EDGE,"E2469"),sQuery(id+"F0.wireOp",EDGE,"E2470"),sQuery(id+"F0.wireOp",EDGE,"E2471"),sQuery(id+"F0.wireOp",EDGE,"E2472"),sQuery(id+"F0.wireOp",EDGE,"E2473"),sQuery(id+"F0.wireOp",EDGE,"E2474"),sQuery(id+"F0.wireOp",EDGE,"E2474"),sQuery(id+"F0.wireOp",EDGE,"E2474"),sQuery(id+"F0.wireOp",EDGE,"E2474"),sQuery(id+"F0.wireOp",EDGE,"E2474"),sQuery(id+"F0.wireOp",EDGE,"E2474"),sQuery(id+"F0.wireOp",EDGE,"E2474"),sQuery(id+"F0.wireOp",EDGE,"E2474"),sQuery(id+"F0.wireOp",EDGE,"E2475"),sQuery(id+"F0.wireOp",EDGE,"E2476"),sQuery(id+"F0.wireOp",EDGE,"E2477"),sQuery(id+"F0.wireOp",EDGE,"E2478"),sQuery(id+"F0.wireOp",EDGE,"E2479"),sQuery(id+"F0.wireOp",EDGE,"E2480"),sQuery(id+"F0.wireOp",EDGE,"E2481"),sQuery(id+"F0.wireOp",EDGE,"E2482"),sQuery(id+"F0.wireOp",EDGE,"E2483"),sQuery(id+"F0.wireOp",EDGE,"E2484"),sQuery(id+"F0.wireOp",EDGE,"E2484"),sQuery(id+"F0.wireOp",EDGE,"E2485"),sQuery(id+"F0.wireOp",EDGE,"E2486"),sQuery(id+"F0.wireOp",EDGE,"E2487"),sQuery(id+"F0.wireOp",EDGE,"E2487"),sQuery(id+"F0.wireOp",EDGE,"E2487"),sQuery(id+"F0.wireOp",EDGE,"E2487"),sQuery(id+"F0.wireOp",EDGE,"E2487"),sQuery(id+"F0.wireOp",EDGE,"E2488"),sQuery(id+"F0.wireOp",EDGE,"E2489"),sQuery(id+"F0.wireOp",EDGE,"E2490"),sQuery(id+"F0.wireOp",EDGE,"E2491"),sQuery(id+"F0.wireOp",EDGE,"E2492"),sQuery(id+"F0.wireOp",EDGE,"E2492"),sQuery(id+"F0.wireOp",EDGE,"E2493"),sQuery(id+"F0.wireOp",EDGE,"E2494"),sQuery(id+"F0.wireOp",EDGE,"E2494"),sQuery(id+"F0.wireOp",EDGE,"E2495"),sQuery(id+"F0.wireOp",EDGE,"E2496"),sQuery(id+"F0.wireOp",EDGE,"E2496"),sQuery(id+"F0.wireOp",EDGE,"E2497"),sQuery(id+"F0.wireOp",EDGE,"E2498"),sQuery(id+"F0.wireOp",EDGE,"E2498"),sQuery(id+"F0.wireOp",EDGE,"E2499"),sQuery(id+"F0.wireOp",EDGE,"E2500"),sQuery(id+"F0.wireOp",EDGE,"E2501"),sQuery(id+"F0.wireOp",EDGE,"E2502"),sQuery(id+"F0.wireOp",EDGE,"E2503"),sQuery(id+"F0.wireOp",EDGE,"E2503"),sQuery(id+"F0.wireOp",EDGE,"E2504"),sQuery(id+"F0.wireOp",EDGE,"E2442"),sQuery(id+"F0.wireOp",EDGE,"E2505"),sQuery(id+"F0.wireOp",EDGE,"E2506"),sQuery(id+"F0.wireOp",EDGE,"E2506"),sQuery(id+"F0.wireOp",EDGE,"E2506"),sQuery(id+"F0.wireOp",EDGE,"E2506"),sQuery(id+"F0.wireOp",EDGE,"E2507"),sQuery(id+"F0.wireOp",EDGE,"E2508"),sQuery(id+"F0.wireOp",EDGE,"E2509"),sQuery(id+"F0.wireOp",EDGE,"E2510"),sQuery(id+"F0.wireOp",EDGE,"E2511"),sQuery(id+"F0.wireOp",EDGE,"E2511"),sQuery(id+"F0.wireOp",EDGE,"E2511"),sQuery(id+"F0.wireOp",EDGE,"E2511"),sQuery(id+"F0.wireOp",EDGE,"E2512"),sQuery(id+"F0.wireOp",EDGE,"E2513"),sQuery(id+"F0.wireOp",EDGE,"E2514"),sQuery(id+"F0.wireOp",EDGE,"E2515"),sQuery(id+"F0.wireOp",EDGE,"E2516"),sQuery(id+"F0.wireOp",EDGE,"E2516"),sQuery(id+"F0.wireOp",EDGE,"E2516"),sQuery(id+"F0.wireOp",EDGE,"E2516"),sQuery(id+"F0.wireOp",EDGE,"E2516"),sQuery(id+"F0.wireOp",EDGE,"E2517"),sQuery(id+"F0.wireOp",EDGE,"E2518"),sQuery(id+"F0.wireOp",EDGE,"E2518"),sQuery(id+"F0.wireOp",EDGE,"E2518"),sQuery(id+"F0.wireOp",EDGE,"E2518"),sQuery(id+"F0.wireOp",EDGE,"E2519"),sQuery(id+"F0.wireOp",EDGE,"E2520"),sQuery(id+"F0.wireOp",EDGE,"E2521"),sQuery(id+"F0.wireOp",EDGE,"E2522"),sQuery(id+"F0.wireOp",EDGE,"E2523"),sQuery(id+"F0.wireOp",EDGE,"E2523"),sQuery(id+"F0.wireOp",EDGE,"E2524"),sQuery(id+"F0.wireOp",EDGE,"E2525"),sQuery(id+"F0.wireOp",EDGE,"E2526"),sQuery(id+"F0.wireOp",EDGE,"E2527"),sQuery(id+"F0.wireOp",EDGE,"E2527"),sQuery(id+"F0.wireOp",EDGE,"E2527"),sQuery(id+"F0.wireOp",EDGE,"E2527"),sQuery(id+"F0.wireOp",EDGE,"E2527"),sQuery(id+"F0.wireOp",EDGE,"E2528"),sQuery(id+"F0.wireOp",EDGE,"E2529"),sQuery(id+"F0.wireOp",EDGE,"E2530"),sQuery(id+"F0.wireOp",EDGE,"E2531"),sQuery(id+"F0.wireOp",EDGE,"E2531"),sQuery(id+"F0.wireOp",EDGE,"E2531"),sQuery(id+"F0.wireOp",EDGE,"E2531"),sQuery(id+"F0.wireOp",EDGE,"E2532"),sQuery(id+"F0.wireOp",EDGE,"E2533"),sQuery(id+"F0.wireOp",EDGE,"E2534"),sQuery(id+"F0.wireOp",EDGE,"E2535"),sQuery(id+"F0.wireOp",EDGE,"E2536"),sQuery(id+"F0.wireOp",EDGE,"E2557"),sQuery(id+"F0.wireOp",EDGE,"E2558"),sQuery(id+"F0.wireOp",EDGE,"E2559"),sQuery(id+"F0.wireOp",EDGE,"E2560"),sQuery(id+"F0.wireOp",EDGE,"E2561"),sQuery(id+"F0.wireOp",EDGE,"E2562"),sQuery(id+"F0.wireOp",EDGE,"E2563"),sQuery(id+"F0.wireOp",EDGE,"E2564"),sQuery(id+"F0.wireOp",EDGE,"E2565"),sQuery(id+"F0.wireOp",EDGE,"E2566"),sQuery(id+"F0.wireOp",EDGE,"E2567"),sQuery(id+"F0.wireOp",EDGE,"E2568"),sQuery(id+"F0.wireOp",EDGE,"E2569"),sQuery(id+"F0.wireOp",EDGE,"E2570"),sQuery(id+"F0.wireOp",EDGE,"E2571"),sQuery(id+"F0.wireOp",EDGE,"E2572"),sQuery(id+"F0.wireOp",EDGE,"E2573"),sQuery(id+"F0.wireOp",EDGE,"E2573"),sQuery(id+"F0.wireOp",EDGE,"E2574"),sQuery(id+"F0.wireOp",EDGE,"E2575"),sQuery(id+"F0.wireOp",EDGE,"E2575"),sQuery(id+"F0.wireOp",EDGE,"E2576"),sQuery(id+"F0.wireOp",EDGE,"E2577"),sQuery(id+"F0.wireOp",EDGE,"E2578"),sQuery(id+"F0.wireOp",EDGE,"E2579"),sQuery(id+"F0.wireOp",EDGE,"E2580"),sQuery(id+"F0.wireOp",EDGE,"E2581"),sQuery(id+"F0.wireOp",EDGE,"E2582"),sQuery(id+"F0.wireOp",EDGE,"E2583"),sQuery(id+"F0.wireOp",EDGE,"E2583"),sQuery(id+"F0.wireOp",EDGE,"E2584"),sQuery(id+"F0.wireOp",EDGE,"E2585"),sQuery(id+"F0.wireOp",EDGE,"E2585"),sQuery(id+"F0.wireOp",EDGE,"E2586"),sQuery(id+"F0.wireOp",EDGE,"E2587"),sQuery(id+"F0.wireOp",EDGE,"E2587"),sQuery(id+"F0.wireOp",EDGE,"E2587"),sQuery(id+"F0.wireOp",EDGE,"E2587"),sQuery(id+"F0.wireOp",EDGE,"E2587"),sQuery(id+"F0.wireOp",EDGE,"E2588"),sQuery(id+"F0.wireOp",EDGE,"E2589"),sQuery(id+"F0.wireOp",EDGE,"E2589"),sQuery(id+"F0.wireOp",EDGE,"E2590"),sQuery(id+"F0.wireOp",EDGE,"E2591"),sQuery(id+"F0.wireOp",EDGE,"E2591"),sQuery(id+"F0.wireOp",EDGE,"E2592"),sQuery(id+"F0.wireOp",EDGE,"E2593"),sQuery(id+"F0.wireOp",EDGE,"E2594"),sQuery(id+"F0.wireOp",EDGE,"E2581"),sQuery(id+"F0.wireOp",EDGE,"E2581"),sQuery(id+"F0.wireOp",EDGE,"E2595"),sQuery(id+"F0.wireOp",EDGE,"E2596"),sQuery(id+"F0.wireOp",EDGE,"E2597"),sQuery(id+"F0.wireOp",EDGE,"E2597"),sQuery(id+"F0.wireOp",EDGE,"E2598"),sQuery(id+"F0.wireOp",EDGE,"E2599"),sQuery(id+"F0.wireOp",EDGE,"E2600"),sQuery(id+"F0.wireOp",EDGE,"E2601"),sQuery(id+"F0.wireOp",EDGE,"E2602"),sQuery(id+"F0.wireOp",EDGE,"E2602"),sQuery(id+"F0.wireOp",EDGE,"E2602"),sQuery(id+"F0.wireOp",EDGE,"E2602"),sQuery(id+"F0.wireOp",EDGE,"E2602"),sQuery(id+"F0.wireOp",EDGE,"E2603"),sQuery(id+"F0.wireOp",EDGE,"E2604"),sQuery(id+"F0.wireOp",EDGE,"E2605"),sQuery(id+"F0.wireOp",EDGE,"E2606"),sQuery(id+"F0.wireOp",EDGE,"E2607"),sQuery(id+"F0.wireOp",EDGE,"E2608"),sQuery(id+"F0.wireOp",EDGE,"E2609"),sQuery(id+"F0.wireOp",EDGE,"E2610"),sQuery(id+"F0.wireOp",EDGE,"E2610"),sQuery(id+"F0.wireOp",EDGE,"E2611"),sQuery(id+"F0.wireOp",EDGE,"E2595"),sQuery(id+"F0.wireOp",EDGE,"E2612"),sQuery(id+"F0.wireOp",EDGE,"E2613"),sQuery(id+"F0.wireOp",EDGE,"E2613"),sQuery(id+"F0.wireOp",EDGE,"E2613"),sQuery(id+"F0.wireOp",EDGE,"E2614"),sQuery(id+"F0.wireOp",EDGE,"E2615"),sQuery(id+"F0.wireOp",EDGE,"E2616"),sQuery(id+"F0.wireOp",EDGE,"E2616"),sQuery(id+"F0.wireOp",EDGE,"E2616"),sQuery(id+"F0.wireOp",EDGE,"E2616"),sQuery(id+"F0.wireOp",EDGE,"E2616"),sQuery(id+"F0.wireOp",EDGE,"E2616"),sQuery(id+"F0.wireOp",EDGE,"E2616"),sQuery(id+"F0.wireOp",EDGE,"E2617"),sQuery(id+"F0.wireOp",EDGE,"E2618"),sQuery(id+"F0.wireOp",EDGE,"E2618"),sQuery(id+"F0.wireOp",EDGE,"E2618"),sQuery(id+"F0.wireOp",EDGE,"E2618"),sQuery(id+"F0.wireOp",EDGE,"E2619"),sQuery(id+"F0.wireOp",EDGE,"E2620"),sQuery(id+"F0.wireOp",EDGE,"E2621"),sQuery(id+"F0.wireOp",EDGE,"E2621"),sQuery(id+"F0.wireOp",EDGE,"E2621"),sQuery(id+"F0.wireOp",EDGE,"E2621"),sQuery(id+"F0.wireOp",EDGE,"E2622"),sQuery(id+"F0.wireOp",EDGE,"E2623"),sQuery(id+"F0.wireOp",EDGE,"E2646"),sQuery(id+"F0.wireOp",EDGE,"E2647"),sQuery(id+"F0.wireOp",EDGE,"E2648"),sQuery(id+"F0.wireOp",EDGE,"E2649"),sQuery(id+"F0.wireOp",EDGE,"E2650"),sQuery(id+"F0.wireOp",EDGE,"E2651"),sQuery(id+"F0.wireOp",EDGE,"E2652"),sQuery(id+"F0.wireOp",EDGE,"E2652"),sQuery(id+"F0.wireOp",EDGE,"E2653"),sQuery(id+"F0.wireOp",EDGE,"E2654"),sQuery(id+"F0.wireOp",EDGE,"E2654"),sQuery(id+"F0.wireOp",EDGE,"E2655"),sQuery(id+"F0.wireOp",EDGE,"E2656"),sQuery(id+"F0.wireOp",EDGE,"E2657"),sQuery(id+"F0.wireOp",EDGE,"E2658"),sQuery(id+"F0.wireOp",EDGE,"E2659"),sQuery(id+"F0.wireOp",EDGE,"E2660"),sQuery(id+"F0.wireOp",EDGE,"E2660"),sQuery(id+"F0.wireOp",EDGE,"E2661"),sQuery(id+"F0.wireOp",EDGE,"E2662"),sQuery(id+"F0.wireOp",EDGE,"E2663"),sQuery(id+"F0.wireOp",EDGE,"E2664"),sQuery(id+"F0.wireOp",EDGE,"E2665"),sQuery(id+"F0.wireOp",EDGE,"E2666"),sQuery(id+"F0.wireOp",EDGE,"E2667"),sQuery(id+"F0.wireOp",EDGE,"E2668"),sQuery(id+"F0.wireOp",EDGE,"E2669.bottom"),sQuery(id+"F0.wireOp",EDGE,"E2669.top"),sQuery(id+"F0.wireOp",EDGE,"E2669.left"),sQuery(id+"F0.wireOp",EDGE,"E2669.right")])]});
            var Q4;
            Q4=makeQuery(id+"F1.opExtrude","SWEPT_BODY",BODY,{"disambiguationData":[OSD([sQuery(id+"F0.wireOp",EDGE,"E153"),sQuery(id+"F0.wireOp",EDGE,"E154"),sQuery(id+"F0.wireOp",EDGE,"E155"),sQuery(id+"F0.wireOp",EDGE,"E156"),sQuery(id+"F0.wireOp",EDGE,"E157"),sQuery(id+"F0.wireOp",EDGE,"E158"),sQuery(id+"F0.wireOp",EDGE,"E159"),sQuery(id+"F0.wireOp",EDGE,"E160"),sQuery(id+"F0.wireOp",EDGE,"E161"),sQuery(id+"F0.wireOp",EDGE,"E162"),sQuery(id+"F0.wireOp",EDGE,"E163"),sQuery(id+"F0.wireOp",EDGE,"E164"),sQuery(id+"F0.wireOp",EDGE,"E165"),sQuery(id+"F0.wireOp",EDGE,"E166"),sQuery(id+"F0.wireOp",EDGE,"E167"),sQuery(id+"F0.wireOp",EDGE,"E168"),sQuery(id+"F0.wireOp",EDGE,"E169"),sQuery(id+"F0.wireOp",EDGE,"E170"),sQuery(id+"F0.wireOp",EDGE,"E171"),sQuery(id+"F0.wireOp",EDGE,"E172"),sQuery(id+"F0.wireOp",EDGE,"E173"),sQuery(id+"F0.wireOp",EDGE,"E174"),sQuery(id+"F0.wireOp",EDGE,"E175"),sQuery(id+"F0.wireOp",EDGE,"E176")])]});
            var Q5;
            Q5=makeQuery(id+"F1.opExtrude","SWEPT_BODY",BODY,{"disambiguationData":[OSD([sQuery(id+"F0.wireOp",EDGE,"E440"),sQuery(id+"F0.wireOp",EDGE,"E441"),sQuery(id+"F0.wireOp",EDGE,"E442"),sQuery(id+"F0.wireOp",EDGE,"E443"),sQuery(id+"F0.wireOp",EDGE,"E444"),sQuery(id+"F0.wireOp",EDGE,"E445"),sQuery(id+"F0.wireOp",EDGE,"E446"),sQuery(id+"F0.wireOp",EDGE,"E447"),sQuery(id+"F0.wireOp",EDGE,"E448"),sQuery(id+"F0.wireOp",EDGE,"E449"),sQuery(id+"F0.wireOp",EDGE,"E450"),sQuery(id+"F0.wireOp",EDGE,"E451"),sQuery(id+"F0.wireOp",EDGE,"E452"),sQuery(id+"F0.wireOp",EDGE,"E453"),sQuery(id+"F0.wireOp",EDGE,"E454"),sQuery(id+"F0.wireOp",EDGE,"E455"),sQuery(id+"F0.wireOp",EDGE,"E456"),sQuery(id+"F0.wireOp",EDGE,"E457"),sQuery(id+"F0.wireOp",EDGE,"E458"),sQuery(id+"F0.wireOp",EDGE,"E459"),sQuery(id+"F0.wireOp",EDGE,"E460"),sQuery(id+"F0.wireOp",EDGE,"E461"),sQuery(id+"F0.wireOp",EDGE,"E462"),sQuery(id+"F0.wireOp",EDGE,"E463")])]});
            var Q6;
            Q6=makeQuery(id+"F1.opExtrude","SWEPT_BODY",BODY,{"disambiguationData":[OSD([sQuery(id+"F0.wireOp",EDGE,"E540"),sQuery(id+"F0.wireOp",EDGE,"E541"),sQuery(id+"F0.wireOp",EDGE,"E542"),sQuery(id+"F0.wireOp",EDGE,"E543"),sQuery(id+"F0.wireOp",EDGE,"E544"),sQuery(id+"F0.wireOp",EDGE,"E545"),sQuery(id+"F0.wireOp",EDGE,"E546"),sQuery(id+"F0.wireOp",EDGE,"E547"),sQuery(id+"F0.wireOp",EDGE,"E548"),sQuery(id+"F0.wireOp",EDGE,"E549"),sQuery(id+"F0.wireOp",EDGE,"E550"),sQuery(id+"F0.wireOp",EDGE,"E551"),sQuery(id+"F0.wireOp",EDGE,"E552"),sQuery(id+"F0.wireOp",EDGE,"E553"),sQuery(id+"F0.wireOp",EDGE,"E554"),sQuery(id+"F0.wireOp",EDGE,"E554"),sQuery(id+"F0.wireOp",EDGE,"E555"),sQuery(id+"F0.wireOp",EDGE,"E556"),sQuery(id+"F0.wireOp",EDGE,"E557"),sQuery(id+"F0.wireOp",EDGE,"E558"),sQuery(id+"F0.wireOp",EDGE,"E559"),sQuery(id+"F0.wireOp",EDGE,"E559"),sQuery(id+"F0.wireOp",EDGE,"E560"),sQuery(id+"F0.wireOp",EDGE,"E561")])]});
            var Q7;
            Q7=makeQuery(id+"F1.opExtrude","SWEPT_BODY",BODY,{"disambiguationData":[OSD([sQuery(id+"F0.wireOp",EDGE,"E795"),sQuery(id+"F0.wireOp",EDGE,"E796"),sQuery(id+"F0.wireOp",EDGE,"E797"),sQuery(id+"F0.wireOp",EDGE,"E798"),sQuery(id+"F0.wireOp",EDGE,"E799"),sQuery(id+"F0.wireOp",EDGE,"E800"),sQuery(id+"F0.wireOp",EDGE,"E801"),sQuery(id+"F0.wireOp",EDGE,"E802"),sQuery(id+"F0.wireOp",EDGE,"E803"),sQuery(id+"F0.wireOp",EDGE,"E804"),sQuery(id+"F0.wireOp",EDGE,"E805"),sQuery(id+"F0.wireOp",EDGE,"E806"),sQuery(id+"F0.wireOp",EDGE,"E807"),sQuery(id+"F0.wireOp",EDGE,"E808"),sQuery(id+"F0.wireOp",EDGE,"E809"),sQuery(id+"F0.wireOp",EDGE,"E810"),sQuery(id+"F0.wireOp",EDGE,"E811"),sQuery(id+"F0.wireOp",EDGE,"E811")])]});
            var Q8;
            Q8=makeQuery(id+"F1.opExtrude","SWEPT_BODY",BODY,{"disambiguationData":[OSD([sQuery(id+"F0.wireOp",EDGE,"E1082"),sQuery(id+"F0.wireOp",EDGE,"E1083"),sQuery(id+"F0.wireOp",EDGE,"E1084"),sQuery(id+"F0.wireOp",EDGE,"E1085"),sQuery(id+"F0.wireOp",EDGE,"E1086"),sQuery(id+"F0.wireOp",EDGE,"E1087"),sQuery(id+"F0.wireOp",EDGE,"E1088"),sQuery(id+"F0.wireOp",EDGE,"E1089"),sQuery(id+"F0.wireOp",EDGE,"E1090"),sQuery(id+"F0.wireOp",EDGE,"E1091"),sQuery(id+"F0.wireOp",EDGE,"E1092"),sQuery(id+"F0.wireOp",EDGE,"E1093"),sQuery(id+"F0.wireOp",EDGE,"E1094"),sQuery(id+"F0.wireOp",EDGE,"E1095"),sQuery(id+"F0.wireOp",EDGE,"E1096"),sQuery(id+"F0.wireOp",EDGE,"E1097"),sQuery(id+"F0.wireOp",EDGE,"E1098"),sQuery(id+"F0.wireOp",EDGE,"E1082")])]});
            var Q9;
            Q9=makeQuery(id+"F1.opExtrude","SWEPT_BODY",BODY,{"disambiguationData":[OSD([sQuery(id+"F0.wireOp",EDGE,"E1099"),sQuery(id+"F0.wireOp",EDGE,"E1100"),sQuery(id+"F0.wireOp",EDGE,"E1101"),sQuery(id+"F0.wireOp",EDGE,"E1102"),sQuery(id+"F0.wireOp",EDGE,"E1103"),sQuery(id+"F0.wireOp",EDGE,"E1104"),sQuery(id+"F0.wireOp",EDGE,"E1105"),sQuery(id+"F0.wireOp",EDGE,"E1106"),sQuery(id+"F0.wireOp",EDGE,"E1106"),sQuery(id+"F0.wireOp",EDGE,"E1107"),sQuery(id+"F0.wireOp",EDGE,"E1108"),sQuery(id+"F0.wireOp",EDGE,"E1109"),sQuery(id+"F0.wireOp",EDGE,"E1110"),sQuery(id+"F0.wireOp",EDGE,"E1111"),sQuery(id+"F0.wireOp",EDGE,"E1112"),sQuery(id+"F0.wireOp",EDGE,"E1099")])]});
            var Q10;
            Q10=makeQuery(id+"F1.opExtrude","SWEPT_BODY",BODY,{"disambiguationData":[OSD([sQuery(id+"F0.wireOp",EDGE,"E1432"),sQuery(id+"F0.wireOp",EDGE,"E1432"),sQuery(id+"F0.wireOp",EDGE,"E1432"),sQuery(id+"F0.wireOp",EDGE,"E1432"),sQuery(id+"F0.wireOp",EDGE,"E1432"),sQuery(id+"F0.wireOp",EDGE,"E1432"),sQuery(id+"F0.wireOp",EDGE,"E1433"),sQuery(id+"F0.wireOp",EDGE,"E1434"),sQuery(id+"F0.wireOp",EDGE,"E1435"),sQuery(id+"F0.wireOp",EDGE,"E1435"),sQuery(id+"F0.wireOp",EDGE,"E1436"),sQuery(id+"F0.wireOp",EDGE,"E1437"),sQuery(id+"F0.wireOp",EDGE,"E1437"),sQuery(id+"F0.wireOp",EDGE,"E1438"),sQuery(id+"F0.wireOp",EDGE,"E1439"),sQuery(id+"F0.wireOp",EDGE,"E1440"),sQuery(id+"F0.wireOp",EDGE,"E1441"),sQuery(id+"F0.wireOp",EDGE,"E1441"),sQuery(id+"F0.wireOp",EDGE,"E1442"),sQuery(id+"F0.wireOp",EDGE,"E1432")])]});
            var Q11;
            Q11=makeQuery(id+"F1.opExtrude","SWEPT_BODY",BODY,{"disambiguationData":[OSD([sQuery(id+"F0.wireOp",EDGE,"E1502"),sQuery(id+"F0.wireOp",EDGE,"E1503"),sQuery(id+"F0.wireOp",EDGE,"E1504"),sQuery(id+"F0.wireOp",EDGE,"E1504"),sQuery(id+"F0.wireOp",EDGE,"E1504"),sQuery(id+"F0.wireOp",EDGE,"E1505"),sQuery(id+"F0.wireOp",EDGE,"E1506"),sQuery(id+"F0.wireOp",EDGE,"E1506"),sQuery(id+"F0.wireOp",EDGE,"E1507"),sQuery(id+"F0.wireOp",EDGE,"E1508"),sQuery(id+"F0.wireOp",EDGE,"E1509"),sQuery(id+"F0.wireOp",EDGE,"E1509"),sQuery(id+"F0.wireOp",EDGE,"E1509"),sQuery(id+"F0.wireOp",EDGE,"E1509"),sQuery(id+"F0.wireOp",EDGE,"E1510"),sQuery(id+"F0.wireOp",EDGE,"E1511"),sQuery(id+"F0.wireOp",EDGE,"E1511"),sQuery(id+"F0.wireOp",EDGE,"E1512"),sQuery(id+"F0.wireOp",EDGE,"E1513"),sQuery(id+"F0.wireOp",EDGE,"E1514")])]});
            var Q12;
            Q12=makeQuery(id+"F1.opExtrude","SWEPT_BODY",BODY,{"disambiguationData":[OSD([sQuery(id+"F0.wireOp",EDGE,"E1642"),sQuery(id+"F0.wireOp",EDGE,"E1643"),sQuery(id+"F0.wireOp",EDGE,"E1644"),sQuery(id+"F0.wireOp",EDGE,"E1645"),sQuery(id+"F0.wireOp",EDGE,"E1645"),sQuery(id+"F0.wireOp",EDGE,"E1646"),sQuery(id+"F0.wireOp",EDGE,"E1647"),sQuery(id+"F0.wireOp",EDGE,"E1647"),sQuery(id+"F0.wireOp",EDGE,"E1647"),sQuery(id+"F0.wireOp",EDGE,"E1647"),sQuery(id+"F0.wireOp",EDGE,"E1647"),sQuery(id+"F0.wireOp",EDGE,"E1648"),sQuery(id+"F0.wireOp",EDGE,"E1649"),sQuery(id+"F0.wireOp",EDGE,"E1650"),sQuery(id+"F0.wireOp",EDGE,"E1651"),sQuery(id+"F0.wireOp",EDGE,"E1652"),sQuery(id+"F0.wireOp",EDGE,"E1652"),sQuery(id+"F0.wireOp",EDGE,"E1653"),sQuery(id+"F0.wireOp",EDGE,"E1654"),sQuery(id+"F0.wireOp",EDGE,"E1654")])]});
            var Q13;
            Q13=makeQuery(id+"F1.opExtrude","SWEPT_BODY",BODY,{"disambiguationData":[OSD([sQuery(id+"F0.wireOp",EDGE,"E1771"),sQuery(id+"F0.wireOp",EDGE,"E1772"),sQuery(id+"F0.wireOp",EDGE,"E1773"),sQuery(id+"F0.wireOp",EDGE,"E1773"),sQuery(id+"F0.wireOp",EDGE,"E1773"),sQuery(id+"F0.wireOp",EDGE,"E1773"),sQuery(id+"F0.wireOp",EDGE,"E1773"),sQuery(id+"F0.wireOp",EDGE,"E1773"),sQuery(id+"F0.wireOp",EDGE,"E1774"),sQuery(id+"F0.wireOp",EDGE,"E1775"),sQuery(id+"F0.wireOp",EDGE,"E1775"),sQuery(id+"F0.wireOp",EDGE,"E1776"),sQuery(id+"F0.wireOp",EDGE,"E1777"),sQuery(id+"F0.wireOp",EDGE,"E1777"),sQuery(id+"F0.wireOp",EDGE,"E1778"),sQuery(id+"F0.wireOp",EDGE,"E1779"),sQuery(id+"F0.wireOp",EDGE,"E1779"),sQuery(id+"F0.wireOp",EDGE,"E1780"),sQuery(id+"F0.wireOp",EDGE,"E1781"),sQuery(id+"F0.wireOp",EDGE,"E1782")])]});
            var Q14;
            Q14=makeQuery(id+"F1.opExtrude","SWEPT_BODY",BODY,{"disambiguationData":[OSD([sQuery(id+"F0.wireOp",EDGE,"E1856"),sQuery(id+"F0.wireOp",EDGE,"E1857"),sQuery(id+"F0.wireOp",EDGE,"E1858"),sQuery(id+"F0.wireOp",EDGE,"E1859"),sQuery(id+"F0.wireOp",EDGE,"E1859"),sQuery(id+"F0.wireOp",EDGE,"E1859"),sQuery(id+"F0.wireOp",EDGE,"E1859"),sQuery(id+"F0.wireOp",EDGE,"E1859"),sQuery(id+"F0.wireOp",EDGE,"E1860"),sQuery(id+"F0.wireOp",EDGE,"E1861"),sQuery(id+"F0.wireOp",EDGE,"E1861"),sQuery(id+"F0.wireOp",EDGE,"E1862"),sQuery(id+"F0.wireOp",EDGE,"E1863"),sQuery(id+"F0.wireOp",EDGE,"E1864"),sQuery(id+"F0.wireOp",EDGE,"E1865"),sQuery(id+"F0.wireOp",EDGE,"E1866"),sQuery(id+"F0.wireOp",EDGE,"E1867"),sQuery(id+"F0.wireOp",EDGE,"E1868"),sQuery(id+"F0.wireOp",EDGE,"E1869"),sQuery(id+"F0.wireOp",EDGE,"E1870")])]});
            var Q15;
            Q15=makeQuery(id+"F1.opExtrude","SWEPT_BODY",BODY,{"disambiguationData":[OSD([sQuery(id+"F0.wireOp",EDGE,"E1915"),sQuery(id+"F0.wireOp",EDGE,"E1916"),sQuery(id+"F0.wireOp",EDGE,"E1917"),sQuery(id+"F0.wireOp",EDGE,"E1917"),sQuery(id+"F0.wireOp",EDGE,"E1918"),sQuery(id+"F0.wireOp",EDGE,"E1919"),sQuery(id+"F0.wireOp",EDGE,"E1919"),sQuery(id+"F0.wireOp",EDGE,"E1919"),sQuery(id+"F0.wireOp",EDGE,"E1919"),sQuery(id+"F0.wireOp",EDGE,"E1920"),sQuery(id+"F0.wireOp",EDGE,"E1921"),sQuery(id+"F0.wireOp",EDGE,"E1922"),sQuery(id+"F0.wireOp",EDGE,"E1923"),sQuery(id+"F0.wireOp",EDGE,"E1924"),sQuery(id+"F0.wireOp",EDGE,"E1925"),sQuery(id+"F0.wireOp",EDGE,"E1926"),sQuery(id+"F0.wireOp",EDGE,"E1915"),sQuery(id+"F0.wireOp",EDGE,"E1915"),sQuery(id+"F0.wireOp",EDGE,"E1915"),sQuery(id+"F0.wireOp",EDGE,"E1915")])]});
            var Q16;
            Q16=makeQuery(id+"F1.opExtrude","SWEPT_BODY",BODY,{"disambiguationData":[OSD([sQuery(id+"F0.wireOp",EDGE,"E2217"),sQuery(id+"F0.wireOp",EDGE,"E2218"),sQuery(id+"F0.wireOp",EDGE,"E2219"),sQuery(id+"F0.wireOp",EDGE,"E2219"),sQuery(id+"F0.wireOp",EDGE,"E2220"),sQuery(id+"F0.wireOp",EDGE,"E2221"),sQuery(id+"F0.wireOp",EDGE,"E2221"),sQuery(id+"F0.wireOp",EDGE,"E2222"),sQuery(id+"F0.wireOp",EDGE,"E2223"),sQuery(id+"F0.wireOp",EDGE,"E2223"),sQuery(id+"F0.wireOp",EDGE,"E2224"),sQuery(id+"F0.wireOp",EDGE,"E2225"),sQuery(id+"F0.wireOp",EDGE,"E2225"),sQuery(id+"F0.wireOp",EDGE,"E2226"),sQuery(id+"F0.wireOp",EDGE,"E2227"),sQuery(id+"F0.wireOp",EDGE,"E2228"),sQuery(id+"F0.wireOp",EDGE,"E2229"),sQuery(id+"F0.wireOp",EDGE,"E2217")])]});
            var Q17;
            Q17=makeQuery(id+"F1.opExtrude","SWEPT_BODY",BODY,{"disambiguationData":[OSD([sQuery(id+"F0.wireOp",EDGE,"E2388"),sQuery(id+"F0.wireOp",EDGE,"E2389"),sQuery(id+"F0.wireOp",EDGE,"E2390"),sQuery(id+"F0.wireOp",EDGE,"E2391"),sQuery(id+"F0.wireOp",EDGE,"E2391"),sQuery(id+"F0.wireOp",EDGE,"E2392"),sQuery(id+"F0.wireOp",EDGE,"E2389"),sQuery(id+"F0.wireOp",EDGE,"E2389"),sQuery(id+"F0.wireOp",EDGE,"E2393"),sQuery(id+"F0.wireOp",EDGE,"E2394"),sQuery(id+"F0.wireOp",EDGE,"E2394"),sQuery(id+"F0.wireOp",EDGE,"E2395"),sQuery(id+"F0.wireOp",EDGE,"E2396"),sQuery(id+"F0.wireOp",EDGE,"E2396"),sQuery(id+"F0.wireOp",EDGE,"E2397"),sQuery(id+"F0.wireOp",EDGE,"E2398"),sQuery(id+"F0.wireOp",EDGE,"E2398"),sQuery(id+"F0.wireOp",EDGE,"E2399"),sQuery(id+"F0.wireOp",EDGE,"E2400"),sQuery(id+"F0.wireOp",EDGE,"E2401")])]});
            var Q18;
            Q18=makeQuery(id+"F1.opExtrude","SWEPT_BODY",BODY,{"disambiguationData":[OSD([sQuery(id+"F0.wireOp",EDGE,"E2537"),sQuery(id+"F0.wireOp",EDGE,"E2538"),sQuery(id+"F0.wireOp",EDGE,"E2539"),sQuery(id+"F0.wireOp",EDGE,"E2539"),sQuery(id+"F0.wireOp",EDGE,"E2540"),sQuery(id+"F0.wireOp",EDGE,"E2541"),sQuery(id+"F0.wireOp",EDGE,"E2541"),sQuery(id+"F0.wireOp",EDGE,"E2542"),sQuery(id+"F0.wireOp",EDGE,"E2543"),sQuery(id+"F0.wireOp",EDGE,"E2543"),sQuery(id+"F0.wireOp",EDGE,"E2544"),sQuery(id+"F0.wireOp",EDGE,"E2545"),sQuery(id+"F0.wireOp",EDGE,"E2546"),sQuery(id+"F0.wireOp",EDGE,"E2547"),sQuery(id+"F0.wireOp",EDGE,"E2548"),sQuery(id+"F0.wireOp",EDGE,"E2549"),sQuery(id+"F0.wireOp",EDGE,"E2549"),sQuery(id+"F0.wireOp",EDGE,"E2550"),sQuery(id+"F0.wireOp",EDGE,"E2551"),sQuery(id+"F0.wireOp",EDGE,"E2551"),sQuery(id+"F0.wireOp",EDGE,"E2552"),sQuery(id+"F0.wireOp",EDGE,"E2553"),sQuery(id+"F0.wireOp",EDGE,"E2553"),sQuery(id+"F0.wireOp",EDGE,"E2554"),sQuery(id+"F0.wireOp",EDGE,"E2555"),sQuery(id+"F0.wireOp",EDGE,"E2556")])]});
            var Q19;
            Q19=makeQuery(id+"F1.opExtrude","SWEPT_BODY",BODY,{"disambiguationData":[OSD([sQuery(id+"F0.wireOp",EDGE,"E2624"),sQuery(id+"F0.wireOp",EDGE,"E2625"),sQuery(id+"F0.wireOp",EDGE,"E2626"),sQuery(id+"F0.wireOp",EDGE,"E2626"),sQuery(id+"F0.wireOp",EDGE,"E2627"),sQuery(id+"F0.wireOp",EDGE,"E2628"),sQuery(id+"F0.wireOp",EDGE,"E2628"),sQuery(id+"F0.wireOp",EDGE,"E2629"),sQuery(id+"F0.wireOp",EDGE,"E2630"),sQuery(id+"F0.wireOp",EDGE,"E2631"),sQuery(id+"F0.wireOp",EDGE,"E2632"),sQuery(id+"F0.wireOp",EDGE,"E2633"),sQuery(id+"F0.wireOp",EDGE,"E2634"),sQuery(id+"F0.wireOp",EDGE,"E2635"),sQuery(id+"F0.wireOp",EDGE,"E2636"),sQuery(id+"F0.wireOp",EDGE,"E2637"),sQuery(id+"F0.wireOp",EDGE,"E2638"),sQuery(id+"F0.wireOp",EDGE,"E2639"),sQuery(id+"F0.wireOp",EDGE,"E2640"),sQuery(id+"F0.wireOp",EDGE,"E2640"),sQuery(id+"F0.wireOp",EDGE,"E2641"),sQuery(id+"F0.wireOp",EDGE,"E2642"),sQuery(id+"F0.wireOp",EDGE,"E2642"),sQuery(id+"F0.wireOp",EDGE,"E2643"),sQuery(id+"F0.wireOp",EDGE,"E2644"),sQuery(id+"F0.wireOp",EDGE,"E2645")])]});
            var Q20;
            Q20=makeQuery(id+"F5.opExtrude","SWEPT_BODY",BODY,{"disambiguationData":[OSD([sQuery(id+"F4.wireOp",EDGE,"E2670.bottom"),sQuery(id+"F4.wireOp",EDGE,"E2670.top"),sQuery(id+"F4.wireOp",EDGE,"E2670.left"),sQuery(id+"F4.wireOp",EDGE,"E2670.right")])]});
            booleanBodies(context, id + "F6", {"operationType" : BooleanOperationType.SUBTRACTION, "tools" : qUnion([Q0, Q1, Q2, Q3, Q4, Q5, Q6, Q7, Q8, Q9, Q10, Q11, Q12, Q13, Q14, Q15, Q16, Q17, Q18, Q19]), "targets" : qUnion([Q20])});
        }
        {
            var Q0;
            Q0=makeQuery(id+"F5.opExtrude","SWEPT_EDGE",EDGE,{"disambiguationData":[OSD([sQuery(id+"F4.wireOp",EDGE,"E2670.bottom"),sQuery(id+"F4.wireOp",EDGE,"E2670.left")])]});
            var Q1;
            Q1=makeQuery(id+"F5.opExtrude","SWEPT_EDGE",EDGE,{"disambiguationData":[OSD([sQuery(id+"F4.wireOp",EDGE,"E2670.bottom"),sQuery(id+"F4.wireOp",EDGE,"E2670.right")])]});
            var Q2;
            Q2=makeQuery(id+"F5.opExtrude","SWEPT_EDGE",EDGE,{"disambiguationData":[OSD([sQuery(id+"F4.wireOp",EDGE,"E2670.top"),sQuery(id+"F4.wireOp",EDGE,"E2670.left")])]});
            var Q3;
            Q3=makeQuery(id+"F5.opExtrude","SWEPT_EDGE",EDGE,{"disambiguationData":[OSD([sQuery(id+"F4.wireOp",EDGE,"E2670.top"),sQuery(id+"F4.wireOp",EDGE,"E2670.right")])]});
            fillet(context, id + "F7", {"entities" : qUnion([Q0, Q1, Q2, Q3]), "radius" : 5 * mm, "tangentPropagation" : true, "allowEdgeOverflow" : false});
        }
    });
